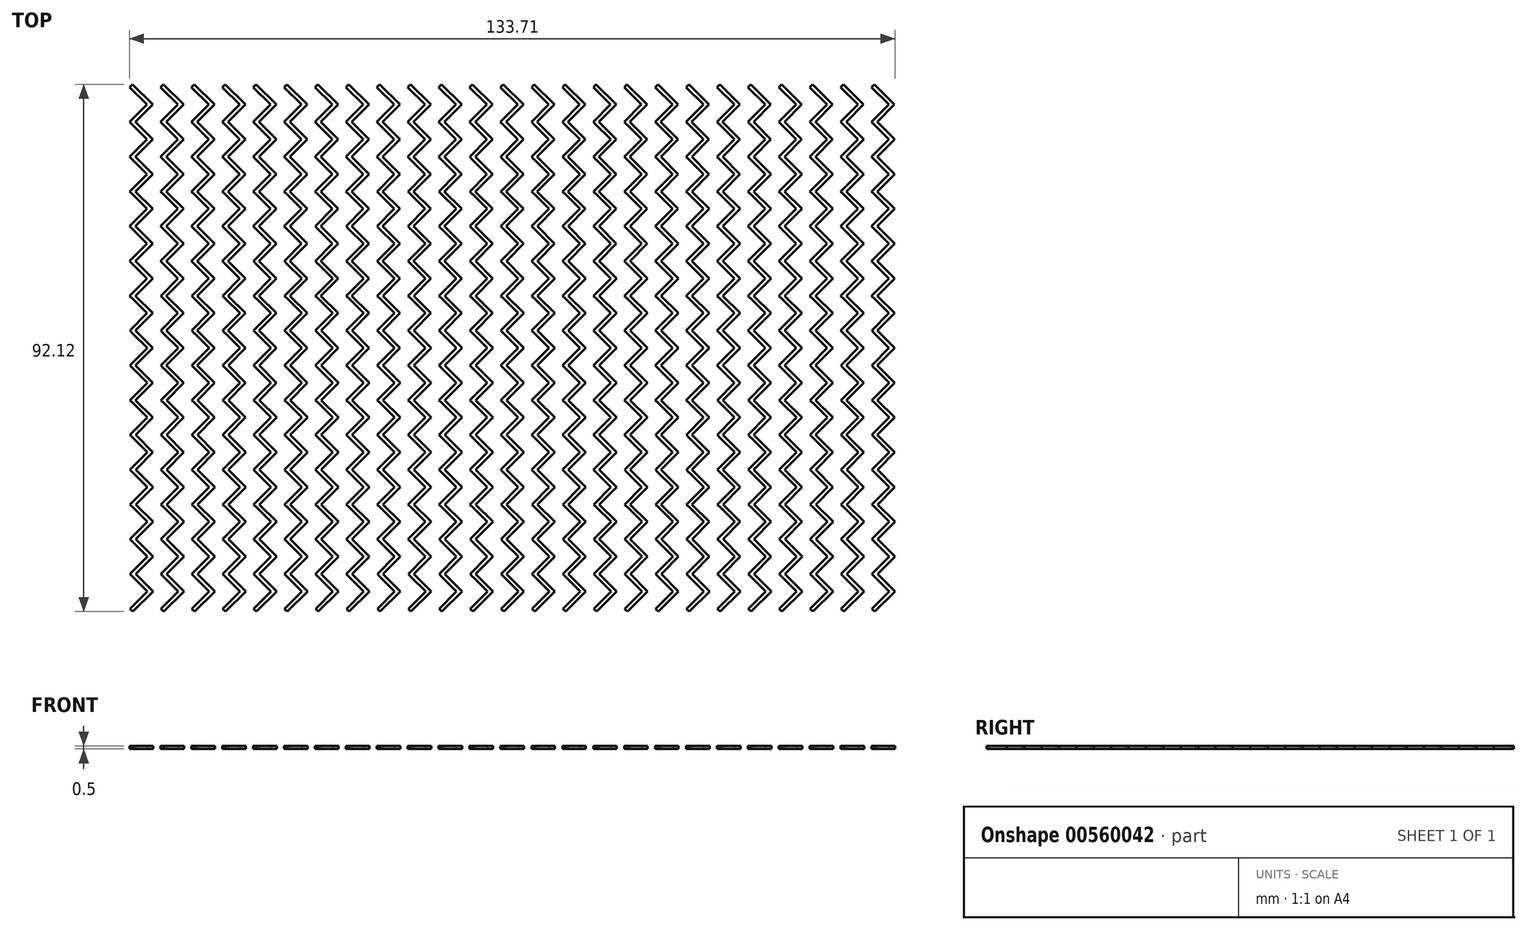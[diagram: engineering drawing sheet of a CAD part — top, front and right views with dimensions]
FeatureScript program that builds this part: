
annotation { "Feature Type Name" : "Feature", "Feature Type Description" : "" }
export const myFeature = defineFeature(function(context is Context, id is Id, definition is map)
    precondition{}
    {
        {
            var Q0;
            Q0=qCreatedBy(makeId("Top.planeOp"),FACE);
            var sketch = newSketch(context, id + "F0", { "sketchPlane" : qUnion([Q0])});
            skLineSegment(sketch, "E0.bottom", {"start": v(-69.05, 44.95) * mm, "end": v(-65.51, 41.41) * mm});
            skLineSegment(sketch, "E0.top", {"start": v(-69.54, 44.45) * mm, "end": v(-66, 40.91) * mm});
            skLineSegment(sketch, "E0.left", {"start": v(-69.05, 44.95) * mm, "end": v(-69.54, 44.45) * mm});
            skLineSegment(sketch, "E0.right", {"start": v(-65.51, 41.41) * mm, "end": v(-66, 40.91) * mm});
            skLineSegment(sketch, "E1.bottom", {"start": v(-65.51, 41.41) * mm, "end": v(-69.05, 37.87) * mm});
            skLineSegment(sketch, "E1.top", {"start": v(-66, 41.9) * mm, "end": v(-69.54, 38.37) * mm});
            skLineSegment(sketch, "E1.left", {"start": v(-65.51, 41.41) * mm, "end": v(-66, 41.9) * mm});
            skLineSegment(sketch, "E1.right", {"start": v(-69.05, 37.87) * mm, "end": v(-69.54, 38.37) * mm});
            skLineSegment(sketch, "E2.1.0.0", {"start": v(-69.54, 38.37) * mm, "end": v(-66, 34.84) * mm});
            skLineSegment(sketch, "E2.1.0.1", {"start": v(-65.5, 35.34) * mm, "end": v(-69.04, 31.8) * mm});
            skLineSegment(sketch, "E2.1.0.2", {"start": v(-66, 35.83) * mm, "end": v(-69.54, 32.3) * mm});
            skLineSegment(sketch, "E2.1.0.3", {"start": v(-69.04, 38.87) * mm, "end": v(-65.5, 35.34) * mm});
            skLineSegment(sketch, "E2.1.0.4", {"start": v(-69.04, 38.87) * mm, "end": v(-69.54, 38.37) * mm});
            skLineSegment(sketch, "E2.1.0.5", {"start": v(-65.5, 35.34) * mm, "end": v(-66, 34.84) * mm});
            skLineSegment(sketch, "E2.1.0.6", {"start": v(-65.5, 35.34) * mm, "end": v(-66, 35.83) * mm});
            skLineSegment(sketch, "E2.1.0.7", {"start": v(-69.04, 31.8) * mm, "end": v(-69.54, 32.3) * mm});
            skLineSegment(sketch, "E2.2.0.0", {"start": v(-69.53, 32.3) * mm, "end": v(-66, 28.76) * mm});
            skLineSegment(sketch, "E2.2.0.1", {"start": v(-65.5, 29.26) * mm, "end": v(-69.03, 25.73) * mm});
            skLineSegment(sketch, "E2.2.0.2", {"start": v(-66, 29.76) * mm, "end": v(-69.53, 26.22) * mm});
            skLineSegment(sketch, "E2.2.0.3", {"start": v(-69.03, 32.8) * mm, "end": v(-65.5, 29.26) * mm});
            skLineSegment(sketch, "E2.2.0.4", {"start": v(-69.03, 32.8) * mm, "end": v(-69.53, 32.3) * mm});
            skLineSegment(sketch, "E2.2.0.5", {"start": v(-65.5, 29.26) * mm, "end": v(-66, 28.76) * mm});
            skLineSegment(sketch, "E2.2.0.6", {"start": v(-65.5, 29.26) * mm, "end": v(-66, 29.76) * mm});
            skLineSegment(sketch, "E2.2.0.7", {"start": v(-69.03, 25.73) * mm, "end": v(-69.53, 26.22) * mm});
            skLineSegment(sketch, "E2.3.0.0", {"start": v(-69.53, 26.22) * mm, "end": v(-66, 22.69) * mm});
            skLineSegment(sketch, "E2.3.0.1", {"start": v(-65.5, 23.19) * mm, "end": v(-69.03, 19.65) * mm});
            skLineSegment(sketch, "E2.3.0.2", {"start": v(-66, 23.68) * mm, "end": v(-69.53, 20.15) * mm});
            skLineSegment(sketch, "E2.3.0.3", {"start": v(-69.03, 26.72) * mm, "end": v(-65.5, 23.19) * mm});
            skLineSegment(sketch, "E2.3.0.4", {"start": v(-69.03, 26.72) * mm, "end": v(-69.53, 26.22) * mm});
            skLineSegment(sketch, "E2.3.0.5", {"start": v(-65.5, 23.19) * mm, "end": v(-66, 22.69) * mm});
            skLineSegment(sketch, "E2.3.0.6", {"start": v(-65.5, 23.19) * mm, "end": v(-66, 23.68) * mm});
            skLineSegment(sketch, "E2.3.0.7", {"start": v(-69.03, 19.65) * mm, "end": v(-69.53, 20.15) * mm});
            skLineSegment(sketch, "E2.4.0.0", {"start": v(-69.52, 20.15) * mm, "end": v(-65.98, 16.61) * mm});
            skLineSegment(sketch, "E2.4.0.1", {"start": v(-65.49, 17.11) * mm, "end": v(-69.02, 13.58) * mm});
            skLineSegment(sketch, "E2.4.0.2", {"start": v(-65.98, 17.6) * mm, "end": v(-69.52, 14.07) * mm});
            skLineSegment(sketch, "E2.4.0.3", {"start": v(-69.02, 20.65) * mm, "end": v(-65.49, 17.11) * mm});
            skLineSegment(sketch, "E2.4.0.4", {"start": v(-69.02, 20.65) * mm, "end": v(-69.52, 20.15) * mm});
            skLineSegment(sketch, "E2.4.0.5", {"start": v(-65.49, 17.11) * mm, "end": v(-65.98, 16.61) * mm});
            skLineSegment(sketch, "E2.4.0.6", {"start": v(-65.49, 17.11) * mm, "end": v(-65.98, 17.6) * mm});
            skLineSegment(sketch, "E2.4.0.7", {"start": v(-69.02, 13.58) * mm, "end": v(-69.52, 14.07) * mm});
            skLineSegment(sketch, "E2.5.0.0", {"start": v(-69.51, 14.07) * mm, "end": v(-65.98, 10.54) * mm});
            skLineSegment(sketch, "E2.5.0.1", {"start": v(-65.48, 11.04) * mm, "end": v(-69.02, 7.5) * mm});
            skLineSegment(sketch, "E2.5.0.2", {"start": v(-65.98, 11.53) * mm, "end": v(-69.51, 8) * mm});
            skLineSegment(sketch, "E2.5.0.3", {"start": v(-69.02, 14.57) * mm, "end": v(-65.48, 11.04) * mm});
            skLineSegment(sketch, "E2.5.0.4", {"start": v(-69.02, 14.57) * mm, "end": v(-69.51, 14.07) * mm});
            skLineSegment(sketch, "E2.5.0.5", {"start": v(-65.48, 11.04) * mm, "end": v(-65.98, 10.54) * mm});
            skLineSegment(sketch, "E2.5.0.6", {"start": v(-65.48, 11.04) * mm, "end": v(-65.98, 11.53) * mm});
            skLineSegment(sketch, "E2.5.0.7", {"start": v(-69.02, 7.5) * mm, "end": v(-69.51, 8) * mm});
            skLineSegment(sketch, "E2.6.0.0", {"start": v(-69.5, 8) * mm, "end": v(-65.97, 4.46) * mm});
            skLineSegment(sketch, "E2.6.0.1", {"start": v(-65.48, 4.96) * mm, "end": v(-69.01, 1.43) * mm});
            skLineSegment(sketch, "E2.6.0.2", {"start": v(-65.97, 5.46) * mm, "end": v(-69.5, 1.92) * mm});
            skLineSegment(sketch, "E2.6.0.3", {"start": v(-69.01, 8.5) * mm, "end": v(-65.48, 4.96) * mm});
            skLineSegment(sketch, "E2.6.0.4", {"start": v(-69.01, 8.5) * mm, "end": v(-69.5, 8) * mm});
            skLineSegment(sketch, "E2.6.0.5", {"start": v(-65.48, 4.96) * mm, "end": v(-65.97, 4.46) * mm});
            skLineSegment(sketch, "E2.6.0.6", {"start": v(-65.48, 4.96) * mm, "end": v(-65.97, 5.46) * mm});
            skLineSegment(sketch, "E2.6.0.7", {"start": v(-69.01, 1.43) * mm, "end": v(-69.5, 1.92) * mm});
            skLineSegment(sketch, "E2.7.0.0", {"start": v(-69.5, 1.92) * mm, "end": v(-65.97, -1.61) * mm});
            skLineSegment(sketch, "E2.7.0.1", {"start": v(-65.47, -1.11) * mm, "end": v(-69, -4.65) * mm});
            skLineSegment(sketch, "E2.7.0.2", {"start": v(-65.97, -0.62) * mm, "end": v(-69.5, -4.15) * mm});
            skLineSegment(sketch, "E2.7.0.3", {"start": v(-69, 2.42) * mm, "end": v(-65.47, -1.11) * mm});
            skLineSegment(sketch, "E2.7.0.4", {"start": v(-69, 2.42) * mm, "end": v(-69.5, 1.92) * mm});
            skLineSegment(sketch, "E2.7.0.5", {"start": v(-65.47, -1.11) * mm, "end": v(-65.97, -1.61) * mm});
            skLineSegment(sketch, "E2.7.0.6", {"start": v(-65.47, -1.11) * mm, "end": v(-65.97, -0.62) * mm});
            skLineSegment(sketch, "E2.7.0.7", {"start": v(-69, -4.65) * mm, "end": v(-69.5, -4.15) * mm});
            skLineSegment(sketch, "E2.8.0.0", {"start": v(-69.5, -4.15) * mm, "end": v(-65.96, -7.69) * mm});
            skLineSegment(sketch, "E2.8.0.1", {"start": v(-65.46, -7.19) * mm, "end": v(-69, -10.72) * mm});
            skLineSegment(sketch, "E2.8.0.2", {"start": v(-65.96, -6.7) * mm, "end": v(-69.5, -10.23) * mm});
            skLineSegment(sketch, "E2.8.0.3", {"start": v(-69, -3.65) * mm, "end": v(-65.46, -7.19) * mm});
            skLineSegment(sketch, "E2.8.0.4", {"start": v(-69, -3.65) * mm, "end": v(-69.5, -4.15) * mm});
            skLineSegment(sketch, "E2.8.0.5", {"start": v(-65.46, -7.19) * mm, "end": v(-65.96, -7.69) * mm});
            skLineSegment(sketch, "E2.8.0.6", {"start": v(-65.46, -7.19) * mm, "end": v(-65.96, -6.7) * mm});
            skLineSegment(sketch, "E2.8.0.7", {"start": v(-69, -10.72) * mm, "end": v(-69.5, -10.23) * mm});
            skLineSegment(sketch, "E2.9.0.0", {"start": v(-69.5, -10.23) * mm, "end": v(-65.96, -13.76) * mm});
            skLineSegment(sketch, "E2.9.0.1", {"start": v(-65.46, -13.26) * mm, "end": v(-69, -16.8) * mm});
            skLineSegment(sketch, "E2.9.0.2", {"start": v(-65.96, -12.77) * mm, "end": v(-69.5, -16.3) * mm});
            skLineSegment(sketch, "E2.9.0.3", {"start": v(-69, -9.73) * mm, "end": v(-65.46, -13.26) * mm});
            skLineSegment(sketch, "E2.9.0.4", {"start": v(-69, -9.73) * mm, "end": v(-69.5, -10.23) * mm});
            skLineSegment(sketch, "E2.9.0.5", {"start": v(-65.46, -13.26) * mm, "end": v(-65.96, -13.76) * mm});
            skLineSegment(sketch, "E2.9.0.6", {"start": v(-65.46, -13.26) * mm, "end": v(-65.96, -12.77) * mm});
            skLineSegment(sketch, "E2.9.0.7", {"start": v(-69, -16.8) * mm, "end": v(-69.5, -16.3) * mm});
            skLineSegment(sketch, "E2.10.0.0", {"start": v(-69.49, -16.3) * mm, "end": v(-65.95, -19.84) * mm});
            skLineSegment(sketch, "E2.10.0.1", {"start": v(-65.45, -19.34) * mm, "end": v(-68.99, -22.87) * mm});
            skLineSegment(sketch, "E2.10.0.2", {"start": v(-65.95, -18.84) * mm, "end": v(-69.49, -22.38) * mm});
            skLineSegment(sketch, "E2.10.0.3", {"start": v(-68.99, -15.8) * mm, "end": v(-65.45, -19.34) * mm});
            skLineSegment(sketch, "E2.10.0.4", {"start": v(-68.99, -15.8) * mm, "end": v(-69.49, -16.3) * mm});
            skLineSegment(sketch, "E2.10.0.5", {"start": v(-65.45, -19.34) * mm, "end": v(-65.95, -19.84) * mm});
            skLineSegment(sketch, "E2.10.0.6", {"start": v(-65.45, -19.34) * mm, "end": v(-65.95, -18.84) * mm});
            skLineSegment(sketch, "E2.10.0.7", {"start": v(-68.99, -22.87) * mm, "end": v(-69.49, -22.38) * mm});
            skLineSegment(sketch, "E2.11.0.0", {"start": v(-69.48, -22.38) * mm, "end": v(-65.94, -25.91) * mm});
            skLineSegment(sketch, "E2.11.0.1", {"start": v(-65.45, -25.41) * mm, "end": v(-68.98, -28.95) * mm});
            skLineSegment(sketch, "E2.11.0.2", {"start": v(-65.94, -24.92) * mm, "end": v(-69.48, -28.45) * mm});
            skLineSegment(sketch, "E2.11.0.3", {"start": v(-68.98, -21.88) * mm, "end": v(-65.45, -25.41) * mm});
            skLineSegment(sketch, "E2.11.0.4", {"start": v(-68.98, -21.88) * mm, "end": v(-69.48, -22.38) * mm});
            skLineSegment(sketch, "E2.11.0.5", {"start": v(-65.45, -25.41) * mm, "end": v(-65.94, -25.91) * mm});
            skLineSegment(sketch, "E2.11.0.6", {"start": v(-65.45, -25.41) * mm, "end": v(-65.94, -24.92) * mm});
            skLineSegment(sketch, "E2.11.0.7", {"start": v(-68.98, -28.95) * mm, "end": v(-69.48, -28.45) * mm});
            skLineSegment(sketch, "E2.12.0.0", {"start": v(-69.47, -28.45) * mm, "end": v(-65.94, -31.99) * mm});
            skLineSegment(sketch, "E2.12.0.1", {"start": v(-65.44, -31.49) * mm, "end": v(-68.98, -35.02) * mm});
            skLineSegment(sketch, "E2.12.0.2", {"start": v(-65.94, -31) * mm, "end": v(-69.47, -34.53) * mm});
            skLineSegment(sketch, "E2.12.0.3", {"start": v(-68.98, -27.95) * mm, "end": v(-65.44, -31.49) * mm});
            skLineSegment(sketch, "E2.12.0.4", {"start": v(-68.98, -27.95) * mm, "end": v(-69.47, -28.45) * mm});
            skLineSegment(sketch, "E2.12.0.5", {"start": v(-65.44, -31.49) * mm, "end": v(-65.94, -31.99) * mm});
            skLineSegment(sketch, "E2.12.0.6", {"start": v(-65.44, -31.49) * mm, "end": v(-65.94, -31) * mm});
            skLineSegment(sketch, "E2.12.0.7", {"start": v(-68.98, -35.02) * mm, "end": v(-69.47, -34.53) * mm});
            skLineSegment(sketch, "E2.13.0.0", {"start": v(-69.47, -34.52) * mm, "end": v(-65.93, -38.06) * mm});
            skLineSegment(sketch, "E2.13.0.1", {"start": v(-65.43, -37.56) * mm, "end": v(-68.97, -41.1) * mm});
            skLineSegment(sketch, "E2.13.0.2", {"start": v(-65.93, -37.07) * mm, "end": v(-69.47, -40.6) * mm});
            skLineSegment(sketch, "E2.13.0.3", {"start": v(-68.97, -34.03) * mm, "end": v(-65.43, -37.56) * mm});
            skLineSegment(sketch, "E2.13.0.4", {"start": v(-68.97, -34.03) * mm, "end": v(-69.47, -34.52) * mm});
            skLineSegment(sketch, "E2.13.0.5", {"start": v(-65.43, -37.56) * mm, "end": v(-65.93, -38.06) * mm});
            skLineSegment(sketch, "E2.13.0.6", {"start": v(-65.43, -37.56) * mm, "end": v(-65.93, -37.07) * mm});
            skLineSegment(sketch, "E2.13.0.7", {"start": v(-68.97, -41.1) * mm, "end": v(-69.47, -40.6) * mm});
            skLineSegment(sketch, "E2.14.0.0", {"start": v(-69.46, -40.6) * mm, "end": v(-65.93, -44.14) * mm});
            skLineSegment(sketch, "E2.14.0.1", {"start": v(-65.43, -43.64) * mm, "end": v(-68.96, -47.17) * mm});
            skLineSegment(sketch, "E2.14.0.2", {"start": v(-65.93, -43.14) * mm, "end": v(-69.46, -46.68) * mm});
            skLineSegment(sketch, "E2.14.0.3", {"start": v(-68.96, -40.1) * mm, "end": v(-65.43, -43.64) * mm});
            skLineSegment(sketch, "E2.14.0.4", {"start": v(-68.96, -40.1) * mm, "end": v(-69.46, -40.6) * mm});
            skLineSegment(sketch, "E2.14.0.5", {"start": v(-65.43, -43.64) * mm, "end": v(-65.93, -44.14) * mm});
            skLineSegment(sketch, "E2.14.0.6", {"start": v(-65.43, -43.64) * mm, "end": v(-65.93, -43.14) * mm});
            skLineSegment(sketch, "E2.14.0.7", {"start": v(-68.96, -47.17) * mm, "end": v(-69.46, -46.68) * mm});
            skLineSegment(sketch, "E2.direction1", {"start": v(-69.05, 37.87) * mm, "end": v(-69.04, 31.8) * mm, "construction": true});
            skLineSegment(sketch, "E3.1.0.0", {"start": v(-63.65, 44.95) * mm, "end": v(-60.11, 41.41) * mm});
            skLineSegment(sketch, "E3.1.0.1", {"start": v(-64.14, 44.45) * mm, "end": v(-60.6, 40.91) * mm});
            skLineSegment(sketch, "E3.1.0.2", {"start": v(-63.65, 44.95) * mm, "end": v(-64.14, 44.45) * mm});
            skLineSegment(sketch, "E3.1.0.3", {"start": v(-60.03, -43.64) * mm, "end": v(-63.56, -47.17) * mm});
            skLineSegment(sketch, "E3.1.0.4", {"start": v(-60.53, -43.14) * mm, "end": v(-64.06, -46.68) * mm});
            skLineSegment(sketch, "E3.1.0.5", {"start": v(-63.56, -47.17) * mm, "end": v(-64.06, -46.68) * mm});
            skLineSegment(sketch, "E3.1.0.6", {"start": v(-63.61, 8.5) * mm, "end": v(-60.08, 4.96) * mm});
            skLineSegment(sketch, "E3.1.0.7", {"start": v(-60.03, -43.64) * mm, "end": v(-60.53, -43.14) * mm});
            skLineSegment(sketch, "E3.1.0.8", {"start": v(-60.08, 11.04) * mm, "end": v(-63.62, 7.5) * mm});
            skLineSegment(sketch, "E3.1.0.9", {"start": v(-60.03, -37.56) * mm, "end": v(-63.57, -41.1) * mm});
            skLineSegment(sketch, "E3.1.0.10", {"start": v(-60.05, -25.41) * mm, "end": v(-63.58, -28.95) * mm});
            skLineSegment(sketch, "E3.1.0.11", {"start": v(-60.58, 11.53) * mm, "end": v(-64.11, 8) * mm});
            skLineSegment(sketch, "E3.1.0.12", {"start": v(-60.6, 23.68) * mm, "end": v(-64.13, 20.15) * mm});
            skLineSegment(sketch, "E3.1.0.13", {"start": v(-63.6, 2.42) * mm, "end": v(-60.07, -1.11) * mm});
            skLineSegment(sketch, "E3.1.0.14", {"start": v(-63.62, 14.57) * mm, "end": v(-60.08, 11.04) * mm});
            skLineSegment(sketch, "E3.1.0.15", {"start": v(-63.63, 26.72) * mm, "end": v(-60.1, 23.19) * mm});
            skLineSegment(sketch, "E3.1.0.16", {"start": v(-63.57, -34.03) * mm, "end": v(-60.03, -37.56) * mm});
            skLineSegment(sketch, "E3.1.0.17", {"start": v(-63.58, -21.88) * mm, "end": v(-60.05, -25.41) * mm});
            skLineSegment(sketch, "E3.1.0.18", {"start": v(-63.6, -9.73) * mm, "end": v(-60.06, -13.26) * mm});
            skLineSegment(sketch, "E3.1.0.19", {"start": v(-60.06, -13.26) * mm, "end": v(-60.56, -13.76) * mm});
            skLineSegment(sketch, "E3.1.0.20", {"start": v(-60.07, -1.11) * mm, "end": v(-60.57, -1.61) * mm});
            skLineSegment(sketch, "E3.1.0.21", {"start": v(-60.08, 11.04) * mm, "end": v(-60.58, 10.54) * mm});
            skLineSegment(sketch, "E3.1.0.22", {"start": v(-60.1, 23.19) * mm, "end": v(-60.6, 22.69) * mm});
            skLineSegment(sketch, "E3.1.0.23", {"start": v(-60.03, -37.56) * mm, "end": v(-60.53, -38.06) * mm});
            skLineSegment(sketch, "E3.1.0.24", {"start": v(-60.05, -25.41) * mm, "end": v(-60.54, -25.91) * mm});
            skLineSegment(sketch, "E3.1.0.25", {"start": v(-60.06, -13.26) * mm, "end": v(-60.56, -12.77) * mm});
            skLineSegment(sketch, "E3.1.0.26", {"start": v(-60.07, -1.11) * mm, "end": v(-60.57, -0.62) * mm});
            skLineSegment(sketch, "E3.1.0.27", {"start": v(-60.08, 11.04) * mm, "end": v(-60.58, 11.53) * mm});
            skLineSegment(sketch, "E3.1.0.28", {"start": v(-60.1, 23.19) * mm, "end": v(-60.6, 23.68) * mm});
            skLineSegment(sketch, "E3.1.0.29", {"start": v(-60.03, -37.56) * mm, "end": v(-60.53, -37.07) * mm});
            skLineSegment(sketch, "E3.1.0.30", {"start": v(-60.05, -25.41) * mm, "end": v(-60.54, -24.92) * mm});
            skLineSegment(sketch, "E3.1.0.31", {"start": v(-63.62, 7.5) * mm, "end": v(-64.11, 8) * mm});
            skLineSegment(sketch, "E3.1.0.32", {"start": v(-60.11, 41.41) * mm, "end": v(-63.65, 37.87) * mm});
            skLineSegment(sketch, "E3.1.0.33", {"start": v(-60.6, 41.9) * mm, "end": v(-64.14, 38.37) * mm});
            skLineSegment(sketch, "E3.1.0.34", {"start": v(-60.11, 41.41) * mm, "end": v(-60.6, 41.9) * mm});
            skLineSegment(sketch, "E3.1.0.35", {"start": v(-64.14, 38.37) * mm, "end": v(-60.6, 34.84) * mm});
            skLineSegment(sketch, "E3.1.0.36", {"start": v(-63.64, 38.87) * mm, "end": v(-60.1, 35.34) * mm});
            skLineSegment(sketch, "E3.1.0.37", {"start": v(-64.06, -40.6) * mm, "end": v(-60.53, -44.14) * mm});
            skLineSegment(sketch, "E3.1.0.38", {"start": v(-64.1, 8) * mm, "end": v(-60.57, 4.46) * mm});
            skLineSegment(sketch, "E3.1.0.39", {"start": v(-60.05, -19.34) * mm, "end": v(-63.59, -22.87) * mm});
            skLineSegment(sketch, "E3.1.0.40", {"start": v(-60.06, -7.19) * mm, "end": v(-63.6, -10.72) * mm});
            skLineSegment(sketch, "E3.1.0.41", {"start": v(-60.08, 4.96) * mm, "end": v(-63.61, 1.43) * mm});
            skLineSegment(sketch, "E3.1.0.42", {"start": v(-60.04, -31.49) * mm, "end": v(-63.58, -35.02) * mm});
            skLineSegment(sketch, "E3.1.0.43", {"start": v(-60.55, -18.84) * mm, "end": v(-64.09, -22.38) * mm});
            skLineSegment(sketch, "E3.1.0.44", {"start": v(-60.56, -6.7) * mm, "end": v(-64.1, -10.23) * mm});
            skLineSegment(sketch, "E3.1.0.45", {"start": v(-60.57, 5.46) * mm, "end": v(-64.1, 1.92) * mm});
            skLineSegment(sketch, "E3.1.0.46", {"start": v(-60.54, -31) * mm, "end": v(-64.07, -34.53) * mm});
            skLineSegment(sketch, "E3.1.0.47", {"start": v(-63.59, -15.8) * mm, "end": v(-60.05, -19.34) * mm});
            skLineSegment(sketch, "E3.1.0.48", {"start": v(-63.6, -3.65) * mm, "end": v(-60.06, -7.19) * mm});
            skLineSegment(sketch, "E3.1.0.49", {"start": v(-63.63, 32.8) * mm, "end": v(-60.1, 29.26) * mm});
            skLineSegment(sketch, "E3.1.0.50", {"start": v(-63.56, -40.1) * mm, "end": v(-60.03, -43.64) * mm});
            skLineSegment(sketch, "E3.1.0.51", {"start": v(-63.58, -27.95) * mm, "end": v(-60.04, -31.49) * mm});
            skLineSegment(sketch, "E3.1.0.52", {"start": v(-63.62, 20.65) * mm, "end": v(-60.09, 17.11) * mm});
            skLineSegment(sketch, "E3.1.0.53", {"start": v(-63.59, -15.8) * mm, "end": v(-64.09, -16.3) * mm});
            skLineSegment(sketch, "E3.1.0.54", {"start": v(-63.6, -3.65) * mm, "end": v(-64.1, -4.15) * mm});
            skLineSegment(sketch, "E3.1.0.55", {"start": v(-63.61, 8.5) * mm, "end": v(-64.1, 8) * mm});
            skLineSegment(sketch, "E3.1.0.56", {"start": v(-63.56, -40.1) * mm, "end": v(-64.06, -40.6) * mm});
            skLineSegment(sketch, "E3.1.0.57", {"start": v(-63.58, -27.95) * mm, "end": v(-64.07, -28.45) * mm});
            skLineSegment(sketch, "E3.1.0.58", {"start": v(-60.03, -43.64) * mm, "end": v(-60.53, -44.14) * mm});
            skLineSegment(sketch, "E3.1.0.59", {"start": v(-60.05, -19.34) * mm, "end": v(-60.55, -18.84) * mm});
            skLineSegment(sketch, "E3.1.0.60", {"start": v(-60.06, -7.19) * mm, "end": v(-60.56, -6.7) * mm});
            skLineSegment(sketch, "E3.1.0.61", {"start": v(-60.08, 4.96) * mm, "end": v(-60.57, 5.46) * mm});
            skLineSegment(sketch, "E3.1.0.62", {"start": v(-60.04, -31.49) * mm, "end": v(-60.54, -31) * mm});
            skLineSegment(sketch, "E3.1.0.63", {"start": v(-63.61, 1.43) * mm, "end": v(-64.1, 1.92) * mm});
            skLineSegment(sketch, "E3.1.0.64", {"start": v(-63.58, -35.02) * mm, "end": v(-64.07, -34.53) * mm});
            skLineSegment(sketch, "E3.1.0.65", {"start": v(-63.59, -22.87) * mm, "end": v(-64.09, -22.38) * mm});
            skLineSegment(sketch, "E3.1.0.66", {"start": v(-63.6, -10.72) * mm, "end": v(-64.1, -10.23) * mm});
            skLineSegment(sketch, "E3.1.0.67", {"start": v(-64.1, 1.92) * mm, "end": v(-60.57, -1.61) * mm});
            skLineSegment(sketch, "E3.1.0.68", {"start": v(-64.11, 14.07) * mm, "end": v(-60.58, 10.54) * mm});
            skLineSegment(sketch, "E3.1.0.69", {"start": v(-64.13, 26.22) * mm, "end": v(-60.6, 22.69) * mm});
            skLineSegment(sketch, "E3.1.0.70", {"start": v(-63.65, 37.87) * mm, "end": v(-63.64, 31.8) * mm, "construction": true});
            skLineSegment(sketch, "E3.1.0.71", {"start": v(-64.07, -34.52) * mm, "end": v(-60.53, -38.06) * mm});
            skLineSegment(sketch, "E3.1.0.72", {"start": v(-64.08, -22.38) * mm, "end": v(-60.54, -25.91) * mm});
            skLineSegment(sketch, "E3.1.0.73", {"start": v(-64.1, -10.23) * mm, "end": v(-60.56, -13.76) * mm});
            skLineSegment(sketch, "E3.1.0.74", {"start": v(-60.07, -1.11) * mm, "end": v(-63.6, -4.65) * mm});
            skLineSegment(sketch, "E3.1.0.75", {"start": v(-60.1, 23.19) * mm, "end": v(-63.63, 19.65) * mm});
            skLineSegment(sketch, "E3.1.0.76", {"start": v(-60.06, -13.26) * mm, "end": v(-63.6, -16.8) * mm});
            skLineSegment(sketch, "E3.1.0.77", {"start": v(-60.57, -0.62) * mm, "end": v(-64.1, -4.15) * mm});
            skLineSegment(sketch, "E3.1.0.78", {"start": v(-60.53, -37.07) * mm, "end": v(-64.07, -40.6) * mm});
            skLineSegment(sketch, "E3.1.0.79", {"start": v(-60.54, -24.92) * mm, "end": v(-64.08, -28.45) * mm});
            skLineSegment(sketch, "E3.1.0.80", {"start": v(-60.56, -12.77) * mm, "end": v(-64.1, -16.3) * mm});
            skLineSegment(sketch, "E3.1.0.81", {"start": v(-63.6, 2.42) * mm, "end": v(-64.1, 1.92) * mm});
            skLineSegment(sketch, "E3.1.0.82", {"start": v(-63.62, 14.57) * mm, "end": v(-64.11, 14.07) * mm});
            skLineSegment(sketch, "E3.1.0.83", {"start": v(-63.63, 26.72) * mm, "end": v(-64.13, 26.22) * mm});
            skLineSegment(sketch, "E3.1.0.84", {"start": v(-63.57, -34.03) * mm, "end": v(-64.07, -34.52) * mm});
            skLineSegment(sketch, "E3.1.0.85", {"start": v(-63.58, -21.88) * mm, "end": v(-64.08, -22.38) * mm});
            skLineSegment(sketch, "E3.1.0.86", {"start": v(-63.6, -9.73) * mm, "end": v(-64.1, -10.23) * mm});
            skLineSegment(sketch, "E3.1.0.87", {"start": v(-63.63, 19.65) * mm, "end": v(-64.13, 20.15) * mm});
            skLineSegment(sketch, "E3.1.0.88", {"start": v(-63.57, -41.1) * mm, "end": v(-64.07, -40.6) * mm});
            skLineSegment(sketch, "E3.1.0.89", {"start": v(-60.1, 35.34) * mm, "end": v(-60.6, 34.84) * mm});
            skLineSegment(sketch, "E3.1.0.90", {"start": v(-60.11, 41.41) * mm, "end": v(-60.6, 40.91) * mm});
            skLineSegment(sketch, "E3.1.0.91", {"start": v(-60.1, 35.34) * mm, "end": v(-63.64, 31.8) * mm});
            skLineSegment(sketch, "E3.1.0.92", {"start": v(-60.6, 35.83) * mm, "end": v(-64.14, 32.3) * mm});
            skLineSegment(sketch, "E3.1.0.93", {"start": v(-63.64, 38.87) * mm, "end": v(-64.14, 38.37) * mm});
            skLineSegment(sketch, "E3.1.0.94", {"start": v(-64.07, -28.45) * mm, "end": v(-60.54, -31.99) * mm});
            skLineSegment(sketch, "E3.1.0.95", {"start": v(-64.13, 32.3) * mm, "end": v(-60.6, 28.76) * mm});
            skLineSegment(sketch, "E3.1.0.96", {"start": v(-64.09, -16.3) * mm, "end": v(-60.55, -19.84) * mm});
            skLineSegment(sketch, "E3.1.0.97", {"start": v(-64.1, -4.15) * mm, "end": v(-60.56, -7.69) * mm});
            skLineSegment(sketch, "E3.1.0.98", {"start": v(-64.12, 20.15) * mm, "end": v(-60.58, 16.61) * mm});
            skLineSegment(sketch, "E3.1.0.99", {"start": v(-60.1, 29.26) * mm, "end": v(-63.63, 25.73) * mm});
            skLineSegment(sketch, "E3.1.0.100", {"start": v(-60.09, 17.11) * mm, "end": v(-63.62, 13.58) * mm});
            skLineSegment(sketch, "E3.1.0.101", {"start": v(-60.6, 29.76) * mm, "end": v(-64.13, 26.22) * mm});
            skLineSegment(sketch, "E3.1.0.102", {"start": v(-60.58, 17.6) * mm, "end": v(-64.12, 14.07) * mm});
            skLineSegment(sketch, "E3.1.0.103", {"start": v(-63.62, 20.65) * mm, "end": v(-64.12, 20.15) * mm});
            skLineSegment(sketch, "E3.1.0.104", {"start": v(-60.05, -19.34) * mm, "end": v(-60.55, -19.84) * mm});
            skLineSegment(sketch, "E3.1.0.105", {"start": v(-60.06, -7.19) * mm, "end": v(-60.56, -7.69) * mm});
            skLineSegment(sketch, "E3.1.0.106", {"start": v(-60.08, 4.96) * mm, "end": v(-60.57, 4.46) * mm});
            skLineSegment(sketch, "E3.1.0.107", {"start": v(-60.04, -31.49) * mm, "end": v(-60.54, -31.99) * mm});
            skLineSegment(sketch, "E3.1.0.108", {"start": v(-60.1, 29.26) * mm, "end": v(-60.6, 29.76) * mm});
            skLineSegment(sketch, "E3.1.0.109", {"start": v(-60.09, 17.11) * mm, "end": v(-60.58, 17.6) * mm});
            skLineSegment(sketch, "E3.1.0.110", {"start": v(-63.62, 13.58) * mm, "end": v(-64.12, 14.07) * mm});
            skLineSegment(sketch, "E3.1.0.111", {"start": v(-63.63, 25.73) * mm, "end": v(-64.13, 26.22) * mm});
            skLineSegment(sketch, "E3.1.0.112", {"start": v(-63.6, -16.8) * mm, "end": v(-64.1, -16.3) * mm});
            skLineSegment(sketch, "E3.1.0.113", {"start": v(-63.6, -4.65) * mm, "end": v(-64.1, -4.15) * mm});
            skLineSegment(sketch, "E3.1.0.114", {"start": v(-63.58, -28.95) * mm, "end": v(-64.08, -28.45) * mm});
            skLineSegment(sketch, "E3.1.0.115", {"start": v(-60.1, 35.34) * mm, "end": v(-60.6, 35.83) * mm});
            skLineSegment(sketch, "E3.1.0.116", {"start": v(-63.64, 31.8) * mm, "end": v(-64.14, 32.3) * mm});
            skLineSegment(sketch, "E3.1.0.117", {"start": v(-63.65, 37.87) * mm, "end": v(-64.14, 38.37) * mm});
            skLineSegment(sketch, "E3.1.0.118", {"start": v(-63.63, 32.8) * mm, "end": v(-64.13, 32.3) * mm});
            skLineSegment(sketch, "E3.1.0.119", {"start": v(-60.1, 29.26) * mm, "end": v(-60.6, 28.76) * mm});
            skLineSegment(sketch, "E3.1.0.120", {"start": v(-60.09, 17.11) * mm, "end": v(-60.58, 16.61) * mm});
            skLineSegment(sketch, "E3.2.0.0", {"start": v(-58.25, 44.95) * mm, "end": v(-54.71, 41.41) * mm});
            skLineSegment(sketch, "E3.2.0.1", {"start": v(-58.74, 44.45) * mm, "end": v(-55.2, 40.91) * mm});
            skLineSegment(sketch, "E3.2.0.2", {"start": v(-58.25, 44.95) * mm, "end": v(-58.74, 44.45) * mm});
            skLineSegment(sketch, "E3.2.0.3", {"start": v(-54.63, -43.64) * mm, "end": v(-58.16, -47.17) * mm});
            skLineSegment(sketch, "E3.2.0.4", {"start": v(-55.13, -43.14) * mm, "end": v(-58.66, -46.68) * mm});
            skLineSegment(sketch, "E3.2.0.5", {"start": v(-58.16, -47.17) * mm, "end": v(-58.66, -46.68) * mm});
            skLineSegment(sketch, "E3.2.0.6", {"start": v(-58.21, 8.5) * mm, "end": v(-54.68, 4.96) * mm});
            skLineSegment(sketch, "E3.2.0.7", {"start": v(-54.63, -43.64) * mm, "end": v(-55.13, -43.14) * mm});
            skLineSegment(sketch, "E3.2.0.8", {"start": v(-54.68, 11.04) * mm, "end": v(-58.22, 7.5) * mm});
            skLineSegment(sketch, "E3.2.0.9", {"start": v(-54.63, -37.56) * mm, "end": v(-58.17, -41.1) * mm});
            skLineSegment(sketch, "E3.2.0.10", {"start": v(-54.65, -25.41) * mm, "end": v(-58.18, -28.95) * mm});
            skLineSegment(sketch, "E3.2.0.11", {"start": v(-55.18, 11.53) * mm, "end": v(-58.71, 8) * mm});
            skLineSegment(sketch, "E3.2.0.12", {"start": v(-55.2, 23.68) * mm, "end": v(-58.73, 20.15) * mm});
            skLineSegment(sketch, "E3.2.0.13", {"start": v(-58.2, 2.42) * mm, "end": v(-54.67, -1.11) * mm});
            skLineSegment(sketch, "E3.2.0.14", {"start": v(-58.22, 14.57) * mm, "end": v(-54.68, 11.04) * mm});
            skLineSegment(sketch, "E3.2.0.15", {"start": v(-58.23, 26.72) * mm, "end": v(-54.7, 23.19) * mm});
            skLineSegment(sketch, "E3.2.0.16", {"start": v(-58.17, -34.03) * mm, "end": v(-54.63, -37.56) * mm});
            skLineSegment(sketch, "E3.2.0.17", {"start": v(-58.18, -21.88) * mm, "end": v(-54.65, -25.41) * mm});
            skLineSegment(sketch, "E3.2.0.18", {"start": v(-58.2, -9.73) * mm, "end": v(-54.66, -13.26) * mm});
            skLineSegment(sketch, "E3.2.0.19", {"start": v(-54.66, -13.26) * mm, "end": v(-55.16, -13.76) * mm});
            skLineSegment(sketch, "E3.2.0.20", {"start": v(-54.67, -1.11) * mm, "end": v(-55.17, -1.61) * mm});
            skLineSegment(sketch, "E3.2.0.21", {"start": v(-54.68, 11.04) * mm, "end": v(-55.18, 10.54) * mm});
            skLineSegment(sketch, "E3.2.0.22", {"start": v(-54.7, 23.19) * mm, "end": v(-55.2, 22.69) * mm});
            skLineSegment(sketch, "E3.2.0.23", {"start": v(-54.63, -37.56) * mm, "end": v(-55.13, -38.06) * mm});
            skLineSegment(sketch, "E3.2.0.24", {"start": v(-54.65, -25.41) * mm, "end": v(-55.14, -25.91) * mm});
            skLineSegment(sketch, "E3.2.0.25", {"start": v(-54.66, -13.26) * mm, "end": v(-55.16, -12.77) * mm});
            skLineSegment(sketch, "E3.2.0.26", {"start": v(-54.67, -1.11) * mm, "end": v(-55.17, -0.62) * mm});
            skLineSegment(sketch, "E3.2.0.27", {"start": v(-54.68, 11.04) * mm, "end": v(-55.18, 11.53) * mm});
            skLineSegment(sketch, "E3.2.0.28", {"start": v(-54.7, 23.19) * mm, "end": v(-55.2, 23.68) * mm});
            skLineSegment(sketch, "E3.2.0.29", {"start": v(-54.63, -37.56) * mm, "end": v(-55.13, -37.07) * mm});
            skLineSegment(sketch, "E3.2.0.30", {"start": v(-54.65, -25.41) * mm, "end": v(-55.14, -24.92) * mm});
            skLineSegment(sketch, "E3.2.0.31", {"start": v(-58.22, 7.5) * mm, "end": v(-58.71, 8) * mm});
            skLineSegment(sketch, "E3.2.0.32", {"start": v(-54.71, 41.41) * mm, "end": v(-58.25, 37.87) * mm});
            skLineSegment(sketch, "E3.2.0.33", {"start": v(-55.2, 41.9) * mm, "end": v(-58.74, 38.37) * mm});
            skLineSegment(sketch, "E3.2.0.34", {"start": v(-54.71, 41.41) * mm, "end": v(-55.2, 41.9) * mm});
            skLineSegment(sketch, "E3.2.0.35", {"start": v(-58.74, 38.37) * mm, "end": v(-55.2, 34.84) * mm});
            skLineSegment(sketch, "E3.2.0.36", {"start": v(-58.24, 38.87) * mm, "end": v(-54.7, 35.34) * mm});
            skLineSegment(sketch, "E3.2.0.37", {"start": v(-58.66, -40.6) * mm, "end": v(-55.13, -44.14) * mm});
            skLineSegment(sketch, "E3.2.0.38", {"start": v(-58.7, 8) * mm, "end": v(-55.17, 4.46) * mm});
            skLineSegment(sketch, "E3.2.0.39", {"start": v(-54.65, -19.34) * mm, "end": v(-58.19, -22.87) * mm});
            skLineSegment(sketch, "E3.2.0.40", {"start": v(-54.66, -7.19) * mm, "end": v(-58.2, -10.72) * mm});
            skLineSegment(sketch, "E3.2.0.41", {"start": v(-54.68, 4.96) * mm, "end": v(-58.21, 1.43) * mm});
            skLineSegment(sketch, "E3.2.0.42", {"start": v(-54.64, -31.49) * mm, "end": v(-58.18, -35.02) * mm});
            skLineSegment(sketch, "E3.2.0.43", {"start": v(-55.15, -18.84) * mm, "end": v(-58.69, -22.38) * mm});
            skLineSegment(sketch, "E3.2.0.44", {"start": v(-55.16, -6.7) * mm, "end": v(-58.7, -10.23) * mm});
            skLineSegment(sketch, "E3.2.0.45", {"start": v(-55.17, 5.46) * mm, "end": v(-58.7, 1.92) * mm});
            skLineSegment(sketch, "E3.2.0.46", {"start": v(-55.14, -31) * mm, "end": v(-58.67, -34.53) * mm});
            skLineSegment(sketch, "E3.2.0.47", {"start": v(-58.19, -15.8) * mm, "end": v(-54.65, -19.34) * mm});
            skLineSegment(sketch, "E3.2.0.48", {"start": v(-58.2, -3.65) * mm, "end": v(-54.66, -7.19) * mm});
            skLineSegment(sketch, "E3.2.0.49", {"start": v(-58.23, 32.8) * mm, "end": v(-54.7, 29.26) * mm});
            skLineSegment(sketch, "E3.2.0.50", {"start": v(-58.16, -40.1) * mm, "end": v(-54.63, -43.64) * mm});
            skLineSegment(sketch, "E3.2.0.51", {"start": v(-58.18, -27.95) * mm, "end": v(-54.64, -31.49) * mm});
            skLineSegment(sketch, "E3.2.0.52", {"start": v(-58.22, 20.65) * mm, "end": v(-54.69, 17.11) * mm});
            skLineSegment(sketch, "E3.2.0.53", {"start": v(-58.19, -15.8) * mm, "end": v(-58.69, -16.3) * mm});
            skLineSegment(sketch, "E3.2.0.54", {"start": v(-58.2, -3.65) * mm, "end": v(-58.7, -4.15) * mm});
            skLineSegment(sketch, "E3.2.0.55", {"start": v(-58.21, 8.5) * mm, "end": v(-58.7, 8) * mm});
            skLineSegment(sketch, "E3.2.0.56", {"start": v(-58.16, -40.1) * mm, "end": v(-58.66, -40.6) * mm});
            skLineSegment(sketch, "E3.2.0.57", {"start": v(-58.18, -27.95) * mm, "end": v(-58.67, -28.45) * mm});
            skLineSegment(sketch, "E3.2.0.58", {"start": v(-54.63, -43.64) * mm, "end": v(-55.13, -44.14) * mm});
            skLineSegment(sketch, "E3.2.0.59", {"start": v(-54.65, -19.34) * mm, "end": v(-55.15, -18.84) * mm});
            skLineSegment(sketch, "E3.2.0.60", {"start": v(-54.66, -7.19) * mm, "end": v(-55.16, -6.7) * mm});
            skLineSegment(sketch, "E3.2.0.61", {"start": v(-54.68, 4.96) * mm, "end": v(-55.17, 5.46) * mm});
            skLineSegment(sketch, "E3.2.0.62", {"start": v(-54.64, -31.49) * mm, "end": v(-55.14, -31) * mm});
            skLineSegment(sketch, "E3.2.0.63", {"start": v(-58.21, 1.43) * mm, "end": v(-58.7, 1.92) * mm});
            skLineSegment(sketch, "E3.2.0.64", {"start": v(-58.18, -35.02) * mm, "end": v(-58.67, -34.53) * mm});
            skLineSegment(sketch, "E3.2.0.65", {"start": v(-58.19, -22.87) * mm, "end": v(-58.69, -22.38) * mm});
            skLineSegment(sketch, "E3.2.0.66", {"start": v(-58.2, -10.72) * mm, "end": v(-58.7, -10.23) * mm});
            skLineSegment(sketch, "E3.2.0.67", {"start": v(-58.7, 1.92) * mm, "end": v(-55.17, -1.61) * mm});
            skLineSegment(sketch, "E3.2.0.68", {"start": v(-58.71, 14.07) * mm, "end": v(-55.18, 10.54) * mm});
            skLineSegment(sketch, "E3.2.0.69", {"start": v(-58.73, 26.22) * mm, "end": v(-55.2, 22.69) * mm});
            skLineSegment(sketch, "E3.2.0.70", {"start": v(-58.25, 37.87) * mm, "end": v(-58.24, 31.8) * mm, "construction": true});
            skLineSegment(sketch, "E3.2.0.71", {"start": v(-58.67, -34.52) * mm, "end": v(-55.13, -38.06) * mm});
            skLineSegment(sketch, "E3.2.0.72", {"start": v(-58.68, -22.38) * mm, "end": v(-55.14, -25.91) * mm});
            skLineSegment(sketch, "E3.2.0.73", {"start": v(-58.7, -10.23) * mm, "end": v(-55.16, -13.76) * mm});
            skLineSegment(sketch, "E3.2.0.74", {"start": v(-54.67, -1.11) * mm, "end": v(-58.2, -4.65) * mm});
            skLineSegment(sketch, "E3.2.0.75", {"start": v(-54.7, 23.19) * mm, "end": v(-58.23, 19.65) * mm});
            skLineSegment(sketch, "E3.2.0.76", {"start": v(-54.66, -13.26) * mm, "end": v(-58.2, -16.8) * mm});
            skLineSegment(sketch, "E3.2.0.77", {"start": v(-55.17, -0.62) * mm, "end": v(-58.7, -4.15) * mm});
            skLineSegment(sketch, "E3.2.0.78", {"start": v(-55.13, -37.07) * mm, "end": v(-58.67, -40.6) * mm});
            skLineSegment(sketch, "E3.2.0.79", {"start": v(-55.14, -24.92) * mm, "end": v(-58.68, -28.45) * mm});
            skLineSegment(sketch, "E3.2.0.80", {"start": v(-55.16, -12.77) * mm, "end": v(-58.7, -16.3) * mm});
            skLineSegment(sketch, "E3.2.0.81", {"start": v(-58.2, 2.42) * mm, "end": v(-58.7, 1.92) * mm});
            skLineSegment(sketch, "E3.2.0.82", {"start": v(-58.22, 14.57) * mm, "end": v(-58.71, 14.07) * mm});
            skLineSegment(sketch, "E3.2.0.83", {"start": v(-58.23, 26.72) * mm, "end": v(-58.73, 26.22) * mm});
            skLineSegment(sketch, "E3.2.0.84", {"start": v(-58.17, -34.03) * mm, "end": v(-58.67, -34.52) * mm});
            skLineSegment(sketch, "E3.2.0.85", {"start": v(-58.18, -21.88) * mm, "end": v(-58.68, -22.38) * mm});
            skLineSegment(sketch, "E3.2.0.86", {"start": v(-58.2, -9.73) * mm, "end": v(-58.7, -10.23) * mm});
            skLineSegment(sketch, "E3.2.0.87", {"start": v(-58.23, 19.65) * mm, "end": v(-58.73, 20.15) * mm});
            skLineSegment(sketch, "E3.2.0.88", {"start": v(-58.17, -41.1) * mm, "end": v(-58.67, -40.6) * mm});
            skLineSegment(sketch, "E3.2.0.89", {"start": v(-54.7, 35.34) * mm, "end": v(-55.2, 34.84) * mm});
            skLineSegment(sketch, "E3.2.0.90", {"start": v(-54.71, 41.41) * mm, "end": v(-55.2, 40.91) * mm});
            skLineSegment(sketch, "E3.2.0.91", {"start": v(-54.7, 35.34) * mm, "end": v(-58.24, 31.8) * mm});
            skLineSegment(sketch, "E3.2.0.92", {"start": v(-55.2, 35.83) * mm, "end": v(-58.74, 32.3) * mm});
            skLineSegment(sketch, "E3.2.0.93", {"start": v(-58.24, 38.87) * mm, "end": v(-58.74, 38.37) * mm});
            skLineSegment(sketch, "E3.2.0.94", {"start": v(-58.67, -28.45) * mm, "end": v(-55.14, -31.99) * mm});
            skLineSegment(sketch, "E3.2.0.95", {"start": v(-58.73, 32.3) * mm, "end": v(-55.2, 28.76) * mm});
            skLineSegment(sketch, "E3.2.0.96", {"start": v(-58.69, -16.3) * mm, "end": v(-55.15, -19.84) * mm});
            skLineSegment(sketch, "E3.2.0.97", {"start": v(-58.7, -4.15) * mm, "end": v(-55.16, -7.69) * mm});
            skLineSegment(sketch, "E3.2.0.98", {"start": v(-58.72, 20.15) * mm, "end": v(-55.18, 16.61) * mm});
            skLineSegment(sketch, "E3.2.0.99", {"start": v(-54.7, 29.26) * mm, "end": v(-58.23, 25.73) * mm});
            skLineSegment(sketch, "E3.2.0.100", {"start": v(-54.69, 17.11) * mm, "end": v(-58.22, 13.58) * mm});
            skLineSegment(sketch, "E3.2.0.101", {"start": v(-55.2, 29.76) * mm, "end": v(-58.73, 26.22) * mm});
            skLineSegment(sketch, "E3.2.0.102", {"start": v(-55.18, 17.6) * mm, "end": v(-58.72, 14.07) * mm});
            skLineSegment(sketch, "E3.2.0.103", {"start": v(-58.22, 20.65) * mm, "end": v(-58.72, 20.15) * mm});
            skLineSegment(sketch, "E3.2.0.104", {"start": v(-54.65, -19.34) * mm, "end": v(-55.15, -19.84) * mm});
            skLineSegment(sketch, "E3.2.0.105", {"start": v(-54.66, -7.19) * mm, "end": v(-55.16, -7.69) * mm});
            skLineSegment(sketch, "E3.2.0.106", {"start": v(-54.68, 4.96) * mm, "end": v(-55.17, 4.46) * mm});
            skLineSegment(sketch, "E3.2.0.107", {"start": v(-54.64, -31.49) * mm, "end": v(-55.14, -31.99) * mm});
            skLineSegment(sketch, "E3.2.0.108", {"start": v(-54.7, 29.26) * mm, "end": v(-55.2, 29.76) * mm});
            skLineSegment(sketch, "E3.2.0.109", {"start": v(-54.69, 17.11) * mm, "end": v(-55.18, 17.6) * mm});
            skLineSegment(sketch, "E3.2.0.110", {"start": v(-58.22, 13.58) * mm, "end": v(-58.72, 14.07) * mm});
            skLineSegment(sketch, "E3.2.0.111", {"start": v(-58.23, 25.73) * mm, "end": v(-58.73, 26.22) * mm});
            skLineSegment(sketch, "E3.2.0.112", {"start": v(-58.2, -16.8) * mm, "end": v(-58.7, -16.3) * mm});
            skLineSegment(sketch, "E3.2.0.113", {"start": v(-58.2, -4.65) * mm, "end": v(-58.7, -4.15) * mm});
            skLineSegment(sketch, "E3.2.0.114", {"start": v(-58.18, -28.95) * mm, "end": v(-58.68, -28.45) * mm});
            skLineSegment(sketch, "E3.2.0.115", {"start": v(-54.7, 35.34) * mm, "end": v(-55.2, 35.83) * mm});
            skLineSegment(sketch, "E3.2.0.116", {"start": v(-58.24, 31.8) * mm, "end": v(-58.74, 32.3) * mm});
            skLineSegment(sketch, "E3.2.0.117", {"start": v(-58.25, 37.87) * mm, "end": v(-58.74, 38.37) * mm});
            skLineSegment(sketch, "E3.2.0.118", {"start": v(-58.23, 32.8) * mm, "end": v(-58.73, 32.3) * mm});
            skLineSegment(sketch, "E3.2.0.119", {"start": v(-54.7, 29.26) * mm, "end": v(-55.2, 28.76) * mm});
            skLineSegment(sketch, "E3.2.0.120", {"start": v(-54.69, 17.11) * mm, "end": v(-55.18, 16.61) * mm});
            skLineSegment(sketch, "E3.3.0.0", {"start": v(-52.85, 44.95) * mm, "end": v(-49.31, 41.41) * mm});
            skLineSegment(sketch, "E3.3.0.1", {"start": v(-53.34, 44.45) * mm, "end": v(-49.8, 40.91) * mm});
            skLineSegment(sketch, "E3.3.0.2", {"start": v(-52.85, 44.95) * mm, "end": v(-53.34, 44.45) * mm});
            skLineSegment(sketch, "E3.3.0.3", {"start": v(-49.23, -43.64) * mm, "end": v(-52.76, -47.17) * mm});
            skLineSegment(sketch, "E3.3.0.4", {"start": v(-49.73, -43.14) * mm, "end": v(-53.26, -46.68) * mm});
            skLineSegment(sketch, "E3.3.0.5", {"start": v(-52.76, -47.17) * mm, "end": v(-53.26, -46.68) * mm});
            skLineSegment(sketch, "E3.3.0.6", {"start": v(-52.81, 8.5) * mm, "end": v(-49.28, 4.96) * mm});
            skLineSegment(sketch, "E3.3.0.7", {"start": v(-49.23, -43.64) * mm, "end": v(-49.73, -43.14) * mm});
            skLineSegment(sketch, "E3.3.0.8", {"start": v(-49.28, 11.04) * mm, "end": v(-52.82, 7.5) * mm});
            skLineSegment(sketch, "E3.3.0.9", {"start": v(-49.23, -37.56) * mm, "end": v(-52.77, -41.1) * mm});
            skLineSegment(sketch, "E3.3.0.10", {"start": v(-49.25, -25.41) * mm, "end": v(-52.78, -28.95) * mm});
            skLineSegment(sketch, "E3.3.0.11", {"start": v(-49.78, 11.53) * mm, "end": v(-53.31, 8) * mm});
            skLineSegment(sketch, "E3.3.0.12", {"start": v(-49.8, 23.68) * mm, "end": v(-53.33, 20.15) * mm});
            skLineSegment(sketch, "E3.3.0.13", {"start": v(-52.8, 2.42) * mm, "end": v(-49.27, -1.11) * mm});
            skLineSegment(sketch, "E3.3.0.14", {"start": v(-52.82, 14.57) * mm, "end": v(-49.28, 11.04) * mm});
            skLineSegment(sketch, "E3.3.0.15", {"start": v(-52.83, 26.72) * mm, "end": v(-49.3, 23.19) * mm});
            skLineSegment(sketch, "E3.3.0.16", {"start": v(-52.77, -34.03) * mm, "end": v(-49.23, -37.56) * mm});
            skLineSegment(sketch, "E3.3.0.17", {"start": v(-52.78, -21.88) * mm, "end": v(-49.25, -25.41) * mm});
            skLineSegment(sketch, "E3.3.0.18", {"start": v(-52.8, -9.73) * mm, "end": v(-49.26, -13.26) * mm});
            skLineSegment(sketch, "E3.3.0.19", {"start": v(-49.26, -13.26) * mm, "end": v(-49.76, -13.76) * mm});
            skLineSegment(sketch, "E3.3.0.20", {"start": v(-49.27, -1.11) * mm, "end": v(-49.77, -1.61) * mm});
            skLineSegment(sketch, "E3.3.0.21", {"start": v(-49.28, 11.04) * mm, "end": v(-49.78, 10.54) * mm});
            skLineSegment(sketch, "E3.3.0.22", {"start": v(-49.3, 23.19) * mm, "end": v(-49.8, 22.69) * mm});
            skLineSegment(sketch, "E3.3.0.23", {"start": v(-49.23, -37.56) * mm, "end": v(-49.73, -38.06) * mm});
            skLineSegment(sketch, "E3.3.0.24", {"start": v(-49.25, -25.41) * mm, "end": v(-49.74, -25.91) * mm});
            skLineSegment(sketch, "E3.3.0.25", {"start": v(-49.26, -13.26) * mm, "end": v(-49.76, -12.77) * mm});
            skLineSegment(sketch, "E3.3.0.26", {"start": v(-49.27, -1.11) * mm, "end": v(-49.77, -0.62) * mm});
            skLineSegment(sketch, "E3.3.0.27", {"start": v(-49.28, 11.04) * mm, "end": v(-49.78, 11.53) * mm});
            skLineSegment(sketch, "E3.3.0.28", {"start": v(-49.3, 23.19) * mm, "end": v(-49.8, 23.68) * mm});
            skLineSegment(sketch, "E3.3.0.29", {"start": v(-49.23, -37.56) * mm, "end": v(-49.73, -37.07) * mm});
            skLineSegment(sketch, "E3.3.0.30", {"start": v(-49.25, -25.41) * mm, "end": v(-49.74, -24.92) * mm});
            skLineSegment(sketch, "E3.3.0.31", {"start": v(-52.82, 7.5) * mm, "end": v(-53.31, 8) * mm});
            skLineSegment(sketch, "E3.3.0.32", {"start": v(-49.31, 41.41) * mm, "end": v(-52.85, 37.87) * mm});
            skLineSegment(sketch, "E3.3.0.33", {"start": v(-49.8, 41.9) * mm, "end": v(-53.34, 38.37) * mm});
            skLineSegment(sketch, "E3.3.0.34", {"start": v(-49.31, 41.41) * mm, "end": v(-49.8, 41.9) * mm});
            skLineSegment(sketch, "E3.3.0.35", {"start": v(-53.34, 38.37) * mm, "end": v(-49.8, 34.84) * mm});
            skLineSegment(sketch, "E3.3.0.36", {"start": v(-52.84, 38.87) * mm, "end": v(-49.3, 35.34) * mm});
            skLineSegment(sketch, "E3.3.0.37", {"start": v(-53.26, -40.6) * mm, "end": v(-49.73, -44.14) * mm});
            skLineSegment(sketch, "E3.3.0.38", {"start": v(-53.3, 8) * mm, "end": v(-49.77, 4.46) * mm});
            skLineSegment(sketch, "E3.3.0.39", {"start": v(-49.25, -19.34) * mm, "end": v(-52.79, -22.87) * mm});
            skLineSegment(sketch, "E3.3.0.40", {"start": v(-49.26, -7.19) * mm, "end": v(-52.8, -10.72) * mm});
            skLineSegment(sketch, "E3.3.0.41", {"start": v(-49.28, 4.96) * mm, "end": v(-52.81, 1.43) * mm});
            skLineSegment(sketch, "E3.3.0.42", {"start": v(-49.24, -31.49) * mm, "end": v(-52.78, -35.02) * mm});
            skLineSegment(sketch, "E3.3.0.43", {"start": v(-49.75, -18.84) * mm, "end": v(-53.29, -22.38) * mm});
            skLineSegment(sketch, "E3.3.0.44", {"start": v(-49.76, -6.7) * mm, "end": v(-53.3, -10.23) * mm});
            skLineSegment(sketch, "E3.3.0.45", {"start": v(-49.77, 5.46) * mm, "end": v(-53.3, 1.92) * mm});
            skLineSegment(sketch, "E3.3.0.46", {"start": v(-49.74, -31) * mm, "end": v(-53.27, -34.53) * mm});
            skLineSegment(sketch, "E3.3.0.47", {"start": v(-52.79, -15.8) * mm, "end": v(-49.25, -19.34) * mm});
            skLineSegment(sketch, "E3.3.0.48", {"start": v(-52.8, -3.65) * mm, "end": v(-49.26, -7.19) * mm});
            skLineSegment(sketch, "E3.3.0.49", {"start": v(-52.83, 32.8) * mm, "end": v(-49.3, 29.26) * mm});
            skLineSegment(sketch, "E3.3.0.50", {"start": v(-52.76, -40.1) * mm, "end": v(-49.23, -43.64) * mm});
            skLineSegment(sketch, "E3.3.0.51", {"start": v(-52.78, -27.95) * mm, "end": v(-49.24, -31.49) * mm});
            skLineSegment(sketch, "E3.3.0.52", {"start": v(-52.82, 20.65) * mm, "end": v(-49.29, 17.11) * mm});
            skLineSegment(sketch, "E3.3.0.53", {"start": v(-52.79, -15.8) * mm, "end": v(-53.29, -16.3) * mm});
            skLineSegment(sketch, "E3.3.0.54", {"start": v(-52.8, -3.65) * mm, "end": v(-53.3, -4.15) * mm});
            skLineSegment(sketch, "E3.3.0.55", {"start": v(-52.81, 8.5) * mm, "end": v(-53.3, 8) * mm});
            skLineSegment(sketch, "E3.3.0.56", {"start": v(-52.76, -40.1) * mm, "end": v(-53.26, -40.6) * mm});
            skLineSegment(sketch, "E3.3.0.57", {"start": v(-52.78, -27.95) * mm, "end": v(-53.27, -28.45) * mm});
            skLineSegment(sketch, "E3.3.0.58", {"start": v(-49.23, -43.64) * mm, "end": v(-49.73, -44.14) * mm});
            skLineSegment(sketch, "E3.3.0.59", {"start": v(-49.25, -19.34) * mm, "end": v(-49.75, -18.84) * mm});
            skLineSegment(sketch, "E3.3.0.60", {"start": v(-49.26, -7.19) * mm, "end": v(-49.76, -6.7) * mm});
            skLineSegment(sketch, "E3.3.0.61", {"start": v(-49.28, 4.96) * mm, "end": v(-49.77, 5.46) * mm});
            skLineSegment(sketch, "E3.3.0.62", {"start": v(-49.24, -31.49) * mm, "end": v(-49.74, -31) * mm});
            skLineSegment(sketch, "E3.3.0.63", {"start": v(-52.81, 1.43) * mm, "end": v(-53.3, 1.92) * mm});
            skLineSegment(sketch, "E3.3.0.64", {"start": v(-52.78, -35.02) * mm, "end": v(-53.27, -34.53) * mm});
            skLineSegment(sketch, "E3.3.0.65", {"start": v(-52.79, -22.87) * mm, "end": v(-53.29, -22.38) * mm});
            skLineSegment(sketch, "E3.3.0.66", {"start": v(-52.8, -10.72) * mm, "end": v(-53.3, -10.23) * mm});
            skLineSegment(sketch, "E3.3.0.67", {"start": v(-53.3, 1.92) * mm, "end": v(-49.77, -1.61) * mm});
            skLineSegment(sketch, "E3.3.0.68", {"start": v(-53.31, 14.07) * mm, "end": v(-49.78, 10.54) * mm});
            skLineSegment(sketch, "E3.3.0.69", {"start": v(-53.33, 26.22) * mm, "end": v(-49.8, 22.69) * mm});
            skLineSegment(sketch, "E3.3.0.70", {"start": v(-52.85, 37.87) * mm, "end": v(-52.84, 31.8) * mm, "construction": true});
            skLineSegment(sketch, "E3.3.0.71", {"start": v(-53.27, -34.52) * mm, "end": v(-49.73, -38.06) * mm});
            skLineSegment(sketch, "E3.3.0.72", {"start": v(-53.28, -22.38) * mm, "end": v(-49.74, -25.91) * mm});
            skLineSegment(sketch, "E3.3.0.73", {"start": v(-53.3, -10.23) * mm, "end": v(-49.76, -13.76) * mm});
            skLineSegment(sketch, "E3.3.0.74", {"start": v(-49.27, -1.11) * mm, "end": v(-52.8, -4.65) * mm});
            skLineSegment(sketch, "E3.3.0.75", {"start": v(-49.3, 23.19) * mm, "end": v(-52.83, 19.65) * mm});
            skLineSegment(sketch, "E3.3.0.76", {"start": v(-49.26, -13.26) * mm, "end": v(-52.8, -16.8) * mm});
            skLineSegment(sketch, "E3.3.0.77", {"start": v(-49.77, -0.62) * mm, "end": v(-53.3, -4.15) * mm});
            skLineSegment(sketch, "E3.3.0.78", {"start": v(-49.73, -37.07) * mm, "end": v(-53.27, -40.6) * mm});
            skLineSegment(sketch, "E3.3.0.79", {"start": v(-49.74, -24.92) * mm, "end": v(-53.28, -28.45) * mm});
            skLineSegment(sketch, "E3.3.0.80", {"start": v(-49.76, -12.77) * mm, "end": v(-53.3, -16.3) * mm});
            skLineSegment(sketch, "E3.3.0.81", {"start": v(-52.8, 2.42) * mm, "end": v(-53.3, 1.92) * mm});
            skLineSegment(sketch, "E3.3.0.82", {"start": v(-52.82, 14.57) * mm, "end": v(-53.31, 14.07) * mm});
            skLineSegment(sketch, "E3.3.0.83", {"start": v(-52.83, 26.72) * mm, "end": v(-53.33, 26.22) * mm});
            skLineSegment(sketch, "E3.3.0.84", {"start": v(-52.77, -34.03) * mm, "end": v(-53.27, -34.52) * mm});
            skLineSegment(sketch, "E3.3.0.85", {"start": v(-52.78, -21.88) * mm, "end": v(-53.28, -22.38) * mm});
            skLineSegment(sketch, "E3.3.0.86", {"start": v(-52.8, -9.73) * mm, "end": v(-53.3, -10.23) * mm});
            skLineSegment(sketch, "E3.3.0.87", {"start": v(-52.83, 19.65) * mm, "end": v(-53.33, 20.15) * mm});
            skLineSegment(sketch, "E3.3.0.88", {"start": v(-52.77, -41.1) * mm, "end": v(-53.27, -40.6) * mm});
            skLineSegment(sketch, "E3.3.0.89", {"start": v(-49.3, 35.34) * mm, "end": v(-49.8, 34.84) * mm});
            skLineSegment(sketch, "E3.3.0.90", {"start": v(-49.31, 41.41) * mm, "end": v(-49.8, 40.91) * mm});
            skLineSegment(sketch, "E3.3.0.91", {"start": v(-49.3, 35.34) * mm, "end": v(-52.84, 31.8) * mm});
            skLineSegment(sketch, "E3.3.0.92", {"start": v(-49.8, 35.83) * mm, "end": v(-53.34, 32.3) * mm});
            skLineSegment(sketch, "E3.3.0.93", {"start": v(-52.84, 38.87) * mm, "end": v(-53.34, 38.37) * mm});
            skLineSegment(sketch, "E3.3.0.94", {"start": v(-53.27, -28.45) * mm, "end": v(-49.74, -31.99) * mm});
            skLineSegment(sketch, "E3.3.0.95", {"start": v(-53.33, 32.3) * mm, "end": v(-49.8, 28.76) * mm});
            skLineSegment(sketch, "E3.3.0.96", {"start": v(-53.29, -16.3) * mm, "end": v(-49.75, -19.84) * mm});
            skLineSegment(sketch, "E3.3.0.97", {"start": v(-53.3, -4.15) * mm, "end": v(-49.76, -7.69) * mm});
            skLineSegment(sketch, "E3.3.0.98", {"start": v(-53.32, 20.15) * mm, "end": v(-49.78, 16.61) * mm});
            skLineSegment(sketch, "E3.3.0.99", {"start": v(-49.3, 29.26) * mm, "end": v(-52.83, 25.73) * mm});
            skLineSegment(sketch, "E3.3.0.100", {"start": v(-49.29, 17.11) * mm, "end": v(-52.82, 13.58) * mm});
            skLineSegment(sketch, "E3.3.0.101", {"start": v(-49.8, 29.76) * mm, "end": v(-53.33, 26.22) * mm});
            skLineSegment(sketch, "E3.3.0.102", {"start": v(-49.78, 17.6) * mm, "end": v(-53.32, 14.07) * mm});
            skLineSegment(sketch, "E3.3.0.103", {"start": v(-52.82, 20.65) * mm, "end": v(-53.32, 20.15) * mm});
            skLineSegment(sketch, "E3.3.0.104", {"start": v(-49.25, -19.34) * mm, "end": v(-49.75, -19.84) * mm});
            skLineSegment(sketch, "E3.3.0.105", {"start": v(-49.26, -7.19) * mm, "end": v(-49.76, -7.69) * mm});
            skLineSegment(sketch, "E3.3.0.106", {"start": v(-49.28, 4.96) * mm, "end": v(-49.77, 4.46) * mm});
            skLineSegment(sketch, "E3.3.0.107", {"start": v(-49.24, -31.49) * mm, "end": v(-49.74, -31.99) * mm});
            skLineSegment(sketch, "E3.3.0.108", {"start": v(-49.3, 29.26) * mm, "end": v(-49.8, 29.76) * mm});
            skLineSegment(sketch, "E3.3.0.109", {"start": v(-49.29, 17.11) * mm, "end": v(-49.78, 17.6) * mm});
            skLineSegment(sketch, "E3.3.0.110", {"start": v(-52.82, 13.58) * mm, "end": v(-53.32, 14.07) * mm});
            skLineSegment(sketch, "E3.3.0.111", {"start": v(-52.83, 25.73) * mm, "end": v(-53.33, 26.22) * mm});
            skLineSegment(sketch, "E3.3.0.112", {"start": v(-52.8, -16.8) * mm, "end": v(-53.3, -16.3) * mm});
            skLineSegment(sketch, "E3.3.0.113", {"start": v(-52.8, -4.65) * mm, "end": v(-53.3, -4.15) * mm});
            skLineSegment(sketch, "E3.3.0.114", {"start": v(-52.78, -28.95) * mm, "end": v(-53.28, -28.45) * mm});
            skLineSegment(sketch, "E3.3.0.115", {"start": v(-49.3, 35.34) * mm, "end": v(-49.8, 35.83) * mm});
            skLineSegment(sketch, "E3.3.0.116", {"start": v(-52.84, 31.8) * mm, "end": v(-53.34, 32.3) * mm});
            skLineSegment(sketch, "E3.3.0.117", {"start": v(-52.85, 37.87) * mm, "end": v(-53.34, 38.37) * mm});
            skLineSegment(sketch, "E3.3.0.118", {"start": v(-52.83, 32.8) * mm, "end": v(-53.33, 32.3) * mm});
            skLineSegment(sketch, "E3.3.0.119", {"start": v(-49.3, 29.26) * mm, "end": v(-49.8, 28.76) * mm});
            skLineSegment(sketch, "E3.3.0.120", {"start": v(-49.29, 17.11) * mm, "end": v(-49.78, 16.61) * mm});
            skLineSegment(sketch, "E3.4.0.0", {"start": v(-47.45, 44.95) * mm, "end": v(-43.91, 41.41) * mm});
            skLineSegment(sketch, "E3.4.0.1", {"start": v(-47.94, 44.45) * mm, "end": v(-44.4, 40.91) * mm});
            skLineSegment(sketch, "E3.4.0.2", {"start": v(-47.45, 44.95) * mm, "end": v(-47.94, 44.45) * mm});
            skLineSegment(sketch, "E3.4.0.3", {"start": v(-43.83, -43.64) * mm, "end": v(-47.36, -47.17) * mm});
            skLineSegment(sketch, "E3.4.0.4", {"start": v(-44.33, -43.14) * mm, "end": v(-47.86, -46.68) * mm});
            skLineSegment(sketch, "E3.4.0.5", {"start": v(-47.36, -47.17) * mm, "end": v(-47.86, -46.68) * mm});
            skLineSegment(sketch, "E3.4.0.6", {"start": v(-47.41, 8.5) * mm, "end": v(-43.88, 4.96) * mm});
            skLineSegment(sketch, "E3.4.0.7", {"start": v(-43.83, -43.64) * mm, "end": v(-44.33, -43.14) * mm});
            skLineSegment(sketch, "E3.4.0.8", {"start": v(-43.88, 11.04) * mm, "end": v(-47.42, 7.5) * mm});
            skLineSegment(sketch, "E3.4.0.9", {"start": v(-43.83, -37.56) * mm, "end": v(-47.37, -41.1) * mm});
            skLineSegment(sketch, "E3.4.0.10", {"start": v(-43.85, -25.41) * mm, "end": v(-47.38, -28.95) * mm});
            skLineSegment(sketch, "E3.4.0.11", {"start": v(-44.38, 11.53) * mm, "end": v(-47.91, 8) * mm});
            skLineSegment(sketch, "E3.4.0.12", {"start": v(-44.4, 23.68) * mm, "end": v(-47.93, 20.15) * mm});
            skLineSegment(sketch, "E3.4.0.13", {"start": v(-47.4, 2.42) * mm, "end": v(-43.87, -1.11) * mm});
            skLineSegment(sketch, "E3.4.0.14", {"start": v(-47.42, 14.57) * mm, "end": v(-43.88, 11.04) * mm});
            skLineSegment(sketch, "E3.4.0.15", {"start": v(-47.43, 26.72) * mm, "end": v(-43.9, 23.19) * mm});
            skLineSegment(sketch, "E3.4.0.16", {"start": v(-47.37, -34.03) * mm, "end": v(-43.83, -37.56) * mm});
            skLineSegment(sketch, "E3.4.0.17", {"start": v(-47.38, -21.88) * mm, "end": v(-43.85, -25.41) * mm});
            skLineSegment(sketch, "E3.4.0.18", {"start": v(-47.4, -9.73) * mm, "end": v(-43.86, -13.26) * mm});
            skLineSegment(sketch, "E3.4.0.19", {"start": v(-43.86, -13.26) * mm, "end": v(-44.36, -13.76) * mm});
            skLineSegment(sketch, "E3.4.0.20", {"start": v(-43.87, -1.11) * mm, "end": v(-44.37, -1.61) * mm});
            skLineSegment(sketch, "E3.4.0.21", {"start": v(-43.88, 11.04) * mm, "end": v(-44.38, 10.54) * mm});
            skLineSegment(sketch, "E3.4.0.22", {"start": v(-43.9, 23.19) * mm, "end": v(-44.4, 22.69) * mm});
            skLineSegment(sketch, "E3.4.0.23", {"start": v(-43.83, -37.56) * mm, "end": v(-44.33, -38.06) * mm});
            skLineSegment(sketch, "E3.4.0.24", {"start": v(-43.85, -25.41) * mm, "end": v(-44.34, -25.91) * mm});
            skLineSegment(sketch, "E3.4.0.25", {"start": v(-43.86, -13.26) * mm, "end": v(-44.36, -12.77) * mm});
            skLineSegment(sketch, "E3.4.0.26", {"start": v(-43.87, -1.11) * mm, "end": v(-44.37, -0.62) * mm});
            skLineSegment(sketch, "E3.4.0.27", {"start": v(-43.88, 11.04) * mm, "end": v(-44.38, 11.53) * mm});
            skLineSegment(sketch, "E3.4.0.28", {"start": v(-43.9, 23.19) * mm, "end": v(-44.4, 23.68) * mm});
            skLineSegment(sketch, "E3.4.0.29", {"start": v(-43.83, -37.56) * mm, "end": v(-44.33, -37.07) * mm});
            skLineSegment(sketch, "E3.4.0.30", {"start": v(-43.85, -25.41) * mm, "end": v(-44.34, -24.92) * mm});
            skLineSegment(sketch, "E3.4.0.31", {"start": v(-47.42, 7.5) * mm, "end": v(-47.91, 8) * mm});
            skLineSegment(sketch, "E3.4.0.32", {"start": v(-43.91, 41.41) * mm, "end": v(-47.45, 37.87) * mm});
            skLineSegment(sketch, "E3.4.0.33", {"start": v(-44.4, 41.9) * mm, "end": v(-47.94, 38.37) * mm});
            skLineSegment(sketch, "E3.4.0.34", {"start": v(-43.91, 41.41) * mm, "end": v(-44.4, 41.9) * mm});
            skLineSegment(sketch, "E3.4.0.35", {"start": v(-47.94, 38.37) * mm, "end": v(-44.4, 34.84) * mm});
            skLineSegment(sketch, "E3.4.0.36", {"start": v(-47.44, 38.87) * mm, "end": v(-43.9, 35.34) * mm});
            skLineSegment(sketch, "E3.4.0.37", {"start": v(-47.86, -40.6) * mm, "end": v(-44.33, -44.14) * mm});
            skLineSegment(sketch, "E3.4.0.38", {"start": v(-47.9, 8) * mm, "end": v(-44.37, 4.46) * mm});
            skLineSegment(sketch, "E3.4.0.39", {"start": v(-43.85, -19.34) * mm, "end": v(-47.39, -22.87) * mm});
            skLineSegment(sketch, "E3.4.0.40", {"start": v(-43.86, -7.19) * mm, "end": v(-47.4, -10.72) * mm});
            skLineSegment(sketch, "E3.4.0.41", {"start": v(-43.88, 4.96) * mm, "end": v(-47.41, 1.43) * mm});
            skLineSegment(sketch, "E3.4.0.42", {"start": v(-43.84, -31.49) * mm, "end": v(-47.38, -35.02) * mm});
            skLineSegment(sketch, "E3.4.0.43", {"start": v(-44.35, -18.84) * mm, "end": v(-47.89, -22.38) * mm});
            skLineSegment(sketch, "E3.4.0.44", {"start": v(-44.36, -6.7) * mm, "end": v(-47.9, -10.23) * mm});
            skLineSegment(sketch, "E3.4.0.45", {"start": v(-44.37, 5.46) * mm, "end": v(-47.9, 1.92) * mm});
            skLineSegment(sketch, "E3.4.0.46", {"start": v(-44.34, -31) * mm, "end": v(-47.87, -34.53) * mm});
            skLineSegment(sketch, "E3.4.0.47", {"start": v(-47.39, -15.8) * mm, "end": v(-43.85, -19.34) * mm});
            skLineSegment(sketch, "E3.4.0.48", {"start": v(-47.4, -3.65) * mm, "end": v(-43.86, -7.19) * mm});
            skLineSegment(sketch, "E3.4.0.49", {"start": v(-47.43, 32.8) * mm, "end": v(-43.9, 29.26) * mm});
            skLineSegment(sketch, "E3.4.0.50", {"start": v(-47.36, -40.1) * mm, "end": v(-43.83, -43.64) * mm});
            skLineSegment(sketch, "E3.4.0.51", {"start": v(-47.38, -27.95) * mm, "end": v(-43.84, -31.49) * mm});
            skLineSegment(sketch, "E3.4.0.52", {"start": v(-47.42, 20.65) * mm, "end": v(-43.89, 17.11) * mm});
            skLineSegment(sketch, "E3.4.0.53", {"start": v(-47.39, -15.8) * mm, "end": v(-47.89, -16.3) * mm});
            skLineSegment(sketch, "E3.4.0.54", {"start": v(-47.4, -3.65) * mm, "end": v(-47.9, -4.15) * mm});
            skLineSegment(sketch, "E3.4.0.55", {"start": v(-47.41, 8.5) * mm, "end": v(-47.9, 8) * mm});
            skLineSegment(sketch, "E3.4.0.56", {"start": v(-47.36, -40.1) * mm, "end": v(-47.86, -40.6) * mm});
            skLineSegment(sketch, "E3.4.0.57", {"start": v(-47.38, -27.95) * mm, "end": v(-47.87, -28.45) * mm});
            skLineSegment(sketch, "E3.4.0.58", {"start": v(-43.83, -43.64) * mm, "end": v(-44.33, -44.14) * mm});
            skLineSegment(sketch, "E3.4.0.59", {"start": v(-43.85, -19.34) * mm, "end": v(-44.35, -18.84) * mm});
            skLineSegment(sketch, "E3.4.0.60", {"start": v(-43.86, -7.19) * mm, "end": v(-44.36, -6.7) * mm});
            skLineSegment(sketch, "E3.4.0.61", {"start": v(-43.88, 4.96) * mm, "end": v(-44.37, 5.46) * mm});
            skLineSegment(sketch, "E3.4.0.62", {"start": v(-43.84, -31.49) * mm, "end": v(-44.34, -31) * mm});
            skLineSegment(sketch, "E3.4.0.63", {"start": v(-47.41, 1.43) * mm, "end": v(-47.9, 1.92) * mm});
            skLineSegment(sketch, "E3.4.0.64", {"start": v(-47.38, -35.02) * mm, "end": v(-47.87, -34.53) * mm});
            skLineSegment(sketch, "E3.4.0.65", {"start": v(-47.39, -22.87) * mm, "end": v(-47.89, -22.38) * mm});
            skLineSegment(sketch, "E3.4.0.66", {"start": v(-47.4, -10.72) * mm, "end": v(-47.9, -10.23) * mm});
            skLineSegment(sketch, "E3.4.0.67", {"start": v(-47.9, 1.92) * mm, "end": v(-44.37, -1.61) * mm});
            skLineSegment(sketch, "E3.4.0.68", {"start": v(-47.91, 14.07) * mm, "end": v(-44.38, 10.54) * mm});
            skLineSegment(sketch, "E3.4.0.69", {"start": v(-47.93, 26.22) * mm, "end": v(-44.4, 22.69) * mm});
            skLineSegment(sketch, "E3.4.0.70", {"start": v(-47.45, 37.87) * mm, "end": v(-47.44, 31.8) * mm, "construction": true});
            skLineSegment(sketch, "E3.4.0.71", {"start": v(-47.87, -34.52) * mm, "end": v(-44.33, -38.06) * mm});
            skLineSegment(sketch, "E3.4.0.72", {"start": v(-47.88, -22.38) * mm, "end": v(-44.34, -25.91) * mm});
            skLineSegment(sketch, "E3.4.0.73", {"start": v(-47.9, -10.23) * mm, "end": v(-44.36, -13.76) * mm});
            skLineSegment(sketch, "E3.4.0.74", {"start": v(-43.87, -1.11) * mm, "end": v(-47.4, -4.65) * mm});
            skLineSegment(sketch, "E3.4.0.75", {"start": v(-43.9, 23.19) * mm, "end": v(-47.43, 19.65) * mm});
            skLineSegment(sketch, "E3.4.0.76", {"start": v(-43.86, -13.26) * mm, "end": v(-47.4, -16.8) * mm});
            skLineSegment(sketch, "E3.4.0.77", {"start": v(-44.37, -0.62) * mm, "end": v(-47.9, -4.15) * mm});
            skLineSegment(sketch, "E3.4.0.78", {"start": v(-44.33, -37.07) * mm, "end": v(-47.87, -40.6) * mm});
            skLineSegment(sketch, "E3.4.0.79", {"start": v(-44.34, -24.92) * mm, "end": v(-47.88, -28.45) * mm});
            skLineSegment(sketch, "E3.4.0.80", {"start": v(-44.36, -12.77) * mm, "end": v(-47.9, -16.3) * mm});
            skLineSegment(sketch, "E3.4.0.81", {"start": v(-47.4, 2.42) * mm, "end": v(-47.9, 1.92) * mm});
            skLineSegment(sketch, "E3.4.0.82", {"start": v(-47.42, 14.57) * mm, "end": v(-47.91, 14.07) * mm});
            skLineSegment(sketch, "E3.4.0.83", {"start": v(-47.43, 26.72) * mm, "end": v(-47.93, 26.22) * mm});
            skLineSegment(sketch, "E3.4.0.84", {"start": v(-47.37, -34.03) * mm, "end": v(-47.87, -34.52) * mm});
            skLineSegment(sketch, "E3.4.0.85", {"start": v(-47.38, -21.88) * mm, "end": v(-47.88, -22.38) * mm});
            skLineSegment(sketch, "E3.4.0.86", {"start": v(-47.4, -9.73) * mm, "end": v(-47.9, -10.23) * mm});
            skLineSegment(sketch, "E3.4.0.87", {"start": v(-47.43, 19.65) * mm, "end": v(-47.93, 20.15) * mm});
            skLineSegment(sketch, "E3.4.0.88", {"start": v(-47.37, -41.1) * mm, "end": v(-47.87, -40.6) * mm});
            skLineSegment(sketch, "E3.4.0.89", {"start": v(-43.9, 35.34) * mm, "end": v(-44.4, 34.84) * mm});
            skLineSegment(sketch, "E3.4.0.90", {"start": v(-43.91, 41.41) * mm, "end": v(-44.4, 40.91) * mm});
            skLineSegment(sketch, "E3.4.0.91", {"start": v(-43.9, 35.34) * mm, "end": v(-47.44, 31.8) * mm});
            skLineSegment(sketch, "E3.4.0.92", {"start": v(-44.4, 35.83) * mm, "end": v(-47.94, 32.3) * mm});
            skLineSegment(sketch, "E3.4.0.93", {"start": v(-47.44, 38.87) * mm, "end": v(-47.94, 38.37) * mm});
            skLineSegment(sketch, "E3.4.0.94", {"start": v(-47.87, -28.45) * mm, "end": v(-44.34, -31.99) * mm});
            skLineSegment(sketch, "E3.4.0.95", {"start": v(-47.93, 32.3) * mm, "end": v(-44.4, 28.76) * mm});
            skLineSegment(sketch, "E3.4.0.96", {"start": v(-47.89, -16.3) * mm, "end": v(-44.35, -19.84) * mm});
            skLineSegment(sketch, "E3.4.0.97", {"start": v(-47.9, -4.15) * mm, "end": v(-44.36, -7.69) * mm});
            skLineSegment(sketch, "E3.4.0.98", {"start": v(-47.92, 20.15) * mm, "end": v(-44.38, 16.61) * mm});
            skLineSegment(sketch, "E3.4.0.99", {"start": v(-43.9, 29.26) * mm, "end": v(-47.43, 25.73) * mm});
            skLineSegment(sketch, "E3.4.0.100", {"start": v(-43.89, 17.11) * mm, "end": v(-47.42, 13.58) * mm});
            skLineSegment(sketch, "E3.4.0.101", {"start": v(-44.4, 29.76) * mm, "end": v(-47.93, 26.22) * mm});
            skLineSegment(sketch, "E3.4.0.102", {"start": v(-44.38, 17.6) * mm, "end": v(-47.92, 14.07) * mm});
            skLineSegment(sketch, "E3.4.0.103", {"start": v(-47.42, 20.65) * mm, "end": v(-47.92, 20.15) * mm});
            skLineSegment(sketch, "E3.4.0.104", {"start": v(-43.85, -19.34) * mm, "end": v(-44.35, -19.84) * mm});
            skLineSegment(sketch, "E3.4.0.105", {"start": v(-43.86, -7.19) * mm, "end": v(-44.36, -7.69) * mm});
            skLineSegment(sketch, "E3.4.0.106", {"start": v(-43.88, 4.96) * mm, "end": v(-44.37, 4.46) * mm});
            skLineSegment(sketch, "E3.4.0.107", {"start": v(-43.84, -31.49) * mm, "end": v(-44.34, -31.99) * mm});
            skLineSegment(sketch, "E3.4.0.108", {"start": v(-43.9, 29.26) * mm, "end": v(-44.4, 29.76) * mm});
            skLineSegment(sketch, "E3.4.0.109", {"start": v(-43.89, 17.11) * mm, "end": v(-44.38, 17.6) * mm});
            skLineSegment(sketch, "E3.4.0.110", {"start": v(-47.42, 13.58) * mm, "end": v(-47.92, 14.07) * mm});
            skLineSegment(sketch, "E3.4.0.111", {"start": v(-47.43, 25.73) * mm, "end": v(-47.93, 26.22) * mm});
            skLineSegment(sketch, "E3.4.0.112", {"start": v(-47.4, -16.8) * mm, "end": v(-47.9, -16.3) * mm});
            skLineSegment(sketch, "E3.4.0.113", {"start": v(-47.4, -4.65) * mm, "end": v(-47.9, -4.15) * mm});
            skLineSegment(sketch, "E3.4.0.114", {"start": v(-47.38, -28.95) * mm, "end": v(-47.88, -28.45) * mm});
            skLineSegment(sketch, "E3.4.0.115", {"start": v(-43.9, 35.34) * mm, "end": v(-44.4, 35.83) * mm});
            skLineSegment(sketch, "E3.4.0.116", {"start": v(-47.44, 31.8) * mm, "end": v(-47.94, 32.3) * mm});
            skLineSegment(sketch, "E3.4.0.117", {"start": v(-47.45, 37.87) * mm, "end": v(-47.94, 38.37) * mm});
            skLineSegment(sketch, "E3.4.0.118", {"start": v(-47.43, 32.8) * mm, "end": v(-47.93, 32.3) * mm});
            skLineSegment(sketch, "E3.4.0.119", {"start": v(-43.9, 29.26) * mm, "end": v(-44.4, 28.76) * mm});
            skLineSegment(sketch, "E3.4.0.120", {"start": v(-43.89, 17.11) * mm, "end": v(-44.38, 16.61) * mm});
            skLineSegment(sketch, "E3.5.0.0", {"start": v(-42.05, 44.95) * mm, "end": v(-38.51, 41.41) * mm});
            skLineSegment(sketch, "E3.5.0.1", {"start": v(-42.54, 44.45) * mm, "end": v(-39, 40.91) * mm});
            skLineSegment(sketch, "E3.5.0.2", {"start": v(-42.05, 44.95) * mm, "end": v(-42.54, 44.45) * mm});
            skLineSegment(sketch, "E3.5.0.3", {"start": v(-38.43, -43.64) * mm, "end": v(-41.96, -47.17) * mm});
            skLineSegment(sketch, "E3.5.0.4", {"start": v(-38.93, -43.14) * mm, "end": v(-42.46, -46.68) * mm});
            skLineSegment(sketch, "E3.5.0.5", {"start": v(-41.96, -47.17) * mm, "end": v(-42.46, -46.68) * mm});
            skLineSegment(sketch, "E3.5.0.6", {"start": v(-42.01, 8.5) * mm, "end": v(-38.48, 4.96) * mm});
            skLineSegment(sketch, "E3.5.0.7", {"start": v(-38.43, -43.64) * mm, "end": v(-38.93, -43.14) * mm});
            skLineSegment(sketch, "E3.5.0.8", {"start": v(-38.48, 11.04) * mm, "end": v(-42.02, 7.5) * mm});
            skLineSegment(sketch, "E3.5.0.9", {"start": v(-38.43, -37.56) * mm, "end": v(-41.97, -41.1) * mm});
            skLineSegment(sketch, "E3.5.0.10", {"start": v(-38.45, -25.41) * mm, "end": v(-41.98, -28.95) * mm});
            skLineSegment(sketch, "E3.5.0.11", {"start": v(-38.98, 11.53) * mm, "end": v(-42.51, 8) * mm});
            skLineSegment(sketch, "E3.5.0.12", {"start": v(-39, 23.68) * mm, "end": v(-42.53, 20.15) * mm});
            skLineSegment(sketch, "E3.5.0.13", {"start": v(-42, 2.42) * mm, "end": v(-38.47, -1.11) * mm});
            skLineSegment(sketch, "E3.5.0.14", {"start": v(-42.02, 14.57) * mm, "end": v(-38.48, 11.04) * mm});
            skLineSegment(sketch, "E3.5.0.15", {"start": v(-42.03, 26.72) * mm, "end": v(-38.5, 23.19) * mm});
            skLineSegment(sketch, "E3.5.0.16", {"start": v(-41.97, -34.03) * mm, "end": v(-38.43, -37.56) * mm});
            skLineSegment(sketch, "E3.5.0.17", {"start": v(-41.98, -21.88) * mm, "end": v(-38.45, -25.41) * mm});
            skLineSegment(sketch, "E3.5.0.18", {"start": v(-42, -9.73) * mm, "end": v(-38.46, -13.26) * mm});
            skLineSegment(sketch, "E3.5.0.19", {"start": v(-38.46, -13.26) * mm, "end": v(-38.96, -13.76) * mm});
            skLineSegment(sketch, "E3.5.0.20", {"start": v(-38.47, -1.11) * mm, "end": v(-38.97, -1.61) * mm});
            skLineSegment(sketch, "E3.5.0.21", {"start": v(-38.48, 11.04) * mm, "end": v(-38.98, 10.54) * mm});
            skLineSegment(sketch, "E3.5.0.22", {"start": v(-38.5, 23.19) * mm, "end": v(-39, 22.69) * mm});
            skLineSegment(sketch, "E3.5.0.23", {"start": v(-38.43, -37.56) * mm, "end": v(-38.93, -38.06) * mm});
            skLineSegment(sketch, "E3.5.0.24", {"start": v(-38.45, -25.41) * mm, "end": v(-38.94, -25.91) * mm});
            skLineSegment(sketch, "E3.5.0.25", {"start": v(-38.46, -13.26) * mm, "end": v(-38.96, -12.77) * mm});
            skLineSegment(sketch, "E3.5.0.26", {"start": v(-38.47, -1.11) * mm, "end": v(-38.97, -0.62) * mm});
            skLineSegment(sketch, "E3.5.0.27", {"start": v(-38.48, 11.04) * mm, "end": v(-38.98, 11.53) * mm});
            skLineSegment(sketch, "E3.5.0.28", {"start": v(-38.5, 23.19) * mm, "end": v(-39, 23.68) * mm});
            skLineSegment(sketch, "E3.5.0.29", {"start": v(-38.43, -37.56) * mm, "end": v(-38.93, -37.07) * mm});
            skLineSegment(sketch, "E3.5.0.30", {"start": v(-38.45, -25.41) * mm, "end": v(-38.94, -24.92) * mm});
            skLineSegment(sketch, "E3.5.0.31", {"start": v(-42.02, 7.5) * mm, "end": v(-42.51, 8) * mm});
            skLineSegment(sketch, "E3.5.0.32", {"start": v(-38.51, 41.41) * mm, "end": v(-42.05, 37.87) * mm});
            skLineSegment(sketch, "E3.5.0.33", {"start": v(-39, 41.9) * mm, "end": v(-42.54, 38.37) * mm});
            skLineSegment(sketch, "E3.5.0.34", {"start": v(-38.51, 41.41) * mm, "end": v(-39, 41.9) * mm});
            skLineSegment(sketch, "E3.5.0.35", {"start": v(-42.54, 38.37) * mm, "end": v(-39, 34.84) * mm});
            skLineSegment(sketch, "E3.5.0.36", {"start": v(-42.04, 38.87) * mm, "end": v(-38.5, 35.34) * mm});
            skLineSegment(sketch, "E3.5.0.37", {"start": v(-42.46, -40.6) * mm, "end": v(-38.93, -44.14) * mm});
            skLineSegment(sketch, "E3.5.0.38", {"start": v(-42.5, 8) * mm, "end": v(-38.97, 4.46) * mm});
            skLineSegment(sketch, "E3.5.0.39", {"start": v(-38.45, -19.34) * mm, "end": v(-41.99, -22.87) * mm});
            skLineSegment(sketch, "E3.5.0.40", {"start": v(-38.46, -7.19) * mm, "end": v(-42, -10.72) * mm});
            skLineSegment(sketch, "E3.5.0.41", {"start": v(-38.48, 4.96) * mm, "end": v(-42.01, 1.43) * mm});
            skLineSegment(sketch, "E3.5.0.42", {"start": v(-38.44, -31.49) * mm, "end": v(-41.98, -35.02) * mm});
            skLineSegment(sketch, "E3.5.0.43", {"start": v(-38.95, -18.84) * mm, "end": v(-42.49, -22.38) * mm});
            skLineSegment(sketch, "E3.5.0.44", {"start": v(-38.96, -6.7) * mm, "end": v(-42.5, -10.23) * mm});
            skLineSegment(sketch, "E3.5.0.45", {"start": v(-38.97, 5.46) * mm, "end": v(-42.5, 1.92) * mm});
            skLineSegment(sketch, "E3.5.0.46", {"start": v(-38.94, -31) * mm, "end": v(-42.47, -34.53) * mm});
            skLineSegment(sketch, "E3.5.0.47", {"start": v(-41.99, -15.8) * mm, "end": v(-38.45, -19.34) * mm});
            skLineSegment(sketch, "E3.5.0.48", {"start": v(-42, -3.65) * mm, "end": v(-38.46, -7.19) * mm});
            skLineSegment(sketch, "E3.5.0.49", {"start": v(-42.03, 32.8) * mm, "end": v(-38.5, 29.26) * mm});
            skLineSegment(sketch, "E3.5.0.50", {"start": v(-41.96, -40.1) * mm, "end": v(-38.43, -43.64) * mm});
            skLineSegment(sketch, "E3.5.0.51", {"start": v(-41.98, -27.95) * mm, "end": v(-38.44, -31.49) * mm});
            skLineSegment(sketch, "E3.5.0.52", {"start": v(-42.02, 20.65) * mm, "end": v(-38.49, 17.11) * mm});
            skLineSegment(sketch, "E3.5.0.53", {"start": v(-41.99, -15.8) * mm, "end": v(-42.49, -16.3) * mm});
            skLineSegment(sketch, "E3.5.0.54", {"start": v(-42, -3.65) * mm, "end": v(-42.5, -4.15) * mm});
            skLineSegment(sketch, "E3.5.0.55", {"start": v(-42.01, 8.5) * mm, "end": v(-42.5, 8) * mm});
            skLineSegment(sketch, "E3.5.0.56", {"start": v(-41.96, -40.1) * mm, "end": v(-42.46, -40.6) * mm});
            skLineSegment(sketch, "E3.5.0.57", {"start": v(-41.98, -27.95) * mm, "end": v(-42.47, -28.45) * mm});
            skLineSegment(sketch, "E3.5.0.58", {"start": v(-38.43, -43.64) * mm, "end": v(-38.93, -44.14) * mm});
            skLineSegment(sketch, "E3.5.0.59", {"start": v(-38.45, -19.34) * mm, "end": v(-38.95, -18.84) * mm});
            skLineSegment(sketch, "E3.5.0.60", {"start": v(-38.46, -7.19) * mm, "end": v(-38.96, -6.7) * mm});
            skLineSegment(sketch, "E3.5.0.61", {"start": v(-38.48, 4.96) * mm, "end": v(-38.97, 5.46) * mm});
            skLineSegment(sketch, "E3.5.0.62", {"start": v(-38.44, -31.49) * mm, "end": v(-38.94, -31) * mm});
            skLineSegment(sketch, "E3.5.0.63", {"start": v(-42.01, 1.43) * mm, "end": v(-42.5, 1.92) * mm});
            skLineSegment(sketch, "E3.5.0.64", {"start": v(-41.98, -35.02) * mm, "end": v(-42.47, -34.53) * mm});
            skLineSegment(sketch, "E3.5.0.65", {"start": v(-41.99, -22.87) * mm, "end": v(-42.49, -22.38) * mm});
            skLineSegment(sketch, "E3.5.0.66", {"start": v(-42, -10.72) * mm, "end": v(-42.5, -10.23) * mm});
            skLineSegment(sketch, "E3.5.0.67", {"start": v(-42.5, 1.92) * mm, "end": v(-38.97, -1.61) * mm});
            skLineSegment(sketch, "E3.5.0.68", {"start": v(-42.51, 14.07) * mm, "end": v(-38.98, 10.54) * mm});
            skLineSegment(sketch, "E3.5.0.69", {"start": v(-42.53, 26.22) * mm, "end": v(-39, 22.69) * mm});
            skLineSegment(sketch, "E3.5.0.70", {"start": v(-42.05, 37.87) * mm, "end": v(-42.04, 31.8) * mm, "construction": true});
            skLineSegment(sketch, "E3.5.0.71", {"start": v(-42.47, -34.52) * mm, "end": v(-38.93, -38.06) * mm});
            skLineSegment(sketch, "E3.5.0.72", {"start": v(-42.48, -22.38) * mm, "end": v(-38.94, -25.91) * mm});
            skLineSegment(sketch, "E3.5.0.73", {"start": v(-42.5, -10.23) * mm, "end": v(-38.96, -13.76) * mm});
            skLineSegment(sketch, "E3.5.0.74", {"start": v(-38.47, -1.11) * mm, "end": v(-42, -4.65) * mm});
            skLineSegment(sketch, "E3.5.0.75", {"start": v(-38.5, 23.19) * mm, "end": v(-42.03, 19.65) * mm});
            skLineSegment(sketch, "E3.5.0.76", {"start": v(-38.46, -13.26) * mm, "end": v(-42, -16.8) * mm});
            skLineSegment(sketch, "E3.5.0.77", {"start": v(-38.97, -0.62) * mm, "end": v(-42.5, -4.15) * mm});
            skLineSegment(sketch, "E3.5.0.78", {"start": v(-38.93, -37.07) * mm, "end": v(-42.47, -40.6) * mm});
            skLineSegment(sketch, "E3.5.0.79", {"start": v(-38.94, -24.92) * mm, "end": v(-42.48, -28.45) * mm});
            skLineSegment(sketch, "E3.5.0.80", {"start": v(-38.96, -12.77) * mm, "end": v(-42.5, -16.3) * mm});
            skLineSegment(sketch, "E3.5.0.81", {"start": v(-42, 2.42) * mm, "end": v(-42.5, 1.92) * mm});
            skLineSegment(sketch, "E3.5.0.82", {"start": v(-42.02, 14.57) * mm, "end": v(-42.51, 14.07) * mm});
            skLineSegment(sketch, "E3.5.0.83", {"start": v(-42.03, 26.72) * mm, "end": v(-42.53, 26.22) * mm});
            skLineSegment(sketch, "E3.5.0.84", {"start": v(-41.97, -34.03) * mm, "end": v(-42.47, -34.52) * mm});
            skLineSegment(sketch, "E3.5.0.85", {"start": v(-41.98, -21.88) * mm, "end": v(-42.48, -22.38) * mm});
            skLineSegment(sketch, "E3.5.0.86", {"start": v(-42, -9.73) * mm, "end": v(-42.5, -10.23) * mm});
            skLineSegment(sketch, "E3.5.0.87", {"start": v(-42.03, 19.65) * mm, "end": v(-42.53, 20.15) * mm});
            skLineSegment(sketch, "E3.5.0.88", {"start": v(-41.97, -41.1) * mm, "end": v(-42.47, -40.6) * mm});
            skLineSegment(sketch, "E3.5.0.89", {"start": v(-38.5, 35.34) * mm, "end": v(-39, 34.84) * mm});
            skLineSegment(sketch, "E3.5.0.90", {"start": v(-38.51, 41.41) * mm, "end": v(-39, 40.91) * mm});
            skLineSegment(sketch, "E3.5.0.91", {"start": v(-38.5, 35.34) * mm, "end": v(-42.04, 31.8) * mm});
            skLineSegment(sketch, "E3.5.0.92", {"start": v(-39, 35.83) * mm, "end": v(-42.54, 32.3) * mm});
            skLineSegment(sketch, "E3.5.0.93", {"start": v(-42.04, 38.87) * mm, "end": v(-42.54, 38.37) * mm});
            skLineSegment(sketch, "E3.5.0.94", {"start": v(-42.47, -28.45) * mm, "end": v(-38.94, -31.99) * mm});
            skLineSegment(sketch, "E3.5.0.95", {"start": v(-42.53, 32.3) * mm, "end": v(-39, 28.76) * mm});
            skLineSegment(sketch, "E3.5.0.96", {"start": v(-42.49, -16.3) * mm, "end": v(-38.95, -19.84) * mm});
            skLineSegment(sketch, "E3.5.0.97", {"start": v(-42.5, -4.15) * mm, "end": v(-38.96, -7.69) * mm});
            skLineSegment(sketch, "E3.5.0.98", {"start": v(-42.52, 20.15) * mm, "end": v(-38.98, 16.61) * mm});
            skLineSegment(sketch, "E3.5.0.99", {"start": v(-38.5, 29.26) * mm, "end": v(-42.03, 25.73) * mm});
            skLineSegment(sketch, "E3.5.0.100", {"start": v(-38.49, 17.11) * mm, "end": v(-42.02, 13.58) * mm});
            skLineSegment(sketch, "E3.5.0.101", {"start": v(-39, 29.76) * mm, "end": v(-42.53, 26.22) * mm});
            skLineSegment(sketch, "E3.5.0.102", {"start": v(-38.98, 17.6) * mm, "end": v(-42.52, 14.07) * mm});
            skLineSegment(sketch, "E3.5.0.103", {"start": v(-42.02, 20.65) * mm, "end": v(-42.52, 20.15) * mm});
            skLineSegment(sketch, "E3.5.0.104", {"start": v(-38.45, -19.34) * mm, "end": v(-38.95, -19.84) * mm});
            skLineSegment(sketch, "E3.5.0.105", {"start": v(-38.46, -7.19) * mm, "end": v(-38.96, -7.69) * mm});
            skLineSegment(sketch, "E3.5.0.106", {"start": v(-38.48, 4.96) * mm, "end": v(-38.97, 4.46) * mm});
            skLineSegment(sketch, "E3.5.0.107", {"start": v(-38.44, -31.49) * mm, "end": v(-38.94, -31.99) * mm});
            skLineSegment(sketch, "E3.5.0.108", {"start": v(-38.5, 29.26) * mm, "end": v(-39, 29.76) * mm});
            skLineSegment(sketch, "E3.5.0.109", {"start": v(-38.49, 17.11) * mm, "end": v(-38.98, 17.6) * mm});
            skLineSegment(sketch, "E3.5.0.110", {"start": v(-42.02, 13.58) * mm, "end": v(-42.52, 14.07) * mm});
            skLineSegment(sketch, "E3.5.0.111", {"start": v(-42.03, 25.73) * mm, "end": v(-42.53, 26.22) * mm});
            skLineSegment(sketch, "E3.5.0.112", {"start": v(-42, -16.8) * mm, "end": v(-42.5, -16.3) * mm});
            skLineSegment(sketch, "E3.5.0.113", {"start": v(-42, -4.65) * mm, "end": v(-42.5, -4.15) * mm});
            skLineSegment(sketch, "E3.5.0.114", {"start": v(-41.98, -28.95) * mm, "end": v(-42.48, -28.45) * mm});
            skLineSegment(sketch, "E3.5.0.115", {"start": v(-38.5, 35.34) * mm, "end": v(-39, 35.83) * mm});
            skLineSegment(sketch, "E3.5.0.116", {"start": v(-42.04, 31.8) * mm, "end": v(-42.54, 32.3) * mm});
            skLineSegment(sketch, "E3.5.0.117", {"start": v(-42.05, 37.87) * mm, "end": v(-42.54, 38.37) * mm});
            skLineSegment(sketch, "E3.5.0.118", {"start": v(-42.03, 32.8) * mm, "end": v(-42.53, 32.3) * mm});
            skLineSegment(sketch, "E3.5.0.119", {"start": v(-38.5, 29.26) * mm, "end": v(-39, 28.76) * mm});
            skLineSegment(sketch, "E3.5.0.120", {"start": v(-38.49, 17.11) * mm, "end": v(-38.98, 16.61) * mm});
            skLineSegment(sketch, "E3.6.0.0", {"start": v(-36.65, 44.95) * mm, "end": v(-33.11, 41.41) * mm});
            skLineSegment(sketch, "E3.6.0.1", {"start": v(-37.14, 44.45) * mm, "end": v(-33.6, 40.91) * mm});
            skLineSegment(sketch, "E3.6.0.2", {"start": v(-36.65, 44.95) * mm, "end": v(-37.14, 44.45) * mm});
            skLineSegment(sketch, "E3.6.0.3", {"start": v(-33.03, -43.64) * mm, "end": v(-36.56, -47.17) * mm});
            skLineSegment(sketch, "E3.6.0.4", {"start": v(-33.53, -43.14) * mm, "end": v(-37.06, -46.68) * mm});
            skLineSegment(sketch, "E3.6.0.5", {"start": v(-36.56, -47.17) * mm, "end": v(-37.06, -46.68) * mm});
            skLineSegment(sketch, "E3.6.0.6", {"start": v(-36.61, 8.5) * mm, "end": v(-33.08, 4.96) * mm});
            skLineSegment(sketch, "E3.6.0.7", {"start": v(-33.03, -43.64) * mm, "end": v(-33.53, -43.14) * mm});
            skLineSegment(sketch, "E3.6.0.8", {"start": v(-33.08, 11.04) * mm, "end": v(-36.62, 7.5) * mm});
            skLineSegment(sketch, "E3.6.0.9", {"start": v(-33.03, -37.56) * mm, "end": v(-36.57, -41.1) * mm});
            skLineSegment(sketch, "E3.6.0.10", {"start": v(-33.05, -25.41) * mm, "end": v(-36.58, -28.95) * mm});
            skLineSegment(sketch, "E3.6.0.11", {"start": v(-33.58, 11.53) * mm, "end": v(-37.11, 8) * mm});
            skLineSegment(sketch, "E3.6.0.12", {"start": v(-33.6, 23.68) * mm, "end": v(-37.13, 20.15) * mm});
            skLineSegment(sketch, "E3.6.0.13", {"start": v(-36.6, 2.42) * mm, "end": v(-33.07, -1.11) * mm});
            skLineSegment(sketch, "E3.6.0.14", {"start": v(-36.62, 14.57) * mm, "end": v(-33.08, 11.04) * mm});
            skLineSegment(sketch, "E3.6.0.15", {"start": v(-36.63, 26.72) * mm, "end": v(-33.1, 23.19) * mm});
            skLineSegment(sketch, "E3.6.0.16", {"start": v(-36.57, -34.03) * mm, "end": v(-33.03, -37.56) * mm});
            skLineSegment(sketch, "E3.6.0.17", {"start": v(-36.58, -21.88) * mm, "end": v(-33.05, -25.41) * mm});
            skLineSegment(sketch, "E3.6.0.18", {"start": v(-36.6, -9.73) * mm, "end": v(-33.06, -13.26) * mm});
            skLineSegment(sketch, "E3.6.0.19", {"start": v(-33.06, -13.26) * mm, "end": v(-33.56, -13.76) * mm});
            skLineSegment(sketch, "E3.6.0.20", {"start": v(-33.07, -1.11) * mm, "end": v(-33.57, -1.61) * mm});
            skLineSegment(sketch, "E3.6.0.21", {"start": v(-33.08, 11.04) * mm, "end": v(-33.58, 10.54) * mm});
            skLineSegment(sketch, "E3.6.0.22", {"start": v(-33.1, 23.19) * mm, "end": v(-33.6, 22.69) * mm});
            skLineSegment(sketch, "E3.6.0.23", {"start": v(-33.03, -37.56) * mm, "end": v(-33.53, -38.06) * mm});
            skLineSegment(sketch, "E3.6.0.24", {"start": v(-33.05, -25.41) * mm, "end": v(-33.54, -25.91) * mm});
            skLineSegment(sketch, "E3.6.0.25", {"start": v(-33.06, -13.26) * mm, "end": v(-33.56, -12.77) * mm});
            skLineSegment(sketch, "E3.6.0.26", {"start": v(-33.07, -1.11) * mm, "end": v(-33.57, -0.62) * mm});
            skLineSegment(sketch, "E3.6.0.27", {"start": v(-33.08, 11.04) * mm, "end": v(-33.58, 11.53) * mm});
            skLineSegment(sketch, "E3.6.0.28", {"start": v(-33.1, 23.19) * mm, "end": v(-33.6, 23.68) * mm});
            skLineSegment(sketch, "E3.6.0.29", {"start": v(-33.03, -37.56) * mm, "end": v(-33.53, -37.07) * mm});
            skLineSegment(sketch, "E3.6.0.30", {"start": v(-33.05, -25.41) * mm, "end": v(-33.54, -24.92) * mm});
            skLineSegment(sketch, "E3.6.0.31", {"start": v(-36.62, 7.5) * mm, "end": v(-37.11, 8) * mm});
            skLineSegment(sketch, "E3.6.0.32", {"start": v(-33.11, 41.41) * mm, "end": v(-36.65, 37.87) * mm});
            skLineSegment(sketch, "E3.6.0.33", {"start": v(-33.6, 41.9) * mm, "end": v(-37.14, 38.37) * mm});
            skLineSegment(sketch, "E3.6.0.34", {"start": v(-33.11, 41.41) * mm, "end": v(-33.6, 41.9) * mm});
            skLineSegment(sketch, "E3.6.0.35", {"start": v(-37.14, 38.37) * mm, "end": v(-33.6, 34.84) * mm});
            skLineSegment(sketch, "E3.6.0.36", {"start": v(-36.64, 38.87) * mm, "end": v(-33.1, 35.34) * mm});
            skLineSegment(sketch, "E3.6.0.37", {"start": v(-37.06, -40.6) * mm, "end": v(-33.53, -44.14) * mm});
            skLineSegment(sketch, "E3.6.0.38", {"start": v(-37.1, 8) * mm, "end": v(-33.57, 4.46) * mm});
            skLineSegment(sketch, "E3.6.0.39", {"start": v(-33.05, -19.34) * mm, "end": v(-36.59, -22.87) * mm});
            skLineSegment(sketch, "E3.6.0.40", {"start": v(-33.06, -7.19) * mm, "end": v(-36.6, -10.72) * mm});
            skLineSegment(sketch, "E3.6.0.41", {"start": v(-33.08, 4.96) * mm, "end": v(-36.61, 1.43) * mm});
            skLineSegment(sketch, "E3.6.0.42", {"start": v(-33.04, -31.49) * mm, "end": v(-36.58, -35.02) * mm});
            skLineSegment(sketch, "E3.6.0.43", {"start": v(-33.55, -18.84) * mm, "end": v(-37.09, -22.38) * mm});
            skLineSegment(sketch, "E3.6.0.44", {"start": v(-33.56, -6.7) * mm, "end": v(-37.1, -10.23) * mm});
            skLineSegment(sketch, "E3.6.0.45", {"start": v(-33.57, 5.46) * mm, "end": v(-37.1, 1.92) * mm});
            skLineSegment(sketch, "E3.6.0.46", {"start": v(-33.54, -31) * mm, "end": v(-37.07, -34.53) * mm});
            skLineSegment(sketch, "E3.6.0.47", {"start": v(-36.59, -15.8) * mm, "end": v(-33.05, -19.34) * mm});
            skLineSegment(sketch, "E3.6.0.48", {"start": v(-36.6, -3.65) * mm, "end": v(-33.06, -7.19) * mm});
            skLineSegment(sketch, "E3.6.0.49", {"start": v(-36.63, 32.8) * mm, "end": v(-33.1, 29.26) * mm});
            skLineSegment(sketch, "E3.6.0.50", {"start": v(-36.56, -40.1) * mm, "end": v(-33.03, -43.64) * mm});
            skLineSegment(sketch, "E3.6.0.51", {"start": v(-36.58, -27.95) * mm, "end": v(-33.04, -31.49) * mm});
            skLineSegment(sketch, "E3.6.0.52", {"start": v(-36.62, 20.65) * mm, "end": v(-33.09, 17.11) * mm});
            skLineSegment(sketch, "E3.6.0.53", {"start": v(-36.59, -15.8) * mm, "end": v(-37.09, -16.3) * mm});
            skLineSegment(sketch, "E3.6.0.54", {"start": v(-36.6, -3.65) * mm, "end": v(-37.1, -4.15) * mm});
            skLineSegment(sketch, "E3.6.0.55", {"start": v(-36.61, 8.5) * mm, "end": v(-37.1, 8) * mm});
            skLineSegment(sketch, "E3.6.0.56", {"start": v(-36.56, -40.1) * mm, "end": v(-37.06, -40.6) * mm});
            skLineSegment(sketch, "E3.6.0.57", {"start": v(-36.58, -27.95) * mm, "end": v(-37.07, -28.45) * mm});
            skLineSegment(sketch, "E3.6.0.58", {"start": v(-33.03, -43.64) * mm, "end": v(-33.53, -44.14) * mm});
            skLineSegment(sketch, "E3.6.0.59", {"start": v(-33.05, -19.34) * mm, "end": v(-33.55, -18.84) * mm});
            skLineSegment(sketch, "E3.6.0.60", {"start": v(-33.06, -7.19) * mm, "end": v(-33.56, -6.7) * mm});
            skLineSegment(sketch, "E3.6.0.61", {"start": v(-33.08, 4.96) * mm, "end": v(-33.57, 5.46) * mm});
            skLineSegment(sketch, "E3.6.0.62", {"start": v(-33.04, -31.49) * mm, "end": v(-33.54, -31) * mm});
            skLineSegment(sketch, "E3.6.0.63", {"start": v(-36.61, 1.43) * mm, "end": v(-37.1, 1.92) * mm});
            skLineSegment(sketch, "E3.6.0.64", {"start": v(-36.58, -35.02) * mm, "end": v(-37.07, -34.53) * mm});
            skLineSegment(sketch, "E3.6.0.65", {"start": v(-36.59, -22.87) * mm, "end": v(-37.09, -22.38) * mm});
            skLineSegment(sketch, "E3.6.0.66", {"start": v(-36.6, -10.72) * mm, "end": v(-37.1, -10.23) * mm});
            skLineSegment(sketch, "E3.6.0.67", {"start": v(-37.1, 1.92) * mm, "end": v(-33.57, -1.61) * mm});
            skLineSegment(sketch, "E3.6.0.68", {"start": v(-37.11, 14.07) * mm, "end": v(-33.58, 10.54) * mm});
            skLineSegment(sketch, "E3.6.0.69", {"start": v(-37.13, 26.22) * mm, "end": v(-33.6, 22.69) * mm});
            skLineSegment(sketch, "E3.6.0.70", {"start": v(-36.65, 37.87) * mm, "end": v(-36.64, 31.8) * mm, "construction": true});
            skLineSegment(sketch, "E3.6.0.71", {"start": v(-37.07, -34.52) * mm, "end": v(-33.53, -38.06) * mm});
            skLineSegment(sketch, "E3.6.0.72", {"start": v(-37.08, -22.38) * mm, "end": v(-33.54, -25.91) * mm});
            skLineSegment(sketch, "E3.6.0.73", {"start": v(-37.1, -10.23) * mm, "end": v(-33.56, -13.76) * mm});
            skLineSegment(sketch, "E3.6.0.74", {"start": v(-33.07, -1.11) * mm, "end": v(-36.6, -4.65) * mm});
            skLineSegment(sketch, "E3.6.0.75", {"start": v(-33.1, 23.19) * mm, "end": v(-36.63, 19.65) * mm});
            skLineSegment(sketch, "E3.6.0.76", {"start": v(-33.06, -13.26) * mm, "end": v(-36.6, -16.8) * mm});
            skLineSegment(sketch, "E3.6.0.77", {"start": v(-33.57, -0.62) * mm, "end": v(-37.1, -4.15) * mm});
            skLineSegment(sketch, "E3.6.0.78", {"start": v(-33.53, -37.07) * mm, "end": v(-37.07, -40.6) * mm});
            skLineSegment(sketch, "E3.6.0.79", {"start": v(-33.54, -24.92) * mm, "end": v(-37.08, -28.45) * mm});
            skLineSegment(sketch, "E3.6.0.80", {"start": v(-33.56, -12.77) * mm, "end": v(-37.1, -16.3) * mm});
            skLineSegment(sketch, "E3.6.0.81", {"start": v(-36.6, 2.42) * mm, "end": v(-37.1, 1.92) * mm});
            skLineSegment(sketch, "E3.6.0.82", {"start": v(-36.62, 14.57) * mm, "end": v(-37.11, 14.07) * mm});
            skLineSegment(sketch, "E3.6.0.83", {"start": v(-36.63, 26.72) * mm, "end": v(-37.13, 26.22) * mm});
            skLineSegment(sketch, "E3.6.0.84", {"start": v(-36.57, -34.03) * mm, "end": v(-37.07, -34.52) * mm});
            skLineSegment(sketch, "E3.6.0.85", {"start": v(-36.58, -21.88) * mm, "end": v(-37.08, -22.38) * mm});
            skLineSegment(sketch, "E3.6.0.86", {"start": v(-36.6, -9.73) * mm, "end": v(-37.1, -10.23) * mm});
            skLineSegment(sketch, "E3.6.0.87", {"start": v(-36.63, 19.65) * mm, "end": v(-37.13, 20.15) * mm});
            skLineSegment(sketch, "E3.6.0.88", {"start": v(-36.57, -41.1) * mm, "end": v(-37.07, -40.6) * mm});
            skLineSegment(sketch, "E3.6.0.89", {"start": v(-33.1, 35.34) * mm, "end": v(-33.6, 34.84) * mm});
            skLineSegment(sketch, "E3.6.0.90", {"start": v(-33.11, 41.41) * mm, "end": v(-33.6, 40.91) * mm});
            skLineSegment(sketch, "E3.6.0.91", {"start": v(-33.1, 35.34) * mm, "end": v(-36.64, 31.8) * mm});
            skLineSegment(sketch, "E3.6.0.92", {"start": v(-33.6, 35.83) * mm, "end": v(-37.14, 32.3) * mm});
            skLineSegment(sketch, "E3.6.0.93", {"start": v(-36.64, 38.87) * mm, "end": v(-37.14, 38.37) * mm});
            skLineSegment(sketch, "E3.6.0.94", {"start": v(-37.07, -28.45) * mm, "end": v(-33.54, -31.99) * mm});
            skLineSegment(sketch, "E3.6.0.95", {"start": v(-37.13, 32.3) * mm, "end": v(-33.6, 28.76) * mm});
            skLineSegment(sketch, "E3.6.0.96", {"start": v(-37.09, -16.3) * mm, "end": v(-33.55, -19.84) * mm});
            skLineSegment(sketch, "E3.6.0.97", {"start": v(-37.1, -4.15) * mm, "end": v(-33.56, -7.69) * mm});
            skLineSegment(sketch, "E3.6.0.98", {"start": v(-37.12, 20.15) * mm, "end": v(-33.58, 16.61) * mm});
            skLineSegment(sketch, "E3.6.0.99", {"start": v(-33.1, 29.26) * mm, "end": v(-36.63, 25.73) * mm});
            skLineSegment(sketch, "E3.6.0.100", {"start": v(-33.09, 17.11) * mm, "end": v(-36.62, 13.58) * mm});
            skLineSegment(sketch, "E3.6.0.101", {"start": v(-33.6, 29.76) * mm, "end": v(-37.13, 26.22) * mm});
            skLineSegment(sketch, "E3.6.0.102", {"start": v(-33.58, 17.6) * mm, "end": v(-37.12, 14.07) * mm});
            skLineSegment(sketch, "E3.6.0.103", {"start": v(-36.62, 20.65) * mm, "end": v(-37.12, 20.15) * mm});
            skLineSegment(sketch, "E3.6.0.104", {"start": v(-33.05, -19.34) * mm, "end": v(-33.55, -19.84) * mm});
            skLineSegment(sketch, "E3.6.0.105", {"start": v(-33.06, -7.19) * mm, "end": v(-33.56, -7.69) * mm});
            skLineSegment(sketch, "E3.6.0.106", {"start": v(-33.08, 4.96) * mm, "end": v(-33.57, 4.46) * mm});
            skLineSegment(sketch, "E3.6.0.107", {"start": v(-33.04, -31.49) * mm, "end": v(-33.54, -31.99) * mm});
            skLineSegment(sketch, "E3.6.0.108", {"start": v(-33.1, 29.26) * mm, "end": v(-33.6, 29.76) * mm});
            skLineSegment(sketch, "E3.6.0.109", {"start": v(-33.09, 17.11) * mm, "end": v(-33.58, 17.6) * mm});
            skLineSegment(sketch, "E3.6.0.110", {"start": v(-36.62, 13.58) * mm, "end": v(-37.12, 14.07) * mm});
            skLineSegment(sketch, "E3.6.0.111", {"start": v(-36.63, 25.73) * mm, "end": v(-37.13, 26.22) * mm});
            skLineSegment(sketch, "E3.6.0.112", {"start": v(-36.6, -16.8) * mm, "end": v(-37.1, -16.3) * mm});
            skLineSegment(sketch, "E3.6.0.113", {"start": v(-36.6, -4.65) * mm, "end": v(-37.1, -4.15) * mm});
            skLineSegment(sketch, "E3.6.0.114", {"start": v(-36.58, -28.95) * mm, "end": v(-37.08, -28.45) * mm});
            skLineSegment(sketch, "E3.6.0.115", {"start": v(-33.1, 35.34) * mm, "end": v(-33.6, 35.83) * mm});
            skLineSegment(sketch, "E3.6.0.116", {"start": v(-36.64, 31.8) * mm, "end": v(-37.14, 32.3) * mm});
            skLineSegment(sketch, "E3.6.0.117", {"start": v(-36.65, 37.87) * mm, "end": v(-37.14, 38.37) * mm});
            skLineSegment(sketch, "E3.6.0.118", {"start": v(-36.63, 32.8) * mm, "end": v(-37.13, 32.3) * mm});
            skLineSegment(sketch, "E3.6.0.119", {"start": v(-33.1, 29.26) * mm, "end": v(-33.6, 28.76) * mm});
            skLineSegment(sketch, "E3.6.0.120", {"start": v(-33.09, 17.11) * mm, "end": v(-33.58, 16.61) * mm});
            skLineSegment(sketch, "E3.7.0.0", {"start": v(-31.25, 44.95) * mm, "end": v(-27.71, 41.41) * mm});
            skLineSegment(sketch, "E3.7.0.1", {"start": v(-31.74, 44.45) * mm, "end": v(-28.2, 40.91) * mm});
            skLineSegment(sketch, "E3.7.0.2", {"start": v(-31.25, 44.95) * mm, "end": v(-31.74, 44.45) * mm});
            skLineSegment(sketch, "E3.7.0.3", {"start": v(-27.63, -43.64) * mm, "end": v(-31.16, -47.17) * mm});
            skLineSegment(sketch, "E3.7.0.4", {"start": v(-28.13, -43.14) * mm, "end": v(-31.66, -46.68) * mm});
            skLineSegment(sketch, "E3.7.0.5", {"start": v(-31.16, -47.17) * mm, "end": v(-31.66, -46.68) * mm});
            skLineSegment(sketch, "E3.7.0.6", {"start": v(-31.21, 8.5) * mm, "end": v(-27.68, 4.96) * mm});
            skLineSegment(sketch, "E3.7.0.7", {"start": v(-27.63, -43.64) * mm, "end": v(-28.13, -43.14) * mm});
            skLineSegment(sketch, "E3.7.0.8", {"start": v(-27.68, 11.04) * mm, "end": v(-31.22, 7.5) * mm});
            skLineSegment(sketch, "E3.7.0.9", {"start": v(-27.63, -37.56) * mm, "end": v(-31.17, -41.1) * mm});
            skLineSegment(sketch, "E3.7.0.10", {"start": v(-27.65, -25.41) * mm, "end": v(-31.18, -28.95) * mm});
            skLineSegment(sketch, "E3.7.0.11", {"start": v(-28.18, 11.53) * mm, "end": v(-31.71, 8) * mm});
            skLineSegment(sketch, "E3.7.0.12", {"start": v(-28.2, 23.68) * mm, "end": v(-31.73, 20.15) * mm});
            skLineSegment(sketch, "E3.7.0.13", {"start": v(-31.2, 2.42) * mm, "end": v(-27.67, -1.11) * mm});
            skLineSegment(sketch, "E3.7.0.14", {"start": v(-31.22, 14.57) * mm, "end": v(-27.68, 11.04) * mm});
            skLineSegment(sketch, "E3.7.0.15", {"start": v(-31.23, 26.72) * mm, "end": v(-27.7, 23.19) * mm});
            skLineSegment(sketch, "E3.7.0.16", {"start": v(-31.17, -34.03) * mm, "end": v(-27.63, -37.56) * mm});
            skLineSegment(sketch, "E3.7.0.17", {"start": v(-31.18, -21.88) * mm, "end": v(-27.65, -25.41) * mm});
            skLineSegment(sketch, "E3.7.0.18", {"start": v(-31.2, -9.73) * mm, "end": v(-27.66, -13.26) * mm});
            skLineSegment(sketch, "E3.7.0.19", {"start": v(-27.66, -13.26) * mm, "end": v(-28.16, -13.76) * mm});
            skLineSegment(sketch, "E3.7.0.20", {"start": v(-27.67, -1.11) * mm, "end": v(-28.17, -1.61) * mm});
            skLineSegment(sketch, "E3.7.0.21", {"start": v(-27.68, 11.04) * mm, "end": v(-28.18, 10.54) * mm});
            skLineSegment(sketch, "E3.7.0.22", {"start": v(-27.7, 23.19) * mm, "end": v(-28.2, 22.69) * mm});
            skLineSegment(sketch, "E3.7.0.23", {"start": v(-27.63, -37.56) * mm, "end": v(-28.13, -38.06) * mm});
            skLineSegment(sketch, "E3.7.0.24", {"start": v(-27.65, -25.41) * mm, "end": v(-28.14, -25.91) * mm});
            skLineSegment(sketch, "E3.7.0.25", {"start": v(-27.66, -13.26) * mm, "end": v(-28.16, -12.77) * mm});
            skLineSegment(sketch, "E3.7.0.26", {"start": v(-27.67, -1.11) * mm, "end": v(-28.17, -0.62) * mm});
            skLineSegment(sketch, "E3.7.0.27", {"start": v(-27.68, 11.04) * mm, "end": v(-28.18, 11.53) * mm});
            skLineSegment(sketch, "E3.7.0.28", {"start": v(-27.7, 23.19) * mm, "end": v(-28.2, 23.68) * mm});
            skLineSegment(sketch, "E3.7.0.29", {"start": v(-27.63, -37.56) * mm, "end": v(-28.13, -37.07) * mm});
            skLineSegment(sketch, "E3.7.0.30", {"start": v(-27.65, -25.41) * mm, "end": v(-28.14, -24.92) * mm});
            skLineSegment(sketch, "E3.7.0.31", {"start": v(-31.22, 7.5) * mm, "end": v(-31.71, 8) * mm});
            skLineSegment(sketch, "E3.7.0.32", {"start": v(-27.71, 41.41) * mm, "end": v(-31.25, 37.87) * mm});
            skLineSegment(sketch, "E3.7.0.33", {"start": v(-28.2, 41.9) * mm, "end": v(-31.74, 38.37) * mm});
            skLineSegment(sketch, "E3.7.0.34", {"start": v(-27.71, 41.41) * mm, "end": v(-28.2, 41.9) * mm});
            skLineSegment(sketch, "E3.7.0.35", {"start": v(-31.74, 38.37) * mm, "end": v(-28.2, 34.84) * mm});
            skLineSegment(sketch, "E3.7.0.36", {"start": v(-31.24, 38.87) * mm, "end": v(-27.7, 35.34) * mm});
            skLineSegment(sketch, "E3.7.0.37", {"start": v(-31.66, -40.6) * mm, "end": v(-28.13, -44.14) * mm});
            skLineSegment(sketch, "E3.7.0.38", {"start": v(-31.7, 8) * mm, "end": v(-28.17, 4.46) * mm});
            skLineSegment(sketch, "E3.7.0.39", {"start": v(-27.65, -19.34) * mm, "end": v(-31.19, -22.87) * mm});
            skLineSegment(sketch, "E3.7.0.40", {"start": v(-27.66, -7.19) * mm, "end": v(-31.2, -10.72) * mm});
            skLineSegment(sketch, "E3.7.0.41", {"start": v(-27.68, 4.96) * mm, "end": v(-31.21, 1.43) * mm});
            skLineSegment(sketch, "E3.7.0.42", {"start": v(-27.64, -31.49) * mm, "end": v(-31.18, -35.02) * mm});
            skLineSegment(sketch, "E3.7.0.43", {"start": v(-28.15, -18.84) * mm, "end": v(-31.69, -22.38) * mm});
            skLineSegment(sketch, "E3.7.0.44", {"start": v(-28.16, -6.7) * mm, "end": v(-31.7, -10.23) * mm});
            skLineSegment(sketch, "E3.7.0.45", {"start": v(-28.17, 5.46) * mm, "end": v(-31.7, 1.92) * mm});
            skLineSegment(sketch, "E3.7.0.46", {"start": v(-28.14, -31) * mm, "end": v(-31.67, -34.53) * mm});
            skLineSegment(sketch, "E3.7.0.47", {"start": v(-31.19, -15.8) * mm, "end": v(-27.65, -19.34) * mm});
            skLineSegment(sketch, "E3.7.0.48", {"start": v(-31.2, -3.65) * mm, "end": v(-27.66, -7.19) * mm});
            skLineSegment(sketch, "E3.7.0.49", {"start": v(-31.23, 32.8) * mm, "end": v(-27.7, 29.26) * mm});
            skLineSegment(sketch, "E3.7.0.50", {"start": v(-31.16, -40.1) * mm, "end": v(-27.63, -43.64) * mm});
            skLineSegment(sketch, "E3.7.0.51", {"start": v(-31.18, -27.95) * mm, "end": v(-27.64, -31.49) * mm});
            skLineSegment(sketch, "E3.7.0.52", {"start": v(-31.22, 20.65) * mm, "end": v(-27.69, 17.11) * mm});
            skLineSegment(sketch, "E3.7.0.53", {"start": v(-31.19, -15.8) * mm, "end": v(-31.69, -16.3) * mm});
            skLineSegment(sketch, "E3.7.0.54", {"start": v(-31.2, -3.65) * mm, "end": v(-31.7, -4.15) * mm});
            skLineSegment(sketch, "E3.7.0.55", {"start": v(-31.21, 8.5) * mm, "end": v(-31.7, 8) * mm});
            skLineSegment(sketch, "E3.7.0.56", {"start": v(-31.16, -40.1) * mm, "end": v(-31.66, -40.6) * mm});
            skLineSegment(sketch, "E3.7.0.57", {"start": v(-31.18, -27.95) * mm, "end": v(-31.67, -28.45) * mm});
            skLineSegment(sketch, "E3.7.0.58", {"start": v(-27.63, -43.64) * mm, "end": v(-28.13, -44.14) * mm});
            skLineSegment(sketch, "E3.7.0.59", {"start": v(-27.65, -19.34) * mm, "end": v(-28.15, -18.84) * mm});
            skLineSegment(sketch, "E3.7.0.60", {"start": v(-27.66, -7.19) * mm, "end": v(-28.16, -6.7) * mm});
            skLineSegment(sketch, "E3.7.0.61", {"start": v(-27.68, 4.96) * mm, "end": v(-28.17, 5.46) * mm});
            skLineSegment(sketch, "E3.7.0.62", {"start": v(-27.64, -31.49) * mm, "end": v(-28.14, -31) * mm});
            skLineSegment(sketch, "E3.7.0.63", {"start": v(-31.21, 1.43) * mm, "end": v(-31.7, 1.92) * mm});
            skLineSegment(sketch, "E3.7.0.64", {"start": v(-31.18, -35.02) * mm, "end": v(-31.67, -34.53) * mm});
            skLineSegment(sketch, "E3.7.0.65", {"start": v(-31.19, -22.87) * mm, "end": v(-31.69, -22.38) * mm});
            skLineSegment(sketch, "E3.7.0.66", {"start": v(-31.2, -10.72) * mm, "end": v(-31.7, -10.23) * mm});
            skLineSegment(sketch, "E3.7.0.67", {"start": v(-31.7, 1.92) * mm, "end": v(-28.17, -1.61) * mm});
            skLineSegment(sketch, "E3.7.0.68", {"start": v(-31.71, 14.07) * mm, "end": v(-28.18, 10.54) * mm});
            skLineSegment(sketch, "E3.7.0.69", {"start": v(-31.73, 26.22) * mm, "end": v(-28.2, 22.69) * mm});
            skLineSegment(sketch, "E3.7.0.70", {"start": v(-31.25, 37.87) * mm, "end": v(-31.24, 31.8) * mm, "construction": true});
            skLineSegment(sketch, "E3.7.0.71", {"start": v(-31.67, -34.52) * mm, "end": v(-28.13, -38.06) * mm});
            skLineSegment(sketch, "E3.7.0.72", {"start": v(-31.68, -22.38) * mm, "end": v(-28.14, -25.91) * mm});
            skLineSegment(sketch, "E3.7.0.73", {"start": v(-31.7, -10.23) * mm, "end": v(-28.16, -13.76) * mm});
            skLineSegment(sketch, "E3.7.0.74", {"start": v(-27.67, -1.11) * mm, "end": v(-31.2, -4.65) * mm});
            skLineSegment(sketch, "E3.7.0.75", {"start": v(-27.7, 23.19) * mm, "end": v(-31.23, 19.65) * mm});
            skLineSegment(sketch, "E3.7.0.76", {"start": v(-27.66, -13.26) * mm, "end": v(-31.2, -16.8) * mm});
            skLineSegment(sketch, "E3.7.0.77", {"start": v(-28.17, -0.62) * mm, "end": v(-31.7, -4.15) * mm});
            skLineSegment(sketch, "E3.7.0.78", {"start": v(-28.13, -37.07) * mm, "end": v(-31.67, -40.6) * mm});
            skLineSegment(sketch, "E3.7.0.79", {"start": v(-28.14, -24.92) * mm, "end": v(-31.68, -28.45) * mm});
            skLineSegment(sketch, "E3.7.0.80", {"start": v(-28.16, -12.77) * mm, "end": v(-31.7, -16.3) * mm});
            skLineSegment(sketch, "E3.7.0.81", {"start": v(-31.2, 2.42) * mm, "end": v(-31.7, 1.92) * mm});
            skLineSegment(sketch, "E3.7.0.82", {"start": v(-31.22, 14.57) * mm, "end": v(-31.71, 14.07) * mm});
            skLineSegment(sketch, "E3.7.0.83", {"start": v(-31.23, 26.72) * mm, "end": v(-31.73, 26.22) * mm});
            skLineSegment(sketch, "E3.7.0.84", {"start": v(-31.17, -34.03) * mm, "end": v(-31.67, -34.52) * mm});
            skLineSegment(sketch, "E3.7.0.85", {"start": v(-31.18, -21.88) * mm, "end": v(-31.68, -22.38) * mm});
            skLineSegment(sketch, "E3.7.0.86", {"start": v(-31.2, -9.73) * mm, "end": v(-31.7, -10.23) * mm});
            skLineSegment(sketch, "E3.7.0.87", {"start": v(-31.23, 19.65) * mm, "end": v(-31.73, 20.15) * mm});
            skLineSegment(sketch, "E3.7.0.88", {"start": v(-31.17, -41.1) * mm, "end": v(-31.67, -40.6) * mm});
            skLineSegment(sketch, "E3.7.0.89", {"start": v(-27.7, 35.34) * mm, "end": v(-28.2, 34.84) * mm});
            skLineSegment(sketch, "E3.7.0.90", {"start": v(-27.71, 41.41) * mm, "end": v(-28.2, 40.91) * mm});
            skLineSegment(sketch, "E3.7.0.91", {"start": v(-27.7, 35.34) * mm, "end": v(-31.24, 31.8) * mm});
            skLineSegment(sketch, "E3.7.0.92", {"start": v(-28.2, 35.83) * mm, "end": v(-31.74, 32.3) * mm});
            skLineSegment(sketch, "E3.7.0.93", {"start": v(-31.24, 38.87) * mm, "end": v(-31.74, 38.37) * mm});
            skLineSegment(sketch, "E3.7.0.94", {"start": v(-31.67, -28.45) * mm, "end": v(-28.14, -31.99) * mm});
            skLineSegment(sketch, "E3.7.0.95", {"start": v(-31.73, 32.3) * mm, "end": v(-28.2, 28.76) * mm});
            skLineSegment(sketch, "E3.7.0.96", {"start": v(-31.69, -16.3) * mm, "end": v(-28.15, -19.84) * mm});
            skLineSegment(sketch, "E3.7.0.97", {"start": v(-31.7, -4.15) * mm, "end": v(-28.16, -7.69) * mm});
            skLineSegment(sketch, "E3.7.0.98", {"start": v(-31.72, 20.15) * mm, "end": v(-28.18, 16.61) * mm});
            skLineSegment(sketch, "E3.7.0.99", {"start": v(-27.7, 29.26) * mm, "end": v(-31.23, 25.73) * mm});
            skLineSegment(sketch, "E3.7.0.100", {"start": v(-27.69, 17.11) * mm, "end": v(-31.22, 13.58) * mm});
            skLineSegment(sketch, "E3.7.0.101", {"start": v(-28.2, 29.76) * mm, "end": v(-31.73, 26.22) * mm});
            skLineSegment(sketch, "E3.7.0.102", {"start": v(-28.18, 17.6) * mm, "end": v(-31.72, 14.07) * mm});
            skLineSegment(sketch, "E3.7.0.103", {"start": v(-31.22, 20.65) * mm, "end": v(-31.72, 20.15) * mm});
            skLineSegment(sketch, "E3.7.0.104", {"start": v(-27.65, -19.34) * mm, "end": v(-28.15, -19.84) * mm});
            skLineSegment(sketch, "E3.7.0.105", {"start": v(-27.66, -7.19) * mm, "end": v(-28.16, -7.69) * mm});
            skLineSegment(sketch, "E3.7.0.106", {"start": v(-27.68, 4.96) * mm, "end": v(-28.17, 4.46) * mm});
            skLineSegment(sketch, "E3.7.0.107", {"start": v(-27.64, -31.49) * mm, "end": v(-28.14, -31.99) * mm});
            skLineSegment(sketch, "E3.7.0.108", {"start": v(-27.7, 29.26) * mm, "end": v(-28.2, 29.76) * mm});
            skLineSegment(sketch, "E3.7.0.109", {"start": v(-27.69, 17.11) * mm, "end": v(-28.18, 17.6) * mm});
            skLineSegment(sketch, "E3.7.0.110", {"start": v(-31.22, 13.58) * mm, "end": v(-31.72, 14.07) * mm});
            skLineSegment(sketch, "E3.7.0.111", {"start": v(-31.23, 25.73) * mm, "end": v(-31.73, 26.22) * mm});
            skLineSegment(sketch, "E3.7.0.112", {"start": v(-31.2, -16.8) * mm, "end": v(-31.7, -16.3) * mm});
            skLineSegment(sketch, "E3.7.0.113", {"start": v(-31.2, -4.65) * mm, "end": v(-31.7, -4.15) * mm});
            skLineSegment(sketch, "E3.7.0.114", {"start": v(-31.18, -28.95) * mm, "end": v(-31.68, -28.45) * mm});
            skLineSegment(sketch, "E3.7.0.115", {"start": v(-27.7, 35.34) * mm, "end": v(-28.2, 35.83) * mm});
            skLineSegment(sketch, "E3.7.0.116", {"start": v(-31.24, 31.8) * mm, "end": v(-31.74, 32.3) * mm});
            skLineSegment(sketch, "E3.7.0.117", {"start": v(-31.25, 37.87) * mm, "end": v(-31.74, 38.37) * mm});
            skLineSegment(sketch, "E3.7.0.118", {"start": v(-31.23, 32.8) * mm, "end": v(-31.73, 32.3) * mm});
            skLineSegment(sketch, "E3.7.0.119", {"start": v(-27.7, 29.26) * mm, "end": v(-28.2, 28.76) * mm});
            skLineSegment(sketch, "E3.7.0.120", {"start": v(-27.69, 17.11) * mm, "end": v(-28.18, 16.61) * mm});
            skLineSegment(sketch, "E3.8.0.0", {"start": v(-25.85, 44.95) * mm, "end": v(-22.31, 41.41) * mm});
            skLineSegment(sketch, "E3.8.0.1", {"start": v(-26.34, 44.45) * mm, "end": v(-22.8, 40.91) * mm});
            skLineSegment(sketch, "E3.8.0.2", {"start": v(-25.85, 44.95) * mm, "end": v(-26.34, 44.45) * mm});
            skLineSegment(sketch, "E3.8.0.3", {"start": v(-22.23, -43.64) * mm, "end": v(-25.76, -47.17) * mm});
            skLineSegment(sketch, "E3.8.0.4", {"start": v(-22.73, -43.14) * mm, "end": v(-26.26, -46.68) * mm});
            skLineSegment(sketch, "E3.8.0.5", {"start": v(-25.76, -47.17) * mm, "end": v(-26.26, -46.68) * mm});
            skLineSegment(sketch, "E3.8.0.6", {"start": v(-25.81, 8.5) * mm, "end": v(-22.28, 4.96) * mm});
            skLineSegment(sketch, "E3.8.0.7", {"start": v(-22.23, -43.64) * mm, "end": v(-22.73, -43.14) * mm});
            skLineSegment(sketch, "E3.8.0.8", {"start": v(-22.28, 11.04) * mm, "end": v(-25.82, 7.5) * mm});
            skLineSegment(sketch, "E3.8.0.9", {"start": v(-22.23, -37.56) * mm, "end": v(-25.77, -41.1) * mm});
            skLineSegment(sketch, "E3.8.0.10", {"start": v(-22.25, -25.41) * mm, "end": v(-25.78, -28.95) * mm});
            skLineSegment(sketch, "E3.8.0.11", {"start": v(-22.78, 11.53) * mm, "end": v(-26.31, 8) * mm});
            skLineSegment(sketch, "E3.8.0.12", {"start": v(-22.8, 23.68) * mm, "end": v(-26.33, 20.15) * mm});
            skLineSegment(sketch, "E3.8.0.13", {"start": v(-25.8, 2.42) * mm, "end": v(-22.27, -1.11) * mm});
            skLineSegment(sketch, "E3.8.0.14", {"start": v(-25.82, 14.57) * mm, "end": v(-22.28, 11.04) * mm});
            skLineSegment(sketch, "E3.8.0.15", {"start": v(-25.83, 26.72) * mm, "end": v(-22.3, 23.19) * mm});
            skLineSegment(sketch, "E3.8.0.16", {"start": v(-25.77, -34.03) * mm, "end": v(-22.23, -37.56) * mm});
            skLineSegment(sketch, "E3.8.0.17", {"start": v(-25.78, -21.88) * mm, "end": v(-22.25, -25.41) * mm});
            skLineSegment(sketch, "E3.8.0.18", {"start": v(-25.8, -9.73) * mm, "end": v(-22.26, -13.26) * mm});
            skLineSegment(sketch, "E3.8.0.19", {"start": v(-22.26, -13.26) * mm, "end": v(-22.76, -13.76) * mm});
            skLineSegment(sketch, "E3.8.0.20", {"start": v(-22.27, -1.11) * mm, "end": v(-22.77, -1.61) * mm});
            skLineSegment(sketch, "E3.8.0.21", {"start": v(-22.28, 11.04) * mm, "end": v(-22.78, 10.54) * mm});
            skLineSegment(sketch, "E3.8.0.22", {"start": v(-22.3, 23.19) * mm, "end": v(-22.8, 22.69) * mm});
            skLineSegment(sketch, "E3.8.0.23", {"start": v(-22.23, -37.56) * mm, "end": v(-22.73, -38.06) * mm});
            skLineSegment(sketch, "E3.8.0.24", {"start": v(-22.25, -25.41) * mm, "end": v(-22.74, -25.91) * mm});
            skLineSegment(sketch, "E3.8.0.25", {"start": v(-22.26, -13.26) * mm, "end": v(-22.76, -12.77) * mm});
            skLineSegment(sketch, "E3.8.0.26", {"start": v(-22.27, -1.11) * mm, "end": v(-22.77, -0.62) * mm});
            skLineSegment(sketch, "E3.8.0.27", {"start": v(-22.28, 11.04) * mm, "end": v(-22.78, 11.53) * mm});
            skLineSegment(sketch, "E3.8.0.28", {"start": v(-22.3, 23.19) * mm, "end": v(-22.8, 23.68) * mm});
            skLineSegment(sketch, "E3.8.0.29", {"start": v(-22.23, -37.56) * mm, "end": v(-22.73, -37.07) * mm});
            skLineSegment(sketch, "E3.8.0.30", {"start": v(-22.25, -25.41) * mm, "end": v(-22.74, -24.92) * mm});
            skLineSegment(sketch, "E3.8.0.31", {"start": v(-25.82, 7.5) * mm, "end": v(-26.31, 8) * mm});
            skLineSegment(sketch, "E3.8.0.32", {"start": v(-22.31, 41.41) * mm, "end": v(-25.85, 37.87) * mm});
            skLineSegment(sketch, "E3.8.0.33", {"start": v(-22.8, 41.9) * mm, "end": v(-26.34, 38.37) * mm});
            skLineSegment(sketch, "E3.8.0.34", {"start": v(-22.31, 41.41) * mm, "end": v(-22.8, 41.9) * mm});
            skLineSegment(sketch, "E3.8.0.35", {"start": v(-26.34, 38.37) * mm, "end": v(-22.8, 34.84) * mm});
            skLineSegment(sketch, "E3.8.0.36", {"start": v(-25.84, 38.87) * mm, "end": v(-22.3, 35.34) * mm});
            skLineSegment(sketch, "E3.8.0.37", {"start": v(-26.26, -40.6) * mm, "end": v(-22.73, -44.14) * mm});
            skLineSegment(sketch, "E3.8.0.38", {"start": v(-26.3, 8) * mm, "end": v(-22.77, 4.46) * mm});
            skLineSegment(sketch, "E3.8.0.39", {"start": v(-22.25, -19.34) * mm, "end": v(-25.79, -22.87) * mm});
            skLineSegment(sketch, "E3.8.0.40", {"start": v(-22.26, -7.19) * mm, "end": v(-25.8, -10.72) * mm});
            skLineSegment(sketch, "E3.8.0.41", {"start": v(-22.28, 4.96) * mm, "end": v(-25.81, 1.43) * mm});
            skLineSegment(sketch, "E3.8.0.42", {"start": v(-22.24, -31.49) * mm, "end": v(-25.78, -35.02) * mm});
            skLineSegment(sketch, "E3.8.0.43", {"start": v(-22.75, -18.84) * mm, "end": v(-26.29, -22.38) * mm});
            skLineSegment(sketch, "E3.8.0.44", {"start": v(-22.76, -6.7) * mm, "end": v(-26.3, -10.23) * mm});
            skLineSegment(sketch, "E3.8.0.45", {"start": v(-22.77, 5.46) * mm, "end": v(-26.3, 1.92) * mm});
            skLineSegment(sketch, "E3.8.0.46", {"start": v(-22.74, -31) * mm, "end": v(-26.27, -34.53) * mm});
            skLineSegment(sketch, "E3.8.0.47", {"start": v(-25.79, -15.8) * mm, "end": v(-22.25, -19.34) * mm});
            skLineSegment(sketch, "E3.8.0.48", {"start": v(-25.8, -3.65) * mm, "end": v(-22.26, -7.19) * mm});
            skLineSegment(sketch, "E3.8.0.49", {"start": v(-25.83, 32.8) * mm, "end": v(-22.3, 29.26) * mm});
            skLineSegment(sketch, "E3.8.0.50", {"start": v(-25.76, -40.1) * mm, "end": v(-22.23, -43.64) * mm});
            skLineSegment(sketch, "E3.8.0.51", {"start": v(-25.78, -27.95) * mm, "end": v(-22.24, -31.49) * mm});
            skLineSegment(sketch, "E3.8.0.52", {"start": v(-25.82, 20.65) * mm, "end": v(-22.29, 17.11) * mm});
            skLineSegment(sketch, "E3.8.0.53", {"start": v(-25.79, -15.8) * mm, "end": v(-26.29, -16.3) * mm});
            skLineSegment(sketch, "E3.8.0.54", {"start": v(-25.8, -3.65) * mm, "end": v(-26.3, -4.15) * mm});
            skLineSegment(sketch, "E3.8.0.55", {"start": v(-25.81, 8.5) * mm, "end": v(-26.3, 8) * mm});
            skLineSegment(sketch, "E3.8.0.56", {"start": v(-25.76, -40.1) * mm, "end": v(-26.26, -40.6) * mm});
            skLineSegment(sketch, "E3.8.0.57", {"start": v(-25.78, -27.95) * mm, "end": v(-26.27, -28.45) * mm});
            skLineSegment(sketch, "E3.8.0.58", {"start": v(-22.23, -43.64) * mm, "end": v(-22.73, -44.14) * mm});
            skLineSegment(sketch, "E3.8.0.59", {"start": v(-22.25, -19.34) * mm, "end": v(-22.75, -18.84) * mm});
            skLineSegment(sketch, "E3.8.0.60", {"start": v(-22.26, -7.19) * mm, "end": v(-22.76, -6.7) * mm});
            skLineSegment(sketch, "E3.8.0.61", {"start": v(-22.28, 4.96) * mm, "end": v(-22.77, 5.46) * mm});
            skLineSegment(sketch, "E3.8.0.62", {"start": v(-22.24, -31.49) * mm, "end": v(-22.74, -31) * mm});
            skLineSegment(sketch, "E3.8.0.63", {"start": v(-25.81, 1.43) * mm, "end": v(-26.3, 1.92) * mm});
            skLineSegment(sketch, "E3.8.0.64", {"start": v(-25.78, -35.02) * mm, "end": v(-26.27, -34.53) * mm});
            skLineSegment(sketch, "E3.8.0.65", {"start": v(-25.79, -22.87) * mm, "end": v(-26.29, -22.38) * mm});
            skLineSegment(sketch, "E3.8.0.66", {"start": v(-25.8, -10.72) * mm, "end": v(-26.3, -10.23) * mm});
            skLineSegment(sketch, "E3.8.0.67", {"start": v(-26.3, 1.92) * mm, "end": v(-22.77, -1.61) * mm});
            skLineSegment(sketch, "E3.8.0.68", {"start": v(-26.31, 14.07) * mm, "end": v(-22.78, 10.54) * mm});
            skLineSegment(sketch, "E3.8.0.69", {"start": v(-26.33, 26.22) * mm, "end": v(-22.8, 22.69) * mm});
            skLineSegment(sketch, "E3.8.0.70", {"start": v(-25.85, 37.87) * mm, "end": v(-25.84, 31.8) * mm, "construction": true});
            skLineSegment(sketch, "E3.8.0.71", {"start": v(-26.27, -34.52) * mm, "end": v(-22.73, -38.06) * mm});
            skLineSegment(sketch, "E3.8.0.72", {"start": v(-26.28, -22.38) * mm, "end": v(-22.74, -25.91) * mm});
            skLineSegment(sketch, "E3.8.0.73", {"start": v(-26.3, -10.23) * mm, "end": v(-22.76, -13.76) * mm});
            skLineSegment(sketch, "E3.8.0.74", {"start": v(-22.27, -1.11) * mm, "end": v(-25.8, -4.65) * mm});
            skLineSegment(sketch, "E3.8.0.75", {"start": v(-22.3, 23.19) * mm, "end": v(-25.83, 19.65) * mm});
            skLineSegment(sketch, "E3.8.0.76", {"start": v(-22.26, -13.26) * mm, "end": v(-25.8, -16.8) * mm});
            skLineSegment(sketch, "E3.8.0.77", {"start": v(-22.77, -0.62) * mm, "end": v(-26.3, -4.15) * mm});
            skLineSegment(sketch, "E3.8.0.78", {"start": v(-22.73, -37.07) * mm, "end": v(-26.27, -40.6) * mm});
            skLineSegment(sketch, "E3.8.0.79", {"start": v(-22.74, -24.92) * mm, "end": v(-26.28, -28.45) * mm});
            skLineSegment(sketch, "E3.8.0.80", {"start": v(-22.76, -12.77) * mm, "end": v(-26.3, -16.3) * mm});
            skLineSegment(sketch, "E3.8.0.81", {"start": v(-25.8, 2.42) * mm, "end": v(-26.3, 1.92) * mm});
            skLineSegment(sketch, "E3.8.0.82", {"start": v(-25.82, 14.57) * mm, "end": v(-26.31, 14.07) * mm});
            skLineSegment(sketch, "E3.8.0.83", {"start": v(-25.83, 26.72) * mm, "end": v(-26.33, 26.22) * mm});
            skLineSegment(sketch, "E3.8.0.84", {"start": v(-25.77, -34.03) * mm, "end": v(-26.27, -34.52) * mm});
            skLineSegment(sketch, "E3.8.0.85", {"start": v(-25.78, -21.88) * mm, "end": v(-26.28, -22.38) * mm});
            skLineSegment(sketch, "E3.8.0.86", {"start": v(-25.8, -9.73) * mm, "end": v(-26.3, -10.23) * mm});
            skLineSegment(sketch, "E3.8.0.87", {"start": v(-25.83, 19.65) * mm, "end": v(-26.33, 20.15) * mm});
            skLineSegment(sketch, "E3.8.0.88", {"start": v(-25.77, -41.1) * mm, "end": v(-26.27, -40.6) * mm});
            skLineSegment(sketch, "E3.8.0.89", {"start": v(-22.3, 35.34) * mm, "end": v(-22.8, 34.84) * mm});
            skLineSegment(sketch, "E3.8.0.90", {"start": v(-22.31, 41.41) * mm, "end": v(-22.8, 40.91) * mm});
            skLineSegment(sketch, "E3.8.0.91", {"start": v(-22.3, 35.34) * mm, "end": v(-25.84, 31.8) * mm});
            skLineSegment(sketch, "E3.8.0.92", {"start": v(-22.8, 35.83) * mm, "end": v(-26.34, 32.3) * mm});
            skLineSegment(sketch, "E3.8.0.93", {"start": v(-25.84, 38.87) * mm, "end": v(-26.34, 38.37) * mm});
            skLineSegment(sketch, "E3.8.0.94", {"start": v(-26.27, -28.45) * mm, "end": v(-22.74, -31.99) * mm});
            skLineSegment(sketch, "E3.8.0.95", {"start": v(-26.33, 32.3) * mm, "end": v(-22.8, 28.76) * mm});
            skLineSegment(sketch, "E3.8.0.96", {"start": v(-26.29, -16.3) * mm, "end": v(-22.75, -19.84) * mm});
            skLineSegment(sketch, "E3.8.0.97", {"start": v(-26.3, -4.15) * mm, "end": v(-22.76, -7.69) * mm});
            skLineSegment(sketch, "E3.8.0.98", {"start": v(-26.32, 20.15) * mm, "end": v(-22.78, 16.61) * mm});
            skLineSegment(sketch, "E3.8.0.99", {"start": v(-22.3, 29.26) * mm, "end": v(-25.83, 25.73) * mm});
            skLineSegment(sketch, "E3.8.0.100", {"start": v(-22.29, 17.11) * mm, "end": v(-25.82, 13.58) * mm});
            skLineSegment(sketch, "E3.8.0.101", {"start": v(-22.8, 29.76) * mm, "end": v(-26.33, 26.22) * mm});
            skLineSegment(sketch, "E3.8.0.102", {"start": v(-22.78, 17.6) * mm, "end": v(-26.32, 14.07) * mm});
            skLineSegment(sketch, "E3.8.0.103", {"start": v(-25.82, 20.65) * mm, "end": v(-26.32, 20.15) * mm});
            skLineSegment(sketch, "E3.8.0.104", {"start": v(-22.25, -19.34) * mm, "end": v(-22.75, -19.84) * mm});
            skLineSegment(sketch, "E3.8.0.105", {"start": v(-22.26, -7.19) * mm, "end": v(-22.76, -7.69) * mm});
            skLineSegment(sketch, "E3.8.0.106", {"start": v(-22.28, 4.96) * mm, "end": v(-22.77, 4.46) * mm});
            skLineSegment(sketch, "E3.8.0.107", {"start": v(-22.24, -31.49) * mm, "end": v(-22.74, -31.99) * mm});
            skLineSegment(sketch, "E3.8.0.108", {"start": v(-22.3, 29.26) * mm, "end": v(-22.8, 29.76) * mm});
            skLineSegment(sketch, "E3.8.0.109", {"start": v(-22.29, 17.11) * mm, "end": v(-22.78, 17.6) * mm});
            skLineSegment(sketch, "E3.8.0.110", {"start": v(-25.82, 13.58) * mm, "end": v(-26.32, 14.07) * mm});
            skLineSegment(sketch, "E3.8.0.111", {"start": v(-25.83, 25.73) * mm, "end": v(-26.33, 26.22) * mm});
            skLineSegment(sketch, "E3.8.0.112", {"start": v(-25.8, -16.8) * mm, "end": v(-26.3, -16.3) * mm});
            skLineSegment(sketch, "E3.8.0.113", {"start": v(-25.8, -4.65) * mm, "end": v(-26.3, -4.15) * mm});
            skLineSegment(sketch, "E3.8.0.114", {"start": v(-25.78, -28.95) * mm, "end": v(-26.28, -28.45) * mm});
            skLineSegment(sketch, "E3.8.0.115", {"start": v(-22.3, 35.34) * mm, "end": v(-22.8, 35.83) * mm});
            skLineSegment(sketch, "E3.8.0.116", {"start": v(-25.84, 31.8) * mm, "end": v(-26.34, 32.3) * mm});
            skLineSegment(sketch, "E3.8.0.117", {"start": v(-25.85, 37.87) * mm, "end": v(-26.34, 38.37) * mm});
            skLineSegment(sketch, "E3.8.0.118", {"start": v(-25.83, 32.8) * mm, "end": v(-26.33, 32.3) * mm});
            skLineSegment(sketch, "E3.8.0.119", {"start": v(-22.3, 29.26) * mm, "end": v(-22.8, 28.76) * mm});
            skLineSegment(sketch, "E3.8.0.120", {"start": v(-22.29, 17.11) * mm, "end": v(-22.78, 16.61) * mm});
            skLineSegment(sketch, "E3.9.0.0", {"start": v(-20.45, 44.95) * mm, "end": v(-16.91, 41.41) * mm});
            skLineSegment(sketch, "E3.9.0.1", {"start": v(-20.94, 44.45) * mm, "end": v(-17.4, 40.91) * mm});
            skLineSegment(sketch, "E3.9.0.2", {"start": v(-20.45, 44.95) * mm, "end": v(-20.94, 44.45) * mm});
            skLineSegment(sketch, "E3.9.0.3", {"start": v(-16.83, -43.64) * mm, "end": v(-20.36, -47.17) * mm});
            skLineSegment(sketch, "E3.9.0.4", {"start": v(-17.33, -43.14) * mm, "end": v(-20.86, -46.68) * mm});
            skLineSegment(sketch, "E3.9.0.5", {"start": v(-20.36, -47.17) * mm, "end": v(-20.86, -46.68) * mm});
            skLineSegment(sketch, "E3.9.0.6", {"start": v(-20.41, 8.5) * mm, "end": v(-16.88, 4.96) * mm});
            skLineSegment(sketch, "E3.9.0.7", {"start": v(-16.83, -43.64) * mm, "end": v(-17.33, -43.14) * mm});
            skLineSegment(sketch, "E3.9.0.8", {"start": v(-16.88, 11.04) * mm, "end": v(-20.42, 7.5) * mm});
            skLineSegment(sketch, "E3.9.0.9", {"start": v(-16.83, -37.56) * mm, "end": v(-20.37, -41.1) * mm});
            skLineSegment(sketch, "E3.9.0.10", {"start": v(-16.85, -25.41) * mm, "end": v(-20.38, -28.95) * mm});
            skLineSegment(sketch, "E3.9.0.11", {"start": v(-17.38, 11.53) * mm, "end": v(-20.91, 8) * mm});
            skLineSegment(sketch, "E3.9.0.12", {"start": v(-17.4, 23.68) * mm, "end": v(-20.93, 20.15) * mm});
            skLineSegment(sketch, "E3.9.0.13", {"start": v(-20.4, 2.42) * mm, "end": v(-16.87, -1.11) * mm});
            skLineSegment(sketch, "E3.9.0.14", {"start": v(-20.42, 14.57) * mm, "end": v(-16.88, 11.04) * mm});
            skLineSegment(sketch, "E3.9.0.15", {"start": v(-20.43, 26.72) * mm, "end": v(-16.9, 23.19) * mm});
            skLineSegment(sketch, "E3.9.0.16", {"start": v(-20.37, -34.03) * mm, "end": v(-16.83, -37.56) * mm});
            skLineSegment(sketch, "E3.9.0.17", {"start": v(-20.38, -21.88) * mm, "end": v(-16.85, -25.41) * mm});
            skLineSegment(sketch, "E3.9.0.18", {"start": v(-20.4, -9.73) * mm, "end": v(-16.86, -13.26) * mm});
            skLineSegment(sketch, "E3.9.0.19", {"start": v(-16.86, -13.26) * mm, "end": v(-17.36, -13.76) * mm});
            skLineSegment(sketch, "E3.9.0.20", {"start": v(-16.87, -1.11) * mm, "end": v(-17.37, -1.61) * mm});
            skLineSegment(sketch, "E3.9.0.21", {"start": v(-16.88, 11.04) * mm, "end": v(-17.38, 10.54) * mm});
            skLineSegment(sketch, "E3.9.0.22", {"start": v(-16.9, 23.19) * mm, "end": v(-17.4, 22.69) * mm});
            skLineSegment(sketch, "E3.9.0.23", {"start": v(-16.83, -37.56) * mm, "end": v(-17.33, -38.06) * mm});
            skLineSegment(sketch, "E3.9.0.24", {"start": v(-16.85, -25.41) * mm, "end": v(-17.34, -25.91) * mm});
            skLineSegment(sketch, "E3.9.0.25", {"start": v(-16.86, -13.26) * mm, "end": v(-17.36, -12.77) * mm});
            skLineSegment(sketch, "E3.9.0.26", {"start": v(-16.87, -1.11) * mm, "end": v(-17.37, -0.62) * mm});
            skLineSegment(sketch, "E3.9.0.27", {"start": v(-16.88, 11.04) * mm, "end": v(-17.38, 11.53) * mm});
            skLineSegment(sketch, "E3.9.0.28", {"start": v(-16.9, 23.19) * mm, "end": v(-17.4, 23.68) * mm});
            skLineSegment(sketch, "E3.9.0.29", {"start": v(-16.83, -37.56) * mm, "end": v(-17.33, -37.07) * mm});
            skLineSegment(sketch, "E3.9.0.30", {"start": v(-16.85, -25.41) * mm, "end": v(-17.34, -24.92) * mm});
            skLineSegment(sketch, "E3.9.0.31", {"start": v(-20.42, 7.5) * mm, "end": v(-20.91, 8) * mm});
            skLineSegment(sketch, "E3.9.0.32", {"start": v(-16.91, 41.41) * mm, "end": v(-20.45, 37.87) * mm});
            skLineSegment(sketch, "E3.9.0.33", {"start": v(-17.4, 41.9) * mm, "end": v(-20.94, 38.37) * mm});
            skLineSegment(sketch, "E3.9.0.34", {"start": v(-16.91, 41.41) * mm, "end": v(-17.4, 41.9) * mm});
            skLineSegment(sketch, "E3.9.0.35", {"start": v(-20.94, 38.37) * mm, "end": v(-17.4, 34.84) * mm});
            skLineSegment(sketch, "E3.9.0.36", {"start": v(-20.44, 38.87) * mm, "end": v(-16.9, 35.34) * mm});
            skLineSegment(sketch, "E3.9.0.37", {"start": v(-20.86, -40.6) * mm, "end": v(-17.33, -44.14) * mm});
            skLineSegment(sketch, "E3.9.0.38", {"start": v(-20.9, 8) * mm, "end": v(-17.37, 4.46) * mm});
            skLineSegment(sketch, "E3.9.0.39", {"start": v(-16.85, -19.34) * mm, "end": v(-20.39, -22.87) * mm});
            skLineSegment(sketch, "E3.9.0.40", {"start": v(-16.86, -7.19) * mm, "end": v(-20.4, -10.72) * mm});
            skLineSegment(sketch, "E3.9.0.41", {"start": v(-16.88, 4.96) * mm, "end": v(-20.41, 1.43) * mm});
            skLineSegment(sketch, "E3.9.0.42", {"start": v(-16.84, -31.49) * mm, "end": v(-20.38, -35.02) * mm});
            skLineSegment(sketch, "E3.9.0.43", {"start": v(-17.35, -18.84) * mm, "end": v(-20.89, -22.38) * mm});
            skLineSegment(sketch, "E3.9.0.44", {"start": v(-17.36, -6.7) * mm, "end": v(-20.9, -10.23) * mm});
            skLineSegment(sketch, "E3.9.0.45", {"start": v(-17.37, 5.46) * mm, "end": v(-20.9, 1.92) * mm});
            skLineSegment(sketch, "E3.9.0.46", {"start": v(-17.34, -31) * mm, "end": v(-20.87, -34.53) * mm});
            skLineSegment(sketch, "E3.9.0.47", {"start": v(-20.39, -15.8) * mm, "end": v(-16.85, -19.34) * mm});
            skLineSegment(sketch, "E3.9.0.48", {"start": v(-20.4, -3.65) * mm, "end": v(-16.86, -7.19) * mm});
            skLineSegment(sketch, "E3.9.0.49", {"start": v(-20.43, 32.8) * mm, "end": v(-16.9, 29.26) * mm});
            skLineSegment(sketch, "E3.9.0.50", {"start": v(-20.36, -40.1) * mm, "end": v(-16.83, -43.64) * mm});
            skLineSegment(sketch, "E3.9.0.51", {"start": v(-20.38, -27.95) * mm, "end": v(-16.84, -31.49) * mm});
            skLineSegment(sketch, "E3.9.0.52", {"start": v(-20.42, 20.65) * mm, "end": v(-16.89, 17.11) * mm});
            skLineSegment(sketch, "E3.9.0.53", {"start": v(-20.39, -15.8) * mm, "end": v(-20.89, -16.3) * mm});
            skLineSegment(sketch, "E3.9.0.54", {"start": v(-20.4, -3.65) * mm, "end": v(-20.9, -4.15) * mm});
            skLineSegment(sketch, "E3.9.0.55", {"start": v(-20.41, 8.5) * mm, "end": v(-20.9, 8) * mm});
            skLineSegment(sketch, "E3.9.0.56", {"start": v(-20.36, -40.1) * mm, "end": v(-20.86, -40.6) * mm});
            skLineSegment(sketch, "E3.9.0.57", {"start": v(-20.38, -27.95) * mm, "end": v(-20.87, -28.45) * mm});
            skLineSegment(sketch, "E3.9.0.58", {"start": v(-16.83, -43.64) * mm, "end": v(-17.33, -44.14) * mm});
            skLineSegment(sketch, "E3.9.0.59", {"start": v(-16.85, -19.34) * mm, "end": v(-17.35, -18.84) * mm});
            skLineSegment(sketch, "E3.9.0.60", {"start": v(-16.86, -7.19) * mm, "end": v(-17.36, -6.7) * mm});
            skLineSegment(sketch, "E3.9.0.61", {"start": v(-16.88, 4.96) * mm, "end": v(-17.37, 5.46) * mm});
            skLineSegment(sketch, "E3.9.0.62", {"start": v(-16.84, -31.49) * mm, "end": v(-17.34, -31) * mm});
            skLineSegment(sketch, "E3.9.0.63", {"start": v(-20.41, 1.43) * mm, "end": v(-20.9, 1.92) * mm});
            skLineSegment(sketch, "E3.9.0.64", {"start": v(-20.38, -35.02) * mm, "end": v(-20.87, -34.53) * mm});
            skLineSegment(sketch, "E3.9.0.65", {"start": v(-20.39, -22.87) * mm, "end": v(-20.89, -22.38) * mm});
            skLineSegment(sketch, "E3.9.0.66", {"start": v(-20.4, -10.72) * mm, "end": v(-20.9, -10.23) * mm});
            skLineSegment(sketch, "E3.9.0.67", {"start": v(-20.9, 1.92) * mm, "end": v(-17.37, -1.61) * mm});
            skLineSegment(sketch, "E3.9.0.68", {"start": v(-20.91, 14.07) * mm, "end": v(-17.38, 10.54) * mm});
            skLineSegment(sketch, "E3.9.0.69", {"start": v(-20.93, 26.22) * mm, "end": v(-17.4, 22.69) * mm});
            skLineSegment(sketch, "E3.9.0.70", {"start": v(-20.45, 37.87) * mm, "end": v(-20.44, 31.8) * mm, "construction": true});
            skLineSegment(sketch, "E3.9.0.71", {"start": v(-20.87, -34.52) * mm, "end": v(-17.33, -38.06) * mm});
            skLineSegment(sketch, "E3.9.0.72", {"start": v(-20.88, -22.38) * mm, "end": v(-17.34, -25.91) * mm});
            skLineSegment(sketch, "E3.9.0.73", {"start": v(-20.9, -10.23) * mm, "end": v(-17.36, -13.76) * mm});
            skLineSegment(sketch, "E3.9.0.74", {"start": v(-16.87, -1.11) * mm, "end": v(-20.4, -4.65) * mm});
            skLineSegment(sketch, "E3.9.0.75", {"start": v(-16.9, 23.19) * mm, "end": v(-20.43, 19.65) * mm});
            skLineSegment(sketch, "E3.9.0.76", {"start": v(-16.86, -13.26) * mm, "end": v(-20.4, -16.8) * mm});
            skLineSegment(sketch, "E3.9.0.77", {"start": v(-17.37, -0.62) * mm, "end": v(-20.9, -4.15) * mm});
            skLineSegment(sketch, "E3.9.0.78", {"start": v(-17.33, -37.07) * mm, "end": v(-20.87, -40.6) * mm});
            skLineSegment(sketch, "E3.9.0.79", {"start": v(-17.34, -24.92) * mm, "end": v(-20.88, -28.45) * mm});
            skLineSegment(sketch, "E3.9.0.80", {"start": v(-17.36, -12.77) * mm, "end": v(-20.9, -16.3) * mm});
            skLineSegment(sketch, "E3.9.0.81", {"start": v(-20.4, 2.42) * mm, "end": v(-20.9, 1.92) * mm});
            skLineSegment(sketch, "E3.9.0.82", {"start": v(-20.42, 14.57) * mm, "end": v(-20.91, 14.07) * mm});
            skLineSegment(sketch, "E3.9.0.83", {"start": v(-20.43, 26.72) * mm, "end": v(-20.93, 26.22) * mm});
            skLineSegment(sketch, "E3.9.0.84", {"start": v(-20.37, -34.03) * mm, "end": v(-20.87, -34.52) * mm});
            skLineSegment(sketch, "E3.9.0.85", {"start": v(-20.38, -21.88) * mm, "end": v(-20.88, -22.38) * mm});
            skLineSegment(sketch, "E3.9.0.86", {"start": v(-20.4, -9.73) * mm, "end": v(-20.9, -10.23) * mm});
            skLineSegment(sketch, "E3.9.0.87", {"start": v(-20.43, 19.65) * mm, "end": v(-20.93, 20.15) * mm});
            skLineSegment(sketch, "E3.9.0.88", {"start": v(-20.37, -41.1) * mm, "end": v(-20.87, -40.6) * mm});
            skLineSegment(sketch, "E3.9.0.89", {"start": v(-16.9, 35.34) * mm, "end": v(-17.4, 34.84) * mm});
            skLineSegment(sketch, "E3.9.0.90", {"start": v(-16.91, 41.41) * mm, "end": v(-17.4, 40.91) * mm});
            skLineSegment(sketch, "E3.9.0.91", {"start": v(-16.9, 35.34) * mm, "end": v(-20.44, 31.8) * mm});
            skLineSegment(sketch, "E3.9.0.92", {"start": v(-17.4, 35.83) * mm, "end": v(-20.94, 32.3) * mm});
            skLineSegment(sketch, "E3.9.0.93", {"start": v(-20.44, 38.87) * mm, "end": v(-20.94, 38.37) * mm});
            skLineSegment(sketch, "E3.9.0.94", {"start": v(-20.87, -28.45) * mm, "end": v(-17.34, -31.99) * mm});
            skLineSegment(sketch, "E3.9.0.95", {"start": v(-20.93, 32.3) * mm, "end": v(-17.4, 28.76) * mm});
            skLineSegment(sketch, "E3.9.0.96", {"start": v(-20.89, -16.3) * mm, "end": v(-17.35, -19.84) * mm});
            skLineSegment(sketch, "E3.9.0.97", {"start": v(-20.9, -4.15) * mm, "end": v(-17.36, -7.69) * mm});
            skLineSegment(sketch, "E3.9.0.98", {"start": v(-20.92, 20.15) * mm, "end": v(-17.38, 16.61) * mm});
            skLineSegment(sketch, "E3.9.0.99", {"start": v(-16.9, 29.26) * mm, "end": v(-20.43, 25.73) * mm});
            skLineSegment(sketch, "E3.9.0.100", {"start": v(-16.89, 17.11) * mm, "end": v(-20.42, 13.58) * mm});
            skLineSegment(sketch, "E3.9.0.101", {"start": v(-17.4, 29.76) * mm, "end": v(-20.93, 26.22) * mm});
            skLineSegment(sketch, "E3.9.0.102", {"start": v(-17.38, 17.6) * mm, "end": v(-20.92, 14.07) * mm});
            skLineSegment(sketch, "E3.9.0.103", {"start": v(-20.42, 20.65) * mm, "end": v(-20.92, 20.15) * mm});
            skLineSegment(sketch, "E3.9.0.104", {"start": v(-16.85, -19.34) * mm, "end": v(-17.35, -19.84) * mm});
            skLineSegment(sketch, "E3.9.0.105", {"start": v(-16.86, -7.19) * mm, "end": v(-17.36, -7.69) * mm});
            skLineSegment(sketch, "E3.9.0.106", {"start": v(-16.88, 4.96) * mm, "end": v(-17.37, 4.46) * mm});
            skLineSegment(sketch, "E3.9.0.107", {"start": v(-16.84, -31.49) * mm, "end": v(-17.34, -31.99) * mm});
            skLineSegment(sketch, "E3.9.0.108", {"start": v(-16.9, 29.26) * mm, "end": v(-17.4, 29.76) * mm});
            skLineSegment(sketch, "E3.9.0.109", {"start": v(-16.89, 17.11) * mm, "end": v(-17.38, 17.6) * mm});
            skLineSegment(sketch, "E3.9.0.110", {"start": v(-20.42, 13.58) * mm, "end": v(-20.92, 14.07) * mm});
            skLineSegment(sketch, "E3.9.0.111", {"start": v(-20.43, 25.73) * mm, "end": v(-20.93, 26.22) * mm});
            skLineSegment(sketch, "E3.9.0.112", {"start": v(-20.4, -16.8) * mm, "end": v(-20.9, -16.3) * mm});
            skLineSegment(sketch, "E3.9.0.113", {"start": v(-20.4, -4.65) * mm, "end": v(-20.9, -4.15) * mm});
            skLineSegment(sketch, "E3.9.0.114", {"start": v(-20.38, -28.95) * mm, "end": v(-20.88, -28.45) * mm});
            skLineSegment(sketch, "E3.9.0.115", {"start": v(-16.9, 35.34) * mm, "end": v(-17.4, 35.83) * mm});
            skLineSegment(sketch, "E3.9.0.116", {"start": v(-20.44, 31.8) * mm, "end": v(-20.94, 32.3) * mm});
            skLineSegment(sketch, "E3.9.0.117", {"start": v(-20.45, 37.87) * mm, "end": v(-20.94, 38.37) * mm});
            skLineSegment(sketch, "E3.9.0.118", {"start": v(-20.43, 32.8) * mm, "end": v(-20.93, 32.3) * mm});
            skLineSegment(sketch, "E3.9.0.119", {"start": v(-16.9, 29.26) * mm, "end": v(-17.4, 28.76) * mm});
            skLineSegment(sketch, "E3.9.0.120", {"start": v(-16.89, 17.11) * mm, "end": v(-17.38, 16.61) * mm});
            skLineSegment(sketch, "E3.10.0.0", {"start": v(-15.05, 44.95) * mm, "end": v(-11.51, 41.41) * mm});
            skLineSegment(sketch, "E3.10.0.1", {"start": v(-15.54, 44.45) * mm, "end": v(-12, 40.91) * mm});
            skLineSegment(sketch, "E3.10.0.2", {"start": v(-15.05, 44.95) * mm, "end": v(-15.54, 44.45) * mm});
            skLineSegment(sketch, "E3.10.0.3", {"start": v(-11.43, -43.64) * mm, "end": v(-14.96, -47.17) * mm});
            skLineSegment(sketch, "E3.10.0.4", {"start": v(-11.93, -43.14) * mm, "end": v(-15.46, -46.68) * mm});
            skLineSegment(sketch, "E3.10.0.5", {"start": v(-14.96, -47.17) * mm, "end": v(-15.46, -46.68) * mm});
            skLineSegment(sketch, "E3.10.0.6", {"start": v(-15.01, 8.5) * mm, "end": v(-11.48, 4.96) * mm});
            skLineSegment(sketch, "E3.10.0.7", {"start": v(-11.43, -43.64) * mm, "end": v(-11.93, -43.14) * mm});
            skLineSegment(sketch, "E3.10.0.8", {"start": v(-11.48, 11.04) * mm, "end": v(-15.02, 7.5) * mm});
            skLineSegment(sketch, "E3.10.0.9", {"start": v(-11.43, -37.56) * mm, "end": v(-14.97, -41.1) * mm});
            skLineSegment(sketch, "E3.10.0.10", {"start": v(-11.45, -25.41) * mm, "end": v(-14.98, -28.95) * mm});
            skLineSegment(sketch, "E3.10.0.11", {"start": v(-11.98, 11.53) * mm, "end": v(-15.51, 8) * mm});
            skLineSegment(sketch, "E3.10.0.12", {"start": v(-12, 23.68) * mm, "end": v(-15.53, 20.15) * mm});
            skLineSegment(sketch, "E3.10.0.13", {"start": v(-15, 2.42) * mm, "end": v(-11.47, -1.11) * mm});
            skLineSegment(sketch, "E3.10.0.14", {"start": v(-15.02, 14.57) * mm, "end": v(-11.48, 11.04) * mm});
            skLineSegment(sketch, "E3.10.0.15", {"start": v(-15.03, 26.72) * mm, "end": v(-11.5, 23.19) * mm});
            skLineSegment(sketch, "E3.10.0.16", {"start": v(-14.97, -34.03) * mm, "end": v(-11.43, -37.56) * mm});
            skLineSegment(sketch, "E3.10.0.17", {"start": v(-14.98, -21.88) * mm, "end": v(-11.45, -25.41) * mm});
            skLineSegment(sketch, "E3.10.0.18", {"start": v(-15, -9.73) * mm, "end": v(-11.46, -13.26) * mm});
            skLineSegment(sketch, "E3.10.0.19", {"start": v(-11.46, -13.26) * mm, "end": v(-11.96, -13.76) * mm});
            skLineSegment(sketch, "E3.10.0.20", {"start": v(-11.47, -1.11) * mm, "end": v(-11.97, -1.61) * mm});
            skLineSegment(sketch, "E3.10.0.21", {"start": v(-11.48, 11.04) * mm, "end": v(-11.98, 10.54) * mm});
            skLineSegment(sketch, "E3.10.0.22", {"start": v(-11.5, 23.19) * mm, "end": v(-12, 22.69) * mm});
            skLineSegment(sketch, "E3.10.0.23", {"start": v(-11.43, -37.56) * mm, "end": v(-11.93, -38.06) * mm});
            skLineSegment(sketch, "E3.10.0.24", {"start": v(-11.45, -25.41) * mm, "end": v(-11.94, -25.91) * mm});
            skLineSegment(sketch, "E3.10.0.25", {"start": v(-11.46, -13.26) * mm, "end": v(-11.96, -12.77) * mm});
            skLineSegment(sketch, "E3.10.0.26", {"start": v(-11.47, -1.11) * mm, "end": v(-11.97, -0.62) * mm});
            skLineSegment(sketch, "E3.10.0.27", {"start": v(-11.48, 11.04) * mm, "end": v(-11.98, 11.53) * mm});
            skLineSegment(sketch, "E3.10.0.28", {"start": v(-11.5, 23.19) * mm, "end": v(-12, 23.68) * mm});
            skLineSegment(sketch, "E3.10.0.29", {"start": v(-11.43, -37.56) * mm, "end": v(-11.93, -37.07) * mm});
            skLineSegment(sketch, "E3.10.0.30", {"start": v(-11.45, -25.41) * mm, "end": v(-11.94, -24.92) * mm});
            skLineSegment(sketch, "E3.10.0.31", {"start": v(-15.02, 7.5) * mm, "end": v(-15.51, 8) * mm});
            skLineSegment(sketch, "E3.10.0.32", {"start": v(-11.51, 41.41) * mm, "end": v(-15.05, 37.87) * mm});
            skLineSegment(sketch, "E3.10.0.33", {"start": v(-12, 41.9) * mm, "end": v(-15.54, 38.37) * mm});
            skLineSegment(sketch, "E3.10.0.34", {"start": v(-11.51, 41.41) * mm, "end": v(-12, 41.9) * mm});
            skLineSegment(sketch, "E3.10.0.35", {"start": v(-15.54, 38.37) * mm, "end": v(-12, 34.84) * mm});
            skLineSegment(sketch, "E3.10.0.36", {"start": v(-15.04, 38.87) * mm, "end": v(-11.5, 35.34) * mm});
            skLineSegment(sketch, "E3.10.0.37", {"start": v(-15.46, -40.6) * mm, "end": v(-11.93, -44.14) * mm});
            skLineSegment(sketch, "E3.10.0.38", {"start": v(-15.5, 8) * mm, "end": v(-11.97, 4.46) * mm});
            skLineSegment(sketch, "E3.10.0.39", {"start": v(-11.45, -19.34) * mm, "end": v(-14.99, -22.87) * mm});
            skLineSegment(sketch, "E3.10.0.40", {"start": v(-11.46, -7.19) * mm, "end": v(-15, -10.72) * mm});
            skLineSegment(sketch, "E3.10.0.41", {"start": v(-11.48, 4.96) * mm, "end": v(-15.01, 1.43) * mm});
            skLineSegment(sketch, "E3.10.0.42", {"start": v(-11.44, -31.49) * mm, "end": v(-14.98, -35.02) * mm});
            skLineSegment(sketch, "E3.10.0.43", {"start": v(-11.95, -18.84) * mm, "end": v(-15.49, -22.38) * mm});
            skLineSegment(sketch, "E3.10.0.44", {"start": v(-11.96, -6.7) * mm, "end": v(-15.5, -10.23) * mm});
            skLineSegment(sketch, "E3.10.0.45", {"start": v(-11.97, 5.46) * mm, "end": v(-15.5, 1.92) * mm});
            skLineSegment(sketch, "E3.10.0.46", {"start": v(-11.94, -31) * mm, "end": v(-15.47, -34.53) * mm});
            skLineSegment(sketch, "E3.10.0.47", {"start": v(-14.99, -15.8) * mm, "end": v(-11.45, -19.34) * mm});
            skLineSegment(sketch, "E3.10.0.48", {"start": v(-15, -3.65) * mm, "end": v(-11.46, -7.19) * mm});
            skLineSegment(sketch, "E3.10.0.49", {"start": v(-15.03, 32.8) * mm, "end": v(-11.5, 29.26) * mm});
            skLineSegment(sketch, "E3.10.0.50", {"start": v(-14.96, -40.1) * mm, "end": v(-11.43, -43.64) * mm});
            skLineSegment(sketch, "E3.10.0.51", {"start": v(-14.98, -27.95) * mm, "end": v(-11.44, -31.49) * mm});
            skLineSegment(sketch, "E3.10.0.52", {"start": v(-15.02, 20.65) * mm, "end": v(-11.49, 17.11) * mm});
            skLineSegment(sketch, "E3.10.0.53", {"start": v(-14.99, -15.8) * mm, "end": v(-15.49, -16.3) * mm});
            skLineSegment(sketch, "E3.10.0.54", {"start": v(-15, -3.65) * mm, "end": v(-15.5, -4.15) * mm});
            skLineSegment(sketch, "E3.10.0.55", {"start": v(-15.01, 8.5) * mm, "end": v(-15.5, 8) * mm});
            skLineSegment(sketch, "E3.10.0.56", {"start": v(-14.96, -40.1) * mm, "end": v(-15.46, -40.6) * mm});
            skLineSegment(sketch, "E3.10.0.57", {"start": v(-14.98, -27.95) * mm, "end": v(-15.47, -28.45) * mm});
            skLineSegment(sketch, "E3.10.0.58", {"start": v(-11.43, -43.64) * mm, "end": v(-11.93, -44.14) * mm});
            skLineSegment(sketch, "E3.10.0.59", {"start": v(-11.45, -19.34) * mm, "end": v(-11.95, -18.84) * mm});
            skLineSegment(sketch, "E3.10.0.60", {"start": v(-11.46, -7.19) * mm, "end": v(-11.96, -6.7) * mm});
            skLineSegment(sketch, "E3.10.0.61", {"start": v(-11.48, 4.96) * mm, "end": v(-11.97, 5.46) * mm});
            skLineSegment(sketch, "E3.10.0.62", {"start": v(-11.44, -31.49) * mm, "end": v(-11.94, -31) * mm});
            skLineSegment(sketch, "E3.10.0.63", {"start": v(-15.01, 1.43) * mm, "end": v(-15.5, 1.92) * mm});
            skLineSegment(sketch, "E3.10.0.64", {"start": v(-14.98, -35.02) * mm, "end": v(-15.47, -34.53) * mm});
            skLineSegment(sketch, "E3.10.0.65", {"start": v(-14.99, -22.87) * mm, "end": v(-15.49, -22.38) * mm});
            skLineSegment(sketch, "E3.10.0.66", {"start": v(-15, -10.72) * mm, "end": v(-15.5, -10.23) * mm});
            skLineSegment(sketch, "E3.10.0.67", {"start": v(-15.5, 1.92) * mm, "end": v(-11.97, -1.61) * mm});
            skLineSegment(sketch, "E3.10.0.68", {"start": v(-15.51, 14.07) * mm, "end": v(-11.98, 10.54) * mm});
            skLineSegment(sketch, "E3.10.0.69", {"start": v(-15.53, 26.22) * mm, "end": v(-12, 22.69) * mm});
            skLineSegment(sketch, "E3.10.0.70", {"start": v(-15.05, 37.87) * mm, "end": v(-15.04, 31.8) * mm, "construction": true});
            skLineSegment(sketch, "E3.10.0.71", {"start": v(-15.47, -34.52) * mm, "end": v(-11.93, -38.06) * mm});
            skLineSegment(sketch, "E3.10.0.72", {"start": v(-15.48, -22.38) * mm, "end": v(-11.94, -25.91) * mm});
            skLineSegment(sketch, "E3.10.0.73", {"start": v(-15.5, -10.23) * mm, "end": v(-11.96, -13.76) * mm});
            skLineSegment(sketch, "E3.10.0.74", {"start": v(-11.47, -1.11) * mm, "end": v(-15, -4.65) * mm});
            skLineSegment(sketch, "E3.10.0.75", {"start": v(-11.5, 23.19) * mm, "end": v(-15.03, 19.65) * mm});
            skLineSegment(sketch, "E3.10.0.76", {"start": v(-11.46, -13.26) * mm, "end": v(-15, -16.8) * mm});
            skLineSegment(sketch, "E3.10.0.77", {"start": v(-11.97, -0.62) * mm, "end": v(-15.5, -4.15) * mm});
            skLineSegment(sketch, "E3.10.0.78", {"start": v(-11.93, -37.07) * mm, "end": v(-15.47, -40.6) * mm});
            skLineSegment(sketch, "E3.10.0.79", {"start": v(-11.94, -24.92) * mm, "end": v(-15.48, -28.45) * mm});
            skLineSegment(sketch, "E3.10.0.80", {"start": v(-11.96, -12.77) * mm, "end": v(-15.5, -16.3) * mm});
            skLineSegment(sketch, "E3.10.0.81", {"start": v(-15, 2.42) * mm, "end": v(-15.5, 1.92) * mm});
            skLineSegment(sketch, "E3.10.0.82", {"start": v(-15.02, 14.57) * mm, "end": v(-15.51, 14.07) * mm});
            skLineSegment(sketch, "E3.10.0.83", {"start": v(-15.03, 26.72) * mm, "end": v(-15.53, 26.22) * mm});
            skLineSegment(sketch, "E3.10.0.84", {"start": v(-14.97, -34.03) * mm, "end": v(-15.47, -34.52) * mm});
            skLineSegment(sketch, "E3.10.0.85", {"start": v(-14.98, -21.88) * mm, "end": v(-15.48, -22.38) * mm});
            skLineSegment(sketch, "E3.10.0.86", {"start": v(-15, -9.73) * mm, "end": v(-15.5, -10.23) * mm});
            skLineSegment(sketch, "E3.10.0.87", {"start": v(-15.03, 19.65) * mm, "end": v(-15.53, 20.15) * mm});
            skLineSegment(sketch, "E3.10.0.88", {"start": v(-14.97, -41.1) * mm, "end": v(-15.47, -40.6) * mm});
            skLineSegment(sketch, "E3.10.0.89", {"start": v(-11.5, 35.34) * mm, "end": v(-12, 34.84) * mm});
            skLineSegment(sketch, "E3.10.0.90", {"start": v(-11.51, 41.41) * mm, "end": v(-12, 40.91) * mm});
            skLineSegment(sketch, "E3.10.0.91", {"start": v(-11.5, 35.34) * mm, "end": v(-15.04, 31.8) * mm});
            skLineSegment(sketch, "E3.10.0.92", {"start": v(-12, 35.83) * mm, "end": v(-15.54, 32.3) * mm});
            skLineSegment(sketch, "E3.10.0.93", {"start": v(-15.04, 38.87) * mm, "end": v(-15.54, 38.37) * mm});
            skLineSegment(sketch, "E3.10.0.94", {"start": v(-15.47, -28.45) * mm, "end": v(-11.94, -31.99) * mm});
            skLineSegment(sketch, "E3.10.0.95", {"start": v(-15.53, 32.3) * mm, "end": v(-12, 28.76) * mm});
            skLineSegment(sketch, "E3.10.0.96", {"start": v(-15.49, -16.3) * mm, "end": v(-11.95, -19.84) * mm});
            skLineSegment(sketch, "E3.10.0.97", {"start": v(-15.5, -4.15) * mm, "end": v(-11.96, -7.69) * mm});
            skLineSegment(sketch, "E3.10.0.98", {"start": v(-15.52, 20.15) * mm, "end": v(-11.98, 16.61) * mm});
            skLineSegment(sketch, "E3.10.0.99", {"start": v(-11.5, 29.26) * mm, "end": v(-15.03, 25.73) * mm});
            skLineSegment(sketch, "E3.10.0.100", {"start": v(-11.49, 17.11) * mm, "end": v(-15.02, 13.58) * mm});
            skLineSegment(sketch, "E3.10.0.101", {"start": v(-12, 29.76) * mm, "end": v(-15.53, 26.22) * mm});
            skLineSegment(sketch, "E3.10.0.102", {"start": v(-11.98, 17.6) * mm, "end": v(-15.52, 14.07) * mm});
            skLineSegment(sketch, "E3.10.0.103", {"start": v(-15.02, 20.65) * mm, "end": v(-15.52, 20.15) * mm});
            skLineSegment(sketch, "E3.10.0.104", {"start": v(-11.45, -19.34) * mm, "end": v(-11.95, -19.84) * mm});
            skLineSegment(sketch, "E3.10.0.105", {"start": v(-11.46, -7.19) * mm, "end": v(-11.96, -7.69) * mm});
            skLineSegment(sketch, "E3.10.0.106", {"start": v(-11.48, 4.96) * mm, "end": v(-11.97, 4.46) * mm});
            skLineSegment(sketch, "E3.10.0.107", {"start": v(-11.44, -31.49) * mm, "end": v(-11.94, -31.99) * mm});
            skLineSegment(sketch, "E3.10.0.108", {"start": v(-11.5, 29.26) * mm, "end": v(-12, 29.76) * mm});
            skLineSegment(sketch, "E3.10.0.109", {"start": v(-11.49, 17.11) * mm, "end": v(-11.98, 17.6) * mm});
            skLineSegment(sketch, "E3.10.0.110", {"start": v(-15.02, 13.58) * mm, "end": v(-15.52, 14.07) * mm});
            skLineSegment(sketch, "E3.10.0.111", {"start": v(-15.03, 25.73) * mm, "end": v(-15.53, 26.22) * mm});
            skLineSegment(sketch, "E3.10.0.112", {"start": v(-15, -16.8) * mm, "end": v(-15.5, -16.3) * mm});
            skLineSegment(sketch, "E3.10.0.113", {"start": v(-15, -4.65) * mm, "end": v(-15.5, -4.15) * mm});
            skLineSegment(sketch, "E3.10.0.114", {"start": v(-14.98, -28.95) * mm, "end": v(-15.48, -28.45) * mm});
            skLineSegment(sketch, "E3.10.0.115", {"start": v(-11.5, 35.34) * mm, "end": v(-12, 35.83) * mm});
            skLineSegment(sketch, "E3.10.0.116", {"start": v(-15.04, 31.8) * mm, "end": v(-15.54, 32.3) * mm});
            skLineSegment(sketch, "E3.10.0.117", {"start": v(-15.05, 37.87) * mm, "end": v(-15.54, 38.37) * mm});
            skLineSegment(sketch, "E3.10.0.118", {"start": v(-15.03, 32.8) * mm, "end": v(-15.53, 32.3) * mm});
            skLineSegment(sketch, "E3.10.0.119", {"start": v(-11.5, 29.26) * mm, "end": v(-12, 28.76) * mm});
            skLineSegment(sketch, "E3.10.0.120", {"start": v(-11.49, 17.11) * mm, "end": v(-11.98, 16.61) * mm});
            skLineSegment(sketch, "E3.11.0.0", {"start": v(-9.65, 44.95) * mm, "end": v(-6.11, 41.41) * mm});
            skLineSegment(sketch, "E3.11.0.1", {"start": v(-10.14, 44.45) * mm, "end": v(-6.6, 40.91) * mm});
            skLineSegment(sketch, "E3.11.0.2", {"start": v(-9.65, 44.95) * mm, "end": v(-10.14, 44.45) * mm});
            skLineSegment(sketch, "E3.11.0.3", {"start": v(-6.03, -43.64) * mm, "end": v(-9.56, -47.17) * mm});
            skLineSegment(sketch, "E3.11.0.4", {"start": v(-6.53, -43.14) * mm, "end": v(-10.06, -46.68) * mm});
            skLineSegment(sketch, "E3.11.0.5", {"start": v(-9.56, -47.17) * mm, "end": v(-10.06, -46.68) * mm});
            skLineSegment(sketch, "E3.11.0.6", {"start": v(-9.61, 8.5) * mm, "end": v(-6.08, 4.96) * mm});
            skLineSegment(sketch, "E3.11.0.7", {"start": v(-6.03, -43.64) * mm, "end": v(-6.53, -43.14) * mm});
            skLineSegment(sketch, "E3.11.0.8", {"start": v(-6.08, 11.04) * mm, "end": v(-9.62, 7.5) * mm});
            skLineSegment(sketch, "E3.11.0.9", {"start": v(-6.03, -37.56) * mm, "end": v(-9.57, -41.1) * mm});
            skLineSegment(sketch, "E3.11.0.10", {"start": v(-6.05, -25.41) * mm, "end": v(-9.58, -28.95) * mm});
            skLineSegment(sketch, "E3.11.0.11", {"start": v(-6.58, 11.53) * mm, "end": v(-10.11, 8) * mm});
            skLineSegment(sketch, "E3.11.0.12", {"start": v(-6.6, 23.68) * mm, "end": v(-10.13, 20.15) * mm});
            skLineSegment(sketch, "E3.11.0.13", {"start": v(-9.6, 2.42) * mm, "end": v(-6.07, -1.11) * mm});
            skLineSegment(sketch, "E3.11.0.14", {"start": v(-9.62, 14.57) * mm, "end": v(-6.08, 11.04) * mm});
            skLineSegment(sketch, "E3.11.0.15", {"start": v(-9.63, 26.72) * mm, "end": v(-6.1, 23.19) * mm});
            skLineSegment(sketch, "E3.11.0.16", {"start": v(-9.57, -34.03) * mm, "end": v(-6.03, -37.56) * mm});
            skLineSegment(sketch, "E3.11.0.17", {"start": v(-9.58, -21.88) * mm, "end": v(-6.05, -25.41) * mm});
            skLineSegment(sketch, "E3.11.0.18", {"start": v(-9.6, -9.73) * mm, "end": v(-6.06, -13.26) * mm});
            skLineSegment(sketch, "E3.11.0.19", {"start": v(-6.06, -13.26) * mm, "end": v(-6.56, -13.76) * mm});
            skLineSegment(sketch, "E3.11.0.20", {"start": v(-6.07, -1.11) * mm, "end": v(-6.57, -1.61) * mm});
            skLineSegment(sketch, "E3.11.0.21", {"start": v(-6.08, 11.04) * mm, "end": v(-6.58, 10.54) * mm});
            skLineSegment(sketch, "E3.11.0.22", {"start": v(-6.1, 23.19) * mm, "end": v(-6.6, 22.69) * mm});
            skLineSegment(sketch, "E3.11.0.23", {"start": v(-6.03, -37.56) * mm, "end": v(-6.53, -38.06) * mm});
            skLineSegment(sketch, "E3.11.0.24", {"start": v(-6.05, -25.41) * mm, "end": v(-6.54, -25.91) * mm});
            skLineSegment(sketch, "E3.11.0.25", {"start": v(-6.06, -13.26) * mm, "end": v(-6.56, -12.77) * mm});
            skLineSegment(sketch, "E3.11.0.26", {"start": v(-6.07, -1.11) * mm, "end": v(-6.57, -0.62) * mm});
            skLineSegment(sketch, "E3.11.0.27", {"start": v(-6.08, 11.04) * mm, "end": v(-6.58, 11.53) * mm});
            skLineSegment(sketch, "E3.11.0.28", {"start": v(-6.1, 23.19) * mm, "end": v(-6.6, 23.68) * mm});
            skLineSegment(sketch, "E3.11.0.29", {"start": v(-6.03, -37.56) * mm, "end": v(-6.53, -37.07) * mm});
            skLineSegment(sketch, "E3.11.0.30", {"start": v(-6.05, -25.41) * mm, "end": v(-6.54, -24.92) * mm});
            skLineSegment(sketch, "E3.11.0.31", {"start": v(-9.62, 7.5) * mm, "end": v(-10.11, 8) * mm});
            skLineSegment(sketch, "E3.11.0.32", {"start": v(-6.11, 41.41) * mm, "end": v(-9.65, 37.87) * mm});
            skLineSegment(sketch, "E3.11.0.33", {"start": v(-6.6, 41.9) * mm, "end": v(-10.14, 38.37) * mm});
            skLineSegment(sketch, "E3.11.0.34", {"start": v(-6.11, 41.41) * mm, "end": v(-6.6, 41.9) * mm});
            skLineSegment(sketch, "E3.11.0.35", {"start": v(-10.14, 38.37) * mm, "end": v(-6.6, 34.84) * mm});
            skLineSegment(sketch, "E3.11.0.36", {"start": v(-9.64, 38.87) * mm, "end": v(-6.1, 35.34) * mm});
            skLineSegment(sketch, "E3.11.0.37", {"start": v(-10.06, -40.6) * mm, "end": v(-6.53, -44.14) * mm});
            skLineSegment(sketch, "E3.11.0.38", {"start": v(-10.1, 8) * mm, "end": v(-6.57, 4.46) * mm});
            skLineSegment(sketch, "E3.11.0.39", {"start": v(-6.05, -19.34) * mm, "end": v(-9.59, -22.87) * mm});
            skLineSegment(sketch, "E3.11.0.40", {"start": v(-6.06, -7.19) * mm, "end": v(-9.6, -10.72) * mm});
            skLineSegment(sketch, "E3.11.0.41", {"start": v(-6.08, 4.96) * mm, "end": v(-9.61, 1.43) * mm});
            skLineSegment(sketch, "E3.11.0.42", {"start": v(-6.04, -31.49) * mm, "end": v(-9.58, -35.02) * mm});
            skLineSegment(sketch, "E3.11.0.43", {"start": v(-6.55, -18.84) * mm, "end": v(-10.09, -22.38) * mm});
            skLineSegment(sketch, "E3.11.0.44", {"start": v(-6.56, -6.7) * mm, "end": v(-10.1, -10.23) * mm});
            skLineSegment(sketch, "E3.11.0.45", {"start": v(-6.57, 5.46) * mm, "end": v(-10.1, 1.92) * mm});
            skLineSegment(sketch, "E3.11.0.46", {"start": v(-6.54, -31) * mm, "end": v(-10.07, -34.53) * mm});
            skLineSegment(sketch, "E3.11.0.47", {"start": v(-9.59, -15.8) * mm, "end": v(-6.05, -19.34) * mm});
            skLineSegment(sketch, "E3.11.0.48", {"start": v(-9.6, -3.65) * mm, "end": v(-6.06, -7.19) * mm});
            skLineSegment(sketch, "E3.11.0.49", {"start": v(-9.63, 32.8) * mm, "end": v(-6.1, 29.26) * mm});
            skLineSegment(sketch, "E3.11.0.50", {"start": v(-9.56, -40.1) * mm, "end": v(-6.03, -43.64) * mm});
            skLineSegment(sketch, "E3.11.0.51", {"start": v(-9.58, -27.95) * mm, "end": v(-6.04, -31.49) * mm});
            skLineSegment(sketch, "E3.11.0.52", {"start": v(-9.62, 20.65) * mm, "end": v(-6.09, 17.11) * mm});
            skLineSegment(sketch, "E3.11.0.53", {"start": v(-9.59, -15.8) * mm, "end": v(-10.09, -16.3) * mm});
            skLineSegment(sketch, "E3.11.0.54", {"start": v(-9.6, -3.65) * mm, "end": v(-10.1, -4.15) * mm});
            skLineSegment(sketch, "E3.11.0.55", {"start": v(-9.61, 8.5) * mm, "end": v(-10.1, 8) * mm});
            skLineSegment(sketch, "E3.11.0.56", {"start": v(-9.56, -40.1) * mm, "end": v(-10.06, -40.6) * mm});
            skLineSegment(sketch, "E3.11.0.57", {"start": v(-9.58, -27.95) * mm, "end": v(-10.07, -28.45) * mm});
            skLineSegment(sketch, "E3.11.0.58", {"start": v(-6.03, -43.64) * mm, "end": v(-6.53, -44.14) * mm});
            skLineSegment(sketch, "E3.11.0.59", {"start": v(-6.05, -19.34) * mm, "end": v(-6.55, -18.84) * mm});
            skLineSegment(sketch, "E3.11.0.60", {"start": v(-6.06, -7.19) * mm, "end": v(-6.56, -6.7) * mm});
            skLineSegment(sketch, "E3.11.0.61", {"start": v(-6.08, 4.96) * mm, "end": v(-6.57, 5.46) * mm});
            skLineSegment(sketch, "E3.11.0.62", {"start": v(-6.04, -31.49) * mm, "end": v(-6.54, -31) * mm});
            skLineSegment(sketch, "E3.11.0.63", {"start": v(-9.61, 1.43) * mm, "end": v(-10.1, 1.92) * mm});
            skLineSegment(sketch, "E3.11.0.64", {"start": v(-9.58, -35.02) * mm, "end": v(-10.07, -34.53) * mm});
            skLineSegment(sketch, "E3.11.0.65", {"start": v(-9.59, -22.87) * mm, "end": v(-10.09, -22.38) * mm});
            skLineSegment(sketch, "E3.11.0.66", {"start": v(-9.6, -10.72) * mm, "end": v(-10.1, -10.23) * mm});
            skLineSegment(sketch, "E3.11.0.67", {"start": v(-10.1, 1.92) * mm, "end": v(-6.57, -1.61) * mm});
            skLineSegment(sketch, "E3.11.0.68", {"start": v(-10.11, 14.07) * mm, "end": v(-6.58, 10.54) * mm});
            skLineSegment(sketch, "E3.11.0.69", {"start": v(-10.13, 26.22) * mm, "end": v(-6.6, 22.69) * mm});
            skLineSegment(sketch, "E3.11.0.70", {"start": v(-9.65, 37.87) * mm, "end": v(-9.64, 31.8) * mm, "construction": true});
            skLineSegment(sketch, "E3.11.0.71", {"start": v(-10.07, -34.52) * mm, "end": v(-6.53, -38.06) * mm});
            skLineSegment(sketch, "E3.11.0.72", {"start": v(-10.08, -22.38) * mm, "end": v(-6.54, -25.91) * mm});
            skLineSegment(sketch, "E3.11.0.73", {"start": v(-10.1, -10.23) * mm, "end": v(-6.56, -13.76) * mm});
            skLineSegment(sketch, "E3.11.0.74", {"start": v(-6.07, -1.11) * mm, "end": v(-9.6, -4.65) * mm});
            skLineSegment(sketch, "E3.11.0.75", {"start": v(-6.1, 23.19) * mm, "end": v(-9.63, 19.65) * mm});
            skLineSegment(sketch, "E3.11.0.76", {"start": v(-6.06, -13.26) * mm, "end": v(-9.6, -16.8) * mm});
            skLineSegment(sketch, "E3.11.0.77", {"start": v(-6.57, -0.62) * mm, "end": v(-10.1, -4.15) * mm});
            skLineSegment(sketch, "E3.11.0.78", {"start": v(-6.53, -37.07) * mm, "end": v(-10.07, -40.6) * mm});
            skLineSegment(sketch, "E3.11.0.79", {"start": v(-6.54, -24.92) * mm, "end": v(-10.08, -28.45) * mm});
            skLineSegment(sketch, "E3.11.0.80", {"start": v(-6.56, -12.77) * mm, "end": v(-10.1, -16.3) * mm});
            skLineSegment(sketch, "E3.11.0.81", {"start": v(-9.6, 2.42) * mm, "end": v(-10.1, 1.92) * mm});
            skLineSegment(sketch, "E3.11.0.82", {"start": v(-9.62, 14.57) * mm, "end": v(-10.11, 14.07) * mm});
            skLineSegment(sketch, "E3.11.0.83", {"start": v(-9.63, 26.72) * mm, "end": v(-10.13, 26.22) * mm});
            skLineSegment(sketch, "E3.11.0.84", {"start": v(-9.57, -34.03) * mm, "end": v(-10.07, -34.52) * mm});
            skLineSegment(sketch, "E3.11.0.85", {"start": v(-9.58, -21.88) * mm, "end": v(-10.08, -22.38) * mm});
            skLineSegment(sketch, "E3.11.0.86", {"start": v(-9.6, -9.73) * mm, "end": v(-10.1, -10.23) * mm});
            skLineSegment(sketch, "E3.11.0.87", {"start": v(-9.63, 19.65) * mm, "end": v(-10.13, 20.15) * mm});
            skLineSegment(sketch, "E3.11.0.88", {"start": v(-9.57, -41.1) * mm, "end": v(-10.07, -40.6) * mm});
            skLineSegment(sketch, "E3.11.0.89", {"start": v(-6.1, 35.34) * mm, "end": v(-6.6, 34.84) * mm});
            skLineSegment(sketch, "E3.11.0.90", {"start": v(-6.11, 41.41) * mm, "end": v(-6.6, 40.91) * mm});
            skLineSegment(sketch, "E3.11.0.91", {"start": v(-6.1, 35.34) * mm, "end": v(-9.64, 31.8) * mm});
            skLineSegment(sketch, "E3.11.0.92", {"start": v(-6.6, 35.83) * mm, "end": v(-10.14, 32.3) * mm});
            skLineSegment(sketch, "E3.11.0.93", {"start": v(-9.64, 38.87) * mm, "end": v(-10.14, 38.37) * mm});
            skLineSegment(sketch, "E3.11.0.94", {"start": v(-10.07, -28.45) * mm, "end": v(-6.54, -31.99) * mm});
            skLineSegment(sketch, "E3.11.0.95", {"start": v(-10.13, 32.3) * mm, "end": v(-6.6, 28.76) * mm});
            skLineSegment(sketch, "E3.11.0.96", {"start": v(-10.09, -16.3) * mm, "end": v(-6.55, -19.84) * mm});
            skLineSegment(sketch, "E3.11.0.97", {"start": v(-10.1, -4.15) * mm, "end": v(-6.56, -7.69) * mm});
            skLineSegment(sketch, "E3.11.0.98", {"start": v(-10.12, 20.15) * mm, "end": v(-6.58, 16.61) * mm});
            skLineSegment(sketch, "E3.11.0.99", {"start": v(-6.1, 29.26) * mm, "end": v(-9.63, 25.73) * mm});
            skLineSegment(sketch, "E3.11.0.100", {"start": v(-6.09, 17.11) * mm, "end": v(-9.62, 13.58) * mm});
            skLineSegment(sketch, "E3.11.0.101", {"start": v(-6.6, 29.76) * mm, "end": v(-10.13, 26.22) * mm});
            skLineSegment(sketch, "E3.11.0.102", {"start": v(-6.58, 17.6) * mm, "end": v(-10.12, 14.07) * mm});
            skLineSegment(sketch, "E3.11.0.103", {"start": v(-9.62, 20.65) * mm, "end": v(-10.12, 20.15) * mm});
            skLineSegment(sketch, "E3.11.0.104", {"start": v(-6.05, -19.34) * mm, "end": v(-6.55, -19.84) * mm});
            skLineSegment(sketch, "E3.11.0.105", {"start": v(-6.06, -7.19) * mm, "end": v(-6.56, -7.69) * mm});
            skLineSegment(sketch, "E3.11.0.106", {"start": v(-6.08, 4.96) * mm, "end": v(-6.57, 4.46) * mm});
            skLineSegment(sketch, "E3.11.0.107", {"start": v(-6.04, -31.49) * mm, "end": v(-6.54, -31.99) * mm});
            skLineSegment(sketch, "E3.11.0.108", {"start": v(-6.1, 29.26) * mm, "end": v(-6.6, 29.76) * mm});
            skLineSegment(sketch, "E3.11.0.109", {"start": v(-6.09, 17.11) * mm, "end": v(-6.58, 17.6) * mm});
            skLineSegment(sketch, "E3.11.0.110", {"start": v(-9.62, 13.58) * mm, "end": v(-10.12, 14.07) * mm});
            skLineSegment(sketch, "E3.11.0.111", {"start": v(-9.63, 25.73) * mm, "end": v(-10.13, 26.22) * mm});
            skLineSegment(sketch, "E3.11.0.112", {"start": v(-9.6, -16.8) * mm, "end": v(-10.1, -16.3) * mm});
            skLineSegment(sketch, "E3.11.0.113", {"start": v(-9.6, -4.65) * mm, "end": v(-10.1, -4.15) * mm});
            skLineSegment(sketch, "E3.11.0.114", {"start": v(-9.58, -28.95) * mm, "end": v(-10.08, -28.45) * mm});
            skLineSegment(sketch, "E3.11.0.115", {"start": v(-6.1, 35.34) * mm, "end": v(-6.6, 35.83) * mm});
            skLineSegment(sketch, "E3.11.0.116", {"start": v(-9.64, 31.8) * mm, "end": v(-10.14, 32.3) * mm});
            skLineSegment(sketch, "E3.11.0.117", {"start": v(-9.65, 37.87) * mm, "end": v(-10.14, 38.37) * mm});
            skLineSegment(sketch, "E3.11.0.118", {"start": v(-9.63, 32.8) * mm, "end": v(-10.13, 32.3) * mm});
            skLineSegment(sketch, "E3.11.0.119", {"start": v(-6.1, 29.26) * mm, "end": v(-6.6, 28.76) * mm});
            skLineSegment(sketch, "E3.11.0.120", {"start": v(-6.09, 17.11) * mm, "end": v(-6.58, 16.61) * mm});
            skLineSegment(sketch, "E3.12.0.0", {"start": v(-4.25, 44.95) * mm, "end": v(-0.71, 41.41) * mm});
            skLineSegment(sketch, "E3.12.0.1", {"start": v(-4.74, 44.45) * mm, "end": v(-1.2, 40.91) * mm});
            skLineSegment(sketch, "E3.12.0.2", {"start": v(-4.25, 44.95) * mm, "end": v(-4.74, 44.45) * mm});
            skLineSegment(sketch, "E3.12.0.3", {"start": v(-0.63, -43.64) * mm, "end": v(-4.16, -47.17) * mm});
            skLineSegment(sketch, "E3.12.0.4", {"start": v(-1.13, -43.14) * mm, "end": v(-4.66, -46.68) * mm});
            skLineSegment(sketch, "E3.12.0.5", {"start": v(-4.16, -47.17) * mm, "end": v(-4.66, -46.68) * mm});
            skLineSegment(sketch, "E3.12.0.6", {"start": v(-4.21, 8.5) * mm, "end": v(-0.68, 4.96) * mm});
            skLineSegment(sketch, "E3.12.0.7", {"start": v(-0.63, -43.64) * mm, "end": v(-1.13, -43.14) * mm});
            skLineSegment(sketch, "E3.12.0.8", {"start": v(-0.68, 11.04) * mm, "end": v(-4.22, 7.5) * mm});
            skLineSegment(sketch, "E3.12.0.9", {"start": v(-0.63, -37.56) * mm, "end": v(-4.17, -41.1) * mm});
            skLineSegment(sketch, "E3.12.0.10", {"start": v(-0.65, -25.41) * mm, "end": v(-4.18, -28.95) * mm});
            skLineSegment(sketch, "E3.12.0.11", {"start": v(-1.18, 11.53) * mm, "end": v(-4.71, 8) * mm});
            skLineSegment(sketch, "E3.12.0.12", {"start": v(-1.2, 23.68) * mm, "end": v(-4.73, 20.15) * mm});
            skLineSegment(sketch, "E3.12.0.13", {"start": v(-4.2, 2.42) * mm, "end": v(-0.67, -1.11) * mm});
            skLineSegment(sketch, "E3.12.0.14", {"start": v(-4.22, 14.57) * mm, "end": v(-0.68, 11.04) * mm});
            skLineSegment(sketch, "E3.12.0.15", {"start": v(-4.23, 26.72) * mm, "end": v(-0.7, 23.19) * mm});
            skLineSegment(sketch, "E3.12.0.16", {"start": v(-4.17, -34.03) * mm, "end": v(-0.63, -37.56) * mm});
            skLineSegment(sketch, "E3.12.0.17", {"start": v(-4.18, -21.88) * mm, "end": v(-0.65, -25.41) * mm});
            skLineSegment(sketch, "E3.12.0.18", {"start": v(-4.2, -9.73) * mm, "end": v(-0.66, -13.26) * mm});
            skLineSegment(sketch, "E3.12.0.19", {"start": v(-0.66, -13.26) * mm, "end": v(-1.16, -13.76) * mm});
            skLineSegment(sketch, "E3.12.0.20", {"start": v(-0.67, -1.11) * mm, "end": v(-1.17, -1.61) * mm});
            skLineSegment(sketch, "E3.12.0.21", {"start": v(-0.68, 11.04) * mm, "end": v(-1.18, 10.54) * mm});
            skLineSegment(sketch, "E3.12.0.22", {"start": v(-0.7, 23.19) * mm, "end": v(-1.2, 22.69) * mm});
            skLineSegment(sketch, "E3.12.0.23", {"start": v(-0.63, -37.56) * mm, "end": v(-1.13, -38.06) * mm});
            skLineSegment(sketch, "E3.12.0.24", {"start": v(-0.65, -25.41) * mm, "end": v(-1.14, -25.91) * mm});
            skLineSegment(sketch, "E3.12.0.25", {"start": v(-0.66, -13.26) * mm, "end": v(-1.16, -12.77) * mm});
            skLineSegment(sketch, "E3.12.0.26", {"start": v(-0.67, -1.11) * mm, "end": v(-1.17, -0.62) * mm});
            skLineSegment(sketch, "E3.12.0.27", {"start": v(-0.68, 11.04) * mm, "end": v(-1.18, 11.53) * mm});
            skLineSegment(sketch, "E3.12.0.28", {"start": v(-0.7, 23.19) * mm, "end": v(-1.2, 23.68) * mm});
            skLineSegment(sketch, "E3.12.0.29", {"start": v(-0.63, -37.56) * mm, "end": v(-1.13, -37.07) * mm});
            skLineSegment(sketch, "E3.12.0.30", {"start": v(-0.65, -25.41) * mm, "end": v(-1.14, -24.92) * mm});
            skLineSegment(sketch, "E3.12.0.31", {"start": v(-4.22, 7.5) * mm, "end": v(-4.71, 8) * mm});
            skLineSegment(sketch, "E3.12.0.32", {"start": v(-0.71, 41.41) * mm, "end": v(-4.25, 37.87) * mm});
            skLineSegment(sketch, "E3.12.0.33", {"start": v(-1.2, 41.9) * mm, "end": v(-4.74, 38.37) * mm});
            skLineSegment(sketch, "E3.12.0.34", {"start": v(-0.71, 41.41) * mm, "end": v(-1.2, 41.9) * mm});
            skLineSegment(sketch, "E3.12.0.35", {"start": v(-4.74, 38.37) * mm, "end": v(-1.2, 34.84) * mm});
            skLineSegment(sketch, "E3.12.0.36", {"start": v(-4.24, 38.87) * mm, "end": v(-0.7, 35.34) * mm});
            skLineSegment(sketch, "E3.12.0.37", {"start": v(-4.66, -40.6) * mm, "end": v(-1.13, -44.14) * mm});
            skLineSegment(sketch, "E3.12.0.38", {"start": v(-4.7, 8) * mm, "end": v(-1.17, 4.46) * mm});
            skLineSegment(sketch, "E3.12.0.39", {"start": v(-0.65, -19.34) * mm, "end": v(-4.19, -22.87) * mm});
            skLineSegment(sketch, "E3.12.0.40", {"start": v(-0.66, -7.19) * mm, "end": v(-4.2, -10.72) * mm});
            skLineSegment(sketch, "E3.12.0.41", {"start": v(-0.68, 4.96) * mm, "end": v(-4.21, 1.43) * mm});
            skLineSegment(sketch, "E3.12.0.42", {"start": v(-0.64, -31.49) * mm, "end": v(-4.18, -35.02) * mm});
            skLineSegment(sketch, "E3.12.0.43", {"start": v(-1.15, -18.84) * mm, "end": v(-4.69, -22.38) * mm});
            skLineSegment(sketch, "E3.12.0.44", {"start": v(-1.16, -6.7) * mm, "end": v(-4.7, -10.23) * mm});
            skLineSegment(sketch, "E3.12.0.45", {"start": v(-1.17, 5.46) * mm, "end": v(-4.7, 1.92) * mm});
            skLineSegment(sketch, "E3.12.0.46", {"start": v(-1.14, -31) * mm, "end": v(-4.67, -34.53) * mm});
            skLineSegment(sketch, "E3.12.0.47", {"start": v(-4.19, -15.8) * mm, "end": v(-0.65, -19.34) * mm});
            skLineSegment(sketch, "E3.12.0.48", {"start": v(-4.2, -3.65) * mm, "end": v(-0.66, -7.19) * mm});
            skLineSegment(sketch, "E3.12.0.49", {"start": v(-4.23, 32.8) * mm, "end": v(-0.7, 29.26) * mm});
            skLineSegment(sketch, "E3.12.0.50", {"start": v(-4.16, -40.1) * mm, "end": v(-0.63, -43.64) * mm});
            skLineSegment(sketch, "E3.12.0.51", {"start": v(-4.18, -27.95) * mm, "end": v(-0.64, -31.49) * mm});
            skLineSegment(sketch, "E3.12.0.52", {"start": v(-4.22, 20.65) * mm, "end": v(-0.69, 17.11) * mm});
            skLineSegment(sketch, "E3.12.0.53", {"start": v(-4.19, -15.8) * mm, "end": v(-4.69, -16.3) * mm});
            skLineSegment(sketch, "E3.12.0.54", {"start": v(-4.2, -3.65) * mm, "end": v(-4.7, -4.15) * mm});
            skLineSegment(sketch, "E3.12.0.55", {"start": v(-4.21, 8.5) * mm, "end": v(-4.7, 8) * mm});
            skLineSegment(sketch, "E3.12.0.56", {"start": v(-4.16, -40.1) * mm, "end": v(-4.66, -40.6) * mm});
            skLineSegment(sketch, "E3.12.0.57", {"start": v(-4.18, -27.95) * mm, "end": v(-4.67, -28.45) * mm});
            skLineSegment(sketch, "E3.12.0.58", {"start": v(-0.63, -43.64) * mm, "end": v(-1.13, -44.14) * mm});
            skLineSegment(sketch, "E3.12.0.59", {"start": v(-0.65, -19.34) * mm, "end": v(-1.15, -18.84) * mm});
            skLineSegment(sketch, "E3.12.0.60", {"start": v(-0.66, -7.19) * mm, "end": v(-1.16, -6.7) * mm});
            skLineSegment(sketch, "E3.12.0.61", {"start": v(-0.68, 4.96) * mm, "end": v(-1.17, 5.46) * mm});
            skLineSegment(sketch, "E3.12.0.62", {"start": v(-0.64, -31.49) * mm, "end": v(-1.14, -31) * mm});
            skLineSegment(sketch, "E3.12.0.63", {"start": v(-4.21, 1.43) * mm, "end": v(-4.7, 1.92) * mm});
            skLineSegment(sketch, "E3.12.0.64", {"start": v(-4.18, -35.02) * mm, "end": v(-4.67, -34.53) * mm});
            skLineSegment(sketch, "E3.12.0.65", {"start": v(-4.19, -22.87) * mm, "end": v(-4.69, -22.38) * mm});
            skLineSegment(sketch, "E3.12.0.66", {"start": v(-4.2, -10.72) * mm, "end": v(-4.7, -10.23) * mm});
            skLineSegment(sketch, "E3.12.0.67", {"start": v(-4.7, 1.92) * mm, "end": v(-1.17, -1.61) * mm});
            skLineSegment(sketch, "E3.12.0.68", {"start": v(-4.71, 14.07) * mm, "end": v(-1.18, 10.54) * mm});
            skLineSegment(sketch, "E3.12.0.69", {"start": v(-4.73, 26.22) * mm, "end": v(-1.2, 22.69) * mm});
            skLineSegment(sketch, "E3.12.0.70", {"start": v(-4.25, 37.87) * mm, "end": v(-4.24, 31.8) * mm, "construction": true});
            skLineSegment(sketch, "E3.12.0.71", {"start": v(-4.67, -34.52) * mm, "end": v(-1.13, -38.06) * mm});
            skLineSegment(sketch, "E3.12.0.72", {"start": v(-4.68, -22.38) * mm, "end": v(-1.14, -25.91) * mm});
            skLineSegment(sketch, "E3.12.0.73", {"start": v(-4.7, -10.23) * mm, "end": v(-1.16, -13.76) * mm});
            skLineSegment(sketch, "E3.12.0.74", {"start": v(-0.67, -1.11) * mm, "end": v(-4.2, -4.65) * mm});
            skLineSegment(sketch, "E3.12.0.75", {"start": v(-0.7, 23.19) * mm, "end": v(-4.23, 19.65) * mm});
            skLineSegment(sketch, "E3.12.0.76", {"start": v(-0.66, -13.26) * mm, "end": v(-4.2, -16.8) * mm});
            skLineSegment(sketch, "E3.12.0.77", {"start": v(-1.17, -0.62) * mm, "end": v(-4.7, -4.15) * mm});
            skLineSegment(sketch, "E3.12.0.78", {"start": v(-1.13, -37.07) * mm, "end": v(-4.67, -40.6) * mm});
            skLineSegment(sketch, "E3.12.0.79", {"start": v(-1.14, -24.92) * mm, "end": v(-4.68, -28.45) * mm});
            skLineSegment(sketch, "E3.12.0.80", {"start": v(-1.16, -12.77) * mm, "end": v(-4.7, -16.3) * mm});
            skLineSegment(sketch, "E3.12.0.81", {"start": v(-4.2, 2.42) * mm, "end": v(-4.7, 1.92) * mm});
            skLineSegment(sketch, "E3.12.0.82", {"start": v(-4.22, 14.57) * mm, "end": v(-4.71, 14.07) * mm});
            skLineSegment(sketch, "E3.12.0.83", {"start": v(-4.23, 26.72) * mm, "end": v(-4.73, 26.22) * mm});
            skLineSegment(sketch, "E3.12.0.84", {"start": v(-4.17, -34.03) * mm, "end": v(-4.67, -34.52) * mm});
            skLineSegment(sketch, "E3.12.0.85", {"start": v(-4.18, -21.88) * mm, "end": v(-4.68, -22.38) * mm});
            skLineSegment(sketch, "E3.12.0.86", {"start": v(-4.2, -9.73) * mm, "end": v(-4.7, -10.23) * mm});
            skLineSegment(sketch, "E3.12.0.87", {"start": v(-4.23, 19.65) * mm, "end": v(-4.73, 20.15) * mm});
            skLineSegment(sketch, "E3.12.0.88", {"start": v(-4.17, -41.1) * mm, "end": v(-4.67, -40.6) * mm});
            skLineSegment(sketch, "E3.12.0.89", {"start": v(-0.7, 35.34) * mm, "end": v(-1.2, 34.84) * mm});
            skLineSegment(sketch, "E3.12.0.90", {"start": v(-0.71, 41.41) * mm, "end": v(-1.2, 40.91) * mm});
            skLineSegment(sketch, "E3.12.0.91", {"start": v(-0.7, 35.34) * mm, "end": v(-4.24, 31.8) * mm});
            skLineSegment(sketch, "E3.12.0.92", {"start": v(-1.2, 35.83) * mm, "end": v(-4.74, 32.3) * mm});
            skLineSegment(sketch, "E3.12.0.93", {"start": v(-4.24, 38.87) * mm, "end": v(-4.74, 38.37) * mm});
            skLineSegment(sketch, "E3.12.0.94", {"start": v(-4.67, -28.45) * mm, "end": v(-1.14, -31.99) * mm});
            skLineSegment(sketch, "E3.12.0.95", {"start": v(-4.73, 32.3) * mm, "end": v(-1.2, 28.76) * mm});
            skLineSegment(sketch, "E3.12.0.96", {"start": v(-4.69, -16.3) * mm, "end": v(-1.15, -19.84) * mm});
            skLineSegment(sketch, "E3.12.0.97", {"start": v(-4.7, -4.15) * mm, "end": v(-1.16, -7.69) * mm});
            skLineSegment(sketch, "E3.12.0.98", {"start": v(-4.72, 20.15) * mm, "end": v(-1.18, 16.61) * mm});
            skLineSegment(sketch, "E3.12.0.99", {"start": v(-0.7, 29.26) * mm, "end": v(-4.23, 25.73) * mm});
            skLineSegment(sketch, "E3.12.0.100", {"start": v(-0.69, 17.11) * mm, "end": v(-4.22, 13.58) * mm});
            skLineSegment(sketch, "E3.12.0.101", {"start": v(-1.2, 29.76) * mm, "end": v(-4.73, 26.22) * mm});
            skLineSegment(sketch, "E3.12.0.102", {"start": v(-1.18, 17.6) * mm, "end": v(-4.72, 14.07) * mm});
            skLineSegment(sketch, "E3.12.0.103", {"start": v(-4.22, 20.65) * mm, "end": v(-4.72, 20.15) * mm});
            skLineSegment(sketch, "E3.12.0.104", {"start": v(-0.65, -19.34) * mm, "end": v(-1.15, -19.84) * mm});
            skLineSegment(sketch, "E3.12.0.105", {"start": v(-0.66, -7.19) * mm, "end": v(-1.16, -7.69) * mm});
            skLineSegment(sketch, "E3.12.0.106", {"start": v(-0.68, 4.96) * mm, "end": v(-1.17, 4.46) * mm});
            skLineSegment(sketch, "E3.12.0.107", {"start": v(-0.64, -31.49) * mm, "end": v(-1.14, -31.99) * mm});
            skLineSegment(sketch, "E3.12.0.108", {"start": v(-0.7, 29.26) * mm, "end": v(-1.2, 29.76) * mm});
            skLineSegment(sketch, "E3.12.0.109", {"start": v(-0.69, 17.11) * mm, "end": v(-1.18, 17.6) * mm});
            skLineSegment(sketch, "E3.12.0.110", {"start": v(-4.22, 13.58) * mm, "end": v(-4.72, 14.07) * mm});
            skLineSegment(sketch, "E3.12.0.111", {"start": v(-4.23, 25.73) * mm, "end": v(-4.73, 26.22) * mm});
            skLineSegment(sketch, "E3.12.0.112", {"start": v(-4.2, -16.8) * mm, "end": v(-4.7, -16.3) * mm});
            skLineSegment(sketch, "E3.12.0.113", {"start": v(-4.2, -4.65) * mm, "end": v(-4.7, -4.15) * mm});
            skLineSegment(sketch, "E3.12.0.114", {"start": v(-4.18, -28.95) * mm, "end": v(-4.68, -28.45) * mm});
            skLineSegment(sketch, "E3.12.0.115", {"start": v(-0.7, 35.34) * mm, "end": v(-1.2, 35.83) * mm});
            skLineSegment(sketch, "E3.12.0.116", {"start": v(-4.24, 31.8) * mm, "end": v(-4.74, 32.3) * mm});
            skLineSegment(sketch, "E3.12.0.117", {"start": v(-4.25, 37.87) * mm, "end": v(-4.74, 38.37) * mm});
            skLineSegment(sketch, "E3.12.0.118", {"start": v(-4.23, 32.8) * mm, "end": v(-4.73, 32.3) * mm});
            skLineSegment(sketch, "E3.12.0.119", {"start": v(-0.7, 29.26) * mm, "end": v(-1.2, 28.76) * mm});
            skLineSegment(sketch, "E3.12.0.120", {"start": v(-0.69, 17.11) * mm, "end": v(-1.18, 16.61) * mm});
            skLineSegment(sketch, "E3.13.0.0", {"start": v(1.15, 44.95) * mm, "end": v(4.69, 41.41) * mm});
            skLineSegment(sketch, "E3.13.0.1", {"start": v(0.66, 44.45) * mm, "end": v(4.2, 40.91) * mm});
            skLineSegment(sketch, "E3.13.0.2", {"start": v(1.15, 44.95) * mm, "end": v(0.66, 44.45) * mm});
            skLineSegment(sketch, "E3.13.0.3", {"start": v(4.77, -43.64) * mm, "end": v(1.24, -47.17) * mm});
            skLineSegment(sketch, "E3.13.0.4", {"start": v(4.27, -43.14) * mm, "end": v(0.74, -46.68) * mm});
            skLineSegment(sketch, "E3.13.0.5", {"start": v(1.24, -47.17) * mm, "end": v(0.74, -46.68) * mm});
            skLineSegment(sketch, "E3.13.0.6", {"start": v(1.19, 8.5) * mm, "end": v(4.72, 4.96) * mm});
            skLineSegment(sketch, "E3.13.0.7", {"start": v(4.77, -43.64) * mm, "end": v(4.27, -43.14) * mm});
            skLineSegment(sketch, "E3.13.0.8", {"start": v(4.72, 11.04) * mm, "end": v(1.18, 7.5) * mm});
            skLineSegment(sketch, "E3.13.0.9", {"start": v(4.77, -37.56) * mm, "end": v(1.23, -41.1) * mm});
            skLineSegment(sketch, "E3.13.0.10", {"start": v(4.75, -25.41) * mm, "end": v(1.22, -28.95) * mm});
            skLineSegment(sketch, "E3.13.0.11", {"start": v(4.22, 11.53) * mm, "end": v(0.69, 8) * mm});
            skLineSegment(sketch, "E3.13.0.12", {"start": v(4.2, 23.68) * mm, "end": v(0.67, 20.15) * mm});
            skLineSegment(sketch, "E3.13.0.13", {"start": v(1.2, 2.42) * mm, "end": v(4.73, -1.11) * mm});
            skLineSegment(sketch, "E3.13.0.14", {"start": v(1.18, 14.57) * mm, "end": v(4.72, 11.04) * mm});
            skLineSegment(sketch, "E3.13.0.15", {"start": v(1.17, 26.72) * mm, "end": v(4.7, 23.19) * mm});
            skLineSegment(sketch, "E3.13.0.16", {"start": v(1.23, -34.03) * mm, "end": v(4.77, -37.56) * mm});
            skLineSegment(sketch, "E3.13.0.17", {"start": v(1.22, -21.88) * mm, "end": v(4.75, -25.41) * mm});
            skLineSegment(sketch, "E3.13.0.18", {"start": v(1.2, -9.73) * mm, "end": v(4.74, -13.26) * mm});
            skLineSegment(sketch, "E3.13.0.19", {"start": v(4.74, -13.26) * mm, "end": v(4.24, -13.76) * mm});
            skLineSegment(sketch, "E3.13.0.20", {"start": v(4.73, -1.11) * mm, "end": v(4.23, -1.61) * mm});
            skLineSegment(sketch, "E3.13.0.21", {"start": v(4.72, 11.04) * mm, "end": v(4.22, 10.54) * mm});
            skLineSegment(sketch, "E3.13.0.22", {"start": v(4.7, 23.19) * mm, "end": v(4.2, 22.69) * mm});
            skLineSegment(sketch, "E3.13.0.23", {"start": v(4.77, -37.56) * mm, "end": v(4.27, -38.06) * mm});
            skLineSegment(sketch, "E3.13.0.24", {"start": v(4.75, -25.41) * mm, "end": v(4.26, -25.91) * mm});
            skLineSegment(sketch, "E3.13.0.25", {"start": v(4.74, -13.26) * mm, "end": v(4.24, -12.77) * mm});
            skLineSegment(sketch, "E3.13.0.26", {"start": v(4.73, -1.11) * mm, "end": v(4.23, -0.62) * mm});
            skLineSegment(sketch, "E3.13.0.27", {"start": v(4.72, 11.04) * mm, "end": v(4.22, 11.53) * mm});
            skLineSegment(sketch, "E3.13.0.28", {"start": v(4.7, 23.19) * mm, "end": v(4.2, 23.68) * mm});
            skLineSegment(sketch, "E3.13.0.29", {"start": v(4.77, -37.56) * mm, "end": v(4.27, -37.07) * mm});
            skLineSegment(sketch, "E3.13.0.30", {"start": v(4.75, -25.41) * mm, "end": v(4.26, -24.92) * mm});
            skLineSegment(sketch, "E3.13.0.31", {"start": v(1.18, 7.5) * mm, "end": v(0.69, 8) * mm});
            skLineSegment(sketch, "E3.13.0.32", {"start": v(4.69, 41.41) * mm, "end": v(1.15, 37.87) * mm});
            skLineSegment(sketch, "E3.13.0.33", {"start": v(4.2, 41.9) * mm, "end": v(0.66, 38.37) * mm});
            skLineSegment(sketch, "E3.13.0.34", {"start": v(4.69, 41.41) * mm, "end": v(4.2, 41.9) * mm});
            skLineSegment(sketch, "E3.13.0.35", {"start": v(0.66, 38.37) * mm, "end": v(4.2, 34.84) * mm});
            skLineSegment(sketch, "E3.13.0.36", {"start": v(1.16, 38.87) * mm, "end": v(4.7, 35.34) * mm});
            skLineSegment(sketch, "E3.13.0.37", {"start": v(0.74, -40.6) * mm, "end": v(4.27, -44.14) * mm});
            skLineSegment(sketch, "E3.13.0.38", {"start": v(0.7, 8) * mm, "end": v(4.23, 4.46) * mm});
            skLineSegment(sketch, "E3.13.0.39", {"start": v(4.75, -19.34) * mm, "end": v(1.21, -22.87) * mm});
            skLineSegment(sketch, "E3.13.0.40", {"start": v(4.74, -7.19) * mm, "end": v(1.2, -10.72) * mm});
            skLineSegment(sketch, "E3.13.0.41", {"start": v(4.72, 4.96) * mm, "end": v(1.19, 1.43) * mm});
            skLineSegment(sketch, "E3.13.0.42", {"start": v(4.76, -31.49) * mm, "end": v(1.22, -35.02) * mm});
            skLineSegment(sketch, "E3.13.0.43", {"start": v(4.25, -18.84) * mm, "end": v(0.71, -22.38) * mm});
            skLineSegment(sketch, "E3.13.0.44", {"start": v(4.24, -6.7) * mm, "end": v(0.7, -10.23) * mm});
            skLineSegment(sketch, "E3.13.0.45", {"start": v(4.23, 5.46) * mm, "end": v(0.7, 1.92) * mm});
            skLineSegment(sketch, "E3.13.0.46", {"start": v(4.26, -31) * mm, "end": v(0.73, -34.53) * mm});
            skLineSegment(sketch, "E3.13.0.47", {"start": v(1.21, -15.8) * mm, "end": v(4.75, -19.34) * mm});
            skLineSegment(sketch, "E3.13.0.48", {"start": v(1.2, -3.65) * mm, "end": v(4.74, -7.19) * mm});
            skLineSegment(sketch, "E3.13.0.49", {"start": v(1.17, 32.8) * mm, "end": v(4.7, 29.26) * mm});
            skLineSegment(sketch, "E3.13.0.50", {"start": v(1.24, -40.1) * mm, "end": v(4.77, -43.64) * mm});
            skLineSegment(sketch, "E3.13.0.51", {"start": v(1.22, -27.95) * mm, "end": v(4.76, -31.49) * mm});
            skLineSegment(sketch, "E3.13.0.52", {"start": v(1.18, 20.65) * mm, "end": v(4.71, 17.11) * mm});
            skLineSegment(sketch, "E3.13.0.53", {"start": v(1.21, -15.8) * mm, "end": v(0.71, -16.3) * mm});
            skLineSegment(sketch, "E3.13.0.54", {"start": v(1.2, -3.65) * mm, "end": v(0.7, -4.15) * mm});
            skLineSegment(sketch, "E3.13.0.55", {"start": v(1.19, 8.5) * mm, "end": v(0.7, 8) * mm});
            skLineSegment(sketch, "E3.13.0.56", {"start": v(1.24, -40.1) * mm, "end": v(0.74, -40.6) * mm});
            skLineSegment(sketch, "E3.13.0.57", {"start": v(1.22, -27.95) * mm, "end": v(0.73, -28.45) * mm});
            skLineSegment(sketch, "E3.13.0.58", {"start": v(4.77, -43.64) * mm, "end": v(4.27, -44.14) * mm});
            skLineSegment(sketch, "E3.13.0.59", {"start": v(4.75, -19.34) * mm, "end": v(4.25, -18.84) * mm});
            skLineSegment(sketch, "E3.13.0.60", {"start": v(4.74, -7.19) * mm, "end": v(4.24, -6.7) * mm});
            skLineSegment(sketch, "E3.13.0.61", {"start": v(4.72, 4.96) * mm, "end": v(4.23, 5.46) * mm});
            skLineSegment(sketch, "E3.13.0.62", {"start": v(4.76, -31.49) * mm, "end": v(4.26, -31) * mm});
            skLineSegment(sketch, "E3.13.0.63", {"start": v(1.19, 1.43) * mm, "end": v(0.7, 1.92) * mm});
            skLineSegment(sketch, "E3.13.0.64", {"start": v(1.22, -35.02) * mm, "end": v(0.73, -34.53) * mm});
            skLineSegment(sketch, "E3.13.0.65", {"start": v(1.21, -22.87) * mm, "end": v(0.71, -22.38) * mm});
            skLineSegment(sketch, "E3.13.0.66", {"start": v(1.2, -10.72) * mm, "end": v(0.7, -10.23) * mm});
            skLineSegment(sketch, "E3.13.0.67", {"start": v(0.7, 1.92) * mm, "end": v(4.23, -1.61) * mm});
            skLineSegment(sketch, "E3.13.0.68", {"start": v(0.69, 14.07) * mm, "end": v(4.22, 10.54) * mm});
            skLineSegment(sketch, "E3.13.0.69", {"start": v(0.67, 26.22) * mm, "end": v(4.2, 22.69) * mm});
            skLineSegment(sketch, "E3.13.0.70", {"start": v(1.15, 37.87) * mm, "end": v(1.16, 31.8) * mm, "construction": true});
            skLineSegment(sketch, "E3.13.0.71", {"start": v(0.73, -34.52) * mm, "end": v(4.27, -38.06) * mm});
            skLineSegment(sketch, "E3.13.0.72", {"start": v(0.72, -22.38) * mm, "end": v(4.26, -25.91) * mm});
            skLineSegment(sketch, "E3.13.0.73", {"start": v(0.7, -10.23) * mm, "end": v(4.24, -13.76) * mm});
            skLineSegment(sketch, "E3.13.0.74", {"start": v(4.73, -1.11) * mm, "end": v(1.2, -4.65) * mm});
            skLineSegment(sketch, "E3.13.0.75", {"start": v(4.7, 23.19) * mm, "end": v(1.17, 19.65) * mm});
            skLineSegment(sketch, "E3.13.0.76", {"start": v(4.74, -13.26) * mm, "end": v(1.2, -16.8) * mm});
            skLineSegment(sketch, "E3.13.0.77", {"start": v(4.23, -0.62) * mm, "end": v(0.7, -4.15) * mm});
            skLineSegment(sketch, "E3.13.0.78", {"start": v(4.27, -37.07) * mm, "end": v(0.73, -40.6) * mm});
            skLineSegment(sketch, "E3.13.0.79", {"start": v(4.26, -24.92) * mm, "end": v(0.72, -28.45) * mm});
            skLineSegment(sketch, "E3.13.0.80", {"start": v(4.24, -12.77) * mm, "end": v(0.7, -16.3) * mm});
            skLineSegment(sketch, "E3.13.0.81", {"start": v(1.2, 2.42) * mm, "end": v(0.7, 1.92) * mm});
            skLineSegment(sketch, "E3.13.0.82", {"start": v(1.18, 14.57) * mm, "end": v(0.69, 14.07) * mm});
            skLineSegment(sketch, "E3.13.0.83", {"start": v(1.17, 26.72) * mm, "end": v(0.67, 26.22) * mm});
            skLineSegment(sketch, "E3.13.0.84", {"start": v(1.23, -34.03) * mm, "end": v(0.73, -34.52) * mm});
            skLineSegment(sketch, "E3.13.0.85", {"start": v(1.22, -21.88) * mm, "end": v(0.72, -22.38) * mm});
            skLineSegment(sketch, "E3.13.0.86", {"start": v(1.2, -9.73) * mm, "end": v(0.7, -10.23) * mm});
            skLineSegment(sketch, "E3.13.0.87", {"start": v(1.17, 19.65) * mm, "end": v(0.67, 20.15) * mm});
            skLineSegment(sketch, "E3.13.0.88", {"start": v(1.23, -41.1) * mm, "end": v(0.73, -40.6) * mm});
            skLineSegment(sketch, "E3.13.0.89", {"start": v(4.7, 35.34) * mm, "end": v(4.2, 34.84) * mm});
            skLineSegment(sketch, "E3.13.0.90", {"start": v(4.69, 41.41) * mm, "end": v(4.2, 40.91) * mm});
            skLineSegment(sketch, "E3.13.0.91", {"start": v(4.7, 35.34) * mm, "end": v(1.16, 31.8) * mm});
            skLineSegment(sketch, "E3.13.0.92", {"start": v(4.2, 35.83) * mm, "end": v(0.66, 32.3) * mm});
            skLineSegment(sketch, "E3.13.0.93", {"start": v(1.16, 38.87) * mm, "end": v(0.66, 38.37) * mm});
            skLineSegment(sketch, "E3.13.0.94", {"start": v(0.73, -28.45) * mm, "end": v(4.26, -31.99) * mm});
            skLineSegment(sketch, "E3.13.0.95", {"start": v(0.67, 32.3) * mm, "end": v(4.2, 28.76) * mm});
            skLineSegment(sketch, "E3.13.0.96", {"start": v(0.71, -16.3) * mm, "end": v(4.25, -19.84) * mm});
            skLineSegment(sketch, "E3.13.0.97", {"start": v(0.7, -4.15) * mm, "end": v(4.24, -7.69) * mm});
            skLineSegment(sketch, "E3.13.0.98", {"start": v(0.68, 20.15) * mm, "end": v(4.22, 16.61) * mm});
            skLineSegment(sketch, "E3.13.0.99", {"start": v(4.7, 29.26) * mm, "end": v(1.17, 25.73) * mm});
            skLineSegment(sketch, "E3.13.0.100", {"start": v(4.71, 17.11) * mm, "end": v(1.18, 13.58) * mm});
            skLineSegment(sketch, "E3.13.0.101", {"start": v(4.2, 29.76) * mm, "end": v(0.67, 26.22) * mm});
            skLineSegment(sketch, "E3.13.0.102", {"start": v(4.22, 17.6) * mm, "end": v(0.68, 14.07) * mm});
            skLineSegment(sketch, "E3.13.0.103", {"start": v(1.18, 20.65) * mm, "end": v(0.68, 20.15) * mm});
            skLineSegment(sketch, "E3.13.0.104", {"start": v(4.75, -19.34) * mm, "end": v(4.25, -19.84) * mm});
            skLineSegment(sketch, "E3.13.0.105", {"start": v(4.74, -7.19) * mm, "end": v(4.24, -7.69) * mm});
            skLineSegment(sketch, "E3.13.0.106", {"start": v(4.72, 4.96) * mm, "end": v(4.23, 4.46) * mm});
            skLineSegment(sketch, "E3.13.0.107", {"start": v(4.76, -31.49) * mm, "end": v(4.26, -31.99) * mm});
            skLineSegment(sketch, "E3.13.0.108", {"start": v(4.7, 29.26) * mm, "end": v(4.2, 29.76) * mm});
            skLineSegment(sketch, "E3.13.0.109", {"start": v(4.71, 17.11) * mm, "end": v(4.22, 17.6) * mm});
            skLineSegment(sketch, "E3.13.0.110", {"start": v(1.18, 13.58) * mm, "end": v(0.68, 14.07) * mm});
            skLineSegment(sketch, "E3.13.0.111", {"start": v(1.17, 25.73) * mm, "end": v(0.67, 26.22) * mm});
            skLineSegment(sketch, "E3.13.0.112", {"start": v(1.2, -16.8) * mm, "end": v(0.7, -16.3) * mm});
            skLineSegment(sketch, "E3.13.0.113", {"start": v(1.2, -4.65) * mm, "end": v(0.7, -4.15) * mm});
            skLineSegment(sketch, "E3.13.0.114", {"start": v(1.22, -28.95) * mm, "end": v(0.72, -28.45) * mm});
            skLineSegment(sketch, "E3.13.0.115", {"start": v(4.7, 35.34) * mm, "end": v(4.2, 35.83) * mm});
            skLineSegment(sketch, "E3.13.0.116", {"start": v(1.16, 31.8) * mm, "end": v(0.66, 32.3) * mm});
            skLineSegment(sketch, "E3.13.0.117", {"start": v(1.15, 37.87) * mm, "end": v(0.66, 38.37) * mm});
            skLineSegment(sketch, "E3.13.0.118", {"start": v(1.17, 32.8) * mm, "end": v(0.67, 32.3) * mm});
            skLineSegment(sketch, "E3.13.0.119", {"start": v(4.7, 29.26) * mm, "end": v(4.2, 28.76) * mm});
            skLineSegment(sketch, "E3.13.0.120", {"start": v(4.71, 17.11) * mm, "end": v(4.22, 16.61) * mm});
            skLineSegment(sketch, "E3.14.0.0", {"start": v(6.55, 44.95) * mm, "end": v(10.09, 41.41) * mm});
            skLineSegment(sketch, "E3.14.0.1", {"start": v(6.06, 44.45) * mm, "end": v(9.6, 40.91) * mm});
            skLineSegment(sketch, "E3.14.0.2", {"start": v(6.55, 44.95) * mm, "end": v(6.06, 44.45) * mm});
            skLineSegment(sketch, "E3.14.0.3", {"start": v(10.17, -43.64) * mm, "end": v(6.64, -47.17) * mm});
            skLineSegment(sketch, "E3.14.0.4", {"start": v(9.67, -43.14) * mm, "end": v(6.14, -46.68) * mm});
            skLineSegment(sketch, "E3.14.0.5", {"start": v(6.64, -47.17) * mm, "end": v(6.14, -46.68) * mm});
            skLineSegment(sketch, "E3.14.0.6", {"start": v(6.59, 8.5) * mm, "end": v(10.12, 4.96) * mm});
            skLineSegment(sketch, "E3.14.0.7", {"start": v(10.17, -43.64) * mm, "end": v(9.67, -43.14) * mm});
            skLineSegment(sketch, "E3.14.0.8", {"start": v(10.12, 11.04) * mm, "end": v(6.58, 7.5) * mm});
            skLineSegment(sketch, "E3.14.0.9", {"start": v(10.17, -37.56) * mm, "end": v(6.63, -41.1) * mm});
            skLineSegment(sketch, "E3.14.0.10", {"start": v(10.15, -25.41) * mm, "end": v(6.62, -28.95) * mm});
            skLineSegment(sketch, "E3.14.0.11", {"start": v(9.62, 11.53) * mm, "end": v(6.09, 8) * mm});
            skLineSegment(sketch, "E3.14.0.12", {"start": v(9.6, 23.68) * mm, "end": v(6.07, 20.15) * mm});
            skLineSegment(sketch, "E3.14.0.13", {"start": v(6.6, 2.42) * mm, "end": v(10.13, -1.11) * mm});
            skLineSegment(sketch, "E3.14.0.14", {"start": v(6.58, 14.57) * mm, "end": v(10.12, 11.04) * mm});
            skLineSegment(sketch, "E3.14.0.15", {"start": v(6.57, 26.72) * mm, "end": v(10.1, 23.19) * mm});
            skLineSegment(sketch, "E3.14.0.16", {"start": v(6.63, -34.03) * mm, "end": v(10.17, -37.56) * mm});
            skLineSegment(sketch, "E3.14.0.17", {"start": v(6.62, -21.88) * mm, "end": v(10.15, -25.41) * mm});
            skLineSegment(sketch, "E3.14.0.18", {"start": v(6.6, -9.73) * mm, "end": v(10.14, -13.26) * mm});
            skLineSegment(sketch, "E3.14.0.19", {"start": v(10.14, -13.26) * mm, "end": v(9.64, -13.76) * mm});
            skLineSegment(sketch, "E3.14.0.20", {"start": v(10.13, -1.11) * mm, "end": v(9.63, -1.61) * mm});
            skLineSegment(sketch, "E3.14.0.21", {"start": v(10.12, 11.04) * mm, "end": v(9.62, 10.54) * mm});
            skLineSegment(sketch, "E3.14.0.22", {"start": v(10.1, 23.19) * mm, "end": v(9.6, 22.69) * mm});
            skLineSegment(sketch, "E3.14.0.23", {"start": v(10.17, -37.56) * mm, "end": v(9.67, -38.06) * mm});
            skLineSegment(sketch, "E3.14.0.24", {"start": v(10.15, -25.41) * mm, "end": v(9.66, -25.91) * mm});
            skLineSegment(sketch, "E3.14.0.25", {"start": v(10.14, -13.26) * mm, "end": v(9.64, -12.77) * mm});
            skLineSegment(sketch, "E3.14.0.26", {"start": v(10.13, -1.11) * mm, "end": v(9.63, -0.62) * mm});
            skLineSegment(sketch, "E3.14.0.27", {"start": v(10.12, 11.04) * mm, "end": v(9.62, 11.53) * mm});
            skLineSegment(sketch, "E3.14.0.28", {"start": v(10.1, 23.19) * mm, "end": v(9.6, 23.68) * mm});
            skLineSegment(sketch, "E3.14.0.29", {"start": v(10.17, -37.56) * mm, "end": v(9.67, -37.07) * mm});
            skLineSegment(sketch, "E3.14.0.30", {"start": v(10.15, -25.41) * mm, "end": v(9.66, -24.92) * mm});
            skLineSegment(sketch, "E3.14.0.31", {"start": v(6.58, 7.5) * mm, "end": v(6.09, 8) * mm});
            skLineSegment(sketch, "E3.14.0.32", {"start": v(10.09, 41.41) * mm, "end": v(6.55, 37.87) * mm});
            skLineSegment(sketch, "E3.14.0.33", {"start": v(9.6, 41.9) * mm, "end": v(6.06, 38.37) * mm});
            skLineSegment(sketch, "E3.14.0.34", {"start": v(10.09, 41.41) * mm, "end": v(9.6, 41.9) * mm});
            skLineSegment(sketch, "E3.14.0.35", {"start": v(6.06, 38.37) * mm, "end": v(9.6, 34.84) * mm});
            skLineSegment(sketch, "E3.14.0.36", {"start": v(6.56, 38.87) * mm, "end": v(10.1, 35.34) * mm});
            skLineSegment(sketch, "E3.14.0.37", {"start": v(6.14, -40.6) * mm, "end": v(9.67, -44.14) * mm});
            skLineSegment(sketch, "E3.14.0.38", {"start": v(6.1, 8) * mm, "end": v(9.63, 4.46) * mm});
            skLineSegment(sketch, "E3.14.0.39", {"start": v(10.15, -19.34) * mm, "end": v(6.61, -22.87) * mm});
            skLineSegment(sketch, "E3.14.0.40", {"start": v(10.14, -7.19) * mm, "end": v(6.6, -10.72) * mm});
            skLineSegment(sketch, "E3.14.0.41", {"start": v(10.12, 4.96) * mm, "end": v(6.59, 1.43) * mm});
            skLineSegment(sketch, "E3.14.0.42", {"start": v(10.16, -31.49) * mm, "end": v(6.62, -35.02) * mm});
            skLineSegment(sketch, "E3.14.0.43", {"start": v(9.65, -18.84) * mm, "end": v(6.11, -22.38) * mm});
            skLineSegment(sketch, "E3.14.0.44", {"start": v(9.64, -6.7) * mm, "end": v(6.1, -10.23) * mm});
            skLineSegment(sketch, "E3.14.0.45", {"start": v(9.63, 5.46) * mm, "end": v(6.1, 1.92) * mm});
            skLineSegment(sketch, "E3.14.0.46", {"start": v(9.66, -31) * mm, "end": v(6.13, -34.53) * mm});
            skLineSegment(sketch, "E3.14.0.47", {"start": v(6.61, -15.8) * mm, "end": v(10.15, -19.34) * mm});
            skLineSegment(sketch, "E3.14.0.48", {"start": v(6.6, -3.65) * mm, "end": v(10.14, -7.19) * mm});
            skLineSegment(sketch, "E3.14.0.49", {"start": v(6.57, 32.8) * mm, "end": v(10.1, 29.26) * mm});
            skLineSegment(sketch, "E3.14.0.50", {"start": v(6.64, -40.1) * mm, "end": v(10.17, -43.64) * mm});
            skLineSegment(sketch, "E3.14.0.51", {"start": v(6.62, -27.95) * mm, "end": v(10.16, -31.49) * mm});
            skLineSegment(sketch, "E3.14.0.52", {"start": v(6.58, 20.65) * mm, "end": v(10.11, 17.11) * mm});
            skLineSegment(sketch, "E3.14.0.53", {"start": v(6.61, -15.8) * mm, "end": v(6.11, -16.3) * mm});
            skLineSegment(sketch, "E3.14.0.54", {"start": v(6.6, -3.65) * mm, "end": v(6.1, -4.15) * mm});
            skLineSegment(sketch, "E3.14.0.55", {"start": v(6.59, 8.5) * mm, "end": v(6.1, 8) * mm});
            skLineSegment(sketch, "E3.14.0.56", {"start": v(6.64, -40.1) * mm, "end": v(6.14, -40.6) * mm});
            skLineSegment(sketch, "E3.14.0.57", {"start": v(6.62, -27.95) * mm, "end": v(6.13, -28.45) * mm});
            skLineSegment(sketch, "E3.14.0.58", {"start": v(10.17, -43.64) * mm, "end": v(9.67, -44.14) * mm});
            skLineSegment(sketch, "E3.14.0.59", {"start": v(10.15, -19.34) * mm, "end": v(9.65, -18.84) * mm});
            skLineSegment(sketch, "E3.14.0.60", {"start": v(10.14, -7.19) * mm, "end": v(9.64, -6.7) * mm});
            skLineSegment(sketch, "E3.14.0.61", {"start": v(10.12, 4.96) * mm, "end": v(9.63, 5.46) * mm});
            skLineSegment(sketch, "E3.14.0.62", {"start": v(10.16, -31.49) * mm, "end": v(9.66, -31) * mm});
            skLineSegment(sketch, "E3.14.0.63", {"start": v(6.59, 1.43) * mm, "end": v(6.1, 1.92) * mm});
            skLineSegment(sketch, "E3.14.0.64", {"start": v(6.62, -35.02) * mm, "end": v(6.13, -34.53) * mm});
            skLineSegment(sketch, "E3.14.0.65", {"start": v(6.61, -22.87) * mm, "end": v(6.11, -22.38) * mm});
            skLineSegment(sketch, "E3.14.0.66", {"start": v(6.6, -10.72) * mm, "end": v(6.1, -10.23) * mm});
            skLineSegment(sketch, "E3.14.0.67", {"start": v(6.1, 1.92) * mm, "end": v(9.63, -1.61) * mm});
            skLineSegment(sketch, "E3.14.0.68", {"start": v(6.09, 14.07) * mm, "end": v(9.62, 10.54) * mm});
            skLineSegment(sketch, "E3.14.0.69", {"start": v(6.07, 26.22) * mm, "end": v(9.6, 22.69) * mm});
            skLineSegment(sketch, "E3.14.0.70", {"start": v(6.55, 37.87) * mm, "end": v(6.56, 31.8) * mm, "construction": true});
            skLineSegment(sketch, "E3.14.0.71", {"start": v(6.13, -34.52) * mm, "end": v(9.67, -38.06) * mm});
            skLineSegment(sketch, "E3.14.0.72", {"start": v(6.12, -22.38) * mm, "end": v(9.66, -25.91) * mm});
            skLineSegment(sketch, "E3.14.0.73", {"start": v(6.1, -10.23) * mm, "end": v(9.64, -13.76) * mm});
            skLineSegment(sketch, "E3.14.0.74", {"start": v(10.13, -1.11) * mm, "end": v(6.6, -4.65) * mm});
            skLineSegment(sketch, "E3.14.0.75", {"start": v(10.1, 23.19) * mm, "end": v(6.57, 19.65) * mm});
            skLineSegment(sketch, "E3.14.0.76", {"start": v(10.14, -13.26) * mm, "end": v(6.6, -16.8) * mm});
            skLineSegment(sketch, "E3.14.0.77", {"start": v(9.63, -0.62) * mm, "end": v(6.1, -4.15) * mm});
            skLineSegment(sketch, "E3.14.0.78", {"start": v(9.67, -37.07) * mm, "end": v(6.13, -40.6) * mm});
            skLineSegment(sketch, "E3.14.0.79", {"start": v(9.66, -24.92) * mm, "end": v(6.12, -28.45) * mm});
            skLineSegment(sketch, "E3.14.0.80", {"start": v(9.64, -12.77) * mm, "end": v(6.1, -16.3) * mm});
            skLineSegment(sketch, "E3.14.0.81", {"start": v(6.6, 2.42) * mm, "end": v(6.1, 1.92) * mm});
            skLineSegment(sketch, "E3.14.0.82", {"start": v(6.58, 14.57) * mm, "end": v(6.09, 14.07) * mm});
            skLineSegment(sketch, "E3.14.0.83", {"start": v(6.57, 26.72) * mm, "end": v(6.07, 26.22) * mm});
            skLineSegment(sketch, "E3.14.0.84", {"start": v(6.63, -34.03) * mm, "end": v(6.13, -34.52) * mm});
            skLineSegment(sketch, "E3.14.0.85", {"start": v(6.62, -21.88) * mm, "end": v(6.12, -22.38) * mm});
            skLineSegment(sketch, "E3.14.0.86", {"start": v(6.6, -9.73) * mm, "end": v(6.1, -10.23) * mm});
            skLineSegment(sketch, "E3.14.0.87", {"start": v(6.57, 19.65) * mm, "end": v(6.07, 20.15) * mm});
            skLineSegment(sketch, "E3.14.0.88", {"start": v(6.63, -41.1) * mm, "end": v(6.13, -40.6) * mm});
            skLineSegment(sketch, "E3.14.0.89", {"start": v(10.1, 35.34) * mm, "end": v(9.6, 34.84) * mm});
            skLineSegment(sketch, "E3.14.0.90", {"start": v(10.09, 41.41) * mm, "end": v(9.6, 40.91) * mm});
            skLineSegment(sketch, "E3.14.0.91", {"start": v(10.1, 35.34) * mm, "end": v(6.56, 31.8) * mm});
            skLineSegment(sketch, "E3.14.0.92", {"start": v(9.6, 35.83) * mm, "end": v(6.06, 32.3) * mm});
            skLineSegment(sketch, "E3.14.0.93", {"start": v(6.56, 38.87) * mm, "end": v(6.06, 38.37) * mm});
            skLineSegment(sketch, "E3.14.0.94", {"start": v(6.13, -28.45) * mm, "end": v(9.66, -31.99) * mm});
            skLineSegment(sketch, "E3.14.0.95", {"start": v(6.07, 32.3) * mm, "end": v(9.6, 28.76) * mm});
            skLineSegment(sketch, "E3.14.0.96", {"start": v(6.11, -16.3) * mm, "end": v(9.65, -19.84) * mm});
            skLineSegment(sketch, "E3.14.0.97", {"start": v(6.1, -4.15) * mm, "end": v(9.64, -7.69) * mm});
            skLineSegment(sketch, "E3.14.0.98", {"start": v(6.08, 20.15) * mm, "end": v(9.62, 16.61) * mm});
            skLineSegment(sketch, "E3.14.0.99", {"start": v(10.1, 29.26) * mm, "end": v(6.57, 25.73) * mm});
            skLineSegment(sketch, "E3.14.0.100", {"start": v(10.11, 17.11) * mm, "end": v(6.58, 13.58) * mm});
            skLineSegment(sketch, "E3.14.0.101", {"start": v(9.6, 29.76) * mm, "end": v(6.07, 26.22) * mm});
            skLineSegment(sketch, "E3.14.0.102", {"start": v(9.62, 17.6) * mm, "end": v(6.08, 14.07) * mm});
            skLineSegment(sketch, "E3.14.0.103", {"start": v(6.58, 20.65) * mm, "end": v(6.08, 20.15) * mm});
            skLineSegment(sketch, "E3.14.0.104", {"start": v(10.15, -19.34) * mm, "end": v(9.65, -19.84) * mm});
            skLineSegment(sketch, "E3.14.0.105", {"start": v(10.14, -7.19) * mm, "end": v(9.64, -7.69) * mm});
            skLineSegment(sketch, "E3.14.0.106", {"start": v(10.12, 4.96) * mm, "end": v(9.63, 4.46) * mm});
            skLineSegment(sketch, "E3.14.0.107", {"start": v(10.16, -31.49) * mm, "end": v(9.66, -31.99) * mm});
            skLineSegment(sketch, "E3.14.0.108", {"start": v(10.1, 29.26) * mm, "end": v(9.6, 29.76) * mm});
            skLineSegment(sketch, "E3.14.0.109", {"start": v(10.11, 17.11) * mm, "end": v(9.62, 17.6) * mm});
            skLineSegment(sketch, "E3.14.0.110", {"start": v(6.58, 13.58) * mm, "end": v(6.08, 14.07) * mm});
            skLineSegment(sketch, "E3.14.0.111", {"start": v(6.57, 25.73) * mm, "end": v(6.07, 26.22) * mm});
            skLineSegment(sketch, "E3.14.0.112", {"start": v(6.6, -16.8) * mm, "end": v(6.1, -16.3) * mm});
            skLineSegment(sketch, "E3.14.0.113", {"start": v(6.6, -4.65) * mm, "end": v(6.1, -4.15) * mm});
            skLineSegment(sketch, "E3.14.0.114", {"start": v(6.62, -28.95) * mm, "end": v(6.12, -28.45) * mm});
            skLineSegment(sketch, "E3.14.0.115", {"start": v(10.1, 35.34) * mm, "end": v(9.6, 35.83) * mm});
            skLineSegment(sketch, "E3.14.0.116", {"start": v(6.56, 31.8) * mm, "end": v(6.06, 32.3) * mm});
            skLineSegment(sketch, "E3.14.0.117", {"start": v(6.55, 37.87) * mm, "end": v(6.06, 38.37) * mm});
            skLineSegment(sketch, "E3.14.0.118", {"start": v(6.57, 32.8) * mm, "end": v(6.07, 32.3) * mm});
            skLineSegment(sketch, "E3.14.0.119", {"start": v(10.1, 29.26) * mm, "end": v(9.6, 28.76) * mm});
            skLineSegment(sketch, "E3.14.0.120", {"start": v(10.11, 17.11) * mm, "end": v(9.62, 16.61) * mm});
            skLineSegment(sketch, "E3.15.0.0", {"start": v(11.95, 44.95) * mm, "end": v(15.49, 41.41) * mm});
            skLineSegment(sketch, "E3.15.0.1", {"start": v(11.46, 44.45) * mm, "end": v(15, 40.91) * mm});
            skLineSegment(sketch, "E3.15.0.2", {"start": v(11.95, 44.95) * mm, "end": v(11.46, 44.45) * mm});
            skLineSegment(sketch, "E3.15.0.3", {"start": v(15.57, -43.64) * mm, "end": v(12.04, -47.17) * mm});
            skLineSegment(sketch, "E3.15.0.4", {"start": v(15.07, -43.14) * mm, "end": v(11.54, -46.68) * mm});
            skLineSegment(sketch, "E3.15.0.5", {"start": v(12.04, -47.17) * mm, "end": v(11.54, -46.68) * mm});
            skLineSegment(sketch, "E3.15.0.6", {"start": v(11.99, 8.5) * mm, "end": v(15.52, 4.96) * mm});
            skLineSegment(sketch, "E3.15.0.7", {"start": v(15.57, -43.64) * mm, "end": v(15.07, -43.14) * mm});
            skLineSegment(sketch, "E3.15.0.8", {"start": v(15.52, 11.04) * mm, "end": v(11.98, 7.5) * mm});
            skLineSegment(sketch, "E3.15.0.9", {"start": v(15.57, -37.56) * mm, "end": v(12.03, -41.1) * mm});
            skLineSegment(sketch, "E3.15.0.10", {"start": v(15.55, -25.41) * mm, "end": v(12.02, -28.95) * mm});
            skLineSegment(sketch, "E3.15.0.11", {"start": v(15.02, 11.53) * mm, "end": v(11.49, 8) * mm});
            skLineSegment(sketch, "E3.15.0.12", {"start": v(15, 23.68) * mm, "end": v(11.47, 20.15) * mm});
            skLineSegment(sketch, "E3.15.0.13", {"start": v(12, 2.42) * mm, "end": v(15.53, -1.11) * mm});
            skLineSegment(sketch, "E3.15.0.14", {"start": v(11.98, 14.57) * mm, "end": v(15.52, 11.04) * mm});
            skLineSegment(sketch, "E3.15.0.15", {"start": v(11.97, 26.72) * mm, "end": v(15.5, 23.19) * mm});
            skLineSegment(sketch, "E3.15.0.16", {"start": v(12.03, -34.03) * mm, "end": v(15.57, -37.56) * mm});
            skLineSegment(sketch, "E3.15.0.17", {"start": v(12.02, -21.88) * mm, "end": v(15.55, -25.41) * mm});
            skLineSegment(sketch, "E3.15.0.18", {"start": v(12, -9.73) * mm, "end": v(15.54, -13.26) * mm});
            skLineSegment(sketch, "E3.15.0.19", {"start": v(15.54, -13.26) * mm, "end": v(15.04, -13.76) * mm});
            skLineSegment(sketch, "E3.15.0.20", {"start": v(15.53, -1.11) * mm, "end": v(15.03, -1.61) * mm});
            skLineSegment(sketch, "E3.15.0.21", {"start": v(15.52, 11.04) * mm, "end": v(15.02, 10.54) * mm});
            skLineSegment(sketch, "E3.15.0.22", {"start": v(15.5, 23.19) * mm, "end": v(15, 22.69) * mm});
            skLineSegment(sketch, "E3.15.0.23", {"start": v(15.57, -37.56) * mm, "end": v(15.07, -38.06) * mm});
            skLineSegment(sketch, "E3.15.0.24", {"start": v(15.55, -25.41) * mm, "end": v(15.06, -25.91) * mm});
            skLineSegment(sketch, "E3.15.0.25", {"start": v(15.54, -13.26) * mm, "end": v(15.04, -12.77) * mm});
            skLineSegment(sketch, "E3.15.0.26", {"start": v(15.53, -1.11) * mm, "end": v(15.03, -0.62) * mm});
            skLineSegment(sketch, "E3.15.0.27", {"start": v(15.52, 11.04) * mm, "end": v(15.02, 11.53) * mm});
            skLineSegment(sketch, "E3.15.0.28", {"start": v(15.5, 23.19) * mm, "end": v(15, 23.68) * mm});
            skLineSegment(sketch, "E3.15.0.29", {"start": v(15.57, -37.56) * mm, "end": v(15.07, -37.07) * mm});
            skLineSegment(sketch, "E3.15.0.30", {"start": v(15.55, -25.41) * mm, "end": v(15.06, -24.92) * mm});
            skLineSegment(sketch, "E3.15.0.31", {"start": v(11.98, 7.5) * mm, "end": v(11.49, 8) * mm});
            skLineSegment(sketch, "E3.15.0.32", {"start": v(15.49, 41.41) * mm, "end": v(11.95, 37.87) * mm});
            skLineSegment(sketch, "E3.15.0.33", {"start": v(15, 41.9) * mm, "end": v(11.46, 38.37) * mm});
            skLineSegment(sketch, "E3.15.0.34", {"start": v(15.49, 41.41) * mm, "end": v(15, 41.9) * mm});
            skLineSegment(sketch, "E3.15.0.35", {"start": v(11.46, 38.37) * mm, "end": v(15, 34.84) * mm});
            skLineSegment(sketch, "E3.15.0.36", {"start": v(11.96, 38.87) * mm, "end": v(15.5, 35.34) * mm});
            skLineSegment(sketch, "E3.15.0.37", {"start": v(11.54, -40.6) * mm, "end": v(15.07, -44.14) * mm});
            skLineSegment(sketch, "E3.15.0.38", {"start": v(11.5, 8) * mm, "end": v(15.03, 4.46) * mm});
            skLineSegment(sketch, "E3.15.0.39", {"start": v(15.55, -19.34) * mm, "end": v(12.01, -22.87) * mm});
            skLineSegment(sketch, "E3.15.0.40", {"start": v(15.54, -7.19) * mm, "end": v(12, -10.72) * mm});
            skLineSegment(sketch, "E3.15.0.41", {"start": v(15.52, 4.96) * mm, "end": v(11.99, 1.43) * mm});
            skLineSegment(sketch, "E3.15.0.42", {"start": v(15.56, -31.49) * mm, "end": v(12.02, -35.02) * mm});
            skLineSegment(sketch, "E3.15.0.43", {"start": v(15.05, -18.84) * mm, "end": v(11.51, -22.38) * mm});
            skLineSegment(sketch, "E3.15.0.44", {"start": v(15.04, -6.7) * mm, "end": v(11.5, -10.23) * mm});
            skLineSegment(sketch, "E3.15.0.45", {"start": v(15.03, 5.46) * mm, "end": v(11.5, 1.92) * mm});
            skLineSegment(sketch, "E3.15.0.46", {"start": v(15.06, -31) * mm, "end": v(11.53, -34.53) * mm});
            skLineSegment(sketch, "E3.15.0.47", {"start": v(12.01, -15.8) * mm, "end": v(15.55, -19.34) * mm});
            skLineSegment(sketch, "E3.15.0.48", {"start": v(12, -3.65) * mm, "end": v(15.54, -7.19) * mm});
            skLineSegment(sketch, "E3.15.0.49", {"start": v(11.97, 32.8) * mm, "end": v(15.5, 29.26) * mm});
            skLineSegment(sketch, "E3.15.0.50", {"start": v(12.04, -40.1) * mm, "end": v(15.57, -43.64) * mm});
            skLineSegment(sketch, "E3.15.0.51", {"start": v(12.02, -27.95) * mm, "end": v(15.56, -31.49) * mm});
            skLineSegment(sketch, "E3.15.0.52", {"start": v(11.98, 20.65) * mm, "end": v(15.51, 17.11) * mm});
            skLineSegment(sketch, "E3.15.0.53", {"start": v(12.01, -15.8) * mm, "end": v(11.51, -16.3) * mm});
            skLineSegment(sketch, "E3.15.0.54", {"start": v(12, -3.65) * mm, "end": v(11.5, -4.15) * mm});
            skLineSegment(sketch, "E3.15.0.55", {"start": v(11.99, 8.5) * mm, "end": v(11.5, 8) * mm});
            skLineSegment(sketch, "E3.15.0.56", {"start": v(12.04, -40.1) * mm, "end": v(11.54, -40.6) * mm});
            skLineSegment(sketch, "E3.15.0.57", {"start": v(12.02, -27.95) * mm, "end": v(11.53, -28.45) * mm});
            skLineSegment(sketch, "E3.15.0.58", {"start": v(15.57, -43.64) * mm, "end": v(15.07, -44.14) * mm});
            skLineSegment(sketch, "E3.15.0.59", {"start": v(15.55, -19.34) * mm, "end": v(15.05, -18.84) * mm});
            skLineSegment(sketch, "E3.15.0.60", {"start": v(15.54, -7.19) * mm, "end": v(15.04, -6.7) * mm});
            skLineSegment(sketch, "E3.15.0.61", {"start": v(15.52, 4.96) * mm, "end": v(15.03, 5.46) * mm});
            skLineSegment(sketch, "E3.15.0.62", {"start": v(15.56, -31.49) * mm, "end": v(15.06, -31) * mm});
            skLineSegment(sketch, "E3.15.0.63", {"start": v(11.99, 1.43) * mm, "end": v(11.5, 1.92) * mm});
            skLineSegment(sketch, "E3.15.0.64", {"start": v(12.02, -35.02) * mm, "end": v(11.53, -34.53) * mm});
            skLineSegment(sketch, "E3.15.0.65", {"start": v(12.01, -22.87) * mm, "end": v(11.51, -22.38) * mm});
            skLineSegment(sketch, "E3.15.0.66", {"start": v(12, -10.72) * mm, "end": v(11.5, -10.23) * mm});
            skLineSegment(sketch, "E3.15.0.67", {"start": v(11.5, 1.92) * mm, "end": v(15.03, -1.61) * mm});
            skLineSegment(sketch, "E3.15.0.68", {"start": v(11.49, 14.07) * mm, "end": v(15.02, 10.54) * mm});
            skLineSegment(sketch, "E3.15.0.69", {"start": v(11.47, 26.22) * mm, "end": v(15, 22.69) * mm});
            skLineSegment(sketch, "E3.15.0.70", {"start": v(11.95, 37.87) * mm, "end": v(11.96, 31.8) * mm, "construction": true});
            skLineSegment(sketch, "E3.15.0.71", {"start": v(11.53, -34.52) * mm, "end": v(15.07, -38.06) * mm});
            skLineSegment(sketch, "E3.15.0.72", {"start": v(11.52, -22.38) * mm, "end": v(15.06, -25.91) * mm});
            skLineSegment(sketch, "E3.15.0.73", {"start": v(11.5, -10.23) * mm, "end": v(15.04, -13.76) * mm});
            skLineSegment(sketch, "E3.15.0.74", {"start": v(15.53, -1.11) * mm, "end": v(12, -4.65) * mm});
            skLineSegment(sketch, "E3.15.0.75", {"start": v(15.5, 23.19) * mm, "end": v(11.97, 19.65) * mm});
            skLineSegment(sketch, "E3.15.0.76", {"start": v(15.54, -13.26) * mm, "end": v(12, -16.8) * mm});
            skLineSegment(sketch, "E3.15.0.77", {"start": v(15.03, -0.62) * mm, "end": v(11.5, -4.15) * mm});
            skLineSegment(sketch, "E3.15.0.78", {"start": v(15.07, -37.07) * mm, "end": v(11.53, -40.6) * mm});
            skLineSegment(sketch, "E3.15.0.79", {"start": v(15.06, -24.92) * mm, "end": v(11.52, -28.45) * mm});
            skLineSegment(sketch, "E3.15.0.80", {"start": v(15.04, -12.77) * mm, "end": v(11.5, -16.3) * mm});
            skLineSegment(sketch, "E3.15.0.81", {"start": v(12, 2.42) * mm, "end": v(11.5, 1.92) * mm});
            skLineSegment(sketch, "E3.15.0.82", {"start": v(11.98, 14.57) * mm, "end": v(11.49, 14.07) * mm});
            skLineSegment(sketch, "E3.15.0.83", {"start": v(11.97, 26.72) * mm, "end": v(11.47, 26.22) * mm});
            skLineSegment(sketch, "E3.15.0.84", {"start": v(12.03, -34.03) * mm, "end": v(11.53, -34.52) * mm});
            skLineSegment(sketch, "E3.15.0.85", {"start": v(12.02, -21.88) * mm, "end": v(11.52, -22.38) * mm});
            skLineSegment(sketch, "E3.15.0.86", {"start": v(12, -9.73) * mm, "end": v(11.5, -10.23) * mm});
            skLineSegment(sketch, "E3.15.0.87", {"start": v(11.97, 19.65) * mm, "end": v(11.47, 20.15) * mm});
            skLineSegment(sketch, "E3.15.0.88", {"start": v(12.03, -41.1) * mm, "end": v(11.53, -40.6) * mm});
            skLineSegment(sketch, "E3.15.0.89", {"start": v(15.5, 35.34) * mm, "end": v(15, 34.84) * mm});
            skLineSegment(sketch, "E3.15.0.90", {"start": v(15.49, 41.41) * mm, "end": v(15, 40.91) * mm});
            skLineSegment(sketch, "E3.15.0.91", {"start": v(15.5, 35.34) * mm, "end": v(11.96, 31.8) * mm});
            skLineSegment(sketch, "E3.15.0.92", {"start": v(15, 35.83) * mm, "end": v(11.46, 32.3) * mm});
            skLineSegment(sketch, "E3.15.0.93", {"start": v(11.96, 38.87) * mm, "end": v(11.46, 38.37) * mm});
            skLineSegment(sketch, "E3.15.0.94", {"start": v(11.53, -28.45) * mm, "end": v(15.06, -31.99) * mm});
            skLineSegment(sketch, "E3.15.0.95", {"start": v(11.47, 32.3) * mm, "end": v(15, 28.76) * mm});
            skLineSegment(sketch, "E3.15.0.96", {"start": v(11.51, -16.3) * mm, "end": v(15.05, -19.84) * mm});
            skLineSegment(sketch, "E3.15.0.97", {"start": v(11.5, -4.15) * mm, "end": v(15.04, -7.69) * mm});
            skLineSegment(sketch, "E3.15.0.98", {"start": v(11.48, 20.15) * mm, "end": v(15.02, 16.61) * mm});
            skLineSegment(sketch, "E3.15.0.99", {"start": v(15.5, 29.26) * mm, "end": v(11.97, 25.73) * mm});
            skLineSegment(sketch, "E3.15.0.100", {"start": v(15.51, 17.11) * mm, "end": v(11.98, 13.58) * mm});
            skLineSegment(sketch, "E3.15.0.101", {"start": v(15, 29.76) * mm, "end": v(11.47, 26.22) * mm});
            skLineSegment(sketch, "E3.15.0.102", {"start": v(15.02, 17.6) * mm, "end": v(11.48, 14.07) * mm});
            skLineSegment(sketch, "E3.15.0.103", {"start": v(11.98, 20.65) * mm, "end": v(11.48, 20.15) * mm});
            skLineSegment(sketch, "E3.15.0.104", {"start": v(15.55, -19.34) * mm, "end": v(15.05, -19.84) * mm});
            skLineSegment(sketch, "E3.15.0.105", {"start": v(15.54, -7.19) * mm, "end": v(15.04, -7.69) * mm});
            skLineSegment(sketch, "E3.15.0.106", {"start": v(15.52, 4.96) * mm, "end": v(15.03, 4.46) * mm});
            skLineSegment(sketch, "E3.15.0.107", {"start": v(15.56, -31.49) * mm, "end": v(15.06, -31.99) * mm});
            skLineSegment(sketch, "E3.15.0.108", {"start": v(15.5, 29.26) * mm, "end": v(15, 29.76) * mm});
            skLineSegment(sketch, "E3.15.0.109", {"start": v(15.51, 17.11) * mm, "end": v(15.02, 17.6) * mm});
            skLineSegment(sketch, "E3.15.0.110", {"start": v(11.98, 13.58) * mm, "end": v(11.48, 14.07) * mm});
            skLineSegment(sketch, "E3.15.0.111", {"start": v(11.97, 25.73) * mm, "end": v(11.47, 26.22) * mm});
            skLineSegment(sketch, "E3.15.0.112", {"start": v(12, -16.8) * mm, "end": v(11.5, -16.3) * mm});
            skLineSegment(sketch, "E3.15.0.113", {"start": v(12, -4.65) * mm, "end": v(11.5, -4.15) * mm});
            skLineSegment(sketch, "E3.15.0.114", {"start": v(12.02, -28.95) * mm, "end": v(11.52, -28.45) * mm});
            skLineSegment(sketch, "E3.15.0.115", {"start": v(15.5, 35.34) * mm, "end": v(15, 35.83) * mm});
            skLineSegment(sketch, "E3.15.0.116", {"start": v(11.96, 31.8) * mm, "end": v(11.46, 32.3) * mm});
            skLineSegment(sketch, "E3.15.0.117", {"start": v(11.95, 37.87) * mm, "end": v(11.46, 38.37) * mm});
            skLineSegment(sketch, "E3.15.0.118", {"start": v(11.97, 32.8) * mm, "end": v(11.47, 32.3) * mm});
            skLineSegment(sketch, "E3.15.0.119", {"start": v(15.5, 29.26) * mm, "end": v(15, 28.76) * mm});
            skLineSegment(sketch, "E3.15.0.120", {"start": v(15.51, 17.11) * mm, "end": v(15.02, 16.61) * mm});
            skLineSegment(sketch, "E3.16.0.0", {"start": v(17.35, 44.95) * mm, "end": v(20.89, 41.41) * mm});
            skLineSegment(sketch, "E3.16.0.1", {"start": v(16.86, 44.45) * mm, "end": v(20.4, 40.91) * mm});
            skLineSegment(sketch, "E3.16.0.2", {"start": v(17.35, 44.95) * mm, "end": v(16.86, 44.45) * mm});
            skLineSegment(sketch, "E3.16.0.3", {"start": v(20.97, -43.64) * mm, "end": v(17.44, -47.17) * mm});
            skLineSegment(sketch, "E3.16.0.4", {"start": v(20.47, -43.14) * mm, "end": v(16.94, -46.68) * mm});
            skLineSegment(sketch, "E3.16.0.5", {"start": v(17.44, -47.17) * mm, "end": v(16.94, -46.68) * mm});
            skLineSegment(sketch, "E3.16.0.6", {"start": v(17.39, 8.5) * mm, "end": v(20.92, 4.96) * mm});
            skLineSegment(sketch, "E3.16.0.7", {"start": v(20.97, -43.64) * mm, "end": v(20.47, -43.14) * mm});
            skLineSegment(sketch, "E3.16.0.8", {"start": v(20.92, 11.04) * mm, "end": v(17.38, 7.5) * mm});
            skLineSegment(sketch, "E3.16.0.9", {"start": v(20.97, -37.56) * mm, "end": v(17.43, -41.1) * mm});
            skLineSegment(sketch, "E3.16.0.10", {"start": v(20.95, -25.41) * mm, "end": v(17.42, -28.95) * mm});
            skLineSegment(sketch, "E3.16.0.11", {"start": v(20.42, 11.53) * mm, "end": v(16.89, 8) * mm});
            skLineSegment(sketch, "E3.16.0.12", {"start": v(20.4, 23.68) * mm, "end": v(16.87, 20.15) * mm});
            skLineSegment(sketch, "E3.16.0.13", {"start": v(17.4, 2.42) * mm, "end": v(20.93, -1.11) * mm});
            skLineSegment(sketch, "E3.16.0.14", {"start": v(17.38, 14.57) * mm, "end": v(20.92, 11.04) * mm});
            skLineSegment(sketch, "E3.16.0.15", {"start": v(17.37, 26.72) * mm, "end": v(20.9, 23.19) * mm});
            skLineSegment(sketch, "E3.16.0.16", {"start": v(17.43, -34.03) * mm, "end": v(20.97, -37.56) * mm});
            skLineSegment(sketch, "E3.16.0.17", {"start": v(17.42, -21.88) * mm, "end": v(20.95, -25.41) * mm});
            skLineSegment(sketch, "E3.16.0.18", {"start": v(17.4, -9.73) * mm, "end": v(20.94, -13.26) * mm});
            skLineSegment(sketch, "E3.16.0.19", {"start": v(20.94, -13.26) * mm, "end": v(20.44, -13.76) * mm});
            skLineSegment(sketch, "E3.16.0.20", {"start": v(20.93, -1.11) * mm, "end": v(20.43, -1.61) * mm});
            skLineSegment(sketch, "E3.16.0.21", {"start": v(20.92, 11.04) * mm, "end": v(20.42, 10.54) * mm});
            skLineSegment(sketch, "E3.16.0.22", {"start": v(20.9, 23.19) * mm, "end": v(20.4, 22.69) * mm});
            skLineSegment(sketch, "E3.16.0.23", {"start": v(20.97, -37.56) * mm, "end": v(20.47, -38.06) * mm});
            skLineSegment(sketch, "E3.16.0.24", {"start": v(20.95, -25.41) * mm, "end": v(20.46, -25.91) * mm});
            skLineSegment(sketch, "E3.16.0.25", {"start": v(20.94, -13.26) * mm, "end": v(20.44, -12.77) * mm});
            skLineSegment(sketch, "E3.16.0.26", {"start": v(20.93, -1.11) * mm, "end": v(20.43, -0.62) * mm});
            skLineSegment(sketch, "E3.16.0.27", {"start": v(20.92, 11.04) * mm, "end": v(20.42, 11.53) * mm});
            skLineSegment(sketch, "E3.16.0.28", {"start": v(20.9, 23.19) * mm, "end": v(20.4, 23.68) * mm});
            skLineSegment(sketch, "E3.16.0.29", {"start": v(20.97, -37.56) * mm, "end": v(20.47, -37.07) * mm});
            skLineSegment(sketch, "E3.16.0.30", {"start": v(20.95, -25.41) * mm, "end": v(20.46, -24.92) * mm});
            skLineSegment(sketch, "E3.16.0.31", {"start": v(17.38, 7.5) * mm, "end": v(16.89, 8) * mm});
            skLineSegment(sketch, "E3.16.0.32", {"start": v(20.89, 41.41) * mm, "end": v(17.35, 37.87) * mm});
            skLineSegment(sketch, "E3.16.0.33", {"start": v(20.4, 41.9) * mm, "end": v(16.86, 38.37) * mm});
            skLineSegment(sketch, "E3.16.0.34", {"start": v(20.89, 41.41) * mm, "end": v(20.4, 41.9) * mm});
            skLineSegment(sketch, "E3.16.0.35", {"start": v(16.86, 38.37) * mm, "end": v(20.4, 34.84) * mm});
            skLineSegment(sketch, "E3.16.0.36", {"start": v(17.36, 38.87) * mm, "end": v(20.9, 35.34) * mm});
            skLineSegment(sketch, "E3.16.0.37", {"start": v(16.94, -40.6) * mm, "end": v(20.47, -44.14) * mm});
            skLineSegment(sketch, "E3.16.0.38", {"start": v(16.9, 8) * mm, "end": v(20.43, 4.46) * mm});
            skLineSegment(sketch, "E3.16.0.39", {"start": v(20.95, -19.34) * mm, "end": v(17.41, -22.87) * mm});
            skLineSegment(sketch, "E3.16.0.40", {"start": v(20.94, -7.19) * mm, "end": v(17.4, -10.72) * mm});
            skLineSegment(sketch, "E3.16.0.41", {"start": v(20.92, 4.96) * mm, "end": v(17.39, 1.43) * mm});
            skLineSegment(sketch, "E3.16.0.42", {"start": v(20.96, -31.49) * mm, "end": v(17.42, -35.02) * mm});
            skLineSegment(sketch, "E3.16.0.43", {"start": v(20.45, -18.84) * mm, "end": v(16.91, -22.38) * mm});
            skLineSegment(sketch, "E3.16.0.44", {"start": v(20.44, -6.7) * mm, "end": v(16.9, -10.23) * mm});
            skLineSegment(sketch, "E3.16.0.45", {"start": v(20.43, 5.46) * mm, "end": v(16.9, 1.92) * mm});
            skLineSegment(sketch, "E3.16.0.46", {"start": v(20.46, -31) * mm, "end": v(16.93, -34.53) * mm});
            skLineSegment(sketch, "E3.16.0.47", {"start": v(17.41, -15.8) * mm, "end": v(20.95, -19.34) * mm});
            skLineSegment(sketch, "E3.16.0.48", {"start": v(17.4, -3.65) * mm, "end": v(20.94, -7.19) * mm});
            skLineSegment(sketch, "E3.16.0.49", {"start": v(17.37, 32.8) * mm, "end": v(20.9, 29.26) * mm});
            skLineSegment(sketch, "E3.16.0.50", {"start": v(17.44, -40.1) * mm, "end": v(20.97, -43.64) * mm});
            skLineSegment(sketch, "E3.16.0.51", {"start": v(17.42, -27.95) * mm, "end": v(20.96, -31.49) * mm});
            skLineSegment(sketch, "E3.16.0.52", {"start": v(17.38, 20.65) * mm, "end": v(20.91, 17.11) * mm});
            skLineSegment(sketch, "E3.16.0.53", {"start": v(17.41, -15.8) * mm, "end": v(16.91, -16.3) * mm});
            skLineSegment(sketch, "E3.16.0.54", {"start": v(17.4, -3.65) * mm, "end": v(16.9, -4.15) * mm});
            skLineSegment(sketch, "E3.16.0.55", {"start": v(17.39, 8.5) * mm, "end": v(16.9, 8) * mm});
            skLineSegment(sketch, "E3.16.0.56", {"start": v(17.44, -40.1) * mm, "end": v(16.94, -40.6) * mm});
            skLineSegment(sketch, "E3.16.0.57", {"start": v(17.42, -27.95) * mm, "end": v(16.93, -28.45) * mm});
            skLineSegment(sketch, "E3.16.0.58", {"start": v(20.97, -43.64) * mm, "end": v(20.47, -44.14) * mm});
            skLineSegment(sketch, "E3.16.0.59", {"start": v(20.95, -19.34) * mm, "end": v(20.45, -18.84) * mm});
            skLineSegment(sketch, "E3.16.0.60", {"start": v(20.94, -7.19) * mm, "end": v(20.44, -6.7) * mm});
            skLineSegment(sketch, "E3.16.0.61", {"start": v(20.92, 4.96) * mm, "end": v(20.43, 5.46) * mm});
            skLineSegment(sketch, "E3.16.0.62", {"start": v(20.96, -31.49) * mm, "end": v(20.46, -31) * mm});
            skLineSegment(sketch, "E3.16.0.63", {"start": v(17.39, 1.43) * mm, "end": v(16.9, 1.92) * mm});
            skLineSegment(sketch, "E3.16.0.64", {"start": v(17.42, -35.02) * mm, "end": v(16.93, -34.53) * mm});
            skLineSegment(sketch, "E3.16.0.65", {"start": v(17.41, -22.87) * mm, "end": v(16.91, -22.38) * mm});
            skLineSegment(sketch, "E3.16.0.66", {"start": v(17.4, -10.72) * mm, "end": v(16.9, -10.23) * mm});
            skLineSegment(sketch, "E3.16.0.67", {"start": v(16.9, 1.92) * mm, "end": v(20.43, -1.61) * mm});
            skLineSegment(sketch, "E3.16.0.68", {"start": v(16.89, 14.07) * mm, "end": v(20.42, 10.54) * mm});
            skLineSegment(sketch, "E3.16.0.69", {"start": v(16.87, 26.22) * mm, "end": v(20.4, 22.69) * mm});
            skLineSegment(sketch, "E3.16.0.70", {"start": v(17.35, 37.87) * mm, "end": v(17.36, 31.8) * mm, "construction": true});
            skLineSegment(sketch, "E3.16.0.71", {"start": v(16.93, -34.52) * mm, "end": v(20.47, -38.06) * mm});
            skLineSegment(sketch, "E3.16.0.72", {"start": v(16.92, -22.38) * mm, "end": v(20.46, -25.91) * mm});
            skLineSegment(sketch, "E3.16.0.73", {"start": v(16.9, -10.23) * mm, "end": v(20.44, -13.76) * mm});
            skLineSegment(sketch, "E3.16.0.74", {"start": v(20.93, -1.11) * mm, "end": v(17.4, -4.65) * mm});
            skLineSegment(sketch, "E3.16.0.75", {"start": v(20.9, 23.19) * mm, "end": v(17.37, 19.65) * mm});
            skLineSegment(sketch, "E3.16.0.76", {"start": v(20.94, -13.26) * mm, "end": v(17.4, -16.8) * mm});
            skLineSegment(sketch, "E3.16.0.77", {"start": v(20.43, -0.62) * mm, "end": v(16.9, -4.15) * mm});
            skLineSegment(sketch, "E3.16.0.78", {"start": v(20.47, -37.07) * mm, "end": v(16.93, -40.6) * mm});
            skLineSegment(sketch, "E3.16.0.79", {"start": v(20.46, -24.92) * mm, "end": v(16.92, -28.45) * mm});
            skLineSegment(sketch, "E3.16.0.80", {"start": v(20.44, -12.77) * mm, "end": v(16.9, -16.3) * mm});
            skLineSegment(sketch, "E3.16.0.81", {"start": v(17.4, 2.42) * mm, "end": v(16.9, 1.92) * mm});
            skLineSegment(sketch, "E3.16.0.82", {"start": v(17.38, 14.57) * mm, "end": v(16.89, 14.07) * mm});
            skLineSegment(sketch, "E3.16.0.83", {"start": v(17.37, 26.72) * mm, "end": v(16.87, 26.22) * mm});
            skLineSegment(sketch, "E3.16.0.84", {"start": v(17.43, -34.03) * mm, "end": v(16.93, -34.52) * mm});
            skLineSegment(sketch, "E3.16.0.85", {"start": v(17.42, -21.88) * mm, "end": v(16.92, -22.38) * mm});
            skLineSegment(sketch, "E3.16.0.86", {"start": v(17.4, -9.73) * mm, "end": v(16.9, -10.23) * mm});
            skLineSegment(sketch, "E3.16.0.87", {"start": v(17.37, 19.65) * mm, "end": v(16.87, 20.15) * mm});
            skLineSegment(sketch, "E3.16.0.88", {"start": v(17.43, -41.1) * mm, "end": v(16.93, -40.6) * mm});
            skLineSegment(sketch, "E3.16.0.89", {"start": v(20.9, 35.34) * mm, "end": v(20.4, 34.84) * mm});
            skLineSegment(sketch, "E3.16.0.90", {"start": v(20.89, 41.41) * mm, "end": v(20.4, 40.91) * mm});
            skLineSegment(sketch, "E3.16.0.91", {"start": v(20.9, 35.34) * mm, "end": v(17.36, 31.8) * mm});
            skLineSegment(sketch, "E3.16.0.92", {"start": v(20.4, 35.83) * mm, "end": v(16.86, 32.3) * mm});
            skLineSegment(sketch, "E3.16.0.93", {"start": v(17.36, 38.87) * mm, "end": v(16.86, 38.37) * mm});
            skLineSegment(sketch, "E3.16.0.94", {"start": v(16.93, -28.45) * mm, "end": v(20.46, -31.99) * mm});
            skLineSegment(sketch, "E3.16.0.95", {"start": v(16.87, 32.3) * mm, "end": v(20.4, 28.76) * mm});
            skLineSegment(sketch, "E3.16.0.96", {"start": v(16.91, -16.3) * mm, "end": v(20.45, -19.84) * mm});
            skLineSegment(sketch, "E3.16.0.97", {"start": v(16.9, -4.15) * mm, "end": v(20.44, -7.69) * mm});
            skLineSegment(sketch, "E3.16.0.98", {"start": v(16.88, 20.15) * mm, "end": v(20.42, 16.61) * mm});
            skLineSegment(sketch, "E3.16.0.99", {"start": v(20.9, 29.26) * mm, "end": v(17.37, 25.73) * mm});
            skLineSegment(sketch, "E3.16.0.100", {"start": v(20.91, 17.11) * mm, "end": v(17.38, 13.58) * mm});
            skLineSegment(sketch, "E3.16.0.101", {"start": v(20.4, 29.76) * mm, "end": v(16.87, 26.22) * mm});
            skLineSegment(sketch, "E3.16.0.102", {"start": v(20.42, 17.6) * mm, "end": v(16.88, 14.07) * mm});
            skLineSegment(sketch, "E3.16.0.103", {"start": v(17.38, 20.65) * mm, "end": v(16.88, 20.15) * mm});
            skLineSegment(sketch, "E3.16.0.104", {"start": v(20.95, -19.34) * mm, "end": v(20.45, -19.84) * mm});
            skLineSegment(sketch, "E3.16.0.105", {"start": v(20.94, -7.19) * mm, "end": v(20.44, -7.69) * mm});
            skLineSegment(sketch, "E3.16.0.106", {"start": v(20.92, 4.96) * mm, "end": v(20.43, 4.46) * mm});
            skLineSegment(sketch, "E3.16.0.107", {"start": v(20.96, -31.49) * mm, "end": v(20.46, -31.99) * mm});
            skLineSegment(sketch, "E3.16.0.108", {"start": v(20.9, 29.26) * mm, "end": v(20.4, 29.76) * mm});
            skLineSegment(sketch, "E3.16.0.109", {"start": v(20.91, 17.11) * mm, "end": v(20.42, 17.6) * mm});
            skLineSegment(sketch, "E3.16.0.110", {"start": v(17.38, 13.58) * mm, "end": v(16.88, 14.07) * mm});
            skLineSegment(sketch, "E3.16.0.111", {"start": v(17.37, 25.73) * mm, "end": v(16.87, 26.22) * mm});
            skLineSegment(sketch, "E3.16.0.112", {"start": v(17.4, -16.8) * mm, "end": v(16.9, -16.3) * mm});
            skLineSegment(sketch, "E3.16.0.113", {"start": v(17.4, -4.65) * mm, "end": v(16.9, -4.15) * mm});
            skLineSegment(sketch, "E3.16.0.114", {"start": v(17.42, -28.95) * mm, "end": v(16.92, -28.45) * mm});
            skLineSegment(sketch, "E3.16.0.115", {"start": v(20.9, 35.34) * mm, "end": v(20.4, 35.83) * mm});
            skLineSegment(sketch, "E3.16.0.116", {"start": v(17.36, 31.8) * mm, "end": v(16.86, 32.3) * mm});
            skLineSegment(sketch, "E3.16.0.117", {"start": v(17.35, 37.87) * mm, "end": v(16.86, 38.37) * mm});
            skLineSegment(sketch, "E3.16.0.118", {"start": v(17.37, 32.8) * mm, "end": v(16.87, 32.3) * mm});
            skLineSegment(sketch, "E3.16.0.119", {"start": v(20.9, 29.26) * mm, "end": v(20.4, 28.76) * mm});
            skLineSegment(sketch, "E3.16.0.120", {"start": v(20.91, 17.11) * mm, "end": v(20.42, 16.61) * mm});
            skLineSegment(sketch, "E3.17.0.0", {"start": v(22.75, 44.95) * mm, "end": v(26.29, 41.41) * mm});
            skLineSegment(sketch, "E3.17.0.1", {"start": v(22.26, 44.45) * mm, "end": v(25.8, 40.91) * mm});
            skLineSegment(sketch, "E3.17.0.2", {"start": v(22.75, 44.95) * mm, "end": v(22.26, 44.45) * mm});
            skLineSegment(sketch, "E3.17.0.3", {"start": v(26.37, -43.64) * mm, "end": v(22.84, -47.17) * mm});
            skLineSegment(sketch, "E3.17.0.4", {"start": v(25.87, -43.14) * mm, "end": v(22.34, -46.68) * mm});
            skLineSegment(sketch, "E3.17.0.5", {"start": v(22.84, -47.17) * mm, "end": v(22.34, -46.68) * mm});
            skLineSegment(sketch, "E3.17.0.6", {"start": v(22.79, 8.5) * mm, "end": v(26.32, 4.96) * mm});
            skLineSegment(sketch, "E3.17.0.7", {"start": v(26.37, -43.64) * mm, "end": v(25.87, -43.14) * mm});
            skLineSegment(sketch, "E3.17.0.8", {"start": v(26.32, 11.04) * mm, "end": v(22.78, 7.5) * mm});
            skLineSegment(sketch, "E3.17.0.9", {"start": v(26.37, -37.56) * mm, "end": v(22.83, -41.1) * mm});
            skLineSegment(sketch, "E3.17.0.10", {"start": v(26.35, -25.41) * mm, "end": v(22.82, -28.95) * mm});
            skLineSegment(sketch, "E3.17.0.11", {"start": v(25.82, 11.53) * mm, "end": v(22.29, 8) * mm});
            skLineSegment(sketch, "E3.17.0.12", {"start": v(25.8, 23.68) * mm, "end": v(22.27, 20.15) * mm});
            skLineSegment(sketch, "E3.17.0.13", {"start": v(22.8, 2.42) * mm, "end": v(26.33, -1.11) * mm});
            skLineSegment(sketch, "E3.17.0.14", {"start": v(22.78, 14.57) * mm, "end": v(26.32, 11.04) * mm});
            skLineSegment(sketch, "E3.17.0.15", {"start": v(22.77, 26.72) * mm, "end": v(26.3, 23.19) * mm});
            skLineSegment(sketch, "E3.17.0.16", {"start": v(22.83, -34.03) * mm, "end": v(26.37, -37.56) * mm});
            skLineSegment(sketch, "E3.17.0.17", {"start": v(22.82, -21.88) * mm, "end": v(26.35, -25.41) * mm});
            skLineSegment(sketch, "E3.17.0.18", {"start": v(22.8, -9.73) * mm, "end": v(26.34, -13.26) * mm});
            skLineSegment(sketch, "E3.17.0.19", {"start": v(26.34, -13.26) * mm, "end": v(25.84, -13.76) * mm});
            skLineSegment(sketch, "E3.17.0.20", {"start": v(26.33, -1.11) * mm, "end": v(25.83, -1.61) * mm});
            skLineSegment(sketch, "E3.17.0.21", {"start": v(26.32, 11.04) * mm, "end": v(25.82, 10.54) * mm});
            skLineSegment(sketch, "E3.17.0.22", {"start": v(26.3, 23.19) * mm, "end": v(25.8, 22.69) * mm});
            skLineSegment(sketch, "E3.17.0.23", {"start": v(26.37, -37.56) * mm, "end": v(25.87, -38.06) * mm});
            skLineSegment(sketch, "E3.17.0.24", {"start": v(26.35, -25.41) * mm, "end": v(25.86, -25.91) * mm});
            skLineSegment(sketch, "E3.17.0.25", {"start": v(26.34, -13.26) * mm, "end": v(25.84, -12.77) * mm});
            skLineSegment(sketch, "E3.17.0.26", {"start": v(26.33, -1.11) * mm, "end": v(25.83, -0.62) * mm});
            skLineSegment(sketch, "E3.17.0.27", {"start": v(26.32, 11.04) * mm, "end": v(25.82, 11.53) * mm});
            skLineSegment(sketch, "E3.17.0.28", {"start": v(26.3, 23.19) * mm, "end": v(25.8, 23.68) * mm});
            skLineSegment(sketch, "E3.17.0.29", {"start": v(26.37, -37.56) * mm, "end": v(25.87, -37.07) * mm});
            skLineSegment(sketch, "E3.17.0.30", {"start": v(26.35, -25.41) * mm, "end": v(25.86, -24.92) * mm});
            skLineSegment(sketch, "E3.17.0.31", {"start": v(22.78, 7.5) * mm, "end": v(22.29, 8) * mm});
            skLineSegment(sketch, "E3.17.0.32", {"start": v(26.29, 41.41) * mm, "end": v(22.75, 37.87) * mm});
            skLineSegment(sketch, "E3.17.0.33", {"start": v(25.8, 41.9) * mm, "end": v(22.26, 38.37) * mm});
            skLineSegment(sketch, "E3.17.0.34", {"start": v(26.29, 41.41) * mm, "end": v(25.8, 41.9) * mm});
            skLineSegment(sketch, "E3.17.0.35", {"start": v(22.26, 38.37) * mm, "end": v(25.8, 34.84) * mm});
            skLineSegment(sketch, "E3.17.0.36", {"start": v(22.76, 38.87) * mm, "end": v(26.3, 35.34) * mm});
            skLineSegment(sketch, "E3.17.0.37", {"start": v(22.34, -40.6) * mm, "end": v(25.87, -44.14) * mm});
            skLineSegment(sketch, "E3.17.0.38", {"start": v(22.3, 8) * mm, "end": v(25.83, 4.46) * mm});
            skLineSegment(sketch, "E3.17.0.39", {"start": v(26.35, -19.34) * mm, "end": v(22.81, -22.87) * mm});
            skLineSegment(sketch, "E3.17.0.40", {"start": v(26.34, -7.19) * mm, "end": v(22.8, -10.72) * mm});
            skLineSegment(sketch, "E3.17.0.41", {"start": v(26.32, 4.96) * mm, "end": v(22.79, 1.43) * mm});
            skLineSegment(sketch, "E3.17.0.42", {"start": v(26.36, -31.49) * mm, "end": v(22.82, -35.02) * mm});
            skLineSegment(sketch, "E3.17.0.43", {"start": v(25.85, -18.84) * mm, "end": v(22.31, -22.38) * mm});
            skLineSegment(sketch, "E3.17.0.44", {"start": v(25.84, -6.7) * mm, "end": v(22.3, -10.23) * mm});
            skLineSegment(sketch, "E3.17.0.45", {"start": v(25.83, 5.46) * mm, "end": v(22.3, 1.92) * mm});
            skLineSegment(sketch, "E3.17.0.46", {"start": v(25.86, -31) * mm, "end": v(22.33, -34.53) * mm});
            skLineSegment(sketch, "E3.17.0.47", {"start": v(22.81, -15.8) * mm, "end": v(26.35, -19.34) * mm});
            skLineSegment(sketch, "E3.17.0.48", {"start": v(22.8, -3.65) * mm, "end": v(26.34, -7.19) * mm});
            skLineSegment(sketch, "E3.17.0.49", {"start": v(22.77, 32.8) * mm, "end": v(26.3, 29.26) * mm});
            skLineSegment(sketch, "E3.17.0.50", {"start": v(22.84, -40.1) * mm, "end": v(26.37, -43.64) * mm});
            skLineSegment(sketch, "E3.17.0.51", {"start": v(22.82, -27.95) * mm, "end": v(26.36, -31.49) * mm});
            skLineSegment(sketch, "E3.17.0.52", {"start": v(22.78, 20.65) * mm, "end": v(26.31, 17.11) * mm});
            skLineSegment(sketch, "E3.17.0.53", {"start": v(22.81, -15.8) * mm, "end": v(22.31, -16.3) * mm});
            skLineSegment(sketch, "E3.17.0.54", {"start": v(22.8, -3.65) * mm, "end": v(22.3, -4.15) * mm});
            skLineSegment(sketch, "E3.17.0.55", {"start": v(22.79, 8.5) * mm, "end": v(22.3, 8) * mm});
            skLineSegment(sketch, "E3.17.0.56", {"start": v(22.84, -40.1) * mm, "end": v(22.34, -40.6) * mm});
            skLineSegment(sketch, "E3.17.0.57", {"start": v(22.82, -27.95) * mm, "end": v(22.33, -28.45) * mm});
            skLineSegment(sketch, "E3.17.0.58", {"start": v(26.37, -43.64) * mm, "end": v(25.87, -44.14) * mm});
            skLineSegment(sketch, "E3.17.0.59", {"start": v(26.35, -19.34) * mm, "end": v(25.85, -18.84) * mm});
            skLineSegment(sketch, "E3.17.0.60", {"start": v(26.34, -7.19) * mm, "end": v(25.84, -6.7) * mm});
            skLineSegment(sketch, "E3.17.0.61", {"start": v(26.32, 4.96) * mm, "end": v(25.83, 5.46) * mm});
            skLineSegment(sketch, "E3.17.0.62", {"start": v(26.36, -31.49) * mm, "end": v(25.86, -31) * mm});
            skLineSegment(sketch, "E3.17.0.63", {"start": v(22.79, 1.43) * mm, "end": v(22.3, 1.92) * mm});
            skLineSegment(sketch, "E3.17.0.64", {"start": v(22.82, -35.02) * mm, "end": v(22.33, -34.53) * mm});
            skLineSegment(sketch, "E3.17.0.65", {"start": v(22.81, -22.87) * mm, "end": v(22.31, -22.38) * mm});
            skLineSegment(sketch, "E3.17.0.66", {"start": v(22.8, -10.72) * mm, "end": v(22.3, -10.23) * mm});
            skLineSegment(sketch, "E3.17.0.67", {"start": v(22.3, 1.92) * mm, "end": v(25.83, -1.61) * mm});
            skLineSegment(sketch, "E3.17.0.68", {"start": v(22.29, 14.07) * mm, "end": v(25.82, 10.54) * mm});
            skLineSegment(sketch, "E3.17.0.69", {"start": v(22.27, 26.22) * mm, "end": v(25.8, 22.69) * mm});
            skLineSegment(sketch, "E3.17.0.70", {"start": v(22.75, 37.87) * mm, "end": v(22.76, 31.8) * mm, "construction": true});
            skLineSegment(sketch, "E3.17.0.71", {"start": v(22.33, -34.52) * mm, "end": v(25.87, -38.06) * mm});
            skLineSegment(sketch, "E3.17.0.72", {"start": v(22.32, -22.38) * mm, "end": v(25.86, -25.91) * mm});
            skLineSegment(sketch, "E3.17.0.73", {"start": v(22.3, -10.23) * mm, "end": v(25.84, -13.76) * mm});
            skLineSegment(sketch, "E3.17.0.74", {"start": v(26.33, -1.11) * mm, "end": v(22.8, -4.65) * mm});
            skLineSegment(sketch, "E3.17.0.75", {"start": v(26.3, 23.19) * mm, "end": v(22.77, 19.65) * mm});
            skLineSegment(sketch, "E3.17.0.76", {"start": v(26.34, -13.26) * mm, "end": v(22.8, -16.8) * mm});
            skLineSegment(sketch, "E3.17.0.77", {"start": v(25.83, -0.62) * mm, "end": v(22.3, -4.15) * mm});
            skLineSegment(sketch, "E3.17.0.78", {"start": v(25.87, -37.07) * mm, "end": v(22.33, -40.6) * mm});
            skLineSegment(sketch, "E3.17.0.79", {"start": v(25.86, -24.92) * mm, "end": v(22.32, -28.45) * mm});
            skLineSegment(sketch, "E3.17.0.80", {"start": v(25.84, -12.77) * mm, "end": v(22.3, -16.3) * mm});
            skLineSegment(sketch, "E3.17.0.81", {"start": v(22.8, 2.42) * mm, "end": v(22.3, 1.92) * mm});
            skLineSegment(sketch, "E3.17.0.82", {"start": v(22.78, 14.57) * mm, "end": v(22.29, 14.07) * mm});
            skLineSegment(sketch, "E3.17.0.83", {"start": v(22.77, 26.72) * mm, "end": v(22.27, 26.22) * mm});
            skLineSegment(sketch, "E3.17.0.84", {"start": v(22.83, -34.03) * mm, "end": v(22.33, -34.52) * mm});
            skLineSegment(sketch, "E3.17.0.85", {"start": v(22.82, -21.88) * mm, "end": v(22.32, -22.38) * mm});
            skLineSegment(sketch, "E3.17.0.86", {"start": v(22.8, -9.73) * mm, "end": v(22.3, -10.23) * mm});
            skLineSegment(sketch, "E3.17.0.87", {"start": v(22.77, 19.65) * mm, "end": v(22.27, 20.15) * mm});
            skLineSegment(sketch, "E3.17.0.88", {"start": v(22.83, -41.1) * mm, "end": v(22.33, -40.6) * mm});
            skLineSegment(sketch, "E3.17.0.89", {"start": v(26.3, 35.34) * mm, "end": v(25.8, 34.84) * mm});
            skLineSegment(sketch, "E3.17.0.90", {"start": v(26.29, 41.41) * mm, "end": v(25.8, 40.91) * mm});
            skLineSegment(sketch, "E3.17.0.91", {"start": v(26.3, 35.34) * mm, "end": v(22.76, 31.8) * mm});
            skLineSegment(sketch, "E3.17.0.92", {"start": v(25.8, 35.83) * mm, "end": v(22.26, 32.3) * mm});
            skLineSegment(sketch, "E3.17.0.93", {"start": v(22.76, 38.87) * mm, "end": v(22.26, 38.37) * mm});
            skLineSegment(sketch, "E3.17.0.94", {"start": v(22.33, -28.45) * mm, "end": v(25.86, -31.99) * mm});
            skLineSegment(sketch, "E3.17.0.95", {"start": v(22.27, 32.3) * mm, "end": v(25.8, 28.76) * mm});
            skLineSegment(sketch, "E3.17.0.96", {"start": v(22.31, -16.3) * mm, "end": v(25.85, -19.84) * mm});
            skLineSegment(sketch, "E3.17.0.97", {"start": v(22.3, -4.15) * mm, "end": v(25.84, -7.69) * mm});
            skLineSegment(sketch, "E3.17.0.98", {"start": v(22.28, 20.15) * mm, "end": v(25.82, 16.61) * mm});
            skLineSegment(sketch, "E3.17.0.99", {"start": v(26.3, 29.26) * mm, "end": v(22.77, 25.73) * mm});
            skLineSegment(sketch, "E3.17.0.100", {"start": v(26.31, 17.11) * mm, "end": v(22.78, 13.58) * mm});
            skLineSegment(sketch, "E3.17.0.101", {"start": v(25.8, 29.76) * mm, "end": v(22.27, 26.22) * mm});
            skLineSegment(sketch, "E3.17.0.102", {"start": v(25.82, 17.6) * mm, "end": v(22.28, 14.07) * mm});
            skLineSegment(sketch, "E3.17.0.103", {"start": v(22.78, 20.65) * mm, "end": v(22.28, 20.15) * mm});
            skLineSegment(sketch, "E3.17.0.104", {"start": v(26.35, -19.34) * mm, "end": v(25.85, -19.84) * mm});
            skLineSegment(sketch, "E3.17.0.105", {"start": v(26.34, -7.19) * mm, "end": v(25.84, -7.69) * mm});
            skLineSegment(sketch, "E3.17.0.106", {"start": v(26.32, 4.96) * mm, "end": v(25.83, 4.46) * mm});
            skLineSegment(sketch, "E3.17.0.107", {"start": v(26.36, -31.49) * mm, "end": v(25.86, -31.99) * mm});
            skLineSegment(sketch, "E3.17.0.108", {"start": v(26.3, 29.26) * mm, "end": v(25.8, 29.76) * mm});
            skLineSegment(sketch, "E3.17.0.109", {"start": v(26.31, 17.11) * mm, "end": v(25.82, 17.6) * mm});
            skLineSegment(sketch, "E3.17.0.110", {"start": v(22.78, 13.58) * mm, "end": v(22.28, 14.07) * mm});
            skLineSegment(sketch, "E3.17.0.111", {"start": v(22.77, 25.73) * mm, "end": v(22.27, 26.22) * mm});
            skLineSegment(sketch, "E3.17.0.112", {"start": v(22.8, -16.8) * mm, "end": v(22.3, -16.3) * mm});
            skLineSegment(sketch, "E3.17.0.113", {"start": v(22.8, -4.65) * mm, "end": v(22.3, -4.15) * mm});
            skLineSegment(sketch, "E3.17.0.114", {"start": v(22.82, -28.95) * mm, "end": v(22.32, -28.45) * mm});
            skLineSegment(sketch, "E3.17.0.115", {"start": v(26.3, 35.34) * mm, "end": v(25.8, 35.83) * mm});
            skLineSegment(sketch, "E3.17.0.116", {"start": v(22.76, 31.8) * mm, "end": v(22.26, 32.3) * mm});
            skLineSegment(sketch, "E3.17.0.117", {"start": v(22.75, 37.87) * mm, "end": v(22.26, 38.37) * mm});
            skLineSegment(sketch, "E3.17.0.118", {"start": v(22.77, 32.8) * mm, "end": v(22.27, 32.3) * mm});
            skLineSegment(sketch, "E3.17.0.119", {"start": v(26.3, 29.26) * mm, "end": v(25.8, 28.76) * mm});
            skLineSegment(sketch, "E3.17.0.120", {"start": v(26.31, 17.11) * mm, "end": v(25.82, 16.61) * mm});
            skLineSegment(sketch, "E3.18.0.0", {"start": v(28.15, 44.95) * mm, "end": v(31.69, 41.41) * mm});
            skLineSegment(sketch, "E3.18.0.1", {"start": v(27.66, 44.45) * mm, "end": v(31.2, 40.91) * mm});
            skLineSegment(sketch, "E3.18.0.2", {"start": v(28.15, 44.95) * mm, "end": v(27.66, 44.45) * mm});
            skLineSegment(sketch, "E3.18.0.3", {"start": v(31.77, -43.64) * mm, "end": v(28.24, -47.17) * mm});
            skLineSegment(sketch, "E3.18.0.4", {"start": v(31.27, -43.14) * mm, "end": v(27.74, -46.68) * mm});
            skLineSegment(sketch, "E3.18.0.5", {"start": v(28.24, -47.17) * mm, "end": v(27.74, -46.68) * mm});
            skLineSegment(sketch, "E3.18.0.6", {"start": v(28.19, 8.5) * mm, "end": v(31.72, 4.96) * mm});
            skLineSegment(sketch, "E3.18.0.7", {"start": v(31.77, -43.64) * mm, "end": v(31.27, -43.14) * mm});
            skLineSegment(sketch, "E3.18.0.8", {"start": v(31.72, 11.04) * mm, "end": v(28.18, 7.5) * mm});
            skLineSegment(sketch, "E3.18.0.9", {"start": v(31.77, -37.56) * mm, "end": v(28.23, -41.1) * mm});
            skLineSegment(sketch, "E3.18.0.10", {"start": v(31.75, -25.41) * mm, "end": v(28.22, -28.95) * mm});
            skLineSegment(sketch, "E3.18.0.11", {"start": v(31.22, 11.53) * mm, "end": v(27.69, 8) * mm});
            skLineSegment(sketch, "E3.18.0.12", {"start": v(31.2, 23.68) * mm, "end": v(27.67, 20.15) * mm});
            skLineSegment(sketch, "E3.18.0.13", {"start": v(28.2, 2.42) * mm, "end": v(31.73, -1.11) * mm});
            skLineSegment(sketch, "E3.18.0.14", {"start": v(28.18, 14.57) * mm, "end": v(31.72, 11.04) * mm});
            skLineSegment(sketch, "E3.18.0.15", {"start": v(28.17, 26.72) * mm, "end": v(31.7, 23.19) * mm});
            skLineSegment(sketch, "E3.18.0.16", {"start": v(28.23, -34.03) * mm, "end": v(31.77, -37.56) * mm});
            skLineSegment(sketch, "E3.18.0.17", {"start": v(28.22, -21.88) * mm, "end": v(31.75, -25.41) * mm});
            skLineSegment(sketch, "E3.18.0.18", {"start": v(28.2, -9.73) * mm, "end": v(31.74, -13.26) * mm});
            skLineSegment(sketch, "E3.18.0.19", {"start": v(31.74, -13.26) * mm, "end": v(31.24, -13.76) * mm});
            skLineSegment(sketch, "E3.18.0.20", {"start": v(31.73, -1.11) * mm, "end": v(31.23, -1.61) * mm});
            skLineSegment(sketch, "E3.18.0.21", {"start": v(31.72, 11.04) * mm, "end": v(31.22, 10.54) * mm});
            skLineSegment(sketch, "E3.18.0.22", {"start": v(31.7, 23.19) * mm, "end": v(31.2, 22.69) * mm});
            skLineSegment(sketch, "E3.18.0.23", {"start": v(31.77, -37.56) * mm, "end": v(31.27, -38.06) * mm});
            skLineSegment(sketch, "E3.18.0.24", {"start": v(31.75, -25.41) * mm, "end": v(31.26, -25.91) * mm});
            skLineSegment(sketch, "E3.18.0.25", {"start": v(31.74, -13.26) * mm, "end": v(31.24, -12.77) * mm});
            skLineSegment(sketch, "E3.18.0.26", {"start": v(31.73, -1.11) * mm, "end": v(31.23, -0.62) * mm});
            skLineSegment(sketch, "E3.18.0.27", {"start": v(31.72, 11.04) * mm, "end": v(31.22, 11.53) * mm});
            skLineSegment(sketch, "E3.18.0.28", {"start": v(31.7, 23.19) * mm, "end": v(31.2, 23.68) * mm});
            skLineSegment(sketch, "E3.18.0.29", {"start": v(31.77, -37.56) * mm, "end": v(31.27, -37.07) * mm});
            skLineSegment(sketch, "E3.18.0.30", {"start": v(31.75, -25.41) * mm, "end": v(31.26, -24.92) * mm});
            skLineSegment(sketch, "E3.18.0.31", {"start": v(28.18, 7.5) * mm, "end": v(27.69, 8) * mm});
            skLineSegment(sketch, "E3.18.0.32", {"start": v(31.69, 41.41) * mm, "end": v(28.15, 37.87) * mm});
            skLineSegment(sketch, "E3.18.0.33", {"start": v(31.2, 41.9) * mm, "end": v(27.66, 38.37) * mm});
            skLineSegment(sketch, "E3.18.0.34", {"start": v(31.69, 41.41) * mm, "end": v(31.2, 41.9) * mm});
            skLineSegment(sketch, "E3.18.0.35", {"start": v(27.66, 38.37) * mm, "end": v(31.2, 34.84) * mm});
            skLineSegment(sketch, "E3.18.0.36", {"start": v(28.16, 38.87) * mm, "end": v(31.7, 35.34) * mm});
            skLineSegment(sketch, "E3.18.0.37", {"start": v(27.74, -40.6) * mm, "end": v(31.27, -44.14) * mm});
            skLineSegment(sketch, "E3.18.0.38", {"start": v(27.7, 8) * mm, "end": v(31.23, 4.46) * mm});
            skLineSegment(sketch, "E3.18.0.39", {"start": v(31.75, -19.34) * mm, "end": v(28.21, -22.87) * mm});
            skLineSegment(sketch, "E3.18.0.40", {"start": v(31.74, -7.19) * mm, "end": v(28.2, -10.72) * mm});
            skLineSegment(sketch, "E3.18.0.41", {"start": v(31.72, 4.96) * mm, "end": v(28.19, 1.43) * mm});
            skLineSegment(sketch, "E3.18.0.42", {"start": v(31.76, -31.49) * mm, "end": v(28.22, -35.02) * mm});
            skLineSegment(sketch, "E3.18.0.43", {"start": v(31.25, -18.84) * mm, "end": v(27.71, -22.38) * mm});
            skLineSegment(sketch, "E3.18.0.44", {"start": v(31.24, -6.7) * mm, "end": v(27.7, -10.23) * mm});
            skLineSegment(sketch, "E3.18.0.45", {"start": v(31.23, 5.46) * mm, "end": v(27.7, 1.92) * mm});
            skLineSegment(sketch, "E3.18.0.46", {"start": v(31.26, -31) * mm, "end": v(27.73, -34.53) * mm});
            skLineSegment(sketch, "E3.18.0.47", {"start": v(28.21, -15.8) * mm, "end": v(31.75, -19.34) * mm});
            skLineSegment(sketch, "E3.18.0.48", {"start": v(28.2, -3.65) * mm, "end": v(31.74, -7.19) * mm});
            skLineSegment(sketch, "E3.18.0.49", {"start": v(28.17, 32.8) * mm, "end": v(31.7, 29.26) * mm});
            skLineSegment(sketch, "E3.18.0.50", {"start": v(28.24, -40.1) * mm, "end": v(31.77, -43.64) * mm});
            skLineSegment(sketch, "E3.18.0.51", {"start": v(28.22, -27.95) * mm, "end": v(31.76, -31.49) * mm});
            skLineSegment(sketch, "E3.18.0.52", {"start": v(28.18, 20.65) * mm, "end": v(31.71, 17.11) * mm});
            skLineSegment(sketch, "E3.18.0.53", {"start": v(28.21, -15.8) * mm, "end": v(27.71, -16.3) * mm});
            skLineSegment(sketch, "E3.18.0.54", {"start": v(28.2, -3.65) * mm, "end": v(27.7, -4.15) * mm});
            skLineSegment(sketch, "E3.18.0.55", {"start": v(28.19, 8.5) * mm, "end": v(27.7, 8) * mm});
            skLineSegment(sketch, "E3.18.0.56", {"start": v(28.24, -40.1) * mm, "end": v(27.74, -40.6) * mm});
            skLineSegment(sketch, "E3.18.0.57", {"start": v(28.22, -27.95) * mm, "end": v(27.73, -28.45) * mm});
            skLineSegment(sketch, "E3.18.0.58", {"start": v(31.77, -43.64) * mm, "end": v(31.27, -44.14) * mm});
            skLineSegment(sketch, "E3.18.0.59", {"start": v(31.75, -19.34) * mm, "end": v(31.25, -18.84) * mm});
            skLineSegment(sketch, "E3.18.0.60", {"start": v(31.74, -7.19) * mm, "end": v(31.24, -6.7) * mm});
            skLineSegment(sketch, "E3.18.0.61", {"start": v(31.72, 4.96) * mm, "end": v(31.23, 5.46) * mm});
            skLineSegment(sketch, "E3.18.0.62", {"start": v(31.76, -31.49) * mm, "end": v(31.26, -31) * mm});
            skLineSegment(sketch, "E3.18.0.63", {"start": v(28.19, 1.43) * mm, "end": v(27.7, 1.92) * mm});
            skLineSegment(sketch, "E3.18.0.64", {"start": v(28.22, -35.02) * mm, "end": v(27.73, -34.53) * mm});
            skLineSegment(sketch, "E3.18.0.65", {"start": v(28.21, -22.87) * mm, "end": v(27.71, -22.38) * mm});
            skLineSegment(sketch, "E3.18.0.66", {"start": v(28.2, -10.72) * mm, "end": v(27.7, -10.23) * mm});
            skLineSegment(sketch, "E3.18.0.67", {"start": v(27.7, 1.92) * mm, "end": v(31.23, -1.61) * mm});
            skLineSegment(sketch, "E3.18.0.68", {"start": v(27.69, 14.07) * mm, "end": v(31.22, 10.54) * mm});
            skLineSegment(sketch, "E3.18.0.69", {"start": v(27.67, 26.22) * mm, "end": v(31.2, 22.69) * mm});
            skLineSegment(sketch, "E3.18.0.70", {"start": v(28.15, 37.87) * mm, "end": v(28.16, 31.8) * mm, "construction": true});
            skLineSegment(sketch, "E3.18.0.71", {"start": v(27.73, -34.52) * mm, "end": v(31.27, -38.06) * mm});
            skLineSegment(sketch, "E3.18.0.72", {"start": v(27.72, -22.38) * mm, "end": v(31.26, -25.91) * mm});
            skLineSegment(sketch, "E3.18.0.73", {"start": v(27.7, -10.23) * mm, "end": v(31.24, -13.76) * mm});
            skLineSegment(sketch, "E3.18.0.74", {"start": v(31.73, -1.11) * mm, "end": v(28.2, -4.65) * mm});
            skLineSegment(sketch, "E3.18.0.75", {"start": v(31.7, 23.19) * mm, "end": v(28.17, 19.65) * mm});
            skLineSegment(sketch, "E3.18.0.76", {"start": v(31.74, -13.26) * mm, "end": v(28.2, -16.8) * mm});
            skLineSegment(sketch, "E3.18.0.77", {"start": v(31.23, -0.62) * mm, "end": v(27.7, -4.15) * mm});
            skLineSegment(sketch, "E3.18.0.78", {"start": v(31.27, -37.07) * mm, "end": v(27.73, -40.6) * mm});
            skLineSegment(sketch, "E3.18.0.79", {"start": v(31.26, -24.92) * mm, "end": v(27.72, -28.45) * mm});
            skLineSegment(sketch, "E3.18.0.80", {"start": v(31.24, -12.77) * mm, "end": v(27.7, -16.3) * mm});
            skLineSegment(sketch, "E3.18.0.81", {"start": v(28.2, 2.42) * mm, "end": v(27.7, 1.92) * mm});
            skLineSegment(sketch, "E3.18.0.82", {"start": v(28.18, 14.57) * mm, "end": v(27.69, 14.07) * mm});
            skLineSegment(sketch, "E3.18.0.83", {"start": v(28.17, 26.72) * mm, "end": v(27.67, 26.22) * mm});
            skLineSegment(sketch, "E3.18.0.84", {"start": v(28.23, -34.03) * mm, "end": v(27.73, -34.52) * mm});
            skLineSegment(sketch, "E3.18.0.85", {"start": v(28.22, -21.88) * mm, "end": v(27.72, -22.38) * mm});
            skLineSegment(sketch, "E3.18.0.86", {"start": v(28.2, -9.73) * mm, "end": v(27.7, -10.23) * mm});
            skLineSegment(sketch, "E3.18.0.87", {"start": v(28.17, 19.65) * mm, "end": v(27.67, 20.15) * mm});
            skLineSegment(sketch, "E3.18.0.88", {"start": v(28.23, -41.1) * mm, "end": v(27.73, -40.6) * mm});
            skLineSegment(sketch, "E3.18.0.89", {"start": v(31.7, 35.34) * mm, "end": v(31.2, 34.84) * mm});
            skLineSegment(sketch, "E3.18.0.90", {"start": v(31.69, 41.41) * mm, "end": v(31.2, 40.91) * mm});
            skLineSegment(sketch, "E3.18.0.91", {"start": v(31.7, 35.34) * mm, "end": v(28.16, 31.8) * mm});
            skLineSegment(sketch, "E3.18.0.92", {"start": v(31.2, 35.83) * mm, "end": v(27.66, 32.3) * mm});
            skLineSegment(sketch, "E3.18.0.93", {"start": v(28.16, 38.87) * mm, "end": v(27.66, 38.37) * mm});
            skLineSegment(sketch, "E3.18.0.94", {"start": v(27.73, -28.45) * mm, "end": v(31.26, -31.99) * mm});
            skLineSegment(sketch, "E3.18.0.95", {"start": v(27.67, 32.3) * mm, "end": v(31.2, 28.76) * mm});
            skLineSegment(sketch, "E3.18.0.96", {"start": v(27.71, -16.3) * mm, "end": v(31.25, -19.84) * mm});
            skLineSegment(sketch, "E3.18.0.97", {"start": v(27.7, -4.15) * mm, "end": v(31.24, -7.69) * mm});
            skLineSegment(sketch, "E3.18.0.98", {"start": v(27.68, 20.15) * mm, "end": v(31.22, 16.61) * mm});
            skLineSegment(sketch, "E3.18.0.99", {"start": v(31.7, 29.26) * mm, "end": v(28.17, 25.73) * mm});
            skLineSegment(sketch, "E3.18.0.100", {"start": v(31.71, 17.11) * mm, "end": v(28.18, 13.58) * mm});
            skLineSegment(sketch, "E3.18.0.101", {"start": v(31.2, 29.76) * mm, "end": v(27.67, 26.22) * mm});
            skLineSegment(sketch, "E3.18.0.102", {"start": v(31.22, 17.6) * mm, "end": v(27.68, 14.07) * mm});
            skLineSegment(sketch, "E3.18.0.103", {"start": v(28.18, 20.65) * mm, "end": v(27.68, 20.15) * mm});
            skLineSegment(sketch, "E3.18.0.104", {"start": v(31.75, -19.34) * mm, "end": v(31.25, -19.84) * mm});
            skLineSegment(sketch, "E3.18.0.105", {"start": v(31.74, -7.19) * mm, "end": v(31.24, -7.69) * mm});
            skLineSegment(sketch, "E3.18.0.106", {"start": v(31.72, 4.96) * mm, "end": v(31.23, 4.46) * mm});
            skLineSegment(sketch, "E3.18.0.107", {"start": v(31.76, -31.49) * mm, "end": v(31.26, -31.99) * mm});
            skLineSegment(sketch, "E3.18.0.108", {"start": v(31.7, 29.26) * mm, "end": v(31.2, 29.76) * mm});
            skLineSegment(sketch, "E3.18.0.109", {"start": v(31.71, 17.11) * mm, "end": v(31.22, 17.6) * mm});
            skLineSegment(sketch, "E3.18.0.110", {"start": v(28.18, 13.58) * mm, "end": v(27.68, 14.07) * mm});
            skLineSegment(sketch, "E3.18.0.111", {"start": v(28.17, 25.73) * mm, "end": v(27.67, 26.22) * mm});
            skLineSegment(sketch, "E3.18.0.112", {"start": v(28.2, -16.8) * mm, "end": v(27.7, -16.3) * mm});
            skLineSegment(sketch, "E3.18.0.113", {"start": v(28.2, -4.65) * mm, "end": v(27.7, -4.15) * mm});
            skLineSegment(sketch, "E3.18.0.114", {"start": v(28.22, -28.95) * mm, "end": v(27.72, -28.45) * mm});
            skLineSegment(sketch, "E3.18.0.115", {"start": v(31.7, 35.34) * mm, "end": v(31.2, 35.83) * mm});
            skLineSegment(sketch, "E3.18.0.116", {"start": v(28.16, 31.8) * mm, "end": v(27.66, 32.3) * mm});
            skLineSegment(sketch, "E3.18.0.117", {"start": v(28.15, 37.87) * mm, "end": v(27.66, 38.37) * mm});
            skLineSegment(sketch, "E3.18.0.118", {"start": v(28.17, 32.8) * mm, "end": v(27.67, 32.3) * mm});
            skLineSegment(sketch, "E3.18.0.119", {"start": v(31.7, 29.26) * mm, "end": v(31.2, 28.76) * mm});
            skLineSegment(sketch, "E3.18.0.120", {"start": v(31.71, 17.11) * mm, "end": v(31.22, 16.61) * mm});
            skLineSegment(sketch, "E3.19.0.0", {"start": v(33.55, 44.95) * mm, "end": v(37.09, 41.41) * mm});
            skLineSegment(sketch, "E3.19.0.1", {"start": v(33.06, 44.45) * mm, "end": v(36.6, 40.91) * mm});
            skLineSegment(sketch, "E3.19.0.2", {"start": v(33.55, 44.95) * mm, "end": v(33.06, 44.45) * mm});
            skLineSegment(sketch, "E3.19.0.3", {"start": v(37.17, -43.64) * mm, "end": v(33.64, -47.17) * mm});
            skLineSegment(sketch, "E3.19.0.4", {"start": v(36.67, -43.14) * mm, "end": v(33.14, -46.68) * mm});
            skLineSegment(sketch, "E3.19.0.5", {"start": v(33.64, -47.17) * mm, "end": v(33.14, -46.68) * mm});
            skLineSegment(sketch, "E3.19.0.6", {"start": v(33.59, 8.5) * mm, "end": v(37.12, 4.96) * mm});
            skLineSegment(sketch, "E3.19.0.7", {"start": v(37.17, -43.64) * mm, "end": v(36.67, -43.14) * mm});
            skLineSegment(sketch, "E3.19.0.8", {"start": v(37.12, 11.04) * mm, "end": v(33.58, 7.5) * mm});
            skLineSegment(sketch, "E3.19.0.9", {"start": v(37.17, -37.56) * mm, "end": v(33.63, -41.1) * mm});
            skLineSegment(sketch, "E3.19.0.10", {"start": v(37.15, -25.41) * mm, "end": v(33.62, -28.95) * mm});
            skLineSegment(sketch, "E3.19.0.11", {"start": v(36.62, 11.53) * mm, "end": v(33.09, 8) * mm});
            skLineSegment(sketch, "E3.19.0.12", {"start": v(36.6, 23.68) * mm, "end": v(33.07, 20.15) * mm});
            skLineSegment(sketch, "E3.19.0.13", {"start": v(33.6, 2.42) * mm, "end": v(37.13, -1.11) * mm});
            skLineSegment(sketch, "E3.19.0.14", {"start": v(33.58, 14.57) * mm, "end": v(37.12, 11.04) * mm});
            skLineSegment(sketch, "E3.19.0.15", {"start": v(33.57, 26.72) * mm, "end": v(37.1, 23.19) * mm});
            skLineSegment(sketch, "E3.19.0.16", {"start": v(33.63, -34.03) * mm, "end": v(37.17, -37.56) * mm});
            skLineSegment(sketch, "E3.19.0.17", {"start": v(33.62, -21.88) * mm, "end": v(37.15, -25.41) * mm});
            skLineSegment(sketch, "E3.19.0.18", {"start": v(33.6, -9.73) * mm, "end": v(37.14, -13.26) * mm});
            skLineSegment(sketch, "E3.19.0.19", {"start": v(37.14, -13.26) * mm, "end": v(36.64, -13.76) * mm});
            skLineSegment(sketch, "E3.19.0.20", {"start": v(37.13, -1.11) * mm, "end": v(36.63, -1.61) * mm});
            skLineSegment(sketch, "E3.19.0.21", {"start": v(37.12, 11.04) * mm, "end": v(36.62, 10.54) * mm});
            skLineSegment(sketch, "E3.19.0.22", {"start": v(37.1, 23.19) * mm, "end": v(36.6, 22.69) * mm});
            skLineSegment(sketch, "E3.19.0.23", {"start": v(37.17, -37.56) * mm, "end": v(36.67, -38.06) * mm});
            skLineSegment(sketch, "E3.19.0.24", {"start": v(37.15, -25.41) * mm, "end": v(36.66, -25.91) * mm});
            skLineSegment(sketch, "E3.19.0.25", {"start": v(37.14, -13.26) * mm, "end": v(36.64, -12.77) * mm});
            skLineSegment(sketch, "E3.19.0.26", {"start": v(37.13, -1.11) * mm, "end": v(36.63, -0.62) * mm});
            skLineSegment(sketch, "E3.19.0.27", {"start": v(37.12, 11.04) * mm, "end": v(36.62, 11.53) * mm});
            skLineSegment(sketch, "E3.19.0.28", {"start": v(37.1, 23.19) * mm, "end": v(36.6, 23.68) * mm});
            skLineSegment(sketch, "E3.19.0.29", {"start": v(37.17, -37.56) * mm, "end": v(36.67, -37.07) * mm});
            skLineSegment(sketch, "E3.19.0.30", {"start": v(37.15, -25.41) * mm, "end": v(36.66, -24.92) * mm});
            skLineSegment(sketch, "E3.19.0.31", {"start": v(33.58, 7.5) * mm, "end": v(33.09, 8) * mm});
            skLineSegment(sketch, "E3.19.0.32", {"start": v(37.09, 41.41) * mm, "end": v(33.55, 37.87) * mm});
            skLineSegment(sketch, "E3.19.0.33", {"start": v(36.6, 41.9) * mm, "end": v(33.06, 38.37) * mm});
            skLineSegment(sketch, "E3.19.0.34", {"start": v(37.09, 41.41) * mm, "end": v(36.6, 41.9) * mm});
            skLineSegment(sketch, "E3.19.0.35", {"start": v(33.06, 38.37) * mm, "end": v(36.6, 34.84) * mm});
            skLineSegment(sketch, "E3.19.0.36", {"start": v(33.56, 38.87) * mm, "end": v(37.1, 35.34) * mm});
            skLineSegment(sketch, "E3.19.0.37", {"start": v(33.14, -40.6) * mm, "end": v(36.67, -44.14) * mm});
            skLineSegment(sketch, "E3.19.0.38", {"start": v(33.1, 8) * mm, "end": v(36.63, 4.46) * mm});
            skLineSegment(sketch, "E3.19.0.39", {"start": v(37.15, -19.34) * mm, "end": v(33.61, -22.87) * mm});
            skLineSegment(sketch, "E3.19.0.40", {"start": v(37.14, -7.19) * mm, "end": v(33.6, -10.72) * mm});
            skLineSegment(sketch, "E3.19.0.41", {"start": v(37.12, 4.96) * mm, "end": v(33.59, 1.43) * mm});
            skLineSegment(sketch, "E3.19.0.42", {"start": v(37.16, -31.49) * mm, "end": v(33.62, -35.02) * mm});
            skLineSegment(sketch, "E3.19.0.43", {"start": v(36.65, -18.84) * mm, "end": v(33.11, -22.38) * mm});
            skLineSegment(sketch, "E3.19.0.44", {"start": v(36.64, -6.7) * mm, "end": v(33.1, -10.23) * mm});
            skLineSegment(sketch, "E3.19.0.45", {"start": v(36.63, 5.46) * mm, "end": v(33.1, 1.92) * mm});
            skLineSegment(sketch, "E3.19.0.46", {"start": v(36.66, -31) * mm, "end": v(33.13, -34.53) * mm});
            skLineSegment(sketch, "E3.19.0.47", {"start": v(33.61, -15.8) * mm, "end": v(37.15, -19.34) * mm});
            skLineSegment(sketch, "E3.19.0.48", {"start": v(33.6, -3.65) * mm, "end": v(37.14, -7.19) * mm});
            skLineSegment(sketch, "E3.19.0.49", {"start": v(33.57, 32.8) * mm, "end": v(37.1, 29.26) * mm});
            skLineSegment(sketch, "E3.19.0.50", {"start": v(33.64, -40.1) * mm, "end": v(37.17, -43.64) * mm});
            skLineSegment(sketch, "E3.19.0.51", {"start": v(33.62, -27.95) * mm, "end": v(37.16, -31.49) * mm});
            skLineSegment(sketch, "E3.19.0.52", {"start": v(33.58, 20.65) * mm, "end": v(37.11, 17.11) * mm});
            skLineSegment(sketch, "E3.19.0.53", {"start": v(33.61, -15.8) * mm, "end": v(33.11, -16.3) * mm});
            skLineSegment(sketch, "E3.19.0.54", {"start": v(33.6, -3.65) * mm, "end": v(33.1, -4.15) * mm});
            skLineSegment(sketch, "E3.19.0.55", {"start": v(33.59, 8.5) * mm, "end": v(33.1, 8) * mm});
            skLineSegment(sketch, "E3.19.0.56", {"start": v(33.64, -40.1) * mm, "end": v(33.14, -40.6) * mm});
            skLineSegment(sketch, "E3.19.0.57", {"start": v(33.62, -27.95) * mm, "end": v(33.13, -28.45) * mm});
            skLineSegment(sketch, "E3.19.0.58", {"start": v(37.17, -43.64) * mm, "end": v(36.67, -44.14) * mm});
            skLineSegment(sketch, "E3.19.0.59", {"start": v(37.15, -19.34) * mm, "end": v(36.65, -18.84) * mm});
            skLineSegment(sketch, "E3.19.0.60", {"start": v(37.14, -7.19) * mm, "end": v(36.64, -6.7) * mm});
            skLineSegment(sketch, "E3.19.0.61", {"start": v(37.12, 4.96) * mm, "end": v(36.63, 5.46) * mm});
            skLineSegment(sketch, "E3.19.0.62", {"start": v(37.16, -31.49) * mm, "end": v(36.66, -31) * mm});
            skLineSegment(sketch, "E3.19.0.63", {"start": v(33.59, 1.43) * mm, "end": v(33.1, 1.92) * mm});
            skLineSegment(sketch, "E3.19.0.64", {"start": v(33.62, -35.02) * mm, "end": v(33.13, -34.53) * mm});
            skLineSegment(sketch, "E3.19.0.65", {"start": v(33.61, -22.87) * mm, "end": v(33.11, -22.38) * mm});
            skLineSegment(sketch, "E3.19.0.66", {"start": v(33.6, -10.72) * mm, "end": v(33.1, -10.23) * mm});
            skLineSegment(sketch, "E3.19.0.67", {"start": v(33.1, 1.92) * mm, "end": v(36.63, -1.61) * mm});
            skLineSegment(sketch, "E3.19.0.68", {"start": v(33.09, 14.07) * mm, "end": v(36.62, 10.54) * mm});
            skLineSegment(sketch, "E3.19.0.69", {"start": v(33.07, 26.22) * mm, "end": v(36.6, 22.69) * mm});
            skLineSegment(sketch, "E3.19.0.70", {"start": v(33.55, 37.87) * mm, "end": v(33.56, 31.8) * mm, "construction": true});
            skLineSegment(sketch, "E3.19.0.71", {"start": v(33.13, -34.52) * mm, "end": v(36.67, -38.06) * mm});
            skLineSegment(sketch, "E3.19.0.72", {"start": v(33.12, -22.38) * mm, "end": v(36.66, -25.91) * mm});
            skLineSegment(sketch, "E3.19.0.73", {"start": v(33.1, -10.23) * mm, "end": v(36.64, -13.76) * mm});
            skLineSegment(sketch, "E3.19.0.74", {"start": v(37.13, -1.11) * mm, "end": v(33.6, -4.65) * mm});
            skLineSegment(sketch, "E3.19.0.75", {"start": v(37.1, 23.19) * mm, "end": v(33.57, 19.65) * mm});
            skLineSegment(sketch, "E3.19.0.76", {"start": v(37.14, -13.26) * mm, "end": v(33.6, -16.8) * mm});
            skLineSegment(sketch, "E3.19.0.77", {"start": v(36.63, -0.62) * mm, "end": v(33.1, -4.15) * mm});
            skLineSegment(sketch, "E3.19.0.78", {"start": v(36.67, -37.07) * mm, "end": v(33.13, -40.6) * mm});
            skLineSegment(sketch, "E3.19.0.79", {"start": v(36.66, -24.92) * mm, "end": v(33.12, -28.45) * mm});
            skLineSegment(sketch, "E3.19.0.80", {"start": v(36.64, -12.77) * mm, "end": v(33.1, -16.3) * mm});
            skLineSegment(sketch, "E3.19.0.81", {"start": v(33.6, 2.42) * mm, "end": v(33.1, 1.92) * mm});
            skLineSegment(sketch, "E3.19.0.82", {"start": v(33.58, 14.57) * mm, "end": v(33.09, 14.07) * mm});
            skLineSegment(sketch, "E3.19.0.83", {"start": v(33.57, 26.72) * mm, "end": v(33.07, 26.22) * mm});
            skLineSegment(sketch, "E3.19.0.84", {"start": v(33.63, -34.03) * mm, "end": v(33.13, -34.52) * mm});
            skLineSegment(sketch, "E3.19.0.85", {"start": v(33.62, -21.88) * mm, "end": v(33.12, -22.38) * mm});
            skLineSegment(sketch, "E3.19.0.86", {"start": v(33.6, -9.73) * mm, "end": v(33.1, -10.23) * mm});
            skLineSegment(sketch, "E3.19.0.87", {"start": v(33.57, 19.65) * mm, "end": v(33.07, 20.15) * mm});
            skLineSegment(sketch, "E3.19.0.88", {"start": v(33.63, -41.1) * mm, "end": v(33.13, -40.6) * mm});
            skLineSegment(sketch, "E3.19.0.89", {"start": v(37.1, 35.34) * mm, "end": v(36.6, 34.84) * mm});
            skLineSegment(sketch, "E3.19.0.90", {"start": v(37.09, 41.41) * mm, "end": v(36.6, 40.91) * mm});
            skLineSegment(sketch, "E3.19.0.91", {"start": v(37.1, 35.34) * mm, "end": v(33.56, 31.8) * mm});
            skLineSegment(sketch, "E3.19.0.92", {"start": v(36.6, 35.83) * mm, "end": v(33.06, 32.3) * mm});
            skLineSegment(sketch, "E3.19.0.93", {"start": v(33.56, 38.87) * mm, "end": v(33.06, 38.37) * mm});
            skLineSegment(sketch, "E3.19.0.94", {"start": v(33.13, -28.45) * mm, "end": v(36.66, -31.99) * mm});
            skLineSegment(sketch, "E3.19.0.95", {"start": v(33.07, 32.3) * mm, "end": v(36.6, 28.76) * mm});
            skLineSegment(sketch, "E3.19.0.96", {"start": v(33.11, -16.3) * mm, "end": v(36.65, -19.84) * mm});
            skLineSegment(sketch, "E3.19.0.97", {"start": v(33.1, -4.15) * mm, "end": v(36.64, -7.69) * mm});
            skLineSegment(sketch, "E3.19.0.98", {"start": v(33.08, 20.15) * mm, "end": v(36.62, 16.61) * mm});
            skLineSegment(sketch, "E3.19.0.99", {"start": v(37.1, 29.26) * mm, "end": v(33.57, 25.73) * mm});
            skLineSegment(sketch, "E3.19.0.100", {"start": v(37.11, 17.11) * mm, "end": v(33.58, 13.58) * mm});
            skLineSegment(sketch, "E3.19.0.101", {"start": v(36.6, 29.76) * mm, "end": v(33.07, 26.22) * mm});
            skLineSegment(sketch, "E3.19.0.102", {"start": v(36.62, 17.6) * mm, "end": v(33.08, 14.07) * mm});
            skLineSegment(sketch, "E3.19.0.103", {"start": v(33.58, 20.65) * mm, "end": v(33.08, 20.15) * mm});
            skLineSegment(sketch, "E3.19.0.104", {"start": v(37.15, -19.34) * mm, "end": v(36.65, -19.84) * mm});
            skLineSegment(sketch, "E3.19.0.105", {"start": v(37.14, -7.19) * mm, "end": v(36.64, -7.69) * mm});
            skLineSegment(sketch, "E3.19.0.106", {"start": v(37.12, 4.96) * mm, "end": v(36.63, 4.46) * mm});
            skLineSegment(sketch, "E3.19.0.107", {"start": v(37.16, -31.49) * mm, "end": v(36.66, -31.99) * mm});
            skLineSegment(sketch, "E3.19.0.108", {"start": v(37.1, 29.26) * mm, "end": v(36.6, 29.76) * mm});
            skLineSegment(sketch, "E3.19.0.109", {"start": v(37.11, 17.11) * mm, "end": v(36.62, 17.6) * mm});
            skLineSegment(sketch, "E3.19.0.110", {"start": v(33.58, 13.58) * mm, "end": v(33.08, 14.07) * mm});
            skLineSegment(sketch, "E3.19.0.111", {"start": v(33.57, 25.73) * mm, "end": v(33.07, 26.22) * mm});
            skLineSegment(sketch, "E3.19.0.112", {"start": v(33.6, -16.8) * mm, "end": v(33.1, -16.3) * mm});
            skLineSegment(sketch, "E3.19.0.113", {"start": v(33.6, -4.65) * mm, "end": v(33.1, -4.15) * mm});
            skLineSegment(sketch, "E3.19.0.114", {"start": v(33.62, -28.95) * mm, "end": v(33.12, -28.45) * mm});
            skLineSegment(sketch, "E3.19.0.115", {"start": v(37.1, 35.34) * mm, "end": v(36.6, 35.83) * mm});
            skLineSegment(sketch, "E3.19.0.116", {"start": v(33.56, 31.8) * mm, "end": v(33.06, 32.3) * mm});
            skLineSegment(sketch, "E3.19.0.117", {"start": v(33.55, 37.87) * mm, "end": v(33.06, 38.37) * mm});
            skLineSegment(sketch, "E3.19.0.118", {"start": v(33.57, 32.8) * mm, "end": v(33.07, 32.3) * mm});
            skLineSegment(sketch, "E3.19.0.119", {"start": v(37.1, 29.26) * mm, "end": v(36.6, 28.76) * mm});
            skLineSegment(sketch, "E3.19.0.120", {"start": v(37.11, 17.11) * mm, "end": v(36.62, 16.61) * mm});
            skLineSegment(sketch, "E3.20.0.0", {"start": v(38.95, 44.95) * mm, "end": v(42.49, 41.41) * mm});
            skLineSegment(sketch, "E3.20.0.1", {"start": v(38.46, 44.45) * mm, "end": v(42, 40.91) * mm});
            skLineSegment(sketch, "E3.20.0.2", {"start": v(38.95, 44.95) * mm, "end": v(38.46, 44.45) * mm});
            skLineSegment(sketch, "E3.20.0.3", {"start": v(42.57, -43.64) * mm, "end": v(39.04, -47.17) * mm});
            skLineSegment(sketch, "E3.20.0.4", {"start": v(42.07, -43.14) * mm, "end": v(38.54, -46.68) * mm});
            skLineSegment(sketch, "E3.20.0.5", {"start": v(39.04, -47.17) * mm, "end": v(38.54, -46.68) * mm});
            skLineSegment(sketch, "E3.20.0.6", {"start": v(38.99, 8.5) * mm, "end": v(42.52, 4.96) * mm});
            skLineSegment(sketch, "E3.20.0.7", {"start": v(42.57, -43.64) * mm, "end": v(42.07, -43.14) * mm});
            skLineSegment(sketch, "E3.20.0.8", {"start": v(42.52, 11.04) * mm, "end": v(38.98, 7.5) * mm});
            skLineSegment(sketch, "E3.20.0.9", {"start": v(42.57, -37.56) * mm, "end": v(39.03, -41.1) * mm});
            skLineSegment(sketch, "E3.20.0.10", {"start": v(42.55, -25.41) * mm, "end": v(39.02, -28.95) * mm});
            skLineSegment(sketch, "E3.20.0.11", {"start": v(42.02, 11.53) * mm, "end": v(38.49, 8) * mm});
            skLineSegment(sketch, "E3.20.0.12", {"start": v(42, 23.68) * mm, "end": v(38.47, 20.15) * mm});
            skLineSegment(sketch, "E3.20.0.13", {"start": v(39, 2.42) * mm, "end": v(42.53, -1.11) * mm});
            skLineSegment(sketch, "E3.20.0.14", {"start": v(38.98, 14.57) * mm, "end": v(42.52, 11.04) * mm});
            skLineSegment(sketch, "E3.20.0.15", {"start": v(38.97, 26.72) * mm, "end": v(42.5, 23.19) * mm});
            skLineSegment(sketch, "E3.20.0.16", {"start": v(39.03, -34.03) * mm, "end": v(42.57, -37.56) * mm});
            skLineSegment(sketch, "E3.20.0.17", {"start": v(39.02, -21.88) * mm, "end": v(42.55, -25.41) * mm});
            skLineSegment(sketch, "E3.20.0.18", {"start": v(39, -9.73) * mm, "end": v(42.54, -13.26) * mm});
            skLineSegment(sketch, "E3.20.0.19", {"start": v(42.54, -13.26) * mm, "end": v(42.04, -13.76) * mm});
            skLineSegment(sketch, "E3.20.0.20", {"start": v(42.53, -1.11) * mm, "end": v(42.03, -1.61) * mm});
            skLineSegment(sketch, "E3.20.0.21", {"start": v(42.52, 11.04) * mm, "end": v(42.02, 10.54) * mm});
            skLineSegment(sketch, "E3.20.0.22", {"start": v(42.5, 23.19) * mm, "end": v(42, 22.69) * mm});
            skLineSegment(sketch, "E3.20.0.23", {"start": v(42.57, -37.56) * mm, "end": v(42.07, -38.06) * mm});
            skLineSegment(sketch, "E3.20.0.24", {"start": v(42.55, -25.41) * mm, "end": v(42.06, -25.91) * mm});
            skLineSegment(sketch, "E3.20.0.25", {"start": v(42.54, -13.26) * mm, "end": v(42.04, -12.77) * mm});
            skLineSegment(sketch, "E3.20.0.26", {"start": v(42.53, -1.11) * mm, "end": v(42.03, -0.62) * mm});
            skLineSegment(sketch, "E3.20.0.27", {"start": v(42.52, 11.04) * mm, "end": v(42.02, 11.53) * mm});
            skLineSegment(sketch, "E3.20.0.28", {"start": v(42.5, 23.19) * mm, "end": v(42, 23.68) * mm});
            skLineSegment(sketch, "E3.20.0.29", {"start": v(42.57, -37.56) * mm, "end": v(42.07, -37.07) * mm});
            skLineSegment(sketch, "E3.20.0.30", {"start": v(42.55, -25.41) * mm, "end": v(42.06, -24.92) * mm});
            skLineSegment(sketch, "E3.20.0.31", {"start": v(38.98, 7.5) * mm, "end": v(38.49, 8) * mm});
            skLineSegment(sketch, "E3.20.0.32", {"start": v(42.49, 41.41) * mm, "end": v(38.95, 37.87) * mm});
            skLineSegment(sketch, "E3.20.0.33", {"start": v(42, 41.9) * mm, "end": v(38.46, 38.37) * mm});
            skLineSegment(sketch, "E3.20.0.34", {"start": v(42.49, 41.41) * mm, "end": v(42, 41.9) * mm});
            skLineSegment(sketch, "E3.20.0.35", {"start": v(38.46, 38.37) * mm, "end": v(42, 34.84) * mm});
            skLineSegment(sketch, "E3.20.0.36", {"start": v(38.96, 38.87) * mm, "end": v(42.5, 35.34) * mm});
            skLineSegment(sketch, "E3.20.0.37", {"start": v(38.54, -40.6) * mm, "end": v(42.07, -44.14) * mm});
            skLineSegment(sketch, "E3.20.0.38", {"start": v(38.5, 8) * mm, "end": v(42.03, 4.46) * mm});
            skLineSegment(sketch, "E3.20.0.39", {"start": v(42.55, -19.34) * mm, "end": v(39.01, -22.87) * mm});
            skLineSegment(sketch, "E3.20.0.40", {"start": v(42.54, -7.19) * mm, "end": v(39, -10.72) * mm});
            skLineSegment(sketch, "E3.20.0.41", {"start": v(42.52, 4.96) * mm, "end": v(38.99, 1.43) * mm});
            skLineSegment(sketch, "E3.20.0.42", {"start": v(42.56, -31.49) * mm, "end": v(39.02, -35.02) * mm});
            skLineSegment(sketch, "E3.20.0.43", {"start": v(42.05, -18.84) * mm, "end": v(38.51, -22.38) * mm});
            skLineSegment(sketch, "E3.20.0.44", {"start": v(42.04, -6.7) * mm, "end": v(38.5, -10.23) * mm});
            skLineSegment(sketch, "E3.20.0.45", {"start": v(42.03, 5.46) * mm, "end": v(38.5, 1.92) * mm});
            skLineSegment(sketch, "E3.20.0.46", {"start": v(42.06, -31) * mm, "end": v(38.53, -34.53) * mm});
            skLineSegment(sketch, "E3.20.0.47", {"start": v(39.01, -15.8) * mm, "end": v(42.55, -19.34) * mm});
            skLineSegment(sketch, "E3.20.0.48", {"start": v(39, -3.65) * mm, "end": v(42.54, -7.19) * mm});
            skLineSegment(sketch, "E3.20.0.49", {"start": v(38.97, 32.8) * mm, "end": v(42.5, 29.26) * mm});
            skLineSegment(sketch, "E3.20.0.50", {"start": v(39.04, -40.1) * mm, "end": v(42.57, -43.64) * mm});
            skLineSegment(sketch, "E3.20.0.51", {"start": v(39.02, -27.95) * mm, "end": v(42.56, -31.49) * mm});
            skLineSegment(sketch, "E3.20.0.52", {"start": v(38.98, 20.65) * mm, "end": v(42.51, 17.11) * mm});
            skLineSegment(sketch, "E3.20.0.53", {"start": v(39.01, -15.8) * mm, "end": v(38.51, -16.3) * mm});
            skLineSegment(sketch, "E3.20.0.54", {"start": v(39, -3.65) * mm, "end": v(38.5, -4.15) * mm});
            skLineSegment(sketch, "E3.20.0.55", {"start": v(38.99, 8.5) * mm, "end": v(38.5, 8) * mm});
            skLineSegment(sketch, "E3.20.0.56", {"start": v(39.04, -40.1) * mm, "end": v(38.54, -40.6) * mm});
            skLineSegment(sketch, "E3.20.0.57", {"start": v(39.02, -27.95) * mm, "end": v(38.53, -28.45) * mm});
            skLineSegment(sketch, "E3.20.0.58", {"start": v(42.57, -43.64) * mm, "end": v(42.07, -44.14) * mm});
            skLineSegment(sketch, "E3.20.0.59", {"start": v(42.55, -19.34) * mm, "end": v(42.05, -18.84) * mm});
            skLineSegment(sketch, "E3.20.0.60", {"start": v(42.54, -7.19) * mm, "end": v(42.04, -6.7) * mm});
            skLineSegment(sketch, "E3.20.0.61", {"start": v(42.52, 4.96) * mm, "end": v(42.03, 5.46) * mm});
            skLineSegment(sketch, "E3.20.0.62", {"start": v(42.56, -31.49) * mm, "end": v(42.06, -31) * mm});
            skLineSegment(sketch, "E3.20.0.63", {"start": v(38.99, 1.43) * mm, "end": v(38.5, 1.92) * mm});
            skLineSegment(sketch, "E3.20.0.64", {"start": v(39.02, -35.02) * mm, "end": v(38.53, -34.53) * mm});
            skLineSegment(sketch, "E3.20.0.65", {"start": v(39.01, -22.87) * mm, "end": v(38.51, -22.38) * mm});
            skLineSegment(sketch, "E3.20.0.66", {"start": v(39, -10.72) * mm, "end": v(38.5, -10.23) * mm});
            skLineSegment(sketch, "E3.20.0.67", {"start": v(38.5, 1.92) * mm, "end": v(42.03, -1.61) * mm});
            skLineSegment(sketch, "E3.20.0.68", {"start": v(38.49, 14.07) * mm, "end": v(42.02, 10.54) * mm});
            skLineSegment(sketch, "E3.20.0.69", {"start": v(38.47, 26.22) * mm, "end": v(42, 22.69) * mm});
            skLineSegment(sketch, "E3.20.0.70", {"start": v(38.95, 37.87) * mm, "end": v(38.96, 31.8) * mm, "construction": true});
            skLineSegment(sketch, "E3.20.0.71", {"start": v(38.53, -34.52) * mm, "end": v(42.07, -38.06) * mm});
            skLineSegment(sketch, "E3.20.0.72", {"start": v(38.52, -22.38) * mm, "end": v(42.06, -25.91) * mm});
            skLineSegment(sketch, "E3.20.0.73", {"start": v(38.5, -10.23) * mm, "end": v(42.04, -13.76) * mm});
            skLineSegment(sketch, "E3.20.0.74", {"start": v(42.53, -1.11) * mm, "end": v(39, -4.65) * mm});
            skLineSegment(sketch, "E3.20.0.75", {"start": v(42.5, 23.19) * mm, "end": v(38.97, 19.65) * mm});
            skLineSegment(sketch, "E3.20.0.76", {"start": v(42.54, -13.26) * mm, "end": v(39, -16.8) * mm});
            skLineSegment(sketch, "E3.20.0.77", {"start": v(42.03, -0.62) * mm, "end": v(38.5, -4.15) * mm});
            skLineSegment(sketch, "E3.20.0.78", {"start": v(42.07, -37.07) * mm, "end": v(38.53, -40.6) * mm});
            skLineSegment(sketch, "E3.20.0.79", {"start": v(42.06, -24.92) * mm, "end": v(38.52, -28.45) * mm});
            skLineSegment(sketch, "E3.20.0.80", {"start": v(42.04, -12.77) * mm, "end": v(38.5, -16.3) * mm});
            skLineSegment(sketch, "E3.20.0.81", {"start": v(39, 2.42) * mm, "end": v(38.5, 1.92) * mm});
            skLineSegment(sketch, "E3.20.0.82", {"start": v(38.98, 14.57) * mm, "end": v(38.49, 14.07) * mm});
            skLineSegment(sketch, "E3.20.0.83", {"start": v(38.97, 26.72) * mm, "end": v(38.47, 26.22) * mm});
            skLineSegment(sketch, "E3.20.0.84", {"start": v(39.03, -34.03) * mm, "end": v(38.53, -34.52) * mm});
            skLineSegment(sketch, "E3.20.0.85", {"start": v(39.02, -21.88) * mm, "end": v(38.52, -22.38) * mm});
            skLineSegment(sketch, "E3.20.0.86", {"start": v(39, -9.73) * mm, "end": v(38.5, -10.23) * mm});
            skLineSegment(sketch, "E3.20.0.87", {"start": v(38.97, 19.65) * mm, "end": v(38.47, 20.15) * mm});
            skLineSegment(sketch, "E3.20.0.88", {"start": v(39.03, -41.1) * mm, "end": v(38.53, -40.6) * mm});
            skLineSegment(sketch, "E3.20.0.89", {"start": v(42.5, 35.34) * mm, "end": v(42, 34.84) * mm});
            skLineSegment(sketch, "E3.20.0.90", {"start": v(42.49, 41.41) * mm, "end": v(42, 40.91) * mm});
            skLineSegment(sketch, "E3.20.0.91", {"start": v(42.5, 35.34) * mm, "end": v(38.96, 31.8) * mm});
            skLineSegment(sketch, "E3.20.0.92", {"start": v(42, 35.83) * mm, "end": v(38.46, 32.3) * mm});
            skLineSegment(sketch, "E3.20.0.93", {"start": v(38.96, 38.87) * mm, "end": v(38.46, 38.37) * mm});
            skLineSegment(sketch, "E3.20.0.94", {"start": v(38.53, -28.45) * mm, "end": v(42.06, -31.99) * mm});
            skLineSegment(sketch, "E3.20.0.95", {"start": v(38.47, 32.3) * mm, "end": v(42, 28.76) * mm});
            skLineSegment(sketch, "E3.20.0.96", {"start": v(38.51, -16.3) * mm, "end": v(42.05, -19.84) * mm});
            skLineSegment(sketch, "E3.20.0.97", {"start": v(38.5, -4.15) * mm, "end": v(42.04, -7.69) * mm});
            skLineSegment(sketch, "E3.20.0.98", {"start": v(38.48, 20.15) * mm, "end": v(42.02, 16.61) * mm});
            skLineSegment(sketch, "E3.20.0.99", {"start": v(42.5, 29.26) * mm, "end": v(38.97, 25.73) * mm});
            skLineSegment(sketch, "E3.20.0.100", {"start": v(42.51, 17.11) * mm, "end": v(38.98, 13.58) * mm});
            skLineSegment(sketch, "E3.20.0.101", {"start": v(42, 29.76) * mm, "end": v(38.47, 26.22) * mm});
            skLineSegment(sketch, "E3.20.0.102", {"start": v(42.02, 17.6) * mm, "end": v(38.48, 14.07) * mm});
            skLineSegment(sketch, "E3.20.0.103", {"start": v(38.98, 20.65) * mm, "end": v(38.48, 20.15) * mm});
            skLineSegment(sketch, "E3.20.0.104", {"start": v(42.55, -19.34) * mm, "end": v(42.05, -19.84) * mm});
            skLineSegment(sketch, "E3.20.0.105", {"start": v(42.54, -7.19) * mm, "end": v(42.04, -7.69) * mm});
            skLineSegment(sketch, "E3.20.0.106", {"start": v(42.52, 4.96) * mm, "end": v(42.03, 4.46) * mm});
            skLineSegment(sketch, "E3.20.0.107", {"start": v(42.56, -31.49) * mm, "end": v(42.06, -31.99) * mm});
            skLineSegment(sketch, "E3.20.0.108", {"start": v(42.5, 29.26) * mm, "end": v(42, 29.76) * mm});
            skLineSegment(sketch, "E3.20.0.109", {"start": v(42.51, 17.11) * mm, "end": v(42.02, 17.6) * mm});
            skLineSegment(sketch, "E3.20.0.110", {"start": v(38.98, 13.58) * mm, "end": v(38.48, 14.07) * mm});
            skLineSegment(sketch, "E3.20.0.111", {"start": v(38.97, 25.73) * mm, "end": v(38.47, 26.22) * mm});
            skLineSegment(sketch, "E3.20.0.112", {"start": v(39, -16.8) * mm, "end": v(38.5, -16.3) * mm});
            skLineSegment(sketch, "E3.20.0.113", {"start": v(39, -4.65) * mm, "end": v(38.5, -4.15) * mm});
            skLineSegment(sketch, "E3.20.0.114", {"start": v(39.02, -28.95) * mm, "end": v(38.52, -28.45) * mm});
            skLineSegment(sketch, "E3.20.0.115", {"start": v(42.5, 35.34) * mm, "end": v(42, 35.83) * mm});
            skLineSegment(sketch, "E3.20.0.116", {"start": v(38.96, 31.8) * mm, "end": v(38.46, 32.3) * mm});
            skLineSegment(sketch, "E3.20.0.117", {"start": v(38.95, 37.87) * mm, "end": v(38.46, 38.37) * mm});
            skLineSegment(sketch, "E3.20.0.118", {"start": v(38.97, 32.8) * mm, "end": v(38.47, 32.3) * mm});
            skLineSegment(sketch, "E3.20.0.119", {"start": v(42.5, 29.26) * mm, "end": v(42, 28.76) * mm});
            skLineSegment(sketch, "E3.20.0.120", {"start": v(42.51, 17.11) * mm, "end": v(42.02, 16.61) * mm});
            skLineSegment(sketch, "E3.21.0.0", {"start": v(44.35, 44.95) * mm, "end": v(47.89, 41.41) * mm});
            skLineSegment(sketch, "E3.21.0.1", {"start": v(43.86, 44.45) * mm, "end": v(47.4, 40.91) * mm});
            skLineSegment(sketch, "E3.21.0.2", {"start": v(44.35, 44.95) * mm, "end": v(43.86, 44.45) * mm});
            skLineSegment(sketch, "E3.21.0.3", {"start": v(47.97, -43.64) * mm, "end": v(44.44, -47.17) * mm});
            skLineSegment(sketch, "E3.21.0.4", {"start": v(47.47, -43.14) * mm, "end": v(43.94, -46.68) * mm});
            skLineSegment(sketch, "E3.21.0.5", {"start": v(44.44, -47.17) * mm, "end": v(43.94, -46.68) * mm});
            skLineSegment(sketch, "E3.21.0.6", {"start": v(44.39, 8.5) * mm, "end": v(47.92, 4.96) * mm});
            skLineSegment(sketch, "E3.21.0.7", {"start": v(47.97, -43.64) * mm, "end": v(47.47, -43.14) * mm});
            skLineSegment(sketch, "E3.21.0.8", {"start": v(47.92, 11.04) * mm, "end": v(44.38, 7.5) * mm});
            skLineSegment(sketch, "E3.21.0.9", {"start": v(47.97, -37.56) * mm, "end": v(44.43, -41.1) * mm});
            skLineSegment(sketch, "E3.21.0.10", {"start": v(47.95, -25.41) * mm, "end": v(44.42, -28.95) * mm});
            skLineSegment(sketch, "E3.21.0.11", {"start": v(47.42, 11.53) * mm, "end": v(43.89, 8) * mm});
            skLineSegment(sketch, "E3.21.0.12", {"start": v(47.4, 23.68) * mm, "end": v(43.87, 20.15) * mm});
            skLineSegment(sketch, "E3.21.0.13", {"start": v(44.4, 2.42) * mm, "end": v(47.93, -1.11) * mm});
            skLineSegment(sketch, "E3.21.0.14", {"start": v(44.38, 14.57) * mm, "end": v(47.92, 11.04) * mm});
            skLineSegment(sketch, "E3.21.0.15", {"start": v(44.37, 26.72) * mm, "end": v(47.9, 23.19) * mm});
            skLineSegment(sketch, "E3.21.0.16", {"start": v(44.43, -34.03) * mm, "end": v(47.97, -37.56) * mm});
            skLineSegment(sketch, "E3.21.0.17", {"start": v(44.42, -21.88) * mm, "end": v(47.95, -25.41) * mm});
            skLineSegment(sketch, "E3.21.0.18", {"start": v(44.4, -9.73) * mm, "end": v(47.94, -13.26) * mm});
            skLineSegment(sketch, "E3.21.0.19", {"start": v(47.94, -13.26) * mm, "end": v(47.44, -13.76) * mm});
            skLineSegment(sketch, "E3.21.0.20", {"start": v(47.93, -1.11) * mm, "end": v(47.43, -1.61) * mm});
            skLineSegment(sketch, "E3.21.0.21", {"start": v(47.92, 11.04) * mm, "end": v(47.42, 10.54) * mm});
            skLineSegment(sketch, "E3.21.0.22", {"start": v(47.9, 23.19) * mm, "end": v(47.4, 22.69) * mm});
            skLineSegment(sketch, "E3.21.0.23", {"start": v(47.97, -37.56) * mm, "end": v(47.47, -38.06) * mm});
            skLineSegment(sketch, "E3.21.0.24", {"start": v(47.95, -25.41) * mm, "end": v(47.46, -25.91) * mm});
            skLineSegment(sketch, "E3.21.0.25", {"start": v(47.94, -13.26) * mm, "end": v(47.44, -12.77) * mm});
            skLineSegment(sketch, "E3.21.0.26", {"start": v(47.93, -1.11) * mm, "end": v(47.43, -0.62) * mm});
            skLineSegment(sketch, "E3.21.0.27", {"start": v(47.92, 11.04) * mm, "end": v(47.42, 11.53) * mm});
            skLineSegment(sketch, "E3.21.0.28", {"start": v(47.9, 23.19) * mm, "end": v(47.4, 23.68) * mm});
            skLineSegment(sketch, "E3.21.0.29", {"start": v(47.97, -37.56) * mm, "end": v(47.47, -37.07) * mm});
            skLineSegment(sketch, "E3.21.0.30", {"start": v(47.95, -25.41) * mm, "end": v(47.46, -24.92) * mm});
            skLineSegment(sketch, "E3.21.0.31", {"start": v(44.38, 7.5) * mm, "end": v(43.89, 8) * mm});
            skLineSegment(sketch, "E3.21.0.32", {"start": v(47.89, 41.41) * mm, "end": v(44.35, 37.87) * mm});
            skLineSegment(sketch, "E3.21.0.33", {"start": v(47.4, 41.9) * mm, "end": v(43.86, 38.37) * mm});
            skLineSegment(sketch, "E3.21.0.34", {"start": v(47.89, 41.41) * mm, "end": v(47.4, 41.9) * mm});
            skLineSegment(sketch, "E3.21.0.35", {"start": v(43.86, 38.37) * mm, "end": v(47.4, 34.84) * mm});
            skLineSegment(sketch, "E3.21.0.36", {"start": v(44.36, 38.87) * mm, "end": v(47.9, 35.34) * mm});
            skLineSegment(sketch, "E3.21.0.37", {"start": v(43.94, -40.6) * mm, "end": v(47.47, -44.14) * mm});
            skLineSegment(sketch, "E3.21.0.38", {"start": v(43.9, 8) * mm, "end": v(47.43, 4.46) * mm});
            skLineSegment(sketch, "E3.21.0.39", {"start": v(47.95, -19.34) * mm, "end": v(44.41, -22.87) * mm});
            skLineSegment(sketch, "E3.21.0.40", {"start": v(47.94, -7.19) * mm, "end": v(44.4, -10.72) * mm});
            skLineSegment(sketch, "E3.21.0.41", {"start": v(47.92, 4.96) * mm, "end": v(44.39, 1.43) * mm});
            skLineSegment(sketch, "E3.21.0.42", {"start": v(47.96, -31.49) * mm, "end": v(44.42, -35.02) * mm});
            skLineSegment(sketch, "E3.21.0.43", {"start": v(47.45, -18.84) * mm, "end": v(43.91, -22.38) * mm});
            skLineSegment(sketch, "E3.21.0.44", {"start": v(47.44, -6.7) * mm, "end": v(43.9, -10.23) * mm});
            skLineSegment(sketch, "E3.21.0.45", {"start": v(47.43, 5.46) * mm, "end": v(43.9, 1.92) * mm});
            skLineSegment(sketch, "E3.21.0.46", {"start": v(47.46, -31) * mm, "end": v(43.93, -34.53) * mm});
            skLineSegment(sketch, "E3.21.0.47", {"start": v(44.41, -15.8) * mm, "end": v(47.95, -19.34) * mm});
            skLineSegment(sketch, "E3.21.0.48", {"start": v(44.4, -3.65) * mm, "end": v(47.94, -7.19) * mm});
            skLineSegment(sketch, "E3.21.0.49", {"start": v(44.37, 32.8) * mm, "end": v(47.9, 29.26) * mm});
            skLineSegment(sketch, "E3.21.0.50", {"start": v(44.44, -40.1) * mm, "end": v(47.97, -43.64) * mm});
            skLineSegment(sketch, "E3.21.0.51", {"start": v(44.42, -27.95) * mm, "end": v(47.96, -31.49) * mm});
            skLineSegment(sketch, "E3.21.0.52", {"start": v(44.38, 20.65) * mm, "end": v(47.91, 17.11) * mm});
            skLineSegment(sketch, "E3.21.0.53", {"start": v(44.41, -15.8) * mm, "end": v(43.91, -16.3) * mm});
            skLineSegment(sketch, "E3.21.0.54", {"start": v(44.4, -3.65) * mm, "end": v(43.9, -4.15) * mm});
            skLineSegment(sketch, "E3.21.0.55", {"start": v(44.39, 8.5) * mm, "end": v(43.9, 8) * mm});
            skLineSegment(sketch, "E3.21.0.56", {"start": v(44.44, -40.1) * mm, "end": v(43.94, -40.6) * mm});
            skLineSegment(sketch, "E3.21.0.57", {"start": v(44.42, -27.95) * mm, "end": v(43.93, -28.45) * mm});
            skLineSegment(sketch, "E3.21.0.58", {"start": v(47.97, -43.64) * mm, "end": v(47.47, -44.14) * mm});
            skLineSegment(sketch, "E3.21.0.59", {"start": v(47.95, -19.34) * mm, "end": v(47.45, -18.84) * mm});
            skLineSegment(sketch, "E3.21.0.60", {"start": v(47.94, -7.19) * mm, "end": v(47.44, -6.7) * mm});
            skLineSegment(sketch, "E3.21.0.61", {"start": v(47.92, 4.96) * mm, "end": v(47.43, 5.46) * mm});
            skLineSegment(sketch, "E3.21.0.62", {"start": v(47.96, -31.49) * mm, "end": v(47.46, -31) * mm});
            skLineSegment(sketch, "E3.21.0.63", {"start": v(44.39, 1.43) * mm, "end": v(43.9, 1.92) * mm});
            skLineSegment(sketch, "E3.21.0.64", {"start": v(44.42, -35.02) * mm, "end": v(43.93, -34.53) * mm});
            skLineSegment(sketch, "E3.21.0.65", {"start": v(44.41, -22.87) * mm, "end": v(43.91, -22.38) * mm});
            skLineSegment(sketch, "E3.21.0.66", {"start": v(44.4, -10.72) * mm, "end": v(43.9, -10.23) * mm});
            skLineSegment(sketch, "E3.21.0.67", {"start": v(43.9, 1.92) * mm, "end": v(47.43, -1.61) * mm});
            skLineSegment(sketch, "E3.21.0.68", {"start": v(43.89, 14.07) * mm, "end": v(47.42, 10.54) * mm});
            skLineSegment(sketch, "E3.21.0.69", {"start": v(43.87, 26.22) * mm, "end": v(47.4, 22.69) * mm});
            skLineSegment(sketch, "E3.21.0.70", {"start": v(44.35, 37.87) * mm, "end": v(44.36, 31.8) * mm, "construction": true});
            skLineSegment(sketch, "E3.21.0.71", {"start": v(43.93, -34.52) * mm, "end": v(47.47, -38.06) * mm});
            skLineSegment(sketch, "E3.21.0.72", {"start": v(43.92, -22.38) * mm, "end": v(47.46, -25.91) * mm});
            skLineSegment(sketch, "E3.21.0.73", {"start": v(43.9, -10.23) * mm, "end": v(47.44, -13.76) * mm});
            skLineSegment(sketch, "E3.21.0.74", {"start": v(47.93, -1.11) * mm, "end": v(44.4, -4.65) * mm});
            skLineSegment(sketch, "E3.21.0.75", {"start": v(47.9, 23.19) * mm, "end": v(44.37, 19.65) * mm});
            skLineSegment(sketch, "E3.21.0.76", {"start": v(47.94, -13.26) * mm, "end": v(44.4, -16.8) * mm});
            skLineSegment(sketch, "E3.21.0.77", {"start": v(47.43, -0.62) * mm, "end": v(43.9, -4.15) * mm});
            skLineSegment(sketch, "E3.21.0.78", {"start": v(47.47, -37.07) * mm, "end": v(43.93, -40.6) * mm});
            skLineSegment(sketch, "E3.21.0.79", {"start": v(47.46, -24.92) * mm, "end": v(43.92, -28.45) * mm});
            skLineSegment(sketch, "E3.21.0.80", {"start": v(47.44, -12.77) * mm, "end": v(43.9, -16.3) * mm});
            skLineSegment(sketch, "E3.21.0.81", {"start": v(44.4, 2.42) * mm, "end": v(43.9, 1.92) * mm});
            skLineSegment(sketch, "E3.21.0.82", {"start": v(44.38, 14.57) * mm, "end": v(43.89, 14.07) * mm});
            skLineSegment(sketch, "E3.21.0.83", {"start": v(44.37, 26.72) * mm, "end": v(43.87, 26.22) * mm});
            skLineSegment(sketch, "E3.21.0.84", {"start": v(44.43, -34.03) * mm, "end": v(43.93, -34.52) * mm});
            skLineSegment(sketch, "E3.21.0.85", {"start": v(44.42, -21.88) * mm, "end": v(43.92, -22.38) * mm});
            skLineSegment(sketch, "E3.21.0.86", {"start": v(44.4, -9.73) * mm, "end": v(43.9, -10.23) * mm});
            skLineSegment(sketch, "E3.21.0.87", {"start": v(44.37, 19.65) * mm, "end": v(43.87, 20.15) * mm});
            skLineSegment(sketch, "E3.21.0.88", {"start": v(44.43, -41.1) * mm, "end": v(43.93, -40.6) * mm});
            skLineSegment(sketch, "E3.21.0.89", {"start": v(47.9, 35.34) * mm, "end": v(47.4, 34.84) * mm});
            skLineSegment(sketch, "E3.21.0.90", {"start": v(47.89, 41.41) * mm, "end": v(47.4, 40.91) * mm});
            skLineSegment(sketch, "E3.21.0.91", {"start": v(47.9, 35.34) * mm, "end": v(44.36, 31.8) * mm});
            skLineSegment(sketch, "E3.21.0.92", {"start": v(47.4, 35.83) * mm, "end": v(43.86, 32.3) * mm});
            skLineSegment(sketch, "E3.21.0.93", {"start": v(44.36, 38.87) * mm, "end": v(43.86, 38.37) * mm});
            skLineSegment(sketch, "E3.21.0.94", {"start": v(43.93, -28.45) * mm, "end": v(47.46, -31.99) * mm});
            skLineSegment(sketch, "E3.21.0.95", {"start": v(43.87, 32.3) * mm, "end": v(47.4, 28.76) * mm});
            skLineSegment(sketch, "E3.21.0.96", {"start": v(43.91, -16.3) * mm, "end": v(47.45, -19.84) * mm});
            skLineSegment(sketch, "E3.21.0.97", {"start": v(43.9, -4.15) * mm, "end": v(47.44, -7.69) * mm});
            skLineSegment(sketch, "E3.21.0.98", {"start": v(43.88, 20.15) * mm, "end": v(47.42, 16.61) * mm});
            skLineSegment(sketch, "E3.21.0.99", {"start": v(47.9, 29.26) * mm, "end": v(44.37, 25.73) * mm});
            skLineSegment(sketch, "E3.21.0.100", {"start": v(47.91, 17.11) * mm, "end": v(44.38, 13.58) * mm});
            skLineSegment(sketch, "E3.21.0.101", {"start": v(47.4, 29.76) * mm, "end": v(43.87, 26.22) * mm});
            skLineSegment(sketch, "E3.21.0.102", {"start": v(47.42, 17.6) * mm, "end": v(43.88, 14.07) * mm});
            skLineSegment(sketch, "E3.21.0.103", {"start": v(44.38, 20.65) * mm, "end": v(43.88, 20.15) * mm});
            skLineSegment(sketch, "E3.21.0.104", {"start": v(47.95, -19.34) * mm, "end": v(47.45, -19.84) * mm});
            skLineSegment(sketch, "E3.21.0.105", {"start": v(47.94, -7.19) * mm, "end": v(47.44, -7.69) * mm});
            skLineSegment(sketch, "E3.21.0.106", {"start": v(47.92, 4.96) * mm, "end": v(47.43, 4.46) * mm});
            skLineSegment(sketch, "E3.21.0.107", {"start": v(47.96, -31.49) * mm, "end": v(47.46, -31.99) * mm});
            skLineSegment(sketch, "E3.21.0.108", {"start": v(47.9, 29.26) * mm, "end": v(47.4, 29.76) * mm});
            skLineSegment(sketch, "E3.21.0.109", {"start": v(47.91, 17.11) * mm, "end": v(47.42, 17.6) * mm});
            skLineSegment(sketch, "E3.21.0.110", {"start": v(44.38, 13.58) * mm, "end": v(43.88, 14.07) * mm});
            skLineSegment(sketch, "E3.21.0.111", {"start": v(44.37, 25.73) * mm, "end": v(43.87, 26.22) * mm});
            skLineSegment(sketch, "E3.21.0.112", {"start": v(44.4, -16.8) * mm, "end": v(43.9, -16.3) * mm});
            skLineSegment(sketch, "E3.21.0.113", {"start": v(44.4, -4.65) * mm, "end": v(43.9, -4.15) * mm});
            skLineSegment(sketch, "E3.21.0.114", {"start": v(44.42, -28.95) * mm, "end": v(43.92, -28.45) * mm});
            skLineSegment(sketch, "E3.21.0.115", {"start": v(47.9, 35.34) * mm, "end": v(47.4, 35.83) * mm});
            skLineSegment(sketch, "E3.21.0.116", {"start": v(44.36, 31.8) * mm, "end": v(43.86, 32.3) * mm});
            skLineSegment(sketch, "E3.21.0.117", {"start": v(44.35, 37.87) * mm, "end": v(43.86, 38.37) * mm});
            skLineSegment(sketch, "E3.21.0.118", {"start": v(44.37, 32.8) * mm, "end": v(43.87, 32.3) * mm});
            skLineSegment(sketch, "E3.21.0.119", {"start": v(47.9, 29.26) * mm, "end": v(47.4, 28.76) * mm});
            skLineSegment(sketch, "E3.21.0.120", {"start": v(47.91, 17.11) * mm, "end": v(47.42, 16.61) * mm});
            skLineSegment(sketch, "E3.22.0.0", {"start": v(49.75, 44.95) * mm, "end": v(53.29, 41.41) * mm});
            skLineSegment(sketch, "E3.22.0.1", {"start": v(49.26, 44.45) * mm, "end": v(52.8, 40.91) * mm});
            skLineSegment(sketch, "E3.22.0.2", {"start": v(49.75, 44.95) * mm, "end": v(49.26, 44.45) * mm});
            skLineSegment(sketch, "E3.22.0.3", {"start": v(53.37, -43.64) * mm, "end": v(49.84, -47.17) * mm});
            skLineSegment(sketch, "E3.22.0.4", {"start": v(52.87, -43.14) * mm, "end": v(49.34, -46.68) * mm});
            skLineSegment(sketch, "E3.22.0.5", {"start": v(49.84, -47.17) * mm, "end": v(49.34, -46.68) * mm});
            skLineSegment(sketch, "E3.22.0.6", {"start": v(49.79, 8.5) * mm, "end": v(53.32, 4.96) * mm});
            skLineSegment(sketch, "E3.22.0.7", {"start": v(53.37, -43.64) * mm, "end": v(52.87, -43.14) * mm});
            skLineSegment(sketch, "E3.22.0.8", {"start": v(53.32, 11.04) * mm, "end": v(49.78, 7.5) * mm});
            skLineSegment(sketch, "E3.22.0.9", {"start": v(53.37, -37.56) * mm, "end": v(49.83, -41.1) * mm});
            skLineSegment(sketch, "E3.22.0.10", {"start": v(53.35, -25.41) * mm, "end": v(49.82, -28.95) * mm});
            skLineSegment(sketch, "E3.22.0.11", {"start": v(52.82, 11.53) * mm, "end": v(49.29, 8) * mm});
            skLineSegment(sketch, "E3.22.0.12", {"start": v(52.8, 23.68) * mm, "end": v(49.27, 20.15) * mm});
            skLineSegment(sketch, "E3.22.0.13", {"start": v(49.8, 2.42) * mm, "end": v(53.33, -1.11) * mm});
            skLineSegment(sketch, "E3.22.0.14", {"start": v(49.78, 14.57) * mm, "end": v(53.32, 11.04) * mm});
            skLineSegment(sketch, "E3.22.0.15", {"start": v(49.77, 26.72) * mm, "end": v(53.3, 23.19) * mm});
            skLineSegment(sketch, "E3.22.0.16", {"start": v(49.83, -34.03) * mm, "end": v(53.37, -37.56) * mm});
            skLineSegment(sketch, "E3.22.0.17", {"start": v(49.82, -21.88) * mm, "end": v(53.35, -25.41) * mm});
            skLineSegment(sketch, "E3.22.0.18", {"start": v(49.8, -9.73) * mm, "end": v(53.34, -13.26) * mm});
            skLineSegment(sketch, "E3.22.0.19", {"start": v(53.34, -13.26) * mm, "end": v(52.84, -13.76) * mm});
            skLineSegment(sketch, "E3.22.0.20", {"start": v(53.33, -1.11) * mm, "end": v(52.83, -1.61) * mm});
            skLineSegment(sketch, "E3.22.0.21", {"start": v(53.32, 11.04) * mm, "end": v(52.82, 10.54) * mm});
            skLineSegment(sketch, "E3.22.0.22", {"start": v(53.3, 23.19) * mm, "end": v(52.8, 22.69) * mm});
            skLineSegment(sketch, "E3.22.0.23", {"start": v(53.37, -37.56) * mm, "end": v(52.87, -38.06) * mm});
            skLineSegment(sketch, "E3.22.0.24", {"start": v(53.35, -25.41) * mm, "end": v(52.86, -25.91) * mm});
            skLineSegment(sketch, "E3.22.0.25", {"start": v(53.34, -13.26) * mm, "end": v(52.84, -12.77) * mm});
            skLineSegment(sketch, "E3.22.0.26", {"start": v(53.33, -1.11) * mm, "end": v(52.83, -0.62) * mm});
            skLineSegment(sketch, "E3.22.0.27", {"start": v(53.32, 11.04) * mm, "end": v(52.82, 11.53) * mm});
            skLineSegment(sketch, "E3.22.0.28", {"start": v(53.3, 23.19) * mm, "end": v(52.8, 23.68) * mm});
            skLineSegment(sketch, "E3.22.0.29", {"start": v(53.37, -37.56) * mm, "end": v(52.87, -37.07) * mm});
            skLineSegment(sketch, "E3.22.0.30", {"start": v(53.35, -25.41) * mm, "end": v(52.86, -24.92) * mm});
            skLineSegment(sketch, "E3.22.0.31", {"start": v(49.78, 7.5) * mm, "end": v(49.29, 8) * mm});
            skLineSegment(sketch, "E3.22.0.32", {"start": v(53.29, 41.41) * mm, "end": v(49.75, 37.87) * mm});
            skLineSegment(sketch, "E3.22.0.33", {"start": v(52.8, 41.9) * mm, "end": v(49.26, 38.37) * mm});
            skLineSegment(sketch, "E3.22.0.34", {"start": v(53.29, 41.41) * mm, "end": v(52.8, 41.9) * mm});
            skLineSegment(sketch, "E3.22.0.35", {"start": v(49.26, 38.37) * mm, "end": v(52.8, 34.84) * mm});
            skLineSegment(sketch, "E3.22.0.36", {"start": v(49.76, 38.87) * mm, "end": v(53.3, 35.34) * mm});
            skLineSegment(sketch, "E3.22.0.37", {"start": v(49.34, -40.6) * mm, "end": v(52.87, -44.14) * mm});
            skLineSegment(sketch, "E3.22.0.38", {"start": v(49.3, 8) * mm, "end": v(52.83, 4.46) * mm});
            skLineSegment(sketch, "E3.22.0.39", {"start": v(53.35, -19.34) * mm, "end": v(49.81, -22.87) * mm});
            skLineSegment(sketch, "E3.22.0.40", {"start": v(53.34, -7.19) * mm, "end": v(49.8, -10.72) * mm});
            skLineSegment(sketch, "E3.22.0.41", {"start": v(53.32, 4.96) * mm, "end": v(49.79, 1.43) * mm});
            skLineSegment(sketch, "E3.22.0.42", {"start": v(53.36, -31.49) * mm, "end": v(49.82, -35.02) * mm});
            skLineSegment(sketch, "E3.22.0.43", {"start": v(52.85, -18.84) * mm, "end": v(49.31, -22.38) * mm});
            skLineSegment(sketch, "E3.22.0.44", {"start": v(52.84, -6.7) * mm, "end": v(49.3, -10.23) * mm});
            skLineSegment(sketch, "E3.22.0.45", {"start": v(52.83, 5.46) * mm, "end": v(49.3, 1.92) * mm});
            skLineSegment(sketch, "E3.22.0.46", {"start": v(52.86, -31) * mm, "end": v(49.33, -34.53) * mm});
            skLineSegment(sketch, "E3.22.0.47", {"start": v(49.81, -15.8) * mm, "end": v(53.35, -19.34) * mm});
            skLineSegment(sketch, "E3.22.0.48", {"start": v(49.8, -3.65) * mm, "end": v(53.34, -7.19) * mm});
            skLineSegment(sketch, "E3.22.0.49", {"start": v(49.77, 32.8) * mm, "end": v(53.3, 29.26) * mm});
            skLineSegment(sketch, "E3.22.0.50", {"start": v(49.84, -40.1) * mm, "end": v(53.37, -43.64) * mm});
            skLineSegment(sketch, "E3.22.0.51", {"start": v(49.82, -27.95) * mm, "end": v(53.36, -31.49) * mm});
            skLineSegment(sketch, "E3.22.0.52", {"start": v(49.78, 20.65) * mm, "end": v(53.31, 17.11) * mm});
            skLineSegment(sketch, "E3.22.0.53", {"start": v(49.81, -15.8) * mm, "end": v(49.31, -16.3) * mm});
            skLineSegment(sketch, "E3.22.0.54", {"start": v(49.8, -3.65) * mm, "end": v(49.3, -4.15) * mm});
            skLineSegment(sketch, "E3.22.0.55", {"start": v(49.79, 8.5) * mm, "end": v(49.3, 8) * mm});
            skLineSegment(sketch, "E3.22.0.56", {"start": v(49.84, -40.1) * mm, "end": v(49.34, -40.6) * mm});
            skLineSegment(sketch, "E3.22.0.57", {"start": v(49.82, -27.95) * mm, "end": v(49.33, -28.45) * mm});
            skLineSegment(sketch, "E3.22.0.58", {"start": v(53.37, -43.64) * mm, "end": v(52.87, -44.14) * mm});
            skLineSegment(sketch, "E3.22.0.59", {"start": v(53.35, -19.34) * mm, "end": v(52.85, -18.84) * mm});
            skLineSegment(sketch, "E3.22.0.60", {"start": v(53.34, -7.19) * mm, "end": v(52.84, -6.7) * mm});
            skLineSegment(sketch, "E3.22.0.61", {"start": v(53.32, 4.96) * mm, "end": v(52.83, 5.46) * mm});
            skLineSegment(sketch, "E3.22.0.62", {"start": v(53.36, -31.49) * mm, "end": v(52.86, -31) * mm});
            skLineSegment(sketch, "E3.22.0.63", {"start": v(49.79, 1.43) * mm, "end": v(49.3, 1.92) * mm});
            skLineSegment(sketch, "E3.22.0.64", {"start": v(49.82, -35.02) * mm, "end": v(49.33, -34.53) * mm});
            skLineSegment(sketch, "E3.22.0.65", {"start": v(49.81, -22.87) * mm, "end": v(49.31, -22.38) * mm});
            skLineSegment(sketch, "E3.22.0.66", {"start": v(49.8, -10.72) * mm, "end": v(49.3, -10.23) * mm});
            skLineSegment(sketch, "E3.22.0.67", {"start": v(49.3, 1.92) * mm, "end": v(52.83, -1.61) * mm});
            skLineSegment(sketch, "E3.22.0.68", {"start": v(49.29, 14.07) * mm, "end": v(52.82, 10.54) * mm});
            skLineSegment(sketch, "E3.22.0.69", {"start": v(49.27, 26.22) * mm, "end": v(52.8, 22.69) * mm});
            skLineSegment(sketch, "E3.22.0.70", {"start": v(49.75, 37.87) * mm, "end": v(49.76, 31.8) * mm, "construction": true});
            skLineSegment(sketch, "E3.22.0.71", {"start": v(49.33, -34.52) * mm, "end": v(52.87, -38.06) * mm});
            skLineSegment(sketch, "E3.22.0.72", {"start": v(49.32, -22.38) * mm, "end": v(52.86, -25.91) * mm});
            skLineSegment(sketch, "E3.22.0.73", {"start": v(49.3, -10.23) * mm, "end": v(52.84, -13.76) * mm});
            skLineSegment(sketch, "E3.22.0.74", {"start": v(53.33, -1.11) * mm, "end": v(49.8, -4.65) * mm});
            skLineSegment(sketch, "E3.22.0.75", {"start": v(53.3, 23.19) * mm, "end": v(49.77, 19.65) * mm});
            skLineSegment(sketch, "E3.22.0.76", {"start": v(53.34, -13.26) * mm, "end": v(49.8, -16.8) * mm});
            skLineSegment(sketch, "E3.22.0.77", {"start": v(52.83, -0.62) * mm, "end": v(49.3, -4.15) * mm});
            skLineSegment(sketch, "E3.22.0.78", {"start": v(52.87, -37.07) * mm, "end": v(49.33, -40.6) * mm});
            skLineSegment(sketch, "E3.22.0.79", {"start": v(52.86, -24.92) * mm, "end": v(49.32, -28.45) * mm});
            skLineSegment(sketch, "E3.22.0.80", {"start": v(52.84, -12.77) * mm, "end": v(49.3, -16.3) * mm});
            skLineSegment(sketch, "E3.22.0.81", {"start": v(49.8, 2.42) * mm, "end": v(49.3, 1.92) * mm});
            skLineSegment(sketch, "E3.22.0.82", {"start": v(49.78, 14.57) * mm, "end": v(49.29, 14.07) * mm});
            skLineSegment(sketch, "E3.22.0.83", {"start": v(49.77, 26.72) * mm, "end": v(49.27, 26.22) * mm});
            skLineSegment(sketch, "E3.22.0.84", {"start": v(49.83, -34.03) * mm, "end": v(49.33, -34.52) * mm});
            skLineSegment(sketch, "E3.22.0.85", {"start": v(49.82, -21.88) * mm, "end": v(49.32, -22.38) * mm});
            skLineSegment(sketch, "E3.22.0.86", {"start": v(49.8, -9.73) * mm, "end": v(49.3, -10.23) * mm});
            skLineSegment(sketch, "E3.22.0.87", {"start": v(49.77, 19.65) * mm, "end": v(49.27, 20.15) * mm});
            skLineSegment(sketch, "E3.22.0.88", {"start": v(49.83, -41.1) * mm, "end": v(49.33, -40.6) * mm});
            skLineSegment(sketch, "E3.22.0.89", {"start": v(53.3, 35.34) * mm, "end": v(52.8, 34.84) * mm});
            skLineSegment(sketch, "E3.22.0.90", {"start": v(53.29, 41.41) * mm, "end": v(52.8, 40.91) * mm});
            skLineSegment(sketch, "E3.22.0.91", {"start": v(53.3, 35.34) * mm, "end": v(49.76, 31.8) * mm});
            skLineSegment(sketch, "E3.22.0.92", {"start": v(52.8, 35.83) * mm, "end": v(49.26, 32.3) * mm});
            skLineSegment(sketch, "E3.22.0.93", {"start": v(49.76, 38.87) * mm, "end": v(49.26, 38.37) * mm});
            skLineSegment(sketch, "E3.22.0.94", {"start": v(49.33, -28.45) * mm, "end": v(52.86, -31.99) * mm});
            skLineSegment(sketch, "E3.22.0.95", {"start": v(49.27, 32.3) * mm, "end": v(52.8, 28.76) * mm});
            skLineSegment(sketch, "E3.22.0.96", {"start": v(49.31, -16.3) * mm, "end": v(52.85, -19.84) * mm});
            skLineSegment(sketch, "E3.22.0.97", {"start": v(49.3, -4.15) * mm, "end": v(52.84, -7.69) * mm});
            skLineSegment(sketch, "E3.22.0.98", {"start": v(49.28, 20.15) * mm, "end": v(52.82, 16.61) * mm});
            skLineSegment(sketch, "E3.22.0.99", {"start": v(53.3, 29.26) * mm, "end": v(49.77, 25.73) * mm});
            skLineSegment(sketch, "E3.22.0.100", {"start": v(53.31, 17.11) * mm, "end": v(49.78, 13.58) * mm});
            skLineSegment(sketch, "E3.22.0.101", {"start": v(52.8, 29.76) * mm, "end": v(49.27, 26.22) * mm});
            skLineSegment(sketch, "E3.22.0.102", {"start": v(52.82, 17.6) * mm, "end": v(49.28, 14.07) * mm});
            skLineSegment(sketch, "E3.22.0.103", {"start": v(49.78, 20.65) * mm, "end": v(49.28, 20.15) * mm});
            skLineSegment(sketch, "E3.22.0.104", {"start": v(53.35, -19.34) * mm, "end": v(52.85, -19.84) * mm});
            skLineSegment(sketch, "E3.22.0.105", {"start": v(53.34, -7.19) * mm, "end": v(52.84, -7.69) * mm});
            skLineSegment(sketch, "E3.22.0.106", {"start": v(53.32, 4.96) * mm, "end": v(52.83, 4.46) * mm});
            skLineSegment(sketch, "E3.22.0.107", {"start": v(53.36, -31.49) * mm, "end": v(52.86, -31.99) * mm});
            skLineSegment(sketch, "E3.22.0.108", {"start": v(53.3, 29.26) * mm, "end": v(52.8, 29.76) * mm});
            skLineSegment(sketch, "E3.22.0.109", {"start": v(53.31, 17.11) * mm, "end": v(52.82, 17.6) * mm});
            skLineSegment(sketch, "E3.22.0.110", {"start": v(49.78, 13.58) * mm, "end": v(49.28, 14.07) * mm});
            skLineSegment(sketch, "E3.22.0.111", {"start": v(49.77, 25.73) * mm, "end": v(49.27, 26.22) * mm});
            skLineSegment(sketch, "E3.22.0.112", {"start": v(49.8, -16.8) * mm, "end": v(49.3, -16.3) * mm});
            skLineSegment(sketch, "E3.22.0.113", {"start": v(49.8, -4.65) * mm, "end": v(49.3, -4.15) * mm});
            skLineSegment(sketch, "E3.22.0.114", {"start": v(49.82, -28.95) * mm, "end": v(49.32, -28.45) * mm});
            skLineSegment(sketch, "E3.22.0.115", {"start": v(53.3, 35.34) * mm, "end": v(52.8, 35.83) * mm});
            skLineSegment(sketch, "E3.22.0.116", {"start": v(49.76, 31.8) * mm, "end": v(49.26, 32.3) * mm});
            skLineSegment(sketch, "E3.22.0.117", {"start": v(49.75, 37.87) * mm, "end": v(49.26, 38.37) * mm});
            skLineSegment(sketch, "E3.22.0.118", {"start": v(49.77, 32.8) * mm, "end": v(49.27, 32.3) * mm});
            skLineSegment(sketch, "E3.22.0.119", {"start": v(53.3, 29.26) * mm, "end": v(52.8, 28.76) * mm});
            skLineSegment(sketch, "E3.22.0.120", {"start": v(53.31, 17.11) * mm, "end": v(52.82, 16.61) * mm});
            skLineSegment(sketch, "E3.23.0.0", {"start": v(55.15, 44.95) * mm, "end": v(58.69, 41.41) * mm});
            skLineSegment(sketch, "E3.23.0.1", {"start": v(54.66, 44.45) * mm, "end": v(58.2, 40.91) * mm});
            skLineSegment(sketch, "E3.23.0.2", {"start": v(55.15, 44.95) * mm, "end": v(54.66, 44.45) * mm});
            skLineSegment(sketch, "E3.23.0.3", {"start": v(58.77, -43.64) * mm, "end": v(55.24, -47.17) * mm});
            skLineSegment(sketch, "E3.23.0.4", {"start": v(58.27, -43.14) * mm, "end": v(54.74, -46.68) * mm});
            skLineSegment(sketch, "E3.23.0.5", {"start": v(55.24, -47.17) * mm, "end": v(54.74, -46.68) * mm});
            skLineSegment(sketch, "E3.23.0.6", {"start": v(55.19, 8.5) * mm, "end": v(58.72, 4.96) * mm});
            skLineSegment(sketch, "E3.23.0.7", {"start": v(58.77, -43.64) * mm, "end": v(58.27, -43.14) * mm});
            skLineSegment(sketch, "E3.23.0.8", {"start": v(58.72, 11.04) * mm, "end": v(55.18, 7.5) * mm});
            skLineSegment(sketch, "E3.23.0.9", {"start": v(58.77, -37.56) * mm, "end": v(55.23, -41.1) * mm});
            skLineSegment(sketch, "E3.23.0.10", {"start": v(58.75, -25.41) * mm, "end": v(55.22, -28.95) * mm});
            skLineSegment(sketch, "E3.23.0.11", {"start": v(58.22, 11.53) * mm, "end": v(54.69, 8) * mm});
            skLineSegment(sketch, "E3.23.0.12", {"start": v(58.2, 23.68) * mm, "end": v(54.67, 20.15) * mm});
            skLineSegment(sketch, "E3.23.0.13", {"start": v(55.2, 2.42) * mm, "end": v(58.73, -1.11) * mm});
            skLineSegment(sketch, "E3.23.0.14", {"start": v(55.18, 14.57) * mm, "end": v(58.72, 11.04) * mm});
            skLineSegment(sketch, "E3.23.0.15", {"start": v(55.17, 26.72) * mm, "end": v(58.7, 23.19) * mm});
            skLineSegment(sketch, "E3.23.0.16", {"start": v(55.23, -34.03) * mm, "end": v(58.77, -37.56) * mm});
            skLineSegment(sketch, "E3.23.0.17", {"start": v(55.22, -21.88) * mm, "end": v(58.75, -25.41) * mm});
            skLineSegment(sketch, "E3.23.0.18", {"start": v(55.2, -9.73) * mm, "end": v(58.74, -13.26) * mm});
            skLineSegment(sketch, "E3.23.0.19", {"start": v(58.74, -13.26) * mm, "end": v(58.24, -13.76) * mm});
            skLineSegment(sketch, "E3.23.0.20", {"start": v(58.73, -1.11) * mm, "end": v(58.23, -1.61) * mm});
            skLineSegment(sketch, "E3.23.0.21", {"start": v(58.72, 11.04) * mm, "end": v(58.22, 10.54) * mm});
            skLineSegment(sketch, "E3.23.0.22", {"start": v(58.7, 23.19) * mm, "end": v(58.2, 22.69) * mm});
            skLineSegment(sketch, "E3.23.0.23", {"start": v(58.77, -37.56) * mm, "end": v(58.27, -38.06) * mm});
            skLineSegment(sketch, "E3.23.0.24", {"start": v(58.75, -25.41) * mm, "end": v(58.26, -25.91) * mm});
            skLineSegment(sketch, "E3.23.0.25", {"start": v(58.74, -13.26) * mm, "end": v(58.24, -12.77) * mm});
            skLineSegment(sketch, "E3.23.0.26", {"start": v(58.73, -1.11) * mm, "end": v(58.23, -0.62) * mm});
            skLineSegment(sketch, "E3.23.0.27", {"start": v(58.72, 11.04) * mm, "end": v(58.22, 11.53) * mm});
            skLineSegment(sketch, "E3.23.0.28", {"start": v(58.7, 23.19) * mm, "end": v(58.2, 23.68) * mm});
            skLineSegment(sketch, "E3.23.0.29", {"start": v(58.77, -37.56) * mm, "end": v(58.27, -37.07) * mm});
            skLineSegment(sketch, "E3.23.0.30", {"start": v(58.75, -25.41) * mm, "end": v(58.26, -24.92) * mm});
            skLineSegment(sketch, "E3.23.0.31", {"start": v(55.18, 7.5) * mm, "end": v(54.69, 8) * mm});
            skLineSegment(sketch, "E3.23.0.32", {"start": v(58.69, 41.41) * mm, "end": v(55.15, 37.87) * mm});
            skLineSegment(sketch, "E3.23.0.33", {"start": v(58.2, 41.9) * mm, "end": v(54.66, 38.37) * mm});
            skLineSegment(sketch, "E3.23.0.34", {"start": v(58.69, 41.41) * mm, "end": v(58.2, 41.9) * mm});
            skLineSegment(sketch, "E3.23.0.35", {"start": v(54.66, 38.37) * mm, "end": v(58.2, 34.84) * mm});
            skLineSegment(sketch, "E3.23.0.36", {"start": v(55.16, 38.87) * mm, "end": v(58.7, 35.34) * mm});
            skLineSegment(sketch, "E3.23.0.37", {"start": v(54.74, -40.6) * mm, "end": v(58.27, -44.14) * mm});
            skLineSegment(sketch, "E3.23.0.38", {"start": v(54.7, 8) * mm, "end": v(58.23, 4.46) * mm});
            skLineSegment(sketch, "E3.23.0.39", {"start": v(58.75, -19.34) * mm, "end": v(55.21, -22.87) * mm});
            skLineSegment(sketch, "E3.23.0.40", {"start": v(58.74, -7.19) * mm, "end": v(55.2, -10.72) * mm});
            skLineSegment(sketch, "E3.23.0.41", {"start": v(58.72, 4.96) * mm, "end": v(55.19, 1.43) * mm});
            skLineSegment(sketch, "E3.23.0.42", {"start": v(58.76, -31.49) * mm, "end": v(55.22, -35.02) * mm});
            skLineSegment(sketch, "E3.23.0.43", {"start": v(58.25, -18.84) * mm, "end": v(54.71, -22.38) * mm});
            skLineSegment(sketch, "E3.23.0.44", {"start": v(58.24, -6.7) * mm, "end": v(54.7, -10.23) * mm});
            skLineSegment(sketch, "E3.23.0.45", {"start": v(58.23, 5.46) * mm, "end": v(54.7, 1.92) * mm});
            skLineSegment(sketch, "E3.23.0.46", {"start": v(58.26, -31) * mm, "end": v(54.73, -34.53) * mm});
            skLineSegment(sketch, "E3.23.0.47", {"start": v(55.21, -15.8) * mm, "end": v(58.75, -19.34) * mm});
            skLineSegment(sketch, "E3.23.0.48", {"start": v(55.2, -3.65) * mm, "end": v(58.74, -7.19) * mm});
            skLineSegment(sketch, "E3.23.0.49", {"start": v(55.17, 32.8) * mm, "end": v(58.7, 29.26) * mm});
            skLineSegment(sketch, "E3.23.0.50", {"start": v(55.24, -40.1) * mm, "end": v(58.77, -43.64) * mm});
            skLineSegment(sketch, "E3.23.0.51", {"start": v(55.22, -27.95) * mm, "end": v(58.76, -31.49) * mm});
            skLineSegment(sketch, "E3.23.0.52", {"start": v(55.18, 20.65) * mm, "end": v(58.71, 17.11) * mm});
            skLineSegment(sketch, "E3.23.0.53", {"start": v(55.21, -15.8) * mm, "end": v(54.71, -16.3) * mm});
            skLineSegment(sketch, "E3.23.0.54", {"start": v(55.2, -3.65) * mm, "end": v(54.7, -4.15) * mm});
            skLineSegment(sketch, "E3.23.0.55", {"start": v(55.19, 8.5) * mm, "end": v(54.7, 8) * mm});
            skLineSegment(sketch, "E3.23.0.56", {"start": v(55.24, -40.1) * mm, "end": v(54.74, -40.6) * mm});
            skLineSegment(sketch, "E3.23.0.57", {"start": v(55.22, -27.95) * mm, "end": v(54.73, -28.45) * mm});
            skLineSegment(sketch, "E3.23.0.58", {"start": v(58.77, -43.64) * mm, "end": v(58.27, -44.14) * mm});
            skLineSegment(sketch, "E3.23.0.59", {"start": v(58.75, -19.34) * mm, "end": v(58.25, -18.84) * mm});
            skLineSegment(sketch, "E3.23.0.60", {"start": v(58.74, -7.19) * mm, "end": v(58.24, -6.7) * mm});
            skLineSegment(sketch, "E3.23.0.61", {"start": v(58.72, 4.96) * mm, "end": v(58.23, 5.46) * mm});
            skLineSegment(sketch, "E3.23.0.62", {"start": v(58.76, -31.49) * mm, "end": v(58.26, -31) * mm});
            skLineSegment(sketch, "E3.23.0.63", {"start": v(55.19, 1.43) * mm, "end": v(54.7, 1.92) * mm});
            skLineSegment(sketch, "E3.23.0.64", {"start": v(55.22, -35.02) * mm, "end": v(54.73, -34.53) * mm});
            skLineSegment(sketch, "E3.23.0.65", {"start": v(55.21, -22.87) * mm, "end": v(54.71, -22.38) * mm});
            skLineSegment(sketch, "E3.23.0.66", {"start": v(55.2, -10.72) * mm, "end": v(54.7, -10.23) * mm});
            skLineSegment(sketch, "E3.23.0.67", {"start": v(54.7, 1.92) * mm, "end": v(58.23, -1.61) * mm});
            skLineSegment(sketch, "E3.23.0.68", {"start": v(54.69, 14.07) * mm, "end": v(58.22, 10.54) * mm});
            skLineSegment(sketch, "E3.23.0.69", {"start": v(54.67, 26.22) * mm, "end": v(58.2, 22.69) * mm});
            skLineSegment(sketch, "E3.23.0.70", {"start": v(55.15, 37.87) * mm, "end": v(55.16, 31.8) * mm, "construction": true});
            skLineSegment(sketch, "E3.23.0.71", {"start": v(54.73, -34.52) * mm, "end": v(58.27, -38.06) * mm});
            skLineSegment(sketch, "E3.23.0.72", {"start": v(54.72, -22.38) * mm, "end": v(58.26, -25.91) * mm});
            skLineSegment(sketch, "E3.23.0.73", {"start": v(54.7, -10.23) * mm, "end": v(58.24, -13.76) * mm});
            skLineSegment(sketch, "E3.23.0.74", {"start": v(58.73, -1.11) * mm, "end": v(55.2, -4.65) * mm});
            skLineSegment(sketch, "E3.23.0.75", {"start": v(58.7, 23.19) * mm, "end": v(55.17, 19.65) * mm});
            skLineSegment(sketch, "E3.23.0.76", {"start": v(58.74, -13.26) * mm, "end": v(55.2, -16.8) * mm});
            skLineSegment(sketch, "E3.23.0.77", {"start": v(58.23, -0.62) * mm, "end": v(54.7, -4.15) * mm});
            skLineSegment(sketch, "E3.23.0.78", {"start": v(58.27, -37.07) * mm, "end": v(54.73, -40.6) * mm});
            skLineSegment(sketch, "E3.23.0.79", {"start": v(58.26, -24.92) * mm, "end": v(54.72, -28.45) * mm});
            skLineSegment(sketch, "E3.23.0.80", {"start": v(58.24, -12.77) * mm, "end": v(54.7, -16.3) * mm});
            skLineSegment(sketch, "E3.23.0.81", {"start": v(55.2, 2.42) * mm, "end": v(54.7, 1.92) * mm});
            skLineSegment(sketch, "E3.23.0.82", {"start": v(55.18, 14.57) * mm, "end": v(54.69, 14.07) * mm});
            skLineSegment(sketch, "E3.23.0.83", {"start": v(55.17, 26.72) * mm, "end": v(54.67, 26.22) * mm});
            skLineSegment(sketch, "E3.23.0.84", {"start": v(55.23, -34.03) * mm, "end": v(54.73, -34.52) * mm});
            skLineSegment(sketch, "E3.23.0.85", {"start": v(55.22, -21.88) * mm, "end": v(54.72, -22.38) * mm});
            skLineSegment(sketch, "E3.23.0.86", {"start": v(55.2, -9.73) * mm, "end": v(54.7, -10.23) * mm});
            skLineSegment(sketch, "E3.23.0.87", {"start": v(55.17, 19.65) * mm, "end": v(54.67, 20.15) * mm});
            skLineSegment(sketch, "E3.23.0.88", {"start": v(55.23, -41.1) * mm, "end": v(54.73, -40.6) * mm});
            skLineSegment(sketch, "E3.23.0.89", {"start": v(58.7, 35.34) * mm, "end": v(58.2, 34.84) * mm});
            skLineSegment(sketch, "E3.23.0.90", {"start": v(58.69, 41.41) * mm, "end": v(58.2, 40.91) * mm});
            skLineSegment(sketch, "E3.23.0.91", {"start": v(58.7, 35.34) * mm, "end": v(55.16, 31.8) * mm});
            skLineSegment(sketch, "E3.23.0.92", {"start": v(58.2, 35.83) * mm, "end": v(54.66, 32.3) * mm});
            skLineSegment(sketch, "E3.23.0.93", {"start": v(55.16, 38.87) * mm, "end": v(54.66, 38.37) * mm});
            skLineSegment(sketch, "E3.23.0.94", {"start": v(54.73, -28.45) * mm, "end": v(58.26, -31.99) * mm});
            skLineSegment(sketch, "E3.23.0.95", {"start": v(54.67, 32.3) * mm, "end": v(58.2, 28.76) * mm});
            skLineSegment(sketch, "E3.23.0.96", {"start": v(54.71, -16.3) * mm, "end": v(58.25, -19.84) * mm});
            skLineSegment(sketch, "E3.23.0.97", {"start": v(54.7, -4.15) * mm, "end": v(58.24, -7.69) * mm});
            skLineSegment(sketch, "E3.23.0.98", {"start": v(54.68, 20.15) * mm, "end": v(58.22, 16.61) * mm});
            skLineSegment(sketch, "E3.23.0.99", {"start": v(58.7, 29.26) * mm, "end": v(55.17, 25.73) * mm});
            skLineSegment(sketch, "E3.23.0.100", {"start": v(58.71, 17.11) * mm, "end": v(55.18, 13.58) * mm});
            skLineSegment(sketch, "E3.23.0.101", {"start": v(58.2, 29.76) * mm, "end": v(54.67, 26.22) * mm});
            skLineSegment(sketch, "E3.23.0.102", {"start": v(58.22, 17.6) * mm, "end": v(54.68, 14.07) * mm});
            skLineSegment(sketch, "E3.23.0.103", {"start": v(55.18, 20.65) * mm, "end": v(54.68, 20.15) * mm});
            skLineSegment(sketch, "E3.23.0.104", {"start": v(58.75, -19.34) * mm, "end": v(58.25, -19.84) * mm});
            skLineSegment(sketch, "E3.23.0.105", {"start": v(58.74, -7.19) * mm, "end": v(58.24, -7.69) * mm});
            skLineSegment(sketch, "E3.23.0.106", {"start": v(58.72, 4.96) * mm, "end": v(58.23, 4.46) * mm});
            skLineSegment(sketch, "E3.23.0.107", {"start": v(58.76, -31.49) * mm, "end": v(58.26, -31.99) * mm});
            skLineSegment(sketch, "E3.23.0.108", {"start": v(58.7, 29.26) * mm, "end": v(58.2, 29.76) * mm});
            skLineSegment(sketch, "E3.23.0.109", {"start": v(58.71, 17.11) * mm, "end": v(58.22, 17.6) * mm});
            skLineSegment(sketch, "E3.23.0.110", {"start": v(55.18, 13.58) * mm, "end": v(54.68, 14.07) * mm});
            skLineSegment(sketch, "E3.23.0.111", {"start": v(55.17, 25.73) * mm, "end": v(54.67, 26.22) * mm});
            skLineSegment(sketch, "E3.23.0.112", {"start": v(55.2, -16.8) * mm, "end": v(54.7, -16.3) * mm});
            skLineSegment(sketch, "E3.23.0.113", {"start": v(55.2, -4.65) * mm, "end": v(54.7, -4.15) * mm});
            skLineSegment(sketch, "E3.23.0.114", {"start": v(55.22, -28.95) * mm, "end": v(54.72, -28.45) * mm});
            skLineSegment(sketch, "E3.23.0.115", {"start": v(58.7, 35.34) * mm, "end": v(58.2, 35.83) * mm});
            skLineSegment(sketch, "E3.23.0.116", {"start": v(55.16, 31.8) * mm, "end": v(54.66, 32.3) * mm});
            skLineSegment(sketch, "E3.23.0.117", {"start": v(55.15, 37.87) * mm, "end": v(54.66, 38.37) * mm});
            skLineSegment(sketch, "E3.23.0.118", {"start": v(55.17, 32.8) * mm, "end": v(54.67, 32.3) * mm});
            skLineSegment(sketch, "E3.23.0.119", {"start": v(58.7, 29.26) * mm, "end": v(58.2, 28.76) * mm});
            skLineSegment(sketch, "E3.23.0.120", {"start": v(58.71, 17.11) * mm, "end": v(58.22, 16.61) * mm});
            skLineSegment(sketch, "E3.24.0.0", {"start": v(60.55, 44.95) * mm, "end": v(64.09, 41.41) * mm});
            skLineSegment(sketch, "E3.24.0.1", {"start": v(60.06, 44.45) * mm, "end": v(63.6, 40.91) * mm});
            skLineSegment(sketch, "E3.24.0.2", {"start": v(60.55, 44.95) * mm, "end": v(60.06, 44.45) * mm});
            skLineSegment(sketch, "E3.24.0.3", {"start": v(64.17, -43.64) * mm, "end": v(60.64, -47.17) * mm});
            skLineSegment(sketch, "E3.24.0.4", {"start": v(63.67, -43.14) * mm, "end": v(60.14, -46.68) * mm});
            skLineSegment(sketch, "E3.24.0.5", {"start": v(60.64, -47.17) * mm, "end": v(60.14, -46.68) * mm});
            skLineSegment(sketch, "E3.24.0.6", {"start": v(60.59, 8.5) * mm, "end": v(64.12, 4.96) * mm});
            skLineSegment(sketch, "E3.24.0.7", {"start": v(64.17, -43.64) * mm, "end": v(63.67, -43.14) * mm});
            skLineSegment(sketch, "E3.24.0.8", {"start": v(64.12, 11.04) * mm, "end": v(60.58, 7.5) * mm});
            skLineSegment(sketch, "E3.24.0.9", {"start": v(64.17, -37.56) * mm, "end": v(60.63, -41.1) * mm});
            skLineSegment(sketch, "E3.24.0.10", {"start": v(64.15, -25.41) * mm, "end": v(60.62, -28.95) * mm});
            skLineSegment(sketch, "E3.24.0.11", {"start": v(63.62, 11.53) * mm, "end": v(60.09, 8) * mm});
            skLineSegment(sketch, "E3.24.0.12", {"start": v(63.6, 23.68) * mm, "end": v(60.07, 20.15) * mm});
            skLineSegment(sketch, "E3.24.0.13", {"start": v(60.6, 2.42) * mm, "end": v(64.13, -1.11) * mm});
            skLineSegment(sketch, "E3.24.0.14", {"start": v(60.58, 14.57) * mm, "end": v(64.12, 11.04) * mm});
            skLineSegment(sketch, "E3.24.0.15", {"start": v(60.57, 26.72) * mm, "end": v(64.1, 23.19) * mm});
            skLineSegment(sketch, "E3.24.0.16", {"start": v(60.63, -34.03) * mm, "end": v(64.17, -37.56) * mm});
            skLineSegment(sketch, "E3.24.0.17", {"start": v(60.62, -21.88) * mm, "end": v(64.15, -25.41) * mm});
            skLineSegment(sketch, "E3.24.0.18", {"start": v(60.6, -9.73) * mm, "end": v(64.14, -13.26) * mm});
            skLineSegment(sketch, "E3.24.0.19", {"start": v(64.14, -13.26) * mm, "end": v(63.64, -13.76) * mm});
            skLineSegment(sketch, "E3.24.0.20", {"start": v(64.13, -1.11) * mm, "end": v(63.63, -1.61) * mm});
            skLineSegment(sketch, "E3.24.0.21", {"start": v(64.12, 11.04) * mm, "end": v(63.62, 10.54) * mm});
            skLineSegment(sketch, "E3.24.0.22", {"start": v(64.1, 23.19) * mm, "end": v(63.6, 22.69) * mm});
            skLineSegment(sketch, "E3.24.0.23", {"start": v(64.17, -37.56) * mm, "end": v(63.67, -38.06) * mm});
            skLineSegment(sketch, "E3.24.0.24", {"start": v(64.15, -25.41) * mm, "end": v(63.66, -25.91) * mm});
            skLineSegment(sketch, "E3.24.0.25", {"start": v(64.14, -13.26) * mm, "end": v(63.64, -12.77) * mm});
            skLineSegment(sketch, "E3.24.0.26", {"start": v(64.13, -1.11) * mm, "end": v(63.63, -0.62) * mm});
            skLineSegment(sketch, "E3.24.0.27", {"start": v(64.12, 11.04) * mm, "end": v(63.62, 11.53) * mm});
            skLineSegment(sketch, "E3.24.0.28", {"start": v(64.1, 23.19) * mm, "end": v(63.6, 23.68) * mm});
            skLineSegment(sketch, "E3.24.0.29", {"start": v(64.17, -37.56) * mm, "end": v(63.67, -37.07) * mm});
            skLineSegment(sketch, "E3.24.0.30", {"start": v(64.15, -25.41) * mm, "end": v(63.66, -24.92) * mm});
            skLineSegment(sketch, "E3.24.0.31", {"start": v(60.58, 7.5) * mm, "end": v(60.09, 8) * mm});
            skLineSegment(sketch, "E3.24.0.32", {"start": v(64.09, 41.41) * mm, "end": v(60.55, 37.87) * mm});
            skLineSegment(sketch, "E3.24.0.33", {"start": v(63.6, 41.9) * mm, "end": v(60.06, 38.37) * mm});
            skLineSegment(sketch, "E3.24.0.34", {"start": v(64.09, 41.41) * mm, "end": v(63.6, 41.9) * mm});
            skLineSegment(sketch, "E3.24.0.35", {"start": v(60.06, 38.37) * mm, "end": v(63.6, 34.84) * mm});
            skLineSegment(sketch, "E3.24.0.36", {"start": v(60.56, 38.87) * mm, "end": v(64.1, 35.34) * mm});
            skLineSegment(sketch, "E3.24.0.37", {"start": v(60.14, -40.6) * mm, "end": v(63.67, -44.14) * mm});
            skLineSegment(sketch, "E3.24.0.38", {"start": v(60.1, 8) * mm, "end": v(63.63, 4.46) * mm});
            skLineSegment(sketch, "E3.24.0.39", {"start": v(64.15, -19.34) * mm, "end": v(60.61, -22.87) * mm});
            skLineSegment(sketch, "E3.24.0.40", {"start": v(64.14, -7.19) * mm, "end": v(60.6, -10.72) * mm});
            skLineSegment(sketch, "E3.24.0.41", {"start": v(64.12, 4.96) * mm, "end": v(60.59, 1.43) * mm});
            skLineSegment(sketch, "E3.24.0.42", {"start": v(64.16, -31.49) * mm, "end": v(60.62, -35.02) * mm});
            skLineSegment(sketch, "E3.24.0.43", {"start": v(63.65, -18.84) * mm, "end": v(60.11, -22.38) * mm});
            skLineSegment(sketch, "E3.24.0.44", {"start": v(63.64, -6.7) * mm, "end": v(60.1, -10.23) * mm});
            skLineSegment(sketch, "E3.24.0.45", {"start": v(63.63, 5.46) * mm, "end": v(60.1, 1.92) * mm});
            skLineSegment(sketch, "E3.24.0.46", {"start": v(63.66, -31) * mm, "end": v(60.13, -34.53) * mm});
            skLineSegment(sketch, "E3.24.0.47", {"start": v(60.61, -15.8) * mm, "end": v(64.15, -19.34) * mm});
            skLineSegment(sketch, "E3.24.0.48", {"start": v(60.6, -3.65) * mm, "end": v(64.14, -7.19) * mm});
            skLineSegment(sketch, "E3.24.0.49", {"start": v(60.57, 32.8) * mm, "end": v(64.1, 29.26) * mm});
            skLineSegment(sketch, "E3.24.0.50", {"start": v(60.64, -40.1) * mm, "end": v(64.17, -43.64) * mm});
            skLineSegment(sketch, "E3.24.0.51", {"start": v(60.62, -27.95) * mm, "end": v(64.16, -31.49) * mm});
            skLineSegment(sketch, "E3.24.0.52", {"start": v(60.58, 20.65) * mm, "end": v(64.11, 17.11) * mm});
            skLineSegment(sketch, "E3.24.0.53", {"start": v(60.61, -15.8) * mm, "end": v(60.11, -16.3) * mm});
            skLineSegment(sketch, "E3.24.0.54", {"start": v(60.6, -3.65) * mm, "end": v(60.1, -4.15) * mm});
            skLineSegment(sketch, "E3.24.0.55", {"start": v(60.59, 8.5) * mm, "end": v(60.1, 8) * mm});
            skLineSegment(sketch, "E3.24.0.56", {"start": v(60.64, -40.1) * mm, "end": v(60.14, -40.6) * mm});
            skLineSegment(sketch, "E3.24.0.57", {"start": v(60.62, -27.95) * mm, "end": v(60.13, -28.45) * mm});
            skLineSegment(sketch, "E3.24.0.58", {"start": v(64.17, -43.64) * mm, "end": v(63.67, -44.14) * mm});
            skLineSegment(sketch, "E3.24.0.59", {"start": v(64.15, -19.34) * mm, "end": v(63.65, -18.84) * mm});
            skLineSegment(sketch, "E3.24.0.60", {"start": v(64.14, -7.19) * mm, "end": v(63.64, -6.7) * mm});
            skLineSegment(sketch, "E3.24.0.61", {"start": v(64.12, 4.96) * mm, "end": v(63.63, 5.46) * mm});
            skLineSegment(sketch, "E3.24.0.62", {"start": v(64.16, -31.49) * mm, "end": v(63.66, -31) * mm});
            skLineSegment(sketch, "E3.24.0.63", {"start": v(60.59, 1.43) * mm, "end": v(60.1, 1.92) * mm});
            skLineSegment(sketch, "E3.24.0.64", {"start": v(60.62, -35.02) * mm, "end": v(60.13, -34.53) * mm});
            skLineSegment(sketch, "E3.24.0.65", {"start": v(60.61, -22.87) * mm, "end": v(60.11, -22.38) * mm});
            skLineSegment(sketch, "E3.24.0.66", {"start": v(60.6, -10.72) * mm, "end": v(60.1, -10.23) * mm});
            skLineSegment(sketch, "E3.24.0.67", {"start": v(60.1, 1.92) * mm, "end": v(63.63, -1.61) * mm});
            skLineSegment(sketch, "E3.24.0.68", {"start": v(60.09, 14.07) * mm, "end": v(63.62, 10.54) * mm});
            skLineSegment(sketch, "E3.24.0.69", {"start": v(60.07, 26.22) * mm, "end": v(63.6, 22.69) * mm});
            skLineSegment(sketch, "E3.24.0.70", {"start": v(60.55, 37.87) * mm, "end": v(60.56, 31.8) * mm, "construction": true});
            skLineSegment(sketch, "E3.24.0.71", {"start": v(60.13, -34.52) * mm, "end": v(63.67, -38.06) * mm});
            skLineSegment(sketch, "E3.24.0.72", {"start": v(60.12, -22.38) * mm, "end": v(63.66, -25.91) * mm});
            skLineSegment(sketch, "E3.24.0.73", {"start": v(60.1, -10.23) * mm, "end": v(63.64, -13.76) * mm});
            skLineSegment(sketch, "E3.24.0.74", {"start": v(64.13, -1.11) * mm, "end": v(60.6, -4.65) * mm});
            skLineSegment(sketch, "E3.24.0.75", {"start": v(64.1, 23.19) * mm, "end": v(60.57, 19.65) * mm});
            skLineSegment(sketch, "E3.24.0.76", {"start": v(64.14, -13.26) * mm, "end": v(60.6, -16.8) * mm});
            skLineSegment(sketch, "E3.24.0.77", {"start": v(63.63, -0.62) * mm, "end": v(60.1, -4.15) * mm});
            skLineSegment(sketch, "E3.24.0.78", {"start": v(63.67, -37.07) * mm, "end": v(60.13, -40.6) * mm});
            skLineSegment(sketch, "E3.24.0.79", {"start": v(63.66, -24.92) * mm, "end": v(60.12, -28.45) * mm});
            skLineSegment(sketch, "E3.24.0.80", {"start": v(63.64, -12.77) * mm, "end": v(60.1, -16.3) * mm});
            skLineSegment(sketch, "E3.24.0.81", {"start": v(60.6, 2.42) * mm, "end": v(60.1, 1.92) * mm});
            skLineSegment(sketch, "E3.24.0.82", {"start": v(60.58, 14.57) * mm, "end": v(60.09, 14.07) * mm});
            skLineSegment(sketch, "E3.24.0.83", {"start": v(60.57, 26.72) * mm, "end": v(60.07, 26.22) * mm});
            skLineSegment(sketch, "E3.24.0.84", {"start": v(60.63, -34.03) * mm, "end": v(60.13, -34.52) * mm});
            skLineSegment(sketch, "E3.24.0.85", {"start": v(60.62, -21.88) * mm, "end": v(60.12, -22.38) * mm});
            skLineSegment(sketch, "E3.24.0.86", {"start": v(60.6, -9.73) * mm, "end": v(60.1, -10.23) * mm});
            skLineSegment(sketch, "E3.24.0.87", {"start": v(60.57, 19.65) * mm, "end": v(60.07, 20.15) * mm});
            skLineSegment(sketch, "E3.24.0.88", {"start": v(60.63, -41.1) * mm, "end": v(60.13, -40.6) * mm});
            skLineSegment(sketch, "E3.24.0.89", {"start": v(64.1, 35.34) * mm, "end": v(63.6, 34.84) * mm});
            skLineSegment(sketch, "E3.24.0.90", {"start": v(64.09, 41.41) * mm, "end": v(63.6, 40.91) * mm});
            skLineSegment(sketch, "E3.24.0.91", {"start": v(64.1, 35.34) * mm, "end": v(60.56, 31.8) * mm});
            skLineSegment(sketch, "E3.24.0.92", {"start": v(63.6, 35.83) * mm, "end": v(60.06, 32.3) * mm});
            skLineSegment(sketch, "E3.24.0.93", {"start": v(60.56, 38.87) * mm, "end": v(60.06, 38.37) * mm});
            skLineSegment(sketch, "E3.24.0.94", {"start": v(60.13, -28.45) * mm, "end": v(63.66, -31.99) * mm});
            skLineSegment(sketch, "E3.24.0.95", {"start": v(60.07, 32.3) * mm, "end": v(63.6, 28.76) * mm});
            skLineSegment(sketch, "E3.24.0.96", {"start": v(60.11, -16.3) * mm, "end": v(63.65, -19.84) * mm});
            skLineSegment(sketch, "E3.24.0.97", {"start": v(60.1, -4.15) * mm, "end": v(63.64, -7.69) * mm});
            skLineSegment(sketch, "E3.24.0.98", {"start": v(60.08, 20.15) * mm, "end": v(63.62, 16.61) * mm});
            skLineSegment(sketch, "E3.24.0.99", {"start": v(64.1, 29.26) * mm, "end": v(60.57, 25.73) * mm});
            skLineSegment(sketch, "E3.24.0.100", {"start": v(64.11, 17.11) * mm, "end": v(60.58, 13.58) * mm});
            skLineSegment(sketch, "E3.24.0.101", {"start": v(63.6, 29.76) * mm, "end": v(60.07, 26.22) * mm});
            skLineSegment(sketch, "E3.24.0.102", {"start": v(63.62, 17.6) * mm, "end": v(60.08, 14.07) * mm});
            skLineSegment(sketch, "E3.24.0.103", {"start": v(60.58, 20.65) * mm, "end": v(60.08, 20.15) * mm});
            skLineSegment(sketch, "E3.24.0.104", {"start": v(64.15, -19.34) * mm, "end": v(63.65, -19.84) * mm});
            skLineSegment(sketch, "E3.24.0.105", {"start": v(64.14, -7.19) * mm, "end": v(63.64, -7.69) * mm});
            skLineSegment(sketch, "E3.24.0.106", {"start": v(64.12, 4.96) * mm, "end": v(63.63, 4.46) * mm});
            skLineSegment(sketch, "E3.24.0.107", {"start": v(64.16, -31.49) * mm, "end": v(63.66, -31.99) * mm});
            skLineSegment(sketch, "E3.24.0.108", {"start": v(64.1, 29.26) * mm, "end": v(63.6, 29.76) * mm});
            skLineSegment(sketch, "E3.24.0.109", {"start": v(64.11, 17.11) * mm, "end": v(63.62, 17.6) * mm});
            skLineSegment(sketch, "E3.24.0.110", {"start": v(60.58, 13.58) * mm, "end": v(60.08, 14.07) * mm});
            skLineSegment(sketch, "E3.24.0.111", {"start": v(60.57, 25.73) * mm, "end": v(60.07, 26.22) * mm});
            skLineSegment(sketch, "E3.24.0.112", {"start": v(60.6, -16.8) * mm, "end": v(60.1, -16.3) * mm});
            skLineSegment(sketch, "E3.24.0.113", {"start": v(60.6, -4.65) * mm, "end": v(60.1, -4.15) * mm});
            skLineSegment(sketch, "E3.24.0.114", {"start": v(60.62, -28.95) * mm, "end": v(60.12, -28.45) * mm});
            skLineSegment(sketch, "E3.24.0.115", {"start": v(64.1, 35.34) * mm, "end": v(63.6, 35.83) * mm});
            skLineSegment(sketch, "E3.24.0.116", {"start": v(60.56, 31.8) * mm, "end": v(60.06, 32.3) * mm});
            skLineSegment(sketch, "E3.24.0.117", {"start": v(60.55, 37.87) * mm, "end": v(60.06, 38.37) * mm});
            skLineSegment(sketch, "E3.24.0.118", {"start": v(60.57, 32.8) * mm, "end": v(60.07, 32.3) * mm});
            skLineSegment(sketch, "E3.24.0.119", {"start": v(64.1, 29.26) * mm, "end": v(63.6, 28.76) * mm});
            skLineSegment(sketch, "E3.24.0.120", {"start": v(64.11, 17.11) * mm, "end": v(63.62, 16.61) * mm});
            skLineSegment(sketch, "E3.direction1", {"start": v(-68.96, -47.17) * mm, "end": v(-63.56, -47.17) * mm, "construction": true});
            skSolve(sketch);
        }
        {
            var Q0;
            {var subQ0=sQuery(id+"F0.wireOp",EDGE,"E3.7.0.2");Q0=makeQuery(id+"F0.imprint","IMPRINT",FACE,{"disambiguationData":[TD([[makeQuery(id+"F0.imprint","IMPRINT",EDGE,{"derivedFrom":subQ0}),1.0]])]});}
            var Q1;
            {var subQ0=sQuery(id+"F0.wireOp",EDGE,"E0.left");Q1=makeQuery(id+"F0.imprint","IMPRINT",FACE,{"disambiguationData":[TD([[makeQuery(id+"F0.imprint","IMPRINT",EDGE,{"derivedFrom":subQ0}),1.0]])]});}
            var Q2;
            {var subQ0=sQuery(id+"F0.wireOp",EDGE,"E3.23.0.2");Q2=makeQuery(id+"F0.imprint","IMPRINT",FACE,{"disambiguationData":[TD([[makeQuery(id+"F0.imprint","IMPRINT",EDGE,{"derivedFrom":subQ0}),1.0]])]});}
            var Q3;
            {var subQ0=sQuery(id+"F0.wireOp",EDGE,"E3.15.0.2");Q3=makeQuery(id+"F0.imprint","IMPRINT",FACE,{"disambiguationData":[TD([[makeQuery(id+"F0.imprint","IMPRINT",EDGE,{"derivedFrom":subQ0}),1.0]])]});}
            var Q4;
            {var subQ0=sQuery(id+"F0.wireOp",EDGE,"E3.24.0.2");Q4=makeQuery(id+"F0.imprint","IMPRINT",FACE,{"disambiguationData":[TD([[makeQuery(id+"F0.imprint","IMPRINT",EDGE,{"derivedFrom":subQ0}),1.0]])]});}
            var Q5;
            {var subQ0=sQuery(id+"F0.wireOp",EDGE,"E3.16.0.2");Q5=makeQuery(id+"F0.imprint","IMPRINT",FACE,{"disambiguationData":[TD([[makeQuery(id+"F0.imprint","IMPRINT",EDGE,{"derivedFrom":subQ0}),1.0]])]});}
            var Q6;
            {var subQ0=sQuery(id+"F0.wireOp",EDGE,"E3.18.0.2");Q6=makeQuery(id+"F0.imprint","IMPRINT",FACE,{"disambiguationData":[TD([[makeQuery(id+"F0.imprint","IMPRINT",EDGE,{"derivedFrom":subQ0}),1.0]])]});}
            var Q7;
            {var subQ3=sQuery(id+"F0.wireOp",EDGE,"E3.12.0.5");Q7=makeQuery(id+"F0.imprint","IMPRINT",FACE,{"disambiguationData":[TD([[makeQuery(id+"F0.imprint","IMPRINT",EDGE,{"derivedFrom":subQ3}),-1.0]])]});}
            var Q8;
            {var subQ3=sQuery(id+"F0.wireOp",EDGE,"E3.7.0.5");Q8=makeQuery(id+"F0.imprint","IMPRINT",FACE,{"disambiguationData":[TD([[makeQuery(id+"F0.imprint","IMPRINT",EDGE,{"derivedFrom":subQ3}),-1.0]])]});}
            var Q9;
            {var subQ3=sQuery(id+"F0.wireOp",EDGE,"E3.6.0.5");Q9=makeQuery(id+"F0.imprint","IMPRINT",FACE,{"disambiguationData":[TD([[makeQuery(id+"F0.imprint","IMPRINT",EDGE,{"derivedFrom":subQ3}),-1.0]])]});}
            var Q10;
            {var subQ5=sQuery(id+"F0.wireOp",EDGE,"E2.14.0.7");Q10=makeQuery(id+"F0.imprint","IMPRINT",FACE,{"disambiguationData":[TD([[makeQuery(id+"F0.imprint","IMPRINT",EDGE,{"derivedFrom":subQ5}),-1.0]])]});}
            var Q11;
            {var subQ0=sQuery(id+"F0.wireOp",EDGE,"E3.1.0.2");Q11=makeQuery(id+"F0.imprint","IMPRINT",FACE,{"disambiguationData":[TD([[makeQuery(id+"F0.imprint","IMPRINT",EDGE,{"derivedFrom":subQ0}),1.0]])]});}
            var Q12;
            {var subQ3=sQuery(id+"F0.wireOp",EDGE,"E3.15.0.5");Q12=makeQuery(id+"F0.imprint","IMPRINT",FACE,{"disambiguationData":[TD([[makeQuery(id+"F0.imprint","IMPRINT",EDGE,{"derivedFrom":subQ3}),-1.0]])]});}
            var Q13;
            {var subQ3=sQuery(id+"F0.wireOp",EDGE,"E3.14.0.5");Q13=makeQuery(id+"F0.imprint","IMPRINT",FACE,{"disambiguationData":[TD([[makeQuery(id+"F0.imprint","IMPRINT",EDGE,{"derivedFrom":subQ3}),-1.0]])]});}
            var Q14;
            {var subQ0=sQuery(id+"F0.wireOp",EDGE,"E3.8.0.2");Q14=makeQuery(id+"F0.imprint","IMPRINT",FACE,{"disambiguationData":[TD([[makeQuery(id+"F0.imprint","IMPRINT",EDGE,{"derivedFrom":subQ0}),1.0]])]});}
            var Q15;
            {var subQ0=sQuery(id+"F0.wireOp",EDGE,"E3.9.0.2");Q15=makeQuery(id+"F0.imprint","IMPRINT",FACE,{"disambiguationData":[TD([[makeQuery(id+"F0.imprint","IMPRINT",EDGE,{"derivedFrom":subQ0}),1.0]])]});}
            var Q16;
            {var subQ0=sQuery(id+"F0.wireOp",EDGE,"E3.17.0.2");Q16=makeQuery(id+"F0.imprint","IMPRINT",FACE,{"disambiguationData":[TD([[makeQuery(id+"F0.imprint","IMPRINT",EDGE,{"derivedFrom":subQ0}),1.0]])]});}
            var Q17;
            {var subQ3=sQuery(id+"F0.wireOp",EDGE,"E1.right");Q17=makeQuery(id+"F0.imprint","IMPRINT",FACE,{"disambiguationData":[TD([[makeQuery(id+"F0.imprint","IMPRINT",EDGE,{"derivedFrom":subQ3}),-1.0]])]});}
            var Q18;
            {var subQ3=sQuery(id+"F0.wireOp",EDGE,"E3.10.0.5");Q18=makeQuery(id+"F0.imprint","IMPRINT",FACE,{"disambiguationData":[TD([[makeQuery(id+"F0.imprint","IMPRINT",EDGE,{"derivedFrom":subQ3}),-1.0]])]});}
            var Q19;
            {var subQ3=sQuery(id+"F0.wireOp",EDGE,"E3.18.0.5");Q19=makeQuery(id+"F0.imprint","IMPRINT",FACE,{"disambiguationData":[TD([[makeQuery(id+"F0.imprint","IMPRINT",EDGE,{"derivedFrom":subQ3}),-1.0]])]});}
            var Q20;
            {var subQ0=sQuery(id+"F0.wireOp",EDGE,"E3.19.0.2");Q20=makeQuery(id+"F0.imprint","IMPRINT",FACE,{"disambiguationData":[TD([[makeQuery(id+"F0.imprint","IMPRINT",EDGE,{"derivedFrom":subQ0}),1.0]])]});}
            var Q21;
            {var subQ3=sQuery(id+"F0.wireOp",EDGE,"E3.11.0.5");Q21=makeQuery(id+"F0.imprint","IMPRINT",FACE,{"disambiguationData":[TD([[makeQuery(id+"F0.imprint","IMPRINT",EDGE,{"derivedFrom":subQ3}),-1.0]])]});}
            var Q22;
            {var subQ3=sQuery(id+"F0.wireOp",EDGE,"E3.13.0.5");Q22=makeQuery(id+"F0.imprint","IMPRINT",FACE,{"disambiguationData":[TD([[makeQuery(id+"F0.imprint","IMPRINT",EDGE,{"derivedFrom":subQ3}),-1.0]])]});}
            var Q23;
            {var subQ10=sQuery(id+"F0.wireOp",EDGE,"E3.19.0.93");Q23=makeQuery(id+"F0.imprint","IMPRINT",FACE,{"disambiguationData":[TD([[makeQuery(id+"F0.imprint","IMPRINT",EDGE,{"derivedFrom":subQ10}),-1.0]])]});}
            var Q24;
            {var subQ10=sQuery(id+"F0.wireOp",EDGE,"E3.18.0.93");Q24=makeQuery(id+"F0.imprint","IMPRINT",FACE,{"disambiguationData":[TD([[makeQuery(id+"F0.imprint","IMPRINT",EDGE,{"derivedFrom":subQ10}),-1.0]])]});}
            var Q25;
            {var subQ0=sQuery(id+"F0.wireOp",EDGE,"E3.24.0.37");var subQ5=sQuery(id+"F0.wireOp",EDGE,"E3.24.0.9");var subQ7=makeQuery(id+"F0.imprint","INTERSECT",VERTEX,{"derivedFrom":[subQ5,subQ0]});Q25=makeQuery(id+"F0.imprint","IMPRINT",FACE,{"disambiguationData":[TD([[makeQuery(id+"F0.imprint","IMPRINT",EDGE,{"disambiguationData":[TD([[subQ7,1.0]])],"derivedFrom":subQ5}),1.0]])]});}
            var Q26;
            {var subQ0=sQuery(id+"F0.wireOp",EDGE,"E3.2.0.2");Q26=makeQuery(id+"F0.imprint","IMPRINT",FACE,{"disambiguationData":[TD([[makeQuery(id+"F0.imprint","IMPRINT",EDGE,{"derivedFrom":subQ0}),1.0]])]});}
            var Q27;
            {var subQ0=sQuery(id+"F0.wireOp",EDGE,"E3.3.0.2");Q27=makeQuery(id+"F0.imprint","IMPRINT",FACE,{"disambiguationData":[TD([[makeQuery(id+"F0.imprint","IMPRINT",EDGE,{"derivedFrom":subQ0}),1.0]])]});}
            var Q28;
            {var subQ3=sQuery(id+"F0.wireOp",EDGE,"E3.3.0.5");Q28=makeQuery(id+"F0.imprint","IMPRINT",FACE,{"disambiguationData":[TD([[makeQuery(id+"F0.imprint","IMPRINT",EDGE,{"derivedFrom":subQ3}),-1.0]])]});}
            var Q29;
            {var subQ0=sQuery(id+"F0.wireOp",EDGE,"E3.4.0.2");Q29=makeQuery(id+"F0.imprint","IMPRINT",FACE,{"disambiguationData":[TD([[makeQuery(id+"F0.imprint","IMPRINT",EDGE,{"derivedFrom":subQ0}),1.0]])]});}
            var Q30;
            {var subQ3=sQuery(id+"F0.wireOp",EDGE,"E3.4.0.5");Q30=makeQuery(id+"F0.imprint","IMPRINT",FACE,{"disambiguationData":[TD([[makeQuery(id+"F0.imprint","IMPRINT",EDGE,{"derivedFrom":subQ3}),-1.0]])]});}
            var Q31;
            {var subQ0=sQuery(id+"F0.wireOp",EDGE,"E3.5.0.2");Q31=makeQuery(id+"F0.imprint","IMPRINT",FACE,{"disambiguationData":[TD([[makeQuery(id+"F0.imprint","IMPRINT",EDGE,{"derivedFrom":subQ0}),1.0]])]});}
            var Q32;
            {var subQ3=sQuery(id+"F0.wireOp",EDGE,"E3.5.0.5");Q32=makeQuery(id+"F0.imprint","IMPRINT",FACE,{"disambiguationData":[TD([[makeQuery(id+"F0.imprint","IMPRINT",EDGE,{"derivedFrom":subQ3}),-1.0]])]});}
            var Q33;
            {var subQ0=sQuery(id+"F0.wireOp",EDGE,"E3.6.0.2");Q33=makeQuery(id+"F0.imprint","IMPRINT",FACE,{"disambiguationData":[TD([[makeQuery(id+"F0.imprint","IMPRINT",EDGE,{"derivedFrom":subQ0}),1.0]])]});}
            var Q34;
            {var subQ3=sQuery(id+"F0.wireOp",EDGE,"E3.23.0.5");Q34=makeQuery(id+"F0.imprint","IMPRINT",FACE,{"disambiguationData":[TD([[makeQuery(id+"F0.imprint","IMPRINT",EDGE,{"derivedFrom":subQ3}),-1.0]])]});}
            var Q35;
            {var subQ3=sQuery(id+"F0.wireOp",EDGE,"E3.22.0.5");Q35=makeQuery(id+"F0.imprint","IMPRINT",FACE,{"disambiguationData":[TD([[makeQuery(id+"F0.imprint","IMPRINT",EDGE,{"derivedFrom":subQ3}),-1.0]])]});}
            var Q36;
            {var subQ3=sQuery(id+"F0.wireOp",EDGE,"E3.8.0.5");Q36=makeQuery(id+"F0.imprint","IMPRINT",FACE,{"disambiguationData":[TD([[makeQuery(id+"F0.imprint","IMPRINT",EDGE,{"derivedFrom":subQ3}),-1.0]])]});}
            var Q37;
            {var subQ3=sQuery(id+"F0.wireOp",EDGE,"E3.24.0.5");Q37=makeQuery(id+"F0.imprint","IMPRINT",FACE,{"disambiguationData":[TD([[makeQuery(id+"F0.imprint","IMPRINT",EDGE,{"derivedFrom":subQ3}),-1.0]])]});}
            var Q38;
            {var subQ3=sQuery(id+"F0.wireOp",EDGE,"E3.16.0.5");Q38=makeQuery(id+"F0.imprint","IMPRINT",FACE,{"disambiguationData":[TD([[makeQuery(id+"F0.imprint","IMPRINT",EDGE,{"derivedFrom":subQ3}),-1.0]])]});}
            var Q39;
            {var subQ3=sQuery(id+"F0.wireOp",EDGE,"E3.9.0.5");Q39=makeQuery(id+"F0.imprint","IMPRINT",FACE,{"disambiguationData":[TD([[makeQuery(id+"F0.imprint","IMPRINT",EDGE,{"derivedFrom":subQ3}),-1.0]])]});}
            var Q40;
            {var subQ0=sQuery(id+"F0.wireOp",EDGE,"E3.10.0.2");Q40=makeQuery(id+"F0.imprint","IMPRINT",FACE,{"disambiguationData":[TD([[makeQuery(id+"F0.imprint","IMPRINT",EDGE,{"derivedFrom":subQ0}),1.0]])]});}
            var Q41;
            {var subQ0=sQuery(id+"F0.wireOp",EDGE,"E2.9.0.0");var subQ1=sQuery(id+"F0.wireOp",EDGE,"E2.8.0.1");var subQ2=makeQuery(id+"F0.imprint","INTERSECT",VERTEX,{"derivedFrom":[subQ1,subQ0]});Q41=makeQuery(id+"F0.imprint","IMPRINT",FACE,{"disambiguationData":[TD([[makeQuery(id+"F0.imprint","IMPRINT",EDGE,{"disambiguationData":[TD([[subQ2,1.0]])],"derivedFrom":subQ1}),1.0]])]});}
            var Q42;
            {var subQ3=sQuery(id+"F0.wireOp",EDGE,"E2.9.0.7");Q42=makeQuery(id+"F0.imprint","IMPRINT",FACE,{"disambiguationData":[TD([[makeQuery(id+"F0.imprint","IMPRINT",EDGE,{"derivedFrom":subQ3}),-1.0]])]});}
            var Q43;
            {var subQ0=sQuery(id+"F0.wireOp",EDGE,"E3.11.0.2");Q43=makeQuery(id+"F0.imprint","IMPRINT",FACE,{"disambiguationData":[TD([[makeQuery(id+"F0.imprint","IMPRINT",EDGE,{"derivedFrom":subQ0}),1.0]])]});}
            var Q44;
            {var subQ3=sQuery(id+"F0.wireOp",EDGE,"E3.19.0.5");Q44=makeQuery(id+"F0.imprint","IMPRINT",FACE,{"disambiguationData":[TD([[makeQuery(id+"F0.imprint","IMPRINT",EDGE,{"derivedFrom":subQ3}),-1.0]])]});}
            var Q45;
            {var subQ0=sQuery(id+"F0.wireOp",EDGE,"E3.20.0.2");Q45=makeQuery(id+"F0.imprint","IMPRINT",FACE,{"disambiguationData":[TD([[makeQuery(id+"F0.imprint","IMPRINT",EDGE,{"derivedFrom":subQ0}),1.0]])]});}
            var Q46;
            {var subQ0=sQuery(id+"F0.wireOp",EDGE,"E3.12.0.2");Q46=makeQuery(id+"F0.imprint","IMPRINT",FACE,{"disambiguationData":[TD([[makeQuery(id+"F0.imprint","IMPRINT",EDGE,{"derivedFrom":subQ0}),1.0]])]});}
            var Q47;
            {var subQ3=sQuery(id+"F0.wireOp",EDGE,"E3.20.0.5");Q47=makeQuery(id+"F0.imprint","IMPRINT",FACE,{"disambiguationData":[TD([[makeQuery(id+"F0.imprint","IMPRINT",EDGE,{"derivedFrom":subQ3}),-1.0]])]});}
            var Q48;
            {var subQ0=sQuery(id+"F0.wireOp",EDGE,"E3.13.0.2");Q48=makeQuery(id+"F0.imprint","IMPRINT",FACE,{"disambiguationData":[TD([[makeQuery(id+"F0.imprint","IMPRINT",EDGE,{"derivedFrom":subQ0}),1.0]])]});}
            var Q49;
            {var subQ10=sQuery(id+"F0.wireOp",EDGE,"E3.17.0.93");Q49=makeQuery(id+"F0.imprint","IMPRINT",FACE,{"disambiguationData":[TD([[makeQuery(id+"F0.imprint","IMPRINT",EDGE,{"derivedFrom":subQ10}),-1.0]])]});}
            var Q50;
            {var subQ3=sQuery(id+"F0.wireOp",EDGE,"E3.21.0.5");Q50=makeQuery(id+"F0.imprint","IMPRINT",FACE,{"disambiguationData":[TD([[makeQuery(id+"F0.imprint","IMPRINT",EDGE,{"derivedFrom":subQ3}),-1.0]])]});}
            var Q51;
            {var subQ10=sQuery(id+"F0.wireOp",EDGE,"E3.1.0.93");Q51=makeQuery(id+"F0.imprint","IMPRINT",FACE,{"disambiguationData":[TD([[makeQuery(id+"F0.imprint","IMPRINT",EDGE,{"derivedFrom":subQ10}),-1.0]])]});}
            var Q52;
            {var subQ0=sQuery(id+"F0.wireOp",EDGE,"E3.14.0.2");Q52=makeQuery(id+"F0.imprint","IMPRINT",FACE,{"disambiguationData":[TD([[makeQuery(id+"F0.imprint","IMPRINT",EDGE,{"derivedFrom":subQ0}),1.0]])]});}
            var Q53;
            {var subQ0=sQuery(id+"F0.wireOp",EDGE,"E3.24.0.96");var subQ1=sQuery(id+"F0.wireOp",EDGE,"E3.24.0.43");var subQ2=makeQuery(id+"F0.imprint","INTERSECT",VERTEX,{"derivedFrom":[subQ1,subQ0]});Q53=makeQuery(id+"F0.imprint","IMPRINT",FACE,{"disambiguationData":[TD([[makeQuery(id+"F0.imprint","IMPRINT",EDGE,{"disambiguationData":[TD([[subQ2,1.0]])],"derivedFrom":subQ1}),-1.0]])]});}
            var Q54;
            {var subQ0=sQuery(id+"F0.wireOp",EDGE,"E3.19.0.40");var subQ1=sQuery(id+"F0.wireOp",EDGE,"E3.19.0.18");var subQ2=makeQuery(id+"F0.imprint","INTERSECT",VERTEX,{"derivedFrom":[subQ1,subQ0]});Q54=makeQuery(id+"F0.imprint","IMPRINT",FACE,{"disambiguationData":[TD([[makeQuery(id+"F0.imprint","IMPRINT",EDGE,{"disambiguationData":[TD([[subQ2,-1.0]])],"derivedFrom":subQ1}),-1.0]])]});}
            var Q55;
            {var subQ0=sQuery(id+"F0.wireOp",EDGE,"E3.24.0.42");var subQ1=sQuery(id+"F0.wireOp",EDGE,"E3.24.0.16");var subQ2=makeQuery(id+"F0.imprint","INTERSECT",VERTEX,{"derivedFrom":[subQ1,subQ0]});Q55=makeQuery(id+"F0.imprint","IMPRINT",FACE,{"disambiguationData":[TD([[makeQuery(id+"F0.imprint","IMPRINT",EDGE,{"disambiguationData":[TD([[subQ2,-1.0]])],"derivedFrom":subQ1}),-1.0]])]});}
            var Q56;
            {var subQ3=sQuery(id+"F0.wireOp",EDGE,"E3.24.0.7");Q56=makeQuery(id+"F0.imprint","IMPRINT",FACE,{"disambiguationData":[TD([[makeQuery(id+"F0.imprint","IMPRINT",EDGE,{"derivedFrom":subQ3}),1.0]])]});}
            var Q57;
            {var subQ0=sQuery(id+"F0.wireOp",EDGE,"E3.24.0.32");var subQ1=sQuery(id+"F0.wireOp",EDGE,"E3.24.0.0");var subQ2=makeQuery(id+"F0.imprint","INTERSECT",VERTEX,{"derivedFrom":[subQ1,subQ0]});Q57=makeQuery(id+"F0.imprint","IMPRINT",FACE,{"disambiguationData":[TD([[makeQuery(id+"F0.imprint","IMPRINT",EDGE,{"disambiguationData":[TD([[subQ2,1.0]])],"derivedFrom":subQ1}),-1.0]])]});}
            var Q58;
            {var subQ3=sQuery(id+"F0.wireOp",EDGE,"E3.23.0.7");Q58=makeQuery(id+"F0.imprint","IMPRINT",FACE,{"disambiguationData":[TD([[makeQuery(id+"F0.imprint","IMPRINT",EDGE,{"derivedFrom":subQ3}),1.0]])]});}
            var Q59;
            {var subQ0=sQuery(id+"F0.wireOp",EDGE,"E3.24.0.51");var subQ1=sQuery(id+"F0.wireOp",EDGE,"E3.24.0.10");var subQ2=makeQuery(id+"F0.imprint","INTERSECT",VERTEX,{"derivedFrom":[subQ1,subQ0]});Q59=makeQuery(id+"F0.imprint","IMPRINT",FACE,{"disambiguationData":[TD([[makeQuery(id+"F0.imprint","IMPRINT",EDGE,{"disambiguationData":[TD([[subQ2,-1.0]])],"derivedFrom":subQ1}),1.0]])]});}
            var Q60;
            {var subQ0=sQuery(id+"F0.wireOp",EDGE,"E3.24.0.63");Q60=makeQuery(id+"F0.imprint","IMPRINT",FACE,{"disambiguationData":[TD([[makeQuery(id+"F0.imprint","IMPRINT",EDGE,{"derivedFrom":subQ0}),-1.0]])]});}
            var Q61;
            {var subQ0=sQuery(id+"F0.wireOp",EDGE,"E3.18.0.32");var subQ1=sQuery(id+"F0.wireOp",EDGE,"E3.18.0.0");var subQ2=makeQuery(id+"F0.imprint","INTERSECT",VERTEX,{"derivedFrom":[subQ1,subQ0]});Q61=makeQuery(id+"F0.imprint","IMPRINT",FACE,{"disambiguationData":[TD([[makeQuery(id+"F0.imprint","IMPRINT",EDGE,{"disambiguationData":[TD([[subQ2,1.0]])],"derivedFrom":subQ1}),-1.0]])]});}
            var Q62;
            {var subQ0=sQuery(id+"F0.wireOp",EDGE,"E3.19.0.32");var subQ1=sQuery(id+"F0.wireOp",EDGE,"E3.19.0.0");var subQ2=makeQuery(id+"F0.imprint","INTERSECT",VERTEX,{"derivedFrom":[subQ1,subQ0]});Q62=makeQuery(id+"F0.imprint","IMPRINT",FACE,{"disambiguationData":[TD([[makeQuery(id+"F0.imprint","IMPRINT",EDGE,{"disambiguationData":[TD([[subQ2,1.0]])],"derivedFrom":subQ1}),-1.0]])]});}
            var Q63;
            {var subQ3=sQuery(id+"F0.wireOp",EDGE,"E3.24.0.65");Q63=makeQuery(id+"F0.imprint","IMPRINT",FACE,{"disambiguationData":[TD([[makeQuery(id+"F0.imprint","IMPRINT",EDGE,{"derivedFrom":subQ3}),-1.0]])]});}
            var Q64;
            {var subQ3=sQuery(id+"F0.wireOp",EDGE,"E3.2.0.5");Q64=makeQuery(id+"F0.imprint","IMPRINT",FACE,{"disambiguationData":[TD([[makeQuery(id+"F0.imprint","IMPRINT",EDGE,{"derivedFrom":subQ3}),-1.0]])]});}
            var Q65;
            {var subQ3=sQuery(id+"F0.wireOp",EDGE,"E3.10.0.7");Q65=makeQuery(id+"F0.imprint","IMPRINT",FACE,{"disambiguationData":[TD([[makeQuery(id+"F0.imprint","IMPRINT",EDGE,{"derivedFrom":subQ3}),1.0]])]});}
            var Q66;
            {var subQ0=sQuery(id+"F0.wireOp",EDGE,"E2.7.0.0");var subQ1=sQuery(id+"F0.wireOp",EDGE,"E2.6.0.1");var subQ2=makeQuery(id+"F0.imprint","INTERSECT",VERTEX,{"derivedFrom":[subQ1,subQ0]});Q66=makeQuery(id+"F0.imprint","IMPRINT",FACE,{"disambiguationData":[TD([[makeQuery(id+"F0.imprint","IMPRINT",EDGE,{"disambiguationData":[TD([[subQ2,1.0]])],"derivedFrom":subQ1}),1.0]])]});}
            var Q67;
            {var subQ3=sQuery(id+"F0.wireOp",EDGE,"E2.11.0.7");Q67=makeQuery(id+"F0.imprint","IMPRINT",FACE,{"disambiguationData":[TD([[makeQuery(id+"F0.imprint","IMPRINT",EDGE,{"derivedFrom":subQ3}),-1.0]])]});}
            var Q68;
            {var subQ10=sQuery(id+"F0.wireOp",EDGE,"E3.16.0.93");Q68=makeQuery(id+"F0.imprint","IMPRINT",FACE,{"disambiguationData":[TD([[makeQuery(id+"F0.imprint","IMPRINT",EDGE,{"derivedFrom":subQ10}),-1.0]])]});}
            var Q69;
            {var subQ0=sQuery(id+"F0.wireOp",EDGE,"E0.right");Q69=makeQuery(id+"F0.imprint","IMPRINT",FACE,{"disambiguationData":[TD([[makeQuery(id+"F0.imprint","IMPRINT",EDGE,{"derivedFrom":subQ0}),-1.0]])]});}
            var Q70;
            {var subQ0=sQuery(id+"F0.wireOp",EDGE,"E3.6.0.51");var subQ1=sQuery(id+"F0.wireOp",EDGE,"E3.6.0.10");var subQ2=makeQuery(id+"F0.imprint","INTERSECT",VERTEX,{"derivedFrom":[subQ1,subQ0]});Q70=makeQuery(id+"F0.imprint","IMPRINT",FACE,{"disambiguationData":[TD([[makeQuery(id+"F0.imprint","IMPRINT",EDGE,{"disambiguationData":[TD([[subQ2,-1.0]])],"derivedFrom":subQ1}),1.0]])]});}
            var Q71;
            {var subQ3=sQuery(id+"F0.wireOp",EDGE,"E3.17.0.5");Q71=makeQuery(id+"F0.imprint","IMPRINT",FACE,{"disambiguationData":[TD([[makeQuery(id+"F0.imprint","IMPRINT",EDGE,{"derivedFrom":subQ3}),-1.0]])]});}
            var Q72;
            {var subQ3=sQuery(id+"F0.wireOp",EDGE,"E3.14.0.7");Q72=makeQuery(id+"F0.imprint","IMPRINT",FACE,{"disambiguationData":[TD([[makeQuery(id+"F0.imprint","IMPRINT",EDGE,{"derivedFrom":subQ3}),1.0]])]});}
            var Q73;
            {var subQ10=sQuery(id+"F0.wireOp",EDGE,"E3.2.0.93");Q73=makeQuery(id+"F0.imprint","IMPRINT",FACE,{"disambiguationData":[TD([[makeQuery(id+"F0.imprint","IMPRINT",EDGE,{"derivedFrom":subQ10}),-1.0]])]});}
            var Q74;
            {var subQ0=sQuery(id+"F0.wireOp",EDGE,"E3.8.0.42");var subQ1=sQuery(id+"F0.wireOp",EDGE,"E3.8.0.16");var subQ2=makeQuery(id+"F0.imprint","INTERSECT",VERTEX,{"derivedFrom":[subQ1,subQ0]});Q74=makeQuery(id+"F0.imprint","IMPRINT",FACE,{"disambiguationData":[TD([[makeQuery(id+"F0.imprint","IMPRINT",EDGE,{"disambiguationData":[TD([[subQ2,-1.0]])],"derivedFrom":subQ1}),-1.0]])]});}
            var Q75;
            {var subQ0=sQuery(id+"F0.wireOp",EDGE,"E3.9.0.37");var subQ5=sQuery(id+"F0.wireOp",EDGE,"E3.9.0.9");var subQ7=makeQuery(id+"F0.imprint","INTERSECT",VERTEX,{"derivedFrom":[subQ5,subQ0]});Q75=makeQuery(id+"F0.imprint","IMPRINT",FACE,{"disambiguationData":[TD([[makeQuery(id+"F0.imprint","IMPRINT",EDGE,{"disambiguationData":[TD([[subQ7,1.0]])],"derivedFrom":subQ5}),1.0]])]});}
            var Q76;
            {var subQ3=sQuery(id+"F0.wireOp",EDGE,"E2.13.0.7");Q76=makeQuery(id+"F0.imprint","IMPRINT",FACE,{"disambiguationData":[TD([[makeQuery(id+"F0.imprint","IMPRINT",EDGE,{"derivedFrom":subQ3}),-1.0]])]});}
            var Q77;
            {var subQ3=sQuery(id+"F0.wireOp",EDGE,"E2.5.0.7");Q77=makeQuery(id+"F0.imprint","IMPRINT",FACE,{"disambiguationData":[TD([[makeQuery(id+"F0.imprint","IMPRINT",EDGE,{"derivedFrom":subQ3}),-1.0]])]});}
            var Q78;
            {var subQ0=sQuery(id+"F0.wireOp",EDGE,"E3.6.0.69");var subQ1=sQuery(id+"F0.wireOp",EDGE,"E3.6.0.12");var subQ2=makeQuery(id+"F0.imprint","INTERSECT",VERTEX,{"derivedFrom":[subQ1,subQ0]});Q78=makeQuery(id+"F0.imprint","IMPRINT",FACE,{"disambiguationData":[TD([[makeQuery(id+"F0.imprint","IMPRINT",EDGE,{"disambiguationData":[TD([[subQ2,1.0]])],"derivedFrom":subQ1}),-1.0]])]});}
            var Q79;
            {var subQ3=sQuery(id+"F0.wireOp",EDGE,"E2.1.0.7");Q79=makeQuery(id+"F0.imprint","IMPRINT",FACE,{"disambiguationData":[TD([[makeQuery(id+"F0.imprint","IMPRINT",EDGE,{"derivedFrom":subQ3}),-1.0]])]});}
            var Q80;
            {var subQ0=sQuery(id+"F0.wireOp",EDGE,"E3.3.0.51");var subQ1=sQuery(id+"F0.wireOp",EDGE,"E3.3.0.10");var subQ2=makeQuery(id+"F0.imprint","INTERSECT",VERTEX,{"derivedFrom":[subQ1,subQ0]});Q80=makeQuery(id+"F0.imprint","IMPRINT",FACE,{"disambiguationData":[TD([[makeQuery(id+"F0.imprint","IMPRINT",EDGE,{"disambiguationData":[TD([[subQ2,-1.0]])],"derivedFrom":subQ1}),1.0]])]});}
            var Q81;
            {var subQ0=sQuery(id+"F0.wireOp",EDGE,"E2.9.0.1");var subQ1=sQuery(id+"F0.wireOp",EDGE,"E2.9.0.0");var subQ2=makeQuery(id+"F0.imprint","INTERSECT",VERTEX,{"derivedFrom":[subQ1,subQ0]});Q81=makeQuery(id+"F0.imprint","IMPRINT",FACE,{"disambiguationData":[TD([[makeQuery(id+"F0.imprint","IMPRINT",EDGE,{"disambiguationData":[TD([[subQ2,1.0]])],"derivedFrom":subQ1}),1.0]])]});}
            var Q82;
            {var subQ0=sQuery(id+"F0.wireOp",EDGE,"E3.11.0.37");var subQ5=sQuery(id+"F0.wireOp",EDGE,"E3.11.0.9");var subQ7=makeQuery(id+"F0.imprint","INTERSECT",VERTEX,{"derivedFrom":[subQ5,subQ0]});Q82=makeQuery(id+"F0.imprint","IMPRINT",FACE,{"disambiguationData":[TD([[makeQuery(id+"F0.imprint","IMPRINT",EDGE,{"disambiguationData":[TD([[subQ7,1.0]])],"derivedFrom":subQ5}),1.0]])]});}
            var Q83;
            {var subQ5=sQuery(id+"F0.wireOp",EDGE,"E2.10.0.4");Q83=makeQuery(id+"F0.imprint","IMPRINT",FACE,{"disambiguationData":[TD([[makeQuery(id+"F0.imprint","IMPRINT",EDGE,{"derivedFrom":subQ5}),1.0]])]});}
            var Q84;
            {var subQ0=sQuery(id+"F0.wireOp",EDGE,"E3.7.0.64");Q84=makeQuery(id+"F0.imprint","IMPRINT",FACE,{"disambiguationData":[TD([[makeQuery(id+"F0.imprint","IMPRINT",EDGE,{"derivedFrom":subQ0}),-1.0]])]});}
            var Q85;
            {var subQ0=sQuery(id+"F0.wireOp",EDGE,"E2.6.0.0");var subQ1=sQuery(id+"F0.wireOp",EDGE,"E2.5.0.1");var subQ2=makeQuery(id+"F0.imprint","INTERSECT",VERTEX,{"derivedFrom":[subQ1,subQ0]});Q85=makeQuery(id+"F0.imprint","IMPRINT",FACE,{"disambiguationData":[TD([[makeQuery(id+"F0.imprint","IMPRINT",EDGE,{"disambiguationData":[TD([[subQ2,1.0]])],"derivedFrom":subQ1}),1.0]])]});}
            var Q86;
            {var subQ0=sQuery(id+"F0.wireOp",EDGE,"E3.13.0.37");var subQ5=sQuery(id+"F0.wireOp",EDGE,"E3.13.0.9");var subQ7=makeQuery(id+"F0.imprint","INTERSECT",VERTEX,{"derivedFrom":[subQ5,subQ0]});Q86=makeQuery(id+"F0.imprint","IMPRINT",FACE,{"disambiguationData":[TD([[makeQuery(id+"F0.imprint","IMPRINT",EDGE,{"disambiguationData":[TD([[subQ7,1.0]])],"derivedFrom":subQ5}),1.0]])]});}
            var Q87;
            {var subQ3=sQuery(id+"F0.wireOp",EDGE,"E2.2.0.7");Q87=makeQuery(id+"F0.imprint","IMPRINT",FACE,{"disambiguationData":[TD([[makeQuery(id+"F0.imprint","IMPRINT",EDGE,{"derivedFrom":subQ3}),-1.0]])]});}
            var Q88;
            {var subQ0=sQuery(id+"F0.wireOp",EDGE,"E3.21.0.2");Q88=makeQuery(id+"F0.imprint","IMPRINT",FACE,{"disambiguationData":[TD([[makeQuery(id+"F0.imprint","IMPRINT",EDGE,{"derivedFrom":subQ0}),1.0]])]});}
            var Q89;
            {var subQ3=sQuery(id+"F0.wireOp",EDGE,"E2.10.0.7");Q89=makeQuery(id+"F0.imprint","IMPRINT",FACE,{"disambiguationData":[TD([[makeQuery(id+"F0.imprint","IMPRINT",EDGE,{"derivedFrom":subQ3}),-1.0]])]});}
            var Q90;
            {var subQ3=sQuery(id+"F0.wireOp",EDGE,"E2.6.0.7");Q90=makeQuery(id+"F0.imprint","IMPRINT",FACE,{"disambiguationData":[TD([[makeQuery(id+"F0.imprint","IMPRINT",EDGE,{"derivedFrom":subQ3}),-1.0]])]});}
            var Q91;
            {var subQ0=sQuery(id+"F0.wireOp",EDGE,"E3.2.0.116");Q91=makeQuery(id+"F0.imprint","IMPRINT",FACE,{"disambiguationData":[TD([[makeQuery(id+"F0.imprint","IMPRINT",EDGE,{"derivedFrom":subQ0}),-1.0]])]});}
            var Q92;
            {var subQ0=sQuery(id+"F0.wireOp",EDGE,"E3.17.0.32");var subQ1=sQuery(id+"F0.wireOp",EDGE,"E3.17.0.0");var subQ2=makeQuery(id+"F0.imprint","INTERSECT",VERTEX,{"derivedFrom":[subQ1,subQ0]});Q92=makeQuery(id+"F0.imprint","IMPRINT",FACE,{"disambiguationData":[TD([[makeQuery(id+"F0.imprint","IMPRINT",EDGE,{"disambiguationData":[TD([[subQ2,1.0]])],"derivedFrom":subQ1}),-1.0]])]});}
            var Q93;
            {var subQ0=sQuery(id+"F0.wireOp",EDGE,"E3.8.0.37");var subQ5=sQuery(id+"F0.wireOp",EDGE,"E3.8.0.9");var subQ7=makeQuery(id+"F0.imprint","INTERSECT",VERTEX,{"derivedFrom":[subQ5,subQ0]});Q93=makeQuery(id+"F0.imprint","IMPRINT",FACE,{"disambiguationData":[TD([[makeQuery(id+"F0.imprint","IMPRINT",EDGE,{"disambiguationData":[TD([[subQ7,1.0]])],"derivedFrom":subQ5}),1.0]])]});}
            var Q94;
            {var subQ3=sQuery(id+"F0.wireOp",EDGE,"E3.11.0.56");Q94=makeQuery(id+"F0.imprint","IMPRINT",FACE,{"disambiguationData":[TD([[makeQuery(id+"F0.imprint","IMPRINT",EDGE,{"derivedFrom":subQ3}),-1.0]])]});}
            var Q95;
            {var subQ0=sQuery(id+"F0.wireOp",EDGE,"E3.1.0.32");var subQ1=sQuery(id+"F0.wireOp",EDGE,"E3.1.0.0");var subQ2=makeQuery(id+"F0.imprint","INTERSECT",VERTEX,{"derivedFrom":[subQ1,subQ0]});Q95=makeQuery(id+"F0.imprint","IMPRINT",FACE,{"disambiguationData":[TD([[makeQuery(id+"F0.imprint","IMPRINT",EDGE,{"disambiguationData":[TD([[subQ2,1.0]])],"derivedFrom":subQ1}),-1.0]])]});}
            var Q96;
            {var subQ3=sQuery(id+"F0.wireOp",EDGE,"E3.24.0.56");Q96=makeQuery(id+"F0.imprint","IMPRINT",FACE,{"disambiguationData":[TD([[makeQuery(id+"F0.imprint","IMPRINT",EDGE,{"derivedFrom":subQ3}),-1.0]])]});}
            var Q97;
            {var subQ0=sQuery(id+"F0.wireOp",EDGE,"E3.24.0.64");Q97=makeQuery(id+"F0.imprint","IMPRINT",FACE,{"disambiguationData":[TD([[makeQuery(id+"F0.imprint","IMPRINT",EDGE,{"derivedFrom":subQ0}),-1.0]])]});}
            var Q98;
            {var subQ0=sQuery(id+"F0.wireOp",EDGE,"E3.24.0.57");Q98=makeQuery(id+"F0.imprint","IMPRINT",FACE,{"disambiguationData":[TD([[makeQuery(id+"F0.imprint","IMPRINT",EDGE,{"derivedFrom":subQ0}),-1.0]])]});}
            var Q99;
            {var subQ7=sQuery(id+"F0.wireOp",EDGE,"E3.24.0.87");Q99=makeQuery(id+"F0.imprint","IMPRINT",FACE,{"disambiguationData":[TD([[makeQuery(id+"F0.imprint","IMPRINT",EDGE,{"derivedFrom":subQ7}),-1.0]])]});}
            var Q100;
            {var subQ0=sQuery(id+"F0.wireOp",EDGE,"E3.23.0.37");var subQ5=sQuery(id+"F0.wireOp",EDGE,"E3.23.0.9");var subQ7=makeQuery(id+"F0.imprint","INTERSECT",VERTEX,{"derivedFrom":[subQ5,subQ0]});Q100=makeQuery(id+"F0.imprint","IMPRINT",FACE,{"disambiguationData":[TD([[makeQuery(id+"F0.imprint","IMPRINT",EDGE,{"disambiguationData":[TD([[subQ7,1.0]])],"derivedFrom":subQ5}),1.0]])]});}
            var Q101;
            {var subQ0=sQuery(id+"F0.wireOp",EDGE,"E3.21.0.69");var subQ1=sQuery(id+"F0.wireOp",EDGE,"E3.21.0.12");var subQ2=makeQuery(id+"F0.imprint","INTERSECT",VERTEX,{"derivedFrom":[subQ1,subQ0]});Q101=makeQuery(id+"F0.imprint","IMPRINT",FACE,{"disambiguationData":[TD([[makeQuery(id+"F0.imprint","IMPRINT",EDGE,{"disambiguationData":[TD([[subQ2,1.0]])],"derivedFrom":subQ1}),-1.0]])]});}
            var Q102;
            {var subQ0=sQuery(id+"F0.wireOp",EDGE,"E3.20.0.116");Q102=makeQuery(id+"F0.imprint","IMPRINT",FACE,{"disambiguationData":[TD([[makeQuery(id+"F0.imprint","IMPRINT",EDGE,{"derivedFrom":subQ0}),-1.0]])]});}
            var Q103;
            {var subQ0=sQuery(id+"F0.wireOp",EDGE,"E3.19.0.94");var subQ1=sQuery(id+"F0.wireOp",EDGE,"E3.19.0.42");var subQ2=makeQuery(id+"F0.imprint","INTERSECT",VERTEX,{"derivedFrom":[subQ1,subQ0]});Q103=makeQuery(id+"F0.imprint","IMPRINT",FACE,{"disambiguationData":[TD([[makeQuery(id+"F0.imprint","IMPRINT",EDGE,{"disambiguationData":[TD([[subQ2,1.0]])],"derivedFrom":subQ1}),-1.0]])]});}
            var Q104;
            {var subQ5=sQuery(id+"F0.wireOp",EDGE,"E3.20.0.93");Q104=makeQuery(id+"F0.imprint","IMPRINT",FACE,{"disambiguationData":[TD([[makeQuery(id+"F0.imprint","IMPRINT",EDGE,{"derivedFrom":subQ5}),1.0]])]});}
            var Q105;
            {var subQ0=sQuery(id+"F0.wireOp",EDGE,"E3.18.0.40");var subQ1=sQuery(id+"F0.wireOp",EDGE,"E3.18.0.18");var subQ2=makeQuery(id+"F0.imprint","INTERSECT",VERTEX,{"derivedFrom":[subQ1,subQ0]});Q105=makeQuery(id+"F0.imprint","IMPRINT",FACE,{"disambiguationData":[TD([[makeQuery(id+"F0.imprint","IMPRINT",EDGE,{"disambiguationData":[TD([[subQ2,-1.0]])],"derivedFrom":subQ1}),-1.0]])]});}
            var Q106;
            {var subQ3=sQuery(id+"F0.wireOp",EDGE,"E3.19.0.66");Q106=makeQuery(id+"F0.imprint","IMPRINT",FACE,{"disambiguationData":[TD([[makeQuery(id+"F0.imprint","IMPRINT",EDGE,{"derivedFrom":subQ3}),-1.0]])]});}
            var Q107;
            {var subQ0=sQuery(id+"F0.wireOp",EDGE,"E3.17.0.40");var subQ1=sQuery(id+"F0.wireOp",EDGE,"E3.17.0.18");var subQ2=makeQuery(id+"F0.imprint","INTERSECT",VERTEX,{"derivedFrom":[subQ1,subQ0]});Q107=makeQuery(id+"F0.imprint","IMPRINT",FACE,{"disambiguationData":[TD([[makeQuery(id+"F0.imprint","IMPRINT",EDGE,{"disambiguationData":[TD([[subQ2,-1.0]])],"derivedFrom":subQ1}),-1.0]])]});}
            var Q108;
            {var subQ0=sQuery(id+"F0.wireOp",EDGE,"E3.20.0.69");var subQ1=sQuery(id+"F0.wireOp",EDGE,"E3.20.0.12");var subQ2=makeQuery(id+"F0.imprint","INTERSECT",VERTEX,{"derivedFrom":[subQ1,subQ0]});Q108=makeQuery(id+"F0.imprint","IMPRINT",FACE,{"disambiguationData":[TD([[makeQuery(id+"F0.imprint","IMPRINT",EDGE,{"disambiguationData":[TD([[subQ2,1.0]])],"derivedFrom":subQ1}),-1.0]])]});}
            var Q109;
            {var subQ3=sQuery(id+"F0.wireOp",EDGE,"E3.21.0.103");Q109=makeQuery(id+"F0.imprint","IMPRINT",FACE,{"disambiguationData":[TD([[makeQuery(id+"F0.imprint","IMPRINT",EDGE,{"derivedFrom":subQ3}),1.0]])]});}
            var Q110;
            {var subQ0=sQuery(id+"F0.wireOp",EDGE,"E3.23.0.51");var subQ1=sQuery(id+"F0.wireOp",EDGE,"E3.23.0.10");var subQ2=makeQuery(id+"F0.imprint","INTERSECT",VERTEX,{"derivedFrom":[subQ1,subQ0]});Q110=makeQuery(id+"F0.imprint","IMPRINT",FACE,{"disambiguationData":[TD([[makeQuery(id+"F0.imprint","IMPRINT",EDGE,{"disambiguationData":[TD([[subQ2,-1.0]])],"derivedFrom":subQ1}),1.0]])]});}
            var Q111;
            {var subQ0=sQuery(id+"F0.wireOp",EDGE,"E3.24.0.71");var subQ1=sQuery(id+"F0.wireOp",EDGE,"E3.24.0.9");var subQ2=makeQuery(id+"F0.imprint","INTERSECT",VERTEX,{"derivedFrom":[subQ1,subQ0]});Q111=makeQuery(id+"F0.imprint","IMPRINT",FACE,{"disambiguationData":[TD([[makeQuery(id+"F0.imprint","IMPRINT",EDGE,{"disambiguationData":[TD([[subQ2,1.0]])],"derivedFrom":subQ1}),-1.0]])]});}
            var Q112;
            {var subQ0=sQuery(id+"F0.wireOp",EDGE,"E3.20.0.64");Q112=makeQuery(id+"F0.imprint","IMPRINT",FACE,{"disambiguationData":[TD([[makeQuery(id+"F0.imprint","IMPRINT",EDGE,{"derivedFrom":subQ0}),-1.0]])]});}
            var Q113;
            {var subQ5=sQuery(id+"F0.wireOp",EDGE,"E3.21.0.22");Q113=makeQuery(id+"F0.imprint","IMPRINT",FACE,{"disambiguationData":[TD([[makeQuery(id+"F0.imprint","IMPRINT",EDGE,{"derivedFrom":subQ5}),-1.0]])]});}
            var Q114;
            {var subQ0=sQuery(id+"F0.wireOp",EDGE,"E3.22.0.35");var subQ1=sQuery(id+"F0.wireOp",EDGE,"E3.22.0.32");var subQ2=makeQuery(id+"F0.imprint","INTERSECT",VERTEX,{"derivedFrom":[subQ1,subQ0]});Q114=makeQuery(id+"F0.imprint","IMPRINT",FACE,{"disambiguationData":[TD([[makeQuery(id+"F0.imprint","IMPRINT",EDGE,{"disambiguationData":[TD([[subQ2,1.0]])],"derivedFrom":subQ1}),1.0]])]});}
            var Q115;
            {var subQ0=sQuery(id+"F0.wireOp",EDGE,"E3.22.0.75");var subQ1=sQuery(id+"F0.wireOp",EDGE,"E3.22.0.52");var subQ2=makeQuery(id+"F0.imprint","INTERSECT",VERTEX,{"derivedFrom":[subQ1,subQ0]});Q115=makeQuery(id+"F0.imprint","IMPRINT",FACE,{"disambiguationData":[TD([[makeQuery(id+"F0.imprint","IMPRINT",EDGE,{"disambiguationData":[TD([[subQ2,-1.0]])],"derivedFrom":subQ1}),-1.0]])]});}
            var Q116;
            {var subQ5=sQuery(id+"F0.wireOp",EDGE,"E3.24.0.82");Q116=makeQuery(id+"F0.imprint","IMPRINT",FACE,{"disambiguationData":[TD([[makeQuery(id+"F0.imprint","IMPRINT",EDGE,{"derivedFrom":subQ5}),-1.0]])]});}
            var Q117;
            {var subQ0=sQuery(id+"F0.wireOp",EDGE,"E3.24.0.91");var subQ1=sQuery(id+"F0.wireOp",EDGE,"E3.24.0.49");var subQ2=makeQuery(id+"F0.imprint","INTERSECT",VERTEX,{"derivedFrom":[subQ1,subQ0]});Q117=makeQuery(id+"F0.imprint","IMPRINT",FACE,{"disambiguationData":[TD([[makeQuery(id+"F0.imprint","IMPRINT",EDGE,{"disambiguationData":[TD([[subQ2,-1.0]])],"derivedFrom":subQ1}),-1.0]])]});}
            var Q118;
            {var subQ0=sQuery(id+"F0.wireOp",EDGE,"E3.21.0.75");var subQ1=sQuery(id+"F0.wireOp",EDGE,"E3.21.0.52");var subQ2=makeQuery(id+"F0.imprint","INTERSECT",VERTEX,{"derivedFrom":[subQ1,subQ0]});Q118=makeQuery(id+"F0.imprint","IMPRINT",FACE,{"disambiguationData":[TD([[makeQuery(id+"F0.imprint","IMPRINT",EDGE,{"disambiguationData":[TD([[subQ2,-1.0]])],"derivedFrom":subQ1}),-1.0]])]});}
            var Q119;
            {var subQ5=sQuery(id+"F0.wireOp",EDGE,"E3.24.0.57");Q119=makeQuery(id+"F0.imprint","IMPRINT",FACE,{"disambiguationData":[TD([[makeQuery(id+"F0.imprint","IMPRINT",EDGE,{"derivedFrom":subQ5}),1.0]])]});}
            var Q120;
            {var subQ5=sQuery(id+"F0.wireOp",EDGE,"E3.23.0.82");Q120=makeQuery(id+"F0.imprint","IMPRINT",FACE,{"disambiguationData":[TD([[makeQuery(id+"F0.imprint","IMPRINT",EDGE,{"derivedFrom":subQ5}),-1.0]])]});}
            var Q121;
            {var subQ0=sQuery(id+"F0.wireOp",EDGE,"E3.24.0.72");var subQ1=sQuery(id+"F0.wireOp",EDGE,"E3.24.0.10");var subQ2=makeQuery(id+"F0.imprint","INTERSECT",VERTEX,{"derivedFrom":[subQ1,subQ0]});Q121=makeQuery(id+"F0.imprint","IMPRINT",FACE,{"disambiguationData":[TD([[makeQuery(id+"F0.imprint","IMPRINT",EDGE,{"disambiguationData":[TD([[subQ2,1.0]])],"derivedFrom":subQ1}),-1.0]])]});}
            var Q122;
            {var subQ0=sQuery(id+"F0.wireOp",EDGE,"E3.24.0.96");var subQ1=sQuery(id+"F0.wireOp",EDGE,"E3.24.0.39");var subQ2=makeQuery(id+"F0.imprint","INTERSECT",VERTEX,{"derivedFrom":[subQ1,subQ0]});Q122=makeQuery(id+"F0.imprint","IMPRINT",FACE,{"disambiguationData":[TD([[makeQuery(id+"F0.imprint","IMPRINT",EDGE,{"disambiguationData":[TD([[subQ2,1.0]])],"derivedFrom":subQ1}),-1.0]])]});}
            var Q123;
            {var subQ3=sQuery(id+"F0.wireOp",EDGE,"E3.1.0.5");Q123=makeQuery(id+"F0.imprint","IMPRINT",FACE,{"disambiguationData":[TD([[makeQuery(id+"F0.imprint","IMPRINT",EDGE,{"derivedFrom":subQ3}),-1.0]])]});}
            var Q124;
            {var subQ0=sQuery(id+"F0.wireOp",EDGE,"E3.4.0.57");Q124=makeQuery(id+"F0.imprint","IMPRINT",FACE,{"disambiguationData":[TD([[makeQuery(id+"F0.imprint","IMPRINT",EDGE,{"derivedFrom":subQ0}),-1.0]])]});}
            var Q125;
            {var subQ7=sQuery(id+"F0.wireOp",EDGE,"E3.5.0.87");Q125=makeQuery(id+"F0.imprint","IMPRINT",FACE,{"disambiguationData":[TD([[makeQuery(id+"F0.imprint","IMPRINT",EDGE,{"derivedFrom":subQ7}),-1.0]])]});}
            var Q126;
            {var subQ10=sQuery(id+"F0.wireOp",EDGE,"E3.5.0.93");Q126=makeQuery(id+"F0.imprint","IMPRINT",FACE,{"disambiguationData":[TD([[makeQuery(id+"F0.imprint","IMPRINT",EDGE,{"derivedFrom":subQ10}),-1.0]])]});}
            var Q127;
            {var subQ0=sQuery(id+"F0.wireOp",EDGE,"E3.5.0.40");var subQ1=sQuery(id+"F0.wireOp",EDGE,"E3.5.0.18");var subQ2=makeQuery(id+"F0.imprint","INTERSECT",VERTEX,{"derivedFrom":[subQ1,subQ0]});Q127=makeQuery(id+"F0.imprint","IMPRINT",FACE,{"disambiguationData":[TD([[makeQuery(id+"F0.imprint","IMPRINT",EDGE,{"disambiguationData":[TD([[subQ2,-1.0]])],"derivedFrom":subQ1}),-1.0]])]});}
            var Q128;
            {var subQ0=sQuery(id+"F0.wireOp",EDGE,"E3.6.0.116");Q128=makeQuery(id+"F0.imprint","IMPRINT",FACE,{"disambiguationData":[TD([[makeQuery(id+"F0.imprint","IMPRINT",EDGE,{"derivedFrom":subQ0}),-1.0]])]});}
            var Q129;
            {var subQ0=sQuery(id+"F0.wireOp",EDGE,"E3.15.0.8");var subQ1=sQuery(id+"F0.wireOp",EDGE,"E3.15.0.6");var subQ2=makeQuery(id+"F0.imprint","INTERSECT",VERTEX,{"derivedFrom":[subQ1,subQ0]});Q129=makeQuery(id+"F0.imprint","IMPRINT",FACE,{"disambiguationData":[TD([[makeQuery(id+"F0.imprint","IMPRINT",EDGE,{"disambiguationData":[TD([[subQ2,-1.0]])],"derivedFrom":subQ1}),-1.0]])]});}
            var Q130;
            {var subQ5=sQuery(id+"F0.wireOp",EDGE,"E3.14.0.53");Q130=makeQuery(id+"F0.imprint","IMPRINT",FACE,{"disambiguationData":[TD([[makeQuery(id+"F0.imprint","IMPRINT",EDGE,{"derivedFrom":subQ5}),-1.0]])]});}
            var Q131;
            {var subQ0=sQuery(id+"F0.wireOp",EDGE,"E2.11.0.1");var subQ1=sQuery(id+"F0.wireOp",EDGE,"E2.11.0.0");var subQ2=makeQuery(id+"F0.imprint","INTERSECT",VERTEX,{"derivedFrom":[subQ1,subQ0]});Q131=makeQuery(id+"F0.imprint","IMPRINT",FACE,{"disambiguationData":[TD([[makeQuery(id+"F0.imprint","IMPRINT",EDGE,{"disambiguationData":[TD([[subQ2,1.0]])],"derivedFrom":subQ1}),1.0]])]});}
            var Q132;
            {var subQ0=sQuery(id+"F0.wireOp",EDGE,"E3.11.0.42");var subQ1=sQuery(id+"F0.wireOp",EDGE,"E3.11.0.16");var subQ2=makeQuery(id+"F0.imprint","INTERSECT",VERTEX,{"derivedFrom":[subQ1,subQ0]});Q132=makeQuery(id+"F0.imprint","IMPRINT",FACE,{"disambiguationData":[TD([[makeQuery(id+"F0.imprint","IMPRINT",EDGE,{"disambiguationData":[TD([[subQ2,-1.0]])],"derivedFrom":subQ1}),-1.0]])]});}
            var Q133;
            {var subQ0=sQuery(id+"F0.wireOp",EDGE,"E3.12.0.63");Q133=makeQuery(id+"F0.imprint","IMPRINT",FACE,{"disambiguationData":[TD([[makeQuery(id+"F0.imprint","IMPRINT",EDGE,{"derivedFrom":subQ0}),-1.0]])]});}
            var Q134;
            {var subQ0=sQuery(id+"F0.wireOp",EDGE,"E3.15.0.20");Q134=makeQuery(id+"F0.imprint","IMPRINT",FACE,{"disambiguationData":[TD([[makeQuery(id+"F0.imprint","IMPRINT",EDGE,{"derivedFrom":subQ0}),-1.0]])]});}
            var Q135;
            {var subQ0=sQuery(id+"F0.wireOp",EDGE,"E2.3.0.0");var subQ1=sQuery(id+"F0.wireOp",EDGE,"E2.2.0.1");var subQ2=makeQuery(id+"F0.imprint","INTERSECT",VERTEX,{"derivedFrom":[subQ1,subQ0]});Q135=makeQuery(id+"F0.imprint","IMPRINT",FACE,{"disambiguationData":[TD([[makeQuery(id+"F0.imprint","IMPRINT",EDGE,{"disambiguationData":[TD([[subQ2,1.0]])],"derivedFrom":subQ1}),1.0]])]});}
            var Q136;
            {var subQ0=sQuery(id+"F0.wireOp",EDGE,"E2.11.0.0");var subQ1=sQuery(id+"F0.wireOp",EDGE,"E2.10.0.1");var subQ2=makeQuery(id+"F0.imprint","INTERSECT",VERTEX,{"derivedFrom":[subQ1,subQ0]});Q136=makeQuery(id+"F0.imprint","IMPRINT",FACE,{"disambiguationData":[TD([[makeQuery(id+"F0.imprint","IMPRINT",EDGE,{"disambiguationData":[TD([[subQ2,1.0]])],"derivedFrom":subQ1}),1.0]])]});}
            var Q137;
            {var subQ10=sQuery(id+"F0.wireOp",EDGE,"E3.3.0.93");Q137=makeQuery(id+"F0.imprint","IMPRINT",FACE,{"disambiguationData":[TD([[makeQuery(id+"F0.imprint","IMPRINT",EDGE,{"derivedFrom":subQ10}),-1.0]])]});}
            var Q138;
            {var subQ3=sQuery(id+"F0.wireOp",EDGE,"E3.4.0.56");Q138=makeQuery(id+"F0.imprint","IMPRINT",FACE,{"disambiguationData":[TD([[makeQuery(id+"F0.imprint","IMPRINT",EDGE,{"derivedFrom":subQ3}),-1.0]])]});}
            var Q139;
            {var subQ0=sQuery(id+"F0.wireOp",EDGE,"E3.13.0.75");var subQ1=sQuery(id+"F0.wireOp",EDGE,"E3.13.0.52");var subQ2=makeQuery(id+"F0.imprint","INTERSECT",VERTEX,{"derivedFrom":[subQ1,subQ0]});Q139=makeQuery(id+"F0.imprint","IMPRINT",FACE,{"disambiguationData":[TD([[makeQuery(id+"F0.imprint","IMPRINT",EDGE,{"disambiguationData":[TD([[subQ2,-1.0]])],"derivedFrom":subQ1}),-1.0]])]});}
            var Q140;
            {var subQ5=sQuery(id+"F0.wireOp",EDGE,"E3.15.0.82");Q140=makeQuery(id+"F0.imprint","IMPRINT",FACE,{"disambiguationData":[TD([[makeQuery(id+"F0.imprint","IMPRINT",EDGE,{"derivedFrom":subQ5}),-1.0]])]});}
            var Q141;
            {var subQ0=sQuery(id+"F0.wireOp",EDGE,"E3.5.0.69");var subQ1=sQuery(id+"F0.wireOp",EDGE,"E3.5.0.12");var subQ2=makeQuery(id+"F0.imprint","INTERSECT",VERTEX,{"derivedFrom":[subQ1,subQ0]});Q141=makeQuery(id+"F0.imprint","IMPRINT",FACE,{"disambiguationData":[TD([[makeQuery(id+"F0.imprint","IMPRINT",EDGE,{"disambiguationData":[TD([[subQ2,1.0]])],"derivedFrom":subQ1}),-1.0]])]});}
            var Q142;
            {var subQ5=sQuery(id+"F0.wireOp",EDGE,"E3.6.0.93");Q142=makeQuery(id+"F0.imprint","IMPRINT",FACE,{"disambiguationData":[TD([[makeQuery(id+"F0.imprint","IMPRINT",EDGE,{"derivedFrom":subQ5}),1.0]])]});}
            var Q143;
            {var subQ3=sQuery(id+"F0.wireOp",EDGE,"E2.7.0.7");Q143=makeQuery(id+"F0.imprint","IMPRINT",FACE,{"disambiguationData":[TD([[makeQuery(id+"F0.imprint","IMPRINT",EDGE,{"derivedFrom":subQ3}),-1.0]])]});}
            var Q144;
            {var subQ0=sQuery(id+"F0.wireOp",EDGE,"E3.1.0.19");Q144=makeQuery(id+"F0.imprint","IMPRINT",FACE,{"disambiguationData":[TD([[makeQuery(id+"F0.imprint","IMPRINT",EDGE,{"derivedFrom":subQ0}),-1.0]])]});}
            var Q145;
            {var subQ7=sQuery(id+"F0.wireOp",EDGE,"E3.6.0.83");Q145=makeQuery(id+"F0.imprint","IMPRINT",FACE,{"disambiguationData":[TD([[makeQuery(id+"F0.imprint","IMPRINT",EDGE,{"derivedFrom":subQ7}),-1.0]])]});}
            var Q146;
            {var subQ0=sQuery(id+"F0.wireOp",EDGE,"E3.10.0.37");var subQ5=sQuery(id+"F0.wireOp",EDGE,"E3.10.0.9");var subQ7=makeQuery(id+"F0.imprint","INTERSECT",VERTEX,{"derivedFrom":[subQ5,subQ0]});Q146=makeQuery(id+"F0.imprint","IMPRINT",FACE,{"disambiguationData":[TD([[makeQuery(id+"F0.imprint","IMPRINT",EDGE,{"disambiguationData":[TD([[subQ7,1.0]])],"derivedFrom":subQ5}),1.0]])]});}
            var Q147;
            {var subQ10=sQuery(id+"F0.wireOp",EDGE,"E3.14.0.93");Q147=makeQuery(id+"F0.imprint","IMPRINT",FACE,{"disambiguationData":[TD([[makeQuery(id+"F0.imprint","IMPRINT",EDGE,{"derivedFrom":subQ10}),-1.0]])]});}
            var Q148;
            {var subQ0=sQuery(id+"F0.wireOp",EDGE,"E3.14.0.40");var subQ1=sQuery(id+"F0.wireOp",EDGE,"E3.14.0.18");var subQ2=makeQuery(id+"F0.imprint","INTERSECT",VERTEX,{"derivedFrom":[subQ1,subQ0]});Q148=makeQuery(id+"F0.imprint","IMPRINT",FACE,{"disambiguationData":[TD([[makeQuery(id+"F0.imprint","IMPRINT",EDGE,{"disambiguationData":[TD([[subQ2,-1.0]])],"derivedFrom":subQ1}),-1.0]])]});}
            var Q149;
            {var subQ0=sQuery(id+"F0.wireOp",EDGE,"E3.8.0.75");var subQ1=sQuery(id+"F0.wireOp",EDGE,"E3.8.0.52");var subQ2=makeQuery(id+"F0.imprint","INTERSECT",VERTEX,{"derivedFrom":[subQ1,subQ0]});Q149=makeQuery(id+"F0.imprint","IMPRINT",FACE,{"disambiguationData":[TD([[makeQuery(id+"F0.imprint","IMPRINT",EDGE,{"disambiguationData":[TD([[subQ2,-1.0]])],"derivedFrom":subQ1}),-1.0]])]});}
            var Q150;
            {var subQ0=sQuery(id+"F0.wireOp",EDGE,"E3.12.0.37");var subQ5=sQuery(id+"F0.wireOp",EDGE,"E3.12.0.9");var subQ7=makeQuery(id+"F0.imprint","INTERSECT",VERTEX,{"derivedFrom":[subQ5,subQ0]});Q150=makeQuery(id+"F0.imprint","IMPRINT",FACE,{"disambiguationData":[TD([[makeQuery(id+"F0.imprint","IMPRINT",EDGE,{"disambiguationData":[TD([[subQ7,1.0]])],"derivedFrom":subQ5}),1.0]])]});}
            var Q151;
            {var subQ5=sQuery(id+"F0.wireOp",EDGE,"E2.12.0.4");Q151=makeQuery(id+"F0.imprint","IMPRINT",FACE,{"disambiguationData":[TD([[makeQuery(id+"F0.imprint","IMPRINT",EDGE,{"derivedFrom":subQ5}),1.0]])]});}
            var Q152;
            {var subQ0=sQuery(id+"F0.wireOp",EDGE,"E3.5.0.32");var subQ1=sQuery(id+"F0.wireOp",EDGE,"E3.5.0.0");var subQ2=makeQuery(id+"F0.imprint","INTERSECT",VERTEX,{"derivedFrom":[subQ1,subQ0]});Q152=makeQuery(id+"F0.imprint","IMPRINT",FACE,{"disambiguationData":[TD([[makeQuery(id+"F0.imprint","IMPRINT",EDGE,{"disambiguationData":[TD([[subQ2,1.0]])],"derivedFrom":subQ1}),-1.0]])]});}
            var Q153;
            {var subQ0=sQuery(id+"F0.wireOp",EDGE,"E3.6.0.64");Q153=makeQuery(id+"F0.imprint","IMPRINT",FACE,{"disambiguationData":[TD([[makeQuery(id+"F0.imprint","IMPRINT",EDGE,{"derivedFrom":subQ0}),-1.0]])]});}
            var Q154;
            {var subQ0=sQuery(id+"F0.wireOp",EDGE,"E3.14.0.63");Q154=makeQuery(id+"F0.imprint","IMPRINT",FACE,{"disambiguationData":[TD([[makeQuery(id+"F0.imprint","IMPRINT",EDGE,{"derivedFrom":subQ0}),-1.0]])]});}
            var Q155;
            {var subQ0=sQuery(id+"F0.wireOp",EDGE,"E3.14.0.32");var subQ1=sQuery(id+"F0.wireOp",EDGE,"E3.14.0.0");var subQ2=makeQuery(id+"F0.imprint","INTERSECT",VERTEX,{"derivedFrom":[subQ1,subQ0]});Q155=makeQuery(id+"F0.imprint","IMPRINT",FACE,{"disambiguationData":[TD([[makeQuery(id+"F0.imprint","IMPRINT",EDGE,{"disambiguationData":[TD([[subQ2,1.0]])],"derivedFrom":subQ1}),-1.0]])]});}
            var Q156;
            {var subQ7=sQuery(id+"F0.wireOp",EDGE,"E3.14.0.54");Q156=makeQuery(id+"F0.imprint","IMPRINT",FACE,{"disambiguationData":[TD([[makeQuery(id+"F0.imprint","IMPRINT",EDGE,{"derivedFrom":subQ7}),-1.0]])]});}
            var Q157;
            {var subQ0=sQuery(id+"F0.wireOp",EDGE,"E2.8.0.0");var subQ1=sQuery(id+"F0.wireOp",EDGE,"E2.7.0.1");var subQ2=makeQuery(id+"F0.imprint","INTERSECT",VERTEX,{"derivedFrom":[subQ1,subQ0]});Q157=makeQuery(id+"F0.imprint","IMPRINT",FACE,{"disambiguationData":[TD([[makeQuery(id+"F0.imprint","IMPRINT",EDGE,{"disambiguationData":[TD([[subQ2,1.0]])],"derivedFrom":subQ1}),1.0]])]});}
            var Q158;
            {var subQ0=sQuery(id+"F0.wireOp",EDGE,"E2.12.0.0");var subQ1=sQuery(id+"F0.wireOp",EDGE,"E2.11.0.1");var subQ2=makeQuery(id+"F0.imprint","INTERSECT",VERTEX,{"derivedFrom":[subQ1,subQ0]});Q158=makeQuery(id+"F0.imprint","IMPRINT",FACE,{"disambiguationData":[TD([[makeQuery(id+"F0.imprint","IMPRINT",EDGE,{"disambiguationData":[TD([[subQ2,1.0]])],"derivedFrom":subQ1}),1.0]])]});}
            var Q159;
            {var subQ0=sQuery(id+"F0.wireOp",EDGE,"E3.9.0.69");var subQ1=sQuery(id+"F0.wireOp",EDGE,"E3.9.0.12");var subQ2=makeQuery(id+"F0.imprint","INTERSECT",VERTEX,{"derivedFrom":[subQ1,subQ0]});Q159=makeQuery(id+"F0.imprint","IMPRINT",FACE,{"disambiguationData":[TD([[makeQuery(id+"F0.imprint","IMPRINT",EDGE,{"disambiguationData":[TD([[subQ2,1.0]])],"derivedFrom":subQ1}),-1.0]])]});}
            var Q160;
            {var subQ0=sQuery(id+"F0.wireOp",EDGE,"E3.11.0.68");var subQ1=sQuery(id+"F0.wireOp",EDGE,"E3.11.0.11");var subQ2=makeQuery(id+"F0.imprint","INTERSECT",VERTEX,{"derivedFrom":[subQ1,subQ0]});Q160=makeQuery(id+"F0.imprint","IMPRINT",FACE,{"disambiguationData":[TD([[makeQuery(id+"F0.imprint","IMPRINT",EDGE,{"disambiguationData":[TD([[subQ2,1.0]])],"derivedFrom":subQ1}),-1.0]])]});}
            var Q161;
            {var subQ0=sQuery(id+"F0.wireOp",EDGE,"E3.11.0.97");var subQ1=sQuery(id+"F0.wireOp",EDGE,"E3.11.0.44");var subQ2=makeQuery(id+"F0.imprint","INTERSECT",VERTEX,{"derivedFrom":[subQ1,subQ0]});Q161=makeQuery(id+"F0.imprint","IMPRINT",FACE,{"disambiguationData":[TD([[makeQuery(id+"F0.imprint","IMPRINT",EDGE,{"disambiguationData":[TD([[subQ2,1.0]])],"derivedFrom":subQ1}),-1.0]])]});}
            var Q162;
            {var subQ7=sQuery(id+"F0.wireOp",EDGE,"E3.7.0.87");Q162=makeQuery(id+"F0.imprint","IMPRINT",FACE,{"disambiguationData":[TD([[makeQuery(id+"F0.imprint","IMPRINT",EDGE,{"derivedFrom":subQ7}),-1.0]])]});}
            var Q163;
            {var subQ3=sQuery(id+"F0.wireOp",EDGE,"E3.8.0.56");Q163=makeQuery(id+"F0.imprint","IMPRINT",FACE,{"disambiguationData":[TD([[makeQuery(id+"F0.imprint","IMPRINT",EDGE,{"derivedFrom":subQ3}),-1.0]])]});}
            var Q164;
            {var subQ0=sQuery(id+"F0.wireOp",EDGE,"E3.14.0.37");var subQ5=sQuery(id+"F0.wireOp",EDGE,"E3.14.0.9");var subQ7=makeQuery(id+"F0.imprint","INTERSECT",VERTEX,{"derivedFrom":[subQ5,subQ0]});Q164=makeQuery(id+"F0.imprint","IMPRINT",FACE,{"disambiguationData":[TD([[makeQuery(id+"F0.imprint","IMPRINT",EDGE,{"disambiguationData":[TD([[subQ7,1.0]])],"derivedFrom":subQ5}),1.0]])]});}
            var Q165;
            {var subQ3=sQuery(id+"F0.wireOp",EDGE,"E2.8.0.7");Q165=makeQuery(id+"F0.imprint","IMPRINT",FACE,{"disambiguationData":[TD([[makeQuery(id+"F0.imprint","IMPRINT",EDGE,{"derivedFrom":subQ3}),-1.0]])]});}
            var Q166;
            {var subQ7=sQuery(id+"F0.wireOp",EDGE,"E3.10.0.83");Q166=makeQuery(id+"F0.imprint","IMPRINT",FACE,{"disambiguationData":[TD([[makeQuery(id+"F0.imprint","IMPRINT",EDGE,{"derivedFrom":subQ7}),-1.0]])]});}
            var Q167;
            {var subQ5=sQuery(id+"F0.wireOp",EDGE,"E3.3.0.93");Q167=makeQuery(id+"F0.imprint","IMPRINT",FACE,{"disambiguationData":[TD([[makeQuery(id+"F0.imprint","IMPRINT",EDGE,{"derivedFrom":subQ5}),1.0]])]});}
            var Q168;
            {var subQ0=sQuery(id+"F0.wireOp",EDGE,"E3.8.0.64");Q168=makeQuery(id+"F0.imprint","IMPRINT",FACE,{"disambiguationData":[TD([[makeQuery(id+"F0.imprint","IMPRINT",EDGE,{"derivedFrom":subQ0}),-1.0]])]});}
            var Q169;
            {var subQ0=sQuery(id+"F0.wireOp",EDGE,"E3.10.0.8");var subQ1=sQuery(id+"F0.wireOp",EDGE,"E3.10.0.6");var subQ2=makeQuery(id+"F0.imprint","INTERSECT",VERTEX,{"derivedFrom":[subQ1,subQ0]});Q169=makeQuery(id+"F0.imprint","IMPRINT",FACE,{"disambiguationData":[TD([[makeQuery(id+"F0.imprint","IMPRINT",EDGE,{"disambiguationData":[TD([[subQ2,-1.0]])],"derivedFrom":subQ1}),-1.0]])]});}
            var Q170;
            {var subQ0=sQuery(id+"F0.wireOp",EDGE,"E3.16.0.32");var subQ1=sQuery(id+"F0.wireOp",EDGE,"E3.16.0.0");var subQ2=makeQuery(id+"F0.imprint","INTERSECT",VERTEX,{"derivedFrom":[subQ1,subQ0]});Q170=makeQuery(id+"F0.imprint","IMPRINT",FACE,{"disambiguationData":[TD([[makeQuery(id+"F0.imprint","IMPRINT",EDGE,{"disambiguationData":[TD([[subQ2,1.0]])],"derivedFrom":subQ1}),-1.0]])]});}
            var Q171;
            {var subQ0=sQuery(id+"F0.wireOp",EDGE,"E3.3.0.35");var subQ1=sQuery(id+"F0.wireOp",EDGE,"E3.3.0.32");var subQ2=makeQuery(id+"F0.imprint","INTERSECT",VERTEX,{"derivedFrom":[subQ1,subQ0]});Q171=makeQuery(id+"F0.imprint","IMPRINT",FACE,{"disambiguationData":[TD([[makeQuery(id+"F0.imprint","IMPRINT",EDGE,{"disambiguationData":[TD([[subQ2,1.0]])],"derivedFrom":subQ1}),1.0]])]});}
            var Q172;
            {var subQ3=sQuery(id+"F0.wireOp",EDGE,"E3.5.0.31");Q172=makeQuery(id+"F0.imprint","IMPRINT",FACE,{"disambiguationData":[TD([[makeQuery(id+"F0.imprint","IMPRINT",EDGE,{"derivedFrom":subQ3}),-1.0]])]});}
            var Q173;
            {var subQ0=sQuery(id+"F0.wireOp",EDGE,"E3.4.0.39");var subQ1=sQuery(id+"F0.wireOp",EDGE,"E3.4.0.17");var subQ2=makeQuery(id+"F0.imprint","INTERSECT",VERTEX,{"derivedFrom":[subQ1,subQ0]});Q173=makeQuery(id+"F0.imprint","IMPRINT",FACE,{"disambiguationData":[TD([[makeQuery(id+"F0.imprint","IMPRINT",EDGE,{"disambiguationData":[TD([[subQ2,-1.0]])],"derivedFrom":subQ1}),-1.0]])]});}
            var Q174;
            {var subQ0=sQuery(id+"F0.wireOp",EDGE,"E3.5.0.91");var subQ1=sQuery(id+"F0.wireOp",EDGE,"E3.5.0.49");var subQ2=makeQuery(id+"F0.imprint","INTERSECT",VERTEX,{"derivedFrom":[subQ1,subQ0]});Q174=makeQuery(id+"F0.imprint","IMPRINT",FACE,{"disambiguationData":[TD([[makeQuery(id+"F0.imprint","IMPRINT",EDGE,{"disambiguationData":[TD([[subQ2,-1.0]])],"derivedFrom":subQ1}),-1.0]])]});}
            var Q175;
            {var subQ0=sQuery(id+"F0.wireOp",EDGE,"E3.7.0.37");var subQ5=sQuery(id+"F0.wireOp",EDGE,"E3.7.0.9");var subQ7=makeQuery(id+"F0.imprint","INTERSECT",VERTEX,{"derivedFrom":[subQ5,subQ0]});Q175=makeQuery(id+"F0.imprint","IMPRINT",FACE,{"disambiguationData":[TD([[makeQuery(id+"F0.imprint","IMPRINT",EDGE,{"disambiguationData":[TD([[subQ7,1.0]])],"derivedFrom":subQ5}),1.0]])]});}
            var Q176;
            {var subQ7=sQuery(id+"F0.wireOp",EDGE,"E3.9.0.87");Q176=makeQuery(id+"F0.imprint","IMPRINT",FACE,{"disambiguationData":[TD([[makeQuery(id+"F0.imprint","IMPRINT",EDGE,{"derivedFrom":subQ7}),-1.0]])]});}
            var Q177;
            {var subQ0=sQuery(id+"F0.wireOp",EDGE,"E3.16.0.37");var subQ5=sQuery(id+"F0.wireOp",EDGE,"E3.16.0.9");var subQ7=makeQuery(id+"F0.imprint","INTERSECT",VERTEX,{"derivedFrom":[subQ5,subQ0]});Q177=makeQuery(id+"F0.imprint","IMPRINT",FACE,{"disambiguationData":[TD([[makeQuery(id+"F0.imprint","IMPRINT",EDGE,{"disambiguationData":[TD([[subQ7,1.0]])],"derivedFrom":subQ5}),1.0]])]});}
            var Q178;
            {var subQ0=sQuery(id+"F0.wireOp",EDGE,"E3.3.0.116");Q178=makeQuery(id+"F0.imprint","IMPRINT",FACE,{"disambiguationData":[TD([[makeQuery(id+"F0.imprint","IMPRINT",EDGE,{"derivedFrom":subQ0}),-1.0]])]});}
            var Q179;
            {var subQ3=sQuery(id+"F0.wireOp",EDGE,"E3.3.0.56");Q179=makeQuery(id+"F0.imprint","IMPRINT",FACE,{"disambiguationData":[TD([[makeQuery(id+"F0.imprint","IMPRINT",EDGE,{"derivedFrom":subQ3}),-1.0]])]});}
            var Q180;
            {var subQ3=sQuery(id+"F0.wireOp",EDGE,"E3.14.0.31");Q180=makeQuery(id+"F0.imprint","IMPRINT",FACE,{"disambiguationData":[TD([[makeQuery(id+"F0.imprint","IMPRINT",EDGE,{"derivedFrom":subQ3}),-1.0]])]});}
            var Q181;
            {var subQ3=sQuery(id+"F0.wireOp",EDGE,"E3.7.0.7");Q181=makeQuery(id+"F0.imprint","IMPRINT",FACE,{"disambiguationData":[TD([[makeQuery(id+"F0.imprint","IMPRINT",EDGE,{"derivedFrom":subQ3}),1.0]])]});}
            var Q182;
            {var subQ7=sQuery(id+"F0.wireOp",EDGE,"E3.9.0.54");Q182=makeQuery(id+"F0.imprint","IMPRINT",FACE,{"disambiguationData":[TD([[makeQuery(id+"F0.imprint","IMPRINT",EDGE,{"derivedFrom":subQ7}),-1.0]])]});}
            var Q183;
            {var subQ0=sQuery(id+"F0.wireOp",EDGE,"E2.5.0.0");var subQ1=sQuery(id+"F0.wireOp",EDGE,"E2.4.0.1");var subQ2=makeQuery(id+"F0.imprint","INTERSECT",VERTEX,{"derivedFrom":[subQ1,subQ0]});Q183=makeQuery(id+"F0.imprint","IMPRINT",FACE,{"disambiguationData":[TD([[makeQuery(id+"F0.imprint","IMPRINT",EDGE,{"disambiguationData":[TD([[subQ2,1.0]])],"derivedFrom":subQ1}),1.0]])]});}
            var Q184;
            {var subQ0=sQuery(id+"F0.wireOp",EDGE,"E3.1.0.96");var subQ1=sQuery(id+"F0.wireOp",EDGE,"E3.1.0.43");var subQ2=makeQuery(id+"F0.imprint","INTERSECT",VERTEX,{"derivedFrom":[subQ1,subQ0]});Q184=makeQuery(id+"F0.imprint","IMPRINT",FACE,{"disambiguationData":[TD([[makeQuery(id+"F0.imprint","IMPRINT",EDGE,{"disambiguationData":[TD([[subQ2,1.0]])],"derivedFrom":subQ1}),-1.0]])]});}
            var Q185;
            {var subQ0=sQuery(id+"F0.wireOp",EDGE,"E3.2.0.32");var subQ1=sQuery(id+"F0.wireOp",EDGE,"E3.2.0.0");var subQ2=makeQuery(id+"F0.imprint","INTERSECT",VERTEX,{"derivedFrom":[subQ1,subQ0]});Q185=makeQuery(id+"F0.imprint","IMPRINT",FACE,{"disambiguationData":[TD([[makeQuery(id+"F0.imprint","IMPRINT",EDGE,{"disambiguationData":[TD([[subQ2,1.0]])],"derivedFrom":subQ1}),-1.0]])]});}
            var Q186;
            {var subQ0=sQuery(id+"F0.wireOp",EDGE,"E3.3.0.64");Q186=makeQuery(id+"F0.imprint","IMPRINT",FACE,{"disambiguationData":[TD([[makeQuery(id+"F0.imprint","IMPRINT",EDGE,{"derivedFrom":subQ0}),-1.0]])]});}
            var Q187;
            {var subQ7=sQuery(id+"F0.wireOp",EDGE,"E3.5.0.83");Q187=makeQuery(id+"F0.imprint","IMPRINT",FACE,{"disambiguationData":[TD([[makeQuery(id+"F0.imprint","IMPRINT",EDGE,{"derivedFrom":subQ7}),-1.0]])]});}
            var Q188;
            {var subQ0=sQuery(id+"F0.wireOp",EDGE,"E3.15.0.68");var subQ1=sQuery(id+"F0.wireOp",EDGE,"E3.15.0.11");var subQ2=makeQuery(id+"F0.imprint","INTERSECT",VERTEX,{"derivedFrom":[subQ1,subQ0]});Q188=makeQuery(id+"F0.imprint","IMPRINT",FACE,{"disambiguationData":[TD([[makeQuery(id+"F0.imprint","IMPRINT",EDGE,{"disambiguationData":[TD([[subQ2,1.0]])],"derivedFrom":subQ1}),-1.0]])]});}
            var Q189;
            {var subQ3=sQuery(id+"F0.wireOp",EDGE,"E3.16.0.7");Q189=makeQuery(id+"F0.imprint","IMPRINT",FACE,{"disambiguationData":[TD([[makeQuery(id+"F0.imprint","IMPRINT",EDGE,{"derivedFrom":subQ3}),1.0]])]});}
            var Q190;
            {var subQ0=sQuery(id+"F0.wireOp",EDGE,"E3.15.0.97");var subQ1=sQuery(id+"F0.wireOp",EDGE,"E3.15.0.44");var subQ2=makeQuery(id+"F0.imprint","INTERSECT",VERTEX,{"derivedFrom":[subQ1,subQ0]});Q190=makeQuery(id+"F0.imprint","IMPRINT",FACE,{"disambiguationData":[TD([[makeQuery(id+"F0.imprint","IMPRINT",EDGE,{"disambiguationData":[TD([[subQ2,1.0]])],"derivedFrom":subQ1}),-1.0]])]});}
            var Q191;
            {var subQ3=sQuery(id+"F0.wireOp",EDGE,"E3.12.0.56");Q191=makeQuery(id+"F0.imprint","IMPRINT",FACE,{"disambiguationData":[TD([[makeQuery(id+"F0.imprint","IMPRINT",EDGE,{"derivedFrom":subQ3}),-1.0]])]});}
            var Q192;
            {var subQ0=sQuery(id+"F0.wireOp",EDGE,"E3.3.0.57");Q192=makeQuery(id+"F0.imprint","IMPRINT",FACE,{"disambiguationData":[TD([[makeQuery(id+"F0.imprint","IMPRINT",EDGE,{"derivedFrom":subQ0}),-1.0]])]});}
            var Q193;
            {var subQ10=sQuery(id+"F0.wireOp",EDGE,"E3.4.0.93");Q193=makeQuery(id+"F0.imprint","IMPRINT",FACE,{"disambiguationData":[TD([[makeQuery(id+"F0.imprint","IMPRINT",EDGE,{"derivedFrom":subQ10}),-1.0]])]});}
            var Q194;
            {var subQ0=sQuery(id+"F0.wireOp",EDGE,"E3.5.0.116");Q194=makeQuery(id+"F0.imprint","IMPRINT",FACE,{"disambiguationData":[TD([[makeQuery(id+"F0.imprint","IMPRINT",EDGE,{"derivedFrom":subQ0}),-1.0]])]});}
            var Q195;
            {var subQ5=sQuery(id+"F0.wireOp",EDGE,"E3.13.0.53");Q195=makeQuery(id+"F0.imprint","IMPRINT",FACE,{"disambiguationData":[TD([[makeQuery(id+"F0.imprint","IMPRINT",EDGE,{"derivedFrom":subQ5}),-1.0]])]});}
            var Q196;
            {var subQ3=sQuery(id+"F0.wireOp",EDGE,"E3.16.0.31");Q196=makeQuery(id+"F0.imprint","IMPRINT",FACE,{"disambiguationData":[TD([[makeQuery(id+"F0.imprint","IMPRINT",EDGE,{"derivedFrom":subQ3}),-1.0]])]});}
            var Q197;
            {var subQ3=sQuery(id+"F0.wireOp",EDGE,"E3.9.0.7");Q197=makeQuery(id+"F0.imprint","IMPRINT",FACE,{"disambiguationData":[TD([[makeQuery(id+"F0.imprint","IMPRINT",EDGE,{"derivedFrom":subQ3}),1.0]])]});}
            var Q198;
            {var subQ7=sQuery(id+"F0.wireOp",EDGE,"E3.11.0.54");Q198=makeQuery(id+"F0.imprint","IMPRINT",FACE,{"disambiguationData":[TD([[makeQuery(id+"F0.imprint","IMPRINT",EDGE,{"derivedFrom":subQ7}),-1.0]])]});}
            var Q199;
            {var subQ0=sQuery(id+"F0.wireOp",EDGE,"E3.11.0.63");Q199=makeQuery(id+"F0.imprint","IMPRINT",FACE,{"disambiguationData":[TD([[makeQuery(id+"F0.imprint","IMPRINT",EDGE,{"derivedFrom":subQ0}),-1.0]])]});}
            var Q200;
            {var subQ0=sQuery(id+"F0.wireOp",EDGE,"E3.3.0.42");var subQ1=sQuery(id+"F0.wireOp",EDGE,"E3.3.0.16");var subQ2=makeQuery(id+"F0.imprint","INTERSECT",VERTEX,{"derivedFrom":[subQ1,subQ0]});Q200=makeQuery(id+"F0.imprint","IMPRINT",FACE,{"disambiguationData":[TD([[makeQuery(id+"F0.imprint","IMPRINT",EDGE,{"disambiguationData":[TD([[subQ2,-1.0]])],"derivedFrom":subQ1}),-1.0]])]});}
            var Q201;
            {var subQ0=sQuery(id+"F0.wireOp",EDGE,"E3.4.0.32");var subQ1=sQuery(id+"F0.wireOp",EDGE,"E3.4.0.0");var subQ2=makeQuery(id+"F0.imprint","INTERSECT",VERTEX,{"derivedFrom":[subQ1,subQ0]});Q201=makeQuery(id+"F0.imprint","IMPRINT",FACE,{"disambiguationData":[TD([[makeQuery(id+"F0.imprint","IMPRINT",EDGE,{"disambiguationData":[TD([[subQ2,1.0]])],"derivedFrom":subQ1}),-1.0]])]});}
            var Q202;
            {var subQ0=sQuery(id+"F0.wireOp",EDGE,"E3.5.0.64");Q202=makeQuery(id+"F0.imprint","IMPRINT",FACE,{"disambiguationData":[TD([[makeQuery(id+"F0.imprint","IMPRINT",EDGE,{"derivedFrom":subQ0}),-1.0]])]});}
            var Q203;
            {var subQ0=sQuery(id+"F0.wireOp",EDGE,"E3.7.0.75");var subQ1=sQuery(id+"F0.wireOp",EDGE,"E3.7.0.52");var subQ2=makeQuery(id+"F0.imprint","INTERSECT",VERTEX,{"derivedFrom":[subQ1,subQ0]});Q203=makeQuery(id+"F0.imprint","IMPRINT",FACE,{"disambiguationData":[TD([[makeQuery(id+"F0.imprint","IMPRINT",EDGE,{"disambiguationData":[TD([[subQ2,-1.0]])],"derivedFrom":subQ1}),-1.0]])]});}
            var Q204;
            {var subQ5=sQuery(id+"F0.wireOp",EDGE,"E3.16.0.93");Q204=makeQuery(id+"F0.imprint","IMPRINT",FACE,{"disambiguationData":[TD([[makeQuery(id+"F0.imprint","IMPRINT",EDGE,{"derivedFrom":subQ5}),1.0]])]});}
            var Q205;
            {var subQ0=sQuery(id+"F0.wireOp",EDGE,"E3.13.0.40");var subQ1=sQuery(id+"F0.wireOp",EDGE,"E3.13.0.18");var subQ2=makeQuery(id+"F0.imprint","INTERSECT",VERTEX,{"derivedFrom":[subQ1,subQ0]});Q205=makeQuery(id+"F0.imprint","IMPRINT",FACE,{"disambiguationData":[TD([[makeQuery(id+"F0.imprint","IMPRINT",EDGE,{"disambiguationData":[TD([[subQ2,-1.0]])],"derivedFrom":subQ1}),-1.0]])]});}
            var Q206;
            {var subQ10=sQuery(id+"F0.wireOp",EDGE,"E3.6.0.93");Q206=makeQuery(id+"F0.imprint","IMPRINT",FACE,{"disambiguationData":[TD([[makeQuery(id+"F0.imprint","IMPRINT",EDGE,{"derivedFrom":subQ10}),-1.0]])]});}
            var Q207;
            {var subQ3=sQuery(id+"F0.wireOp",EDGE,"E3.7.0.56");Q207=makeQuery(id+"F0.imprint","IMPRINT",FACE,{"disambiguationData":[TD([[makeQuery(id+"F0.imprint","IMPRINT",EDGE,{"derivedFrom":subQ3}),-1.0]])]});}
            var Q208;
            {var subQ7=sQuery(id+"F0.wireOp",EDGE,"E3.13.0.54");Q208=makeQuery(id+"F0.imprint","IMPRINT",FACE,{"disambiguationData":[TD([[makeQuery(id+"F0.imprint","IMPRINT",EDGE,{"derivedFrom":subQ7}),-1.0]])]});}
            var Q209;
            {var subQ5=sQuery(id+"F0.wireOp",EDGE,"E3.15.0.53");Q209=makeQuery(id+"F0.imprint","IMPRINT",FACE,{"disambiguationData":[TD([[makeQuery(id+"F0.imprint","IMPRINT",EDGE,{"derivedFrom":subQ5}),-1.0]])]});}
            var Q210;
            {var subQ5=sQuery(id+"F0.wireOp",EDGE,"E2.2.0.4");Q210=makeQuery(id+"F0.imprint","IMPRINT",FACE,{"disambiguationData":[TD([[makeQuery(id+"F0.imprint","IMPRINT",EDGE,{"derivedFrom":subQ5}),1.0]])]});}
            var Q211;
            {var subQ5=sQuery(id+"F0.wireOp",EDGE,"E2.14.0.4");Q211=makeQuery(id+"F0.imprint","IMPRINT",FACE,{"disambiguationData":[TD([[makeQuery(id+"F0.imprint","IMPRINT",EDGE,{"derivedFrom":subQ5}),1.0]])]});}
            var Q212;
            {var subQ5=sQuery(id+"F0.wireOp",EDGE,"E2.6.0.4");Q212=makeQuery(id+"F0.imprint","IMPRINT",FACE,{"disambiguationData":[TD([[makeQuery(id+"F0.imprint","IMPRINT",EDGE,{"derivedFrom":subQ5}),1.0]])]});}
            var Q213;
            {var subQ3=sQuery(id+"F0.wireOp",EDGE,"E3.11.0.7");Q213=makeQuery(id+"F0.imprint","IMPRINT",FACE,{"disambiguationData":[TD([[makeQuery(id+"F0.imprint","IMPRINT",EDGE,{"derivedFrom":subQ3}),1.0]])]});}
            var Q214;
            {var subQ0=sQuery(id+"F0.wireOp",EDGE,"E3.12.0.42");var subQ1=sQuery(id+"F0.wireOp",EDGE,"E3.12.0.16");var subQ2=makeQuery(id+"F0.imprint","INTERSECT",VERTEX,{"derivedFrom":[subQ1,subQ0]});Q214=makeQuery(id+"F0.imprint","IMPRINT",FACE,{"disambiguationData":[TD([[makeQuery(id+"F0.imprint","IMPRINT",EDGE,{"disambiguationData":[TD([[subQ2,-1.0]])],"derivedFrom":subQ1}),-1.0]])]});}
            var Q215;
            {var subQ0=sQuery(id+"F0.wireOp",EDGE,"E3.5.0.51");var subQ1=sQuery(id+"F0.wireOp",EDGE,"E3.5.0.10");var subQ2=makeQuery(id+"F0.imprint","INTERSECT",VERTEX,{"derivedFrom":[subQ1,subQ0]});Q215=makeQuery(id+"F0.imprint","IMPRINT",FACE,{"disambiguationData":[TD([[makeQuery(id+"F0.imprint","IMPRINT",EDGE,{"disambiguationData":[TD([[subQ2,-1.0]])],"derivedFrom":subQ1}),1.0]])]});}
            var Q216;
            {var subQ0=sQuery(id+"F0.wireOp",EDGE,"E3.6.0.32");var subQ1=sQuery(id+"F0.wireOp",EDGE,"E3.6.0.0");var subQ2=makeQuery(id+"F0.imprint","INTERSECT",VERTEX,{"derivedFrom":[subQ1,subQ0]});Q216=makeQuery(id+"F0.imprint","IMPRINT",FACE,{"disambiguationData":[TD([[makeQuery(id+"F0.imprint","IMPRINT",EDGE,{"disambiguationData":[TD([[subQ2,1.0]])],"derivedFrom":subQ1}),-1.0]])]});}
            var Q217;
            {var subQ7=sQuery(id+"F0.wireOp",EDGE,"E3.9.0.83");Q217=makeQuery(id+"F0.imprint","IMPRINT",FACE,{"disambiguationData":[TD([[makeQuery(id+"F0.imprint","IMPRINT",EDGE,{"derivedFrom":subQ7}),-1.0]])]});}
            var Q218;
            {var subQ10=sQuery(id+"F0.wireOp",EDGE,"E3.15.0.93");Q218=makeQuery(id+"F0.imprint","IMPRINT",FACE,{"disambiguationData":[TD([[makeQuery(id+"F0.imprint","IMPRINT",EDGE,{"derivedFrom":subQ10}),-1.0]])]});}
            var Q219;
            {var subQ0=sQuery(id+"F0.wireOp",EDGE,"E3.15.0.40");var subQ1=sQuery(id+"F0.wireOp",EDGE,"E3.15.0.18");var subQ2=makeQuery(id+"F0.imprint","INTERSECT",VERTEX,{"derivedFrom":[subQ1,subQ0]});Q219=makeQuery(id+"F0.imprint","IMPRINT",FACE,{"disambiguationData":[TD([[makeQuery(id+"F0.imprint","IMPRINT",EDGE,{"disambiguationData":[TD([[subQ2,-1.0]])],"derivedFrom":subQ1}),-1.0]])]});}
            var Q220;
            {var subQ0=sQuery(id+"F0.wireOp",EDGE,"E2.14.0.0");var subQ1=sQuery(id+"F0.wireOp",EDGE,"E2.13.0.1");var subQ2=makeQuery(id+"F0.imprint","INTERSECT",VERTEX,{"derivedFrom":[subQ1,subQ0]});Q220=makeQuery(id+"F0.imprint","IMPRINT",FACE,{"disambiguationData":[TD([[makeQuery(id+"F0.imprint","IMPRINT",EDGE,{"disambiguationData":[TD([[subQ2,1.0]])],"derivedFrom":subQ1}),1.0]])]});}
            var Q221;
            {var subQ0=sQuery(id+"F0.wireOp",EDGE,"E2.10.0.0");var subQ1=sQuery(id+"F0.wireOp",EDGE,"E2.9.0.1");var subQ2=makeQuery(id+"F0.imprint","INTERSECT",VERTEX,{"derivedFrom":[subQ1,subQ0]});Q221=makeQuery(id+"F0.imprint","IMPRINT",FACE,{"disambiguationData":[TD([[makeQuery(id+"F0.imprint","IMPRINT",EDGE,{"disambiguationData":[TD([[subQ2,1.0]])],"derivedFrom":subQ1}),1.0]])]});}
            var Q222;
            {var subQ3=sQuery(id+"F0.wireOp",EDGE,"E3.1.0.66");Q222=makeQuery(id+"F0.imprint","IMPRINT",FACE,{"disambiguationData":[TD([[makeQuery(id+"F0.imprint","IMPRINT",EDGE,{"derivedFrom":subQ3}),-1.0]])]});}
            var Q223;
            {var subQ0=sQuery(id+"F0.wireOp",EDGE,"E3.15.0.32");var subQ1=sQuery(id+"F0.wireOp",EDGE,"E3.15.0.0");var subQ2=makeQuery(id+"F0.imprint","INTERSECT",VERTEX,{"derivedFrom":[subQ1,subQ0]});Q223=makeQuery(id+"F0.imprint","IMPRINT",FACE,{"disambiguationData":[TD([[makeQuery(id+"F0.imprint","IMPRINT",EDGE,{"disambiguationData":[TD([[subQ2,1.0]])],"derivedFrom":subQ1}),-1.0]])]});}
            var Q224;
            {var subQ0=sQuery(id+"F0.wireOp",EDGE,"E3.6.0.37");var subQ5=sQuery(id+"F0.wireOp",EDGE,"E3.6.0.9");var subQ7=makeQuery(id+"F0.imprint","INTERSECT",VERTEX,{"derivedFrom":[subQ5,subQ0]});Q224=makeQuery(id+"F0.imprint","IMPRINT",FACE,{"disambiguationData":[TD([[makeQuery(id+"F0.imprint","IMPRINT",EDGE,{"disambiguationData":[TD([[subQ7,1.0]])],"derivedFrom":subQ5}),1.0]])]});}
            var Q225;
            {var subQ0=sQuery(id+"F0.wireOp",EDGE,"E3.7.0.57");Q225=makeQuery(id+"F0.imprint","IMPRINT",FACE,{"disambiguationData":[TD([[makeQuery(id+"F0.imprint","IMPRINT",EDGE,{"derivedFrom":subQ0}),-1.0]])]});}
            var Q226;
            {var subQ3=sQuery(id+"F0.wireOp",EDGE,"E3.9.0.56");Q226=makeQuery(id+"F0.imprint","IMPRINT",FACE,{"disambiguationData":[TD([[makeQuery(id+"F0.imprint","IMPRINT",EDGE,{"derivedFrom":subQ3}),-1.0]])]});}
            var Q227;
            {var subQ0=sQuery(id+"F0.wireOp",EDGE,"E3.10.0.69");var subQ1=sQuery(id+"F0.wireOp",EDGE,"E3.10.0.12");var subQ2=makeQuery(id+"F0.imprint","INTERSECT",VERTEX,{"derivedFrom":[subQ1,subQ0]});Q227=makeQuery(id+"F0.imprint","IMPRINT",FACE,{"disambiguationData":[TD([[makeQuery(id+"F0.imprint","IMPRINT",EDGE,{"disambiguationData":[TD([[subQ2,1.0]])],"derivedFrom":subQ1}),-1.0]])]});}
            var Q228;
            {var subQ7=sQuery(id+"F0.wireOp",EDGE,"E3.15.0.54");Q228=makeQuery(id+"F0.imprint","IMPRINT",FACE,{"disambiguationData":[TD([[makeQuery(id+"F0.imprint","IMPRINT",EDGE,{"derivedFrom":subQ7}),-1.0]])]});}
            var Q229;
            {var subQ0=sQuery(id+"F0.wireOp",EDGE,"E3.15.0.63");Q229=makeQuery(id+"F0.imprint","IMPRINT",FACE,{"disambiguationData":[TD([[makeQuery(id+"F0.imprint","IMPRINT",EDGE,{"derivedFrom":subQ0}),-1.0]])]});}
            var Q230;
            {var subQ5=sQuery(id+"F0.wireOp",EDGE,"E3.1.0.53");Q230=makeQuery(id+"F0.imprint","IMPRINT",FACE,{"disambiguationData":[TD([[makeQuery(id+"F0.imprint","IMPRINT",EDGE,{"derivedFrom":subQ5}),-1.0]])]});}
            var Q231;
            {var subQ0=sQuery(id+"F0.wireOp",EDGE,"E3.2.0.35");var subQ1=sQuery(id+"F0.wireOp",EDGE,"E3.2.0.32");var subQ2=makeQuery(id+"F0.imprint","INTERSECT",VERTEX,{"derivedFrom":[subQ1,subQ0]});Q231=makeQuery(id+"F0.imprint","IMPRINT",FACE,{"disambiguationData":[TD([[makeQuery(id+"F0.imprint","IMPRINT",EDGE,{"disambiguationData":[TD([[subQ2,1.0]])],"derivedFrom":subQ1}),1.0]])]});}
            var Q232;
            {var subQ0=sQuery(id+"F0.wireOp",EDGE,"E3.15.0.37");var subQ5=sQuery(id+"F0.wireOp",EDGE,"E3.15.0.9");var subQ7=makeQuery(id+"F0.imprint","INTERSECT",VERTEX,{"derivedFrom":[subQ5,subQ0]});Q232=makeQuery(id+"F0.imprint","IMPRINT",FACE,{"disambiguationData":[TD([[makeQuery(id+"F0.imprint","IMPRINT",EDGE,{"disambiguationData":[TD([[subQ7,1.0]])],"derivedFrom":subQ5}),1.0]])]});}
            var Q233;
            {var subQ3=sQuery(id+"F0.wireOp",EDGE,"E3.13.0.7");Q233=makeQuery(id+"F0.imprint","IMPRINT",FACE,{"disambiguationData":[TD([[makeQuery(id+"F0.imprint","IMPRINT",EDGE,{"derivedFrom":subQ3}),1.0]])]});}
            var Q234;
            {var subQ3=sQuery(id+"F0.wireOp",EDGE,"E3.6.0.7");Q234=makeQuery(id+"F0.imprint","IMPRINT",FACE,{"disambiguationData":[TD([[makeQuery(id+"F0.imprint","IMPRINT",EDGE,{"derivedFrom":subQ3}),1.0]])]});}
            var Q235;
            {var subQ0=sQuery(id+"F0.wireOp",EDGE,"E3.7.0.42");var subQ1=sQuery(id+"F0.wireOp",EDGE,"E3.7.0.16");var subQ2=makeQuery(id+"F0.imprint","INTERSECT",VERTEX,{"derivedFrom":[subQ1,subQ0]});Q235=makeQuery(id+"F0.imprint","IMPRINT",FACE,{"disambiguationData":[TD([[makeQuery(id+"F0.imprint","IMPRINT",EDGE,{"disambiguationData":[TD([[subQ2,-1.0]])],"derivedFrom":subQ1}),-1.0]])]});}
            var Q236;
            {var subQ0=sQuery(id+"F0.wireOp",EDGE,"E3.7.0.51");var subQ1=sQuery(id+"F0.wireOp",EDGE,"E3.7.0.10");var subQ2=makeQuery(id+"F0.imprint","INTERSECT",VERTEX,{"derivedFrom":[subQ1,subQ0]});Q236=makeQuery(id+"F0.imprint","IMPRINT",FACE,{"disambiguationData":[TD([[makeQuery(id+"F0.imprint","IMPRINT",EDGE,{"disambiguationData":[TD([[subQ2,-1.0]])],"derivedFrom":subQ1}),1.0]])]});}
            var Q237;
            {var subQ3=sQuery(id+"F0.wireOp",EDGE,"E3.13.0.31");Q237=makeQuery(id+"F0.imprint","IMPRINT",FACE,{"disambiguationData":[TD([[makeQuery(id+"F0.imprint","IMPRINT",EDGE,{"derivedFrom":subQ3}),-1.0]])]});}
            var Q238;
            {var subQ0=sQuery(id+"F0.wireOp",EDGE,"E2.6.0.1");var subQ1=sQuery(id+"F0.wireOp",EDGE,"E2.6.0.0");var subQ2=makeQuery(id+"F0.imprint","INTERSECT",VERTEX,{"derivedFrom":[subQ1,subQ0]});Q238=makeQuery(id+"F0.imprint","IMPRINT",FACE,{"disambiguationData":[TD([[makeQuery(id+"F0.imprint","IMPRINT",EDGE,{"disambiguationData":[TD([[subQ2,1.0]])],"derivedFrom":subQ1}),1.0]])]});}
            var Q239;
            {var subQ0=sQuery(id+"F0.wireOp",EDGE,"E3.1.0.40");var subQ1=sQuery(id+"F0.wireOp",EDGE,"E3.1.0.18");var subQ2=makeQuery(id+"F0.imprint","INTERSECT",VERTEX,{"derivedFrom":[subQ1,subQ0]});Q239=makeQuery(id+"F0.imprint","IMPRINT",FACE,{"disambiguationData":[TD([[makeQuery(id+"F0.imprint","IMPRINT",EDGE,{"disambiguationData":[TD([[subQ2,-1.0]])],"derivedFrom":subQ1}),-1.0]])]});}
            var Q240;
            {var subQ5=sQuery(id+"F0.wireOp",EDGE,"E3.4.0.93");Q240=makeQuery(id+"F0.imprint","IMPRINT",FACE,{"disambiguationData":[TD([[makeQuery(id+"F0.imprint","IMPRINT",EDGE,{"derivedFrom":subQ5}),1.0]])]});}
            var Q241;
            {var subQ0=sQuery(id+"F0.wireOp",EDGE,"E3.5.0.68");var subQ1=sQuery(id+"F0.wireOp",EDGE,"E3.5.0.11");var subQ2=makeQuery(id+"F0.imprint","INTERSECT",VERTEX,{"derivedFrom":[subQ1,subQ0]});Q241=makeQuery(id+"F0.imprint","IMPRINT",FACE,{"disambiguationData":[TD([[makeQuery(id+"F0.imprint","IMPRINT",EDGE,{"disambiguationData":[TD([[subQ2,1.0]])],"derivedFrom":subQ1}),-1.0]])]});}
            var Q242;
            {var subQ3=sQuery(id+"F0.wireOp",EDGE,"E3.15.0.7");Q242=makeQuery(id+"F0.imprint","IMPRINT",FACE,{"disambiguationData":[TD([[makeQuery(id+"F0.imprint","IMPRINT",EDGE,{"derivedFrom":subQ3}),1.0]])]});}
            var Q243;
            {var subQ0=sQuery(id+"F0.wireOp",EDGE,"E3.14.0.68");var subQ1=sQuery(id+"F0.wireOp",EDGE,"E3.14.0.11");var subQ2=makeQuery(id+"F0.imprint","INTERSECT",VERTEX,{"derivedFrom":[subQ1,subQ0]});Q243=makeQuery(id+"F0.imprint","IMPRINT",FACE,{"disambiguationData":[TD([[makeQuery(id+"F0.imprint","IMPRINT",EDGE,{"disambiguationData":[TD([[subQ2,1.0]])],"derivedFrom":subQ1}),-1.0]])]});}
            var Q244;
            {var subQ0=sQuery(id+"F0.wireOp",EDGE,"E3.15.0.41");var subQ1=sQuery(id+"F0.wireOp",EDGE,"E3.15.0.13");var subQ2=makeQuery(id+"F0.imprint","INTERSECT",VERTEX,{"derivedFrom":[subQ1,subQ0]});Q244=makeQuery(id+"F0.imprint","IMPRINT",FACE,{"disambiguationData":[TD([[makeQuery(id+"F0.imprint","IMPRINT",EDGE,{"disambiguationData":[TD([[subQ2,-1.0]])],"derivedFrom":subQ1}),-1.0]])]});}
            var Q245;
            {var subQ0=sQuery(id+"F0.wireOp",EDGE,"E3.22.0.2");Q245=makeQuery(id+"F0.imprint","IMPRINT",FACE,{"disambiguationData":[TD([[makeQuery(id+"F0.imprint","IMPRINT",EDGE,{"derivedFrom":subQ0}),1.0]])]});}
            var Q246;
            {var subQ5=sQuery(id+"F0.wireOp",EDGE,"E2.7.0.4");Q246=makeQuery(id+"F0.imprint","IMPRINT",FACE,{"disambiguationData":[TD([[makeQuery(id+"F0.imprint","IMPRINT",EDGE,{"derivedFrom":subQ5}),1.0]])]});}
            var Q247;
            {var subQ0=sQuery(id+"F0.wireOp",EDGE,"E3.4.0.35");var subQ1=sQuery(id+"F0.wireOp",EDGE,"E3.4.0.32");var subQ2=makeQuery(id+"F0.imprint","INTERSECT",VERTEX,{"derivedFrom":[subQ1,subQ0]});Q247=makeQuery(id+"F0.imprint","IMPRINT",FACE,{"disambiguationData":[TD([[makeQuery(id+"F0.imprint","IMPRINT",EDGE,{"disambiguationData":[TD([[subQ2,1.0]])],"derivedFrom":subQ1}),1.0]])]});}
            var Q248;
            {var subQ5=sQuery(id+"F0.wireOp",EDGE,"E3.3.0.53");Q248=makeQuery(id+"F0.imprint","IMPRINT",FACE,{"disambiguationData":[TD([[makeQuery(id+"F0.imprint","IMPRINT",EDGE,{"derivedFrom":subQ5}),-1.0]])]});}
            var Q249;
            {var subQ0=sQuery(id+"F0.wireOp",EDGE,"E3.19.0.57");Q249=makeQuery(id+"F0.imprint","IMPRINT",FACE,{"disambiguationData":[TD([[makeQuery(id+"F0.imprint","IMPRINT",EDGE,{"derivedFrom":subQ0}),-1.0]])]});}
            var Q250;
            {var subQ0=sQuery(id+"F0.wireOp",EDGE,"E3.20.0.40");var subQ1=sQuery(id+"F0.wireOp",EDGE,"E3.20.0.18");var subQ2=makeQuery(id+"F0.imprint","INTERSECT",VERTEX,{"derivedFrom":[subQ1,subQ0]});Q250=makeQuery(id+"F0.imprint","IMPRINT",FACE,{"disambiguationData":[TD([[makeQuery(id+"F0.imprint","IMPRINT",EDGE,{"disambiguationData":[TD([[subQ2,-1.0]])],"derivedFrom":subQ1}),-1.0]])]});}
            var Q251;
            {var subQ10=sQuery(id+"F0.wireOp",EDGE,"E3.20.0.93");Q251=makeQuery(id+"F0.imprint","IMPRINT",FACE,{"disambiguationData":[TD([[makeQuery(id+"F0.imprint","IMPRINT",EDGE,{"derivedFrom":subQ10}),-1.0]])]});}
            var Q252;
            {var subQ0=sQuery(id+"F0.wireOp",EDGE,"E3.21.0.116");Q252=makeQuery(id+"F0.imprint","IMPRINT",FACE,{"disambiguationData":[TD([[makeQuery(id+"F0.imprint","IMPRINT",EDGE,{"derivedFrom":subQ0}),-1.0]])]});}
            var Q253;
            {var subQ3=sQuery(id+"F0.wireOp",EDGE,"E3.23.0.103");Q253=makeQuery(id+"F0.imprint","IMPRINT",FACE,{"disambiguationData":[TD([[makeQuery(id+"F0.imprint","IMPRINT",EDGE,{"derivedFrom":subQ3}),1.0]])]});}
            var Q254;
            {var subQ0=sQuery(id+"F0.wireOp",EDGE,"E3.24.0.68");var subQ1=sQuery(id+"F0.wireOp",EDGE,"E3.24.0.11");var subQ2=makeQuery(id+"F0.imprint","INTERSECT",VERTEX,{"derivedFrom":[subQ1,subQ0]});Q254=makeQuery(id+"F0.imprint","IMPRINT",FACE,{"disambiguationData":[TD([[makeQuery(id+"F0.imprint","IMPRINT",EDGE,{"disambiguationData":[TD([[subQ2,1.0]])],"derivedFrom":subQ1}),-1.0]])]});}
            var Q255;
            {var subQ0=sQuery(id+"F0.wireOp",EDGE,"E3.18.0.19");Q255=makeQuery(id+"F0.imprint","IMPRINT",FACE,{"disambiguationData":[TD([[makeQuery(id+"F0.imprint","IMPRINT",EDGE,{"derivedFrom":subQ0}),-1.0]])]});}
            var Q256;
            {var subQ0=sQuery(id+"F0.wireOp",EDGE,"E3.23.0.75");var subQ1=sQuery(id+"F0.wireOp",EDGE,"E3.23.0.52");var subQ2=makeQuery(id+"F0.imprint","INTERSECT",VERTEX,{"derivedFrom":[subQ1,subQ0]});Q256=makeQuery(id+"F0.imprint","IMPRINT",FACE,{"disambiguationData":[TD([[makeQuery(id+"F0.imprint","IMPRINT",EDGE,{"disambiguationData":[TD([[subQ2,-1.0]])],"derivedFrom":subQ1}),-1.0]])]});}
            var Q257;
            {var subQ0=sQuery(id+"F0.wireOp",EDGE,"E3.23.0.35");var subQ1=sQuery(id+"F0.wireOp",EDGE,"E3.23.0.32");var subQ2=makeQuery(id+"F0.imprint","INTERSECT",VERTEX,{"derivedFrom":[subQ1,subQ0]});Q257=makeQuery(id+"F0.imprint","IMPRINT",FACE,{"disambiguationData":[TD([[makeQuery(id+"F0.imprint","IMPRINT",EDGE,{"disambiguationData":[TD([[subQ2,1.0]])],"derivedFrom":subQ1}),1.0]])]});}
            var Q258;
            {var subQ0=sQuery(id+"F0.wireOp",EDGE,"E3.24.0.39");var subQ1=sQuery(id+"F0.wireOp",EDGE,"E3.24.0.17");var subQ2=makeQuery(id+"F0.imprint","INTERSECT",VERTEX,{"derivedFrom":[subQ1,subQ0]});Q258=makeQuery(id+"F0.imprint","IMPRINT",FACE,{"disambiguationData":[TD([[makeQuery(id+"F0.imprint","IMPRINT",EDGE,{"disambiguationData":[TD([[subQ2,-1.0]])],"derivedFrom":subQ1}),-1.0]])]});}
            var Q259;
            {var subQ0=sQuery(id+"F0.wireOp",EDGE,"E3.24.0.35");var subQ1=sQuery(id+"F0.wireOp",EDGE,"E3.24.0.32");var subQ2=makeQuery(id+"F0.imprint","INTERSECT",VERTEX,{"derivedFrom":[subQ1,subQ0]});Q259=makeQuery(id+"F0.imprint","IMPRINT",FACE,{"disambiguationData":[TD([[makeQuery(id+"F0.imprint","IMPRINT",EDGE,{"disambiguationData":[TD([[subQ2,1.0]])],"derivedFrom":subQ1}),1.0]])]});}
            var Q260;
            {var subQ0=sQuery(id+"F0.wireOp",EDGE,"E3.24.0.75");var subQ1=sQuery(id+"F0.wireOp",EDGE,"E3.24.0.52");var subQ2=makeQuery(id+"F0.imprint","INTERSECT",VERTEX,{"derivedFrom":[subQ1,subQ0]});Q260=makeQuery(id+"F0.imprint","IMPRINT",FACE,{"disambiguationData":[TD([[makeQuery(id+"F0.imprint","IMPRINT",EDGE,{"disambiguationData":[TD([[subQ2,-1.0]])],"derivedFrom":subQ1}),-1.0]])]});}
            var Q261;
            {var subQ7=sQuery(id+"F0.wireOp",EDGE,"E3.24.0.83");Q261=makeQuery(id+"F0.imprint","IMPRINT",FACE,{"disambiguationData":[TD([[makeQuery(id+"F0.imprint","IMPRINT",EDGE,{"derivedFrom":subQ7}),-1.0]])]});}
            var Q262;
            {var subQ0=sQuery(id+"F0.wireOp",EDGE,"E3.20.0.72");var subQ1=sQuery(id+"F0.wireOp",EDGE,"E3.20.0.10");var subQ2=makeQuery(id+"F0.imprint","INTERSECT",VERTEX,{"derivedFrom":[subQ1,subQ0]});Q262=makeQuery(id+"F0.imprint","IMPRINT",FACE,{"disambiguationData":[TD([[makeQuery(id+"F0.imprint","IMPRINT",EDGE,{"disambiguationData":[TD([[subQ2,1.0]])],"derivedFrom":subQ1}),-1.0]])]});}
            var Q263;
            {var subQ10=sQuery(id+"F0.wireOp",EDGE,"E3.22.0.93");Q263=makeQuery(id+"F0.imprint","IMPRINT",FACE,{"disambiguationData":[TD([[makeQuery(id+"F0.imprint","IMPRINT",EDGE,{"derivedFrom":subQ10}),-1.0]])]});}
            var Q264;
            {var subQ3=sQuery(id+"F0.wireOp",EDGE,"E3.23.0.56");Q264=makeQuery(id+"F0.imprint","IMPRINT",FACE,{"disambiguationData":[TD([[makeQuery(id+"F0.imprint","IMPRINT",EDGE,{"derivedFrom":subQ3}),-1.0]])]});}
            var Q265;
            {var subQ7=sQuery(id+"F0.wireOp",EDGE,"E3.22.0.87");Q265=makeQuery(id+"F0.imprint","IMPRINT",FACE,{"disambiguationData":[TD([[makeQuery(id+"F0.imprint","IMPRINT",EDGE,{"derivedFrom":subQ7}),-1.0]])]});}
            var Q266;
            {var subQ0=sQuery(id+"F0.wireOp",EDGE,"E3.24.0.69");var subQ1=sQuery(id+"F0.wireOp",EDGE,"E3.24.0.12");var subQ2=makeQuery(id+"F0.imprint","INTERSECT",VERTEX,{"derivedFrom":[subQ1,subQ0]});Q266=makeQuery(id+"F0.imprint","IMPRINT",FACE,{"disambiguationData":[TD([[makeQuery(id+"F0.imprint","IMPRINT",EDGE,{"disambiguationData":[TD([[subQ2,1.0]])],"derivedFrom":subQ1}),-1.0]])]});}
            var Q267;
            {var subQ0=sQuery(id+"F0.wireOp",EDGE,"E3.24.0.94");var subQ1=sQuery(id+"F0.wireOp",EDGE,"E3.24.0.42");var subQ2=makeQuery(id+"F0.imprint","INTERSECT",VERTEX,{"derivedFrom":[subQ1,subQ0]});Q267=makeQuery(id+"F0.imprint","IMPRINT",FACE,{"disambiguationData":[TD([[makeQuery(id+"F0.imprint","IMPRINT",EDGE,{"disambiguationData":[TD([[subQ2,1.0]])],"derivedFrom":subQ1}),-1.0]])]});}
            var Q268;
            {var subQ0=sQuery(id+"F0.wireOp",EDGE,"E3.23.0.32");var subQ1=sQuery(id+"F0.wireOp",EDGE,"E3.23.0.0");var subQ2=makeQuery(id+"F0.imprint","INTERSECT",VERTEX,{"derivedFrom":[subQ1,subQ0]});Q268=makeQuery(id+"F0.imprint","IMPRINT",FACE,{"disambiguationData":[TD([[makeQuery(id+"F0.imprint","IMPRINT",EDGE,{"disambiguationData":[TD([[subQ2,1.0]])],"derivedFrom":subQ1}),-1.0]])]});}
            var Q269;
            {var subQ5=sQuery(id+"F0.wireOp",EDGE,"E3.24.0.56");Q269=makeQuery(id+"F0.imprint","IMPRINT",FACE,{"disambiguationData":[TD([[makeQuery(id+"F0.imprint","IMPRINT",EDGE,{"derivedFrom":subQ5}),1.0]])]});}
            var Q270;
            {var subQ5=sQuery(id+"F0.wireOp",EDGE,"E3.24.0.53");Q270=makeQuery(id+"F0.imprint","IMPRINT",FACE,{"disambiguationData":[TD([[makeQuery(id+"F0.imprint","IMPRINT",EDGE,{"derivedFrom":subQ5}),-1.0]])]});}
            var Q271;
            {var subQ5=sQuery(id+"F0.wireOp",EDGE,"E3.19.0.93");Q271=makeQuery(id+"F0.imprint","IMPRINT",FACE,{"disambiguationData":[TD([[makeQuery(id+"F0.imprint","IMPRINT",EDGE,{"derivedFrom":subQ5}),1.0]])]});}
            var Q272;
            {var subQ0=sQuery(id+"F0.wireOp",EDGE,"E3.23.0.69");var subQ1=sQuery(id+"F0.wireOp",EDGE,"E3.23.0.12");var subQ2=makeQuery(id+"F0.imprint","INTERSECT",VERTEX,{"derivedFrom":[subQ1,subQ0]});Q272=makeQuery(id+"F0.imprint","IMPRINT",FACE,{"disambiguationData":[TD([[makeQuery(id+"F0.imprint","IMPRINT",EDGE,{"disambiguationData":[TD([[subQ2,1.0]])],"derivedFrom":subQ1}),-1.0]])]});}
            var Q273;
            {var subQ10=sQuery(id+"F0.wireOp",EDGE,"E3.21.0.93");Q273=makeQuery(id+"F0.imprint","IMPRINT",FACE,{"disambiguationData":[TD([[makeQuery(id+"F0.imprint","IMPRINT",EDGE,{"derivedFrom":subQ10}),-1.0]])]});}
            var Q274;
            {var subQ7=sQuery(id+"F0.wireOp",EDGE,"E3.21.0.87");Q274=makeQuery(id+"F0.imprint","IMPRINT",FACE,{"disambiguationData":[TD([[makeQuery(id+"F0.imprint","IMPRINT",EDGE,{"derivedFrom":subQ7}),-1.0]])]});}
            var Q275;
            {var subQ0=sQuery(id+"F0.wireOp",EDGE,"E3.24.0.41");var subQ1=sQuery(id+"F0.wireOp",EDGE,"E3.24.0.6");var subQ2=makeQuery(id+"F0.imprint","INTERSECT",VERTEX,{"derivedFrom":[subQ1,subQ0]});Q275=makeQuery(id+"F0.imprint","IMPRINT",FACE,{"disambiguationData":[TD([[makeQuery(id+"F0.imprint","IMPRINT",EDGE,{"disambiguationData":[TD([[subQ2,1.0]])],"derivedFrom":subQ1}),-1.0]])]});}
            var Q276;
            {var subQ5=sQuery(id+"F0.wireOp",EDGE,"E3.18.0.53");Q276=makeQuery(id+"F0.imprint","IMPRINT",FACE,{"disambiguationData":[TD([[makeQuery(id+"F0.imprint","IMPRINT",EDGE,{"derivedFrom":subQ5}),-1.0]])]});}
            var Q277;
            {var subQ3=sQuery(id+"F0.wireOp",EDGE,"E3.21.0.65");Q277=makeQuery(id+"F0.imprint","IMPRINT",FACE,{"disambiguationData":[TD([[makeQuery(id+"F0.imprint","IMPRINT",EDGE,{"derivedFrom":subQ3}),-1.0]])]});}
            var Q278;
            {var subQ0=sQuery(id+"F0.wireOp",EDGE,"E3.20.0.39");var subQ1=sQuery(id+"F0.wireOp",EDGE,"E3.20.0.17");var subQ2=makeQuery(id+"F0.imprint","INTERSECT",VERTEX,{"derivedFrom":[subQ1,subQ0]});Q278=makeQuery(id+"F0.imprint","IMPRINT",FACE,{"disambiguationData":[TD([[makeQuery(id+"F0.imprint","IMPRINT",EDGE,{"disambiguationData":[TD([[subQ2,-1.0]])],"derivedFrom":subQ1}),-1.0]])]});}
            var Q279;
            {var subQ10=sQuery(id+"F0.wireOp",EDGE,"E3.24.0.93");Q279=makeQuery(id+"F0.imprint","IMPRINT",FACE,{"disambiguationData":[TD([[makeQuery(id+"F0.imprint","IMPRINT",EDGE,{"derivedFrom":subQ10}),-1.0]])]});}
            var Q280;
            {var subQ0=sQuery(id+"F0.wireOp",EDGE,"E3.23.0.57");Q280=makeQuery(id+"F0.imprint","IMPRINT",FACE,{"disambiguationData":[TD([[makeQuery(id+"F0.imprint","IMPRINT",EDGE,{"derivedFrom":subQ0}),-1.0]])]});}
            var Q281;
            {var subQ3=sQuery(id+"F0.wireOp",EDGE,"E3.22.0.65");Q281=makeQuery(id+"F0.imprint","IMPRINT",FACE,{"disambiguationData":[TD([[makeQuery(id+"F0.imprint","IMPRINT",EDGE,{"derivedFrom":subQ3}),-1.0]])]});}
            var Q282;
            {var subQ0=sQuery(id+"F0.wireOp",EDGE,"E3.21.0.94");var subQ1=sQuery(id+"F0.wireOp",EDGE,"E3.21.0.42");var subQ2=makeQuery(id+"F0.imprint","INTERSECT",VERTEX,{"derivedFrom":[subQ1,subQ0]});Q282=makeQuery(id+"F0.imprint","IMPRINT",FACE,{"disambiguationData":[TD([[makeQuery(id+"F0.imprint","IMPRINT",EDGE,{"disambiguationData":[TD([[subQ2,1.0]])],"derivedFrom":subQ1}),-1.0]])]});}
            var Q283;
            {var subQ3=sQuery(id+"F0.wireOp",EDGE,"E3.20.0.56");Q283=makeQuery(id+"F0.imprint","IMPRINT",FACE,{"disambiguationData":[TD([[makeQuery(id+"F0.imprint","IMPRINT",EDGE,{"derivedFrom":subQ3}),-1.0]])]});}
            var Q284;
            {var subQ0=sQuery(id+"F0.wireOp",EDGE,"E3.18.0.41");var subQ1=sQuery(id+"F0.wireOp",EDGE,"E3.18.0.6");var subQ2=makeQuery(id+"F0.imprint","INTERSECT",VERTEX,{"derivedFrom":[subQ1,subQ0]});Q284=makeQuery(id+"F0.imprint","IMPRINT",FACE,{"disambiguationData":[TD([[makeQuery(id+"F0.imprint","IMPRINT",EDGE,{"disambiguationData":[TD([[subQ2,1.0]])],"derivedFrom":subQ1}),-1.0]])]});}
            var Q285;
            {var subQ0=sQuery(id+"F0.wireOp",EDGE,"E3.23.0.68");var subQ1=sQuery(id+"F0.wireOp",EDGE,"E3.23.0.11");var subQ2=makeQuery(id+"F0.imprint","INTERSECT",VERTEX,{"derivedFrom":[subQ1,subQ0]});Q285=makeQuery(id+"F0.imprint","IMPRINT",FACE,{"disambiguationData":[TD([[makeQuery(id+"F0.imprint","IMPRINT",EDGE,{"disambiguationData":[TD([[subQ2,1.0]])],"derivedFrom":subQ1}),-1.0]])]});}
            var Q286;
            {var subQ0=sQuery(id+"F0.wireOp",EDGE,"E3.18.0.57");Q286=makeQuery(id+"F0.imprint","IMPRINT",FACE,{"disambiguationData":[TD([[makeQuery(id+"F0.imprint","IMPRINT",EDGE,{"derivedFrom":subQ0}),-1.0]])]});}
            var Q287;
            {var subQ0=sQuery(id+"F0.wireOp",EDGE,"E3.24.0.41");var subQ1=sQuery(id+"F0.wireOp",EDGE,"E3.24.0.13");var subQ2=makeQuery(id+"F0.imprint","INTERSECT",VERTEX,{"derivedFrom":[subQ1,subQ0]});Q287=makeQuery(id+"F0.imprint","IMPRINT",FACE,{"disambiguationData":[TD([[makeQuery(id+"F0.imprint","IMPRINT",EDGE,{"disambiguationData":[TD([[subQ2,-1.0]])],"derivedFrom":subQ1}),-1.0]])]});}
            var Q288;
            {var subQ3=sQuery(id+"F0.wireOp",EDGE,"E3.19.0.56");Q288=makeQuery(id+"F0.imprint","IMPRINT",FACE,{"disambiguationData":[TD([[makeQuery(id+"F0.imprint","IMPRINT",EDGE,{"derivedFrom":subQ3}),-1.0]])]});}
            var Q289;
            {var subQ3=sQuery(id+"F0.wireOp",EDGE,"E3.18.0.53");Q289=makeQuery(id+"F0.imprint","IMPRINT",FACE,{"disambiguationData":[TD([[makeQuery(id+"F0.imprint","IMPRINT",EDGE,{"derivedFrom":subQ3}),1.0]])]});}
            var Q290;
            {var subQ0=sQuery(id+"F0.wireOp",EDGE,"E3.19.0.116");Q290=makeQuery(id+"F0.imprint","IMPRINT",FACE,{"disambiguationData":[TD([[makeQuery(id+"F0.imprint","IMPRINT",EDGE,{"derivedFrom":subQ0}),-1.0]])]});}
            var Q291;
            {var subQ0=sQuery(id+"F0.wireOp",EDGE,"E3.18.0.116");Q291=makeQuery(id+"F0.imprint","IMPRINT",FACE,{"disambiguationData":[TD([[makeQuery(id+"F0.imprint","IMPRINT",EDGE,{"derivedFrom":subQ0}),-1.0]])]});}
            var Q292;
            {var subQ7=sQuery(id+"F0.wireOp",EDGE,"E3.18.0.87");Q292=makeQuery(id+"F0.imprint","IMPRINT",FACE,{"disambiguationData":[TD([[makeQuery(id+"F0.imprint","IMPRINT",EDGE,{"derivedFrom":subQ7}),-1.0]])]});}
            var Q293;
            {var subQ0=sQuery(id+"F0.wireOp",EDGE,"E3.19.0.69");var subQ1=sQuery(id+"F0.wireOp",EDGE,"E3.19.0.12");var subQ2=makeQuery(id+"F0.imprint","INTERSECT",VERTEX,{"derivedFrom":[subQ1,subQ0]});Q293=makeQuery(id+"F0.imprint","IMPRINT",FACE,{"disambiguationData":[TD([[makeQuery(id+"F0.imprint","IMPRINT",EDGE,{"disambiguationData":[TD([[subQ2,1.0]])],"derivedFrom":subQ1}),-1.0]])]});}
            var Q294;
            {var subQ3=sQuery(id+"F0.wireOp",EDGE,"E3.17.0.53");Q294=makeQuery(id+"F0.imprint","IMPRINT",FACE,{"disambiguationData":[TD([[makeQuery(id+"F0.imprint","IMPRINT",EDGE,{"derivedFrom":subQ3}),1.0]])]});}
            var Q295;
            {var subQ0=sQuery(id+"F0.wireOp",EDGE,"E3.17.0.57");Q295=makeQuery(id+"F0.imprint","IMPRINT",FACE,{"disambiguationData":[TD([[makeQuery(id+"F0.imprint","IMPRINT",EDGE,{"derivedFrom":subQ0}),-1.0]])]});}
            var Q296;
            {var subQ3=sQuery(id+"F0.wireOp",EDGE,"E3.22.0.103");Q296=makeQuery(id+"F0.imprint","IMPRINT",FACE,{"disambiguationData":[TD([[makeQuery(id+"F0.imprint","IMPRINT",EDGE,{"derivedFrom":subQ3}),1.0]])]});}
            var Q297;
            {var subQ0=sQuery(id+"F0.wireOp",EDGE,"E3.20.0.94");var subQ1=sQuery(id+"F0.wireOp",EDGE,"E3.20.0.42");var subQ2=makeQuery(id+"F0.imprint","INTERSECT",VERTEX,{"derivedFrom":[subQ1,subQ0]});Q297=makeQuery(id+"F0.imprint","IMPRINT",FACE,{"disambiguationData":[TD([[makeQuery(id+"F0.imprint","IMPRINT",EDGE,{"disambiguationData":[TD([[subQ2,1.0]])],"derivedFrom":subQ1}),-1.0]])]});}
            var Q298;
            {var subQ0=sQuery(id+"F0.wireOp",EDGE,"E3.21.0.68");var subQ1=sQuery(id+"F0.wireOp",EDGE,"E3.21.0.11");var subQ2=makeQuery(id+"F0.imprint","INTERSECT",VERTEX,{"derivedFrom":[subQ1,subQ0]});Q298=makeQuery(id+"F0.imprint","IMPRINT",FACE,{"disambiguationData":[TD([[makeQuery(id+"F0.imprint","IMPRINT",EDGE,{"disambiguationData":[TD([[subQ2,1.0]])],"derivedFrom":subQ1}),-1.0]])]});}
            var Q299;
            {var subQ5=sQuery(id+"F0.wireOp",EDGE,"E3.21.0.93");Q299=makeQuery(id+"F0.imprint","IMPRINT",FACE,{"disambiguationData":[TD([[makeQuery(id+"F0.imprint","IMPRINT",EDGE,{"derivedFrom":subQ5}),1.0]])]});}
            var Q300;
            {var subQ3=sQuery(id+"F0.wireOp",EDGE,"E3.22.0.7");Q300=makeQuery(id+"F0.imprint","IMPRINT",FACE,{"disambiguationData":[TD([[makeQuery(id+"F0.imprint","IMPRINT",EDGE,{"derivedFrom":subQ3}),1.0]])]});}
            var Q301;
            {var subQ0=sQuery(id+"F0.wireOp",EDGE,"E3.22.0.68");var subQ1=sQuery(id+"F0.wireOp",EDGE,"E3.22.0.11");var subQ2=makeQuery(id+"F0.imprint","INTERSECT",VERTEX,{"derivedFrom":[subQ1,subQ0]});Q301=makeQuery(id+"F0.imprint","IMPRINT",FACE,{"disambiguationData":[TD([[makeQuery(id+"F0.imprint","IMPRINT",EDGE,{"disambiguationData":[TD([[subQ2,1.0]])],"derivedFrom":subQ1}),-1.0]])]});}
            var Q302;
            {var subQ0=sQuery(id+"F0.wireOp",EDGE,"E3.23.0.42");var subQ1=sQuery(id+"F0.wireOp",EDGE,"E3.23.0.16");var subQ2=makeQuery(id+"F0.imprint","INTERSECT",VERTEX,{"derivedFrom":[subQ1,subQ0]});Q302=makeQuery(id+"F0.imprint","IMPRINT",FACE,{"disambiguationData":[TD([[makeQuery(id+"F0.imprint","IMPRINT",EDGE,{"disambiguationData":[TD([[subQ2,-1.0]])],"derivedFrom":subQ1}),-1.0]])]});}
            var Q303;
            {var subQ0=sQuery(id+"F0.wireOp",EDGE,"E3.23.0.41");var subQ1=sQuery(id+"F0.wireOp",EDGE,"E3.23.0.13");var subQ2=makeQuery(id+"F0.imprint","INTERSECT",VERTEX,{"derivedFrom":[subQ1,subQ0]});Q303=makeQuery(id+"F0.imprint","IMPRINT",FACE,{"disambiguationData":[TD([[makeQuery(id+"F0.imprint","IMPRINT",EDGE,{"disambiguationData":[TD([[subQ2,-1.0]])],"derivedFrom":subQ1}),-1.0]])]});}
            var Q304;
            {var subQ0=sQuery(id+"F0.wireOp",EDGE,"E3.18.0.64");Q304=makeQuery(id+"F0.imprint","IMPRINT",FACE,{"disambiguationData":[TD([[makeQuery(id+"F0.imprint","IMPRINT",EDGE,{"derivedFrom":subQ0}),-1.0]])]});}
            var Q305;
            {var subQ3=sQuery(id+"F0.wireOp",EDGE,"E3.19.0.86");Q305=makeQuery(id+"F0.imprint","IMPRINT",FACE,{"disambiguationData":[TD([[makeQuery(id+"F0.imprint","IMPRINT",EDGE,{"derivedFrom":subQ3}),1.0]])]});}
            var Q306;
            {var subQ0=sQuery(id+"F0.wireOp",EDGE,"E3.17.0.96");var subQ1=sQuery(id+"F0.wireOp",EDGE,"E3.17.0.43");var subQ2=makeQuery(id+"F0.imprint","INTERSECT",VERTEX,{"derivedFrom":[subQ1,subQ0]});Q306=makeQuery(id+"F0.imprint","IMPRINT",FACE,{"disambiguationData":[TD([[makeQuery(id+"F0.imprint","IMPRINT",EDGE,{"disambiguationData":[TD([[subQ2,1.0]])],"derivedFrom":subQ1}),-1.0]])]});}
            var Q307;
            {var subQ0=sQuery(id+"F0.wireOp",EDGE,"E3.24.0.19");Q307=makeQuery(id+"F0.imprint","IMPRINT",FACE,{"disambiguationData":[TD([[makeQuery(id+"F0.imprint","IMPRINT",EDGE,{"derivedFrom":subQ0}),-1.0]])]});}
            var Q308;
            {var subQ0=sQuery(id+"F0.wireOp",EDGE,"E3.19.0.63");Q308=makeQuery(id+"F0.imprint","IMPRINT",FACE,{"disambiguationData":[TD([[makeQuery(id+"F0.imprint","IMPRINT",EDGE,{"derivedFrom":subQ0}),-1.0]])]});}
            var Q309;
            {var subQ0=sQuery(id+"F0.wireOp",EDGE,"E3.18.0.96");var subQ1=sQuery(id+"F0.wireOp",EDGE,"E3.18.0.43");var subQ2=makeQuery(id+"F0.imprint","INTERSECT",VERTEX,{"derivedFrom":[subQ1,subQ0]});Q309=makeQuery(id+"F0.imprint","IMPRINT",FACE,{"disambiguationData":[TD([[makeQuery(id+"F0.imprint","IMPRINT",EDGE,{"disambiguationData":[TD([[subQ2,1.0]])],"derivedFrom":subQ1}),-1.0]])]});}
            var Q310;
            {var subQ0=sQuery(id+"F0.wireOp",EDGE,"E3.20.0.89");Q310=makeQuery(id+"F0.imprint","IMPRINT",FACE,{"disambiguationData":[TD([[makeQuery(id+"F0.imprint","IMPRINT",EDGE,{"derivedFrom":subQ0}),-1.0]])]});}
            var Q311;
            {var subQ7=sQuery(id+"F0.wireOp",EDGE,"E3.19.0.54");Q311=makeQuery(id+"F0.imprint","IMPRINT",FACE,{"disambiguationData":[TD([[makeQuery(id+"F0.imprint","IMPRINT",EDGE,{"derivedFrom":subQ7}),-1.0]])]});}
            var Q312;
            {var subQ7=sQuery(id+"F0.wireOp",EDGE,"E3.22.0.83");Q312=makeQuery(id+"F0.imprint","IMPRINT",FACE,{"disambiguationData":[TD([[makeQuery(id+"F0.imprint","IMPRINT",EDGE,{"derivedFrom":subQ7}),-1.0]])]});}
            var Q313;
            {var subQ3=sQuery(id+"F0.wireOp",EDGE,"E3.24.0.31");Q313=makeQuery(id+"F0.imprint","IMPRINT",FACE,{"disambiguationData":[TD([[makeQuery(id+"F0.imprint","IMPRINT",EDGE,{"derivedFrom":subQ3}),-1.0]])]});}
            var Q314;
            {var subQ0=sQuery(id+"F0.wireOp",EDGE,"E3.23.0.39");var subQ1=sQuery(id+"F0.wireOp",EDGE,"E3.23.0.17");var subQ2=makeQuery(id+"F0.imprint","INTERSECT",VERTEX,{"derivedFrom":[subQ1,subQ0]});Q314=makeQuery(id+"F0.imprint","IMPRINT",FACE,{"disambiguationData":[TD([[makeQuery(id+"F0.imprint","IMPRINT",EDGE,{"disambiguationData":[TD([[subQ2,-1.0]])],"derivedFrom":subQ1}),-1.0]])]});}
            var Q315;
            {var subQ7=sQuery(id+"F0.wireOp",EDGE,"E3.20.0.83");Q315=makeQuery(id+"F0.imprint","IMPRINT",FACE,{"disambiguationData":[TD([[makeQuery(id+"F0.imprint","IMPRINT",EDGE,{"derivedFrom":subQ7}),-1.0]])]});}
            var Q316;
            {var subQ0=sQuery(id+"F0.wireOp",EDGE,"E3.19.0.64");Q316=makeQuery(id+"F0.imprint","IMPRINT",FACE,{"disambiguationData":[TD([[makeQuery(id+"F0.imprint","IMPRINT",EDGE,{"derivedFrom":subQ0}),-1.0]])]});}
            var Q317;
            {var subQ0=sQuery(id+"F0.wireOp",EDGE,"E3.20.0.35");var subQ1=sQuery(id+"F0.wireOp",EDGE,"E3.20.0.32");var subQ2=makeQuery(id+"F0.imprint","INTERSECT",VERTEX,{"derivedFrom":[subQ1,subQ0]});Q317=makeQuery(id+"F0.imprint","IMPRINT",FACE,{"disambiguationData":[TD([[makeQuery(id+"F0.imprint","IMPRINT",EDGE,{"disambiguationData":[TD([[subQ2,1.0]])],"derivedFrom":subQ1}),1.0]])]});}
            var Q318;
            {var subQ5=sQuery(id+"F0.wireOp",EDGE,"E3.19.0.53");Q318=makeQuery(id+"F0.imprint","IMPRINT",FACE,{"disambiguationData":[TD([[makeQuery(id+"F0.imprint","IMPRINT",EDGE,{"derivedFrom":subQ5}),-1.0]])]});}
            var Q319;
            {var subQ0=sQuery(id+"F0.wireOp",EDGE,"E3.20.0.8");var subQ1=sQuery(id+"F0.wireOp",EDGE,"E3.20.0.6");var subQ2=makeQuery(id+"F0.imprint","INTERSECT",VERTEX,{"derivedFrom":[subQ1,subQ0]});Q319=makeQuery(id+"F0.imprint","IMPRINT",FACE,{"disambiguationData":[TD([[makeQuery(id+"F0.imprint","IMPRINT",EDGE,{"disambiguationData":[TD([[subQ2,-1.0]])],"derivedFrom":subQ1}),-1.0]])]});}
            var Q320;
            {var subQ5=sQuery(id+"F0.wireOp",EDGE,"E3.20.0.53");Q320=makeQuery(id+"F0.imprint","IMPRINT",FACE,{"disambiguationData":[TD([[makeQuery(id+"F0.imprint","IMPRINT",EDGE,{"derivedFrom":subQ5}),-1.0]])]});}
            var Q321;
            {var subQ0=sQuery(id+"F0.wireOp",EDGE,"E3.21.0.68");var subQ1=sQuery(id+"F0.wireOp",EDGE,"E3.21.0.8");var subQ2=makeQuery(id+"F0.imprint","INTERSECT",VERTEX,{"derivedFrom":[subQ1,subQ0]});Q321=makeQuery(id+"F0.imprint","IMPRINT",FACE,{"disambiguationData":[TD([[makeQuery(id+"F0.imprint","IMPRINT",EDGE,{"disambiguationData":[TD([[subQ2,1.0]])],"derivedFrom":subQ1}),-1.0]])]});}
            var Q322;
            {var subQ5=sQuery(id+"F0.wireOp",EDGE,"E3.20.0.22");Q322=makeQuery(id+"F0.imprint","IMPRINT",FACE,{"disambiguationData":[TD([[makeQuery(id+"F0.imprint","IMPRINT",EDGE,{"derivedFrom":subQ5}),-1.0]])]});}
            var Q323;
            {var subQ0=sQuery(id+"F0.wireOp",EDGE,"E3.21.0.35");var subQ1=sQuery(id+"F0.wireOp",EDGE,"E3.21.0.32");var subQ2=makeQuery(id+"F0.imprint","INTERSECT",VERTEX,{"derivedFrom":[subQ1,subQ0]});Q323=makeQuery(id+"F0.imprint","IMPRINT",FACE,{"disambiguationData":[TD([[makeQuery(id+"F0.imprint","IMPRINT",EDGE,{"disambiguationData":[TD([[subQ2,1.0]])],"derivedFrom":subQ1}),1.0]])]});}
            var Q324;
            {var subQ0=sQuery(id+"F0.wireOp",EDGE,"E3.22.0.91");var subQ1=sQuery(id+"F0.wireOp",EDGE,"E3.22.0.49");var subQ2=makeQuery(id+"F0.imprint","INTERSECT",VERTEX,{"derivedFrom":[subQ1,subQ0]});Q324=makeQuery(id+"F0.imprint","IMPRINT",FACE,{"disambiguationData":[TD([[makeQuery(id+"F0.imprint","IMPRINT",EDGE,{"disambiguationData":[TD([[subQ2,-1.0]])],"derivedFrom":subQ1}),-1.0]])]});}
            var Q325;
            {var subQ3=sQuery(id+"F0.wireOp",EDGE,"E3.22.0.31");Q325=makeQuery(id+"F0.imprint","IMPRINT",FACE,{"disambiguationData":[TD([[makeQuery(id+"F0.imprint","IMPRINT",EDGE,{"derivedFrom":subQ3}),-1.0]])]});}
            var Q326;
            {var subQ5=sQuery(id+"F0.wireOp",EDGE,"E3.22.0.82");Q326=makeQuery(id+"F0.imprint","IMPRINT",FACE,{"disambiguationData":[TD([[makeQuery(id+"F0.imprint","IMPRINT",EDGE,{"derivedFrom":subQ5}),-1.0]])]});}
            var Q327;
            {var subQ7=sQuery(id+"F0.wireOp",EDGE,"E3.21.0.83");Q327=makeQuery(id+"F0.imprint","IMPRINT",FACE,{"disambiguationData":[TD([[makeQuery(id+"F0.imprint","IMPRINT",EDGE,{"derivedFrom":subQ7}),-1.0]])]});}
            var Q328;
            {var subQ5=sQuery(id+"F0.wireOp",EDGE,"E3.23.0.57");Q328=makeQuery(id+"F0.imprint","IMPRINT",FACE,{"disambiguationData":[TD([[makeQuery(id+"F0.imprint","IMPRINT",EDGE,{"derivedFrom":subQ5}),1.0]])]});}
            var Q329;
            {var subQ3=sQuery(id+"F0.wireOp",EDGE,"E3.23.0.65");Q329=makeQuery(id+"F0.imprint","IMPRINT",FACE,{"disambiguationData":[TD([[makeQuery(id+"F0.imprint","IMPRINT",EDGE,{"derivedFrom":subQ3}),-1.0]])]});}
            var Q330;
            {var subQ0=sQuery(id+"F0.wireOp",EDGE,"E3.22.0.39");var subQ1=sQuery(id+"F0.wireOp",EDGE,"E3.22.0.17");var subQ2=makeQuery(id+"F0.imprint","INTERSECT",VERTEX,{"derivedFrom":[subQ1,subQ0]});Q330=makeQuery(id+"F0.imprint","IMPRINT",FACE,{"disambiguationData":[TD([[makeQuery(id+"F0.imprint","IMPRINT",EDGE,{"disambiguationData":[TD([[subQ2,-1.0]])],"derivedFrom":subQ1}),-1.0]])]});}
            var Q331;
            {var subQ3=sQuery(id+"F0.wireOp",EDGE,"E3.4.0.84");Q331=makeQuery(id+"F0.imprint","IMPRINT",FACE,{"disambiguationData":[TD([[makeQuery(id+"F0.imprint","IMPRINT",EDGE,{"derivedFrom":subQ3}),1.0]])]});}
            var Q332;
            {var subQ3=sQuery(id+"F0.wireOp",EDGE,"E3.6.0.56");Q332=makeQuery(id+"F0.imprint","IMPRINT",FACE,{"disambiguationData":[TD([[makeQuery(id+"F0.imprint","IMPRINT",EDGE,{"derivedFrom":subQ3}),-1.0]])]});}
            var Q333;
            {var subQ0=sQuery(id+"F0.wireOp",EDGE,"E3.7.0.94");var subQ1=sQuery(id+"F0.wireOp",EDGE,"E3.7.0.42");var subQ2=makeQuery(id+"F0.imprint","INTERSECT",VERTEX,{"derivedFrom":[subQ1,subQ0]});Q333=makeQuery(id+"F0.imprint","IMPRINT",FACE,{"disambiguationData":[TD([[makeQuery(id+"F0.imprint","IMPRINT",EDGE,{"disambiguationData":[TD([[subQ2,1.0]])],"derivedFrom":subQ1}),-1.0]])]});}
            var Q334;
            {var subQ0=sQuery(id+"F0.wireOp",EDGE,"E3.7.0.69");var subQ1=sQuery(id+"F0.wireOp",EDGE,"E3.7.0.12");var subQ2=makeQuery(id+"F0.imprint","INTERSECT",VERTEX,{"derivedFrom":[subQ1,subQ0]});Q334=makeQuery(id+"F0.imprint","IMPRINT",FACE,{"disambiguationData":[TD([[makeQuery(id+"F0.imprint","IMPRINT",EDGE,{"disambiguationData":[TD([[subQ2,1.0]])],"derivedFrom":subQ1}),-1.0]])]});}
            var Q335;
            {var subQ3=sQuery(id+"F0.wireOp",EDGE,"E3.8.0.103");Q335=makeQuery(id+"F0.imprint","IMPRINT",FACE,{"disambiguationData":[TD([[makeQuery(id+"F0.imprint","IMPRINT",EDGE,{"derivedFrom":subQ3}),1.0]])]});}
            var Q336;
            {var subQ0=sQuery(id+"F0.wireOp",EDGE,"E3.10.0.41");var subQ1=sQuery(id+"F0.wireOp",EDGE,"E3.10.0.13");var subQ2=makeQuery(id+"F0.imprint","INTERSECT",VERTEX,{"derivedFrom":[subQ1,subQ0]});Q336=makeQuery(id+"F0.imprint","IMPRINT",FACE,{"disambiguationData":[TD([[makeQuery(id+"F0.imprint","IMPRINT",EDGE,{"disambiguationData":[TD([[subQ2,-1.0]])],"derivedFrom":subQ1}),-1.0]])]});}
            var Q337;
            {var subQ0=sQuery(id+"F0.wireOp",EDGE,"E3.9.0.97");var subQ1=sQuery(id+"F0.wireOp",EDGE,"E3.9.0.44");var subQ2=makeQuery(id+"F0.imprint","INTERSECT",VERTEX,{"derivedFrom":[subQ1,subQ0]});Q337=makeQuery(id+"F0.imprint","IMPRINT",FACE,{"disambiguationData":[TD([[makeQuery(id+"F0.imprint","IMPRINT",EDGE,{"disambiguationData":[TD([[subQ2,1.0]])],"derivedFrom":subQ1}),-1.0]])]});}
            var Q338;
            {var subQ0=sQuery(id+"F0.wireOp",EDGE,"E3.13.0.100");var subQ1=sQuery(id+"F0.wireOp",EDGE,"E3.13.0.52");var subQ2=makeQuery(id+"F0.imprint","INTERSECT",VERTEX,{"derivedFrom":[subQ1,subQ0]});Q338=makeQuery(id+"F0.imprint","IMPRINT",FACE,{"disambiguationData":[TD([[makeQuery(id+"F0.imprint","IMPRINT",EDGE,{"disambiguationData":[TD([[subQ2,1.0]])],"derivedFrom":subQ1}),-1.0]])]});}
            var Q339;
            {var subQ0=sQuery(id+"F0.wireOp",EDGE,"E3.15.0.35");var subQ1=sQuery(id+"F0.wireOp",EDGE,"E3.15.0.32");var subQ2=makeQuery(id+"F0.imprint","INTERSECT",VERTEX,{"derivedFrom":[subQ1,subQ0]});Q339=makeQuery(id+"F0.imprint","IMPRINT",FACE,{"disambiguationData":[TD([[makeQuery(id+"F0.imprint","IMPRINT",EDGE,{"disambiguationData":[TD([[subQ2,1.0]])],"derivedFrom":subQ1}),1.0]])]});}
            var Q340;
            {var subQ0=sQuery(id+"F0.wireOp",EDGE,"E3.16.0.68");var subQ1=sQuery(id+"F0.wireOp",EDGE,"E3.16.0.8");var subQ2=makeQuery(id+"F0.imprint","INTERSECT",VERTEX,{"derivedFrom":[subQ1,subQ0]});Q340=makeQuery(id+"F0.imprint","IMPRINT",FACE,{"disambiguationData":[TD([[makeQuery(id+"F0.imprint","IMPRINT",EDGE,{"disambiguationData":[TD([[subQ2,1.0]])],"derivedFrom":subQ1}),-1.0]])]});}
            var Q341;
            {var subQ0=sQuery(id+"F0.wireOp",EDGE,"E2.7.0.1");var subQ1=sQuery(id+"F0.wireOp",EDGE,"E2.7.0.0");var subQ2=makeQuery(id+"F0.imprint","INTERSECT",VERTEX,{"derivedFrom":[subQ1,subQ0]});Q341=makeQuery(id+"F0.imprint","IMPRINT",FACE,{"disambiguationData":[TD([[makeQuery(id+"F0.imprint","IMPRINT",EDGE,{"disambiguationData":[TD([[subQ2,1.0]])],"derivedFrom":subQ1}),1.0]])]});}
            var Q342;
            {var subQ0=sQuery(id+"F0.wireOp",EDGE,"E3.3.0.37");var subQ5=sQuery(id+"F0.wireOp",EDGE,"E3.3.0.9");var subQ7=makeQuery(id+"F0.imprint","INTERSECT",VERTEX,{"derivedFrom":[subQ5,subQ0]});Q342=makeQuery(id+"F0.imprint","IMPRINT",FACE,{"disambiguationData":[TD([[makeQuery(id+"F0.imprint","IMPRINT",EDGE,{"disambiguationData":[TD([[subQ7,1.0]])],"derivedFrom":subQ5}),1.0]])]});}
            var Q343;
            {var subQ3=sQuery(id+"F0.wireOp",EDGE,"E3.2.0.65");Q343=makeQuery(id+"F0.imprint","IMPRINT",FACE,{"disambiguationData":[TD([[makeQuery(id+"F0.imprint","IMPRINT",EDGE,{"derivedFrom":subQ3}),-1.0]])]});}
            var Q344;
            {var subQ0=sQuery(id+"F0.wireOp",EDGE,"E3.11.0.51");var subQ1=sQuery(id+"F0.wireOp",EDGE,"E3.11.0.10");var subQ2=makeQuery(id+"F0.imprint","INTERSECT",VERTEX,{"derivedFrom":[subQ1,subQ0]});Q344=makeQuery(id+"F0.imprint","IMPRINT",FACE,{"disambiguationData":[TD([[makeQuery(id+"F0.imprint","IMPRINT",EDGE,{"disambiguationData":[TD([[subQ2,-1.0]])],"derivedFrom":subQ1}),1.0]])]});}
            var Q345;
            {var subQ0=sQuery(id+"F0.wireOp",EDGE,"E3.12.0.71");var subQ1=sQuery(id+"F0.wireOp",EDGE,"E3.12.0.9");var subQ2=makeQuery(id+"F0.imprint","INTERSECT",VERTEX,{"derivedFrom":[subQ1,subQ0]});Q345=makeQuery(id+"F0.imprint","IMPRINT",FACE,{"disambiguationData":[TD([[makeQuery(id+"F0.imprint","IMPRINT",EDGE,{"disambiguationData":[TD([[subQ2,1.0]])],"derivedFrom":subQ1}),-1.0]])]});}
            var Q346;
            {var subQ0=sQuery(id+"F0.wireOp",EDGE,"E3.13.0.64");Q346=makeQuery(id+"F0.imprint","IMPRINT",FACE,{"disambiguationData":[TD([[makeQuery(id+"F0.imprint","IMPRINT",EDGE,{"derivedFrom":subQ0}),-1.0]])]});}
            var Q347;
            {var subQ7=sQuery(id+"F0.wireOp",EDGE,"E3.12.0.54");Q347=makeQuery(id+"F0.imprint","IMPRINT",FACE,{"disambiguationData":[TD([[makeQuery(id+"F0.imprint","IMPRINT",EDGE,{"derivedFrom":subQ7}),-1.0]])]});}
            var Q348;
            {var subQ0=sQuery(id+"F0.wireOp",EDGE,"E3.1.0.37");var subQ5=sQuery(id+"F0.wireOp",EDGE,"E3.1.0.9");var subQ7=makeQuery(id+"F0.imprint","INTERSECT",VERTEX,{"derivedFrom":[subQ5,subQ0]});Q348=makeQuery(id+"F0.imprint","IMPRINT",FACE,{"disambiguationData":[TD([[makeQuery(id+"F0.imprint","IMPRINT",EDGE,{"disambiguationData":[TD([[subQ7,1.0]])],"derivedFrom":subQ5}),1.0]])]});}
            var Q349;
            {var subQ3=sQuery(id+"F0.wireOp",EDGE,"E3.2.0.84");Q349=makeQuery(id+"F0.imprint","IMPRINT",FACE,{"disambiguationData":[TD([[makeQuery(id+"F0.imprint","IMPRINT",EDGE,{"derivedFrom":subQ3}),1.0]])]});}
            var Q350;
            {var subQ0=sQuery(id+"F0.wireOp",EDGE,"E3.3.0.40");var subQ1=sQuery(id+"F0.wireOp",EDGE,"E3.3.0.18");var subQ2=makeQuery(id+"F0.imprint","INTERSECT",VERTEX,{"derivedFrom":[subQ1,subQ0]});Q350=makeQuery(id+"F0.imprint","IMPRINT",FACE,{"disambiguationData":[TD([[makeQuery(id+"F0.imprint","IMPRINT",EDGE,{"disambiguationData":[TD([[subQ2,-1.0]])],"derivedFrom":subQ1}),-1.0]])]});}
            var Q351;
            {var subQ7=sQuery(id+"F0.wireOp",EDGE,"E3.3.0.87");Q351=makeQuery(id+"F0.imprint","IMPRINT",FACE,{"disambiguationData":[TD([[makeQuery(id+"F0.imprint","IMPRINT",EDGE,{"derivedFrom":subQ7}),-1.0]])]});}
            var Q352;
            {var subQ0=sQuery(id+"F0.wireOp",EDGE,"E3.4.0.116");Q352=makeQuery(id+"F0.imprint","IMPRINT",FACE,{"disambiguationData":[TD([[makeQuery(id+"F0.imprint","IMPRINT",EDGE,{"derivedFrom":subQ0}),-1.0]])]});}
            var Q353;
            {var subQ0=sQuery(id+"F0.wireOp",EDGE,"E3.14.0.68");var subQ1=sQuery(id+"F0.wireOp",EDGE,"E3.14.0.8");var subQ2=makeQuery(id+"F0.imprint","INTERSECT",VERTEX,{"derivedFrom":[subQ1,subQ0]});Q353=makeQuery(id+"F0.imprint","IMPRINT",FACE,{"disambiguationData":[TD([[makeQuery(id+"F0.imprint","IMPRINT",EDGE,{"disambiguationData":[TD([[subQ2,1.0]])],"derivedFrom":subQ1}),-1.0]])]});}
            var Q354;
            {var subQ0=sQuery(id+"F0.wireOp",EDGE,"E3.17.0.37");var subQ5=sQuery(id+"F0.wireOp",EDGE,"E3.17.0.9");var subQ7=makeQuery(id+"F0.imprint","INTERSECT",VERTEX,{"derivedFrom":[subQ5,subQ0]});Q354=makeQuery(id+"F0.imprint","IMPRINT",FACE,{"disambiguationData":[TD([[makeQuery(id+"F0.imprint","IMPRINT",EDGE,{"disambiguationData":[TD([[subQ7,1.0]])],"derivedFrom":subQ5}),1.0]])]});}
            var Q355;
            {var subQ3=sQuery(id+"F0.wireOp",EDGE,"E3.15.0.31");Q355=makeQuery(id+"F0.imprint","IMPRINT",FACE,{"disambiguationData":[TD([[makeQuery(id+"F0.imprint","IMPRINT",EDGE,{"derivedFrom":subQ3}),-1.0]])]});}
            var Q356;
            {var subQ7=sQuery(id+"F0.wireOp",EDGE,"E3.13.0.83");Q356=makeQuery(id+"F0.imprint","IMPRINT",FACE,{"disambiguationData":[TD([[makeQuery(id+"F0.imprint","IMPRINT",EDGE,{"derivedFrom":subQ7}),-1.0]])]});}
            var Q357;
            {var subQ0=sQuery(id+"F0.wireOp",EDGE,"E3.5.0.94");var subQ1=sQuery(id+"F0.wireOp",EDGE,"E3.5.0.42");var subQ2=makeQuery(id+"F0.imprint","INTERSECT",VERTEX,{"derivedFrom":[subQ1,subQ0]});Q357=makeQuery(id+"F0.imprint","IMPRINT",FACE,{"disambiguationData":[TD([[makeQuery(id+"F0.imprint","IMPRINT",EDGE,{"disambiguationData":[TD([[subQ2,1.0]])],"derivedFrom":subQ1}),-1.0]])]});}
            var Q358;
            {var subQ3=sQuery(id+"F0.wireOp",EDGE,"E3.5.0.66");Q358=makeQuery(id+"F0.imprint","IMPRINT",FACE,{"disambiguationData":[TD([[makeQuery(id+"F0.imprint","IMPRINT",EDGE,{"derivedFrom":subQ3}),-1.0]])]});}
            var Q359;
            {var subQ3=sQuery(id+"F0.wireOp",EDGE,"E3.6.0.82");Q359=makeQuery(id+"F0.imprint","IMPRINT",FACE,{"disambiguationData":[TD([[makeQuery(id+"F0.imprint","IMPRINT",EDGE,{"derivedFrom":subQ3}),1.0]])]});}
            var Q360;
            {var subQ3=sQuery(id+"F0.wireOp",EDGE,"E3.8.0.7");Q360=makeQuery(id+"F0.imprint","IMPRINT",FACE,{"disambiguationData":[TD([[makeQuery(id+"F0.imprint","IMPRINT",EDGE,{"derivedFrom":subQ3}),1.0]])]});}
            var Q361;
            {var subQ0=sQuery(id+"F0.wireOp",EDGE,"E3.9.0.96");var subQ1=sQuery(id+"F0.wireOp",EDGE,"E3.9.0.43");var subQ2=makeQuery(id+"F0.imprint","INTERSECT",VERTEX,{"derivedFrom":[subQ1,subQ0]});Q361=makeQuery(id+"F0.imprint","IMPRINT",FACE,{"disambiguationData":[TD([[makeQuery(id+"F0.imprint","IMPRINT",EDGE,{"disambiguationData":[TD([[subQ2,1.0]])],"derivedFrom":subQ1}),-1.0]])]});}
            var Q362;
            {var subQ0=sQuery(id+"F0.wireOp",EDGE,"E3.9.0.42");var subQ1=sQuery(id+"F0.wireOp",EDGE,"E3.9.0.16");var subQ2=makeQuery(id+"F0.imprint","INTERSECT",VERTEX,{"derivedFrom":[subQ1,subQ0]});Q362=makeQuery(id+"F0.imprint","IMPRINT",FACE,{"disambiguationData":[TD([[makeQuery(id+"F0.imprint","IMPRINT",EDGE,{"disambiguationData":[TD([[subQ2,-1.0]])],"derivedFrom":subQ1}),-1.0]])]});}
            var Q363;
            {var subQ0=sQuery(id+"F0.wireOp",EDGE,"E3.9.0.51");var subQ1=sQuery(id+"F0.wireOp",EDGE,"E3.9.0.10");var subQ2=makeQuery(id+"F0.imprint","INTERSECT",VERTEX,{"derivedFrom":[subQ1,subQ0]});Q363=makeQuery(id+"F0.imprint","IMPRINT",FACE,{"disambiguationData":[TD([[makeQuery(id+"F0.imprint","IMPRINT",EDGE,{"disambiguationData":[TD([[subQ2,-1.0]])],"derivedFrom":subQ1}),1.0]])]});}
            var Q364;
            {var subQ5=sQuery(id+"F0.wireOp",EDGE,"E3.11.0.56");Q364=makeQuery(id+"F0.imprint","IMPRINT",FACE,{"disambiguationData":[TD([[makeQuery(id+"F0.imprint","IMPRINT",EDGE,{"derivedFrom":subQ5}),1.0]])]});}
            var Q365;
            {var subQ7=sQuery(id+"F0.wireOp",EDGE,"E3.10.0.54");Q365=makeQuery(id+"F0.imprint","IMPRINT",FACE,{"disambiguationData":[TD([[makeQuery(id+"F0.imprint","IMPRINT",EDGE,{"derivedFrom":subQ7}),-1.0]])]});}
            var Q366;
            {var subQ0=sQuery(id+"F0.wireOp",EDGE,"E3.10.0.63");Q366=makeQuery(id+"F0.imprint","IMPRINT",FACE,{"disambiguationData":[TD([[makeQuery(id+"F0.imprint","IMPRINT",EDGE,{"derivedFrom":subQ0}),-1.0]])]});}
            var Q367;
            {var subQ0=sQuery(id+"F0.wireOp",EDGE,"E3.11.0.64");Q367=makeQuery(id+"F0.imprint","IMPRINT",FACE,{"disambiguationData":[TD([[makeQuery(id+"F0.imprint","IMPRINT",EDGE,{"derivedFrom":subQ0}),-1.0]])]});}
            var Q368;
            {var subQ3=sQuery(id+"F0.wireOp",EDGE,"E2.3.0.7");Q368=makeQuery(id+"F0.imprint","IMPRINT",FACE,{"disambiguationData":[TD([[makeQuery(id+"F0.imprint","IMPRINT",EDGE,{"derivedFrom":subQ3}),-1.0]])]});}
            var Q369;
            {var subQ0=sQuery(id+"F0.wireOp",EDGE,"E3.1.0.41");var subQ1=sQuery(id+"F0.wireOp",EDGE,"E3.1.0.13");var subQ2=makeQuery(id+"F0.imprint","INTERSECT",VERTEX,{"derivedFrom":[subQ1,subQ0]});Q369=makeQuery(id+"F0.imprint","IMPRINT",FACE,{"disambiguationData":[TD([[makeQuery(id+"F0.imprint","IMPRINT",EDGE,{"disambiguationData":[TD([[subQ2,-1.0]])],"derivedFrom":subQ1}),-1.0]])]});}
            var Q370;
            {var subQ3=sQuery(id+"F0.wireOp",EDGE,"E3.1.0.7");Q370=makeQuery(id+"F0.imprint","IMPRINT",FACE,{"disambiguationData":[TD([[makeQuery(id+"F0.imprint","IMPRINT",EDGE,{"derivedFrom":subQ3}),1.0]])]});}
            var Q371;
            {var subQ0=sQuery(id+"F0.wireOp",EDGE,"E3.2.0.42");var subQ1=sQuery(id+"F0.wireOp",EDGE,"E3.2.0.16");var subQ2=makeQuery(id+"F0.imprint","INTERSECT",VERTEX,{"derivedFrom":[subQ1,subQ0]});Q371=makeQuery(id+"F0.imprint","IMPRINT",FACE,{"disambiguationData":[TD([[makeQuery(id+"F0.imprint","IMPRINT",EDGE,{"disambiguationData":[TD([[subQ2,-1.0]])],"derivedFrom":subQ1}),-1.0]])]});}
            var Q372;
            {var subQ0=sQuery(id+"F0.wireOp",EDGE,"E3.2.0.51");var subQ1=sQuery(id+"F0.wireOp",EDGE,"E3.2.0.10");var subQ2=makeQuery(id+"F0.imprint","INTERSECT",VERTEX,{"derivedFrom":[subQ1,subQ0]});Q372=makeQuery(id+"F0.imprint","IMPRINT",FACE,{"disambiguationData":[TD([[makeQuery(id+"F0.imprint","IMPRINT",EDGE,{"disambiguationData":[TD([[subQ2,-1.0]])],"derivedFrom":subQ1}),1.0]])]});}
            var Q373;
            {var subQ7=sQuery(id+"F0.wireOp",EDGE,"E3.3.0.54");Q373=makeQuery(id+"F0.imprint","IMPRINT",FACE,{"disambiguationData":[TD([[makeQuery(id+"F0.imprint","IMPRINT",EDGE,{"derivedFrom":subQ7}),-1.0]])]});}
            var Q374;
            {var subQ0=sQuery(id+"F0.wireOp",EDGE,"E3.3.0.71");var subQ1=sQuery(id+"F0.wireOp",EDGE,"E3.3.0.9");var subQ2=makeQuery(id+"F0.imprint","INTERSECT",VERTEX,{"derivedFrom":[subQ1,subQ0]});Q374=makeQuery(id+"F0.imprint","IMPRINT",FACE,{"disambiguationData":[TD([[makeQuery(id+"F0.imprint","IMPRINT",EDGE,{"disambiguationData":[TD([[subQ2,1.0]])],"derivedFrom":subQ1}),-1.0]])]});}
            var Q375;
            {var subQ0=sQuery(id+"F0.wireOp",EDGE,"E3.3.0.63");Q375=makeQuery(id+"F0.imprint","IMPRINT",FACE,{"disambiguationData":[TD([[makeQuery(id+"F0.imprint","IMPRINT",EDGE,{"derivedFrom":subQ0}),-1.0]])]});}
            var Q376;
            {var subQ0=sQuery(id+"F0.wireOp",EDGE,"E3.3.0.32");var subQ1=sQuery(id+"F0.wireOp",EDGE,"E3.3.0.0");var subQ2=makeQuery(id+"F0.imprint","INTERSECT",VERTEX,{"derivedFrom":[subQ1,subQ0]});Q376=makeQuery(id+"F0.imprint","IMPRINT",FACE,{"disambiguationData":[TD([[makeQuery(id+"F0.imprint","IMPRINT",EDGE,{"disambiguationData":[TD([[subQ2,1.0]])],"derivedFrom":subQ1}),-1.0]])]});}
            var Q377;
            {var subQ0=sQuery(id+"F0.wireOp",EDGE,"E3.4.0.64");Q377=makeQuery(id+"F0.imprint","IMPRINT",FACE,{"disambiguationData":[TD([[makeQuery(id+"F0.imprint","IMPRINT",EDGE,{"derivedFrom":subQ0}),-1.0]])]});}
            var Q378;
            {var subQ5=sQuery(id+"F0.wireOp",EDGE,"E3.5.0.22");Q378=makeQuery(id+"F0.imprint","IMPRINT",FACE,{"disambiguationData":[TD([[makeQuery(id+"F0.imprint","IMPRINT",EDGE,{"derivedFrom":subQ5}),-1.0]])]});}
            var Q379;
            {var subQ0=sQuery(id+"F0.wireOp",EDGE,"E3.16.0.97");var subQ1=sQuery(id+"F0.wireOp",EDGE,"E3.16.0.44");var subQ2=makeQuery(id+"F0.imprint","INTERSECT",VERTEX,{"derivedFrom":[subQ1,subQ0]});Q379=makeQuery(id+"F0.imprint","IMPRINT",FACE,{"disambiguationData":[TD([[makeQuery(id+"F0.imprint","IMPRINT",EDGE,{"disambiguationData":[TD([[subQ2,1.0]])],"derivedFrom":subQ1}),-1.0]])]});}
            var Q380;
            {var subQ3=sQuery(id+"F0.wireOp",EDGE,"E3.17.0.7");Q380=makeQuery(id+"F0.imprint","IMPRINT",FACE,{"disambiguationData":[TD([[makeQuery(id+"F0.imprint","IMPRINT",EDGE,{"derivedFrom":subQ3}),1.0]])]});}
            var Q381;
            {var subQ3=sQuery(id+"F0.wireOp",EDGE,"E3.15.0.82");Q381=makeQuery(id+"F0.imprint","IMPRINT",FACE,{"disambiguationData":[TD([[makeQuery(id+"F0.imprint","IMPRINT",EDGE,{"derivedFrom":subQ3}),1.0]])]});}
            var Q382;
            {var subQ3=sQuery(id+"F0.wireOp",EDGE,"E3.14.0.66");Q382=makeQuery(id+"F0.imprint","IMPRINT",FACE,{"disambiguationData":[TD([[makeQuery(id+"F0.imprint","IMPRINT",EDGE,{"derivedFrom":subQ3}),-1.0]])]});}
            var Q383;
            {var subQ0=sQuery(id+"F0.wireOp",EDGE,"E3.16.0.68");var subQ1=sQuery(id+"F0.wireOp",EDGE,"E3.16.0.11");var subQ2=makeQuery(id+"F0.imprint","INTERSECT",VERTEX,{"derivedFrom":[subQ1,subQ0]});Q383=makeQuery(id+"F0.imprint","IMPRINT",FACE,{"disambiguationData":[TD([[makeQuery(id+"F0.imprint","IMPRINT",EDGE,{"disambiguationData":[TD([[subQ2,1.0]])],"derivedFrom":subQ1}),-1.0]])]});}
            var Q384;
            {var subQ5=sQuery(id+"F0.wireOp",EDGE,"E3.15.0.93");Q384=makeQuery(id+"F0.imprint","IMPRINT",FACE,{"disambiguationData":[TD([[makeQuery(id+"F0.imprint","IMPRINT",EDGE,{"derivedFrom":subQ5}),1.0]])]});}
            var Q385;
            {var subQ0=sQuery(id+"F0.wireOp",EDGE,"E3.6.0.35");var subQ1=sQuery(id+"F0.wireOp",EDGE,"E3.6.0.32");var subQ2=makeQuery(id+"F0.imprint","INTERSECT",VERTEX,{"derivedFrom":[subQ1,subQ0]});Q385=makeQuery(id+"F0.imprint","IMPRINT",FACE,{"disambiguationData":[TD([[makeQuery(id+"F0.imprint","IMPRINT",EDGE,{"disambiguationData":[TD([[subQ2,1.0]])],"derivedFrom":subQ1}),1.0]])]});}
            var Q386;
            {var subQ0=sQuery(id+"F0.wireOp",EDGE,"E3.7.0.39");var subQ1=sQuery(id+"F0.wireOp",EDGE,"E3.7.0.17");var subQ2=makeQuery(id+"F0.imprint","INTERSECT",VERTEX,{"derivedFrom":[subQ1,subQ0]});Q386=makeQuery(id+"F0.imprint","IMPRINT",FACE,{"disambiguationData":[TD([[makeQuery(id+"F0.imprint","IMPRINT",EDGE,{"disambiguationData":[TD([[subQ2,-1.0]])],"derivedFrom":subQ1}),-1.0]])]});}
            var Q387;
            {var subQ0=sQuery(id+"F0.wireOp",EDGE,"E3.6.0.75");var subQ1=sQuery(id+"F0.wireOp",EDGE,"E3.6.0.52");var subQ2=makeQuery(id+"F0.imprint","INTERSECT",VERTEX,{"derivedFrom":[subQ1,subQ0]});Q387=makeQuery(id+"F0.imprint","IMPRINT",FACE,{"disambiguationData":[TD([[makeQuery(id+"F0.imprint","IMPRINT",EDGE,{"disambiguationData":[TD([[subQ2,-1.0]])],"derivedFrom":subQ1}),-1.0]])]});}
            var Q388;
            {var subQ0=sQuery(id+"F0.wireOp",EDGE,"E3.8.0.91");var subQ1=sQuery(id+"F0.wireOp",EDGE,"E3.8.0.49");var subQ2=makeQuery(id+"F0.imprint","INTERSECT",VERTEX,{"derivedFrom":[subQ1,subQ0]});Q388=makeQuery(id+"F0.imprint","IMPRINT",FACE,{"disambiguationData":[TD([[makeQuery(id+"F0.imprint","IMPRINT",EDGE,{"disambiguationData":[TD([[subQ2,-1.0]])],"derivedFrom":subQ1}),-1.0]])]});}
            var Q389;
            {var subQ5=sQuery(id+"F0.wireOp",EDGE,"E3.8.0.82");Q389=makeQuery(id+"F0.imprint","IMPRINT",FACE,{"disambiguationData":[TD([[makeQuery(id+"F0.imprint","IMPRINT",EDGE,{"derivedFrom":subQ5}),-1.0]])]});}
            var Q390;
            {var subQ0=sQuery(id+"F0.wireOp",EDGE,"E3.11.0.41");var subQ1=sQuery(id+"F0.wireOp",EDGE,"E3.11.0.6");var subQ2=makeQuery(id+"F0.imprint","INTERSECT",VERTEX,{"derivedFrom":[subQ1,subQ0]});Q390=makeQuery(id+"F0.imprint","IMPRINT",FACE,{"disambiguationData":[TD([[makeQuery(id+"F0.imprint","IMPRINT",EDGE,{"disambiguationData":[TD([[subQ2,1.0]])],"derivedFrom":subQ1}),-1.0]])]});}
            var Q391;
            {var subQ3=sQuery(id+"F0.wireOp",EDGE,"E3.16.0.66");Q391=makeQuery(id+"F0.imprint","IMPRINT",FACE,{"disambiguationData":[TD([[makeQuery(id+"F0.imprint","IMPRINT",EDGE,{"derivedFrom":subQ3}),-1.0]])]});}
            var Q392;
            {var subQ3=sQuery(id+"F0.wireOp",EDGE,"E3.15.0.56");Q392=makeQuery(id+"F0.imprint","IMPRINT",FACE,{"disambiguationData":[TD([[makeQuery(id+"F0.imprint","IMPRINT",EDGE,{"derivedFrom":subQ3}),-1.0]])]});}
            var Q393;
            {var subQ7=sQuery(id+"F0.wireOp",EDGE,"E3.8.0.83");Q393=makeQuery(id+"F0.imprint","IMPRINT",FACE,{"disambiguationData":[TD([[makeQuery(id+"F0.imprint","IMPRINT",EDGE,{"derivedFrom":subQ7}),-1.0]])]});}
            var Q394;
            {var subQ3=sQuery(id+"F0.wireOp",EDGE,"E3.10.0.31");Q394=makeQuery(id+"F0.imprint","IMPRINT",FACE,{"disambiguationData":[TD([[makeQuery(id+"F0.imprint","IMPRINT",EDGE,{"derivedFrom":subQ3}),-1.0]])]});}
            var Q395;
            {var subQ0=sQuery(id+"F0.wireOp",EDGE,"E3.9.0.39");var subQ1=sQuery(id+"F0.wireOp",EDGE,"E3.9.0.17");var subQ2=makeQuery(id+"F0.imprint","INTERSECT",VERTEX,{"derivedFrom":[subQ1,subQ0]});Q395=makeQuery(id+"F0.imprint","IMPRINT",FACE,{"disambiguationData":[TD([[makeQuery(id+"F0.imprint","IMPRINT",EDGE,{"disambiguationData":[TD([[subQ2,-1.0]])],"derivedFrom":subQ1}),-1.0]])]});}
            var Q396;
            {var subQ0=sQuery(id+"F0.wireOp",EDGE,"E3.10.0.91");var subQ1=sQuery(id+"F0.wireOp",EDGE,"E3.10.0.49");var subQ2=makeQuery(id+"F0.imprint","INTERSECT",VERTEX,{"derivedFrom":[subQ1,subQ0]});Q396=makeQuery(id+"F0.imprint","IMPRINT",FACE,{"disambiguationData":[TD([[makeQuery(id+"F0.imprint","IMPRINT",EDGE,{"disambiguationData":[TD([[subQ2,-1.0]])],"derivedFrom":subQ1}),-1.0]])]});}
            var Q397;
            {var subQ5=sQuery(id+"F0.wireOp",EDGE,"E3.10.0.82");Q397=makeQuery(id+"F0.imprint","IMPRINT",FACE,{"disambiguationData":[TD([[makeQuery(id+"F0.imprint","IMPRINT",EDGE,{"derivedFrom":subQ5}),-1.0]])]});}
            var Q398;
            {var subQ3=sQuery(id+"F0.wireOp",EDGE,"E3.12.0.81");Q398=makeQuery(id+"F0.imprint","IMPRINT",FACE,{"disambiguationData":[TD([[makeQuery(id+"F0.imprint","IMPRINT",EDGE,{"derivedFrom":subQ3}),1.0]])]});}
            var Q399;
            {var subQ5=sQuery(id+"F0.wireOp",EDGE,"E3.1.0.93");Q399=makeQuery(id+"F0.imprint","IMPRINT",FACE,{"disambiguationData":[TD([[makeQuery(id+"F0.imprint","IMPRINT",EDGE,{"derivedFrom":subQ5}),1.0]])]});}
            var Q400;
            {var subQ3=sQuery(id+"F0.wireOp",EDGE,"E3.3.0.7");Q400=makeQuery(id+"F0.imprint","IMPRINT",FACE,{"disambiguationData":[TD([[makeQuery(id+"F0.imprint","IMPRINT",EDGE,{"derivedFrom":subQ3}),1.0]])]});}
            var Q401;
            {var subQ0=sQuery(id+"F0.wireOp",EDGE,"E3.4.0.96");var subQ1=sQuery(id+"F0.wireOp",EDGE,"E3.4.0.43");var subQ2=makeQuery(id+"F0.imprint","INTERSECT",VERTEX,{"derivedFrom":[subQ1,subQ0]});Q401=makeQuery(id+"F0.imprint","IMPRINT",FACE,{"disambiguationData":[TD([[makeQuery(id+"F0.imprint","IMPRINT",EDGE,{"disambiguationData":[TD([[subQ2,1.0]])],"derivedFrom":subQ1}),-1.0]])]});}
            var Q402;
            {var subQ0=sQuery(id+"F0.wireOp",EDGE,"E3.4.0.42");var subQ1=sQuery(id+"F0.wireOp",EDGE,"E3.4.0.16");var subQ2=makeQuery(id+"F0.imprint","INTERSECT",VERTEX,{"derivedFrom":[subQ1,subQ0]});Q402=makeQuery(id+"F0.imprint","IMPRINT",FACE,{"disambiguationData":[TD([[makeQuery(id+"F0.imprint","IMPRINT",EDGE,{"disambiguationData":[TD([[subQ2,-1.0]])],"derivedFrom":subQ1}),-1.0]])]});}
            var Q403;
            {var subQ5=sQuery(id+"F0.wireOp",EDGE,"E3.7.0.53");Q403=makeQuery(id+"F0.imprint","IMPRINT",FACE,{"disambiguationData":[TD([[makeQuery(id+"F0.imprint","IMPRINT",EDGE,{"derivedFrom":subQ5}),-1.0]])]});}
            var Q404;
            {var subQ5=sQuery(id+"F0.wireOp",EDGE,"E3.16.0.53");Q404=makeQuery(id+"F0.imprint","IMPRINT",FACE,{"disambiguationData":[TD([[makeQuery(id+"F0.imprint","IMPRINT",EDGE,{"derivedFrom":subQ5}),-1.0]])]});}
            var Q405;
            {var subQ0=sQuery(id+"F0.wireOp",EDGE,"E3.1.0.35");var subQ1=sQuery(id+"F0.wireOp",EDGE,"E3.1.0.32");var subQ2=makeQuery(id+"F0.imprint","INTERSECT",VERTEX,{"derivedFrom":[subQ1,subQ0]});Q405=makeQuery(id+"F0.imprint","IMPRINT",FACE,{"disambiguationData":[TD([[makeQuery(id+"F0.imprint","IMPRINT",EDGE,{"disambiguationData":[TD([[subQ2,1.0]])],"derivedFrom":subQ1}),1.0]])]});}
            var Q406;
            {var subQ7=sQuery(id+"F0.wireOp",EDGE,"E3.1.0.83");Q406=makeQuery(id+"F0.imprint","IMPRINT",FACE,{"disambiguationData":[TD([[makeQuery(id+"F0.imprint","IMPRINT",EDGE,{"derivedFrom":subQ7}),-1.0]])]});}
            var Q407;
            {var subQ3=sQuery(id+"F0.wireOp",EDGE,"E3.12.0.7");Q407=makeQuery(id+"F0.imprint","IMPRINT",FACE,{"disambiguationData":[TD([[makeQuery(id+"F0.imprint","IMPRINT",EDGE,{"derivedFrom":subQ3}),1.0]])]});}
            var Q408;
            {var subQ0=sQuery(id+"F0.wireOp",EDGE,"E3.3.0.91");var subQ1=sQuery(id+"F0.wireOp",EDGE,"E3.3.0.49");var subQ2=makeQuery(id+"F0.imprint","INTERSECT",VERTEX,{"derivedFrom":[subQ1,subQ0]});Q408=makeQuery(id+"F0.imprint","IMPRINT",FACE,{"disambiguationData":[TD([[makeQuery(id+"F0.imprint","IMPRINT",EDGE,{"disambiguationData":[TD([[subQ2,-1.0]])],"derivedFrom":subQ1}),-1.0]])]});}
            var Q409;
            {var subQ5=sQuery(id+"F0.wireOp",EDGE,"E3.3.0.82");Q409=makeQuery(id+"F0.imprint","IMPRINT",FACE,{"disambiguationData":[TD([[makeQuery(id+"F0.imprint","IMPRINT",EDGE,{"derivedFrom":subQ5}),-1.0]])]});}
            var Q410;
            {var subQ3=sQuery(id+"F0.wireOp",EDGE,"E3.3.0.31");Q410=makeQuery(id+"F0.imprint","IMPRINT",FACE,{"disambiguationData":[TD([[makeQuery(id+"F0.imprint","IMPRINT",EDGE,{"derivedFrom":subQ3}),-1.0]])]});}
            var Q411;
            {var subQ3=sQuery(id+"F0.wireOp",EDGE,"E3.4.0.65");Q411=makeQuery(id+"F0.imprint","IMPRINT",FACE,{"disambiguationData":[TD([[makeQuery(id+"F0.imprint","IMPRINT",EDGE,{"derivedFrom":subQ3}),-1.0]])]});}
            var Q412;
            {var subQ0=sQuery(id+"F0.wireOp",EDGE,"E3.6.0.57");Q412=makeQuery(id+"F0.imprint","IMPRINT",FACE,{"disambiguationData":[TD([[makeQuery(id+"F0.imprint","IMPRINT",EDGE,{"derivedFrom":subQ0}),-1.0]])]});}
            var Q413;
            {var subQ3=sQuery(id+"F0.wireOp",EDGE,"E3.6.0.84");Q413=makeQuery(id+"F0.imprint","IMPRINT",FACE,{"disambiguationData":[TD([[makeQuery(id+"F0.imprint","IMPRINT",EDGE,{"derivedFrom":subQ3}),1.0]])]});}
            var Q414;
            {var subQ0=sQuery(id+"F0.wireOp",EDGE,"E3.7.0.40");var subQ1=sQuery(id+"F0.wireOp",EDGE,"E3.7.0.18");var subQ2=makeQuery(id+"F0.imprint","INTERSECT",VERTEX,{"derivedFrom":[subQ1,subQ0]});Q414=makeQuery(id+"F0.imprint","IMPRINT",FACE,{"disambiguationData":[TD([[makeQuery(id+"F0.imprint","IMPRINT",EDGE,{"disambiguationData":[TD([[subQ2,-1.0]])],"derivedFrom":subQ1}),-1.0]])]});}
            var Q415;
            {var subQ10=sQuery(id+"F0.wireOp",EDGE,"E3.7.0.93");Q415=makeQuery(id+"F0.imprint","IMPRINT",FACE,{"disambiguationData":[TD([[makeQuery(id+"F0.imprint","IMPRINT",EDGE,{"derivedFrom":subQ10}),-1.0]])]});}
            var Q416;
            {var subQ0=sQuery(id+"F0.wireOp",EDGE,"E3.8.0.116");Q416=makeQuery(id+"F0.imprint","IMPRINT",FACE,{"disambiguationData":[TD([[makeQuery(id+"F0.imprint","IMPRINT",EDGE,{"derivedFrom":subQ0}),-1.0]])]});}
            var Q417;
            {var subQ3=sQuery(id+"F0.wireOp",EDGE,"E3.14.0.81");Q417=makeQuery(id+"F0.imprint","IMPRINT",FACE,{"disambiguationData":[TD([[makeQuery(id+"F0.imprint","IMPRINT",EDGE,{"derivedFrom":subQ3}),1.0]])]});}
            var Q418;
            {var subQ0=sQuery(id+"F0.wireOp",EDGE,"E3.15.0.41");var subQ1=sQuery(id+"F0.wireOp",EDGE,"E3.15.0.6");var subQ2=makeQuery(id+"F0.imprint","INTERSECT",VERTEX,{"derivedFrom":[subQ1,subQ0]});Q418=makeQuery(id+"F0.imprint","IMPRINT",FACE,{"disambiguationData":[TD([[makeQuery(id+"F0.imprint","IMPRINT",EDGE,{"disambiguationData":[TD([[subQ2,1.0]])],"derivedFrom":subQ1}),-1.0]])]});}
            var Q419;
            {var subQ0=sQuery(id+"F0.wireOp",EDGE,"E3.1.0.116");Q419=makeQuery(id+"F0.imprint","IMPRINT",FACE,{"disambiguationData":[TD([[makeQuery(id+"F0.imprint","IMPRINT",EDGE,{"derivedFrom":subQ0}),-1.0]])]});}
            var Q420;
            {var subQ3=sQuery(id+"F0.wireOp",EDGE,"E2.12.0.7");Q420=makeQuery(id+"F0.imprint","IMPRINT",FACE,{"disambiguationData":[TD([[makeQuery(id+"F0.imprint","IMPRINT",EDGE,{"derivedFrom":subQ3}),-1.0]])]});}
            var Q421;
            {var subQ3=sQuery(id+"F0.wireOp",EDGE,"E3.2.0.66");Q421=makeQuery(id+"F0.imprint","IMPRINT",FACE,{"disambiguationData":[TD([[makeQuery(id+"F0.imprint","IMPRINT",EDGE,{"derivedFrom":subQ3}),-1.0]])]});}
            var Q422;
            {var subQ0=sQuery(id+"F0.wireOp",EDGE,"E3.16.0.40");var subQ1=sQuery(id+"F0.wireOp",EDGE,"E3.16.0.18");var subQ2=makeQuery(id+"F0.imprint","INTERSECT",VERTEX,{"derivedFrom":[subQ1,subQ0]});Q422=makeQuery(id+"F0.imprint","IMPRINT",FACE,{"disambiguationData":[TD([[makeQuery(id+"F0.imprint","IMPRINT",EDGE,{"disambiguationData":[TD([[subQ2,-1.0]])],"derivedFrom":subQ1}),-1.0]])]});}
            var Q423;
            {var subQ0=sQuery(id+"F0.wireOp",EDGE,"E3.10.0.75");var subQ1=sQuery(id+"F0.wireOp",EDGE,"E3.10.0.52");var subQ2=makeQuery(id+"F0.imprint","INTERSECT",VERTEX,{"derivedFrom":[subQ1,subQ0]});Q423=makeQuery(id+"F0.imprint","IMPRINT",FACE,{"disambiguationData":[TD([[makeQuery(id+"F0.imprint","IMPRINT",EDGE,{"disambiguationData":[TD([[subQ2,-1.0]])],"derivedFrom":subQ1}),-1.0]])]});}
            var Q424;
            {var subQ3=sQuery(id+"F0.wireOp",EDGE,"E3.12.0.31");Q424=makeQuery(id+"F0.imprint","IMPRINT",FACE,{"disambiguationData":[TD([[makeQuery(id+"F0.imprint","IMPRINT",EDGE,{"derivedFrom":subQ3}),-1.0]])]});}
            var Q425;
            {var subQ0=sQuery(id+"F0.wireOp",EDGE,"E3.11.0.97");var subQ1=sQuery(id+"F0.wireOp",EDGE,"E3.11.0.40");var subQ2=makeQuery(id+"F0.imprint","INTERSECT",VERTEX,{"derivedFrom":[subQ1,subQ0]});Q425=makeQuery(id+"F0.imprint","IMPRINT",FACE,{"disambiguationData":[TD([[makeQuery(id+"F0.imprint","IMPRINT",EDGE,{"disambiguationData":[TD([[subQ2,1.0]])],"derivedFrom":subQ1}),-1.0]])]});}
            var Q426;
            {var subQ3=sQuery(id+"F0.wireOp",EDGE,"E3.5.0.7");Q426=makeQuery(id+"F0.imprint","IMPRINT",FACE,{"disambiguationData":[TD([[makeQuery(id+"F0.imprint","IMPRINT",EDGE,{"derivedFrom":subQ3}),1.0]])]});}
            var Q427;
            {var subQ0=sQuery(id+"F0.wireOp",EDGE,"E3.5.0.19");Q427=makeQuery(id+"F0.imprint","IMPRINT",FACE,{"disambiguationData":[TD([[makeQuery(id+"F0.imprint","IMPRINT",EDGE,{"derivedFrom":subQ0}),-1.0]])]});}
            var Q428;
            {var subQ0=sQuery(id+"F0.wireOp",EDGE,"E3.7.0.32");var subQ1=sQuery(id+"F0.wireOp",EDGE,"E3.7.0.0");var subQ2=makeQuery(id+"F0.imprint","INTERSECT",VERTEX,{"derivedFrom":[subQ1,subQ0]});Q428=makeQuery(id+"F0.imprint","IMPRINT",FACE,{"disambiguationData":[TD([[makeQuery(id+"F0.imprint","IMPRINT",EDGE,{"disambiguationData":[TD([[subQ2,1.0]])],"derivedFrom":subQ1}),-1.0]])]});}
            var Q429;
            {var subQ0=sQuery(id+"F0.wireOp",EDGE,"E3.8.0.100");var subQ1=sQuery(id+"F0.wireOp",EDGE,"E3.8.0.52");var subQ2=makeQuery(id+"F0.imprint","INTERSECT",VERTEX,{"derivedFrom":[subQ1,subQ0]});Q429=makeQuery(id+"F0.imprint","IMPRINT",FACE,{"disambiguationData":[TD([[makeQuery(id+"F0.imprint","IMPRINT",EDGE,{"disambiguationData":[TD([[subQ2,1.0]])],"derivedFrom":subQ1}),-1.0]])]});}
            var Q430;
            {var subQ5=sQuery(id+"F0.wireOp",EDGE,"E3.9.0.22");Q430=makeQuery(id+"F0.imprint","IMPRINT",FACE,{"disambiguationData":[TD([[makeQuery(id+"F0.imprint","IMPRINT",EDGE,{"derivedFrom":subQ5}),-1.0]])]});}
            var Q431;
            {var subQ0=sQuery(id+"F0.wireOp",EDGE,"E3.14.0.19");Q431=makeQuery(id+"F0.imprint","IMPRINT",FACE,{"disambiguationData":[TD([[makeQuery(id+"F0.imprint","IMPRINT",EDGE,{"derivedFrom":subQ0}),-1.0]])]});}
            var Q432;
            {var subQ0=sQuery(id+"F0.wireOp",EDGE,"E3.15.0.96");var subQ1=sQuery(id+"F0.wireOp",EDGE,"E3.15.0.43");var subQ2=makeQuery(id+"F0.imprint","INTERSECT",VERTEX,{"derivedFrom":[subQ1,subQ0]});Q432=makeQuery(id+"F0.imprint","IMPRINT",FACE,{"disambiguationData":[TD([[makeQuery(id+"F0.imprint","IMPRINT",EDGE,{"disambiguationData":[TD([[subQ2,1.0]])],"derivedFrom":subQ1}),-1.0]])]});}
            var Q433;
            {var subQ0=sQuery(id+"F0.wireOp",EDGE,"E2.8.0.1");var subQ1=sQuery(id+"F0.wireOp",EDGE,"E2.8.0.0");var subQ2=makeQuery(id+"F0.imprint","INTERSECT",VERTEX,{"derivedFrom":[subQ1,subQ0]});Q433=makeQuery(id+"F0.imprint","IMPRINT",FACE,{"disambiguationData":[TD([[makeQuery(id+"F0.imprint","IMPRINT",EDGE,{"disambiguationData":[TD([[subQ2,1.0]])],"derivedFrom":subQ1}),1.0]])]});}
            var Q434;
            {var subQ0=sQuery(id+"F0.wireOp",EDGE,"E3.1.0.64");Q434=makeQuery(id+"F0.imprint","IMPRINT",FACE,{"disambiguationData":[TD([[makeQuery(id+"F0.imprint","IMPRINT",EDGE,{"derivedFrom":subQ0}),-1.0]])]});}
            var Q435;
            {var subQ0=sQuery(id+"F0.wireOp",EDGE,"E2.12.0.1");var subQ1=sQuery(id+"F0.wireOp",EDGE,"E2.12.0.0");var subQ2=makeQuery(id+"F0.imprint","INTERSECT",VERTEX,{"derivedFrom":[subQ1,subQ0]});Q435=makeQuery(id+"F0.imprint","IMPRINT",FACE,{"disambiguationData":[TD([[makeQuery(id+"F0.imprint","IMPRINT",EDGE,{"disambiguationData":[TD([[subQ2,1.0]])],"derivedFrom":subQ1}),1.0]])]});}
            var Q436;
            {var subQ0=sQuery(id+"F0.wireOp",EDGE,"E3.3.0.75");var subQ1=sQuery(id+"F0.wireOp",EDGE,"E3.3.0.52");var subQ2=makeQuery(id+"F0.imprint","INTERSECT",VERTEX,{"derivedFrom":[subQ1,subQ0]});Q436=makeQuery(id+"F0.imprint","IMPRINT",FACE,{"disambiguationData":[TD([[makeQuery(id+"F0.imprint","IMPRINT",EDGE,{"disambiguationData":[TD([[subQ2,-1.0]])],"derivedFrom":subQ1}),-1.0]])]});}
            var Q437;
            {var subQ7=sQuery(id+"F0.wireOp",EDGE,"E3.3.0.83");Q437=makeQuery(id+"F0.imprint","IMPRINT",FACE,{"disambiguationData":[TD([[makeQuery(id+"F0.imprint","IMPRINT",EDGE,{"derivedFrom":subQ7}),-1.0]])]});}
            var Q438;
            {var subQ0=sQuery(id+"F0.wireOp",EDGE,"E3.3.0.8");var subQ1=sQuery(id+"F0.wireOp",EDGE,"E3.3.0.6");var subQ2=makeQuery(id+"F0.imprint","INTERSECT",VERTEX,{"derivedFrom":[subQ1,subQ0]});Q438=makeQuery(id+"F0.imprint","IMPRINT",FACE,{"disambiguationData":[TD([[makeQuery(id+"F0.imprint","IMPRINT",EDGE,{"disambiguationData":[TD([[subQ2,-1.0]])],"derivedFrom":subQ1}),-1.0]])]});}
            var Q439;
            {var subQ0=sQuery(id+"F0.wireOp",EDGE,"E3.14.0.41");var subQ1=sQuery(id+"F0.wireOp",EDGE,"E3.14.0.13");var subQ2=makeQuery(id+"F0.imprint","INTERSECT",VERTEX,{"derivedFrom":[subQ1,subQ0]});Q439=makeQuery(id+"F0.imprint","IMPRINT",FACE,{"disambiguationData":[TD([[makeQuery(id+"F0.imprint","IMPRINT",EDGE,{"disambiguationData":[TD([[subQ2,-1.0]])],"derivedFrom":subQ1}),-1.0]])]});}
            var Q440;
            {var subQ7=sQuery(id+"F0.wireOp",EDGE,"E3.16.0.54");Q440=makeQuery(id+"F0.imprint","IMPRINT",FACE,{"disambiguationData":[TD([[makeQuery(id+"F0.imprint","IMPRINT",EDGE,{"derivedFrom":subQ7}),-1.0]])]});}
            var Q441;
            {var subQ3=sQuery(id+"F0.wireOp",EDGE,"E3.11.0.66");Q441=makeQuery(id+"F0.imprint","IMPRINT",FACE,{"disambiguationData":[TD([[makeQuery(id+"F0.imprint","IMPRINT",EDGE,{"derivedFrom":subQ3}),-1.0]])]});}
            var Q442;
            {var subQ0=sQuery(id+"F0.wireOp",EDGE,"E3.13.0.68");var subQ1=sQuery(id+"F0.wireOp",EDGE,"E3.13.0.11");var subQ2=makeQuery(id+"F0.imprint","INTERSECT",VERTEX,{"derivedFrom":[subQ1,subQ0]});Q442=makeQuery(id+"F0.imprint","IMPRINT",FACE,{"disambiguationData":[TD([[makeQuery(id+"F0.imprint","IMPRINT",EDGE,{"disambiguationData":[TD([[subQ2,1.0]])],"derivedFrom":subQ1}),-1.0]])]});}
            var Q443;
            {var subQ0=sQuery(id+"F0.wireOp",EDGE,"E3.4.0.68");var subQ1=sQuery(id+"F0.wireOp",EDGE,"E3.4.0.8");var subQ2=makeQuery(id+"F0.imprint","INTERSECT",VERTEX,{"derivedFrom":[subQ1,subQ0]});Q443=makeQuery(id+"F0.imprint","IMPRINT",FACE,{"disambiguationData":[TD([[makeQuery(id+"F0.imprint","IMPRINT",EDGE,{"disambiguationData":[TD([[subQ2,1.0]])],"derivedFrom":subQ1}),-1.0]])]});}
            var Q444;
            {var subQ5=sQuery(id+"F0.wireOp",EDGE,"E3.5.0.82");Q444=makeQuery(id+"F0.imprint","IMPRINT",FACE,{"disambiguationData":[TD([[makeQuery(id+"F0.imprint","IMPRINT",EDGE,{"derivedFrom":subQ5}),-1.0]])]});}
            var Q445;
            {var subQ0=sQuery(id+"F0.wireOp",EDGE,"E3.8.0.57");Q445=makeQuery(id+"F0.imprint","IMPRINT",FACE,{"disambiguationData":[TD([[makeQuery(id+"F0.imprint","IMPRINT",EDGE,{"derivedFrom":subQ0}),-1.0]])]});}
            var Q446;
            {var subQ3=sQuery(id+"F0.wireOp",EDGE,"E3.10.0.56");Q446=makeQuery(id+"F0.imprint","IMPRINT",FACE,{"disambiguationData":[TD([[makeQuery(id+"F0.imprint","IMPRINT",EDGE,{"derivedFrom":subQ3}),-1.0]])]});}
            var Q447;
            {var subQ0=sQuery(id+"F0.wireOp",EDGE,"E3.10.0.116");Q447=makeQuery(id+"F0.imprint","IMPRINT",FACE,{"disambiguationData":[TD([[makeQuery(id+"F0.imprint","IMPRINT",EDGE,{"derivedFrom":subQ0}),-1.0]])]});}
            var Q448;
            {var subQ3=sQuery(id+"F0.wireOp",EDGE,"E3.10.0.83");Q448=makeQuery(id+"F0.imprint","IMPRINT",FACE,{"disambiguationData":[TD([[makeQuery(id+"F0.imprint","IMPRINT",EDGE,{"derivedFrom":subQ3}),1.0]])]});}
            var Q449;
            {var subQ5=sQuery(id+"F0.wireOp",EDGE,"E2.9.0.4");Q449=makeQuery(id+"F0.imprint","IMPRINT",FACE,{"disambiguationData":[TD([[makeQuery(id+"F0.imprint","IMPRINT",EDGE,{"derivedFrom":subQ5}),1.0]])]});}
            var Q450;
            {var subQ0=sQuery(id+"F0.wireOp",EDGE,"E3.1.0.57");Q450=makeQuery(id+"F0.imprint","IMPRINT",FACE,{"disambiguationData":[TD([[makeQuery(id+"F0.imprint","IMPRINT",EDGE,{"derivedFrom":subQ0}),-1.0]])]});}
            var Q451;
            {var subQ0=sQuery(id+"F0.wireOp",EDGE,"E3.2.0.40");var subQ1=sQuery(id+"F0.wireOp",EDGE,"E3.2.0.18");var subQ2=makeQuery(id+"F0.imprint","INTERSECT",VERTEX,{"derivedFrom":[subQ1,subQ0]});Q451=makeQuery(id+"F0.imprint","IMPRINT",FACE,{"disambiguationData":[TD([[makeQuery(id+"F0.imprint","IMPRINT",EDGE,{"disambiguationData":[TD([[subQ2,-1.0]])],"derivedFrom":subQ1}),-1.0]])]});}
            var Q452;
            {var subQ7=sQuery(id+"F0.wireOp",EDGE,"E3.2.0.87");Q452=makeQuery(id+"F0.imprint","IMPRINT",FACE,{"disambiguationData":[TD([[makeQuery(id+"F0.imprint","IMPRINT",EDGE,{"derivedFrom":subQ7}),-1.0]])]});}
            var Q453;
            {var subQ3=sQuery(id+"F0.wireOp",EDGE,"E3.4.0.66");Q453=makeQuery(id+"F0.imprint","IMPRINT",FACE,{"disambiguationData":[TD([[makeQuery(id+"F0.imprint","IMPRINT",EDGE,{"derivedFrom":subQ3}),-1.0]])]});}
            var Q454;
            {var subQ0=sQuery(id+"F0.wireOp",EDGE,"E3.4.0.69");var subQ1=sQuery(id+"F0.wireOp",EDGE,"E3.4.0.12");var subQ2=makeQuery(id+"F0.imprint","INTERSECT",VERTEX,{"derivedFrom":[subQ1,subQ0]});Q454=makeQuery(id+"F0.imprint","IMPRINT",FACE,{"disambiguationData":[TD([[makeQuery(id+"F0.imprint","IMPRINT",EDGE,{"disambiguationData":[TD([[subQ2,1.0]])],"derivedFrom":subQ1}),-1.0]])]});}
            var Q455;
            {var subQ5=sQuery(id+"F0.wireOp",EDGE,"E3.14.0.82");Q455=makeQuery(id+"F0.imprint","IMPRINT",FACE,{"disambiguationData":[TD([[makeQuery(id+"F0.imprint","IMPRINT",EDGE,{"derivedFrom":subQ5}),-1.0]])]});}
            var Q456;
            {var subQ0=sQuery(id+"F0.wireOp",EDGE,"E3.14.0.20");Q456=makeQuery(id+"F0.imprint","IMPRINT",FACE,{"disambiguationData":[TD([[makeQuery(id+"F0.imprint","IMPRINT",EDGE,{"derivedFrom":subQ0}),-1.0]])]});}
            var Q457;
            {var subQ0=sQuery(id+"F0.wireOp",EDGE,"E3.12.0.75");var subQ1=sQuery(id+"F0.wireOp",EDGE,"E3.12.0.52");var subQ2=makeQuery(id+"F0.imprint","INTERSECT",VERTEX,{"derivedFrom":[subQ1,subQ0]});Q457=makeQuery(id+"F0.imprint","IMPRINT",FACE,{"disambiguationData":[TD([[makeQuery(id+"F0.imprint","IMPRINT",EDGE,{"disambiguationData":[TD([[subQ2,-1.0]])],"derivedFrom":subQ1}),-1.0]])]});}
            var Q458;
            {var subQ0=sQuery(id+"F0.wireOp",EDGE,"E3.6.0.68");var subQ1=sQuery(id+"F0.wireOp",EDGE,"E3.6.0.11");var subQ2=makeQuery(id+"F0.imprint","INTERSECT",VERTEX,{"derivedFrom":[subQ1,subQ0]});Q458=makeQuery(id+"F0.imprint","IMPRINT",FACE,{"disambiguationData":[TD([[makeQuery(id+"F0.imprint","IMPRINT",EDGE,{"disambiguationData":[TD([[subQ2,1.0]])],"derivedFrom":subQ1}),-1.0]])]});}
            var Q459;
            {var subQ3=sQuery(id+"F0.wireOp",EDGE,"E3.5.0.103");Q459=makeQuery(id+"F0.imprint","IMPRINT",FACE,{"disambiguationData":[TD([[makeQuery(id+"F0.imprint","IMPRINT",EDGE,{"derivedFrom":subQ3}),1.0]])]});}
            var Q460;
            {var subQ5=sQuery(id+"F0.wireOp",EDGE,"E3.5.0.93");Q460=makeQuery(id+"F0.imprint","IMPRINT",FACE,{"disambiguationData":[TD([[makeQuery(id+"F0.imprint","IMPRINT",EDGE,{"derivedFrom":subQ5}),1.0]])]});}
            var Q461;
            {var subQ0=sQuery(id+"F0.wireOp",EDGE,"E3.8.0.51");var subQ1=sQuery(id+"F0.wireOp",EDGE,"E3.8.0.10");var subQ2=makeQuery(id+"F0.imprint","INTERSECT",VERTEX,{"derivedFrom":[subQ1,subQ0]});Q461=makeQuery(id+"F0.imprint","IMPRINT",FACE,{"disambiguationData":[TD([[makeQuery(id+"F0.imprint","IMPRINT",EDGE,{"disambiguationData":[TD([[subQ2,-1.0]])],"derivedFrom":subQ1}),1.0]])]});}
            var Q462;
            {var subQ0=sQuery(id+"F0.wireOp",EDGE,"E3.9.0.63");Q462=makeQuery(id+"F0.imprint","IMPRINT",FACE,{"disambiguationData":[TD([[makeQuery(id+"F0.imprint","IMPRINT",EDGE,{"derivedFrom":subQ0}),-1.0]])]});}
            var Q463;
            {var subQ0=sQuery(id+"F0.wireOp",EDGE,"E3.12.0.8");var subQ1=sQuery(id+"F0.wireOp",EDGE,"E3.12.0.6");var subQ2=makeQuery(id+"F0.imprint","INTERSECT",VERTEX,{"derivedFrom":[subQ1,subQ0]});Q463=makeQuery(id+"F0.imprint","IMPRINT",FACE,{"disambiguationData":[TD([[makeQuery(id+"F0.imprint","IMPRINT",EDGE,{"disambiguationData":[TD([[subQ2,-1.0]])],"derivedFrom":subQ1}),-1.0]])]});}
            var Q464;
            {var subQ0=sQuery(id+"F0.wireOp",EDGE,"E2.1.0.0");var subQ1=sQuery(id+"F0.wireOp",EDGE,"E1.bottom");var subQ2=makeQuery(id+"F0.imprint","INTERSECT",VERTEX,{"derivedFrom":[subQ1,subQ0]});Q464=makeQuery(id+"F0.imprint","IMPRINT",FACE,{"disambiguationData":[TD([[makeQuery(id+"F0.imprint","IMPRINT",EDGE,{"disambiguationData":[TD([[subQ2,1.0]])],"derivedFrom":subQ1}),1.0]])]});}
            var Q465;
            {var subQ0=sQuery(id+"F0.wireOp",EDGE,"E3.1.0.51");var subQ1=sQuery(id+"F0.wireOp",EDGE,"E3.1.0.10");var subQ2=makeQuery(id+"F0.imprint","INTERSECT",VERTEX,{"derivedFrom":[subQ1,subQ0]});Q465=makeQuery(id+"F0.imprint","IMPRINT",FACE,{"disambiguationData":[TD([[makeQuery(id+"F0.imprint","IMPRINT",EDGE,{"disambiguationData":[TD([[subQ2,-1.0]])],"derivedFrom":subQ1}),1.0]])]});}
            var Q466;
            {var subQ0=sQuery(id+"F0.wireOp",EDGE,"E2.13.0.0");var subQ1=sQuery(id+"F0.wireOp",EDGE,"E2.12.0.1");var subQ2=makeQuery(id+"F0.imprint","INTERSECT",VERTEX,{"derivedFrom":[subQ1,subQ0]});Q466=makeQuery(id+"F0.imprint","IMPRINT",FACE,{"disambiguationData":[TD([[makeQuery(id+"F0.imprint","IMPRINT",EDGE,{"disambiguationData":[TD([[subQ2,1.0]])],"derivedFrom":subQ1}),1.0]])]});}
            var Q467;
            {var subQ0=sQuery(id+"F0.wireOp",EDGE,"E3.3.0.89");Q467=makeQuery(id+"F0.imprint","IMPRINT",FACE,{"disambiguationData":[TD([[makeQuery(id+"F0.imprint","IMPRINT",EDGE,{"derivedFrom":subQ0}),-1.0]])]});}
            var Q468;
            {var subQ5=sQuery(id+"F0.wireOp",EDGE,"E3.4.0.53");Q468=makeQuery(id+"F0.imprint","IMPRINT",FACE,{"disambiguationData":[TD([[makeQuery(id+"F0.imprint","IMPRINT",EDGE,{"derivedFrom":subQ5}),-1.0]])]});}
            var Q469;
            {var subQ0=sQuery(id+"F0.wireOp",EDGE,"E3.5.0.75");var subQ1=sQuery(id+"F0.wireOp",EDGE,"E3.5.0.52");var subQ2=makeQuery(id+"F0.imprint","INTERSECT",VERTEX,{"derivedFrom":[subQ1,subQ0]});Q469=makeQuery(id+"F0.imprint","IMPRINT",FACE,{"disambiguationData":[TD([[makeQuery(id+"F0.imprint","IMPRINT",EDGE,{"disambiguationData":[TD([[subQ2,-1.0]])],"derivedFrom":subQ1}),-1.0]])]});}
            var Q470;
            {var subQ0=sQuery(id+"F0.wireOp",EDGE,"E3.5.0.35");var subQ1=sQuery(id+"F0.wireOp",EDGE,"E3.5.0.32");var subQ2=makeQuery(id+"F0.imprint","INTERSECT",VERTEX,{"derivedFrom":[subQ1,subQ0]});Q470=makeQuery(id+"F0.imprint","IMPRINT",FACE,{"disambiguationData":[TD([[makeQuery(id+"F0.imprint","IMPRINT",EDGE,{"disambiguationData":[TD([[subQ2,1.0]])],"derivedFrom":subQ1}),1.0]])]});}
            var Q471;
            {var subQ0=sQuery(id+"F0.wireOp",EDGE,"E3.16.0.19");Q471=makeQuery(id+"F0.imprint","IMPRINT",FACE,{"disambiguationData":[TD([[makeQuery(id+"F0.imprint","IMPRINT",EDGE,{"derivedFrom":subQ0}),-1.0]])]});}
            var Q472;
            {var subQ0=sQuery(id+"F0.wireOp",EDGE,"E3.6.0.39");var subQ1=sQuery(id+"F0.wireOp",EDGE,"E3.6.0.17");var subQ2=makeQuery(id+"F0.imprint","INTERSECT",VERTEX,{"derivedFrom":[subQ1,subQ0]});Q472=makeQuery(id+"F0.imprint","IMPRINT",FACE,{"disambiguationData":[TD([[makeQuery(id+"F0.imprint","IMPRINT",EDGE,{"disambiguationData":[TD([[subQ2,-1.0]])],"derivedFrom":subQ1}),-1.0]])]});}
            var Q473;
            {var subQ0=sQuery(id+"F0.wireOp",EDGE,"E3.7.0.91");var subQ1=sQuery(id+"F0.wireOp",EDGE,"E3.7.0.49");var subQ2=makeQuery(id+"F0.imprint","INTERSECT",VERTEX,{"derivedFrom":[subQ1,subQ0]});Q473=makeQuery(id+"F0.imprint","IMPRINT",FACE,{"disambiguationData":[TD([[makeQuery(id+"F0.imprint","IMPRINT",EDGE,{"disambiguationData":[TD([[subQ2,-1.0]])],"derivedFrom":subQ1}),-1.0]])]});}
            var Q474;
            {var subQ3=sQuery(id+"F0.wireOp",EDGE,"E3.8.0.65");Q474=makeQuery(id+"F0.imprint","IMPRINT",FACE,{"disambiguationData":[TD([[makeQuery(id+"F0.imprint","IMPRINT",EDGE,{"derivedFrom":subQ3}),-1.0]])]});}
            var Q475;
            {var subQ0=sQuery(id+"F0.wireOp",EDGE,"E3.10.0.57");Q475=makeQuery(id+"F0.imprint","IMPRINT",FACE,{"disambiguationData":[TD([[makeQuery(id+"F0.imprint","IMPRINT",EDGE,{"derivedFrom":subQ0}),-1.0]])]});}
            var Q476;
            {var subQ7=sQuery(id+"F0.wireOp",EDGE,"E3.11.0.87");Q476=makeQuery(id+"F0.imprint","IMPRINT",FACE,{"disambiguationData":[TD([[makeQuery(id+"F0.imprint","IMPRINT",EDGE,{"derivedFrom":subQ7}),-1.0]])]});}
            var Q477;
            {var subQ3=sQuery(id+"F0.wireOp",EDGE,"E3.13.0.66");Q477=makeQuery(id+"F0.imprint","IMPRINT",FACE,{"disambiguationData":[TD([[makeQuery(id+"F0.imprint","IMPRINT",EDGE,{"derivedFrom":subQ3}),-1.0]])]});}
            var Q478;
            {var subQ0=sQuery(id+"F0.wireOp",EDGE,"E3.13.0.69");var subQ1=sQuery(id+"F0.wireOp",EDGE,"E3.13.0.12");var subQ2=makeQuery(id+"F0.imprint","INTERSECT",VERTEX,{"derivedFrom":[subQ1,subQ0]});Q478=makeQuery(id+"F0.imprint","IMPRINT",FACE,{"disambiguationData":[TD([[makeQuery(id+"F0.imprint","IMPRINT",EDGE,{"disambiguationData":[TD([[subQ2,1.0]])],"derivedFrom":subQ1}),-1.0]])]});}
            var Q479;
            {var subQ0=sQuery(id+"F0.wireOp",EDGE,"E3.2.0.37");var subQ5=sQuery(id+"F0.wireOp",EDGE,"E3.2.0.9");var subQ7=makeQuery(id+"F0.imprint","INTERSECT",VERTEX,{"derivedFrom":[subQ5,subQ0]});Q479=makeQuery(id+"F0.imprint","IMPRINT",FACE,{"disambiguationData":[TD([[makeQuery(id+"F0.imprint","IMPRINT",EDGE,{"disambiguationData":[TD([[subQ7,1.0]])],"derivedFrom":subQ5}),1.0]])]});}
            var Q480;
            {var subQ3=sQuery(id+"F0.wireOp",EDGE,"E3.1.0.65");Q480=makeQuery(id+"F0.imprint","IMPRINT",FACE,{"disambiguationData":[TD([[makeQuery(id+"F0.imprint","IMPRINT",EDGE,{"derivedFrom":subQ3}),-1.0]])]});}
            var Q481;
            {var subQ3=sQuery(id+"F0.wireOp",EDGE,"E3.3.0.84");Q481=makeQuery(id+"F0.imprint","IMPRINT",FACE,{"disambiguationData":[TD([[makeQuery(id+"F0.imprint","IMPRINT",EDGE,{"derivedFrom":subQ3}),1.0]])]});}
            var Q482;
            {var subQ0=sQuery(id+"F0.wireOp",EDGE,"E3.4.0.40");var subQ1=sQuery(id+"F0.wireOp",EDGE,"E3.4.0.18");var subQ2=makeQuery(id+"F0.imprint","INTERSECT",VERTEX,{"derivedFrom":[subQ1,subQ0]});Q482=makeQuery(id+"F0.imprint","IMPRINT",FACE,{"disambiguationData":[TD([[makeQuery(id+"F0.imprint","IMPRINT",EDGE,{"disambiguationData":[TD([[subQ2,-1.0]])],"derivedFrom":subQ1}),-1.0]])]});}
            var Q483;
            {var subQ0=sQuery(id+"F0.wireOp",EDGE,"E3.6.0.94");var subQ1=sQuery(id+"F0.wireOp",EDGE,"E3.6.0.42");var subQ2=makeQuery(id+"F0.imprint","INTERSECT",VERTEX,{"derivedFrom":[subQ1,subQ0]});Q483=makeQuery(id+"F0.imprint","IMPRINT",FACE,{"disambiguationData":[TD([[makeQuery(id+"F0.imprint","IMPRINT",EDGE,{"disambiguationData":[TD([[subQ2,1.0]])],"derivedFrom":subQ1}),-1.0]])]});}
            var Q484;
            {var subQ0=sQuery(id+"F0.wireOp",EDGE,"E3.14.0.8");var subQ1=sQuery(id+"F0.wireOp",EDGE,"E3.14.0.6");var subQ2=makeQuery(id+"F0.imprint","INTERSECT",VERTEX,{"derivedFrom":[subQ1,subQ0]});Q484=makeQuery(id+"F0.imprint","IMPRINT",FACE,{"disambiguationData":[TD([[makeQuery(id+"F0.imprint","IMPRINT",EDGE,{"disambiguationData":[TD([[subQ2,-1.0]])],"derivedFrom":subQ1}),-1.0]])]});}
            var Q485;
            {var subQ0=sQuery(id+"F0.wireOp",EDGE,"E3.15.0.39");var subQ1=sQuery(id+"F0.wireOp",EDGE,"E3.15.0.17");var subQ2=makeQuery(id+"F0.imprint","INTERSECT",VERTEX,{"derivedFrom":[subQ1,subQ0]});Q485=makeQuery(id+"F0.imprint","IMPRINT",FACE,{"disambiguationData":[TD([[makeQuery(id+"F0.imprint","IMPRINT",EDGE,{"disambiguationData":[TD([[subQ2,-1.0]])],"derivedFrom":subQ1}),-1.0]])]});}
            var Q486;
            {var subQ0=sQuery(id+"F0.wireOp",EDGE,"E3.15.0.68");var subQ1=sQuery(id+"F0.wireOp",EDGE,"E3.15.0.8");var subQ2=makeQuery(id+"F0.imprint","INTERSECT",VERTEX,{"derivedFrom":[subQ1,subQ0]});Q486=makeQuery(id+"F0.imprint","IMPRINT",FACE,{"disambiguationData":[TD([[makeQuery(id+"F0.imprint","IMPRINT",EDGE,{"disambiguationData":[TD([[subQ2,1.0]])],"derivedFrom":subQ1}),-1.0]])]});}
            var Q487;
            {var subQ5=sQuery(id+"F0.wireOp",EDGE,"E3.16.0.82");Q487=makeQuery(id+"F0.imprint","IMPRINT",FACE,{"disambiguationData":[TD([[makeQuery(id+"F0.imprint","IMPRINT",EDGE,{"derivedFrom":subQ5}),-1.0]])]});}
            var Q488;
            {var subQ3=sQuery(id+"F0.wireOp",EDGE,"E3.7.0.103");Q488=makeQuery(id+"F0.imprint","IMPRINT",FACE,{"disambiguationData":[TD([[makeQuery(id+"F0.imprint","IMPRINT",EDGE,{"derivedFrom":subQ3}),1.0]])]});}
            var Q489;
            {var subQ0=sQuery(id+"F0.wireOp",EDGE,"E3.9.0.41");var subQ1=sQuery(id+"F0.wireOp",EDGE,"E3.9.0.13");var subQ2=makeQuery(id+"F0.imprint","INTERSECT",VERTEX,{"derivedFrom":[subQ1,subQ0]});Q489=makeQuery(id+"F0.imprint","IMPRINT",FACE,{"disambiguationData":[TD([[makeQuery(id+"F0.imprint","IMPRINT",EDGE,{"disambiguationData":[TD([[subQ2,-1.0]])],"derivedFrom":subQ1}),-1.0]])]});}
            var Q490;
            {var subQ0=sQuery(id+"F0.wireOp",EDGE,"E3.10.0.51");var subQ1=sQuery(id+"F0.wireOp",EDGE,"E3.10.0.10");var subQ2=makeQuery(id+"F0.imprint","INTERSECT",VERTEX,{"derivedFrom":[subQ1,subQ0]});Q490=makeQuery(id+"F0.imprint","IMPRINT",FACE,{"disambiguationData":[TD([[makeQuery(id+"F0.imprint","IMPRINT",EDGE,{"disambiguationData":[TD([[subQ2,-1.0]])],"derivedFrom":subQ1}),1.0]])]});}
            var Q491;
            {var subQ0=sQuery(id+"F0.wireOp",EDGE,"E3.12.0.64");Q491=makeQuery(id+"F0.imprint","IMPRINT",FACE,{"disambiguationData":[TD([[makeQuery(id+"F0.imprint","IMPRINT",EDGE,{"derivedFrom":subQ0}),-1.0]])]});}
            var Q492;
            {var subQ3=sQuery(id+"F0.wireOp",EDGE,"E3.2.0.7");Q492=makeQuery(id+"F0.imprint","IMPRINT",FACE,{"disambiguationData":[TD([[makeQuery(id+"F0.imprint","IMPRINT",EDGE,{"derivedFrom":subQ3}),1.0]])]});}
            var Q493;
            {var subQ0=sQuery(id+"F0.wireOp",EDGE,"E3.1.0.97");var subQ1=sQuery(id+"F0.wireOp",EDGE,"E3.1.0.44");var subQ2=makeQuery(id+"F0.imprint","INTERSECT",VERTEX,{"derivedFrom":[subQ1,subQ0]});Q493=makeQuery(id+"F0.imprint","IMPRINT",FACE,{"disambiguationData":[TD([[makeQuery(id+"F0.imprint","IMPRINT",EDGE,{"disambiguationData":[TD([[subQ2,1.0]])],"derivedFrom":subQ1}),-1.0]])]});}
            var Q494;
            {var subQ3=sQuery(id+"F0.wireOp",EDGE,"E3.2.0.118");Q494=makeQuery(id+"F0.imprint","IMPRINT",FACE,{"disambiguationData":[TD([[makeQuery(id+"F0.imprint","IMPRINT",EDGE,{"derivedFrom":subQ3}),1.0]])]});}
            var Q495;
            {var subQ0=sQuery(id+"F0.wireOp",EDGE,"E3.3.0.96");var subQ1=sQuery(id+"F0.wireOp",EDGE,"E3.3.0.43");var subQ2=makeQuery(id+"F0.imprint","INTERSECT",VERTEX,{"derivedFrom":[subQ1,subQ0]});Q495=makeQuery(id+"F0.imprint","IMPRINT",FACE,{"disambiguationData":[TD([[makeQuery(id+"F0.imprint","IMPRINT",EDGE,{"disambiguationData":[TD([[subQ2,1.0]])],"derivedFrom":subQ1}),-1.0]])]});}
            var Q496;
            {var subQ7=sQuery(id+"F0.wireOp",EDGE,"E3.7.0.83");Q496=makeQuery(id+"F0.imprint","IMPRINT",FACE,{"disambiguationData":[TD([[makeQuery(id+"F0.imprint","IMPRINT",EDGE,{"derivedFrom":subQ7}),-1.0]])]});}
            var Q497;
            {var subQ3=sQuery(id+"F0.wireOp",EDGE,"E3.14.0.56");Q497=makeQuery(id+"F0.imprint","IMPRINT",FACE,{"disambiguationData":[TD([[makeQuery(id+"F0.imprint","IMPRINT",EDGE,{"derivedFrom":subQ3}),-1.0]])]});}
            var Q498;
            {var subQ3=sQuery(id+"F0.wireOp",EDGE,"E3.15.0.66");Q498=makeQuery(id+"F0.imprint","IMPRINT",FACE,{"disambiguationData":[TD([[makeQuery(id+"F0.imprint","IMPRINT",EDGE,{"derivedFrom":subQ3}),-1.0]])]});}
            var Q499;
            {var subQ0=sQuery(id+"F0.wireOp",EDGE,"E2.13.0.1");var subQ1=sQuery(id+"F0.wireOp",EDGE,"E2.13.0.0");var subQ2=makeQuery(id+"F0.imprint","INTERSECT",VERTEX,{"derivedFrom":[subQ1,subQ0]});Q499=makeQuery(id+"F0.imprint","IMPRINT",FACE,{"disambiguationData":[TD([[makeQuery(id+"F0.imprint","IMPRINT",EDGE,{"disambiguationData":[TD([[subQ2,1.0]])],"derivedFrom":subQ1}),1.0]])]});}
            var Q500;
            {var subQ0=sQuery(id+"F0.wireOp",EDGE,"E2.5.0.1");var subQ1=sQuery(id+"F0.wireOp",EDGE,"E2.5.0.0");var subQ2=makeQuery(id+"F0.imprint","INTERSECT",VERTEX,{"derivedFrom":[subQ1,subQ0]});Q500=makeQuery(id+"F0.imprint","IMPRINT",FACE,{"disambiguationData":[TD([[makeQuery(id+"F0.imprint","IMPRINT",EDGE,{"disambiguationData":[TD([[subQ2,1.0]])],"derivedFrom":subQ1}),1.0]])]});}
            var Q501;
            {var subQ0=sQuery(id+"F0.wireOp",EDGE,"E3.16.0.35");var subQ1=sQuery(id+"F0.wireOp",EDGE,"E3.16.0.32");var subQ2=makeQuery(id+"F0.imprint","INTERSECT",VERTEX,{"derivedFrom":[subQ1,subQ0]});Q501=makeQuery(id+"F0.imprint","IMPRINT",FACE,{"disambiguationData":[TD([[makeQuery(id+"F0.imprint","IMPRINT",EDGE,{"disambiguationData":[TD([[subQ2,1.0]])],"derivedFrom":subQ1}),1.0]])]});}
            var Q502;
            {var subQ0=sQuery(id+"F0.wireOp",EDGE,"E3.9.0.20");Q502=makeQuery(id+"F0.imprint","IMPRINT",FACE,{"disambiguationData":[TD([[makeQuery(id+"F0.imprint","IMPRINT",EDGE,{"derivedFrom":subQ0}),-1.0]])]});}
            var Q503;
            {var subQ5=sQuery(id+"F0.wireOp",EDGE,"E3.9.0.82");Q503=makeQuery(id+"F0.imprint","IMPRINT",FACE,{"disambiguationData":[TD([[makeQuery(id+"F0.imprint","IMPRINT",EDGE,{"derivedFrom":subQ5}),-1.0]])]});}
            var Q504;
            {var subQ0=sQuery(id+"F0.wireOp",EDGE,"E3.9.0.91");var subQ1=sQuery(id+"F0.wireOp",EDGE,"E3.9.0.49");var subQ2=makeQuery(id+"F0.imprint","INTERSECT",VERTEX,{"derivedFrom":[subQ1,subQ0]});Q504=makeQuery(id+"F0.imprint","IMPRINT",FACE,{"disambiguationData":[TD([[makeQuery(id+"F0.imprint","IMPRINT",EDGE,{"disambiguationData":[TD([[subQ2,-1.0]])],"derivedFrom":subQ1}),-1.0]])]});}
            var Q505;
            {var subQ3=sQuery(id+"F0.wireOp",EDGE,"E3.11.0.81");Q505=makeQuery(id+"F0.imprint","IMPRINT",FACE,{"disambiguationData":[TD([[makeQuery(id+"F0.imprint","IMPRINT",EDGE,{"derivedFrom":subQ3}),1.0]])]});}
            var Q506;
            {var subQ0=sQuery(id+"F0.wireOp",EDGE,"E3.12.0.41");var subQ1=sQuery(id+"F0.wireOp",EDGE,"E3.12.0.6");var subQ2=makeQuery(id+"F0.imprint","INTERSECT",VERTEX,{"derivedFrom":[subQ1,subQ0]});Q506=makeQuery(id+"F0.imprint","IMPRINT",FACE,{"disambiguationData":[TD([[makeQuery(id+"F0.imprint","IMPRINT",EDGE,{"disambiguationData":[TD([[subQ2,1.0]])],"derivedFrom":subQ1}),-1.0]])]});}
            var Q507;
            {var subQ7=sQuery(id+"F0.wireOp",EDGE,"E3.13.0.87");Q507=makeQuery(id+"F0.imprint","IMPRINT",FACE,{"disambiguationData":[TD([[makeQuery(id+"F0.imprint","IMPRINT",EDGE,{"derivedFrom":subQ7}),-1.0]])]});}
            var Q508;
            {var subQ3=sQuery(id+"F0.wireOp",EDGE,"E3.3.0.65");Q508=makeQuery(id+"F0.imprint","IMPRINT",FACE,{"disambiguationData":[TD([[makeQuery(id+"F0.imprint","IMPRINT",EDGE,{"derivedFrom":subQ3}),-1.0]])]});}
            var Q509;
            {var subQ0=sQuery(id+"F0.wireOp",EDGE,"E3.4.0.37");var subQ5=sQuery(id+"F0.wireOp",EDGE,"E3.4.0.9");var subQ7=makeQuery(id+"F0.imprint","INTERSECT",VERTEX,{"derivedFrom":[subQ5,subQ0]});Q509=makeQuery(id+"F0.imprint","IMPRINT",FACE,{"disambiguationData":[TD([[makeQuery(id+"F0.imprint","IMPRINT",EDGE,{"disambiguationData":[TD([[subQ7,1.0]])],"derivedFrom":subQ5}),1.0]])]});}
            var Q510;
            {var subQ3=sQuery(id+"F0.wireOp",EDGE,"E3.5.0.84");Q510=makeQuery(id+"F0.imprint","IMPRINT",FACE,{"disambiguationData":[TD([[makeQuery(id+"F0.imprint","IMPRINT",EDGE,{"derivedFrom":subQ3}),1.0]])]});}
            var Q511;
            {var subQ0=sQuery(id+"F0.wireOp",EDGE,"E3.5.0.57");Q511=makeQuery(id+"F0.imprint","IMPRINT",FACE,{"disambiguationData":[TD([[makeQuery(id+"F0.imprint","IMPRINT",EDGE,{"derivedFrom":subQ0}),-1.0]])]});}
            var Q512;
            {var subQ7=sQuery(id+"F0.wireOp",EDGE,"E3.6.0.87");Q512=makeQuery(id+"F0.imprint","IMPRINT",FACE,{"disambiguationData":[TD([[makeQuery(id+"F0.imprint","IMPRINT",EDGE,{"derivedFrom":subQ7}),-1.0]])]});}
            var Q513;
            {var subQ0=sQuery(id+"F0.wireOp",EDGE,"E3.6.0.40");var subQ1=sQuery(id+"F0.wireOp",EDGE,"E3.6.0.18");var subQ2=makeQuery(id+"F0.imprint","INTERSECT",VERTEX,{"derivedFrom":[subQ1,subQ0]});Q513=makeQuery(id+"F0.imprint","IMPRINT",FACE,{"disambiguationData":[TD([[makeQuery(id+"F0.imprint","IMPRINT",EDGE,{"disambiguationData":[TD([[subQ2,-1.0]])],"derivedFrom":subQ1}),-1.0]])]});}
            var Q514;
            {var subQ0=sQuery(id+"F0.wireOp",EDGE,"E3.8.0.69");var subQ1=sQuery(id+"F0.wireOp",EDGE,"E3.8.0.12");var subQ2=makeQuery(id+"F0.imprint","INTERSECT",VERTEX,{"derivedFrom":[subQ1,subQ0]});Q514=makeQuery(id+"F0.imprint","IMPRINT",FACE,{"disambiguationData":[TD([[makeQuery(id+"F0.imprint","IMPRINT",EDGE,{"disambiguationData":[TD([[subQ2,1.0]])],"derivedFrom":subQ1}),-1.0]])]});}
            var Q515;
            {var subQ0=sQuery(id+"F0.wireOp",EDGE,"E3.7.0.116");Q515=makeQuery(id+"F0.imprint","IMPRINT",FACE,{"disambiguationData":[TD([[makeQuery(id+"F0.imprint","IMPRINT",EDGE,{"derivedFrom":subQ0}),-1.0]])]});}
            var Q516;
            {var subQ5=sQuery(id+"F0.wireOp",EDGE,"E3.2.0.82");Q516=makeQuery(id+"F0.imprint","IMPRINT",FACE,{"disambiguationData":[TD([[makeQuery(id+"F0.imprint","IMPRINT",EDGE,{"derivedFrom":subQ5}),-1.0]])]});}
            var Q517;
            {var subQ3=sQuery(id+"F0.wireOp",EDGE,"E3.2.0.31");Q517=makeQuery(id+"F0.imprint","IMPRINT",FACE,{"disambiguationData":[TD([[makeQuery(id+"F0.imprint","IMPRINT",EDGE,{"derivedFrom":subQ3}),-1.0]])]});}
            var Q518;
            {var subQ0=sQuery(id+"F0.wireOp",EDGE,"E3.1.0.39");var subQ1=sQuery(id+"F0.wireOp",EDGE,"E3.1.0.17");var subQ2=makeQuery(id+"F0.imprint","INTERSECT",VERTEX,{"derivedFrom":[subQ1,subQ0]});Q518=makeQuery(id+"F0.imprint","IMPRINT",FACE,{"disambiguationData":[TD([[makeQuery(id+"F0.imprint","IMPRINT",EDGE,{"disambiguationData":[TD([[subQ2,-1.0]])],"derivedFrom":subQ1}),-1.0]])]});}
            var Q519;
            {var subQ0=sQuery(id+"F0.wireOp",EDGE,"E3.16.0.116");Q519=makeQuery(id+"F0.imprint","IMPRINT",FACE,{"disambiguationData":[TD([[makeQuery(id+"F0.imprint","IMPRINT",EDGE,{"derivedFrom":subQ0}),-1.0]])]});}
            var Q520;
            {var subQ0=sQuery(id+"F0.wireOp",EDGE,"E3.11.0.41");var subQ1=sQuery(id+"F0.wireOp",EDGE,"E3.11.0.13");var subQ2=makeQuery(id+"F0.imprint","INTERSECT",VERTEX,{"derivedFrom":[subQ1,subQ0]});Q520=makeQuery(id+"F0.imprint","IMPRINT",FACE,{"disambiguationData":[TD([[makeQuery(id+"F0.imprint","IMPRINT",EDGE,{"disambiguationData":[TD([[subQ2,-1.0]])],"derivedFrom":subQ1}),-1.0]])]});}
            var Q521;
            {var subQ0=sQuery(id+"F0.wireOp",EDGE,"E3.13.0.63");Q521=makeQuery(id+"F0.imprint","IMPRINT",FACE,{"disambiguationData":[TD([[makeQuery(id+"F0.imprint","IMPRINT",EDGE,{"derivedFrom":subQ0}),-1.0]])]});}
            var Q522;
            {var subQ0=sQuery(id+"F0.wireOp",EDGE,"E3.9.0.8");var subQ1=sQuery(id+"F0.wireOp",EDGE,"E3.9.0.6");var subQ2=makeQuery(id+"F0.imprint","INTERSECT",VERTEX,{"derivedFrom":[subQ1,subQ0]});Q522=makeQuery(id+"F0.imprint","IMPRINT",FACE,{"disambiguationData":[TD([[makeQuery(id+"F0.imprint","IMPRINT",EDGE,{"disambiguationData":[TD([[subQ2,-1.0]])],"derivedFrom":subQ1}),-1.0]])]});}
            var Q523;
            {var subQ0=sQuery(id+"F0.wireOp",EDGE,"E3.9.0.75");var subQ1=sQuery(id+"F0.wireOp",EDGE,"E3.9.0.52");var subQ2=makeQuery(id+"F0.imprint","INTERSECT",VERTEX,{"derivedFrom":[subQ1,subQ0]});Q523=makeQuery(id+"F0.imprint","IMPRINT",FACE,{"disambiguationData":[TD([[makeQuery(id+"F0.imprint","IMPRINT",EDGE,{"disambiguationData":[TD([[subQ2,-1.0]])],"derivedFrom":subQ1}),-1.0]])]});}
            var Q524;
            {var subQ0=sQuery(id+"F0.wireOp",EDGE,"E3.14.0.41");var subQ1=sQuery(id+"F0.wireOp",EDGE,"E3.14.0.6");var subQ2=makeQuery(id+"F0.imprint","INTERSECT",VERTEX,{"derivedFrom":[subQ1,subQ0]});Q524=makeQuery(id+"F0.imprint","IMPRINT",FACE,{"disambiguationData":[TD([[makeQuery(id+"F0.imprint","IMPRINT",EDGE,{"disambiguationData":[TD([[subQ2,1.0]])],"derivedFrom":subQ1}),-1.0]])]});}
            var Q525;
            {var subQ3=sQuery(id+"F0.wireOp",EDGE,"E3.16.0.56");Q525=makeQuery(id+"F0.imprint","IMPRINT",FACE,{"disambiguationData":[TD([[makeQuery(id+"F0.imprint","IMPRINT",EDGE,{"derivedFrom":subQ3}),-1.0]])]});}
            var Q526;
            {var subQ0=sQuery(id+"F0.wireOp",EDGE,"E2.2.0.0");var subQ1=sQuery(id+"F0.wireOp",EDGE,"E2.1.0.1");var subQ2=makeQuery(id+"F0.imprint","INTERSECT",VERTEX,{"derivedFrom":[subQ1,subQ0]});Q526=makeQuery(id+"F0.imprint","IMPRINT",FACE,{"disambiguationData":[TD([[makeQuery(id+"F0.imprint","IMPRINT",EDGE,{"disambiguationData":[TD([[subQ2,1.0]])],"derivedFrom":subQ1}),1.0]])]});}
            var Q527;
            {var subQ0=sQuery(id+"F0.wireOp",EDGE,"E3.3.0.68");var subQ1=sQuery(id+"F0.wireOp",EDGE,"E3.3.0.11");var subQ2=makeQuery(id+"F0.imprint","INTERSECT",VERTEX,{"derivedFrom":[subQ1,subQ0]});Q527=makeQuery(id+"F0.imprint","IMPRINT",FACE,{"disambiguationData":[TD([[makeQuery(id+"F0.imprint","IMPRINT",EDGE,{"disambiguationData":[TD([[subQ2,1.0]])],"derivedFrom":subQ1}),-1.0]])]});}
            var Q528;
            {var subQ5=sQuery(id+"F0.wireOp",EDGE,"E3.2.0.93");Q528=makeQuery(id+"F0.imprint","IMPRINT",FACE,{"disambiguationData":[TD([[makeQuery(id+"F0.imprint","IMPRINT",EDGE,{"derivedFrom":subQ5}),1.0]])]});}
            var Q529;
            {var subQ0=sQuery(id+"F0.wireOp",EDGE,"E3.14.0.51");var subQ1=sQuery(id+"F0.wireOp",EDGE,"E3.14.0.10");var subQ2=makeQuery(id+"F0.imprint","INTERSECT",VERTEX,{"derivedFrom":[subQ1,subQ0]});Q529=makeQuery(id+"F0.imprint","IMPRINT",FACE,{"disambiguationData":[TD([[makeQuery(id+"F0.imprint","IMPRINT",EDGE,{"disambiguationData":[TD([[subQ2,-1.0]])],"derivedFrom":subQ1}),1.0]])]});}
            var Q530;
            {var subQ0=sQuery(id+"F0.wireOp",EDGE,"E3.11.0.20");Q530=makeQuery(id+"F0.imprint","IMPRINT",FACE,{"disambiguationData":[TD([[makeQuery(id+"F0.imprint","IMPRINT",EDGE,{"derivedFrom":subQ0}),-1.0]])]});}
            var Q531;
            {var subQ5=sQuery(id+"F0.wireOp",EDGE,"E3.11.0.82");Q531=makeQuery(id+"F0.imprint","IMPRINT",FACE,{"disambiguationData":[TD([[makeQuery(id+"F0.imprint","IMPRINT",EDGE,{"derivedFrom":subQ5}),-1.0]])]});}
            var Q532;
            {var subQ3=sQuery(id+"F0.wireOp",EDGE,"E3.11.0.31");Q532=makeQuery(id+"F0.imprint","IMPRINT",FACE,{"disambiguationData":[TD([[makeQuery(id+"F0.imprint","IMPRINT",EDGE,{"derivedFrom":subQ3}),-1.0]])]});}
            var Q533;
            {var subQ3=sQuery(id+"F0.wireOp",EDGE,"E3.5.0.65");Q533=makeQuery(id+"F0.imprint","IMPRINT",FACE,{"disambiguationData":[TD([[makeQuery(id+"F0.imprint","IMPRINT",EDGE,{"derivedFrom":subQ3}),-1.0]])]});}
            var Q534;
            {var subQ0=sQuery(id+"F0.wireOp",EDGE,"E3.4.0.91");var subQ1=sQuery(id+"F0.wireOp",EDGE,"E3.4.0.49");var subQ2=makeQuery(id+"F0.imprint","INTERSECT",VERTEX,{"derivedFrom":[subQ1,subQ0]});Q534=makeQuery(id+"F0.imprint","IMPRINT",FACE,{"disambiguationData":[TD([[makeQuery(id+"F0.imprint","IMPRINT",EDGE,{"disambiguationData":[TD([[subQ2,-1.0]])],"derivedFrom":subQ1}),-1.0]])]});}
            var Q535;
            {var subQ7=sQuery(id+"F0.wireOp",EDGE,"E3.8.0.87");Q535=makeQuery(id+"F0.imprint","IMPRINT",FACE,{"disambiguationData":[TD([[makeQuery(id+"F0.imprint","IMPRINT",EDGE,{"derivedFrom":subQ7}),-1.0]])]});}
            var Q536;
            {var subQ3=sQuery(id+"F0.wireOp",EDGE,"E3.9.0.83");Q536=makeQuery(id+"F0.imprint","IMPRINT",FACE,{"disambiguationData":[TD([[makeQuery(id+"F0.imprint","IMPRINT",EDGE,{"derivedFrom":subQ3}),1.0]])]});}
            var Q537;
            {var subQ0=sQuery(id+"F0.wireOp",EDGE,"E3.9.0.99");var subQ1=sQuery(id+"F0.wireOp",EDGE,"E3.9.0.49");var subQ2=makeQuery(id+"F0.imprint","INTERSECT",VERTEX,{"derivedFrom":[subQ1,subQ0]});Q537=makeQuery(id+"F0.imprint","IMPRINT",FACE,{"disambiguationData":[TD([[makeQuery(id+"F0.imprint","IMPRINT",EDGE,{"disambiguationData":[TD([[subQ2,1.0]])],"derivedFrom":subQ1}),-1.0]])]});}
            var Q538;
            {var subQ0=sQuery(id+"F0.wireOp",EDGE,"E2.14.0.1");var subQ1=sQuery(id+"F0.wireOp",EDGE,"E2.14.0.0");var subQ2=makeQuery(id+"F0.imprint","INTERSECT",VERTEX,{"derivedFrom":[subQ1,subQ0]});Q538=makeQuery(id+"F0.imprint","IMPRINT",FACE,{"disambiguationData":[TD([[makeQuery(id+"F0.imprint","IMPRINT",EDGE,{"disambiguationData":[TD([[subQ2,1.0]])],"derivedFrom":subQ1}),1.0]])]});}
            var Q539;
            {var subQ3=sQuery(id+"F0.wireOp",EDGE,"E3.1.0.86");Q539=makeQuery(id+"F0.imprint","IMPRINT",FACE,{"disambiguationData":[TD([[makeQuery(id+"F0.imprint","IMPRINT",EDGE,{"derivedFrom":subQ3}),1.0]])]});}
            var Q540;
            {var subQ0=sQuery(id+"F0.wireOp",EDGE,"E3.3.0.39");var subQ1=sQuery(id+"F0.wireOp",EDGE,"E3.3.0.17");var subQ2=makeQuery(id+"F0.imprint","INTERSECT",VERTEX,{"derivedFrom":[subQ1,subQ0]});Q540=makeQuery(id+"F0.imprint","IMPRINT",FACE,{"disambiguationData":[TD([[makeQuery(id+"F0.imprint","IMPRINT",EDGE,{"disambiguationData":[TD([[subQ2,-1.0]])],"derivedFrom":subQ1}),-1.0]])]});}
            var Q541;
            {var subQ0=sQuery(id+"F0.wireOp",EDGE,"E3.2.0.75");var subQ1=sQuery(id+"F0.wireOp",EDGE,"E3.2.0.52");var subQ2=makeQuery(id+"F0.imprint","INTERSECT",VERTEX,{"derivedFrom":[subQ1,subQ0]});Q541=makeQuery(id+"F0.imprint","IMPRINT",FACE,{"disambiguationData":[TD([[makeQuery(id+"F0.imprint","IMPRINT",EDGE,{"disambiguationData":[TD([[subQ2,-1.0]])],"derivedFrom":subQ1}),-1.0]])]});}
            var Q542;
            {var subQ3=sQuery(id+"F0.wireOp",EDGE,"E3.4.0.31");Q542=makeQuery(id+"F0.imprint","IMPRINT",FACE,{"disambiguationData":[TD([[makeQuery(id+"F0.imprint","IMPRINT",EDGE,{"derivedFrom":subQ3}),-1.0]])]});}
            var Q543;
            {var subQ0=sQuery(id+"F0.wireOp",EDGE,"E3.12.0.97");var subQ1=sQuery(id+"F0.wireOp",EDGE,"E3.12.0.44");var subQ2=makeQuery(id+"F0.imprint","INTERSECT",VERTEX,{"derivedFrom":[subQ1,subQ0]});Q543=makeQuery(id+"F0.imprint","IMPRINT",FACE,{"disambiguationData":[TD([[makeQuery(id+"F0.imprint","IMPRINT",EDGE,{"disambiguationData":[TD([[subQ2,1.0]])],"derivedFrom":subQ1}),-1.0]])]});}
            var Q544;
            {var subQ0=sQuery(id+"F0.wireOp",EDGE,"E3.13.0.19");Q544=makeQuery(id+"F0.imprint","IMPRINT",FACE,{"disambiguationData":[TD([[makeQuery(id+"F0.imprint","IMPRINT",EDGE,{"derivedFrom":subQ0}),-1.0]])]});}
            var Q545;
            {var subQ0=sQuery(id+"F0.wireOp",EDGE,"E3.13.0.41");var subQ1=sQuery(id+"F0.wireOp",EDGE,"E3.13.0.13");var subQ2=makeQuery(id+"F0.imprint","INTERSECT",VERTEX,{"derivedFrom":[subQ1,subQ0]});Q545=makeQuery(id+"F0.imprint","IMPRINT",FACE,{"disambiguationData":[TD([[makeQuery(id+"F0.imprint","IMPRINT",EDGE,{"disambiguationData":[TD([[subQ2,-1.0]])],"derivedFrom":subQ1}),-1.0]])]});}
            var Q546;
            {var subQ3=sQuery(id+"F0.wireOp",EDGE,"E3.6.0.118");Q546=makeQuery(id+"F0.imprint","IMPRINT",FACE,{"disambiguationData":[TD([[makeQuery(id+"F0.imprint","IMPRINT",EDGE,{"derivedFrom":subQ3}),1.0]])]});}
            var Q547;
            {var subQ0=sQuery(id+"F0.wireOp",EDGE,"E3.8.0.71");var subQ1=sQuery(id+"F0.wireOp",EDGE,"E3.8.0.9");var subQ2=makeQuery(id+"F0.imprint","INTERSECT",VERTEX,{"derivedFrom":[subQ1,subQ0]});Q547=makeQuery(id+"F0.imprint","IMPRINT",FACE,{"disambiguationData":[TD([[makeQuery(id+"F0.imprint","IMPRINT",EDGE,{"disambiguationData":[TD([[subQ2,1.0]])],"derivedFrom":subQ1}),-1.0]])]});}
            var Q548;
            {var subQ0=sQuery(id+"F0.wireOp",EDGE,"E3.7.0.96");var subQ1=sQuery(id+"F0.wireOp",EDGE,"E3.7.0.43");var subQ2=makeQuery(id+"F0.imprint","INTERSECT",VERTEX,{"derivedFrom":[subQ1,subQ0]});Q548=makeQuery(id+"F0.imprint","IMPRINT",FACE,{"disambiguationData":[TD([[makeQuery(id+"F0.imprint","IMPRINT",EDGE,{"disambiguationData":[TD([[subQ2,1.0]])],"derivedFrom":subQ1}),-1.0]])]});}
            var Q549;
            {var subQ0=sQuery(id+"F0.wireOp",EDGE,"E3.9.0.64");Q549=makeQuery(id+"F0.imprint","IMPRINT",FACE,{"disambiguationData":[TD([[makeQuery(id+"F0.imprint","IMPRINT",EDGE,{"derivedFrom":subQ0}),-1.0]])]});}
            var Q550;
            {var subQ5=sQuery(id+"F0.wireOp",EDGE,"E3.9.0.56");Q550=makeQuery(id+"F0.imprint","IMPRINT",FACE,{"disambiguationData":[TD([[makeQuery(id+"F0.imprint","IMPRINT",EDGE,{"derivedFrom":subQ5}),1.0]])]});}
            var Q551;
            {var subQ5=sQuery(id+"F0.wireOp",EDGE,"E3.10.0.22");Q551=makeQuery(id+"F0.imprint","IMPRINT",FACE,{"disambiguationData":[TD([[makeQuery(id+"F0.imprint","IMPRINT",EDGE,{"derivedFrom":subQ5}),-1.0]])]});}
            var Q552;
            {var subQ0=sQuery(id+"F0.wireOp",EDGE,"E3.11.0.75");var subQ1=sQuery(id+"F0.wireOp",EDGE,"E3.11.0.52");var subQ2=makeQuery(id+"F0.imprint","INTERSECT",VERTEX,{"derivedFrom":[subQ1,subQ0]});Q552=makeQuery(id+"F0.imprint","IMPRINT",FACE,{"disambiguationData":[TD([[makeQuery(id+"F0.imprint","IMPRINT",EDGE,{"disambiguationData":[TD([[subQ2,-1.0]])],"derivedFrom":subQ1}),-1.0]])]});}
            var Q553;
            {var subQ0=sQuery(id+"F0.wireOp",EDGE,"E3.11.0.8");var subQ1=sQuery(id+"F0.wireOp",EDGE,"E3.11.0.6");var subQ2=makeQuery(id+"F0.imprint","INTERSECT",VERTEX,{"derivedFrom":[subQ1,subQ0]});Q553=makeQuery(id+"F0.imprint","IMPRINT",FACE,{"disambiguationData":[TD([[makeQuery(id+"F0.imprint","IMPRINT",EDGE,{"disambiguationData":[TD([[subQ2,-1.0]])],"derivedFrom":subQ1}),-1.0]])]});}
            var Q554;
            {var subQ0=sQuery(id+"F0.wireOp",EDGE,"E2.2.0.1");var subQ1=sQuery(id+"F0.wireOp",EDGE,"E2.2.0.0");var subQ2=makeQuery(id+"F0.imprint","INTERSECT",VERTEX,{"derivedFrom":[subQ1,subQ0]});Q554=makeQuery(id+"F0.imprint","IMPRINT",FACE,{"disambiguationData":[TD([[makeQuery(id+"F0.imprint","IMPRINT",EDGE,{"disambiguationData":[TD([[subQ2,1.0]])],"derivedFrom":subQ1}),1.0]])]});}
            var Q555;
            {var subQ0=sQuery(id+"F0.wireOp",EDGE,"E2.10.0.1");var subQ1=sQuery(id+"F0.wireOp",EDGE,"E2.10.0.0");var subQ2=makeQuery(id+"F0.imprint","INTERSECT",VERTEX,{"derivedFrom":[subQ1,subQ0]});Q555=makeQuery(id+"F0.imprint","IMPRINT",FACE,{"disambiguationData":[TD([[makeQuery(id+"F0.imprint","IMPRINT",EDGE,{"disambiguationData":[TD([[subQ2,1.0]])],"derivedFrom":subQ1}),1.0]])]});}
            var Q556;
            {var subQ3=sQuery(id+"F0.wireOp",EDGE,"E3.1.0.53");Q556=makeQuery(id+"F0.imprint","IMPRINT",FACE,{"disambiguationData":[TD([[makeQuery(id+"F0.imprint","IMPRINT",EDGE,{"derivedFrom":subQ3}),1.0]])]});}
            var Q557;
            {var subQ3=sQuery(id+"F0.wireOp",EDGE,"E3.3.0.66");Q557=makeQuery(id+"F0.imprint","IMPRINT",FACE,{"disambiguationData":[TD([[makeQuery(id+"F0.imprint","IMPRINT",EDGE,{"derivedFrom":subQ3}),-1.0]])]});}
            var Q558;
            {var subQ0=sQuery(id+"F0.wireOp",EDGE,"E3.3.0.94");var subQ1=sQuery(id+"F0.wireOp",EDGE,"E3.3.0.42");var subQ2=makeQuery(id+"F0.imprint","INTERSECT",VERTEX,{"derivedFrom":[subQ1,subQ0]});Q558=makeQuery(id+"F0.imprint","IMPRINT",FACE,{"disambiguationData":[TD([[makeQuery(id+"F0.imprint","IMPRINT",EDGE,{"disambiguationData":[TD([[subQ2,1.0]])],"derivedFrom":subQ1}),-1.0]])]});}
            var Q559;
            {var subQ0=sQuery(id+"F0.wireOp",EDGE,"E3.16.0.96");var subQ1=sQuery(id+"F0.wireOp",EDGE,"E3.16.0.43");var subQ2=makeQuery(id+"F0.imprint","INTERSECT",VERTEX,{"derivedFrom":[subQ1,subQ0]});Q559=makeQuery(id+"F0.imprint","IMPRINT",FACE,{"disambiguationData":[TD([[makeQuery(id+"F0.imprint","IMPRINT",EDGE,{"disambiguationData":[TD([[subQ2,1.0]])],"derivedFrom":subQ1}),-1.0]])]});}
            var Q560;
            {var subQ0=sQuery(id+"F0.wireOp",EDGE,"E3.15.0.19");Q560=makeQuery(id+"F0.imprint","IMPRINT",FACE,{"disambiguationData":[TD([[makeQuery(id+"F0.imprint","IMPRINT",EDGE,{"derivedFrom":subQ0}),-1.0]])]});}
            var Q561;
            {var subQ5=sQuery(id+"F0.wireOp",EDGE,"E3.13.0.82");Q561=makeQuery(id+"F0.imprint","IMPRINT",FACE,{"disambiguationData":[TD([[makeQuery(id+"F0.imprint","IMPRINT",EDGE,{"derivedFrom":subQ5}),-1.0]])]});}
            var Q562;
            {var subQ3=sQuery(id+"F0.wireOp",EDGE,"E3.7.0.65");Q562=makeQuery(id+"F0.imprint","IMPRINT",FACE,{"disambiguationData":[TD([[makeQuery(id+"F0.imprint","IMPRINT",EDGE,{"derivedFrom":subQ3}),-1.0]])]});}
            var Q563;
            {var subQ5=sQuery(id+"F0.wireOp",EDGE,"E3.7.0.57");Q563=makeQuery(id+"F0.imprint","IMPRINT",FACE,{"disambiguationData":[TD([[makeQuery(id+"F0.imprint","IMPRINT",EDGE,{"derivedFrom":subQ5}),1.0]])]});}
            var Q564;
            {var subQ0=sQuery(id+"F0.wireOp",EDGE,"E3.6.0.91");var subQ1=sQuery(id+"F0.wireOp",EDGE,"E3.6.0.49");var subQ2=makeQuery(id+"F0.imprint","INTERSECT",VERTEX,{"derivedFrom":[subQ1,subQ0]});Q564=makeQuery(id+"F0.imprint","IMPRINT",FACE,{"disambiguationData":[TD([[makeQuery(id+"F0.imprint","IMPRINT",EDGE,{"disambiguationData":[TD([[subQ2,-1.0]])],"derivedFrom":subQ1}),-1.0]])]});}
            var Q565;
            {var subQ0=sQuery(id+"F0.wireOp",EDGE,"E3.9.0.57");Q565=makeQuery(id+"F0.imprint","IMPRINT",FACE,{"disambiguationData":[TD([[makeQuery(id+"F0.imprint","IMPRINT",EDGE,{"derivedFrom":subQ0}),-1.0]])]});}
            var Q566;
            {var subQ7=sQuery(id+"F0.wireOp",EDGE,"E3.10.0.87");Q566=makeQuery(id+"F0.imprint","IMPRINT",FACE,{"disambiguationData":[TD([[makeQuery(id+"F0.imprint","IMPRINT",EDGE,{"derivedFrom":subQ7}),-1.0]])]});}
            var Q567;
            {var subQ0=sQuery(id+"F0.wireOp",EDGE,"E3.12.0.69");var subQ1=sQuery(id+"F0.wireOp",EDGE,"E3.12.0.12");var subQ2=makeQuery(id+"F0.imprint","INTERSECT",VERTEX,{"derivedFrom":[subQ1,subQ0]});Q567=makeQuery(id+"F0.imprint","IMPRINT",FACE,{"disambiguationData":[TD([[makeQuery(id+"F0.imprint","IMPRINT",EDGE,{"disambiguationData":[TD([[subQ2,1.0]])],"derivedFrom":subQ1}),-1.0]])]});}
            var Q568;
            {var subQ5=sQuery(id+"F0.wireOp",EDGE,"E2.3.0.4");Q568=makeQuery(id+"F0.imprint","IMPRINT",FACE,{"disambiguationData":[TD([[makeQuery(id+"F0.imprint","IMPRINT",EDGE,{"derivedFrom":subQ5}),1.0]])]});}
            var Q569;
            {var subQ5=sQuery(id+"F0.wireOp",EDGE,"E2.11.0.4");Q569=makeQuery(id+"F0.imprint","IMPRINT",FACE,{"disambiguationData":[TD([[makeQuery(id+"F0.imprint","IMPRINT",EDGE,{"derivedFrom":subQ5}),1.0]])]});}
            var Q570;
            {var subQ0=sQuery(id+"F0.wireOp",EDGE,"E3.2.0.64");Q570=makeQuery(id+"F0.imprint","IMPRINT",FACE,{"disambiguationData":[TD([[makeQuery(id+"F0.imprint","IMPRINT",EDGE,{"derivedFrom":subQ0}),-1.0]])]});}
            var Q571;
            {var subQ7=sQuery(id+"F0.wireOp",EDGE,"E3.4.0.83");Q571=makeQuery(id+"F0.imprint","IMPRINT",FACE,{"disambiguationData":[TD([[makeQuery(id+"F0.imprint","IMPRINT",EDGE,{"derivedFrom":subQ7}),-1.0]])]});}
            var Q572;
            {var subQ0=sQuery(id+"F0.wireOp",EDGE,"E3.4.0.8");var subQ1=sQuery(id+"F0.wireOp",EDGE,"E3.4.0.6");var subQ2=makeQuery(id+"F0.imprint","INTERSECT",VERTEX,{"derivedFrom":[subQ1,subQ0]});Q572=makeQuery(id+"F0.imprint","IMPRINT",FACE,{"disambiguationData":[TD([[makeQuery(id+"F0.imprint","IMPRINT",EDGE,{"disambiguationData":[TD([[subQ2,-1.0]])],"derivedFrom":subQ1}),-1.0]])]});}
            var Q573;
            {var subQ0=sQuery(id+"F0.wireOp",EDGE,"E3.5.0.68");var subQ1=sQuery(id+"F0.wireOp",EDGE,"E3.5.0.8");var subQ2=makeQuery(id+"F0.imprint","INTERSECT",VERTEX,{"derivedFrom":[subQ1,subQ0]});Q573=makeQuery(id+"F0.imprint","IMPRINT",FACE,{"disambiguationData":[TD([[makeQuery(id+"F0.imprint","IMPRINT",EDGE,{"disambiguationData":[TD([[subQ2,1.0]])],"derivedFrom":subQ1}),-1.0]])]});}
            var Q574;
            {var subQ5=sQuery(id+"F0.wireOp",EDGE,"E3.6.0.82");Q574=makeQuery(id+"F0.imprint","IMPRINT",FACE,{"disambiguationData":[TD([[makeQuery(id+"F0.imprint","IMPRINT",EDGE,{"derivedFrom":subQ5}),-1.0]])]});}
            var Q575;
            {var subQ0=sQuery(id+"F0.wireOp",EDGE,"E3.22.0.94");var subQ1=sQuery(id+"F0.wireOp",EDGE,"E3.22.0.42");var subQ2=makeQuery(id+"F0.imprint","INTERSECT",VERTEX,{"derivedFrom":[subQ1,subQ0]});Q575=makeQuery(id+"F0.imprint","IMPRINT",FACE,{"disambiguationData":[TD([[makeQuery(id+"F0.imprint","IMPRINT",EDGE,{"disambiguationData":[TD([[subQ2,1.0]])],"derivedFrom":subQ1}),-1.0]])]});}
            var Q576;
            {var subQ0=sQuery(id+"F0.wireOp",EDGE,"E3.22.0.69");var subQ1=sQuery(id+"F0.wireOp",EDGE,"E3.22.0.12");var subQ2=makeQuery(id+"F0.imprint","INTERSECT",VERTEX,{"derivedFrom":[subQ1,subQ0]});Q576=makeQuery(id+"F0.imprint","IMPRINT",FACE,{"disambiguationData":[TD([[makeQuery(id+"F0.imprint","IMPRINT",EDGE,{"disambiguationData":[TD([[subQ2,1.0]])],"derivedFrom":subQ1}),-1.0]])]});}
            var Q577;
            {var subQ3=sQuery(id+"F0.wireOp",EDGE,"E3.24.0.85");Q577=makeQuery(id+"F0.imprint","IMPRINT",FACE,{"disambiguationData":[TD([[makeQuery(id+"F0.imprint","IMPRINT",EDGE,{"derivedFrom":subQ3}),1.0]])]});}
            var Q578;
            {var subQ0=sQuery(id+"F0.wireOp",EDGE,"E3.24.0.97");var subQ1=sQuery(id+"F0.wireOp",EDGE,"E3.24.0.44");var subQ2=makeQuery(id+"F0.imprint","INTERSECT",VERTEX,{"derivedFrom":[subQ1,subQ0]});Q578=makeQuery(id+"F0.imprint","IMPRINT",FACE,{"disambiguationData":[TD([[makeQuery(id+"F0.imprint","IMPRINT",EDGE,{"disambiguationData":[TD([[subQ2,1.0]])],"derivedFrom":subQ1}),-1.0]])]});}
            var Q579;
            {var subQ0=sQuery(id+"F0.wireOp",EDGE,"E3.17.0.97");var subQ1=sQuery(id+"F0.wireOp",EDGE,"E3.17.0.44");var subQ2=makeQuery(id+"F0.imprint","INTERSECT",VERTEX,{"derivedFrom":[subQ1,subQ0]});Q579=makeQuery(id+"F0.imprint","IMPRINT",FACE,{"disambiguationData":[TD([[makeQuery(id+"F0.imprint","IMPRINT",EDGE,{"disambiguationData":[TD([[subQ2,1.0]])],"derivedFrom":subQ1}),-1.0]])]});}
            var Q580;
            {var subQ0=sQuery(id+"F0.wireOp",EDGE,"E3.19.0.51");var subQ1=sQuery(id+"F0.wireOp",EDGE,"E3.19.0.10");var subQ2=makeQuery(id+"F0.imprint","INTERSECT",VERTEX,{"derivedFrom":[subQ1,subQ0]});Q580=makeQuery(id+"F0.imprint","IMPRINT",FACE,{"disambiguationData":[TD([[makeQuery(id+"F0.imprint","IMPRINT",EDGE,{"disambiguationData":[TD([[subQ2,-1.0]])],"derivedFrom":subQ1}),1.0]])]});}
            var Q581;
            {var subQ0=sQuery(id+"F0.wireOp",EDGE,"E3.18.0.68");var subQ1=sQuery(id+"F0.wireOp",EDGE,"E3.18.0.11");var subQ2=makeQuery(id+"F0.imprint","INTERSECT",VERTEX,{"derivedFrom":[subQ1,subQ0]});Q581=makeQuery(id+"F0.imprint","IMPRINT",FACE,{"disambiguationData":[TD([[makeQuery(id+"F0.imprint","IMPRINT",EDGE,{"disambiguationData":[TD([[subQ2,1.0]])],"derivedFrom":subQ1}),-1.0]])]});}
            var Q582;
            {var subQ0=sQuery(id+"F0.wireOp",EDGE,"E3.19.0.42");var subQ1=sQuery(id+"F0.wireOp",EDGE,"E3.19.0.16");var subQ2=makeQuery(id+"F0.imprint","INTERSECT",VERTEX,{"derivedFrom":[subQ1,subQ0]});Q582=makeQuery(id+"F0.imprint","IMPRINT",FACE,{"disambiguationData":[TD([[makeQuery(id+"F0.imprint","IMPRINT",EDGE,{"disambiguationData":[TD([[subQ2,-1.0]])],"derivedFrom":subQ1}),-1.0]])]});}
            var Q583;
            {var subQ0=sQuery(id+"F0.wireOp",EDGE,"E3.19.0.96");var subQ1=sQuery(id+"F0.wireOp",EDGE,"E3.19.0.43");var subQ2=makeQuery(id+"F0.imprint","INTERSECT",VERTEX,{"derivedFrom":[subQ1,subQ0]});Q583=makeQuery(id+"F0.imprint","IMPRINT",FACE,{"disambiguationData":[TD([[makeQuery(id+"F0.imprint","IMPRINT",EDGE,{"disambiguationData":[TD([[subQ2,1.0]])],"derivedFrom":subQ1}),-1.0]])]});}
            var Q584;
            {var subQ0=sQuery(id+"F0.wireOp",EDGE,"E3.18.0.97");var subQ1=sQuery(id+"F0.wireOp",EDGE,"E3.18.0.44");var subQ2=makeQuery(id+"F0.imprint","INTERSECT",VERTEX,{"derivedFrom":[subQ1,subQ0]});Q584=makeQuery(id+"F0.imprint","IMPRINT",FACE,{"disambiguationData":[TD([[makeQuery(id+"F0.imprint","IMPRINT",EDGE,{"disambiguationData":[TD([[subQ2,1.0]])],"derivedFrom":subQ1}),-1.0]])]});}
            var Q585;
            {var subQ0=sQuery(id+"F0.wireOp",EDGE,"E3.20.0.32");var subQ1=sQuery(id+"F0.wireOp",EDGE,"E3.20.0.0");var subQ2=makeQuery(id+"F0.imprint","INTERSECT",VERTEX,{"derivedFrom":[subQ1,subQ0]});Q585=makeQuery(id+"F0.imprint","IMPRINT",FACE,{"disambiguationData":[TD([[makeQuery(id+"F0.imprint","IMPRINT",EDGE,{"disambiguationData":[TD([[subQ2,1.0]])],"derivedFrom":subQ1}),-1.0]])]});}
            var Q586;
            {var subQ0=sQuery(id+"F0.wireOp",EDGE,"E3.20.0.96");var subQ1=sQuery(id+"F0.wireOp",EDGE,"E3.20.0.43");var subQ2=makeQuery(id+"F0.imprint","INTERSECT",VERTEX,{"derivedFrom":[subQ1,subQ0]});Q586=makeQuery(id+"F0.imprint","IMPRINT",FACE,{"disambiguationData":[TD([[makeQuery(id+"F0.imprint","IMPRINT",EDGE,{"disambiguationData":[TD([[subQ2,1.0]])],"derivedFrom":subQ1}),-1.0]])]});}
            var Q587;
            {var subQ0=sQuery(id+"F0.wireOp",EDGE,"E3.21.0.100");var subQ1=sQuery(id+"F0.wireOp",EDGE,"E3.21.0.52");var subQ2=makeQuery(id+"F0.imprint","INTERSECT",VERTEX,{"derivedFrom":[subQ1,subQ0]});Q587=makeQuery(id+"F0.imprint","IMPRINT",FACE,{"disambiguationData":[TD([[makeQuery(id+"F0.imprint","IMPRINT",EDGE,{"disambiguationData":[TD([[subQ2,1.0]])],"derivedFrom":subQ1}),-1.0]])]});}
            var Q588;
            {var subQ0=sQuery(id+"F0.wireOp",EDGE,"E3.21.0.32");var subQ1=sQuery(id+"F0.wireOp",EDGE,"E3.21.0.0");var subQ2=makeQuery(id+"F0.imprint","INTERSECT",VERTEX,{"derivedFrom":[subQ1,subQ0]});Q588=makeQuery(id+"F0.imprint","IMPRINT",FACE,{"disambiguationData":[TD([[makeQuery(id+"F0.imprint","IMPRINT",EDGE,{"disambiguationData":[TD([[subQ2,1.0]])],"derivedFrom":subQ1}),-1.0]])]});}
            var Q589;
            {var subQ0=sQuery(id+"F0.wireOp",EDGE,"E3.20.0.51");var subQ1=sQuery(id+"F0.wireOp",EDGE,"E3.20.0.10");var subQ2=makeQuery(id+"F0.imprint","INTERSECT",VERTEX,{"derivedFrom":[subQ1,subQ0]});Q589=makeQuery(id+"F0.imprint","IMPRINT",FACE,{"disambiguationData":[TD([[makeQuery(id+"F0.imprint","IMPRINT",EDGE,{"disambiguationData":[TD([[subQ2,-1.0]])],"derivedFrom":subQ1}),1.0]])]});}
            var Q590;
            {var subQ0=sQuery(id+"F0.wireOp",EDGE,"E3.21.0.64");Q590=makeQuery(id+"F0.imprint","IMPRINT",FACE,{"disambiguationData":[TD([[makeQuery(id+"F0.imprint","IMPRINT",EDGE,{"derivedFrom":subQ0}),-1.0]])]});}
            var Q591;
            {var subQ0=sQuery(id+"F0.wireOp",EDGE,"E3.20.0.42");var subQ1=sQuery(id+"F0.wireOp",EDGE,"E3.20.0.16");var subQ2=makeQuery(id+"F0.imprint","INTERSECT",VERTEX,{"derivedFrom":[subQ1,subQ0]});Q591=makeQuery(id+"F0.imprint","IMPRINT",FACE,{"disambiguationData":[TD([[makeQuery(id+"F0.imprint","IMPRINT",EDGE,{"disambiguationData":[TD([[subQ2,-1.0]])],"derivedFrom":subQ1}),-1.0]])]});}
            var Q592;
            {var subQ5=sQuery(id+"F0.wireOp",EDGE,"E3.22.0.53");Q592=makeQuery(id+"F0.imprint","IMPRINT",FACE,{"disambiguationData":[TD([[makeQuery(id+"F0.imprint","IMPRINT",EDGE,{"derivedFrom":subQ5}),-1.0]])]});}
            var Q593;
            {var subQ7=sQuery(id+"F0.wireOp",EDGE,"E3.21.0.54");Q593=makeQuery(id+"F0.imprint","IMPRINT",FACE,{"disambiguationData":[TD([[makeQuery(id+"F0.imprint","IMPRINT",EDGE,{"derivedFrom":subQ7}),-1.0]])]});}
            var Q594;
            {var subQ5=sQuery(id+"F0.wireOp",EDGE,"E3.22.0.22");Q594=makeQuery(id+"F0.imprint","IMPRINT",FACE,{"disambiguationData":[TD([[makeQuery(id+"F0.imprint","IMPRINT",EDGE,{"derivedFrom":subQ5}),-1.0]])]});}
            var Q595;
            {var subQ0=sQuery(id+"F0.wireOp",EDGE,"E3.24.0.68");var subQ1=sQuery(id+"F0.wireOp",EDGE,"E3.24.0.8");var subQ2=makeQuery(id+"F0.imprint","INTERSECT",VERTEX,{"derivedFrom":[subQ1,subQ0]});Q595=makeQuery(id+"F0.imprint","IMPRINT",FACE,{"disambiguationData":[TD([[makeQuery(id+"F0.imprint","IMPRINT",EDGE,{"disambiguationData":[TD([[subQ2,1.0]])],"derivedFrom":subQ1}),-1.0]])]});}
            var Q596;
            {var subQ0=sQuery(id+"F0.wireOp",EDGE,"E3.22.0.64");Q596=makeQuery(id+"F0.imprint","IMPRINT",FACE,{"disambiguationData":[TD([[makeQuery(id+"F0.imprint","IMPRINT",EDGE,{"derivedFrom":subQ0}),-1.0]])]});}
            var Q597;
            {var subQ5=sQuery(id+"F0.wireOp",EDGE,"E3.23.0.53");Q597=makeQuery(id+"F0.imprint","IMPRINT",FACE,{"disambiguationData":[TD([[makeQuery(id+"F0.imprint","IMPRINT",EDGE,{"derivedFrom":subQ5}),-1.0]])]});}
            var Q598;
            {var subQ3=sQuery(id+"F0.wireOp",EDGE,"E3.20.0.65");Q598=makeQuery(id+"F0.imprint","IMPRINT",FACE,{"disambiguationData":[TD([[makeQuery(id+"F0.imprint","IMPRINT",EDGE,{"derivedFrom":subQ3}),-1.0]])]});}
            var Q599;
            {var subQ0=sQuery(id+"F0.wireOp",EDGE,"E3.22.0.57");Q599=makeQuery(id+"F0.imprint","IMPRINT",FACE,{"disambiguationData":[TD([[makeQuery(id+"F0.imprint","IMPRINT",EDGE,{"derivedFrom":subQ0}),-1.0]])]});}
            var Q600;
            {var subQ0=sQuery(id+"F0.wireOp",EDGE,"E3.22.0.40");var subQ1=sQuery(id+"F0.wireOp",EDGE,"E3.22.0.18");var subQ2=makeQuery(id+"F0.imprint","INTERSECT",VERTEX,{"derivedFrom":[subQ1,subQ0]});Q600=makeQuery(id+"F0.imprint","IMPRINT",FACE,{"disambiguationData":[TD([[makeQuery(id+"F0.imprint","IMPRINT",EDGE,{"disambiguationData":[TD([[subQ2,-1.0]])],"derivedFrom":subQ1}),-1.0]])]});}
            var Q601;
            {var subQ10=sQuery(id+"F0.wireOp",EDGE,"E3.23.0.93");Q601=makeQuery(id+"F0.imprint","IMPRINT",FACE,{"disambiguationData":[TD([[makeQuery(id+"F0.imprint","IMPRINT",EDGE,{"derivedFrom":subQ10}),-1.0]])]});}
            var Q602;
            {var subQ7=sQuery(id+"F0.wireOp",EDGE,"E3.23.0.87");Q602=makeQuery(id+"F0.imprint","IMPRINT",FACE,{"disambiguationData":[TD([[makeQuery(id+"F0.imprint","IMPRINT",EDGE,{"derivedFrom":subQ7}),-1.0]])]});}
            var Q603;
            {var subQ0=sQuery(id+"F0.wireOp",EDGE,"E3.23.0.116");Q603=makeQuery(id+"F0.imprint","IMPRINT",FACE,{"disambiguationData":[TD([[makeQuery(id+"F0.imprint","IMPRINT",EDGE,{"derivedFrom":subQ0}),-1.0]])]});}
            var Q604;
            {var subQ0=sQuery(id+"F0.wireOp",EDGE,"E3.23.0.40");var subQ1=sQuery(id+"F0.wireOp",EDGE,"E3.23.0.18");var subQ2=makeQuery(id+"F0.imprint","INTERSECT",VERTEX,{"derivedFrom":[subQ1,subQ0]});Q604=makeQuery(id+"F0.imprint","IMPRINT",FACE,{"disambiguationData":[TD([[makeQuery(id+"F0.imprint","IMPRINT",EDGE,{"disambiguationData":[TD([[subQ2,-1.0]])],"derivedFrom":subQ1}),-1.0]])]});}
            var Q605;
            {var subQ0=sQuery(id+"F0.wireOp",EDGE,"E3.24.0.116");Q605=makeQuery(id+"F0.imprint","IMPRINT",FACE,{"disambiguationData":[TD([[makeQuery(id+"F0.imprint","IMPRINT",EDGE,{"derivedFrom":subQ0}),-1.0]])]});}
            var Q606;
            {var subQ0=sQuery(id+"F0.wireOp",EDGE,"E3.24.0.99");var subQ1=sQuery(id+"F0.wireOp",EDGE,"E3.24.0.49");var subQ2=makeQuery(id+"F0.imprint","INTERSECT",VERTEX,{"derivedFrom":[subQ1,subQ0]});Q606=makeQuery(id+"F0.imprint","IMPRINT",FACE,{"disambiguationData":[TD([[makeQuery(id+"F0.imprint","IMPRINT",EDGE,{"disambiguationData":[TD([[subQ2,1.0]])],"derivedFrom":subQ1}),-1.0]])]});}
            var Q607;
            {var subQ3=sQuery(id+"F0.wireOp",EDGE,"E3.24.0.83");Q607=makeQuery(id+"F0.imprint","IMPRINT",FACE,{"disambiguationData":[TD([[makeQuery(id+"F0.imprint","IMPRINT",EDGE,{"derivedFrom":subQ3}),1.0]])]});}
            var Q608;
            {var subQ3=sQuery(id+"F0.wireOp",EDGE,"E3.18.0.31");Q608=makeQuery(id+"F0.imprint","IMPRINT",FACE,{"disambiguationData":[TD([[makeQuery(id+"F0.imprint","IMPRINT",EDGE,{"derivedFrom":subQ3}),-1.0]])]});}
            var Q609;
            {var subQ5=sQuery(id+"F0.wireOp",EDGE,"E3.19.0.57");Q609=makeQuery(id+"F0.imprint","IMPRINT",FACE,{"disambiguationData":[TD([[makeQuery(id+"F0.imprint","IMPRINT",EDGE,{"derivedFrom":subQ5}),1.0]])]});}
            var Q610;
            {var subQ3=sQuery(id+"F0.wireOp",EDGE,"E3.19.0.65");Q610=makeQuery(id+"F0.imprint","IMPRINT",FACE,{"disambiguationData":[TD([[makeQuery(id+"F0.imprint","IMPRINT",EDGE,{"derivedFrom":subQ3}),-1.0]])]});}
            var Q611;
            {var subQ0=sQuery(id+"F0.wireOp",EDGE,"E3.18.0.39");var subQ1=sQuery(id+"F0.wireOp",EDGE,"E3.18.0.17");var subQ2=makeQuery(id+"F0.imprint","INTERSECT",VERTEX,{"derivedFrom":[subQ1,subQ0]});Q611=makeQuery(id+"F0.imprint","IMPRINT",FACE,{"disambiguationData":[TD([[makeQuery(id+"F0.imprint","IMPRINT",EDGE,{"disambiguationData":[TD([[subQ2,-1.0]])],"derivedFrom":subQ1}),-1.0]])]});}
            var Q612;
            {var subQ0=sQuery(id+"F0.wireOp",EDGE,"E3.18.0.91");var subQ1=sQuery(id+"F0.wireOp",EDGE,"E3.18.0.49");var subQ2=makeQuery(id+"F0.imprint","INTERSECT",VERTEX,{"derivedFrom":[subQ1,subQ0]});Q612=makeQuery(id+"F0.imprint","IMPRINT",FACE,{"disambiguationData":[TD([[makeQuery(id+"F0.imprint","IMPRINT",EDGE,{"disambiguationData":[TD([[subQ2,-1.0]])],"derivedFrom":subQ1}),-1.0]])]});}
            var Q613;
            {var subQ7=sQuery(id+"F0.wireOp",EDGE,"E3.22.0.54");Q613=makeQuery(id+"F0.imprint","IMPRINT",FACE,{"disambiguationData":[TD([[makeQuery(id+"F0.imprint","IMPRINT",EDGE,{"derivedFrom":subQ7}),-1.0]])]});}
            var Q614;
            {var subQ5=sQuery(id+"F0.wireOp",EDGE,"E3.23.0.56");Q614=makeQuery(id+"F0.imprint","IMPRINT",FACE,{"disambiguationData":[TD([[makeQuery(id+"F0.imprint","IMPRINT",EDGE,{"derivedFrom":subQ5}),1.0]])]});}
            var Q615;
            {var subQ0=sQuery(id+"F0.wireOp",EDGE,"E3.22.0.51");var subQ1=sQuery(id+"F0.wireOp",EDGE,"E3.22.0.10");var subQ2=makeQuery(id+"F0.imprint","INTERSECT",VERTEX,{"derivedFrom":[subQ1,subQ0]});Q615=makeQuery(id+"F0.imprint","IMPRINT",FACE,{"disambiguationData":[TD([[makeQuery(id+"F0.imprint","IMPRINT",EDGE,{"disambiguationData":[TD([[subQ2,-1.0]])],"derivedFrom":subQ1}),1.0]])]});}
            var Q616;
            {var subQ3=sQuery(id+"F0.wireOp",EDGE,"E3.21.0.118");Q616=makeQuery(id+"F0.imprint","IMPRINT",FACE,{"disambiguationData":[TD([[makeQuery(id+"F0.imprint","IMPRINT",EDGE,{"derivedFrom":subQ3}),1.0]])]});}
            var Q617;
            {var subQ0=sQuery(id+"F0.wireOp",EDGE,"E3.22.0.32");var subQ1=sQuery(id+"F0.wireOp",EDGE,"E3.22.0.0");var subQ2=makeQuery(id+"F0.imprint","INTERSECT",VERTEX,{"derivedFrom":[subQ1,subQ0]});Q617=makeQuery(id+"F0.imprint","IMPRINT",FACE,{"disambiguationData":[TD([[makeQuery(id+"F0.imprint","IMPRINT",EDGE,{"disambiguationData":[TD([[subQ2,1.0]])],"derivedFrom":subQ1}),-1.0]])]});}
            var Q618;
            {var subQ0=sQuery(id+"F0.wireOp",EDGE,"E3.22.0.63");Q618=makeQuery(id+"F0.imprint","IMPRINT",FACE,{"disambiguationData":[TD([[makeQuery(id+"F0.imprint","IMPRINT",EDGE,{"derivedFrom":subQ0}),-1.0]])]});}
            var Q619;
            {var subQ0=sQuery(id+"F0.wireOp",EDGE,"E3.23.0.100");var subQ1=sQuery(id+"F0.wireOp",EDGE,"E3.23.0.52");var subQ2=makeQuery(id+"F0.imprint","INTERSECT",VERTEX,{"derivedFrom":[subQ1,subQ0]});Q619=makeQuery(id+"F0.imprint","IMPRINT",FACE,{"disambiguationData":[TD([[makeQuery(id+"F0.imprint","IMPRINT",EDGE,{"disambiguationData":[TD([[subQ2,1.0]])],"derivedFrom":subQ1}),-1.0]])]});}
            var Q620;
            {var subQ5=sQuery(id+"F0.wireOp",EDGE,"E3.24.0.22");Q620=makeQuery(id+"F0.imprint","IMPRINT",FACE,{"disambiguationData":[TD([[makeQuery(id+"F0.imprint","IMPRINT",EDGE,{"derivedFrom":subQ5}),-1.0]])]});}
            var Q621;
            {var subQ0=sQuery(id+"F0.wireOp",EDGE,"E3.23.0.64");Q621=makeQuery(id+"F0.imprint","IMPRINT",FACE,{"disambiguationData":[TD([[makeQuery(id+"F0.imprint","IMPRINT",EDGE,{"derivedFrom":subQ0}),-1.0]])]});}
            var Q622;
            {var subQ0=sQuery(id+"F0.wireOp",EDGE,"E3.22.0.96");var subQ1=sQuery(id+"F0.wireOp",EDGE,"E3.22.0.43");var subQ2=makeQuery(id+"F0.imprint","INTERSECT",VERTEX,{"derivedFrom":[subQ1,subQ0]});Q622=makeQuery(id+"F0.imprint","IMPRINT",FACE,{"disambiguationData":[TD([[makeQuery(id+"F0.imprint","IMPRINT",EDGE,{"disambiguationData":[TD([[subQ2,1.0]])],"derivedFrom":subQ1}),-1.0]])]});}
            var Q623;
            {var subQ0=sQuery(id+"F0.wireOp",EDGE,"E3.24.0.100");var subQ1=sQuery(id+"F0.wireOp",EDGE,"E3.24.0.52");var subQ2=makeQuery(id+"F0.imprint","INTERSECT",VERTEX,{"derivedFrom":[subQ1,subQ0]});Q623=makeQuery(id+"F0.imprint","IMPRINT",FACE,{"disambiguationData":[TD([[makeQuery(id+"F0.imprint","IMPRINT",EDGE,{"disambiguationData":[TD([[subQ2,1.0]])],"derivedFrom":subQ1}),-1.0]])]});}
            var Q624;
            {var subQ3=sQuery(id+"F0.wireOp",EDGE,"E3.17.0.66");Q624=makeQuery(id+"F0.imprint","IMPRINT",FACE,{"disambiguationData":[TD([[makeQuery(id+"F0.imprint","IMPRINT",EDGE,{"derivedFrom":subQ3}),-1.0]])]});}
            var Q625;
            {var subQ0=sQuery(id+"F0.wireOp",EDGE,"E3.18.0.69");var subQ1=sQuery(id+"F0.wireOp",EDGE,"E3.18.0.12");var subQ2=makeQuery(id+"F0.imprint","INTERSECT",VERTEX,{"derivedFrom":[subQ1,subQ0]});Q625=makeQuery(id+"F0.imprint","IMPRINT",FACE,{"disambiguationData":[TD([[makeQuery(id+"F0.imprint","IMPRINT",EDGE,{"disambiguationData":[TD([[subQ2,1.0]])],"derivedFrom":subQ1}),-1.0]])]});}
            var Q626;
            {var subQ3=sQuery(id+"F0.wireOp",EDGE,"E3.18.0.66");Q626=makeQuery(id+"F0.imprint","IMPRINT",FACE,{"disambiguationData":[TD([[makeQuery(id+"F0.imprint","IMPRINT",EDGE,{"derivedFrom":subQ3}),-1.0]])]});}
            var Q627;
            {var subQ5=sQuery(id+"F0.wireOp",EDGE,"E3.18.0.93");Q627=makeQuery(id+"F0.imprint","IMPRINT",FACE,{"disambiguationData":[TD([[makeQuery(id+"F0.imprint","IMPRINT",EDGE,{"derivedFrom":subQ5}),1.0]])]});}
            var Q628;
            {var subQ0=sQuery(id+"F0.wireOp",EDGE,"E3.19.0.97");var subQ1=sQuery(id+"F0.wireOp",EDGE,"E3.19.0.44");var subQ2=makeQuery(id+"F0.imprint","INTERSECT",VERTEX,{"derivedFrom":[subQ1,subQ0]});Q628=makeQuery(id+"F0.imprint","IMPRINT",FACE,{"disambiguationData":[TD([[makeQuery(id+"F0.imprint","IMPRINT",EDGE,{"disambiguationData":[TD([[subQ2,1.0]])],"derivedFrom":subQ1}),-1.0]])]});}
            var Q629;
            {var subQ0=sQuery(id+"F0.wireOp",EDGE,"E3.21.0.96");var subQ1=sQuery(id+"F0.wireOp",EDGE,"E3.21.0.43");var subQ2=makeQuery(id+"F0.imprint","INTERSECT",VERTEX,{"derivedFrom":[subQ1,subQ0]});Q629=makeQuery(id+"F0.imprint","IMPRINT",FACE,{"disambiguationData":[TD([[makeQuery(id+"F0.imprint","IMPRINT",EDGE,{"disambiguationData":[TD([[subQ2,1.0]])],"derivedFrom":subQ1}),-1.0]])]});}
            var Q630;
            {var subQ0=sQuery(id+"F0.wireOp",EDGE,"E3.21.0.51");var subQ1=sQuery(id+"F0.wireOp",EDGE,"E3.21.0.10");var subQ2=makeQuery(id+"F0.imprint","INTERSECT",VERTEX,{"derivedFrom":[subQ1,subQ0]});Q630=makeQuery(id+"F0.imprint","IMPRINT",FACE,{"disambiguationData":[TD([[makeQuery(id+"F0.imprint","IMPRINT",EDGE,{"disambiguationData":[TD([[subQ2,-1.0]])],"derivedFrom":subQ1}),1.0]])]});}
            var Q631;
            {var subQ0=sQuery(id+"F0.wireOp",EDGE,"E3.22.0.116");Q631=makeQuery(id+"F0.imprint","IMPRINT",FACE,{"disambiguationData":[TD([[makeQuery(id+"F0.imprint","IMPRINT",EDGE,{"derivedFrom":subQ0}),-1.0]])]});}
            var Q632;
            {var subQ0=sQuery(id+"F0.wireOp",EDGE,"E3.21.0.40");var subQ1=sQuery(id+"F0.wireOp",EDGE,"E3.21.0.18");var subQ2=makeQuery(id+"F0.imprint","INTERSECT",VERTEX,{"derivedFrom":[subQ1,subQ0]});Q632=makeQuery(id+"F0.imprint","IMPRINT",FACE,{"disambiguationData":[TD([[makeQuery(id+"F0.imprint","IMPRINT",EDGE,{"disambiguationData":[TD([[subQ2,-1.0]])],"derivedFrom":subQ1}),-1.0]])]});}
            var Q633;
            {var subQ3=sQuery(id+"F0.wireOp",EDGE,"E3.24.0.103");Q633=makeQuery(id+"F0.imprint","IMPRINT",FACE,{"disambiguationData":[TD([[makeQuery(id+"F0.imprint","IMPRINT",EDGE,{"derivedFrom":subQ3}),1.0]])]});}
            var Q634;
            {var subQ0=sQuery(id+"F0.wireOp",EDGE,"E3.18.0.96");var subQ1=sQuery(id+"F0.wireOp",EDGE,"E3.18.0.39");var subQ2=makeQuery(id+"F0.imprint","INTERSECT",VERTEX,{"derivedFrom":[subQ1,subQ0]});Q634=makeQuery(id+"F0.imprint","IMPRINT",FACE,{"disambiguationData":[TD([[makeQuery(id+"F0.imprint","IMPRINT",EDGE,{"disambiguationData":[TD([[subQ2,1.0]])],"derivedFrom":subQ1}),-1.0]])]});}
            var Q635;
            {var subQ3=sQuery(id+"F0.wireOp",EDGE,"E3.18.0.65");Q635=makeQuery(id+"F0.imprint","IMPRINT",FACE,{"disambiguationData":[TD([[makeQuery(id+"F0.imprint","IMPRINT",EDGE,{"derivedFrom":subQ3}),-1.0]])]});}
            var Q636;
            {var subQ0=sQuery(id+"F0.wireOp",EDGE,"E3.20.0.57");Q636=makeQuery(id+"F0.imprint","IMPRINT",FACE,{"disambiguationData":[TD([[makeQuery(id+"F0.imprint","IMPRINT",EDGE,{"derivedFrom":subQ0}),-1.0]])]});}
            var Q637;
            {var subQ0=sQuery(id+"F0.wireOp",EDGE,"E3.19.0.72");var subQ1=sQuery(id+"F0.wireOp",EDGE,"E3.19.0.10");var subQ2=makeQuery(id+"F0.imprint","INTERSECT",VERTEX,{"derivedFrom":[subQ1,subQ0]});Q637=makeQuery(id+"F0.imprint","IMPRINT",FACE,{"disambiguationData":[TD([[makeQuery(id+"F0.imprint","IMPRINT",EDGE,{"disambiguationData":[TD([[subQ2,1.0]])],"derivedFrom":subQ1}),-1.0]])]});}
            var Q638;
            {var subQ0=sQuery(id+"F0.wireOp",EDGE,"E3.24.0.40");var subQ1=sQuery(id+"F0.wireOp",EDGE,"E3.24.0.18");var subQ2=makeQuery(id+"F0.imprint","INTERSECT",VERTEX,{"derivedFrom":[subQ1,subQ0]});Q638=makeQuery(id+"F0.imprint","IMPRINT",FACE,{"disambiguationData":[TD([[makeQuery(id+"F0.imprint","IMPRINT",EDGE,{"disambiguationData":[TD([[subQ2,-1.0]])],"derivedFrom":subQ1}),-1.0]])]});}
            var Q639;
            {var subQ3=sQuery(id+"F0.wireOp",EDGE,"E3.24.0.53");Q639=makeQuery(id+"F0.imprint","IMPRINT",FACE,{"disambiguationData":[TD([[makeQuery(id+"F0.imprint","IMPRINT",EDGE,{"derivedFrom":subQ3}),1.0]])]});}
            var Q640;
            {var subQ0=sQuery(id+"F0.wireOp",EDGE,"E3.18.0.8");var subQ1=sQuery(id+"F0.wireOp",EDGE,"E3.18.0.6");var subQ2=makeQuery(id+"F0.imprint","INTERSECT",VERTEX,{"derivedFrom":[subQ1,subQ0]});Q640=makeQuery(id+"F0.imprint","IMPRINT",FACE,{"disambiguationData":[TD([[makeQuery(id+"F0.imprint","IMPRINT",EDGE,{"disambiguationData":[TD([[subQ2,-1.0]])],"derivedFrom":subQ1}),-1.0]])]});}
            var Q641;
            {var subQ7=sQuery(id+"F0.wireOp",EDGE,"E3.18.0.83");Q641=makeQuery(id+"F0.imprint","IMPRINT",FACE,{"disambiguationData":[TD([[makeQuery(id+"F0.imprint","IMPRINT",EDGE,{"derivedFrom":subQ7}),-1.0]])]});}
            var Q642;
            {var subQ5=sQuery(id+"F0.wireOp",EDGE,"E3.17.0.53");Q642=makeQuery(id+"F0.imprint","IMPRINT",FACE,{"disambiguationData":[TD([[makeQuery(id+"F0.imprint","IMPRINT",EDGE,{"derivedFrom":subQ5}),-1.0]])]});}
            var Q643;
            {var subQ0=sQuery(id+"F0.wireOp",EDGE,"E3.19.0.39");var subQ1=sQuery(id+"F0.wireOp",EDGE,"E3.19.0.17");var subQ2=makeQuery(id+"F0.imprint","INTERSECT",VERTEX,{"derivedFrom":[subQ1,subQ0]});Q643=makeQuery(id+"F0.imprint","IMPRINT",FACE,{"disambiguationData":[TD([[makeQuery(id+"F0.imprint","IMPRINT",EDGE,{"disambiguationData":[TD([[subQ2,-1.0]])],"derivedFrom":subQ1}),-1.0]])]});}
            var Q644;
            {var subQ0=sQuery(id+"F0.wireOp",EDGE,"E3.18.0.35");var subQ1=sQuery(id+"F0.wireOp",EDGE,"E3.18.0.32");var subQ2=makeQuery(id+"F0.imprint","INTERSECT",VERTEX,{"derivedFrom":[subQ1,subQ0]});Q644=makeQuery(id+"F0.imprint","IMPRINT",FACE,{"disambiguationData":[TD([[makeQuery(id+"F0.imprint","IMPRINT",EDGE,{"disambiguationData":[TD([[subQ2,1.0]])],"derivedFrom":subQ1}),1.0]])]});}
            var Q645;
            {var subQ0=sQuery(id+"F0.wireOp",EDGE,"E3.19.0.35");var subQ1=sQuery(id+"F0.wireOp",EDGE,"E3.19.0.32");var subQ2=makeQuery(id+"F0.imprint","INTERSECT",VERTEX,{"derivedFrom":[subQ1,subQ0]});Q645=makeQuery(id+"F0.imprint","IMPRINT",FACE,{"disambiguationData":[TD([[makeQuery(id+"F0.imprint","IMPRINT",EDGE,{"disambiguationData":[TD([[subQ2,1.0]])],"derivedFrom":subQ1}),1.0]])]});}
            var Q646;
            {var subQ3=sQuery(id+"F0.wireOp",EDGE,"E3.20.0.31");Q646=makeQuery(id+"F0.imprint","IMPRINT",FACE,{"disambiguationData":[TD([[makeQuery(id+"F0.imprint","IMPRINT",EDGE,{"derivedFrom":subQ3}),-1.0]])]});}
            var Q647;
            {var subQ0=sQuery(id+"F0.wireOp",EDGE,"E3.19.0.8");var subQ1=sQuery(id+"F0.wireOp",EDGE,"E3.19.0.6");var subQ2=makeQuery(id+"F0.imprint","INTERSECT",VERTEX,{"derivedFrom":[subQ1,subQ0]});Q647=makeQuery(id+"F0.imprint","IMPRINT",FACE,{"disambiguationData":[TD([[makeQuery(id+"F0.imprint","IMPRINT",EDGE,{"disambiguationData":[TD([[subQ2,-1.0]])],"derivedFrom":subQ1}),-1.0]])]});}
            var Q648;
            {var subQ0=sQuery(id+"F0.wireOp",EDGE,"E3.21.0.91");var subQ1=sQuery(id+"F0.wireOp",EDGE,"E3.21.0.49");var subQ2=makeQuery(id+"F0.imprint","INTERSECT",VERTEX,{"derivedFrom":[subQ1,subQ0]});Q648=makeQuery(id+"F0.imprint","IMPRINT",FACE,{"disambiguationData":[TD([[makeQuery(id+"F0.imprint","IMPRINT",EDGE,{"disambiguationData":[TD([[subQ2,-1.0]])],"derivedFrom":subQ1}),-1.0]])]});}
            var Q649;
            {var subQ0=sQuery(id+"F0.wireOp",EDGE,"E3.22.0.37");var subQ5=sQuery(id+"F0.wireOp",EDGE,"E3.22.0.9");var subQ7=makeQuery(id+"F0.imprint","INTERSECT",VERTEX,{"derivedFrom":[subQ5,subQ0]});Q649=makeQuery(id+"F0.imprint","IMPRINT",FACE,{"disambiguationData":[TD([[makeQuery(id+"F0.imprint","IMPRINT",EDGE,{"disambiguationData":[TD([[subQ7,1.0]])],"derivedFrom":subQ5}),1.0]])]});}
            var Q650;
            {var subQ3=sQuery(id+"F0.wireOp",EDGE,"E3.21.0.31");Q650=makeQuery(id+"F0.imprint","IMPRINT",FACE,{"disambiguationData":[TD([[makeQuery(id+"F0.imprint","IMPRINT",EDGE,{"derivedFrom":subQ3}),-1.0]])]});}
            var Q651;
            {var subQ5=sQuery(id+"F0.wireOp",EDGE,"E3.21.0.82");Q651=makeQuery(id+"F0.imprint","IMPRINT",FACE,{"disambiguationData":[TD([[makeQuery(id+"F0.imprint","IMPRINT",EDGE,{"derivedFrom":subQ5}),-1.0]])]});}
            var Q652;
            {var subQ5=sQuery(id+"F0.wireOp",EDGE,"E3.22.0.93");Q652=makeQuery(id+"F0.imprint","IMPRINT",FACE,{"disambiguationData":[TD([[makeQuery(id+"F0.imprint","IMPRINT",EDGE,{"derivedFrom":subQ5}),1.0]])]});}
            var Q653;
            {var subQ3=sQuery(id+"F0.wireOp",EDGE,"E3.21.0.66");Q653=makeQuery(id+"F0.imprint","IMPRINT",FACE,{"disambiguationData":[TD([[makeQuery(id+"F0.imprint","IMPRINT",EDGE,{"derivedFrom":subQ3}),-1.0]])]});}
            var Q654;
            {var subQ3=sQuery(id+"F0.wireOp",EDGE,"E3.20.0.83");Q654=makeQuery(id+"F0.imprint","IMPRINT",FACE,{"disambiguationData":[TD([[makeQuery(id+"F0.imprint","IMPRINT",EDGE,{"derivedFrom":subQ3}),1.0]])]});}
            var Q655;
            {var subQ3=sQuery(id+"F0.wireOp",EDGE,"E3.17.0.54");Q655=makeQuery(id+"F0.imprint","IMPRINT",FACE,{"disambiguationData":[TD([[makeQuery(id+"F0.imprint","IMPRINT",EDGE,{"derivedFrom":subQ3}),1.0]])]});}
            var Q656;
            {var subQ0=sQuery(id+"F0.wireOp",EDGE,"E3.17.0.72");var subQ1=sQuery(id+"F0.wireOp",EDGE,"E3.17.0.10");var subQ2=makeQuery(id+"F0.imprint","INTERSECT",VERTEX,{"derivedFrom":[subQ1,subQ0]});Q656=makeQuery(id+"F0.imprint","IMPRINT",FACE,{"disambiguationData":[TD([[makeQuery(id+"F0.imprint","IMPRINT",EDGE,{"disambiguationData":[TD([[subQ2,1.0]])],"derivedFrom":subQ1}),-1.0]])]});}
            var Q657;
            {var subQ3=sQuery(id+"F0.wireOp",EDGE,"E3.19.0.83");Q657=makeQuery(id+"F0.imprint","IMPRINT",FACE,{"disambiguationData":[TD([[makeQuery(id+"F0.imprint","IMPRINT",EDGE,{"derivedFrom":subQ3}),1.0]])]});}
            var Q658;
            {var subQ3=sQuery(id+"F0.wireOp",EDGE,"E3.20.0.82");Q658=makeQuery(id+"F0.imprint","IMPRINT",FACE,{"disambiguationData":[TD([[makeQuery(id+"F0.imprint","IMPRINT",EDGE,{"derivedFrom":subQ3}),1.0]])]});}
            var Q659;
            {var subQ0=sQuery(id+"F0.wireOp",EDGE,"E3.18.0.99");var subQ1=sQuery(id+"F0.wireOp",EDGE,"E3.18.0.49");var subQ2=makeQuery(id+"F0.imprint","INTERSECT",VERTEX,{"derivedFrom":[subQ1,subQ0]});Q659=makeQuery(id+"F0.imprint","IMPRINT",FACE,{"disambiguationData":[TD([[makeQuery(id+"F0.imprint","IMPRINT",EDGE,{"disambiguationData":[TD([[subQ2,1.0]])],"derivedFrom":subQ1}),-1.0]])]});}
            var Q660;
            {var subQ3=sQuery(id+"F0.wireOp",EDGE,"E3.18.0.83");Q660=makeQuery(id+"F0.imprint","IMPRINT",FACE,{"disambiguationData":[TD([[makeQuery(id+"F0.imprint","IMPRINT",EDGE,{"derivedFrom":subQ3}),1.0]])]});}
            var Q661;
            {var subQ3=sQuery(id+"F0.wireOp",EDGE,"E3.18.0.56");Q661=makeQuery(id+"F0.imprint","IMPRINT",FACE,{"disambiguationData":[TD([[makeQuery(id+"F0.imprint","IMPRINT",EDGE,{"derivedFrom":subQ3}),-1.0]])]});}
            var Q662;
            {var subQ3=sQuery(id+"F0.wireOp",EDGE,"E3.22.0.82");Q662=makeQuery(id+"F0.imprint","IMPRINT",FACE,{"disambiguationData":[TD([[makeQuery(id+"F0.imprint","IMPRINT",EDGE,{"derivedFrom":subQ3}),1.0]])]});}
            var Q663;
            {var subQ3=sQuery(id+"F0.wireOp",EDGE,"E3.20.0.66");Q663=makeQuery(id+"F0.imprint","IMPRINT",FACE,{"disambiguationData":[TD([[makeQuery(id+"F0.imprint","IMPRINT",EDGE,{"derivedFrom":subQ3}),-1.0]])]});}
            var Q664;
            {var subQ3=sQuery(id+"F0.wireOp",EDGE,"E3.21.0.85");Q664=makeQuery(id+"F0.imprint","IMPRINT",FACE,{"disambiguationData":[TD([[makeQuery(id+"F0.imprint","IMPRINT",EDGE,{"derivedFrom":subQ3}),1.0]])]});}
            var Q665;
            {var subQ0=sQuery(id+"F0.wireOp",EDGE,"E3.21.0.97");var subQ1=sQuery(id+"F0.wireOp",EDGE,"E3.21.0.44");var subQ2=makeQuery(id+"F0.imprint","INTERSECT",VERTEX,{"derivedFrom":[subQ1,subQ0]});Q665=makeQuery(id+"F0.imprint","IMPRINT",FACE,{"disambiguationData":[TD([[makeQuery(id+"F0.imprint","IMPRINT",EDGE,{"disambiguationData":[TD([[subQ2,1.0]])],"derivedFrom":subQ1}),-1.0]])]});}
            var Q666;
            {var subQ0=sQuery(id+"F0.wireOp",EDGE,"E3.22.0.19");Q666=makeQuery(id+"F0.imprint","IMPRINT",FACE,{"disambiguationData":[TD([[makeQuery(id+"F0.imprint","IMPRINT",EDGE,{"derivedFrom":subQ0}),-1.0]])]});}
            var Q667;
            {var subQ3=sQuery(id+"F0.wireOp",EDGE,"E3.22.0.118");Q667=makeQuery(id+"F0.imprint","IMPRINT",FACE,{"disambiguationData":[TD([[makeQuery(id+"F0.imprint","IMPRINT",EDGE,{"derivedFrom":subQ3}),1.0]])]});}
            var Q668;
            {var subQ3=sQuery(id+"F0.wireOp",EDGE,"E3.21.0.55");Q668=makeQuery(id+"F0.imprint","IMPRINT",FACE,{"disambiguationData":[TD([[makeQuery(id+"F0.imprint","IMPRINT",EDGE,{"derivedFrom":subQ3}),1.0]])]});}
            var Q669;
            {var subQ0=sQuery(id+"F0.wireOp",EDGE,"E3.22.0.41");var subQ1=sQuery(id+"F0.wireOp",EDGE,"E3.22.0.13");var subQ2=makeQuery(id+"F0.imprint","INTERSECT",VERTEX,{"derivedFrom":[subQ1,subQ0]});Q669=makeQuery(id+"F0.imprint","IMPRINT",FACE,{"disambiguationData":[TD([[makeQuery(id+"F0.imprint","IMPRINT",EDGE,{"disambiguationData":[TD([[subQ2,-1.0]])],"derivedFrom":subQ1}),-1.0]])]});}
            var Q670;
            {var subQ3=sQuery(id+"F0.wireOp",EDGE,"E3.21.0.82");Q670=makeQuery(id+"F0.imprint","IMPRINT",FACE,{"disambiguationData":[TD([[makeQuery(id+"F0.imprint","IMPRINT",EDGE,{"derivedFrom":subQ3}),1.0]])]});}
            var Q671;
            {var subQ0=sQuery(id+"F0.wireOp",EDGE,"E3.23.0.96");var subQ1=sQuery(id+"F0.wireOp",EDGE,"E3.23.0.43");var subQ2=makeQuery(id+"F0.imprint","INTERSECT",VERTEX,{"derivedFrom":[subQ1,subQ0]});Q671=makeQuery(id+"F0.imprint","IMPRINT",FACE,{"disambiguationData":[TD([[makeQuery(id+"F0.imprint","IMPRINT",EDGE,{"disambiguationData":[TD([[subQ2,1.0]])],"derivedFrom":subQ1}),-1.0]])]});}
            var Q672;
            {var subQ3=sQuery(id+"F0.wireOp",EDGE,"E3.22.0.85");Q672=makeQuery(id+"F0.imprint","IMPRINT",FACE,{"disambiguationData":[TD([[makeQuery(id+"F0.imprint","IMPRINT",EDGE,{"derivedFrom":subQ3}),1.0]])]});}
            var Q673;
            {var subQ0=sQuery(id+"F0.wireOp",EDGE,"E3.23.0.19");Q673=makeQuery(id+"F0.imprint","IMPRINT",FACE,{"disambiguationData":[TD([[makeQuery(id+"F0.imprint","IMPRINT",EDGE,{"derivedFrom":subQ0}),-1.0]])]});}
            var Q674;
            {var subQ7=sQuery(id+"F0.wireOp",EDGE,"E3.24.0.54");Q674=makeQuery(id+"F0.imprint","IMPRINT",FACE,{"disambiguationData":[TD([[makeQuery(id+"F0.imprint","IMPRINT",EDGE,{"derivedFrom":subQ7}),-1.0]])]});}
            var Q675;
            {var subQ0=sQuery(id+"F0.wireOp",EDGE,"E3.17.0.51");var subQ1=sQuery(id+"F0.wireOp",EDGE,"E3.17.0.10");var subQ2=makeQuery(id+"F0.imprint","INTERSECT",VERTEX,{"derivedFrom":[subQ1,subQ0]});Q675=makeQuery(id+"F0.imprint","IMPRINT",FACE,{"disambiguationData":[TD([[makeQuery(id+"F0.imprint","IMPRINT",EDGE,{"disambiguationData":[TD([[subQ2,-1.0]])],"derivedFrom":subQ1}),1.0]])]});}
            var Q676;
            {var subQ7=sQuery(id+"F0.wireOp",EDGE,"E3.17.0.54");Q676=makeQuery(id+"F0.imprint","IMPRINT",FACE,{"disambiguationData":[TD([[makeQuery(id+"F0.imprint","IMPRINT",EDGE,{"derivedFrom":subQ7}),-1.0]])]});}
            var Q677;
            {var subQ0=sQuery(id+"F0.wireOp",EDGE,"E3.18.0.63");Q677=makeQuery(id+"F0.imprint","IMPRINT",FACE,{"disambiguationData":[TD([[makeQuery(id+"F0.imprint","IMPRINT",EDGE,{"derivedFrom":subQ0}),-1.0]])]});}
            var Q678;
            {var subQ0=sQuery(id+"F0.wireOp",EDGE,"E3.18.0.89");Q678=makeQuery(id+"F0.imprint","IMPRINT",FACE,{"disambiguationData":[TD([[makeQuery(id+"F0.imprint","IMPRINT",EDGE,{"derivedFrom":subQ0}),-1.0]])]});}
            var Q679;
            {var subQ3=sQuery(id+"F0.wireOp",EDGE,"E3.24.0.118");Q679=makeQuery(id+"F0.imprint","IMPRINT",FACE,{"disambiguationData":[TD([[makeQuery(id+"F0.imprint","IMPRINT",EDGE,{"derivedFrom":subQ3}),1.0]])]});}
            var Q680;
            {var subQ0=sQuery(id+"F0.wireOp",EDGE,"E3.19.0.71");var subQ1=sQuery(id+"F0.wireOp",EDGE,"E3.19.0.9");var subQ2=makeQuery(id+"F0.imprint","INTERSECT",VERTEX,{"derivedFrom":[subQ1,subQ0]});Q680=makeQuery(id+"F0.imprint","IMPRINT",FACE,{"disambiguationData":[TD([[makeQuery(id+"F0.imprint","IMPRINT",EDGE,{"disambiguationData":[TD([[subQ2,1.0]])],"derivedFrom":subQ1}),-1.0]])]});}
            var Q681;
            {var subQ5=sQuery(id+"F0.wireOp",EDGE,"E3.21.0.53");Q681=makeQuery(id+"F0.imprint","IMPRINT",FACE,{"disambiguationData":[TD([[makeQuery(id+"F0.imprint","IMPRINT",EDGE,{"derivedFrom":subQ5}),-1.0]])]});}
            var Q682;
            {var subQ0=sQuery(id+"F0.wireOp",EDGE,"E3.20.0.100");var subQ1=sQuery(id+"F0.wireOp",EDGE,"E3.20.0.52");var subQ2=makeQuery(id+"F0.imprint","INTERSECT",VERTEX,{"derivedFrom":[subQ1,subQ0]});Q682=makeQuery(id+"F0.imprint","IMPRINT",FACE,{"disambiguationData":[TD([[makeQuery(id+"F0.imprint","IMPRINT",EDGE,{"disambiguationData":[TD([[subQ2,1.0]])],"derivedFrom":subQ1}),-1.0]])]});}
            var Q683;
            {var subQ0=sQuery(id+"F0.wireOp",EDGE,"E3.22.0.8");var subQ1=sQuery(id+"F0.wireOp",EDGE,"E3.22.0.6");var subQ2=makeQuery(id+"F0.imprint","INTERSECT",VERTEX,{"derivedFrom":[subQ1,subQ0]});Q683=makeQuery(id+"F0.imprint","IMPRINT",FACE,{"disambiguationData":[TD([[makeQuery(id+"F0.imprint","IMPRINT",EDGE,{"disambiguationData":[TD([[subQ2,-1.0]])],"derivedFrom":subQ1}),-1.0]])]});}
            var Q684;
            {var subQ0=sQuery(id+"F0.wireOp",EDGE,"E3.23.0.68");var subQ1=sQuery(id+"F0.wireOp",EDGE,"E3.23.0.8");var subQ2=makeQuery(id+"F0.imprint","INTERSECT",VERTEX,{"derivedFrom":[subQ1,subQ0]});Q684=makeQuery(id+"F0.imprint","IMPRINT",FACE,{"disambiguationData":[TD([[makeQuery(id+"F0.imprint","IMPRINT",EDGE,{"disambiguationData":[TD([[subQ2,1.0]])],"derivedFrom":subQ1}),-1.0]])]});}
            var Q685;
            {var subQ0=sQuery(id+"F0.wireOp",EDGE,"E3.24.0.20");Q685=makeQuery(id+"F0.imprint","IMPRINT",FACE,{"disambiguationData":[TD([[makeQuery(id+"F0.imprint","IMPRINT",EDGE,{"derivedFrom":subQ0}),-1.0]])]});}
            var Q686;
            {var subQ7=sQuery(id+"F0.wireOp",EDGE,"E3.18.0.54");Q686=makeQuery(id+"F0.imprint","IMPRINT",FACE,{"disambiguationData":[TD([[makeQuery(id+"F0.imprint","IMPRINT",EDGE,{"derivedFrom":subQ7}),-1.0]])]});}
            var Q687;
            {var subQ5=sQuery(id+"F0.wireOp",EDGE,"E3.19.0.56");Q687=makeQuery(id+"F0.imprint","IMPRINT",FACE,{"disambiguationData":[TD([[makeQuery(id+"F0.imprint","IMPRINT",EDGE,{"derivedFrom":subQ5}),1.0]])]});}
            var Q688;
            {var subQ0=sQuery(id+"F0.wireOp",EDGE,"E3.21.0.39");var subQ1=sQuery(id+"F0.wireOp",EDGE,"E3.21.0.17");var subQ2=makeQuery(id+"F0.imprint","INTERSECT",VERTEX,{"derivedFrom":[subQ1,subQ0]});Q688=makeQuery(id+"F0.imprint","IMPRINT",FACE,{"disambiguationData":[TD([[makeQuery(id+"F0.imprint","IMPRINT",EDGE,{"disambiguationData":[TD([[subQ2,-1.0]])],"derivedFrom":subQ1}),-1.0]])]});}
            var Q689;
            {var subQ0=sQuery(id+"F0.wireOp",EDGE,"E3.20.0.75");var subQ1=sQuery(id+"F0.wireOp",EDGE,"E3.20.0.52");var subQ2=makeQuery(id+"F0.imprint","INTERSECT",VERTEX,{"derivedFrom":[subQ1,subQ0]});Q689=makeQuery(id+"F0.imprint","IMPRINT",FACE,{"disambiguationData":[TD([[makeQuery(id+"F0.imprint","IMPRINT",EDGE,{"disambiguationData":[TD([[subQ2,-1.0]])],"derivedFrom":subQ1}),-1.0]])]});}
            var Q690;
            {var subQ3=sQuery(id+"F0.wireOp",EDGE,"E3.23.0.31");Q690=makeQuery(id+"F0.imprint","IMPRINT",FACE,{"disambiguationData":[TD([[makeQuery(id+"F0.imprint","IMPRINT",EDGE,{"derivedFrom":subQ3}),-1.0]])]});}
            var Q691;
            {var subQ0=sQuery(id+"F0.wireOp",EDGE,"E3.22.0.68");var subQ1=sQuery(id+"F0.wireOp",EDGE,"E3.22.0.8");var subQ2=makeQuery(id+"F0.imprint","INTERSECT",VERTEX,{"derivedFrom":[subQ1,subQ0]});Q691=makeQuery(id+"F0.imprint","IMPRINT",FACE,{"disambiguationData":[TD([[makeQuery(id+"F0.imprint","IMPRINT",EDGE,{"disambiguationData":[TD([[subQ2,1.0]])],"derivedFrom":subQ1}),-1.0]])]});}
            var Q692;
            {var subQ0=sQuery(id+"F0.wireOp",EDGE,"E3.23.0.91");var subQ1=sQuery(id+"F0.wireOp",EDGE,"E3.23.0.49");var subQ2=makeQuery(id+"F0.imprint","INTERSECT",VERTEX,{"derivedFrom":[subQ1,subQ0]});Q692=makeQuery(id+"F0.imprint","IMPRINT",FACE,{"disambiguationData":[TD([[makeQuery(id+"F0.imprint","IMPRINT",EDGE,{"disambiguationData":[TD([[subQ2,-1.0]])],"derivedFrom":subQ1}),-1.0]])]});}
            var Q693;
            {var subQ3=sQuery(id+"F0.wireOp",EDGE,"E3.24.0.81");Q693=makeQuery(id+"F0.imprint","IMPRINT",FACE,{"disambiguationData":[TD([[makeQuery(id+"F0.imprint","IMPRINT",EDGE,{"derivedFrom":subQ3}),1.0]])]});}
            var Q694;
            {var subQ0=sQuery(id+"F0.wireOp",EDGE,"E3.23.0.20");Q694=makeQuery(id+"F0.imprint","IMPRINT",FACE,{"disambiguationData":[TD([[makeQuery(id+"F0.imprint","IMPRINT",EDGE,{"derivedFrom":subQ0}),-1.0]])]});}
            var Q695;
            {var subQ0=sQuery(id+"F0.wireOp",EDGE,"E3.18.0.51");var subQ1=sQuery(id+"F0.wireOp",EDGE,"E3.18.0.10");var subQ2=makeQuery(id+"F0.imprint","INTERSECT",VERTEX,{"derivedFrom":[subQ1,subQ0]});Q695=makeQuery(id+"F0.imprint","IMPRINT",FACE,{"disambiguationData":[TD([[makeQuery(id+"F0.imprint","IMPRINT",EDGE,{"disambiguationData":[TD([[subQ2,-1.0]])],"derivedFrom":subQ1}),1.0]])]});}
            var Q696;
            {var subQ0=sQuery(id+"F0.wireOp",EDGE,"E3.17.0.19");Q696=makeQuery(id+"F0.imprint","IMPRINT",FACE,{"disambiguationData":[TD([[makeQuery(id+"F0.imprint","IMPRINT",EDGE,{"derivedFrom":subQ0}),-1.0]])]});}
            var Q697;
            {var subQ3=sQuery(id+"F0.wireOp",EDGE,"E3.17.0.118");Q697=makeQuery(id+"F0.imprint","IMPRINT",FACE,{"disambiguationData":[TD([[makeQuery(id+"F0.imprint","IMPRINT",EDGE,{"derivedFrom":subQ3}),1.0]])]});}
            var Q698;
            {var subQ3=sQuery(id+"F0.wireOp",EDGE,"E3.3.0.54");Q698=makeQuery(id+"F0.imprint","IMPRINT",FACE,{"disambiguationData":[TD([[makeQuery(id+"F0.imprint","IMPRINT",EDGE,{"derivedFrom":subQ3}),1.0]])]});}
            var Q699;
            {var subQ0=sQuery(id+"F0.wireOp",EDGE,"E3.3.0.72");var subQ1=sQuery(id+"F0.wireOp",EDGE,"E3.3.0.10");var subQ2=makeQuery(id+"F0.imprint","INTERSECT",VERTEX,{"derivedFrom":[subQ1,subQ0]});Q699=makeQuery(id+"F0.imprint","IMPRINT",FACE,{"disambiguationData":[TD([[makeQuery(id+"F0.imprint","IMPRINT",EDGE,{"disambiguationData":[TD([[subQ2,1.0]])],"derivedFrom":subQ1}),-1.0]])]});}
            var Q700;
            {var subQ0=sQuery(id+"F0.wireOp",EDGE,"E3.4.0.41");var subQ1=sQuery(id+"F0.wireOp",EDGE,"E3.4.0.6");var subQ2=makeQuery(id+"F0.imprint","INTERSECT",VERTEX,{"derivedFrom":[subQ1,subQ0]});Q700=makeQuery(id+"F0.imprint","IMPRINT",FACE,{"disambiguationData":[TD([[makeQuery(id+"F0.imprint","IMPRINT",EDGE,{"disambiguationData":[TD([[subQ2,1.0]])],"derivedFrom":subQ1}),-1.0]])]});}
            var Q701;
            {var subQ3=sQuery(id+"F0.wireOp",EDGE,"E3.6.0.83");Q701=makeQuery(id+"F0.imprint","IMPRINT",FACE,{"disambiguationData":[TD([[makeQuery(id+"F0.imprint","IMPRINT",EDGE,{"derivedFrom":subQ3}),1.0]])]});}
            var Q702;
            {var subQ3=sQuery(id+"F0.wireOp",EDGE,"E3.8.0.55");Q702=makeQuery(id+"F0.imprint","IMPRINT",FACE,{"disambiguationData":[TD([[makeQuery(id+"F0.imprint","IMPRINT",EDGE,{"derivedFrom":subQ3}),1.0]])]});}
            var Q703;
            {var subQ3=sQuery(id+"F0.wireOp",EDGE,"E3.7.0.66");Q703=makeQuery(id+"F0.imprint","IMPRINT",FACE,{"disambiguationData":[TD([[makeQuery(id+"F0.imprint","IMPRINT",EDGE,{"derivedFrom":subQ3}),-1.0]])]});}
            var Q704;
            {var subQ0=sQuery(id+"F0.wireOp",EDGE,"E3.9.0.68");var subQ1=sQuery(id+"F0.wireOp",EDGE,"E3.9.0.11");var subQ2=makeQuery(id+"F0.imprint","INTERSECT",VERTEX,{"derivedFrom":[subQ1,subQ0]});Q704=makeQuery(id+"F0.imprint","IMPRINT",FACE,{"disambiguationData":[TD([[makeQuery(id+"F0.imprint","IMPRINT",EDGE,{"disambiguationData":[TD([[subQ2,1.0]])],"derivedFrom":subQ1}),-1.0]])]});}
            var Q705;
            {var subQ3=sQuery(id+"F0.wireOp",EDGE,"E3.9.0.85");Q705=makeQuery(id+"F0.imprint","IMPRINT",FACE,{"disambiguationData":[TD([[makeQuery(id+"F0.imprint","IMPRINT",EDGE,{"derivedFrom":subQ3}),1.0]])]});}
            var Q706;
            {var subQ3=sQuery(id+"F0.wireOp",EDGE,"E3.14.0.86");Q706=makeQuery(id+"F0.imprint","IMPRINT",FACE,{"disambiguationData":[TD([[makeQuery(id+"F0.imprint","IMPRINT",EDGE,{"derivedFrom":subQ3}),1.0]])]});}
            var Q707;
            {var subQ3=sQuery(id+"F0.wireOp",EDGE,"E3.17.0.31");Q707=makeQuery(id+"F0.imprint","IMPRINT",FACE,{"disambiguationData":[TD([[makeQuery(id+"F0.imprint","IMPRINT",EDGE,{"derivedFrom":subQ3}),-1.0]])]});}
            var Q708;
            {var subQ0=sQuery(id+"F0.wireOp",EDGE,"E3.16.0.39");var subQ1=sQuery(id+"F0.wireOp",EDGE,"E3.16.0.17");var subQ2=makeQuery(id+"F0.imprint","INTERSECT",VERTEX,{"derivedFrom":[subQ1,subQ0]});Q708=makeQuery(id+"F0.imprint","IMPRINT",FACE,{"disambiguationData":[TD([[makeQuery(id+"F0.imprint","IMPRINT",EDGE,{"disambiguationData":[TD([[subQ2,-1.0]])],"derivedFrom":subQ1}),-1.0]])]});}
            var Q709;
            {var subQ0=sQuery(id+"F0.wireOp",EDGE,"E3.15.0.75");var subQ1=sQuery(id+"F0.wireOp",EDGE,"E3.15.0.52");var subQ2=makeQuery(id+"F0.imprint","INTERSECT",VERTEX,{"derivedFrom":[subQ1,subQ0]});Q709=makeQuery(id+"F0.imprint","IMPRINT",FACE,{"disambiguationData":[TD([[makeQuery(id+"F0.imprint","IMPRINT",EDGE,{"disambiguationData":[TD([[subQ2,-1.0]])],"derivedFrom":subQ1}),-1.0]])]});}
            var Q710;
            {var subQ0=sQuery(id+"F0.wireOp",EDGE,"E2.3.0.1");var subQ1=sQuery(id+"F0.wireOp",EDGE,"E2.3.0.0");var subQ2=makeQuery(id+"F0.imprint","INTERSECT",VERTEX,{"derivedFrom":[subQ1,subQ0]});Q710=makeQuery(id+"F0.imprint","IMPRINT",FACE,{"disambiguationData":[TD([[makeQuery(id+"F0.imprint","IMPRINT",EDGE,{"disambiguationData":[TD([[subQ2,1.0]])],"derivedFrom":subQ1}),1.0]])]});}
            var Q711;
            {var subQ0=sQuery(id+"F0.wireOp",EDGE,"E3.1.0.91");var subQ1=sQuery(id+"F0.wireOp",EDGE,"E3.1.0.49");var subQ2=makeQuery(id+"F0.imprint","INTERSECT",VERTEX,{"derivedFrom":[subQ1,subQ0]});Q711=makeQuery(id+"F0.imprint","IMPRINT",FACE,{"disambiguationData":[TD([[makeQuery(id+"F0.imprint","IMPRINT",EDGE,{"disambiguationData":[TD([[subQ2,-1.0]])],"derivedFrom":subQ1}),-1.0]])]});}
            var Q712;
            {var subQ5=sQuery(id+"F0.wireOp",EDGE,"E3.1.0.82");Q712=makeQuery(id+"F0.imprint","IMPRINT",FACE,{"disambiguationData":[TD([[makeQuery(id+"F0.imprint","IMPRINT",EDGE,{"derivedFrom":subQ5}),-1.0]])]});}
            var Q713;
            {var subQ3=sQuery(id+"F0.wireOp",EDGE,"E3.1.0.31");Q713=makeQuery(id+"F0.imprint","IMPRINT",FACE,{"disambiguationData":[TD([[makeQuery(id+"F0.imprint","IMPRINT",EDGE,{"derivedFrom":subQ3}),-1.0]])]});}
            var Q714;
            {var subQ5=sQuery(id+"F0.wireOp",EDGE,"E3.2.0.57");Q714=makeQuery(id+"F0.imprint","IMPRINT",FACE,{"disambiguationData":[TD([[makeQuery(id+"F0.imprint","IMPRINT",EDGE,{"derivedFrom":subQ5}),1.0]])]});}
            var Q715;
            {var subQ3=sQuery(id+"F0.wireOp",EDGE,"E3.10.0.118");Q715=makeQuery(id+"F0.imprint","IMPRINT",FACE,{"disambiguationData":[TD([[makeQuery(id+"F0.imprint","IMPRINT",EDGE,{"derivedFrom":subQ3}),1.0]])]});}
            var Q716;
            {var subQ0=sQuery(id+"F0.wireOp",EDGE,"E3.11.0.96");var subQ1=sQuery(id+"F0.wireOp",EDGE,"E3.11.0.43");var subQ2=makeQuery(id+"F0.imprint","INTERSECT",VERTEX,{"derivedFrom":[subQ1,subQ0]});Q716=makeQuery(id+"F0.imprint","IMPRINT",FACE,{"disambiguationData":[TD([[makeQuery(id+"F0.imprint","IMPRINT",EDGE,{"disambiguationData":[TD([[subQ2,1.0]])],"derivedFrom":subQ1}),-1.0]])]});}
            var Q717;
            {var subQ0=sQuery(id+"F0.wireOp",EDGE,"E3.13.0.89");Q717=makeQuery(id+"F0.imprint","IMPRINT",FACE,{"disambiguationData":[TD([[makeQuery(id+"F0.imprint","IMPRINT",EDGE,{"derivedFrom":subQ0}),-1.0]])]});}
            var Q718;
            {var subQ5=sQuery(id+"F0.wireOp",EDGE,"E3.13.0.56");Q718=makeQuery(id+"F0.imprint","IMPRINT",FACE,{"disambiguationData":[TD([[makeQuery(id+"F0.imprint","IMPRINT",EDGE,{"derivedFrom":subQ5}),1.0]])]});}
            var Q719;
            {var subQ3=sQuery(id+"F0.wireOp",EDGE,"E3.16.0.65");Q719=makeQuery(id+"F0.imprint","IMPRINT",FACE,{"disambiguationData":[TD([[makeQuery(id+"F0.imprint","IMPRINT",EDGE,{"derivedFrom":subQ3}),-1.0]])]});}
            var Q720;
            {var subQ0=sQuery(id+"F0.wireOp",EDGE,"E3.15.0.91");var subQ1=sQuery(id+"F0.wireOp",EDGE,"E3.15.0.49");var subQ2=makeQuery(id+"F0.imprint","INTERSECT",VERTEX,{"derivedFrom":[subQ1,subQ0]});Q720=makeQuery(id+"F0.imprint","IMPRINT",FACE,{"disambiguationData":[TD([[makeQuery(id+"F0.imprint","IMPRINT",EDGE,{"disambiguationData":[TD([[subQ2,-1.0]])],"derivedFrom":subQ1}),-1.0]])]});}
            var Q721;
            {var subQ0=sQuery(id+"F0.wireOp",EDGE,"E3.1.0.72");var subQ1=sQuery(id+"F0.wireOp",EDGE,"E3.1.0.10");var subQ2=makeQuery(id+"F0.imprint","INTERSECT",VERTEX,{"derivedFrom":[subQ1,subQ0]});Q721=makeQuery(id+"F0.imprint","IMPRINT",FACE,{"disambiguationData":[TD([[makeQuery(id+"F0.imprint","IMPRINT",EDGE,{"disambiguationData":[TD([[subQ2,1.0]])],"derivedFrom":subQ1}),-1.0]])]});}
            var Q722;
            {var subQ3=sQuery(id+"F0.wireOp",EDGE,"E3.1.0.81");Q722=makeQuery(id+"F0.imprint","IMPRINT",FACE,{"disambiguationData":[TD([[makeQuery(id+"F0.imprint","IMPRINT",EDGE,{"derivedFrom":subQ3}),1.0]])]});}
            var Q723;
            {var subQ0=sQuery(id+"F0.wireOp",EDGE,"E3.2.0.57");Q723=makeQuery(id+"F0.imprint","IMPRINT",FACE,{"disambiguationData":[TD([[makeQuery(id+"F0.imprint","IMPRINT",EDGE,{"derivedFrom":subQ0}),-1.0]])]});}
            var Q724;
            {var subQ0=sQuery(id+"F0.wireOp",EDGE,"E3.4.0.99");var subQ1=sQuery(id+"F0.wireOp",EDGE,"E3.4.0.49");var subQ2=makeQuery(id+"F0.imprint","INTERSECT",VERTEX,{"derivedFrom":[subQ1,subQ0]});Q724=makeQuery(id+"F0.imprint","IMPRINT",FACE,{"disambiguationData":[TD([[makeQuery(id+"F0.imprint","IMPRINT",EDGE,{"disambiguationData":[TD([[subQ2,1.0]])],"derivedFrom":subQ1}),-1.0]])]});}
            var Q725;
            {var subQ3=sQuery(id+"F0.wireOp",EDGE,"E3.4.0.83");Q725=makeQuery(id+"F0.imprint","IMPRINT",FACE,{"disambiguationData":[TD([[makeQuery(id+"F0.imprint","IMPRINT",EDGE,{"derivedFrom":subQ3}),1.0]])]});}
            var Q726;
            {var subQ0=sQuery(id+"F0.wireOp",EDGE,"E3.14.0.39");var subQ1=sQuery(id+"F0.wireOp",EDGE,"E3.14.0.17");var subQ2=makeQuery(id+"F0.imprint","INTERSECT",VERTEX,{"derivedFrom":[subQ1,subQ0]});Q726=makeQuery(id+"F0.imprint","IMPRINT",FACE,{"disambiguationData":[TD([[makeQuery(id+"F0.imprint","IMPRINT",EDGE,{"disambiguationData":[TD([[subQ2,-1.0]])],"derivedFrom":subQ1}),-1.0]])]});}
            var Q727;
            {var subQ0=sQuery(id+"F0.wireOp",EDGE,"E3.13.0.8");var subQ1=sQuery(id+"F0.wireOp",EDGE,"E3.13.0.6");var subQ2=makeQuery(id+"F0.imprint","INTERSECT",VERTEX,{"derivedFrom":[subQ1,subQ0]});Q727=makeQuery(id+"F0.imprint","IMPRINT",FACE,{"disambiguationData":[TD([[makeQuery(id+"F0.imprint","IMPRINT",EDGE,{"disambiguationData":[TD([[subQ2,-1.0]])],"derivedFrom":subQ1}),-1.0]])]});}
            var Q728;
            {var subQ5=sQuery(id+"F0.wireOp",EDGE,"E3.12.0.53");Q728=makeQuery(id+"F0.imprint","IMPRINT",FACE,{"disambiguationData":[TD([[makeQuery(id+"F0.imprint","IMPRINT",EDGE,{"derivedFrom":subQ5}),-1.0]])]});}
            var Q729;
            {var subQ3=sQuery(id+"F0.wireOp",EDGE,"E3.12.0.86");Q729=makeQuery(id+"F0.imprint","IMPRINT",FACE,{"disambiguationData":[TD([[makeQuery(id+"F0.imprint","IMPRINT",EDGE,{"derivedFrom":subQ3}),1.0]])]});}
            var Q730;
            {var subQ0=sQuery(id+"F0.wireOp",EDGE,"E3.7.0.97");var subQ1=sQuery(id+"F0.wireOp",EDGE,"E3.7.0.44");var subQ2=makeQuery(id+"F0.imprint","INTERSECT",VERTEX,{"derivedFrom":[subQ1,subQ0]});Q730=makeQuery(id+"F0.imprint","IMPRINT",FACE,{"disambiguationData":[TD([[makeQuery(id+"F0.imprint","IMPRINT",EDGE,{"disambiguationData":[TD([[subQ2,1.0]])],"derivedFrom":subQ1}),-1.0]])]});}
            var Q731;
            {var subQ3=sQuery(id+"F0.wireOp",EDGE,"E3.7.0.85");Q731=makeQuery(id+"F0.imprint","IMPRINT",FACE,{"disambiguationData":[TD([[makeQuery(id+"F0.imprint","IMPRINT",EDGE,{"derivedFrom":subQ3}),1.0]])]});}
            var Q732;
            {var subQ0=sQuery(id+"F0.wireOp",EDGE,"E3.7.0.68");var subQ1=sQuery(id+"F0.wireOp",EDGE,"E3.7.0.11");var subQ2=makeQuery(id+"F0.imprint","INTERSECT",VERTEX,{"derivedFrom":[subQ1,subQ0]});Q732=makeQuery(id+"F0.imprint","IMPRINT",FACE,{"disambiguationData":[TD([[makeQuery(id+"F0.imprint","IMPRINT",EDGE,{"disambiguationData":[TD([[subQ2,1.0]])],"derivedFrom":subQ1}),-1.0]])]});}
            var Q733;
            {var subQ3=sQuery(id+"F0.wireOp",EDGE,"E3.6.0.103");Q733=makeQuery(id+"F0.imprint","IMPRINT",FACE,{"disambiguationData":[TD([[makeQuery(id+"F0.imprint","IMPRINT",EDGE,{"derivedFrom":subQ3}),1.0]])]});}
            var Q734;
            {var subQ3=sQuery(id+"F0.wireOp",EDGE,"E3.8.0.118");Q734=makeQuery(id+"F0.imprint","IMPRINT",FACE,{"disambiguationData":[TD([[makeQuery(id+"F0.imprint","IMPRINT",EDGE,{"derivedFrom":subQ3}),1.0]])]});}
            var Q735;
            {var subQ0=sQuery(id+"F0.wireOp",EDGE,"E3.8.0.41");var subQ1=sQuery(id+"F0.wireOp",EDGE,"E3.8.0.13");var subQ2=makeQuery(id+"F0.imprint","INTERSECT",VERTEX,{"derivedFrom":[subQ1,subQ0]});Q735=makeQuery(id+"F0.imprint","IMPRINT",FACE,{"disambiguationData":[TD([[makeQuery(id+"F0.imprint","IMPRINT",EDGE,{"disambiguationData":[TD([[subQ2,-1.0]])],"derivedFrom":subQ1}),-1.0]])]});}
            var Q736;
            {var subQ0=sQuery(id+"F0.wireOp",EDGE,"E3.10.0.32");var subQ1=sQuery(id+"F0.wireOp",EDGE,"E3.10.0.0");var subQ2=makeQuery(id+"F0.imprint","INTERSECT",VERTEX,{"derivedFrom":[subQ1,subQ0]});Q736=makeQuery(id+"F0.imprint","IMPRINT",FACE,{"disambiguationData":[TD([[makeQuery(id+"F0.imprint","IMPRINT",EDGE,{"disambiguationData":[TD([[subQ2,1.0]])],"derivedFrom":subQ1}),-1.0]])]});}
            var Q737;
            {var subQ5=sQuery(id+"F0.wireOp",EDGE,"E3.12.0.22");Q737=makeQuery(id+"F0.imprint","IMPRINT",FACE,{"disambiguationData":[TD([[makeQuery(id+"F0.imprint","IMPRINT",EDGE,{"derivedFrom":subQ5}),-1.0]])]});}
            var Q738;
            {var subQ0=sQuery(id+"F0.wireOp",EDGE,"E3.2.0.96");var subQ1=sQuery(id+"F0.wireOp",EDGE,"E3.2.0.43");var subQ2=makeQuery(id+"F0.imprint","INTERSECT",VERTEX,{"derivedFrom":[subQ1,subQ0]});Q738=makeQuery(id+"F0.imprint","IMPRINT",FACE,{"disambiguationData":[TD([[makeQuery(id+"F0.imprint","IMPRINT",EDGE,{"disambiguationData":[TD([[subQ2,1.0]])],"derivedFrom":subQ1}),-1.0]])]});}
            var Q739;
            {var subQ0=sQuery(id+"F0.wireOp",EDGE,"E3.4.0.100");var subQ1=sQuery(id+"F0.wireOp",EDGE,"E3.4.0.52");var subQ2=makeQuery(id+"F0.imprint","INTERSECT",VERTEX,{"derivedFrom":[subQ1,subQ0]});Q739=makeQuery(id+"F0.imprint","IMPRINT",FACE,{"disambiguationData":[TD([[makeQuery(id+"F0.imprint","IMPRINT",EDGE,{"disambiguationData":[TD([[subQ2,1.0]])],"derivedFrom":subQ1}),-1.0]])]});}
            var Q740;
            {var subQ0=sQuery(id+"F0.wireOp",EDGE,"E3.4.0.89");Q740=makeQuery(id+"F0.imprint","IMPRINT",FACE,{"disambiguationData":[TD([[makeQuery(id+"F0.imprint","IMPRINT",EDGE,{"derivedFrom":subQ0}),-1.0]])]});}
            var Q741;
            {var subQ5=sQuery(id+"F0.wireOp",EDGE,"E3.4.0.56");Q741=makeQuery(id+"F0.imprint","IMPRINT",FACE,{"disambiguationData":[TD([[makeQuery(id+"F0.imprint","IMPRINT",EDGE,{"derivedFrom":subQ5}),1.0]])]});}
            var Q742;
            {var subQ0=sQuery(id+"F0.wireOp",EDGE,"E3.6.0.8");var subQ1=sQuery(id+"F0.wireOp",EDGE,"E3.6.0.6");var subQ2=makeQuery(id+"F0.imprint","INTERSECT",VERTEX,{"derivedFrom":[subQ1,subQ0]});Q742=makeQuery(id+"F0.imprint","IMPRINT",FACE,{"disambiguationData":[TD([[makeQuery(id+"F0.imprint","IMPRINT",EDGE,{"disambiguationData":[TD([[subQ2,-1.0]])],"derivedFrom":subQ1}),-1.0]])]});}
            var Q743;
            {var subQ5=sQuery(id+"F0.wireOp",EDGE,"E3.5.0.53");Q743=makeQuery(id+"F0.imprint","IMPRINT",FACE,{"disambiguationData":[TD([[makeQuery(id+"F0.imprint","IMPRINT",EDGE,{"derivedFrom":subQ5}),-1.0]])]});}
            var Q744;
            {var subQ3=sQuery(id+"F0.wireOp",EDGE,"E3.5.0.86");Q744=makeQuery(id+"F0.imprint","IMPRINT",FACE,{"disambiguationData":[TD([[makeQuery(id+"F0.imprint","IMPRINT",EDGE,{"derivedFrom":subQ3}),1.0]])]});}
            var Q745;
            {var subQ0=sQuery(id+"F0.wireOp",EDGE,"E3.14.0.69");var subQ1=sQuery(id+"F0.wireOp",EDGE,"E3.14.0.12");var subQ2=makeQuery(id+"F0.imprint","INTERSECT",VERTEX,{"derivedFrom":[subQ1,subQ0]});Q745=makeQuery(id+"F0.imprint","IMPRINT",FACE,{"disambiguationData":[TD([[makeQuery(id+"F0.imprint","IMPRINT",EDGE,{"disambiguationData":[TD([[subQ2,1.0]])],"derivedFrom":subQ1}),-1.0]])]});}
            var Q746;
            {var subQ0=sQuery(id+"F0.wireOp",EDGE,"E3.13.0.99");var subQ1=sQuery(id+"F0.wireOp",EDGE,"E3.13.0.49");var subQ2=makeQuery(id+"F0.imprint","INTERSECT",VERTEX,{"derivedFrom":[subQ1,subQ0]});Q746=makeQuery(id+"F0.imprint","IMPRINT",FACE,{"disambiguationData":[TD([[makeQuery(id+"F0.imprint","IMPRINT",EDGE,{"disambiguationData":[TD([[subQ2,1.0]])],"derivedFrom":subQ1}),-1.0]])]});}
            var Q747;
            {var subQ3=sQuery(id+"F0.wireOp",EDGE,"E3.15.0.55");Q747=makeQuery(id+"F0.imprint","IMPRINT",FACE,{"disambiguationData":[TD([[makeQuery(id+"F0.imprint","IMPRINT",EDGE,{"derivedFrom":subQ3}),1.0]])]});}
            var Q748;
            {var subQ0=sQuery(id+"F0.wireOp",EDGE,"E3.14.0.94");var subQ1=sQuery(id+"F0.wireOp",EDGE,"E3.14.0.42");var subQ2=makeQuery(id+"F0.imprint","INTERSECT",VERTEX,{"derivedFrom":[subQ1,subQ0]});Q748=makeQuery(id+"F0.imprint","IMPRINT",FACE,{"disambiguationData":[TD([[makeQuery(id+"F0.imprint","IMPRINT",EDGE,{"disambiguationData":[TD([[subQ2,1.0]])],"derivedFrom":subQ1}),-1.0]])]});}
            var Q749;
            {var subQ0=sQuery(id+"F0.wireOp",EDGE,"E3.13.0.116");Q749=makeQuery(id+"F0.imprint","IMPRINT",FACE,{"disambiguationData":[TD([[makeQuery(id+"F0.imprint","IMPRINT",EDGE,{"derivedFrom":subQ0}),-1.0]])]});}
            var Q750;
            {var subQ0=sQuery(id+"F0.wireOp",EDGE,"E3.7.0.68");var subQ1=sQuery(id+"F0.wireOp",EDGE,"E3.7.0.8");var subQ2=makeQuery(id+"F0.imprint","INTERSECT",VERTEX,{"derivedFrom":[subQ1,subQ0]});Q750=makeQuery(id+"F0.imprint","IMPRINT",FACE,{"disambiguationData":[TD([[makeQuery(id+"F0.imprint","IMPRINT",EDGE,{"disambiguationData":[TD([[subQ2,1.0]])],"derivedFrom":subQ1}),-1.0]])]});}
            var Q751;
            {var subQ3=sQuery(id+"F0.wireOp",EDGE,"E3.8.0.31");Q751=makeQuery(id+"F0.imprint","IMPRINT",FACE,{"disambiguationData":[TD([[makeQuery(id+"F0.imprint","IMPRINT",EDGE,{"derivedFrom":subQ3}),-1.0]])]});}
            var Q752;
            {var subQ3=sQuery(id+"F0.wireOp",EDGE,"E3.9.0.65");Q752=makeQuery(id+"F0.imprint","IMPRINT",FACE,{"disambiguationData":[TD([[makeQuery(id+"F0.imprint","IMPRINT",EDGE,{"derivedFrom":subQ3}),-1.0]])]});}
            var Q753;
            {var subQ5=sQuery(id+"F0.wireOp",EDGE,"E3.9.0.57");Q753=makeQuery(id+"F0.imprint","IMPRINT",FACE,{"disambiguationData":[TD([[makeQuery(id+"F0.imprint","IMPRINT",EDGE,{"derivedFrom":subQ5}),1.0]])]});}
            var Q754;
            {var subQ0=sQuery(id+"F0.wireOp",EDGE,"E3.11.0.57");Q754=makeQuery(id+"F0.imprint","IMPRINT",FACE,{"disambiguationData":[TD([[makeQuery(id+"F0.imprint","IMPRINT",EDGE,{"derivedFrom":subQ0}),-1.0]])]});}
            var Q755;
            {var subQ3=sQuery(id+"F0.wireOp",EDGE,"E3.10.0.54");Q755=makeQuery(id+"F0.imprint","IMPRINT",FACE,{"disambiguationData":[TD([[makeQuery(id+"F0.imprint","IMPRINT",EDGE,{"derivedFrom":subQ3}),1.0]])]});}
            var Q756;
            {var subQ0=sQuery(id+"F0.wireOp",EDGE,"E3.10.0.72");var subQ1=sQuery(id+"F0.wireOp",EDGE,"E3.10.0.10");var subQ2=makeQuery(id+"F0.imprint","INTERSECT",VERTEX,{"derivedFrom":[subQ1,subQ0]});Q756=makeQuery(id+"F0.imprint","IMPRINT",FACE,{"disambiguationData":[TD([[makeQuery(id+"F0.imprint","IMPRINT",EDGE,{"disambiguationData":[TD([[subQ2,1.0]])],"derivedFrom":subQ1}),-1.0]])]});}
            var Q757;
            {var subQ3=sQuery(id+"F0.wireOp",EDGE,"E3.10.0.81");Q757=makeQuery(id+"F0.imprint","IMPRINT",FACE,{"disambiguationData":[TD([[makeQuery(id+"F0.imprint","IMPRINT",EDGE,{"derivedFrom":subQ3}),1.0]])]});}
            var Q758;
            {var subQ7=sQuery(id+"F0.wireOp",EDGE,"E3.12.0.87");Q758=makeQuery(id+"F0.imprint","IMPRINT",FACE,{"disambiguationData":[TD([[makeQuery(id+"F0.imprint","IMPRINT",EDGE,{"derivedFrom":subQ7}),-1.0]])]});}
            var Q759;
            {var subQ10=sQuery(id+"F0.wireOp",EDGE,"E3.12.0.93");Q759=makeQuery(id+"F0.imprint","IMPRINT",FACE,{"disambiguationData":[TD([[makeQuery(id+"F0.imprint","IMPRINT",EDGE,{"derivedFrom":subQ10}),-1.0]])]});}
            var Q760;
            {var subQ3=sQuery(id+"F0.wireOp",EDGE,"E3.11.0.84");Q760=makeQuery(id+"F0.imprint","IMPRINT",FACE,{"disambiguationData":[TD([[makeQuery(id+"F0.imprint","IMPRINT",EDGE,{"derivedFrom":subQ3}),1.0]])]});}
            var Q761;
            {var subQ3=sQuery(id+"F0.wireOp",EDGE,"E3.13.0.83");Q761=makeQuery(id+"F0.imprint","IMPRINT",FACE,{"disambiguationData":[TD([[makeQuery(id+"F0.imprint","IMPRINT",EDGE,{"derivedFrom":subQ3}),1.0]])]});}
            var Q762;
            {var subQ3=sQuery(id+"F0.wireOp",EDGE,"E3.13.0.56");Q762=makeQuery(id+"F0.imprint","IMPRINT",FACE,{"disambiguationData":[TD([[makeQuery(id+"F0.imprint","IMPRINT",EDGE,{"derivedFrom":subQ3}),-1.0]])]});}
            var Q763;
            {var subQ0=sQuery(id+"F0.wireOp",EDGE,"E3.12.0.40");var subQ1=sQuery(id+"F0.wireOp",EDGE,"E3.12.0.18");var subQ2=makeQuery(id+"F0.imprint","INTERSECT",VERTEX,{"derivedFrom":[subQ1,subQ0]});Q763=makeQuery(id+"F0.imprint","IMPRINT",FACE,{"disambiguationData":[TD([[makeQuery(id+"F0.imprint","IMPRINT",EDGE,{"disambiguationData":[TD([[subQ2,-1.0]])],"derivedFrom":subQ1}),-1.0]])]});}
            var Q764;
            {var subQ7=sQuery(id+"F0.wireOp",EDGE,"E3.14.0.87");Q764=makeQuery(id+"F0.imprint","IMPRINT",FACE,{"disambiguationData":[TD([[makeQuery(id+"F0.imprint","IMPRINT",EDGE,{"derivedFrom":subQ7}),-1.0]])]});}
            var Q765;
            {var subQ0=sQuery(id+"F0.wireOp",EDGE,"E3.13.0.41");var subQ1=sQuery(id+"F0.wireOp",EDGE,"E3.13.0.6");var subQ2=makeQuery(id+"F0.imprint","INTERSECT",VERTEX,{"derivedFrom":[subQ1,subQ0]});Q765=makeQuery(id+"F0.imprint","IMPRINT",FACE,{"disambiguationData":[TD([[makeQuery(id+"F0.imprint","IMPRINT",EDGE,{"disambiguationData":[TD([[subQ2,1.0]])],"derivedFrom":subQ1}),-1.0]])]});}
            var Q766;
            {var subQ0=sQuery(id+"F0.wireOp",EDGE,"E3.16.0.69");var subQ1=sQuery(id+"F0.wireOp",EDGE,"E3.16.0.12");var subQ2=makeQuery(id+"F0.imprint","INTERSECT",VERTEX,{"derivedFrom":[subQ1,subQ0]});Q766=makeQuery(id+"F0.imprint","IMPRINT",FACE,{"disambiguationData":[TD([[makeQuery(id+"F0.imprint","IMPRINT",EDGE,{"disambiguationData":[TD([[subQ2,1.0]])],"derivedFrom":subQ1}),-1.0]])]});}
            var Q767;
            {var subQ0=sQuery(id+"F0.wireOp",EDGE,"E3.15.0.116");Q767=makeQuery(id+"F0.imprint","IMPRINT",FACE,{"disambiguationData":[TD([[makeQuery(id+"F0.imprint","IMPRINT",EDGE,{"derivedFrom":subQ0}),-1.0]])]});}
            var Q768;
            {var subQ5=sQuery(id+"F0.wireOp",EDGE,"E2.8.0.4");Q768=makeQuery(id+"F0.imprint","IMPRINT",FACE,{"disambiguationData":[TD([[makeQuery(id+"F0.imprint","IMPRINT",EDGE,{"derivedFrom":subQ5}),1.0]])]});}
            var Q769;
            {var subQ5=sQuery(id+"F0.wireOp",EDGE,"E2.4.0.4");Q769=makeQuery(id+"F0.imprint","IMPRINT",FACE,{"disambiguationData":[TD([[makeQuery(id+"F0.imprint","IMPRINT",EDGE,{"derivedFrom":subQ5}),1.0]])]});}
            var Q770;
            {var subQ0=sQuery(id+"F0.wireOp",EDGE,"E3.8.0.35");var subQ1=sQuery(id+"F0.wireOp",EDGE,"E3.8.0.32");var subQ2=makeQuery(id+"F0.imprint","INTERSECT",VERTEX,{"derivedFrom":[subQ1,subQ0]});Q770=makeQuery(id+"F0.imprint","IMPRINT",FACE,{"disambiguationData":[TD([[makeQuery(id+"F0.imprint","IMPRINT",EDGE,{"disambiguationData":[TD([[subQ2,1.0]])],"derivedFrom":subQ1}),1.0]])]});}
            var Q771;
            {var subQ0=sQuery(id+"F0.wireOp",EDGE,"E3.8.0.8");var subQ1=sQuery(id+"F0.wireOp",EDGE,"E3.8.0.6");var subQ2=makeQuery(id+"F0.imprint","INTERSECT",VERTEX,{"derivedFrom":[subQ1,subQ0]});Q771=makeQuery(id+"F0.imprint","IMPRINT",FACE,{"disambiguationData":[TD([[makeQuery(id+"F0.imprint","IMPRINT",EDGE,{"disambiguationData":[TD([[subQ2,-1.0]])],"derivedFrom":subQ1}),-1.0]])]});}
            var Q772;
            {var subQ0=sQuery(id+"F0.wireOp",EDGE,"E3.10.0.20");Q772=makeQuery(id+"F0.imprint","IMPRINT",FACE,{"disambiguationData":[TD([[makeQuery(id+"F0.imprint","IMPRINT",EDGE,{"derivedFrom":subQ0}),-1.0]])]});}
            var Q773;
            {var subQ3=sQuery(id+"F0.wireOp",EDGE,"E3.13.0.84");Q773=makeQuery(id+"F0.imprint","IMPRINT",FACE,{"disambiguationData":[TD([[makeQuery(id+"F0.imprint","IMPRINT",EDGE,{"derivedFrom":subQ3}),1.0]])]});}
            var Q774;
            {var subQ3=sQuery(id+"F0.wireOp",EDGE,"E3.12.0.54");Q774=makeQuery(id+"F0.imprint","IMPRINT",FACE,{"disambiguationData":[TD([[makeQuery(id+"F0.imprint","IMPRINT",EDGE,{"derivedFrom":subQ3}),1.0]])]});}
            var Q775;
            {var subQ0=sQuery(id+"F0.wireOp",EDGE,"E3.2.0.97");var subQ1=sQuery(id+"F0.wireOp",EDGE,"E3.2.0.44");var subQ2=makeQuery(id+"F0.imprint","INTERSECT",VERTEX,{"derivedFrom":[subQ1,subQ0]});Q775=makeQuery(id+"F0.imprint","IMPRINT",FACE,{"disambiguationData":[TD([[makeQuery(id+"F0.imprint","IMPRINT",EDGE,{"disambiguationData":[TD([[subQ2,1.0]])],"derivedFrom":subQ1}),-1.0]])]});}
            var Q776;
            {var subQ0=sQuery(id+"F0.wireOp",EDGE,"E3.2.0.68");var subQ1=sQuery(id+"F0.wireOp",EDGE,"E3.2.0.11");var subQ2=makeQuery(id+"F0.imprint","INTERSECT",VERTEX,{"derivedFrom":[subQ1,subQ0]});Q776=makeQuery(id+"F0.imprint","IMPRINT",FACE,{"disambiguationData":[TD([[makeQuery(id+"F0.imprint","IMPRINT",EDGE,{"disambiguationData":[TD([[subQ2,1.0]])],"derivedFrom":subQ1}),-1.0]])]});}
            var Q777;
            {var subQ3=sQuery(id+"F0.wireOp",EDGE,"E3.1.0.103");Q777=makeQuery(id+"F0.imprint","IMPRINT",FACE,{"disambiguationData":[TD([[makeQuery(id+"F0.imprint","IMPRINT",EDGE,{"derivedFrom":subQ3}),1.0]])]});}
            var Q778;
            {var subQ0=sQuery(id+"F0.wireOp",EDGE,"E3.3.0.19");Q778=makeQuery(id+"F0.imprint","IMPRINT",FACE,{"disambiguationData":[TD([[makeQuery(id+"F0.imprint","IMPRINT",EDGE,{"derivedFrom":subQ0}),-1.0]])]});}
            var Q779;
            {var subQ0=sQuery(id+"F0.wireOp",EDGE,"E3.3.0.41");var subQ1=sQuery(id+"F0.wireOp",EDGE,"E3.3.0.13");var subQ2=makeQuery(id+"F0.imprint","INTERSECT",VERTEX,{"derivedFrom":[subQ1,subQ0]});Q779=makeQuery(id+"F0.imprint","IMPRINT",FACE,{"disambiguationData":[TD([[makeQuery(id+"F0.imprint","IMPRINT",EDGE,{"disambiguationData":[TD([[subQ2,-1.0]])],"derivedFrom":subQ1}),-1.0]])]});}
            var Q780;
            {var subQ0=sQuery(id+"F0.wireOp",EDGE,"E3.4.0.51");var subQ1=sQuery(id+"F0.wireOp",EDGE,"E3.4.0.10");var subQ2=makeQuery(id+"F0.imprint","INTERSECT",VERTEX,{"derivedFrom":[subQ1,subQ0]});Q780=makeQuery(id+"F0.imprint","IMPRINT",FACE,{"disambiguationData":[TD([[makeQuery(id+"F0.imprint","IMPRINT",EDGE,{"disambiguationData":[TD([[subQ2,-1.0]])],"derivedFrom":subQ1}),1.0]])]});}
            var Q781;
            {var subQ5=sQuery(id+"F0.wireOp",EDGE,"E3.6.0.56");Q781=makeQuery(id+"F0.imprint","IMPRINT",FACE,{"disambiguationData":[TD([[makeQuery(id+"F0.imprint","IMPRINT",EDGE,{"derivedFrom":subQ5}),1.0]])]});}
            var Q782;
            {var subQ7=sQuery(id+"F0.wireOp",EDGE,"E3.5.0.54");Q782=makeQuery(id+"F0.imprint","IMPRINT",FACE,{"disambiguationData":[TD([[makeQuery(id+"F0.imprint","IMPRINT",EDGE,{"derivedFrom":subQ7}),-1.0]])]});}
            var Q783;
            {var subQ0=sQuery(id+"F0.wireOp",EDGE,"E3.5.0.71");var subQ1=sQuery(id+"F0.wireOp",EDGE,"E3.5.0.9");var subQ2=makeQuery(id+"F0.imprint","INTERSECT",VERTEX,{"derivedFrom":[subQ1,subQ0]});Q783=makeQuery(id+"F0.imprint","IMPRINT",FACE,{"disambiguationData":[TD([[makeQuery(id+"F0.imprint","IMPRINT",EDGE,{"disambiguationData":[TD([[subQ2,1.0]])],"derivedFrom":subQ1}),-1.0]])]});}
            var Q784;
            {var subQ0=sQuery(id+"F0.wireOp",EDGE,"E3.6.0.89");Q784=makeQuery(id+"F0.imprint","IMPRINT",FACE,{"disambiguationData":[TD([[makeQuery(id+"F0.imprint","IMPRINT",EDGE,{"derivedFrom":subQ0}),-1.0]])]});}
            var Q785;
            {var subQ5=sQuery(id+"F0.wireOp",EDGE,"E3.7.0.22");Q785=makeQuery(id+"F0.imprint","IMPRINT",FACE,{"disambiguationData":[TD([[makeQuery(id+"F0.imprint","IMPRINT",EDGE,{"derivedFrom":subQ5}),-1.0]])]});}
            var Q786;
            {var subQ3=sQuery(id+"F0.wireOp",EDGE,"E3.16.0.86");Q786=makeQuery(id+"F0.imprint","IMPRINT",FACE,{"disambiguationData":[TD([[makeQuery(id+"F0.imprint","IMPRINT",EDGE,{"derivedFrom":subQ3}),1.0]])]});}
            var Q787;
            {var subQ0=sQuery(id+"F0.wireOp",EDGE,"E3.15.0.64");Q787=makeQuery(id+"F0.imprint","IMPRINT",FACE,{"disambiguationData":[TD([[makeQuery(id+"F0.imprint","IMPRINT",EDGE,{"derivedFrom":subQ0}),-1.0]])]});}
            var Q788;
            {var subQ5=sQuery(id+"F0.wireOp",EDGE,"E3.15.0.56");Q788=makeQuery(id+"F0.imprint","IMPRINT",FACE,{"disambiguationData":[TD([[makeQuery(id+"F0.imprint","IMPRINT",EDGE,{"derivedFrom":subQ5}),1.0]])]});}
            var Q789;
            {var subQ0=sQuery(id+"F0.wireOp",EDGE,"E3.14.0.71");var subQ1=sQuery(id+"F0.wireOp",EDGE,"E3.14.0.9");var subQ2=makeQuery(id+"F0.imprint","INTERSECT",VERTEX,{"derivedFrom":[subQ1,subQ0]});Q789=makeQuery(id+"F0.imprint","IMPRINT",FACE,{"disambiguationData":[TD([[makeQuery(id+"F0.imprint","IMPRINT",EDGE,{"disambiguationData":[TD([[subQ2,1.0]])],"derivedFrom":subQ1}),-1.0]])]});}
            var Q790;
            {var subQ0=sQuery(id+"F0.wireOp",EDGE,"E3.15.0.100");var subQ1=sQuery(id+"F0.wireOp",EDGE,"E3.15.0.52");var subQ2=makeQuery(id+"F0.imprint","INTERSECT",VERTEX,{"derivedFrom":[subQ1,subQ0]});Q790=makeQuery(id+"F0.imprint","IMPRINT",FACE,{"disambiguationData":[TD([[makeQuery(id+"F0.imprint","IMPRINT",EDGE,{"disambiguationData":[TD([[subQ2,1.0]])],"derivedFrom":subQ1}),-1.0]])]});}
            var Q791;
            {var subQ0=sQuery(id+"F0.wireOp",EDGE,"E2.4.0.0");var subQ1=sQuery(id+"F0.wireOp",EDGE,"E2.3.0.1");var subQ2=makeQuery(id+"F0.imprint","INTERSECT",VERTEX,{"derivedFrom":[subQ1,subQ0]});Q791=makeQuery(id+"F0.imprint","IMPRINT",FACE,{"disambiguationData":[TD([[makeQuery(id+"F0.imprint","IMPRINT",EDGE,{"disambiguationData":[TD([[subQ2,1.0]])],"derivedFrom":subQ1}),1.0]])]});}
            var Q792;
            {var subQ0=sQuery(id+"F0.wireOp",EDGE,"E3.1.0.8");var subQ1=sQuery(id+"F0.wireOp",EDGE,"E3.1.0.6");var subQ2=makeQuery(id+"F0.imprint","INTERSECT",VERTEX,{"derivedFrom":[subQ1,subQ0]});Q792=makeQuery(id+"F0.imprint","IMPRINT",FACE,{"disambiguationData":[TD([[makeQuery(id+"F0.imprint","IMPRINT",EDGE,{"disambiguationData":[TD([[subQ2,-1.0]])],"derivedFrom":subQ1}),-1.0]])]});}
            var Q793;
            {var subQ3=sQuery(id+"F0.wireOp",EDGE,"E3.9.0.66");Q793=makeQuery(id+"F0.imprint","IMPRINT",FACE,{"disambiguationData":[TD([[makeQuery(id+"F0.imprint","IMPRINT",EDGE,{"derivedFrom":subQ3}),-1.0]])]});}
            var Q794;
            {var subQ3=sQuery(id+"F0.wireOp",EDGE,"E3.10.0.103");Q794=makeQuery(id+"F0.imprint","IMPRINT",FACE,{"disambiguationData":[TD([[makeQuery(id+"F0.imprint","IMPRINT",EDGE,{"derivedFrom":subQ3}),1.0]])]});}
            var Q795;
            {var subQ3=sQuery(id+"F0.wireOp",EDGE,"E3.10.0.82");Q795=makeQuery(id+"F0.imprint","IMPRINT",FACE,{"disambiguationData":[TD([[makeQuery(id+"F0.imprint","IMPRINT",EDGE,{"derivedFrom":subQ3}),1.0]])]});}
            var Q796;
            {var subQ0=sQuery(id+"F0.wireOp",EDGE,"E3.12.0.41");var subQ1=sQuery(id+"F0.wireOp",EDGE,"E3.12.0.13");var subQ2=makeQuery(id+"F0.imprint","INTERSECT",VERTEX,{"derivedFrom":[subQ1,subQ0]});Q796=makeQuery(id+"F0.imprint","IMPRINT",FACE,{"disambiguationData":[TD([[makeQuery(id+"F0.imprint","IMPRINT",EDGE,{"disambiguationData":[TD([[subQ2,-1.0]])],"derivedFrom":subQ1}),-1.0]])]});}
            var Q797;
            {var subQ0=sQuery(id+"F0.wireOp",EDGE,"E3.13.0.42");var subQ1=sQuery(id+"F0.wireOp",EDGE,"E3.13.0.16");var subQ2=makeQuery(id+"F0.imprint","INTERSECT",VERTEX,{"derivedFrom":[subQ1,subQ0]});Q797=makeQuery(id+"F0.imprint","IMPRINT",FACE,{"disambiguationData":[TD([[makeQuery(id+"F0.imprint","IMPRINT",EDGE,{"disambiguationData":[TD([[subQ2,-1.0]])],"derivedFrom":subQ1}),-1.0]])]});}
            var Q798;
            {var subQ0=sQuery(id+"F0.wireOp",EDGE,"E3.13.0.51");var subQ1=sQuery(id+"F0.wireOp",EDGE,"E3.13.0.10");var subQ2=makeQuery(id+"F0.imprint","INTERSECT",VERTEX,{"derivedFrom":[subQ1,subQ0]});Q798=makeQuery(id+"F0.imprint","IMPRINT",FACE,{"disambiguationData":[TD([[makeQuery(id+"F0.imprint","IMPRINT",EDGE,{"disambiguationData":[TD([[subQ2,-1.0]])],"derivedFrom":subQ1}),1.0]])]});}
            var Q799;
            {var subQ0=sQuery(id+"F0.wireOp",EDGE,"E3.2.0.97");var subQ1=sQuery(id+"F0.wireOp",EDGE,"E3.2.0.40");var subQ2=makeQuery(id+"F0.imprint","INTERSECT",VERTEX,{"derivedFrom":[subQ1,subQ0]});Q799=makeQuery(id+"F0.imprint","IMPRINT",FACE,{"disambiguationData":[TD([[makeQuery(id+"F0.imprint","IMPRINT",EDGE,{"disambiguationData":[TD([[subQ2,1.0]])],"derivedFrom":subQ1}),-1.0]])]});}
            var Q800;
            {var subQ0=sQuery(id+"F0.wireOp",EDGE,"E3.2.0.39");var subQ1=sQuery(id+"F0.wireOp",EDGE,"E3.2.0.17");var subQ2=makeQuery(id+"F0.imprint","INTERSECT",VERTEX,{"derivedFrom":[subQ1,subQ0]});Q800=makeQuery(id+"F0.imprint","IMPRINT",FACE,{"disambiguationData":[TD([[makeQuery(id+"F0.imprint","IMPRINT",EDGE,{"disambiguationData":[TD([[subQ2,-1.0]])],"derivedFrom":subQ1}),-1.0]])]});}
            var Q801;
            {var subQ0=sQuery(id+"F0.wireOp",EDGE,"E3.2.0.68");var subQ1=sQuery(id+"F0.wireOp",EDGE,"E3.2.0.8");var subQ2=makeQuery(id+"F0.imprint","INTERSECT",VERTEX,{"derivedFrom":[subQ1,subQ0]});Q801=makeQuery(id+"F0.imprint","IMPRINT",FACE,{"disambiguationData":[TD([[makeQuery(id+"F0.imprint","IMPRINT",EDGE,{"disambiguationData":[TD([[subQ2,1.0]])],"derivedFrom":subQ1}),-1.0]])]});}
            var Q802;
            {var subQ0=sQuery(id+"F0.wireOp",EDGE,"E3.1.0.75");var subQ1=sQuery(id+"F0.wireOp",EDGE,"E3.1.0.52");var subQ2=makeQuery(id+"F0.imprint","INTERSECT",VERTEX,{"derivedFrom":[subQ1,subQ0]});Q802=makeQuery(id+"F0.imprint","IMPRINT",FACE,{"disambiguationData":[TD([[makeQuery(id+"F0.imprint","IMPRINT",EDGE,{"disambiguationData":[TD([[subQ2,-1.0]])],"derivedFrom":subQ1}),-1.0]])]});}
            var Q803;
            {var subQ0=sQuery(id+"F0.wireOp",EDGE,"E3.5.0.37");var subQ5=sQuery(id+"F0.wireOp",EDGE,"E3.5.0.9");var subQ7=makeQuery(id+"F0.imprint","INTERSECT",VERTEX,{"derivedFrom":[subQ5,subQ0]});Q803=makeQuery(id+"F0.imprint","IMPRINT",FACE,{"disambiguationData":[TD([[makeQuery(id+"F0.imprint","IMPRINT",EDGE,{"disambiguationData":[TD([[subQ7,1.0]])],"derivedFrom":subQ5}),1.0]])]});}
            var Q804;
            {var subQ0=sQuery(id+"F0.wireOp",EDGE,"E3.4.0.96");var subQ1=sQuery(id+"F0.wireOp",EDGE,"E3.4.0.39");var subQ2=makeQuery(id+"F0.imprint","INTERSECT",VERTEX,{"derivedFrom":[subQ1,subQ0]});Q804=makeQuery(id+"F0.imprint","IMPRINT",FACE,{"disambiguationData":[TD([[makeQuery(id+"F0.imprint","IMPRINT",EDGE,{"disambiguationData":[TD([[subQ2,1.0]])],"derivedFrom":subQ1}),-1.0]])]});}
            var Q805;
            {var subQ0=sQuery(id+"F0.wireOp",EDGE,"E3.5.0.72");var subQ1=sQuery(id+"F0.wireOp",EDGE,"E3.5.0.10");var subQ2=makeQuery(id+"F0.imprint","INTERSECT",VERTEX,{"derivedFrom":[subQ1,subQ0]});Q805=makeQuery(id+"F0.imprint","IMPRINT",FACE,{"disambiguationData":[TD([[makeQuery(id+"F0.imprint","IMPRINT",EDGE,{"disambiguationData":[TD([[subQ2,1.0]])],"derivedFrom":subQ1}),-1.0]])]});}
            var Q806;
            {var subQ3=sQuery(id+"F0.wireOp",EDGE,"E3.7.0.53");Q806=makeQuery(id+"F0.imprint","IMPRINT",FACE,{"disambiguationData":[TD([[makeQuery(id+"F0.imprint","IMPRINT",EDGE,{"derivedFrom":subQ3}),1.0]])]});}
            var Q807;
            {var subQ0=sQuery(id+"F0.wireOp",EDGE,"E3.8.0.99");var subQ1=sQuery(id+"F0.wireOp",EDGE,"E3.8.0.49");var subQ2=makeQuery(id+"F0.imprint","INTERSECT",VERTEX,{"derivedFrom":[subQ1,subQ0]});Q807=makeQuery(id+"F0.imprint","IMPRINT",FACE,{"disambiguationData":[TD([[makeQuery(id+"F0.imprint","IMPRINT",EDGE,{"disambiguationData":[TD([[subQ2,1.0]])],"derivedFrom":subQ1}),-1.0]])]});}
            var Q808;
            {var subQ3=sQuery(id+"F0.wireOp",EDGE,"E3.8.0.83");Q808=makeQuery(id+"F0.imprint","IMPRINT",FACE,{"disambiguationData":[TD([[makeQuery(id+"F0.imprint","IMPRINT",EDGE,{"derivedFrom":subQ3}),1.0]])]});}
            var Q809;
            {var subQ3=sQuery(id+"F0.wireOp",EDGE,"E3.16.0.53");Q809=makeQuery(id+"F0.imprint","IMPRINT",FACE,{"disambiguationData":[TD([[makeQuery(id+"F0.imprint","IMPRINT",EDGE,{"derivedFrom":subQ3}),1.0]])]});}
            var Q810;
            {var subQ0=sQuery(id+"F0.wireOp",EDGE,"E3.15.0.57");Q810=makeQuery(id+"F0.imprint","IMPRINT",FACE,{"disambiguationData":[TD([[makeQuery(id+"F0.imprint","IMPRINT",EDGE,{"derivedFrom":subQ0}),-1.0]])]});}
            var Q811;
            {var subQ0=sQuery(id+"F0.wireOp",EDGE,"E3.14.0.72");var subQ1=sQuery(id+"F0.wireOp",EDGE,"E3.14.0.10");var subQ2=makeQuery(id+"F0.imprint","INTERSECT",VERTEX,{"derivedFrom":[subQ1,subQ0]});Q811=makeQuery(id+"F0.imprint","IMPRINT",FACE,{"disambiguationData":[TD([[makeQuery(id+"F0.imprint","IMPRINT",EDGE,{"disambiguationData":[TD([[subQ2,1.0]])],"derivedFrom":subQ1}),-1.0]])]});}
            var Q812;
            {var subQ7=sQuery(id+"F0.wireOp",EDGE,"E3.16.0.87");Q812=makeQuery(id+"F0.imprint","IMPRINT",FACE,{"disambiguationData":[TD([[makeQuery(id+"F0.imprint","IMPRINT",EDGE,{"derivedFrom":subQ7}),-1.0]])]});}
            var Q813;
            {var subQ3=sQuery(id+"F0.wireOp",EDGE,"E2.4.0.7");Q813=makeQuery(id+"F0.imprint","IMPRINT",FACE,{"disambiguationData":[TD([[makeQuery(id+"F0.imprint","IMPRINT",EDGE,{"derivedFrom":subQ3}),-1.0]])]});}
            var Q814;
            {var subQ3=sQuery(id+"F0.wireOp",EDGE,"E3.1.0.83");Q814=makeQuery(id+"F0.imprint","IMPRINT",FACE,{"disambiguationData":[TD([[makeQuery(id+"F0.imprint","IMPRINT",EDGE,{"derivedFrom":subQ3}),1.0]])]});}
            var Q815;
            {var subQ3=sQuery(id+"F0.wireOp",EDGE,"E3.1.0.56");Q815=makeQuery(id+"F0.imprint","IMPRINT",FACE,{"disambiguationData":[TD([[makeQuery(id+"F0.imprint","IMPRINT",EDGE,{"derivedFrom":subQ3}),-1.0]])]});}
            var Q816;
            {var subQ0=sQuery(id+"F0.wireOp",EDGE,"E3.2.0.94");var subQ1=sQuery(id+"F0.wireOp",EDGE,"E3.2.0.42");var subQ2=makeQuery(id+"F0.imprint","INTERSECT",VERTEX,{"derivedFrom":[subQ1,subQ0]});Q816=makeQuery(id+"F0.imprint","IMPRINT",FACE,{"disambiguationData":[TD([[makeQuery(id+"F0.imprint","IMPRINT",EDGE,{"disambiguationData":[TD([[subQ2,1.0]])],"derivedFrom":subQ1}),-1.0]])]});}
            var Q817;
            {var subQ0=sQuery(id+"F0.wireOp",EDGE,"E3.2.0.69");var subQ1=sQuery(id+"F0.wireOp",EDGE,"E3.2.0.12");var subQ2=makeQuery(id+"F0.imprint","INTERSECT",VERTEX,{"derivedFrom":[subQ1,subQ0]});Q817=makeQuery(id+"F0.imprint","IMPRINT",FACE,{"disambiguationData":[TD([[makeQuery(id+"F0.imprint","IMPRINT",EDGE,{"disambiguationData":[TD([[subQ2,1.0]])],"derivedFrom":subQ1}),-1.0]])]});}
            var Q818;
            {var subQ0=sQuery(id+"F0.wireOp",EDGE,"E3.1.0.99");var subQ1=sQuery(id+"F0.wireOp",EDGE,"E3.1.0.49");var subQ2=makeQuery(id+"F0.imprint","INTERSECT",VERTEX,{"derivedFrom":[subQ1,subQ0]});Q818=makeQuery(id+"F0.imprint","IMPRINT",FACE,{"disambiguationData":[TD([[makeQuery(id+"F0.imprint","IMPRINT",EDGE,{"disambiguationData":[TD([[subQ2,1.0]])],"derivedFrom":subQ1}),-1.0]])]});}
            var Q819;
            {var subQ5=sQuery(id+"F0.wireOp",EDGE,"E3.12.0.82");Q819=makeQuery(id+"F0.imprint","IMPRINT",FACE,{"disambiguationData":[TD([[makeQuery(id+"F0.imprint","IMPRINT",EDGE,{"derivedFrom":subQ5}),-1.0]])]});}
            var Q820;
            {var subQ0=sQuery(id+"F0.wireOp",EDGE,"E3.12.0.91");var subQ1=sQuery(id+"F0.wireOp",EDGE,"E3.12.0.49");var subQ2=makeQuery(id+"F0.imprint","INTERSECT",VERTEX,{"derivedFrom":[subQ1,subQ0]});Q820=makeQuery(id+"F0.imprint","IMPRINT",FACE,{"disambiguationData":[TD([[makeQuery(id+"F0.imprint","IMPRINT",EDGE,{"disambiguationData":[TD([[subQ2,-1.0]])],"derivedFrom":subQ1}),-1.0]])]});}
            var Q821;
            {var subQ3=sQuery(id+"F0.wireOp",EDGE,"E3.3.0.103");Q821=makeQuery(id+"F0.imprint","IMPRINT",FACE,{"disambiguationData":[TD([[makeQuery(id+"F0.imprint","IMPRINT",EDGE,{"derivedFrom":subQ3}),1.0]])]});}
            var Q822;
            {var subQ3=sQuery(id+"F0.wireOp",EDGE,"E3.3.0.82");Q822=makeQuery(id+"F0.imprint","IMPRINT",FACE,{"disambiguationData":[TD([[makeQuery(id+"F0.imprint","IMPRINT",EDGE,{"derivedFrom":subQ3}),1.0]])]});}
            var Q823;
            {var subQ3=sQuery(id+"F0.wireOp",EDGE,"E3.3.0.55");Q823=makeQuery(id+"F0.imprint","IMPRINT",FACE,{"disambiguationData":[TD([[makeQuery(id+"F0.imprint","IMPRINT",EDGE,{"derivedFrom":subQ3}),1.0]])]});}
            var Q824;
            {var subQ0=sQuery(id+"F0.wireOp",EDGE,"E3.4.0.97");var subQ1=sQuery(id+"F0.wireOp",EDGE,"E3.4.0.44");var subQ2=makeQuery(id+"F0.imprint","INTERSECT",VERTEX,{"derivedFrom":[subQ1,subQ0]});Q824=makeQuery(id+"F0.imprint","IMPRINT",FACE,{"disambiguationData":[TD([[makeQuery(id+"F0.imprint","IMPRINT",EDGE,{"disambiguationData":[TD([[subQ2,1.0]])],"derivedFrom":subQ1}),-1.0]])]});}
            var Q825;
            {var subQ3=sQuery(id+"F0.wireOp",EDGE,"E3.4.0.85");Q825=makeQuery(id+"F0.imprint","IMPRINT",FACE,{"disambiguationData":[TD([[makeQuery(id+"F0.imprint","IMPRINT",EDGE,{"derivedFrom":subQ3}),1.0]])]});}
            var Q826;
            {var subQ0=sQuery(id+"F0.wireOp",EDGE,"E3.4.0.68");var subQ1=sQuery(id+"F0.wireOp",EDGE,"E3.4.0.11");var subQ2=makeQuery(id+"F0.imprint","INTERSECT",VERTEX,{"derivedFrom":[subQ1,subQ0]});Q826=makeQuery(id+"F0.imprint","IMPRINT",FACE,{"disambiguationData":[TD([[makeQuery(id+"F0.imprint","IMPRINT",EDGE,{"disambiguationData":[TD([[subQ2,1.0]])],"derivedFrom":subQ1}),-1.0]])]});}
            var Q827;
            {var subQ3=sQuery(id+"F0.wireOp",EDGE,"E3.5.0.118");Q827=makeQuery(id+"F0.imprint","IMPRINT",FACE,{"disambiguationData":[TD([[makeQuery(id+"F0.imprint","IMPRINT",EDGE,{"derivedFrom":subQ3}),1.0]])]});}
            var Q828;
            {var subQ0=sQuery(id+"F0.wireOp",EDGE,"E3.6.0.96");var subQ1=sQuery(id+"F0.wireOp",EDGE,"E3.6.0.43");var subQ2=makeQuery(id+"F0.imprint","INTERSECT",VERTEX,{"derivedFrom":[subQ1,subQ0]});Q828=makeQuery(id+"F0.imprint","IMPRINT",FACE,{"disambiguationData":[TD([[makeQuery(id+"F0.imprint","IMPRINT",EDGE,{"disambiguationData":[TD([[subQ2,1.0]])],"derivedFrom":subQ1}),-1.0]])]});}
            var Q829;
            {var subQ0=sQuery(id+"F0.wireOp",EDGE,"E3.6.0.42");var subQ1=sQuery(id+"F0.wireOp",EDGE,"E3.6.0.16");var subQ2=makeQuery(id+"F0.imprint","INTERSECT",VERTEX,{"derivedFrom":[subQ1,subQ0]});Q829=makeQuery(id+"F0.imprint","IMPRINT",FACE,{"disambiguationData":[TD([[makeQuery(id+"F0.imprint","IMPRINT",EDGE,{"disambiguationData":[TD([[subQ2,-1.0]])],"derivedFrom":subQ1}),-1.0]])]});}
            var Q830;
            {var subQ7=sQuery(id+"F0.wireOp",EDGE,"E3.7.0.54");Q830=makeQuery(id+"F0.imprint","IMPRINT",FACE,{"disambiguationData":[TD([[makeQuery(id+"F0.imprint","IMPRINT",EDGE,{"derivedFrom":subQ7}),-1.0]])]});}
            var Q831;
            {var subQ0=sQuery(id+"F0.wireOp",EDGE,"E3.7.0.71");var subQ1=sQuery(id+"F0.wireOp",EDGE,"E3.7.0.9");var subQ2=makeQuery(id+"F0.imprint","INTERSECT",VERTEX,{"derivedFrom":[subQ1,subQ0]});Q831=makeQuery(id+"F0.imprint","IMPRINT",FACE,{"disambiguationData":[TD([[makeQuery(id+"F0.imprint","IMPRINT",EDGE,{"disambiguationData":[TD([[subQ2,1.0]])],"derivedFrom":subQ1}),-1.0]])]});}
            var Q832;
            {var subQ0=sQuery(id+"F0.wireOp",EDGE,"E3.7.0.63");Q832=makeQuery(id+"F0.imprint","IMPRINT",FACE,{"disambiguationData":[TD([[makeQuery(id+"F0.imprint","IMPRINT",EDGE,{"derivedFrom":subQ0}),-1.0]])]});}
            var Q833;
            {var subQ5=sQuery(id+"F0.wireOp",EDGE,"E3.8.0.56");Q833=makeQuery(id+"F0.imprint","IMPRINT",FACE,{"disambiguationData":[TD([[makeQuery(id+"F0.imprint","IMPRINT",EDGE,{"derivedFrom":subQ5}),1.0]])]});}
            var Q834;
            {var subQ5=sQuery(id+"F0.wireOp",EDGE,"E3.9.0.53");Q834=makeQuery(id+"F0.imprint","IMPRINT",FACE,{"disambiguationData":[TD([[makeQuery(id+"F0.imprint","IMPRINT",EDGE,{"derivedFrom":subQ5}),-1.0]])]});}
            var Q835;
            {var subQ0=sQuery(id+"F0.wireOp",EDGE,"E3.15.0.42");var subQ1=sQuery(id+"F0.wireOp",EDGE,"E3.15.0.16");var subQ2=makeQuery(id+"F0.imprint","INTERSECT",VERTEX,{"derivedFrom":[subQ1,subQ0]});Q835=makeQuery(id+"F0.imprint","IMPRINT",FACE,{"disambiguationData":[TD([[makeQuery(id+"F0.imprint","IMPRINT",EDGE,{"disambiguationData":[TD([[subQ2,-1.0]])],"derivedFrom":subQ1}),-1.0]])]});}
            var Q836;
            {var subQ0=sQuery(id+"F0.wireOp",EDGE,"E3.15.0.51");var subQ1=sQuery(id+"F0.wireOp",EDGE,"E3.15.0.10");var subQ2=makeQuery(id+"F0.imprint","INTERSECT",VERTEX,{"derivedFrom":[subQ1,subQ0]});Q836=makeQuery(id+"F0.imprint","IMPRINT",FACE,{"disambiguationData":[TD([[makeQuery(id+"F0.imprint","IMPRINT",EDGE,{"disambiguationData":[TD([[subQ2,-1.0]])],"derivedFrom":subQ1}),1.0]])]});}
            var Q837;
            {var subQ3=sQuery(id+"F0.wireOp",EDGE,"E3.14.0.118");Q837=makeQuery(id+"F0.imprint","IMPRINT",FACE,{"disambiguationData":[TD([[makeQuery(id+"F0.imprint","IMPRINT",EDGE,{"derivedFrom":subQ3}),1.0]])]});}
            var Q838;
            {var subQ0=sQuery(id+"F0.wireOp",EDGE,"E3.16.0.63");Q838=makeQuery(id+"F0.imprint","IMPRINT",FACE,{"disambiguationData":[TD([[makeQuery(id+"F0.imprint","IMPRINT",EDGE,{"derivedFrom":subQ0}),-1.0]])]});}
            var Q839;
            {var subQ0=sQuery(id+"F0.wireOp",EDGE,"E2.4.0.1");var subQ1=sQuery(id+"F0.wireOp",EDGE,"E2.4.0.0");var subQ2=makeQuery(id+"F0.imprint","INTERSECT",VERTEX,{"derivedFrom":[subQ1,subQ0]});Q839=makeQuery(id+"F0.imprint","IMPRINT",FACE,{"disambiguationData":[TD([[makeQuery(id+"F0.imprint","IMPRINT",EDGE,{"disambiguationData":[TD([[subQ2,1.0]])],"derivedFrom":subQ1}),1.0]])]});}
            var Q840;
            {var subQ0=sQuery(id+"F0.wireOp",EDGE,"E3.1.0.89");Q840=makeQuery(id+"F0.imprint","IMPRINT",FACE,{"disambiguationData":[TD([[makeQuery(id+"F0.imprint","IMPRINT",EDGE,{"derivedFrom":subQ0}),-1.0]])]});}
            var Q841;
            {var subQ5=sQuery(id+"F0.wireOp",EDGE,"E3.1.0.56");Q841=makeQuery(id+"F0.imprint","IMPRINT",FACE,{"disambiguationData":[TD([[makeQuery(id+"F0.imprint","IMPRINT",EDGE,{"derivedFrom":subQ5}),1.0]])]});}
            var Q842;
            {var subQ5=sQuery(id+"F0.wireOp",EDGE,"E3.2.0.53");Q842=makeQuery(id+"F0.imprint","IMPRINT",FACE,{"disambiguationData":[TD([[makeQuery(id+"F0.imprint","IMPRINT",EDGE,{"derivedFrom":subQ5}),-1.0]])]});}
            var Q843;
            {var subQ3=sQuery(id+"F0.wireOp",EDGE,"E3.2.0.86");Q843=makeQuery(id+"F0.imprint","IMPRINT",FACE,{"disambiguationData":[TD([[makeQuery(id+"F0.imprint","IMPRINT",EDGE,{"derivedFrom":subQ3}),1.0]])]});}
            var Q844;
            {var subQ5=sQuery(id+"F0.wireOp",EDGE,"E3.2.0.22");Q844=makeQuery(id+"F0.imprint","IMPRINT",FACE,{"disambiguationData":[TD([[makeQuery(id+"F0.imprint","IMPRINT",EDGE,{"derivedFrom":subQ5}),-1.0]])]});}
            var Q845;
            {var subQ0=sQuery(id+"F0.wireOp",EDGE,"E3.16.0.71");var subQ1=sQuery(id+"F0.wireOp",EDGE,"E3.16.0.9");var subQ2=makeQuery(id+"F0.imprint","INTERSECT",VERTEX,{"derivedFrom":[subQ1,subQ0]});Q845=makeQuery(id+"F0.imprint","IMPRINT",FACE,{"disambiguationData":[TD([[makeQuery(id+"F0.imprint","IMPRINT",EDGE,{"disambiguationData":[TD([[subQ2,1.0]])],"derivedFrom":subQ1}),-1.0]])]});}
            var Q846;
            {var subQ0=sQuery(id+"F0.wireOp",EDGE,"E3.13.0.97");var subQ1=sQuery(id+"F0.wireOp",EDGE,"E3.13.0.44");var subQ2=makeQuery(id+"F0.imprint","INTERSECT",VERTEX,{"derivedFrom":[subQ1,subQ0]});Q846=makeQuery(id+"F0.imprint","IMPRINT",FACE,{"disambiguationData":[TD([[makeQuery(id+"F0.imprint","IMPRINT",EDGE,{"disambiguationData":[TD([[subQ2,1.0]])],"derivedFrom":subQ1}),-1.0]])]});}
            var Q847;
            {var subQ3=sQuery(id+"F0.wireOp",EDGE,"E3.12.0.55");Q847=makeQuery(id+"F0.imprint","IMPRINT",FACE,{"disambiguationData":[TD([[makeQuery(id+"F0.imprint","IMPRINT",EDGE,{"derivedFrom":subQ3}),1.0]])]});}
            var Q848;
            {var subQ0=sQuery(id+"F0.wireOp",EDGE,"E3.11.0.94");var subQ1=sQuery(id+"F0.wireOp",EDGE,"E3.11.0.42");var subQ2=makeQuery(id+"F0.imprint","INTERSECT",VERTEX,{"derivedFrom":[subQ1,subQ0]});Q848=makeQuery(id+"F0.imprint","IMPRINT",FACE,{"disambiguationData":[TD([[makeQuery(id+"F0.imprint","IMPRINT",EDGE,{"disambiguationData":[TD([[subQ2,1.0]])],"derivedFrom":subQ1}),-1.0]])]});}
            var Q849;
            {var subQ5=sQuery(id+"F0.wireOp",EDGE,"E3.6.0.57");Q849=makeQuery(id+"F0.imprint","IMPRINT",FACE,{"disambiguationData":[TD([[makeQuery(id+"F0.imprint","IMPRINT",EDGE,{"derivedFrom":subQ5}),1.0]])]});}
            var Q850;
            {var subQ3=sQuery(id+"F0.wireOp",EDGE,"E3.6.0.65");Q850=makeQuery(id+"F0.imprint","IMPRINT",FACE,{"disambiguationData":[TD([[makeQuery(id+"F0.imprint","IMPRINT",EDGE,{"derivedFrom":subQ3}),-1.0]])]});}
            var Q851;
            {var subQ0=sQuery(id+"F0.wireOp",EDGE,"E3.7.0.72");var subQ1=sQuery(id+"F0.wireOp",EDGE,"E3.7.0.10");var subQ2=makeQuery(id+"F0.imprint","INTERSECT",VERTEX,{"derivedFrom":[subQ1,subQ0]});Q851=makeQuery(id+"F0.imprint","IMPRINT",FACE,{"disambiguationData":[TD([[makeQuery(id+"F0.imprint","IMPRINT",EDGE,{"disambiguationData":[TD([[subQ2,1.0]])],"derivedFrom":subQ1}),-1.0]])]});}
            var Q852;
            {var subQ0=sQuery(id+"F0.wireOp",EDGE,"E3.8.0.41");var subQ1=sQuery(id+"F0.wireOp",EDGE,"E3.8.0.6");var subQ2=makeQuery(id+"F0.imprint","INTERSECT",VERTEX,{"derivedFrom":[subQ1,subQ0]});Q852=makeQuery(id+"F0.imprint","IMPRINT",FACE,{"disambiguationData":[TD([[makeQuery(id+"F0.imprint","IMPRINT",EDGE,{"disambiguationData":[TD([[subQ2,1.0]])],"derivedFrom":subQ1}),-1.0]])]});}
            var Q853;
            {var subQ3=sQuery(id+"F0.wireOp",EDGE,"E3.8.0.84");Q853=makeQuery(id+"F0.imprint","IMPRINT",FACE,{"disambiguationData":[TD([[makeQuery(id+"F0.imprint","IMPRINT",EDGE,{"derivedFrom":subQ3}),1.0]])]});}
            var Q854;
            {var subQ0=sQuery(id+"F0.wireOp",EDGE,"E3.9.0.40");var subQ1=sQuery(id+"F0.wireOp",EDGE,"E3.9.0.18");var subQ2=makeQuery(id+"F0.imprint","INTERSECT",VERTEX,{"derivedFrom":[subQ1,subQ0]});Q854=makeQuery(id+"F0.imprint","IMPRINT",FACE,{"disambiguationData":[TD([[makeQuery(id+"F0.imprint","IMPRINT",EDGE,{"disambiguationData":[TD([[subQ2,-1.0]])],"derivedFrom":subQ1}),-1.0]])]});}
            var Q855;
            {var subQ0=sQuery(id+"F0.wireOp",EDGE,"E3.11.0.69");var subQ1=sQuery(id+"F0.wireOp",EDGE,"E3.11.0.12");var subQ2=makeQuery(id+"F0.imprint","INTERSECT",VERTEX,{"derivedFrom":[subQ1,subQ0]});Q855=makeQuery(id+"F0.imprint","IMPRINT",FACE,{"disambiguationData":[TD([[makeQuery(id+"F0.imprint","IMPRINT",EDGE,{"disambiguationData":[TD([[subQ2,1.0]])],"derivedFrom":subQ1}),-1.0]])]});}
            var Q856;
            {var subQ0=sQuery(id+"F0.wireOp",EDGE,"E3.10.0.99");var subQ1=sQuery(id+"F0.wireOp",EDGE,"E3.10.0.49");var subQ2=makeQuery(id+"F0.imprint","INTERSECT",VERTEX,{"derivedFrom":[subQ1,subQ0]});Q856=makeQuery(id+"F0.imprint","IMPRINT",FACE,{"disambiguationData":[TD([[makeQuery(id+"F0.imprint","IMPRINT",EDGE,{"disambiguationData":[TD([[subQ2,1.0]])],"derivedFrom":subQ1}),-1.0]])]});}
            var Q857;
            {var subQ0=sQuery(id+"F0.wireOp",EDGE,"E3.15.0.96");var subQ1=sQuery(id+"F0.wireOp",EDGE,"E3.15.0.39");var subQ2=makeQuery(id+"F0.imprint","INTERSECT",VERTEX,{"derivedFrom":[subQ1,subQ0]});Q857=makeQuery(id+"F0.imprint","IMPRINT",FACE,{"disambiguationData":[TD([[makeQuery(id+"F0.imprint","IMPRINT",EDGE,{"disambiguationData":[TD([[subQ2,1.0]])],"derivedFrom":subQ1}),-1.0]])]});}
            var Q858;
            {var subQ5=sQuery(id+"F0.wireOp",EDGE,"E2.1.0.4");Q858=makeQuery(id+"F0.imprint","IMPRINT",FACE,{"disambiguationData":[TD([[makeQuery(id+"F0.imprint","IMPRINT",EDGE,{"derivedFrom":subQ5}),1.0]])]});}
            var Q859;
            {var subQ3=sQuery(id+"F0.wireOp",EDGE,"E3.1.0.84");Q859=makeQuery(id+"F0.imprint","IMPRINT",FACE,{"disambiguationData":[TD([[makeQuery(id+"F0.imprint","IMPRINT",EDGE,{"derivedFrom":subQ3}),1.0]])]});}
            var Q860;
            {var subQ5=sQuery(id+"F0.wireOp",EDGE,"E2.13.0.4");Q860=makeQuery(id+"F0.imprint","IMPRINT",FACE,{"disambiguationData":[TD([[makeQuery(id+"F0.imprint","IMPRINT",EDGE,{"derivedFrom":subQ5}),1.0]])]});}
            var Q861;
            {var subQ0=sQuery(id+"F0.wireOp",EDGE,"E3.3.0.99");var subQ1=sQuery(id+"F0.wireOp",EDGE,"E3.3.0.49");var subQ2=makeQuery(id+"F0.imprint","INTERSECT",VERTEX,{"derivedFrom":[subQ1,subQ0]});Q861=makeQuery(id+"F0.imprint","IMPRINT",FACE,{"disambiguationData":[TD([[makeQuery(id+"F0.imprint","IMPRINT",EDGE,{"disambiguationData":[TD([[subQ2,1.0]])],"derivedFrom":subQ1}),-1.0]])]});}
            var Q862;
            {var subQ3=sQuery(id+"F0.wireOp",EDGE,"E3.3.0.83");Q862=makeQuery(id+"F0.imprint","IMPRINT",FACE,{"disambiguationData":[TD([[makeQuery(id+"F0.imprint","IMPRINT",EDGE,{"derivedFrom":subQ3}),1.0]])]});}
            var Q863;
            {var subQ3=sQuery(id+"F0.wireOp",EDGE,"E3.16.0.54");Q863=makeQuery(id+"F0.imprint","IMPRINT",FACE,{"disambiguationData":[TD([[makeQuery(id+"F0.imprint","IMPRINT",EDGE,{"derivedFrom":subQ3}),1.0]])]});}
            var Q864;
            {var subQ3=sQuery(id+"F0.wireOp",EDGE,"E3.15.0.65");Q864=makeQuery(id+"F0.imprint","IMPRINT",FACE,{"disambiguationData":[TD([[makeQuery(id+"F0.imprint","IMPRINT",EDGE,{"derivedFrom":subQ3}),-1.0]])]});}
            var Q865;
            {var subQ0=sQuery(id+"F0.wireOp",EDGE,"E3.14.0.91");var subQ1=sQuery(id+"F0.wireOp",EDGE,"E3.14.0.49");var subQ2=makeQuery(id+"F0.imprint","INTERSECT",VERTEX,{"derivedFrom":[subQ1,subQ0]});Q865=makeQuery(id+"F0.imprint","IMPRINT",FACE,{"disambiguationData":[TD([[makeQuery(id+"F0.imprint","IMPRINT",EDGE,{"disambiguationData":[TD([[subQ2,-1.0]])],"derivedFrom":subQ1}),-1.0]])]});}
            var Q866;
            {var subQ0=sQuery(id+"F0.wireOp",EDGE,"E3.13.0.68");var subQ1=sQuery(id+"F0.wireOp",EDGE,"E3.13.0.8");var subQ2=makeQuery(id+"F0.imprint","INTERSECT",VERTEX,{"derivedFrom":[subQ1,subQ0]});Q866=makeQuery(id+"F0.imprint","IMPRINT",FACE,{"disambiguationData":[TD([[makeQuery(id+"F0.imprint","IMPRINT",EDGE,{"disambiguationData":[TD([[subQ2,1.0]])],"derivedFrom":subQ1}),-1.0]])]});}
            var Q867;
            {var subQ3=sQuery(id+"F0.wireOp",EDGE,"E3.5.0.82");Q867=makeQuery(id+"F0.imprint","IMPRINT",FACE,{"disambiguationData":[TD([[makeQuery(id+"F0.imprint","IMPRINT",EDGE,{"derivedFrom":subQ3}),1.0]])]});}
            var Q868;
            {var subQ0=sQuery(id+"F0.wireOp",EDGE,"E3.7.0.19");Q868=makeQuery(id+"F0.imprint","IMPRINT",FACE,{"disambiguationData":[TD([[makeQuery(id+"F0.imprint","IMPRINT",EDGE,{"derivedFrom":subQ0}),-1.0]])]});}
            var Q869;
            {var subQ0=sQuery(id+"F0.wireOp",EDGE,"E3.9.0.32");var subQ1=sQuery(id+"F0.wireOp",EDGE,"E3.9.0.0");var subQ2=makeQuery(id+"F0.imprint","INTERSECT",VERTEX,{"derivedFrom":[subQ1,subQ0]});Q869=makeQuery(id+"F0.imprint","IMPRINT",FACE,{"disambiguationData":[TD([[makeQuery(id+"F0.imprint","IMPRINT",EDGE,{"disambiguationData":[TD([[subQ2,1.0]])],"derivedFrom":subQ1}),-1.0]])]});}
            var Q870;
            {var subQ0=sQuery(id+"F0.wireOp",EDGE,"E3.8.0.96");var subQ1=sQuery(id+"F0.wireOp",EDGE,"E3.8.0.43");var subQ2=makeQuery(id+"F0.imprint","INTERSECT",VERTEX,{"derivedFrom":[subQ1,subQ0]});Q870=makeQuery(id+"F0.imprint","IMPRINT",FACE,{"disambiguationData":[TD([[makeQuery(id+"F0.imprint","IMPRINT",EDGE,{"disambiguationData":[TD([[subQ2,1.0]])],"derivedFrom":subQ1}),-1.0]])]});}
            var Q871;
            {var subQ5=sQuery(id+"F0.wireOp",EDGE,"E3.10.0.56");Q871=makeQuery(id+"F0.imprint","IMPRINT",FACE,{"disambiguationData":[TD([[makeQuery(id+"F0.imprint","IMPRINT",EDGE,{"derivedFrom":subQ5}),1.0]])]});}
            var Q872;
            {var subQ5=sQuery(id+"F0.wireOp",EDGE,"E3.11.0.22");Q872=makeQuery(id+"F0.imprint","IMPRINT",FACE,{"disambiguationData":[TD([[makeQuery(id+"F0.imprint","IMPRINT",EDGE,{"derivedFrom":subQ5}),-1.0]])]});}
            var Q873;
            {var subQ0=sQuery(id+"F0.wireOp",EDGE,"E3.10.0.100");var subQ1=sQuery(id+"F0.wireOp",EDGE,"E3.10.0.52");var subQ2=makeQuery(id+"F0.imprint","INTERSECT",VERTEX,{"derivedFrom":[subQ1,subQ0]});Q873=makeQuery(id+"F0.imprint","IMPRINT",FACE,{"disambiguationData":[TD([[makeQuery(id+"F0.imprint","IMPRINT",EDGE,{"disambiguationData":[TD([[subQ2,1.0]])],"derivedFrom":subQ1}),-1.0]])]});}
            var Q874;
            {var subQ0=sQuery(id+"F0.wireOp",EDGE,"E3.10.0.64");Q874=makeQuery(id+"F0.imprint","IMPRINT",FACE,{"disambiguationData":[TD([[makeQuery(id+"F0.imprint","IMPRINT",EDGE,{"derivedFrom":subQ0}),-1.0]])]});}
            var Q875;
            {var subQ7=sQuery(id+"F0.wireOp",EDGE,"E3.12.0.83");Q875=makeQuery(id+"F0.imprint","IMPRINT",FACE,{"disambiguationData":[TD([[makeQuery(id+"F0.imprint","IMPRINT",EDGE,{"derivedFrom":subQ7}),-1.0]])]});}
            var Q876;
            {var subQ5=sQuery(id+"F0.wireOp",EDGE,"E3.11.0.53");Q876=makeQuery(id+"F0.imprint","IMPRINT",FACE,{"disambiguationData":[TD([[makeQuery(id+"F0.imprint","IMPRINT",EDGE,{"derivedFrom":subQ5}),-1.0]])]});}
            var Q877;
            {var subQ0=sQuery(id+"F0.wireOp",EDGE,"E3.1.0.42");var subQ1=sQuery(id+"F0.wireOp",EDGE,"E3.1.0.16");var subQ2=makeQuery(id+"F0.imprint","INTERSECT",VERTEX,{"derivedFrom":[subQ1,subQ0]});Q877=makeQuery(id+"F0.imprint","IMPRINT",FACE,{"disambiguationData":[TD([[makeQuery(id+"F0.imprint","IMPRINT",EDGE,{"disambiguationData":[TD([[subQ2,-1.0]])],"derivedFrom":subQ1}),-1.0]])]});}
            var Q878;
            {var subQ7=sQuery(id+"F0.wireOp",EDGE,"E3.2.0.54");Q878=makeQuery(id+"F0.imprint","IMPRINT",FACE,{"disambiguationData":[TD([[makeQuery(id+"F0.imprint","IMPRINT",EDGE,{"derivedFrom":subQ7}),-1.0]])]});}
            var Q879;
            {var subQ0=sQuery(id+"F0.wireOp",EDGE,"E3.2.0.71");var subQ1=sQuery(id+"F0.wireOp",EDGE,"E3.2.0.9");var subQ2=makeQuery(id+"F0.imprint","INTERSECT",VERTEX,{"derivedFrom":[subQ1,subQ0]});Q879=makeQuery(id+"F0.imprint","IMPRINT",FACE,{"disambiguationData":[TD([[makeQuery(id+"F0.imprint","IMPRINT",EDGE,{"disambiguationData":[TD([[subQ2,1.0]])],"derivedFrom":subQ1}),-1.0]])]});}
            var Q880;
            {var subQ0=sQuery(id+"F0.wireOp",EDGE,"E3.3.0.100");var subQ1=sQuery(id+"F0.wireOp",EDGE,"E3.3.0.52");var subQ2=makeQuery(id+"F0.imprint","INTERSECT",VERTEX,{"derivedFrom":[subQ1,subQ0]});Q880=makeQuery(id+"F0.imprint","IMPRINT",FACE,{"disambiguationData":[TD([[makeQuery(id+"F0.imprint","IMPRINT",EDGE,{"disambiguationData":[TD([[subQ2,1.0]])],"derivedFrom":subQ1}),-1.0]])]});}
            var Q881;
            {var subQ5=sQuery(id+"F0.wireOp",EDGE,"E3.3.0.56");Q881=makeQuery(id+"F0.imprint","IMPRINT",FACE,{"disambiguationData":[TD([[makeQuery(id+"F0.imprint","IMPRINT",EDGE,{"derivedFrom":subQ5}),1.0]])]});}
            var Q882;
            {var subQ0=sQuery(id+"F0.wireOp",EDGE,"E3.5.0.8");var subQ1=sQuery(id+"F0.wireOp",EDGE,"E3.5.0.6");var subQ2=makeQuery(id+"F0.imprint","INTERSECT",VERTEX,{"derivedFrom":[subQ1,subQ0]});Q882=makeQuery(id+"F0.imprint","IMPRINT",FACE,{"disambiguationData":[TD([[makeQuery(id+"F0.imprint","IMPRINT",EDGE,{"disambiguationData":[TD([[subQ2,-1.0]])],"derivedFrom":subQ1}),-1.0]])]});}
            var Q883;
            {var subQ3=sQuery(id+"F0.wireOp",EDGE,"E3.4.0.86");Q883=makeQuery(id+"F0.imprint","IMPRINT",FACE,{"disambiguationData":[TD([[makeQuery(id+"F0.imprint","IMPRINT",EDGE,{"derivedFrom":subQ3}),1.0]])]});}
            var Q884;
            {var subQ3=sQuery(id+"F0.wireOp",EDGE,"E3.14.0.82");Q884=makeQuery(id+"F0.imprint","IMPRINT",FACE,{"disambiguationData":[TD([[makeQuery(id+"F0.imprint","IMPRINT",EDGE,{"derivedFrom":subQ3}),1.0]])]});}
            var Q885;
            {var subQ3=sQuery(id+"F0.wireOp",EDGE,"E3.14.0.55");Q885=makeQuery(id+"F0.imprint","IMPRINT",FACE,{"disambiguationData":[TD([[makeQuery(id+"F0.imprint","IMPRINT",EDGE,{"derivedFrom":subQ3}),1.0]])]});}
            var Q886;
            {var subQ3=sQuery(id+"F0.wireOp",EDGE,"E3.16.0.118");Q886=makeQuery(id+"F0.imprint","IMPRINT",FACE,{"disambiguationData":[TD([[makeQuery(id+"F0.imprint","IMPRINT",EDGE,{"derivedFrom":subQ3}),1.0]])]});}
            var Q887;
            {var subQ0=sQuery(id+"F0.wireOp",EDGE,"E3.16.0.41");var subQ1=sQuery(id+"F0.wireOp",EDGE,"E3.16.0.13");var subQ2=makeQuery(id+"F0.imprint","INTERSECT",VERTEX,{"derivedFrom":[subQ1,subQ0]});Q887=makeQuery(id+"F0.imprint","IMPRINT",FACE,{"disambiguationData":[TD([[makeQuery(id+"F0.imprint","IMPRINT",EDGE,{"disambiguationData":[TD([[subQ2,-1.0]])],"derivedFrom":subQ1}),-1.0]])]});}
            var Q888;
            {var subQ5=sQuery(id+"F0.wireOp",EDGE,"E3.7.0.82");Q888=makeQuery(id+"F0.imprint","IMPRINT",FACE,{"disambiguationData":[TD([[makeQuery(id+"F0.imprint","IMPRINT",EDGE,{"derivedFrom":subQ5}),-1.0]])]});}
            var Q889;
            {var subQ3=sQuery(id+"F0.wireOp",EDGE,"E3.7.0.31");Q889=makeQuery(id+"F0.imprint","IMPRINT",FACE,{"disambiguationData":[TD([[makeQuery(id+"F0.imprint","IMPRINT",EDGE,{"derivedFrom":subQ3}),-1.0]])]});}
            var Q890;
            {var subQ5=sQuery(id+"F0.wireOp",EDGE,"E3.8.0.57");Q890=makeQuery(id+"F0.imprint","IMPRINT",FACE,{"disambiguationData":[TD([[makeQuery(id+"F0.imprint","IMPRINT",EDGE,{"derivedFrom":subQ5}),1.0]])]});}
            var Q891;
            {var subQ3=sQuery(id+"F0.wireOp",EDGE,"E3.9.0.54");Q891=makeQuery(id+"F0.imprint","IMPRINT",FACE,{"disambiguationData":[TD([[makeQuery(id+"F0.imprint","IMPRINT",EDGE,{"derivedFrom":subQ3}),1.0]])]});}
            var Q892;
            {var subQ0=sQuery(id+"F0.wireOp",EDGE,"E3.9.0.72");var subQ1=sQuery(id+"F0.wireOp",EDGE,"E3.9.0.10");var subQ2=makeQuery(id+"F0.imprint","INTERSECT",VERTEX,{"derivedFrom":[subQ1,subQ0]});Q892=makeQuery(id+"F0.imprint","IMPRINT",FACE,{"disambiguationData":[TD([[makeQuery(id+"F0.imprint","IMPRINT",EDGE,{"disambiguationData":[TD([[subQ2,1.0]])],"derivedFrom":subQ1}),-1.0]])]});}
            var Q893;
            {var subQ3=sQuery(id+"F0.wireOp",EDGE,"E3.9.0.81");Q893=makeQuery(id+"F0.imprint","IMPRINT",FACE,{"disambiguationData":[TD([[makeQuery(id+"F0.imprint","IMPRINT",EDGE,{"derivedFrom":subQ3}),1.0]])]});}
            var Q894;
            {var subQ10=sQuery(id+"F0.wireOp",EDGE,"E3.11.0.93");Q894=makeQuery(id+"F0.imprint","IMPRINT",FACE,{"disambiguationData":[TD([[makeQuery(id+"F0.imprint","IMPRINT",EDGE,{"derivedFrom":subQ10}),-1.0]])]});}
            var Q895;
            {var subQ0=sQuery(id+"F0.wireOp",EDGE,"E3.10.0.41");var subQ1=sQuery(id+"F0.wireOp",EDGE,"E3.10.0.6");var subQ2=makeQuery(id+"F0.imprint","INTERSECT",VERTEX,{"derivedFrom":[subQ1,subQ0]});Q895=makeQuery(id+"F0.imprint","IMPRINT",FACE,{"disambiguationData":[TD([[makeQuery(id+"F0.imprint","IMPRINT",EDGE,{"disambiguationData":[TD([[subQ2,1.0]])],"derivedFrom":subQ1}),-1.0]])]});}
            var Q896;
            {var subQ0=sQuery(id+"F0.wireOp",EDGE,"E3.11.0.40");var subQ1=sQuery(id+"F0.wireOp",EDGE,"E3.11.0.18");var subQ2=makeQuery(id+"F0.imprint","INTERSECT",VERTEX,{"derivedFrom":[subQ1,subQ0]});Q896=makeQuery(id+"F0.imprint","IMPRINT",FACE,{"disambiguationData":[TD([[makeQuery(id+"F0.imprint","IMPRINT",EDGE,{"disambiguationData":[TD([[subQ2,-1.0]])],"derivedFrom":subQ1}),-1.0]])]});}
            var Q897;
            {var subQ5=sQuery(id+"F0.wireOp",EDGE,"E3.1.0.57");Q897=makeQuery(id+"F0.imprint","IMPRINT",FACE,{"disambiguationData":[TD([[makeQuery(id+"F0.imprint","IMPRINT",EDGE,{"derivedFrom":subQ5}),1.0]])]});}
            var Q898;
            {var subQ0=sQuery(id+"F0.wireOp",EDGE,"E3.1.0.96");var subQ1=sQuery(id+"F0.wireOp",EDGE,"E3.1.0.39");var subQ2=makeQuery(id+"F0.imprint","INTERSECT",VERTEX,{"derivedFrom":[subQ1,subQ0]});Q898=makeQuery(id+"F0.imprint","IMPRINT",FACE,{"disambiguationData":[TD([[makeQuery(id+"F0.imprint","IMPRINT",EDGE,{"disambiguationData":[TD([[subQ2,1.0]])],"derivedFrom":subQ1}),-1.0]])]});}
            var Q899;
            {var subQ7=sQuery(id+"F0.wireOp",EDGE,"E3.4.0.87");Q899=makeQuery(id+"F0.imprint","IMPRINT",FACE,{"disambiguationData":[TD([[makeQuery(id+"F0.imprint","IMPRINT",EDGE,{"derivedFrom":subQ7}),-1.0]])]});}
            var Q900;
            {var subQ0=sQuery(id+"F0.wireOp",EDGE,"E3.3.0.41");var subQ1=sQuery(id+"F0.wireOp",EDGE,"E3.3.0.6");var subQ2=makeQuery(id+"F0.imprint","INTERSECT",VERTEX,{"derivedFrom":[subQ1,subQ0]});Q900=makeQuery(id+"F0.imprint","IMPRINT",FACE,{"disambiguationData":[TD([[makeQuery(id+"F0.imprint","IMPRINT",EDGE,{"disambiguationData":[TD([[subQ2,1.0]])],"derivedFrom":subQ1}),-1.0]])]});}
            var Q901;
            {var subQ3=sQuery(id+"F0.wireOp",EDGE,"E3.5.0.83");Q901=makeQuery(id+"F0.imprint","IMPRINT",FACE,{"disambiguationData":[TD([[makeQuery(id+"F0.imprint","IMPRINT",EDGE,{"derivedFrom":subQ3}),1.0]])]});}
            var Q902;
            {var subQ3=sQuery(id+"F0.wireOp",EDGE,"E3.5.0.56");Q902=makeQuery(id+"F0.imprint","IMPRINT",FACE,{"disambiguationData":[TD([[makeQuery(id+"F0.imprint","IMPRINT",EDGE,{"derivedFrom":subQ3}),-1.0]])]});}
            var Q903;
            {var subQ3=sQuery(id+"F0.wireOp",EDGE,"E3.4.0.53");Q903=makeQuery(id+"F0.imprint","IMPRINT",FACE,{"disambiguationData":[TD([[makeQuery(id+"F0.imprint","IMPRINT",EDGE,{"derivedFrom":subQ3}),1.0]])]});}
            var Q904;
            {var subQ0=sQuery(id+"F0.wireOp",EDGE,"E3.5.0.99");var subQ1=sQuery(id+"F0.wireOp",EDGE,"E3.5.0.49");var subQ2=makeQuery(id+"F0.imprint","INTERSECT",VERTEX,{"derivedFrom":[subQ1,subQ0]});Q904=makeQuery(id+"F0.imprint","IMPRINT",FACE,{"disambiguationData":[TD([[makeQuery(id+"F0.imprint","IMPRINT",EDGE,{"disambiguationData":[TD([[subQ2,1.0]])],"derivedFrom":subQ1}),-1.0]])]});}
            var Q905;
            {var subQ3=sQuery(id+"F0.wireOp",EDGE,"E3.6.0.66");Q905=makeQuery(id+"F0.imprint","IMPRINT",FACE,{"disambiguationData":[TD([[makeQuery(id+"F0.imprint","IMPRINT",EDGE,{"derivedFrom":subQ3}),-1.0]])]});}
            var Q906;
            {var subQ0=sQuery(id+"F0.wireOp",EDGE,"E3.16.0.91");var subQ1=sQuery(id+"F0.wireOp",EDGE,"E3.16.0.49");var subQ2=makeQuery(id+"F0.imprint","INTERSECT",VERTEX,{"derivedFrom":[subQ1,subQ0]});Q906=makeQuery(id+"F0.imprint","IMPRINT",FACE,{"disambiguationData":[TD([[makeQuery(id+"F0.imprint","IMPRINT",EDGE,{"disambiguationData":[TD([[subQ2,-1.0]])],"derivedFrom":subQ1}),-1.0]])]});}
            var Q907;
            {var subQ0=sQuery(id+"F0.wireOp",EDGE,"E3.14.0.75");var subQ1=sQuery(id+"F0.wireOp",EDGE,"E3.14.0.52");var subQ2=makeQuery(id+"F0.imprint","INTERSECT",VERTEX,{"derivedFrom":[subQ1,subQ0]});Q907=makeQuery(id+"F0.imprint","IMPRINT",FACE,{"disambiguationData":[TD([[makeQuery(id+"F0.imprint","IMPRINT",EDGE,{"disambiguationData":[TD([[subQ2,-1.0]])],"derivedFrom":subQ1}),-1.0]])]});}
            var Q908;
            {var subQ0=sQuery(id+"F0.wireOp",EDGE,"E3.14.0.35");var subQ1=sQuery(id+"F0.wireOp",EDGE,"E3.14.0.32");var subQ2=makeQuery(id+"F0.imprint","INTERSECT",VERTEX,{"derivedFrom":[subQ1,subQ0]});Q908=makeQuery(id+"F0.imprint","IMPRINT",FACE,{"disambiguationData":[TD([[makeQuery(id+"F0.imprint","IMPRINT",EDGE,{"disambiguationData":[TD([[subQ2,1.0]])],"derivedFrom":subQ1}),1.0]])]});}
            var Q909;
            {var subQ7=sQuery(id+"F0.wireOp",EDGE,"E3.14.0.83");Q909=makeQuery(id+"F0.imprint","IMPRINT",FACE,{"disambiguationData":[TD([[makeQuery(id+"F0.imprint","IMPRINT",EDGE,{"derivedFrom":subQ7}),-1.0]])]});}
            var Q910;
            {var subQ0=sQuery(id+"F0.wireOp",EDGE,"E3.15.0.97");var subQ1=sQuery(id+"F0.wireOp",EDGE,"E3.15.0.40");var subQ2=makeQuery(id+"F0.imprint","INTERSECT",VERTEX,{"derivedFrom":[subQ1,subQ0]});Q910=makeQuery(id+"F0.imprint","IMPRINT",FACE,{"disambiguationData":[TD([[makeQuery(id+"F0.imprint","IMPRINT",EDGE,{"disambiguationData":[TD([[subQ2,1.0]])],"derivedFrom":subQ1}),-1.0]])]});}
            var Q911;
            {var subQ3=sQuery(id+"F0.wireOp",EDGE,"E3.8.0.85");Q911=makeQuery(id+"F0.imprint","IMPRINT",FACE,{"disambiguationData":[TD([[makeQuery(id+"F0.imprint","IMPRINT",EDGE,{"derivedFrom":subQ3}),1.0]])]});}
            var Q912;
            {var subQ0=sQuery(id+"F0.wireOp",EDGE,"E3.8.0.68");var subQ1=sQuery(id+"F0.wireOp",EDGE,"E3.8.0.11");var subQ2=makeQuery(id+"F0.imprint","INTERSECT",VERTEX,{"derivedFrom":[subQ1,subQ0]});Q912=makeQuery(id+"F0.imprint","IMPRINT",FACE,{"disambiguationData":[TD([[makeQuery(id+"F0.imprint","IMPRINT",EDGE,{"disambiguationData":[TD([[subQ2,1.0]])],"derivedFrom":subQ1}),-1.0]])]});}
            var Q913;
            {var subQ5=sQuery(id+"F0.wireOp",EDGE,"E3.7.0.93");Q913=makeQuery(id+"F0.imprint","IMPRINT",FACE,{"disambiguationData":[TD([[makeQuery(id+"F0.imprint","IMPRINT",EDGE,{"derivedFrom":subQ5}),1.0]])]});}
            var Q914;
            {var subQ0=sQuery(id+"F0.wireOp",EDGE,"E3.8.0.97");var subQ1=sQuery(id+"F0.wireOp",EDGE,"E3.8.0.44");var subQ2=makeQuery(id+"F0.imprint","INTERSECT",VERTEX,{"derivedFrom":[subQ1,subQ0]});Q914=makeQuery(id+"F0.imprint","IMPRINT",FACE,{"disambiguationData":[TD([[makeQuery(id+"F0.imprint","IMPRINT",EDGE,{"disambiguationData":[TD([[subQ2,1.0]])],"derivedFrom":subQ1}),-1.0]])]});}
            var Q915;
            {var subQ0=sQuery(id+"F0.wireOp",EDGE,"E3.10.0.42");var subQ1=sQuery(id+"F0.wireOp",EDGE,"E3.10.0.16");var subQ2=makeQuery(id+"F0.imprint","INTERSECT",VERTEX,{"derivedFrom":[subQ1,subQ0]});Q915=makeQuery(id+"F0.imprint","IMPRINT",FACE,{"disambiguationData":[TD([[makeQuery(id+"F0.imprint","IMPRINT",EDGE,{"disambiguationData":[TD([[subQ2,-1.0]])],"derivedFrom":subQ1}),-1.0]])]});}
            var Q916;
            {var subQ3=sQuery(id+"F0.wireOp",EDGE,"E3.9.0.118");Q916=makeQuery(id+"F0.imprint","IMPRINT",FACE,{"disambiguationData":[TD([[makeQuery(id+"F0.imprint","IMPRINT",EDGE,{"derivedFrom":subQ3}),1.0]])]});}
            var Q917;
            {var subQ0=sQuery(id+"F0.wireOp",EDGE,"E3.11.0.71");var subQ1=sQuery(id+"F0.wireOp",EDGE,"E3.11.0.9");var subQ2=makeQuery(id+"F0.imprint","INTERSECT",VERTEX,{"derivedFrom":[subQ1,subQ0]});Q917=makeQuery(id+"F0.imprint","IMPRINT",FACE,{"disambiguationData":[TD([[makeQuery(id+"F0.imprint","IMPRINT",EDGE,{"disambiguationData":[TD([[subQ2,1.0]])],"derivedFrom":subQ1}),-1.0]])]});}
            var Q918;
            {var subQ0=sQuery(id+"F0.wireOp",EDGE,"E3.11.0.32");var subQ1=sQuery(id+"F0.wireOp",EDGE,"E3.11.0.0");var subQ2=makeQuery(id+"F0.imprint","INTERSECT",VERTEX,{"derivedFrom":[subQ1,subQ0]});Q918=makeQuery(id+"F0.imprint","IMPRINT",FACE,{"disambiguationData":[TD([[makeQuery(id+"F0.imprint","IMPRINT",EDGE,{"disambiguationData":[TD([[subQ2,1.0]])],"derivedFrom":subQ1}),-1.0]])]});}
            var Q919;
            {var subQ0=sQuery(id+"F0.wireOp",EDGE,"E3.12.0.100");var subQ1=sQuery(id+"F0.wireOp",EDGE,"E3.12.0.52");var subQ2=makeQuery(id+"F0.imprint","INTERSECT",VERTEX,{"derivedFrom":[subQ1,subQ0]});Q919=makeQuery(id+"F0.imprint","IMPRINT",FACE,{"disambiguationData":[TD([[makeQuery(id+"F0.imprint","IMPRINT",EDGE,{"disambiguationData":[TD([[subQ2,1.0]])],"derivedFrom":subQ1}),-1.0]])]});}
            var Q920;
            {var subQ5=sQuery(id+"F0.wireOp",EDGE,"E3.12.0.56");Q920=makeQuery(id+"F0.imprint","IMPRINT",FACE,{"disambiguationData":[TD([[makeQuery(id+"F0.imprint","IMPRINT",EDGE,{"derivedFrom":subQ5}),1.0]])]});}
            var Q921;
            {var subQ3=sQuery(id+"F0.wireOp",EDGE,"E3.13.0.86");Q921=makeQuery(id+"F0.imprint","IMPRINT",FACE,{"disambiguationData":[TD([[makeQuery(id+"F0.imprint","IMPRINT",EDGE,{"derivedFrom":subQ3}),1.0]])]});}
            var Q922;
            {var subQ5=sQuery(id+"F0.wireOp",EDGE,"E3.13.0.22");Q922=makeQuery(id+"F0.imprint","IMPRINT",FACE,{"disambiguationData":[TD([[makeQuery(id+"F0.imprint","IMPRINT",EDGE,{"derivedFrom":subQ5}),-1.0]])]});}
            var Q923;
            {var subQ0=sQuery(id+"F0.wireOp",EDGE,"E3.2.0.41");var subQ1=sQuery(id+"F0.wireOp",EDGE,"E3.2.0.13");var subQ2=makeQuery(id+"F0.imprint","INTERSECT",VERTEX,{"derivedFrom":[subQ1,subQ0]});Q923=makeQuery(id+"F0.imprint","IMPRINT",FACE,{"disambiguationData":[TD([[makeQuery(id+"F0.imprint","IMPRINT",EDGE,{"disambiguationData":[TD([[subQ2,-1.0]])],"derivedFrom":subQ1}),-1.0]])]});}
            var Q924;
            {var subQ3=sQuery(id+"F0.wireOp",EDGE,"E3.1.0.85");Q924=makeQuery(id+"F0.imprint","IMPRINT",FACE,{"disambiguationData":[TD([[makeQuery(id+"F0.imprint","IMPRINT",EDGE,{"derivedFrom":subQ3}),1.0]])]});}
            var Q925;
            {var subQ0=sQuery(id+"F0.wireOp",EDGE,"E3.2.0.19");Q925=makeQuery(id+"F0.imprint","IMPRINT",FACE,{"disambiguationData":[TD([[makeQuery(id+"F0.imprint","IMPRINT",EDGE,{"derivedFrom":subQ0}),-1.0]])]});}
            var Q926;
            {var subQ0=sQuery(id+"F0.wireOp",EDGE,"E3.4.0.71");var subQ1=sQuery(id+"F0.wireOp",EDGE,"E3.4.0.9");var subQ2=makeQuery(id+"F0.imprint","INTERSECT",VERTEX,{"derivedFrom":[subQ1,subQ0]});Q926=makeQuery(id+"F0.imprint","IMPRINT",FACE,{"disambiguationData":[TD([[makeQuery(id+"F0.imprint","IMPRINT",EDGE,{"disambiguationData":[TD([[subQ2,1.0]])],"derivedFrom":subQ1}),-1.0]])]});}
            var Q927;
            {var subQ0=sQuery(id+"F0.wireOp",EDGE,"E3.4.0.63");Q927=makeQuery(id+"F0.imprint","IMPRINT",FACE,{"disambiguationData":[TD([[makeQuery(id+"F0.imprint","IMPRINT",EDGE,{"derivedFrom":subQ0}),-1.0]])]});}
            var Q928;
            {var subQ0=sQuery(id+"F0.wireOp",EDGE,"E3.5.0.89");Q928=makeQuery(id+"F0.imprint","IMPRINT",FACE,{"disambiguationData":[TD([[makeQuery(id+"F0.imprint","IMPRINT",EDGE,{"derivedFrom":subQ0}),-1.0]])]});}
            var Q929;
            {var subQ7=sQuery(id+"F0.wireOp",EDGE,"E3.4.0.54");Q929=makeQuery(id+"F0.imprint","IMPRINT",FACE,{"disambiguationData":[TD([[makeQuery(id+"F0.imprint","IMPRINT",EDGE,{"derivedFrom":subQ7}),-1.0]])]});}
            var Q930;
            {var subQ5=sQuery(id+"F0.wireOp",EDGE,"E3.6.0.22");Q930=makeQuery(id+"F0.imprint","IMPRINT",FACE,{"disambiguationData":[TD([[makeQuery(id+"F0.imprint","IMPRINT",EDGE,{"derivedFrom":subQ5}),-1.0]])]});}
            var Q931;
            {var subQ0=sQuery(id+"F0.wireOp",EDGE,"E3.5.0.100");var subQ1=sQuery(id+"F0.wireOp",EDGE,"E3.5.0.52");var subQ2=makeQuery(id+"F0.imprint","INTERSECT",VERTEX,{"derivedFrom":[subQ1,subQ0]});Q931=makeQuery(id+"F0.imprint","IMPRINT",FACE,{"disambiguationData":[TD([[makeQuery(id+"F0.imprint","IMPRINT",EDGE,{"disambiguationData":[TD([[subQ2,1.0]])],"derivedFrom":subQ1}),-1.0]])]});}
            var Q932;
            {var subQ0=sQuery(id+"F0.wireOp",EDGE,"E3.7.0.8");var subQ1=sQuery(id+"F0.wireOp",EDGE,"E3.7.0.6");var subQ2=makeQuery(id+"F0.imprint","INTERSECT",VERTEX,{"derivedFrom":[subQ1,subQ0]});Q932=makeQuery(id+"F0.imprint","IMPRINT",FACE,{"disambiguationData":[TD([[makeQuery(id+"F0.imprint","IMPRINT",EDGE,{"disambiguationData":[TD([[subQ2,-1.0]])],"derivedFrom":subQ1}),-1.0]])]});}
            var Q933;
            {var subQ5=sQuery(id+"F0.wireOp",EDGE,"E3.6.0.53");Q933=makeQuery(id+"F0.imprint","IMPRINT",FACE,{"disambiguationData":[TD([[makeQuery(id+"F0.imprint","IMPRINT",EDGE,{"derivedFrom":subQ5}),-1.0]])]});}
            var Q934;
            {var subQ0=sQuery(id+"F0.wireOp",EDGE,"E3.8.0.39");var subQ1=sQuery(id+"F0.wireOp",EDGE,"E3.8.0.17");var subQ2=makeQuery(id+"F0.imprint","INTERSECT",VERTEX,{"derivedFrom":[subQ1,subQ0]});Q934=makeQuery(id+"F0.imprint","IMPRINT",FACE,{"disambiguationData":[TD([[makeQuery(id+"F0.imprint","IMPRINT",EDGE,{"disambiguationData":[TD([[subQ2,-1.0]])],"derivedFrom":subQ1}),-1.0]])]});}
            var Q935;
            {var subQ0=sQuery(id+"F0.wireOp",EDGE,"E3.7.0.35");var subQ1=sQuery(id+"F0.wireOp",EDGE,"E3.7.0.32");var subQ2=makeQuery(id+"F0.imprint","INTERSECT",VERTEX,{"derivedFrom":[subQ1,subQ0]});Q935=makeQuery(id+"F0.imprint","IMPRINT",FACE,{"disambiguationData":[TD([[makeQuery(id+"F0.imprint","IMPRINT",EDGE,{"disambiguationData":[TD([[subQ2,1.0]])],"derivedFrom":subQ1}),1.0]])]});}
            var Q936;
            {var subQ0=sQuery(id+"F0.wireOp",EDGE,"E3.14.0.99");var subQ1=sQuery(id+"F0.wireOp",EDGE,"E3.14.0.49");var subQ2=makeQuery(id+"F0.imprint","INTERSECT",VERTEX,{"derivedFrom":[subQ1,subQ0]});Q936=makeQuery(id+"F0.imprint","IMPRINT",FACE,{"disambiguationData":[TD([[makeQuery(id+"F0.imprint","IMPRINT",EDGE,{"disambiguationData":[TD([[subQ2,1.0]])],"derivedFrom":subQ1}),-1.0]])]});}
            var Q937;
            {var subQ0=sQuery(id+"F0.wireOp",EDGE,"E3.14.0.116");Q937=makeQuery(id+"F0.imprint","IMPRINT",FACE,{"disambiguationData":[TD([[makeQuery(id+"F0.imprint","IMPRINT",EDGE,{"derivedFrom":subQ0}),-1.0]])]});}
            var Q938;
            {var subQ3=sQuery(id+"F0.wireOp",EDGE,"E3.16.0.55");Q938=makeQuery(id+"F0.imprint","IMPRINT",FACE,{"disambiguationData":[TD([[makeQuery(id+"F0.imprint","IMPRINT",EDGE,{"derivedFrom":subQ3}),1.0]])]});}
            var Q939;
            {var subQ3=sQuery(id+"F0.wireOp",EDGE,"E3.16.0.82");Q939=makeQuery(id+"F0.imprint","IMPRINT",FACE,{"disambiguationData":[TD([[makeQuery(id+"F0.imprint","IMPRINT",EDGE,{"derivedFrom":subQ3}),1.0]])]});}
            var Q940;
            {var subQ0=sQuery(id+"F0.wireOp",EDGE,"E2.1.0.1");var subQ1=sQuery(id+"F0.wireOp",EDGE,"E2.1.0.0");var subQ2=makeQuery(id+"F0.imprint","INTERSECT",VERTEX,{"derivedFrom":[subQ1,subQ0]});Q940=makeQuery(id+"F0.imprint","IMPRINT",FACE,{"disambiguationData":[TD([[makeQuery(id+"F0.imprint","IMPRINT",EDGE,{"disambiguationData":[TD([[subQ2,1.0]])],"derivedFrom":subQ1}),1.0]])]});}
            var Q941;
            {var subQ0=sQuery(id+"F0.wireOp",EDGE,"E3.1.0.68");var subQ1=sQuery(id+"F0.wireOp",EDGE,"E3.1.0.11");var subQ2=makeQuery(id+"F0.imprint","INTERSECT",VERTEX,{"derivedFrom":[subQ1,subQ0]});Q941=makeQuery(id+"F0.imprint","IMPRINT",FACE,{"disambiguationData":[TD([[makeQuery(id+"F0.imprint","IMPRINT",EDGE,{"disambiguationData":[TD([[subQ2,1.0]])],"derivedFrom":subQ1}),-1.0]])]});}
            var Q942;
            {var subQ3=sQuery(id+"F0.wireOp",EDGE,"E3.9.0.31");Q942=makeQuery(id+"F0.imprint","IMPRINT",FACE,{"disambiguationData":[TD([[makeQuery(id+"F0.imprint","IMPRINT",EDGE,{"derivedFrom":subQ3}),-1.0]])]});}
            var Q943;
            {var subQ3=sQuery(id+"F0.wireOp",EDGE,"E3.10.0.65");Q943=makeQuery(id+"F0.imprint","IMPRINT",FACE,{"disambiguationData":[TD([[makeQuery(id+"F0.imprint","IMPRINT",EDGE,{"derivedFrom":subQ3}),-1.0]])]});}
            var Q944;
            {var subQ5=sQuery(id+"F0.wireOp",EDGE,"E3.10.0.57");Q944=makeQuery(id+"F0.imprint","IMPRINT",FACE,{"disambiguationData":[TD([[makeQuery(id+"F0.imprint","IMPRINT",EDGE,{"derivedFrom":subQ5}),1.0]])]});}
            var Q945;
            {var subQ3=sQuery(id+"F0.wireOp",EDGE,"E3.11.0.54");Q945=makeQuery(id+"F0.imprint","IMPRINT",FACE,{"disambiguationData":[TD([[makeQuery(id+"F0.imprint","IMPRINT",EDGE,{"derivedFrom":subQ3}),1.0]])]});}
            var Q946;
            {var subQ10=sQuery(id+"F0.wireOp",EDGE,"E3.13.0.93");Q946=makeQuery(id+"F0.imprint","IMPRINT",FACE,{"disambiguationData":[TD([[makeQuery(id+"F0.imprint","IMPRINT",EDGE,{"derivedFrom":subQ10}),-1.0]])]});}
            var Q947;
            {var subQ3=sQuery(id+"F0.wireOp",EDGE,"E3.12.0.84");Q947=makeQuery(id+"F0.imprint","IMPRINT",FACE,{"disambiguationData":[TD([[makeQuery(id+"F0.imprint","IMPRINT",EDGE,{"derivedFrom":subQ3}),1.0]])]});}
            var Q948;
            {var subQ5=sQuery(id+"F0.wireOp",EDGE,"E3.3.0.57");Q948=makeQuery(id+"F0.imprint","IMPRINT",FACE,{"disambiguationData":[TD([[makeQuery(id+"F0.imprint","IMPRINT",EDGE,{"derivedFrom":subQ5}),1.0]])]});}
            var Q949;
            {var subQ0=sQuery(id+"F0.wireOp",EDGE,"E3.2.0.91");var subQ1=sQuery(id+"F0.wireOp",EDGE,"E3.2.0.49");var subQ2=makeQuery(id+"F0.imprint","INTERSECT",VERTEX,{"derivedFrom":[subQ1,subQ0]});Q949=makeQuery(id+"F0.imprint","IMPRINT",FACE,{"disambiguationData":[TD([[makeQuery(id+"F0.imprint","IMPRINT",EDGE,{"disambiguationData":[TD([[subQ2,-1.0]])],"derivedFrom":subQ1}),-1.0]])]});}
            var Q950;
            {var subQ0=sQuery(id+"F0.wireOp",EDGE,"E3.4.0.72");var subQ1=sQuery(id+"F0.wireOp",EDGE,"E3.4.0.10");var subQ2=makeQuery(id+"F0.imprint","INTERSECT",VERTEX,{"derivedFrom":[subQ1,subQ0]});Q950=makeQuery(id+"F0.imprint","IMPRINT",FACE,{"disambiguationData":[TD([[makeQuery(id+"F0.imprint","IMPRINT",EDGE,{"disambiguationData":[TD([[subQ2,1.0]])],"derivedFrom":subQ1}),-1.0]])]});}
            var Q951;
            {var subQ3=sQuery(id+"F0.wireOp",EDGE,"E3.8.0.66");Q951=makeQuery(id+"F0.imprint","IMPRINT",FACE,{"disambiguationData":[TD([[makeQuery(id+"F0.imprint","IMPRINT",EDGE,{"derivedFrom":subQ3}),-1.0]])]});}
            var Q952;
            {var subQ0=sQuery(id+"F0.wireOp",EDGE,"E3.7.0.99");var subQ1=sQuery(id+"F0.wireOp",EDGE,"E3.7.0.49");var subQ2=makeQuery(id+"F0.imprint","INTERSECT",VERTEX,{"derivedFrom":[subQ1,subQ0]});Q952=makeQuery(id+"F0.imprint","IMPRINT",FACE,{"disambiguationData":[TD([[makeQuery(id+"F0.imprint","IMPRINT",EDGE,{"disambiguationData":[TD([[subQ2,1.0]])],"derivedFrom":subQ1}),-1.0]])]});}
            var Q953;
            {var subQ0=sQuery(id+"F0.wireOp",EDGE,"E3.8.0.94");var subQ1=sQuery(id+"F0.wireOp",EDGE,"E3.8.0.42");var subQ2=makeQuery(id+"F0.imprint","INTERSECT",VERTEX,{"derivedFrom":[subQ1,subQ0]});Q953=makeQuery(id+"F0.imprint","IMPRINT",FACE,{"disambiguationData":[TD([[makeQuery(id+"F0.imprint","IMPRINT",EDGE,{"disambiguationData":[TD([[subQ2,1.0]])],"derivedFrom":subQ1}),-1.0]])]});}
            var Q954;
            {var subQ0=sQuery(id+"F0.wireOp",EDGE,"E3.16.0.75");var subQ1=sQuery(id+"F0.wireOp",EDGE,"E3.16.0.52");var subQ2=makeQuery(id+"F0.imprint","INTERSECT",VERTEX,{"derivedFrom":[subQ1,subQ0]});Q954=makeQuery(id+"F0.imprint","IMPRINT",FACE,{"disambiguationData":[TD([[makeQuery(id+"F0.imprint","IMPRINT",EDGE,{"disambiguationData":[TD([[subQ2,-1.0]])],"derivedFrom":subQ1}),-1.0]])]});}
            var Q955;
            {var subQ0=sQuery(id+"F0.wireOp",EDGE,"E3.14.0.64");Q955=makeQuery(id+"F0.imprint","IMPRINT",FACE,{"disambiguationData":[TD([[makeQuery(id+"F0.imprint","IMPRINT",EDGE,{"derivedFrom":subQ0}),-1.0]])]});}
            var Q956;
            {var subQ5=sQuery(id+"F0.wireOp",EDGE,"E3.14.0.56");Q956=makeQuery(id+"F0.imprint","IMPRINT",FACE,{"disambiguationData":[TD([[makeQuery(id+"F0.imprint","IMPRINT",EDGE,{"derivedFrom":subQ5}),1.0]])]});}
            var Q957;
            {var subQ0=sQuery(id+"F0.wireOp",EDGE,"E3.16.0.8");var subQ1=sQuery(id+"F0.wireOp",EDGE,"E3.16.0.6");var subQ2=makeQuery(id+"F0.imprint","INTERSECT",VERTEX,{"derivedFrom":[subQ1,subQ0]});Q957=makeQuery(id+"F0.imprint","IMPRINT",FACE,{"disambiguationData":[TD([[makeQuery(id+"F0.imprint","IMPRINT",EDGE,{"disambiguationData":[TD([[subQ2,-1.0]])],"derivedFrom":subQ1}),-1.0]])]});}
            var Q958;
            {var subQ3=sQuery(id+"F0.wireOp",EDGE,"E3.15.0.86");Q958=makeQuery(id+"F0.imprint","IMPRINT",FACE,{"disambiguationData":[TD([[makeQuery(id+"F0.imprint","IMPRINT",EDGE,{"derivedFrom":subQ3}),1.0]])]});}
            var Q959;
            {var subQ7=sQuery(id+"F0.wireOp",EDGE,"E3.16.0.83");Q959=makeQuery(id+"F0.imprint","IMPRINT",FACE,{"disambiguationData":[TD([[makeQuery(id+"F0.imprint","IMPRINT",EDGE,{"derivedFrom":subQ7}),-1.0]])]});}
            var Q960;
            {var subQ0=sQuery(id+"F0.wireOp",EDGE,"E3.1.0.97");var subQ1=sQuery(id+"F0.wireOp",EDGE,"E3.1.0.40");var subQ2=makeQuery(id+"F0.imprint","INTERSECT",VERTEX,{"derivedFrom":[subQ1,subQ0]});Q960=makeQuery(id+"F0.imprint","IMPRINT",FACE,{"disambiguationData":[TD([[makeQuery(id+"F0.imprint","IMPRINT",EDGE,{"disambiguationData":[TD([[subQ2,1.0]])],"derivedFrom":subQ1}),-1.0]])]});}
            var Q961;
            {var subQ0=sQuery(id+"F0.wireOp",EDGE,"E3.10.0.68");var subQ1=sQuery(id+"F0.wireOp",EDGE,"E3.10.0.11");var subQ2=makeQuery(id+"F0.imprint","INTERSECT",VERTEX,{"derivedFrom":[subQ1,subQ0]});Q961=makeQuery(id+"F0.imprint","IMPRINT",FACE,{"disambiguationData":[TD([[makeQuery(id+"F0.imprint","IMPRINT",EDGE,{"disambiguationData":[TD([[subQ2,1.0]])],"derivedFrom":subQ1}),-1.0]])]});}
            var Q962;
            {var subQ3=sQuery(id+"F0.wireOp",EDGE,"E3.9.0.103");Q962=makeQuery(id+"F0.imprint","IMPRINT",FACE,{"disambiguationData":[TD([[makeQuery(id+"F0.imprint","IMPRINT",EDGE,{"derivedFrom":subQ3}),1.0]])]});}
            var Q963;
            {var subQ0=sQuery(id+"F0.wireOp",EDGE,"E3.13.0.32");var subQ1=sQuery(id+"F0.wireOp",EDGE,"E3.13.0.0");var subQ2=makeQuery(id+"F0.imprint","INTERSECT",VERTEX,{"derivedFrom":[subQ1,subQ0]});Q963=makeQuery(id+"F0.imprint","IMPRINT",FACE,{"disambiguationData":[TD([[makeQuery(id+"F0.imprint","IMPRINT",EDGE,{"disambiguationData":[TD([[subQ2,1.0]])],"derivedFrom":subQ1}),-1.0]])]});}
            var Q964;
            {var subQ0=sQuery(id+"F0.wireOp",EDGE,"E3.4.0.19");Q964=makeQuery(id+"F0.imprint","IMPRINT",FACE,{"disambiguationData":[TD([[makeQuery(id+"F0.imprint","IMPRINT",EDGE,{"derivedFrom":subQ0}),-1.0]])]});}
            var Q965;
            {var subQ3=sQuery(id+"F0.wireOp",EDGE,"E3.4.0.7");Q965=makeQuery(id+"F0.imprint","IMPRINT",FACE,{"disambiguationData":[TD([[makeQuery(id+"F0.imprint","IMPRINT",EDGE,{"derivedFrom":subQ3}),1.0]])]});}
            var Q966;
            {var subQ0=sQuery(id+"F0.wireOp",EDGE,"E3.3.0.97");var subQ1=sQuery(id+"F0.wireOp",EDGE,"E3.3.0.44");var subQ2=makeQuery(id+"F0.imprint","INTERSECT",VERTEX,{"derivedFrom":[subQ1,subQ0]});Q966=makeQuery(id+"F0.imprint","IMPRINT",FACE,{"disambiguationData":[TD([[makeQuery(id+"F0.imprint","IMPRINT",EDGE,{"disambiguationData":[TD([[subQ2,1.0]])],"derivedFrom":subQ1}),-1.0]])]});}
            var Q967;
            {var subQ0=sQuery(id+"F0.wireOp",EDGE,"E3.5.0.96");var subQ1=sQuery(id+"F0.wireOp",EDGE,"E3.5.0.43");var subQ2=makeQuery(id+"F0.imprint","INTERSECT",VERTEX,{"derivedFrom":[subQ1,subQ0]});Q967=makeQuery(id+"F0.imprint","IMPRINT",FACE,{"disambiguationData":[TD([[makeQuery(id+"F0.imprint","IMPRINT",EDGE,{"disambiguationData":[TD([[subQ2,1.0]])],"derivedFrom":subQ1}),-1.0]])]});}
            var Q968;
            {var subQ0=sQuery(id+"F0.wireOp",EDGE,"E3.5.0.42");var subQ1=sQuery(id+"F0.wireOp",EDGE,"E3.5.0.16");var subQ2=makeQuery(id+"F0.imprint","INTERSECT",VERTEX,{"derivedFrom":[subQ1,subQ0]});Q968=makeQuery(id+"F0.imprint","IMPRINT",FACE,{"disambiguationData":[TD([[makeQuery(id+"F0.imprint","IMPRINT",EDGE,{"disambiguationData":[TD([[subQ2,-1.0]])],"derivedFrom":subQ1}),-1.0]])]});}
            var Q969;
            {var subQ3=sQuery(id+"F0.wireOp",EDGE,"E3.4.0.118");Q969=makeQuery(id+"F0.imprint","IMPRINT",FACE,{"disambiguationData":[TD([[makeQuery(id+"F0.imprint","IMPRINT",EDGE,{"derivedFrom":subQ3}),1.0]])]});}
            var Q970;
            {var subQ0=sQuery(id+"F0.wireOp",EDGE,"E3.6.0.63");Q970=makeQuery(id+"F0.imprint","IMPRINT",FACE,{"disambiguationData":[TD([[makeQuery(id+"F0.imprint","IMPRINT",EDGE,{"derivedFrom":subQ0}),-1.0]])]});}
            var Q971;
            {var subQ5=sQuery(id+"F0.wireOp",EDGE,"E3.7.0.56");Q971=makeQuery(id+"F0.imprint","IMPRINT",FACE,{"disambiguationData":[TD([[makeQuery(id+"F0.imprint","IMPRINT",EDGE,{"derivedFrom":subQ5}),1.0]])]});}
            var Q972;
            {var subQ7=sQuery(id+"F0.wireOp",EDGE,"E3.6.0.54");Q972=makeQuery(id+"F0.imprint","IMPRINT",FACE,{"disambiguationData":[TD([[makeQuery(id+"F0.imprint","IMPRINT",EDGE,{"derivedFrom":subQ7}),-1.0]])]});}
            var Q973;
            {var subQ5=sQuery(id+"F0.wireOp",EDGE,"E3.8.0.22");Q973=makeQuery(id+"F0.imprint","IMPRINT",FACE,{"disambiguationData":[TD([[makeQuery(id+"F0.imprint","IMPRINT",EDGE,{"derivedFrom":subQ5}),-1.0]])]});}
            var Q974;
            {var subQ0=sQuery(id+"F0.wireOp",EDGE,"E3.7.0.100");var subQ1=sQuery(id+"F0.wireOp",EDGE,"E3.7.0.52");var subQ2=makeQuery(id+"F0.imprint","INTERSECT",VERTEX,{"derivedFrom":[subQ1,subQ0]});Q974=makeQuery(id+"F0.imprint","IMPRINT",FACE,{"disambiguationData":[TD([[makeQuery(id+"F0.imprint","IMPRINT",EDGE,{"disambiguationData":[TD([[subQ2,1.0]])],"derivedFrom":subQ1}),-1.0]])]});}
            var Q975;
            {var subQ0=sQuery(id+"F0.wireOp",EDGE,"E3.7.0.89");Q975=makeQuery(id+"F0.imprint","IMPRINT",FACE,{"disambiguationData":[TD([[makeQuery(id+"F0.imprint","IMPRINT",EDGE,{"derivedFrom":subQ0}),-1.0]])]});}
            var Q976;
            {var subQ5=sQuery(id+"F0.wireOp",EDGE,"E3.8.0.53");Q976=makeQuery(id+"F0.imprint","IMPRINT",FACE,{"disambiguationData":[TD([[makeQuery(id+"F0.imprint","IMPRINT",EDGE,{"derivedFrom":subQ5}),-1.0]])]});}
            var Q977;
            {var subQ0=sQuery(id+"F0.wireOp",EDGE,"E3.14.0.57");Q977=makeQuery(id+"F0.imprint","IMPRINT",FACE,{"disambiguationData":[TD([[makeQuery(id+"F0.imprint","IMPRINT",EDGE,{"derivedFrom":subQ0}),-1.0]])]});}
            var Q978;
            {var subQ3=sQuery(id+"F0.wireOp",EDGE,"E3.15.0.53");Q978=makeQuery(id+"F0.imprint","IMPRINT",FACE,{"disambiguationData":[TD([[makeQuery(id+"F0.imprint","IMPRINT",EDGE,{"derivedFrom":subQ3}),1.0]])]});}
            var Q979;
            {var subQ7=sQuery(id+"F0.wireOp",EDGE,"E3.15.0.87");Q979=makeQuery(id+"F0.imprint","IMPRINT",FACE,{"disambiguationData":[TD([[makeQuery(id+"F0.imprint","IMPRINT",EDGE,{"derivedFrom":subQ7}),-1.0]])]});}
            var Q980;
            {var subQ0=sQuery(id+"F0.wireOp",EDGE,"E3.1.0.69");var subQ1=sQuery(id+"F0.wireOp",EDGE,"E3.1.0.12");var subQ2=makeQuery(id+"F0.imprint","INTERSECT",VERTEX,{"derivedFrom":[subQ1,subQ0]});Q980=makeQuery(id+"F0.imprint","IMPRINT",FACE,{"disambiguationData":[TD([[makeQuery(id+"F0.imprint","IMPRINT",EDGE,{"disambiguationData":[TD([[subQ2,1.0]])],"derivedFrom":subQ1}),-1.0]])]});}
            var Q981;
            {var subQ0=sQuery(id+"F0.wireOp",EDGE,"E3.1.0.94");var subQ1=sQuery(id+"F0.wireOp",EDGE,"E3.1.0.42");var subQ2=makeQuery(id+"F0.imprint","INTERSECT",VERTEX,{"derivedFrom":[subQ1,subQ0]});Q981=makeQuery(id+"F0.imprint","IMPRINT",FACE,{"disambiguationData":[TD([[makeQuery(id+"F0.imprint","IMPRINT",EDGE,{"disambiguationData":[TD([[subQ2,1.0]])],"derivedFrom":subQ1}),-1.0]])]});}
            var Q982;
            {var subQ3=sQuery(id+"F0.wireOp",EDGE,"E3.3.0.85");Q982=makeQuery(id+"F0.imprint","IMPRINT",FACE,{"disambiguationData":[TD([[makeQuery(id+"F0.imprint","IMPRINT",EDGE,{"derivedFrom":subQ3}),1.0]])]});}
            var Q983;
            {var subQ3=sQuery(id+"F0.wireOp",EDGE,"E3.2.0.103");Q983=makeQuery(id+"F0.imprint","IMPRINT",FACE,{"disambiguationData":[TD([[makeQuery(id+"F0.imprint","IMPRINT",EDGE,{"derivedFrom":subQ3}),1.0]])]});}
            var Q984;
            {var subQ0=sQuery(id+"F0.wireOp",EDGE,"E3.16.0.89");Q984=makeQuery(id+"F0.imprint","IMPRINT",FACE,{"disambiguationData":[TD([[makeQuery(id+"F0.imprint","IMPRINT",EDGE,{"derivedFrom":subQ0}),-1.0]])]});}
            var Q985;
            {var subQ0=sQuery(id+"F0.wireOp",EDGE,"E3.14.0.42");var subQ1=sQuery(id+"F0.wireOp",EDGE,"E3.14.0.16");var subQ2=makeQuery(id+"F0.imprint","INTERSECT",VERTEX,{"derivedFrom":[subQ1,subQ0]});Q985=makeQuery(id+"F0.imprint","IMPRINT",FACE,{"disambiguationData":[TD([[makeQuery(id+"F0.imprint","IMPRINT",EDGE,{"disambiguationData":[TD([[subQ2,-1.0]])],"derivedFrom":subQ1}),-1.0]])]});}
            var Q986;
            {var subQ0=sQuery(id+"F0.wireOp",EDGE,"E3.11.0.91");var subQ1=sQuery(id+"F0.wireOp",EDGE,"E3.11.0.49");var subQ2=makeQuery(id+"F0.imprint","INTERSECT",VERTEX,{"derivedFrom":[subQ1,subQ0]});Q986=makeQuery(id+"F0.imprint","IMPRINT",FACE,{"disambiguationData":[TD([[makeQuery(id+"F0.imprint","IMPRINT",EDGE,{"disambiguationData":[TD([[subQ2,-1.0]])],"derivedFrom":subQ1}),-1.0]])]});}
            var Q987;
            {var subQ3=sQuery(id+"F0.wireOp",EDGE,"E3.13.0.81");Q987=makeQuery(id+"F0.imprint","IMPRINT",FACE,{"disambiguationData":[TD([[makeQuery(id+"F0.imprint","IMPRINT",EDGE,{"derivedFrom":subQ3}),1.0]])]});}
            var Q988;
            {var subQ5=sQuery(id+"F0.wireOp",EDGE,"E3.5.0.57");Q988=makeQuery(id+"F0.imprint","IMPRINT",FACE,{"disambiguationData":[TD([[makeQuery(id+"F0.imprint","IMPRINT",EDGE,{"derivedFrom":subQ5}),1.0]])]});}
            var Q989;
            {var subQ3=sQuery(id+"F0.wireOp",EDGE,"E3.7.0.84");Q989=makeQuery(id+"F0.imprint","IMPRINT",FACE,{"disambiguationData":[TD([[makeQuery(id+"F0.imprint","IMPRINT",EDGE,{"derivedFrom":subQ3}),1.0]])]});}
            var Q990;
            {var subQ0=sQuery(id+"F0.wireOp",EDGE,"E3.6.0.72");var subQ1=sQuery(id+"F0.wireOp",EDGE,"E3.6.0.10");var subQ2=makeQuery(id+"F0.imprint","INTERSECT",VERTEX,{"derivedFrom":[subQ1,subQ0]});Q990=makeQuery(id+"F0.imprint","IMPRINT",FACE,{"disambiguationData":[TD([[makeQuery(id+"F0.imprint","IMPRINT",EDGE,{"disambiguationData":[TD([[subQ2,1.0]])],"derivedFrom":subQ1}),-1.0]])]});}
            var Q991;
            {var subQ0=sQuery(id+"F0.wireOp",EDGE,"E3.8.0.40");var subQ1=sQuery(id+"F0.wireOp",EDGE,"E3.8.0.18");var subQ2=makeQuery(id+"F0.imprint","INTERSECT",VERTEX,{"derivedFrom":[subQ1,subQ0]});Q991=makeQuery(id+"F0.imprint","IMPRINT",FACE,{"disambiguationData":[TD([[makeQuery(id+"F0.imprint","IMPRINT",EDGE,{"disambiguationData":[TD([[subQ2,-1.0]])],"derivedFrom":subQ1}),-1.0]])]});}
            var Q992;
            {var subQ0=sQuery(id+"F0.wireOp",EDGE,"E3.7.0.41");var subQ1=sQuery(id+"F0.wireOp",EDGE,"E3.7.0.6");var subQ2=makeQuery(id+"F0.imprint","INTERSECT",VERTEX,{"derivedFrom":[subQ1,subQ0]});Q992=makeQuery(id+"F0.imprint","IMPRINT",FACE,{"disambiguationData":[TD([[makeQuery(id+"F0.imprint","IMPRINT",EDGE,{"disambiguationData":[TD([[subQ2,1.0]])],"derivedFrom":subQ1}),-1.0]])]});}
            var Q993;
            {var subQ0=sQuery(id+"F0.wireOp",EDGE,"E3.9.0.116");Q993=makeQuery(id+"F0.imprint","IMPRINT",FACE,{"disambiguationData":[TD([[makeQuery(id+"F0.imprint","IMPRINT",EDGE,{"derivedFrom":subQ0}),-1.0]])]});}
            var Q994;
            {var subQ0=sQuery(id+"F0.wireOp",EDGE,"E3.10.0.94");var subQ1=sQuery(id+"F0.wireOp",EDGE,"E3.10.0.42");var subQ2=makeQuery(id+"F0.imprint","INTERSECT",VERTEX,{"derivedFrom":[subQ1,subQ0]});Q994=makeQuery(id+"F0.imprint","IMPRINT",FACE,{"disambiguationData":[TD([[makeQuery(id+"F0.imprint","IMPRINT",EDGE,{"disambiguationData":[TD([[subQ2,1.0]])],"derivedFrom":subQ1}),-1.0]])]});}
            var Q995;
            {var subQ3=sQuery(id+"F0.wireOp",EDGE,"E3.10.0.66");Q995=makeQuery(id+"F0.imprint","IMPRINT",FACE,{"disambiguationData":[TD([[makeQuery(id+"F0.imprint","IMPRINT",EDGE,{"derivedFrom":subQ3}),-1.0]])]});}
            var Q996;
            {var subQ3=sQuery(id+"F0.wireOp",EDGE,"E3.11.0.103");Q996=makeQuery(id+"F0.imprint","IMPRINT",FACE,{"disambiguationData":[TD([[makeQuery(id+"F0.imprint","IMPRINT",EDGE,{"derivedFrom":subQ3}),1.0]])]});}
            var Q997;
            {var subQ3=sQuery(id+"F0.wireOp",EDGE,"E3.11.0.82");Q997=makeQuery(id+"F0.imprint","IMPRINT",FACE,{"disambiguationData":[TD([[makeQuery(id+"F0.imprint","IMPRINT",EDGE,{"derivedFrom":subQ3}),1.0]])]});}
            var Q998;
            {var subQ3=sQuery(id+"F0.wireOp",EDGE,"E3.11.0.55");Q998=makeQuery(id+"F0.imprint","IMPRINT",FACE,{"disambiguationData":[TD([[makeQuery(id+"F0.imprint","IMPRINT",EDGE,{"derivedFrom":subQ3}),1.0]])]});}
            var Q999;
            {var subQ5=sQuery(id+"F0.wireOp",EDGE,"E3.16.0.56");Q999=makeQuery(id+"F0.imprint","IMPRINT",FACE,{"disambiguationData":[TD([[makeQuery(id+"F0.imprint","IMPRINT",EDGE,{"derivedFrom":subQ5}),1.0]])]});}
            var Q1000;
            {var subQ0=sQuery(id+"F0.wireOp",EDGE,"E3.16.0.64");Q1000=makeQuery(id+"F0.imprint","IMPRINT",FACE,{"disambiguationData":[TD([[makeQuery(id+"F0.imprint","IMPRINT",EDGE,{"derivedFrom":subQ0}),-1.0]])]});}
            var Q1001;
            {var subQ5=sQuery(id+"F0.wireOp",EDGE,"E3.1.0.22");Q1001=makeQuery(id+"F0.imprint","IMPRINT",FACE,{"disambiguationData":[TD([[makeQuery(id+"F0.imprint","IMPRINT",EDGE,{"derivedFrom":subQ5}),-1.0]])]});}
            var Q1002;
            {var subQ7=sQuery(id+"F0.wireOp",EDGE,"E3.2.0.83");Q1002=makeQuery(id+"F0.imprint","IMPRINT",FACE,{"disambiguationData":[TD([[makeQuery(id+"F0.imprint","IMPRINT",EDGE,{"derivedFrom":subQ7}),-1.0]])]});}
            var Q1003;
            {var subQ0=sQuery(id+"F0.wireOp",EDGE,"E3.3.0.68");var subQ1=sQuery(id+"F0.wireOp",EDGE,"E3.3.0.8");var subQ2=makeQuery(id+"F0.imprint","INTERSECT",VERTEX,{"derivedFrom":[subQ1,subQ0]});Q1003=makeQuery(id+"F0.imprint","IMPRINT",FACE,{"disambiguationData":[TD([[makeQuery(id+"F0.imprint","IMPRINT",EDGE,{"disambiguationData":[TD([[subQ2,1.0]])],"derivedFrom":subQ1}),-1.0]])]});}
            var Q1004;
            {var subQ5=sQuery(id+"F0.wireOp",EDGE,"E3.4.0.82");Q1004=makeQuery(id+"F0.imprint","IMPRINT",FACE,{"disambiguationData":[TD([[makeQuery(id+"F0.imprint","IMPRINT",EDGE,{"derivedFrom":subQ5}),-1.0]])]});}
            var Q1005;
            {var subQ0=sQuery(id+"F0.wireOp",EDGE,"E3.13.0.91");var subQ1=sQuery(id+"F0.wireOp",EDGE,"E3.13.0.49");var subQ2=makeQuery(id+"F0.imprint","INTERSECT",VERTEX,{"derivedFrom":[subQ1,subQ0]});Q1005=makeQuery(id+"F0.imprint","IMPRINT",FACE,{"disambiguationData":[TD([[makeQuery(id+"F0.imprint","IMPRINT",EDGE,{"disambiguationData":[TD([[subQ2,-1.0]])],"derivedFrom":subQ1}),-1.0]])]});}
            var Q1006;
            {var subQ3=sQuery(id+"F0.wireOp",EDGE,"E3.14.0.65");Q1006=makeQuery(id+"F0.imprint","IMPRINT",FACE,{"disambiguationData":[TD([[makeQuery(id+"F0.imprint","IMPRINT",EDGE,{"derivedFrom":subQ3}),-1.0]])]});}
            var Q1007;
            {var subQ0=sQuery(id+"F0.wireOp",EDGE,"E3.16.0.57");Q1007=makeQuery(id+"F0.imprint","IMPRINT",FACE,{"disambiguationData":[TD([[makeQuery(id+"F0.imprint","IMPRINT",EDGE,{"derivedFrom":subQ0}),-1.0]])]});}
            var Q1008;
            {var subQ3=sQuery(id+"F0.wireOp",EDGE,"E3.15.0.54");Q1008=makeQuery(id+"F0.imprint","IMPRINT",FACE,{"disambiguationData":[TD([[makeQuery(id+"F0.imprint","IMPRINT",EDGE,{"derivedFrom":subQ3}),1.0]])]});}
            var Q1009;
            {var subQ0=sQuery(id+"F0.wireOp",EDGE,"E3.15.0.72");var subQ1=sQuery(id+"F0.wireOp",EDGE,"E3.15.0.10");var subQ2=makeQuery(id+"F0.imprint","INTERSECT",VERTEX,{"derivedFrom":[subQ1,subQ0]});Q1009=makeQuery(id+"F0.imprint","IMPRINT",FACE,{"disambiguationData":[TD([[makeQuery(id+"F0.imprint","IMPRINT",EDGE,{"disambiguationData":[TD([[subQ2,1.0]])],"derivedFrom":subQ1}),-1.0]])]});}
            var Q1010;
            {var subQ3=sQuery(id+"F0.wireOp",EDGE,"E3.15.0.81");Q1010=makeQuery(id+"F0.imprint","IMPRINT",FACE,{"disambiguationData":[TD([[makeQuery(id+"F0.imprint","IMPRINT",EDGE,{"derivedFrom":subQ3}),1.0]])]});}
            var Q1011;
            {var subQ0=sQuery(id+"F0.wireOp",EDGE,"E3.12.0.68");var subQ1=sQuery(id+"F0.wireOp",EDGE,"E3.12.0.11");var subQ2=makeQuery(id+"F0.imprint","INTERSECT",VERTEX,{"derivedFrom":[subQ1,subQ0]});Q1011=makeQuery(id+"F0.imprint","IMPRINT",FACE,{"disambiguationData":[TD([[makeQuery(id+"F0.imprint","IMPRINT",EDGE,{"disambiguationData":[TD([[subQ2,1.0]])],"derivedFrom":subQ1}),-1.0]])]});}
            var Q1012;
            {var subQ5=sQuery(id+"F0.wireOp",EDGE,"E3.17.0.57");Q1012=makeQuery(id+"F0.imprint","IMPRINT",FACE,{"disambiguationData":[TD([[makeQuery(id+"F0.imprint","IMPRINT",EDGE,{"derivedFrom":subQ5}),1.0]])]});}
            var Q1013;
            {var subQ0=sQuery(id+"F0.wireOp",EDGE,"E3.6.0.41");var subQ1=sQuery(id+"F0.wireOp",EDGE,"E3.6.0.13");var subQ2=makeQuery(id+"F0.imprint","INTERSECT",VERTEX,{"derivedFrom":[subQ1,subQ0]});Q1013=makeQuery(id+"F0.imprint","IMPRINT",FACE,{"disambiguationData":[TD([[makeQuery(id+"F0.imprint","IMPRINT",EDGE,{"disambiguationData":[TD([[subQ2,-1.0]])],"derivedFrom":subQ1}),-1.0]])]});}
            var Q1014;
            {var subQ0=sQuery(id+"F0.wireOp",EDGE,"E3.6.0.19");Q1014=makeQuery(id+"F0.imprint","IMPRINT",FACE,{"disambiguationData":[TD([[makeQuery(id+"F0.imprint","IMPRINT",EDGE,{"derivedFrom":subQ0}),-1.0]])]});}
            var Q1015;
            {var subQ0=sQuery(id+"F0.wireOp",EDGE,"E3.8.0.63");Q1015=makeQuery(id+"F0.imprint","IMPRINT",FACE,{"disambiguationData":[TD([[makeQuery(id+"F0.imprint","IMPRINT",EDGE,{"derivedFrom":subQ0}),-1.0]])]});}
            var Q1016;
            {var subQ0=sQuery(id+"F0.wireOp",EDGE,"E3.8.0.32");var subQ1=sQuery(id+"F0.wireOp",EDGE,"E3.8.0.0");var subQ2=makeQuery(id+"F0.imprint","INTERSECT",VERTEX,{"derivedFrom":[subQ1,subQ0]});Q1016=makeQuery(id+"F0.imprint","IMPRINT",FACE,{"disambiguationData":[TD([[makeQuery(id+"F0.imprint","IMPRINT",EDGE,{"disambiguationData":[TD([[subQ2,1.0]])],"derivedFrom":subQ1}),-1.0]])]});}
            var Q1017;
            {var subQ7=sQuery(id+"F0.wireOp",EDGE,"E3.8.0.54");Q1017=makeQuery(id+"F0.imprint","IMPRINT",FACE,{"disambiguationData":[TD([[makeQuery(id+"F0.imprint","IMPRINT",EDGE,{"derivedFrom":subQ7}),-1.0]])]});}
            var Q1018;
            {var subQ5=sQuery(id+"F0.wireOp",EDGE,"E3.10.0.53");Q1018=makeQuery(id+"F0.imprint","IMPRINT",FACE,{"disambiguationData":[TD([[makeQuery(id+"F0.imprint","IMPRINT",EDGE,{"derivedFrom":subQ5}),-1.0]])]});}
            var Q1019;
            {var subQ0=sQuery(id+"F0.wireOp",EDGE,"E3.9.0.100");var subQ1=sQuery(id+"F0.wireOp",EDGE,"E3.9.0.52");var subQ2=makeQuery(id+"F0.imprint","INTERSECT",VERTEX,{"derivedFrom":[subQ1,subQ0]});Q1019=makeQuery(id+"F0.imprint","IMPRINT",FACE,{"disambiguationData":[TD([[makeQuery(id+"F0.imprint","IMPRINT",EDGE,{"disambiguationData":[TD([[subQ2,1.0]])],"derivedFrom":subQ1}),-1.0]])]});}
            var Q1020;
            {var subQ7=sQuery(id+"F0.wireOp",EDGE,"E3.11.0.83");Q1020=makeQuery(id+"F0.imprint","IMPRINT",FACE,{"disambiguationData":[TD([[makeQuery(id+"F0.imprint","IMPRINT",EDGE,{"derivedFrom":subQ7}),-1.0]])]});}
            var Q1021;
            {var subQ0=sQuery(id+"F0.wireOp",EDGE,"E3.12.0.97");var subQ1=sQuery(id+"F0.wireOp",EDGE,"E3.12.0.40");var subQ2=makeQuery(id+"F0.imprint","INTERSECT",VERTEX,{"derivedFrom":[subQ1,subQ0]});Q1021=makeQuery(id+"F0.imprint","IMPRINT",FACE,{"disambiguationData":[TD([[makeQuery(id+"F0.imprint","IMPRINT",EDGE,{"disambiguationData":[TD([[subQ2,1.0]])],"derivedFrom":subQ1}),-1.0]])]});}
            var Q1022;
            {var subQ0=sQuery(id+"F0.wireOp",EDGE,"E3.12.0.39");var subQ1=sQuery(id+"F0.wireOp",EDGE,"E3.12.0.17");var subQ2=makeQuery(id+"F0.imprint","INTERSECT",VERTEX,{"derivedFrom":[subQ1,subQ0]});Q1022=makeQuery(id+"F0.imprint","IMPRINT",FACE,{"disambiguationData":[TD([[makeQuery(id+"F0.imprint","IMPRINT",EDGE,{"disambiguationData":[TD([[subQ2,-1.0]])],"derivedFrom":subQ1}),-1.0]])]});}
            var Q1023;
            {var subQ7=sQuery(id+"F0.wireOp",EDGE,"E3.1.0.87");Q1023=makeQuery(id+"F0.imprint","IMPRINT",FACE,{"disambiguationData":[TD([[makeQuery(id+"F0.imprint","IMPRINT",EDGE,{"derivedFrom":subQ7}),-1.0]])]});}
            var Q1024;
            {var subQ3=sQuery(id+"F0.wireOp",EDGE,"E3.2.0.56");Q1024=makeQuery(id+"F0.imprint","IMPRINT",FACE,{"disambiguationData":[TD([[makeQuery(id+"F0.imprint","IMPRINT",EDGE,{"derivedFrom":subQ3}),-1.0]])]});}
            var Q1025;
            {var subQ0=sQuery(id+"F0.wireOp",EDGE,"E3.3.0.69");var subQ1=sQuery(id+"F0.wireOp",EDGE,"E3.3.0.12");var subQ2=makeQuery(id+"F0.imprint","INTERSECT",VERTEX,{"derivedFrom":[subQ1,subQ0]});Q1025=makeQuery(id+"F0.imprint","IMPRINT",FACE,{"disambiguationData":[TD([[makeQuery(id+"F0.imprint","IMPRINT",EDGE,{"disambiguationData":[TD([[subQ2,1.0]])],"derivedFrom":subQ1}),-1.0]])]});}
            var Q1026;
            {var subQ3=sQuery(id+"F0.wireOp",EDGE,"E3.4.0.55");Q1026=makeQuery(id+"F0.imprint","IMPRINT",FACE,{"disambiguationData":[TD([[makeQuery(id+"F0.imprint","IMPRINT",EDGE,{"derivedFrom":subQ3}),1.0]])]});}
            var Q1027;
            {var subQ3=sQuery(id+"F0.wireOp",EDGE,"E3.13.0.103");Q1027=makeQuery(id+"F0.imprint","IMPRINT",FACE,{"disambiguationData":[TD([[makeQuery(id+"F0.imprint","IMPRINT",EDGE,{"derivedFrom":subQ3}),1.0]])]});}
            var Q1028;
            {var subQ0=sQuery(id+"F0.wireOp",EDGE,"E3.18.0.37");var subQ5=sQuery(id+"F0.wireOp",EDGE,"E3.18.0.9");var subQ7=makeQuery(id+"F0.imprint","INTERSECT",VERTEX,{"derivedFrom":[subQ5,subQ0]});Q1028=makeQuery(id+"F0.imprint","IMPRINT",FACE,{"disambiguationData":[TD([[makeQuery(id+"F0.imprint","IMPRINT",EDGE,{"disambiguationData":[TD([[subQ7,1.0]])],"derivedFrom":subQ5}),1.0]])]});}
            var Q1029;
            {var subQ0=sQuery(id+"F0.wireOp",EDGE,"E3.14.0.97");var subQ1=sQuery(id+"F0.wireOp",EDGE,"E3.14.0.44");var subQ2=makeQuery(id+"F0.imprint","INTERSECT",VERTEX,{"derivedFrom":[subQ1,subQ0]});Q1029=makeQuery(id+"F0.imprint","IMPRINT",FACE,{"disambiguationData":[TD([[makeQuery(id+"F0.imprint","IMPRINT",EDGE,{"disambiguationData":[TD([[subQ2,1.0]])],"derivedFrom":subQ1}),-1.0]])]});}
            var Q1030;
            {var subQ0=sQuery(id+"F0.wireOp",EDGE,"E3.16.0.51");var subQ1=sQuery(id+"F0.wireOp",EDGE,"E3.16.0.10");var subQ2=makeQuery(id+"F0.imprint","INTERSECT",VERTEX,{"derivedFrom":[subQ1,subQ0]});Q1030=makeQuery(id+"F0.imprint","IMPRINT",FACE,{"disambiguationData":[TD([[makeQuery(id+"F0.imprint","IMPRINT",EDGE,{"disambiguationData":[TD([[subQ2,-1.0]])],"derivedFrom":subQ1}),1.0]])]});}
            var Q1031;
            {var subQ0=sQuery(id+"F0.wireOp",EDGE,"E3.16.0.42");var subQ1=sQuery(id+"F0.wireOp",EDGE,"E3.16.0.16");var subQ2=makeQuery(id+"F0.imprint","INTERSECT",VERTEX,{"derivedFrom":[subQ1,subQ0]});Q1031=makeQuery(id+"F0.imprint","IMPRINT",FACE,{"disambiguationData":[TD([[makeQuery(id+"F0.imprint","IMPRINT",EDGE,{"disambiguationData":[TD([[subQ2,-1.0]])],"derivedFrom":subQ1}),-1.0]])]});}
            var Q1032;
            {var subQ0=sQuery(id+"F0.wireOp",EDGE,"E3.13.0.20");Q1032=makeQuery(id+"F0.imprint","IMPRINT",FACE,{"disambiguationData":[TD([[makeQuery(id+"F0.imprint","IMPRINT",EDGE,{"derivedFrom":subQ0}),-1.0]])]});}
            var Q1033;
            {var subQ0=sQuery(id+"F0.wireOp",EDGE,"E3.7.0.96");var subQ1=sQuery(id+"F0.wireOp",EDGE,"E3.7.0.39");var subQ2=makeQuery(id+"F0.imprint","INTERSECT",VERTEX,{"derivedFrom":[subQ1,subQ0]});Q1033=makeQuery(id+"F0.imprint","IMPRINT",FACE,{"disambiguationData":[TD([[makeQuery(id+"F0.imprint","IMPRINT",EDGE,{"disambiguationData":[TD([[subQ2,1.0]])],"derivedFrom":subQ1}),-1.0]])]});}
            var Q1034;
            {var subQ0=sQuery(id+"F0.wireOp",EDGE,"E3.9.0.41");var subQ1=sQuery(id+"F0.wireOp",EDGE,"E3.9.0.6");var subQ2=makeQuery(id+"F0.imprint","INTERSECT",VERTEX,{"derivedFrom":[subQ1,subQ0]});Q1034=makeQuery(id+"F0.imprint","IMPRINT",FACE,{"disambiguationData":[TD([[makeQuery(id+"F0.imprint","IMPRINT",EDGE,{"disambiguationData":[TD([[subQ2,1.0]])],"derivedFrom":subQ1}),-1.0]])]});}
            var Q1035;
            {var subQ0=sQuery(id+"F0.wireOp",EDGE,"E3.10.0.40");var subQ1=sQuery(id+"F0.wireOp",EDGE,"E3.10.0.18");var subQ2=makeQuery(id+"F0.imprint","INTERSECT",VERTEX,{"derivedFrom":[subQ1,subQ0]});Q1035=makeQuery(id+"F0.imprint","IMPRINT",FACE,{"disambiguationData":[TD([[makeQuery(id+"F0.imprint","IMPRINT",EDGE,{"disambiguationData":[TD([[subQ2,-1.0]])],"derivedFrom":subQ1}),-1.0]])]});}
            var Q1036;
            {var subQ3=sQuery(id+"F0.wireOp",EDGE,"E3.17.0.65");Q1036=makeQuery(id+"F0.imprint","IMPRINT",FACE,{"disambiguationData":[TD([[makeQuery(id+"F0.imprint","IMPRINT",EDGE,{"derivedFrom":subQ3}),-1.0]])]});}
            var Q1037;
            {var subQ3=sQuery(id+"F0.wireOp",EDGE,"E3.12.0.66");Q1037=makeQuery(id+"F0.imprint","IMPRINT",FACE,{"disambiguationData":[TD([[makeQuery(id+"F0.imprint","IMPRINT",EDGE,{"derivedFrom":subQ3}),-1.0]])]});}
            var Q1038;
            {var subQ3=sQuery(id+"F0.wireOp",EDGE,"E3.13.0.82");Q1038=makeQuery(id+"F0.imprint","IMPRINT",FACE,{"disambiguationData":[TD([[makeQuery(id+"F0.imprint","IMPRINT",EDGE,{"derivedFrom":subQ3}),1.0]])]});}
            var Q1039;
            {var subQ0=sQuery(id+"F0.wireOp",EDGE,"E3.1.0.63");Q1039=makeQuery(id+"F0.imprint","IMPRINT",FACE,{"disambiguationData":[TD([[makeQuery(id+"F0.imprint","IMPRINT",EDGE,{"derivedFrom":subQ0}),-1.0]])]});}
            var Q1040;
            {var subQ7=sQuery(id+"F0.wireOp",EDGE,"E3.1.0.54");Q1040=makeQuery(id+"F0.imprint","IMPRINT",FACE,{"disambiguationData":[TD([[makeQuery(id+"F0.imprint","IMPRINT",EDGE,{"derivedFrom":subQ7}),-1.0]])]});}
            var Q1041;
            {var subQ3=sQuery(id+"F0.wireOp",EDGE,"E3.3.0.86");Q1041=makeQuery(id+"F0.imprint","IMPRINT",FACE,{"disambiguationData":[TD([[makeQuery(id+"F0.imprint","IMPRINT",EDGE,{"derivedFrom":subQ3}),1.0]])]});}
            var Q1042;
            {var subQ5=sQuery(id+"F0.wireOp",EDGE,"E3.3.0.22");Q1042=makeQuery(id+"F0.imprint","IMPRINT",FACE,{"disambiguationData":[TD([[makeQuery(id+"F0.imprint","IMPRINT",EDGE,{"derivedFrom":subQ5}),-1.0]])]});}
            var Q1043;
            {var subQ0=sQuery(id+"F0.wireOp",EDGE,"E3.2.0.100");var subQ1=sQuery(id+"F0.wireOp",EDGE,"E3.2.0.52");var subQ2=makeQuery(id+"F0.imprint","INTERSECT",VERTEX,{"derivedFrom":[subQ1,subQ0]});Q1043=makeQuery(id+"F0.imprint","IMPRINT",FACE,{"disambiguationData":[TD([[makeQuery(id+"F0.imprint","IMPRINT",EDGE,{"disambiguationData":[TD([[subQ2,1.0]])],"derivedFrom":subQ1}),-1.0]])]});}
            var Q1044;
            {var subQ0=sQuery(id+"F0.wireOp",EDGE,"E3.2.0.89");Q1044=makeQuery(id+"F0.imprint","IMPRINT",FACE,{"disambiguationData":[TD([[makeQuery(id+"F0.imprint","IMPRINT",EDGE,{"derivedFrom":subQ0}),-1.0]])]});}
            var Q1045;
            {var subQ0=sQuery(id+"F0.wireOp",EDGE,"E3.17.0.96");var subQ1=sQuery(id+"F0.wireOp",EDGE,"E3.17.0.39");var subQ2=makeQuery(id+"F0.imprint","INTERSECT",VERTEX,{"derivedFrom":[subQ1,subQ0]});Q1045=makeQuery(id+"F0.imprint","IMPRINT",FACE,{"disambiguationData":[TD([[makeQuery(id+"F0.imprint","IMPRINT",EDGE,{"disambiguationData":[TD([[subQ2,1.0]])],"derivedFrom":subQ1}),-1.0]])]});}
            var Q1046;
            {var subQ0=sQuery(id+"F0.wireOp",EDGE,"E3.5.0.39");var subQ1=sQuery(id+"F0.wireOp",EDGE,"E3.5.0.17");var subQ2=makeQuery(id+"F0.imprint","INTERSECT",VERTEX,{"derivedFrom":[subQ1,subQ0]});Q1046=makeQuery(id+"F0.imprint","IMPRINT",FACE,{"disambiguationData":[TD([[makeQuery(id+"F0.imprint","IMPRINT",EDGE,{"disambiguationData":[TD([[subQ2,-1.0]])],"derivedFrom":subQ1}),-1.0]])]});}
            var Q1047;
            {var subQ0=sQuery(id+"F0.wireOp",EDGE,"E3.4.0.75");var subQ1=sQuery(id+"F0.wireOp",EDGE,"E3.4.0.52");var subQ2=makeQuery(id+"F0.imprint","INTERSECT",VERTEX,{"derivedFrom":[subQ1,subQ0]});Q1047=makeQuery(id+"F0.imprint","IMPRINT",FACE,{"disambiguationData":[TD([[makeQuery(id+"F0.imprint","IMPRINT",EDGE,{"disambiguationData":[TD([[subQ2,-1.0]])],"derivedFrom":subQ1}),-1.0]])]});}
            var Q1048;
            {var subQ3=sQuery(id+"F0.wireOp",EDGE,"E3.6.0.31");Q1048=makeQuery(id+"F0.imprint","IMPRINT",FACE,{"disambiguationData":[TD([[makeQuery(id+"F0.imprint","IMPRINT",EDGE,{"derivedFrom":subQ3}),-1.0]])]});}
            var Q1049;
            {var subQ3=sQuery(id+"F0.wireOp",EDGE,"E3.19.0.84");Q1049=makeQuery(id+"F0.imprint","IMPRINT",FACE,{"disambiguationData":[TD([[makeQuery(id+"F0.imprint","IMPRINT",EDGE,{"derivedFrom":subQ3}),1.0]])]});}
            var Q1050;
            {var subQ0=sQuery(id+"F0.wireOp",EDGE,"E3.19.0.41");var subQ1=sQuery(id+"F0.wireOp",EDGE,"E3.19.0.6");var subQ2=makeQuery(id+"F0.imprint","INTERSECT",VERTEX,{"derivedFrom":[subQ1,subQ0]});Q1050=makeQuery(id+"F0.imprint","IMPRINT",FACE,{"disambiguationData":[TD([[makeQuery(id+"F0.imprint","IMPRINT",EDGE,{"disambiguationData":[TD([[subQ2,1.0]])],"derivedFrom":subQ1}),-1.0]])]});}
            var Q1051;
            {var subQ0=sQuery(id+"F0.wireOp",EDGE,"E3.18.0.72");var subQ1=sQuery(id+"F0.wireOp",EDGE,"E3.18.0.10");var subQ2=makeQuery(id+"F0.imprint","INTERSECT",VERTEX,{"derivedFrom":[subQ1,subQ0]});Q1051=makeQuery(id+"F0.imprint","IMPRINT",FACE,{"disambiguationData":[TD([[makeQuery(id+"F0.imprint","IMPRINT",EDGE,{"disambiguationData":[TD([[subQ2,1.0]])],"derivedFrom":subQ1}),-1.0]])]});}
            var Q1052;
            {var subQ3=sQuery(id+"F0.wireOp",EDGE,"E3.20.0.53");Q1052=makeQuery(id+"F0.imprint","IMPRINT",FACE,{"disambiguationData":[TD([[makeQuery(id+"F0.imprint","IMPRINT",EDGE,{"derivedFrom":subQ3}),1.0]])]});}
            var Q1053;
            {var subQ7=sQuery(id+"F0.wireOp",EDGE,"E3.20.0.87");Q1053=makeQuery(id+"F0.imprint","IMPRINT",FACE,{"disambiguationData":[TD([[makeQuery(id+"F0.imprint","IMPRINT",EDGE,{"derivedFrom":subQ7}),-1.0]])]});}
            var Q1054;
            {var subQ0=sQuery(id+"F0.wireOp",EDGE,"E3.21.0.99");var subQ1=sQuery(id+"F0.wireOp",EDGE,"E3.21.0.49");var subQ2=makeQuery(id+"F0.imprint","INTERSECT",VERTEX,{"derivedFrom":[subQ1,subQ0]});Q1054=makeQuery(id+"F0.imprint","IMPRINT",FACE,{"disambiguationData":[TD([[makeQuery(id+"F0.imprint","IMPRINT",EDGE,{"disambiguationData":[TD([[subQ2,1.0]])],"derivedFrom":subQ1}),-1.0]])]});}
            var Q1055;
            {var subQ3=sQuery(id+"F0.wireOp",EDGE,"E3.21.0.83");Q1055=makeQuery(id+"F0.imprint","IMPRINT",FACE,{"disambiguationData":[TD([[makeQuery(id+"F0.imprint","IMPRINT",EDGE,{"derivedFrom":subQ3}),1.0]])]});}
            var Q1056;
            {var subQ3=sQuery(id+"F0.wireOp",EDGE,"E3.22.0.66");Q1056=makeQuery(id+"F0.imprint","IMPRINT",FACE,{"disambiguationData":[TD([[makeQuery(id+"F0.imprint","IMPRINT",EDGE,{"derivedFrom":subQ3}),-1.0]])]});}
            var Q1057;
            {var subQ3=sQuery(id+"F0.wireOp",EDGE,"E3.23.0.82");Q1057=makeQuery(id+"F0.imprint","IMPRINT",FACE,{"disambiguationData":[TD([[makeQuery(id+"F0.imprint","IMPRINT",EDGE,{"derivedFrom":subQ3}),1.0]])]});}
            var Q1058;
            {var subQ3=sQuery(id+"F0.wireOp",EDGE,"E3.18.0.7");Q1058=makeQuery(id+"F0.imprint","IMPRINT",FACE,{"disambiguationData":[TD([[makeQuery(id+"F0.imprint","IMPRINT",EDGE,{"derivedFrom":subQ3}),1.0]])]});}
            var Q1059;
            {var subQ0=sQuery(id+"F0.wireOp",EDGE,"E3.18.0.41");var subQ1=sQuery(id+"F0.wireOp",EDGE,"E3.18.0.13");var subQ2=makeQuery(id+"F0.imprint","INTERSECT",VERTEX,{"derivedFrom":[subQ1,subQ0]});Q1059=makeQuery(id+"F0.imprint","IMPRINT",FACE,{"disambiguationData":[TD([[makeQuery(id+"F0.imprint","IMPRINT",EDGE,{"disambiguationData":[TD([[subQ2,-1.0]])],"derivedFrom":subQ1}),-1.0]])]});}
            var Q1060;
            {var subQ3=sQuery(id+"F0.wireOp",EDGE,"E3.18.0.85");Q1060=makeQuery(id+"F0.imprint","IMPRINT",FACE,{"disambiguationData":[TD([[makeQuery(id+"F0.imprint","IMPRINT",EDGE,{"derivedFrom":subQ3}),1.0]])]});}
            var Q1061;
            {var subQ5=sQuery(id+"F0.wireOp",EDGE,"E3.17.0.93");Q1061=makeQuery(id+"F0.imprint","IMPRINT",FACE,{"disambiguationData":[TD([[makeQuery(id+"F0.imprint","IMPRINT",EDGE,{"derivedFrom":subQ5}),1.0]])]});}
            var Q1062;
            {var subQ3=sQuery(id+"F0.wireOp",EDGE,"E3.18.0.118");Q1062=makeQuery(id+"F0.imprint","IMPRINT",FACE,{"disambiguationData":[TD([[makeQuery(id+"F0.imprint","IMPRINT",EDGE,{"derivedFrom":subQ3}),1.0]])]});}
            var Q1063;
            {var subQ0=sQuery(id+"F0.wireOp",EDGE,"E3.20.0.71");var subQ1=sQuery(id+"F0.wireOp",EDGE,"E3.20.0.9");var subQ2=makeQuery(id+"F0.imprint","INTERSECT",VERTEX,{"derivedFrom":[subQ1,subQ0]});Q1063=makeQuery(id+"F0.imprint","IMPRINT",FACE,{"disambiguationData":[TD([[makeQuery(id+"F0.imprint","IMPRINT",EDGE,{"disambiguationData":[TD([[subQ2,1.0]])],"derivedFrom":subQ1}),-1.0]])]});}
            var Q1064;
            {var subQ0=sQuery(id+"F0.wireOp",EDGE,"E3.20.0.63");Q1064=makeQuery(id+"F0.imprint","IMPRINT",FACE,{"disambiguationData":[TD([[makeQuery(id+"F0.imprint","IMPRINT",EDGE,{"derivedFrom":subQ0}),-1.0]])]});}
            var Q1065;
            {var subQ0=sQuery(id+"F0.wireOp",EDGE,"E3.19.0.41");var subQ1=sQuery(id+"F0.wireOp",EDGE,"E3.19.0.13");var subQ2=makeQuery(id+"F0.imprint","INTERSECT",VERTEX,{"derivedFrom":[subQ1,subQ0]});Q1065=makeQuery(id+"F0.imprint","IMPRINT",FACE,{"disambiguationData":[TD([[makeQuery(id+"F0.imprint","IMPRINT",EDGE,{"disambiguationData":[TD([[subQ2,-1.0]])],"derivedFrom":subQ1}),-1.0]])]});}
            var Q1066;
            {var subQ7=sQuery(id+"F0.wireOp",EDGE,"E3.20.0.54");Q1066=makeQuery(id+"F0.imprint","IMPRINT",FACE,{"disambiguationData":[TD([[makeQuery(id+"F0.imprint","IMPRINT",EDGE,{"derivedFrom":subQ7}),-1.0]])]});}
            var Q1067;
            {var subQ3=sQuery(id+"F0.wireOp",EDGE,"E3.19.0.118");Q1067=makeQuery(id+"F0.imprint","IMPRINT",FACE,{"disambiguationData":[TD([[makeQuery(id+"F0.imprint","IMPRINT",EDGE,{"derivedFrom":subQ3}),1.0]])]});}
            var Q1068;
            {var subQ0=sQuery(id+"F0.wireOp",EDGE,"E3.19.0.19");Q1068=makeQuery(id+"F0.imprint","IMPRINT",FACE,{"disambiguationData":[TD([[makeQuery(id+"F0.imprint","IMPRINT",EDGE,{"derivedFrom":subQ0}),-1.0]])]});}
            var Q1069;
            {var subQ3=sQuery(id+"F0.wireOp",EDGE,"E3.19.0.7");Q1069=makeQuery(id+"F0.imprint","IMPRINT",FACE,{"disambiguationData":[TD([[makeQuery(id+"F0.imprint","IMPRINT",EDGE,{"derivedFrom":subQ3}),1.0]])]});}
            var Q1070;
            {var subQ0=sQuery(id+"F0.wireOp",EDGE,"E3.21.0.89");Q1070=makeQuery(id+"F0.imprint","IMPRINT",FACE,{"disambiguationData":[TD([[makeQuery(id+"F0.imprint","IMPRINT",EDGE,{"derivedFrom":subQ0}),-1.0]])]});}
            var Q1071;
            {var subQ0=sQuery(id+"F0.wireOp",EDGE,"E3.23.0.8");var subQ1=sQuery(id+"F0.wireOp",EDGE,"E3.23.0.6");var subQ2=makeQuery(id+"F0.imprint","INTERSECT",VERTEX,{"derivedFrom":[subQ1,subQ0]});Q1071=makeQuery(id+"F0.imprint","IMPRINT",FACE,{"disambiguationData":[TD([[makeQuery(id+"F0.imprint","IMPRINT",EDGE,{"disambiguationData":[TD([[subQ2,-1.0]])],"derivedFrom":subQ1}),-1.0]])]});}
            var Q1072;
            {var subQ0=sQuery(id+"F0.wireOp",EDGE,"E3.22.0.100");var subQ1=sQuery(id+"F0.wireOp",EDGE,"E3.22.0.52");var subQ2=makeQuery(id+"F0.imprint","INTERSECT",VERTEX,{"derivedFrom":[subQ1,subQ0]});Q1072=makeQuery(id+"F0.imprint","IMPRINT",FACE,{"disambiguationData":[TD([[makeQuery(id+"F0.imprint","IMPRINT",EDGE,{"disambiguationData":[TD([[subQ2,1.0]])],"derivedFrom":subQ1}),-1.0]])]});}
            var Q1073;
            {var subQ5=sQuery(id+"F0.wireOp",EDGE,"E3.23.0.22");Q1073=makeQuery(id+"F0.imprint","IMPRINT",FACE,{"disambiguationData":[TD([[makeQuery(id+"F0.imprint","IMPRINT",EDGE,{"derivedFrom":subQ5}),-1.0]])]});}
            var Q1074;
            {var subQ7=sQuery(id+"F0.wireOp",EDGE,"E3.23.0.83");Q1074=makeQuery(id+"F0.imprint","IMPRINT",FACE,{"disambiguationData":[TD([[makeQuery(id+"F0.imprint","IMPRINT",EDGE,{"derivedFrom":subQ7}),-1.0]])]});}
            var Q1075;
            {var subQ0=sQuery(id+"F0.wireOp",EDGE,"E3.22.0.89");Q1075=makeQuery(id+"F0.imprint","IMPRINT",FACE,{"disambiguationData":[TD([[makeQuery(id+"F0.imprint","IMPRINT",EDGE,{"derivedFrom":subQ0}),-1.0]])]});}
            var Q1076;
            {var subQ0=sQuery(id+"F0.wireOp",EDGE,"E3.24.0.8");var subQ1=sQuery(id+"F0.wireOp",EDGE,"E3.24.0.6");var subQ2=makeQuery(id+"F0.imprint","INTERSECT",VERTEX,{"derivedFrom":[subQ1,subQ0]});Q1076=makeQuery(id+"F0.imprint","IMPRINT",FACE,{"disambiguationData":[TD([[makeQuery(id+"F0.imprint","IMPRINT",EDGE,{"disambiguationData":[TD([[subQ2,-1.0]])],"derivedFrom":subQ1}),-1.0]])]});}
            var Q1077;
            {var subQ0=sQuery(id+"F0.wireOp",EDGE,"E3.24.0.97");var subQ1=sQuery(id+"F0.wireOp",EDGE,"E3.24.0.40");var subQ2=makeQuery(id+"F0.imprint","INTERSECT",VERTEX,{"derivedFrom":[subQ1,subQ0]});Q1077=makeQuery(id+"F0.imprint","IMPRINT",FACE,{"disambiguationData":[TD([[makeQuery(id+"F0.imprint","IMPRINT",EDGE,{"disambiguationData":[TD([[subQ2,1.0]])],"derivedFrom":subQ1}),-1.0]])]});}
            var Q1078;
            {var subQ0=sQuery(id+"F0.wireOp",EDGE,"E3.17.0.68");var subQ1=sQuery(id+"F0.wireOp",EDGE,"E3.17.0.11");var subQ2=makeQuery(id+"F0.imprint","INTERSECT",VERTEX,{"derivedFrom":[subQ1,subQ0]});Q1078=makeQuery(id+"F0.imprint","IMPRINT",FACE,{"disambiguationData":[TD([[makeQuery(id+"F0.imprint","IMPRINT",EDGE,{"disambiguationData":[TD([[subQ2,1.0]])],"derivedFrom":subQ1}),-1.0]])]});}
            var Q1079;
            {var subQ0=sQuery(id+"F0.wireOp",EDGE,"E3.19.0.20");Q1079=makeQuery(id+"F0.imprint","IMPRINT",FACE,{"disambiguationData":[TD([[makeQuery(id+"F0.imprint","IMPRINT",EDGE,{"derivedFrom":subQ0}),-1.0]])]});}
            var Q1080;
            {var subQ0=sQuery(id+"F0.wireOp",EDGE,"E3.19.0.96");var subQ1=sQuery(id+"F0.wireOp",EDGE,"E3.19.0.39");var subQ2=makeQuery(id+"F0.imprint","INTERSECT",VERTEX,{"derivedFrom":[subQ1,subQ0]});Q1080=makeQuery(id+"F0.imprint","IMPRINT",FACE,{"disambiguationData":[TD([[makeQuery(id+"F0.imprint","IMPRINT",EDGE,{"disambiguationData":[TD([[subQ2,1.0]])],"derivedFrom":subQ1}),-1.0]])]});}
            var Q1081;
            {var subQ0=sQuery(id+"F0.wireOp",EDGE,"E3.18.0.97");var subQ1=sQuery(id+"F0.wireOp",EDGE,"E3.18.0.40");var subQ2=makeQuery(id+"F0.imprint","INTERSECT",VERTEX,{"derivedFrom":[subQ1,subQ0]});Q1081=makeQuery(id+"F0.imprint","IMPRINT",FACE,{"disambiguationData":[TD([[makeQuery(id+"F0.imprint","IMPRINT",EDGE,{"disambiguationData":[TD([[subQ2,1.0]])],"derivedFrom":subQ1}),-1.0]])]});}
            var Q1082;
            {var subQ0=sQuery(id+"F0.wireOp",EDGE,"E3.20.0.37");var subQ5=sQuery(id+"F0.wireOp",EDGE,"E3.20.0.9");var subQ7=makeQuery(id+"F0.imprint","INTERSECT",VERTEX,{"derivedFrom":[subQ5,subQ0]});Q1082=makeQuery(id+"F0.imprint","IMPRINT",FACE,{"disambiguationData":[TD([[makeQuery(id+"F0.imprint","IMPRINT",EDGE,{"disambiguationData":[TD([[subQ7,1.0]])],"derivedFrom":subQ5}),1.0]])]});}
            var Q1083;
            {var subQ3=sQuery(id+"F0.wireOp",EDGE,"E3.19.0.31");Q1083=makeQuery(id+"F0.imprint","IMPRINT",FACE,{"disambiguationData":[TD([[makeQuery(id+"F0.imprint","IMPRINT",EDGE,{"derivedFrom":subQ3}),-1.0]])]});}
            var Q1084;
            {var subQ3=sQuery(id+"F0.wireOp",EDGE,"E3.21.0.84");Q1084=makeQuery(id+"F0.imprint","IMPRINT",FACE,{"disambiguationData":[TD([[makeQuery(id+"F0.imprint","IMPRINT",EDGE,{"derivedFrom":subQ3}),1.0]])]});}
            var Q1085;
            {var subQ0=sQuery(id+"F0.wireOp",EDGE,"E3.20.0.96");var subQ1=sQuery(id+"F0.wireOp",EDGE,"E3.20.0.39");var subQ2=makeQuery(id+"F0.imprint","INTERSECT",VERTEX,{"derivedFrom":[subQ1,subQ0]});Q1085=makeQuery(id+"F0.imprint","IMPRINT",FACE,{"disambiguationData":[TD([[makeQuery(id+"F0.imprint","IMPRINT",EDGE,{"disambiguationData":[TD([[subQ2,1.0]])],"derivedFrom":subQ1}),-1.0]])]});}
            var Q1086;
            {var subQ0=sQuery(id+"F0.wireOp",EDGE,"E3.19.0.91");var subQ1=sQuery(id+"F0.wireOp",EDGE,"E3.19.0.49");var subQ2=makeQuery(id+"F0.imprint","INTERSECT",VERTEX,{"derivedFrom":[subQ1,subQ0]});Q1086=makeQuery(id+"F0.imprint","IMPRINT",FACE,{"disambiguationData":[TD([[makeQuery(id+"F0.imprint","IMPRINT",EDGE,{"disambiguationData":[TD([[subQ2,-1.0]])],"derivedFrom":subQ1}),-1.0]])]});}
            var Q1087;
            {var subQ0=sQuery(id+"F0.wireOp",EDGE,"E3.21.0.57");Q1087=makeQuery(id+"F0.imprint","IMPRINT",FACE,{"disambiguationData":[TD([[makeQuery(id+"F0.imprint","IMPRINT",EDGE,{"derivedFrom":subQ0}),-1.0]])]});}
            var Q1088;
            {var subQ5=sQuery(id+"F0.wireOp",EDGE,"E3.20.0.57");Q1088=makeQuery(id+"F0.imprint","IMPRINT",FACE,{"disambiguationData":[TD([[makeQuery(id+"F0.imprint","IMPRINT",EDGE,{"derivedFrom":subQ5}),1.0]])]});}
            var Q1089;
            {var subQ3=sQuery(id+"F0.wireOp",EDGE,"E3.21.0.54");Q1089=makeQuery(id+"F0.imprint","IMPRINT",FACE,{"disambiguationData":[TD([[makeQuery(id+"F0.imprint","IMPRINT",EDGE,{"derivedFrom":subQ3}),1.0]])]});}
            var Q1090;
            {var subQ3=sQuery(id+"F0.wireOp",EDGE,"E3.22.0.84");Q1090=makeQuery(id+"F0.imprint","IMPRINT",FACE,{"disambiguationData":[TD([[makeQuery(id+"F0.imprint","IMPRINT",EDGE,{"derivedFrom":subQ3}),1.0]])]});}
            var Q1091;
            {var subQ0=sQuery(id+"F0.wireOp",EDGE,"E3.22.0.41");var subQ1=sQuery(id+"F0.wireOp",EDGE,"E3.22.0.6");var subQ2=makeQuery(id+"F0.imprint","INTERSECT",VERTEX,{"derivedFrom":[subQ1,subQ0]});Q1091=makeQuery(id+"F0.imprint","IMPRINT",FACE,{"disambiguationData":[TD([[makeQuery(id+"F0.imprint","IMPRINT",EDGE,{"disambiguationData":[TD([[subQ2,1.0]])],"derivedFrom":subQ1}),-1.0]])]});}
            var Q1092;
            {var subQ3=sQuery(id+"F0.wireOp",EDGE,"E3.23.0.53");Q1092=makeQuery(id+"F0.imprint","IMPRINT",FACE,{"disambiguationData":[TD([[makeQuery(id+"F0.imprint","IMPRINT",EDGE,{"derivedFrom":subQ3}),1.0]])]});}
            var Q1093;
            {var subQ3=sQuery(id+"F0.wireOp",EDGE,"E3.24.0.66");Q1093=makeQuery(id+"F0.imprint","IMPRINT",FACE,{"disambiguationData":[TD([[makeQuery(id+"F0.imprint","IMPRINT",EDGE,{"derivedFrom":subQ3}),-1.0]])]});}
            var Q1094;
            {var subQ0=sQuery(id+"F0.wireOp",EDGE,"E3.17.0.8");var subQ1=sQuery(id+"F0.wireOp",EDGE,"E3.17.0.6");var subQ2=makeQuery(id+"F0.imprint","INTERSECT",VERTEX,{"derivedFrom":[subQ1,subQ0]});Q1094=makeQuery(id+"F0.imprint","IMPRINT",FACE,{"disambiguationData":[TD([[makeQuery(id+"F0.imprint","IMPRINT",EDGE,{"disambiguationData":[TD([[subQ2,-1.0]])],"derivedFrom":subQ1}),-1.0]])]});}
            var Q1095;
            {var subQ5=sQuery(id+"F0.wireOp",EDGE,"E3.18.0.82");Q1095=makeQuery(id+"F0.imprint","IMPRINT",FACE,{"disambiguationData":[TD([[makeQuery(id+"F0.imprint","IMPRINT",EDGE,{"derivedFrom":subQ5}),-1.0]])]});}
            var Q1096;
            {var subQ7=sQuery(id+"F0.wireOp",EDGE,"E3.17.0.83");Q1096=makeQuery(id+"F0.imprint","IMPRINT",FACE,{"disambiguationData":[TD([[makeQuery(id+"F0.imprint","IMPRINT",EDGE,{"derivedFrom":subQ7}),-1.0]])]});}
            var Q1097;
            {var subQ0=sQuery(id+"F0.wireOp",EDGE,"E3.17.0.39");var subQ1=sQuery(id+"F0.wireOp",EDGE,"E3.17.0.17");var subQ2=makeQuery(id+"F0.imprint","INTERSECT",VERTEX,{"derivedFrom":[subQ1,subQ0]});Q1097=makeQuery(id+"F0.imprint","IMPRINT",FACE,{"disambiguationData":[TD([[makeQuery(id+"F0.imprint","IMPRINT",EDGE,{"disambiguationData":[TD([[subQ2,-1.0]])],"derivedFrom":subQ1}),-1.0]])]});}
            var Q1098;
            {var subQ0=sQuery(id+"F0.wireOp",EDGE,"E3.17.0.97");var subQ1=sQuery(id+"F0.wireOp",EDGE,"E3.17.0.40");var subQ2=makeQuery(id+"F0.imprint","INTERSECT",VERTEX,{"derivedFrom":[subQ1,subQ0]});Q1098=makeQuery(id+"F0.imprint","IMPRINT",FACE,{"disambiguationData":[TD([[makeQuery(id+"F0.imprint","IMPRINT",EDGE,{"disambiguationData":[TD([[subQ2,1.0]])],"derivedFrom":subQ1}),-1.0]])]});}
            var Q1099;
            {var subQ0=sQuery(id+"F0.wireOp",EDGE,"E3.18.0.68");var subQ1=sQuery(id+"F0.wireOp",EDGE,"E3.18.0.8");var subQ2=makeQuery(id+"F0.imprint","INTERSECT",VERTEX,{"derivedFrom":[subQ1,subQ0]});Q1099=makeQuery(id+"F0.imprint","IMPRINT",FACE,{"disambiguationData":[TD([[makeQuery(id+"F0.imprint","IMPRINT",EDGE,{"disambiguationData":[TD([[subQ2,1.0]])],"derivedFrom":subQ1}),-1.0]])]});}
            var Q1100;
            {var subQ0=sQuery(id+"F0.wireOp",EDGE,"E3.17.0.35");var subQ1=sQuery(id+"F0.wireOp",EDGE,"E3.17.0.32");var subQ2=makeQuery(id+"F0.imprint","INTERSECT",VERTEX,{"derivedFrom":[subQ1,subQ0]});Q1100=makeQuery(id+"F0.imprint","IMPRINT",FACE,{"disambiguationData":[TD([[makeQuery(id+"F0.imprint","IMPRINT",EDGE,{"disambiguationData":[TD([[subQ2,1.0]])],"derivedFrom":subQ1}),1.0]])]});}
            var Q1101;
            {var subQ0=sQuery(id+"F0.wireOp",EDGE,"E3.17.0.75");var subQ1=sQuery(id+"F0.wireOp",EDGE,"E3.17.0.52");var subQ2=makeQuery(id+"F0.imprint","INTERSECT",VERTEX,{"derivedFrom":[subQ1,subQ0]});Q1101=makeQuery(id+"F0.imprint","IMPRINT",FACE,{"disambiguationData":[TD([[makeQuery(id+"F0.imprint","IMPRINT",EDGE,{"disambiguationData":[TD([[subQ2,-1.0]])],"derivedFrom":subQ1}),-1.0]])]});}
            var Q1102;
            {var subQ0=sQuery(id+"F0.wireOp",EDGE,"E3.22.0.71");var subQ1=sQuery(id+"F0.wireOp",EDGE,"E3.22.0.9");var subQ2=makeQuery(id+"F0.imprint","INTERSECT",VERTEX,{"derivedFrom":[subQ1,subQ0]});Q1102=makeQuery(id+"F0.imprint","IMPRINT",FACE,{"disambiguationData":[TD([[makeQuery(id+"F0.imprint","IMPRINT",EDGE,{"disambiguationData":[TD([[subQ2,1.0]])],"derivedFrom":subQ1}),-1.0]])]});}
            var Q1103;
            {var subQ0=sQuery(id+"F0.wireOp",EDGE,"E3.21.0.19");Q1103=makeQuery(id+"F0.imprint","IMPRINT",FACE,{"disambiguationData":[TD([[makeQuery(id+"F0.imprint","IMPRINT",EDGE,{"derivedFrom":subQ0}),-1.0]])]});}
            var Q1104;
            {var subQ3=sQuery(id+"F0.wireOp",EDGE,"E3.21.0.7");Q1104=makeQuery(id+"F0.imprint","IMPRINT",FACE,{"disambiguationData":[TD([[makeQuery(id+"F0.imprint","IMPRINT",EDGE,{"derivedFrom":subQ3}),1.0]])]});}
            var Q1105;
            {var subQ0=sQuery(id+"F0.wireOp",EDGE,"E3.21.0.41");var subQ1=sQuery(id+"F0.wireOp",EDGE,"E3.21.0.13");var subQ2=makeQuery(id+"F0.imprint","INTERSECT",VERTEX,{"derivedFrom":[subQ1,subQ0]});Q1105=makeQuery(id+"F0.imprint","IMPRINT",FACE,{"disambiguationData":[TD([[makeQuery(id+"F0.imprint","IMPRINT",EDGE,{"disambiguationData":[TD([[subQ2,-1.0]])],"derivedFrom":subQ1}),-1.0]])]});}
            var Q1106;
            {var subQ0=sQuery(id+"F0.wireOp",EDGE,"E3.23.0.63");Q1106=makeQuery(id+"F0.imprint","IMPRINT",FACE,{"disambiguationData":[TD([[makeQuery(id+"F0.imprint","IMPRINT",EDGE,{"derivedFrom":subQ0}),-1.0]])]});}
            var Q1107;
            {var subQ0=sQuery(id+"F0.wireOp",EDGE,"E3.22.0.42");var subQ1=sQuery(id+"F0.wireOp",EDGE,"E3.22.0.16");var subQ2=makeQuery(id+"F0.imprint","INTERSECT",VERTEX,{"derivedFrom":[subQ1,subQ0]});Q1107=makeQuery(id+"F0.imprint","IMPRINT",FACE,{"disambiguationData":[TD([[makeQuery(id+"F0.imprint","IMPRINT",EDGE,{"disambiguationData":[TD([[subQ2,-1.0]])],"derivedFrom":subQ1}),-1.0]])]});}
            var Q1108;
            {var subQ0=sQuery(id+"F0.wireOp",EDGE,"E3.23.0.71");var subQ1=sQuery(id+"F0.wireOp",EDGE,"E3.23.0.9");var subQ2=makeQuery(id+"F0.imprint","INTERSECT",VERTEX,{"derivedFrom":[subQ1,subQ0]});Q1108=makeQuery(id+"F0.imprint","IMPRINT",FACE,{"disambiguationData":[TD([[makeQuery(id+"F0.imprint","IMPRINT",EDGE,{"disambiguationData":[TD([[subQ2,1.0]])],"derivedFrom":subQ1}),-1.0]])]});}
            var Q1109;
            {var subQ7=sQuery(id+"F0.wireOp",EDGE,"E3.23.0.54");Q1109=makeQuery(id+"F0.imprint","IMPRINT",FACE,{"disambiguationData":[TD([[makeQuery(id+"F0.imprint","IMPRINT",EDGE,{"derivedFrom":subQ7}),-1.0]])]});}
            var Q1110;
            {var subQ0=sQuery(id+"F0.wireOp",EDGE,"E3.24.0.89");Q1110=makeQuery(id+"F0.imprint","IMPRINT",FACE,{"disambiguationData":[TD([[makeQuery(id+"F0.imprint","IMPRINT",EDGE,{"derivedFrom":subQ0}),-1.0]])]});}
            var Q1111;
            {var subQ3=sQuery(id+"F0.wireOp",EDGE,"E3.18.0.55");Q1111=makeQuery(id+"F0.imprint","IMPRINT",FACE,{"disambiguationData":[TD([[makeQuery(id+"F0.imprint","IMPRINT",EDGE,{"derivedFrom":subQ3}),1.0]])]});}
            var Q1112;
            {var subQ3=sQuery(id+"F0.wireOp",EDGE,"E3.17.0.56");Q1112=makeQuery(id+"F0.imprint","IMPRINT",FACE,{"disambiguationData":[TD([[makeQuery(id+"F0.imprint","IMPRINT",EDGE,{"derivedFrom":subQ3}),-1.0]])]});}
            var Q1113;
            {var subQ0=sQuery(id+"F0.wireOp",EDGE,"E3.19.0.68");var subQ1=sQuery(id+"F0.wireOp",EDGE,"E3.19.0.11");var subQ2=makeQuery(id+"F0.imprint","INTERSECT",VERTEX,{"derivedFrom":[subQ1,subQ0]});Q1113=makeQuery(id+"F0.imprint","IMPRINT",FACE,{"disambiguationData":[TD([[makeQuery(id+"F0.imprint","IMPRINT",EDGE,{"disambiguationData":[TD([[subQ2,1.0]])],"derivedFrom":subQ1}),-1.0]])]});}
            var Q1114;
            {var subQ3=sQuery(id+"F0.wireOp",EDGE,"E3.19.0.85");Q1114=makeQuery(id+"F0.imprint","IMPRINT",FACE,{"disambiguationData":[TD([[makeQuery(id+"F0.imprint","IMPRINT",EDGE,{"derivedFrom":subQ3}),1.0]])]});}
            var Q1115;
            {var subQ0=sQuery(id+"F0.wireOp",EDGE,"E3.17.0.116");Q1115=makeQuery(id+"F0.imprint","IMPRINT",FACE,{"disambiguationData":[TD([[makeQuery(id+"F0.imprint","IMPRINT",EDGE,{"derivedFrom":subQ0}),-1.0]])]});}
            var Q1116;
            {var subQ0=sQuery(id+"F0.wireOp",EDGE,"E3.17.0.99");var subQ1=sQuery(id+"F0.wireOp",EDGE,"E3.17.0.49");var subQ2=makeQuery(id+"F0.imprint","INTERSECT",VERTEX,{"derivedFrom":[subQ1,subQ0]});Q1116=makeQuery(id+"F0.imprint","IMPRINT",FACE,{"disambiguationData":[TD([[makeQuery(id+"F0.imprint","IMPRINT",EDGE,{"disambiguationData":[TD([[subQ2,1.0]])],"derivedFrom":subQ1}),-1.0]])]});}
            var Q1117;
            {var subQ0=sQuery(id+"F0.wireOp",EDGE,"E3.20.0.41");var subQ1=sQuery(id+"F0.wireOp",EDGE,"E3.20.0.13");var subQ2=makeQuery(id+"F0.imprint","INTERSECT",VERTEX,{"derivedFrom":[subQ1,subQ0]});Q1117=makeQuery(id+"F0.imprint","IMPRINT",FACE,{"disambiguationData":[TD([[makeQuery(id+"F0.imprint","IMPRINT",EDGE,{"disambiguationData":[TD([[subQ2,-1.0]])],"derivedFrom":subQ1}),-1.0]])]});}
            var Q1118;
            {var subQ0=sQuery(id+"F0.wireOp",EDGE,"E3.21.0.42");var subQ1=sQuery(id+"F0.wireOp",EDGE,"E3.21.0.16");var subQ2=makeQuery(id+"F0.imprint","INTERSECT",VERTEX,{"derivedFrom":[subQ1,subQ0]});Q1118=makeQuery(id+"F0.imprint","IMPRINT",FACE,{"disambiguationData":[TD([[makeQuery(id+"F0.imprint","IMPRINT",EDGE,{"disambiguationData":[TD([[subQ2,-1.0]])],"derivedFrom":subQ1}),-1.0]])]});}
            var Q1119;
            {var subQ3=sQuery(id+"F0.wireOp",EDGE,"E3.20.0.85");Q1119=makeQuery(id+"F0.imprint","IMPRINT",FACE,{"disambiguationData":[TD([[makeQuery(id+"F0.imprint","IMPRINT",EDGE,{"derivedFrom":subQ3}),1.0]])]});}
            var Q1120;
            {var subQ0=sQuery(id+"F0.wireOp",EDGE,"E3.20.0.97");var subQ1=sQuery(id+"F0.wireOp",EDGE,"E3.20.0.44");var subQ2=makeQuery(id+"F0.imprint","INTERSECT",VERTEX,{"derivedFrom":[subQ1,subQ0]});Q1120=makeQuery(id+"F0.imprint","IMPRINT",FACE,{"disambiguationData":[TD([[makeQuery(id+"F0.imprint","IMPRINT",EDGE,{"disambiguationData":[TD([[subQ2,1.0]])],"derivedFrom":subQ1}),-1.0]])]});}
            var Q1121;
            {var subQ0=sQuery(id+"F0.wireOp",EDGE,"E3.20.0.68");var subQ1=sQuery(id+"F0.wireOp",EDGE,"E3.20.0.11");var subQ2=makeQuery(id+"F0.imprint","INTERSECT",VERTEX,{"derivedFrom":[subQ1,subQ0]});Q1121=makeQuery(id+"F0.imprint","IMPRINT",FACE,{"disambiguationData":[TD([[makeQuery(id+"F0.imprint","IMPRINT",EDGE,{"disambiguationData":[TD([[subQ2,1.0]])],"derivedFrom":subQ1}),-1.0]])]});}
            var Q1122;
            {var subQ3=sQuery(id+"F0.wireOp",EDGE,"E3.22.0.56");Q1122=makeQuery(id+"F0.imprint","IMPRINT",FACE,{"disambiguationData":[TD([[makeQuery(id+"F0.imprint","IMPRINT",EDGE,{"derivedFrom":subQ3}),-1.0]])]});}
            var Q1123;
            {var subQ3=sQuery(id+"F0.wireOp",EDGE,"E3.22.0.83");Q1123=makeQuery(id+"F0.imprint","IMPRINT",FACE,{"disambiguationData":[TD([[makeQuery(id+"F0.imprint","IMPRINT",EDGE,{"derivedFrom":subQ3}),1.0]])]});}
            var Q1124;
            {var subQ0=sQuery(id+"F0.wireOp",EDGE,"E3.23.0.94");var subQ1=sQuery(id+"F0.wireOp",EDGE,"E3.23.0.42");var subQ2=makeQuery(id+"F0.imprint","INTERSECT",VERTEX,{"derivedFrom":[subQ1,subQ0]});Q1124=makeQuery(id+"F0.imprint","IMPRINT",FACE,{"disambiguationData":[TD([[makeQuery(id+"F0.imprint","IMPRINT",EDGE,{"disambiguationData":[TD([[subQ2,1.0]])],"derivedFrom":subQ1}),-1.0]])]});}
            var Q1125;
            {var subQ3=sQuery(id+"F0.wireOp",EDGE,"E3.24.0.82");Q1125=makeQuery(id+"F0.imprint","IMPRINT",FACE,{"disambiguationData":[TD([[makeQuery(id+"F0.imprint","IMPRINT",EDGE,{"derivedFrom":subQ3}),1.0]])]});}
            var Q1126;
            {var subQ5=sQuery(id+"F0.wireOp",EDGE,"E3.24.0.93");Q1126=makeQuery(id+"F0.imprint","IMPRINT",FACE,{"disambiguationData":[TD([[makeQuery(id+"F0.imprint","IMPRINT",EDGE,{"derivedFrom":subQ5}),1.0]])]});}
            var Q1127;
            {var subQ0=sQuery(id+"F0.wireOp",EDGE,"E3.17.0.91");var subQ1=sQuery(id+"F0.wireOp",EDGE,"E3.17.0.49");var subQ2=makeQuery(id+"F0.imprint","INTERSECT",VERTEX,{"derivedFrom":[subQ1,subQ0]});Q1127=makeQuery(id+"F0.imprint","IMPRINT",FACE,{"disambiguationData":[TD([[makeQuery(id+"F0.imprint","IMPRINT",EDGE,{"disambiguationData":[TD([[subQ2,-1.0]])],"derivedFrom":subQ1}),-1.0]])]});}
            var Q1128;
            {var subQ5=sQuery(id+"F0.wireOp",EDGE,"E3.17.0.82");Q1128=makeQuery(id+"F0.imprint","IMPRINT",FACE,{"disambiguationData":[TD([[makeQuery(id+"F0.imprint","IMPRINT",EDGE,{"derivedFrom":subQ5}),-1.0]])]});}
            var Q1129;
            {var subQ0=sQuery(id+"F0.wireOp",EDGE,"E3.19.0.37");var subQ5=sQuery(id+"F0.wireOp",EDGE,"E3.19.0.9");var subQ7=makeQuery(id+"F0.imprint","INTERSECT",VERTEX,{"derivedFrom":[subQ5,subQ0]});Q1129=makeQuery(id+"F0.imprint","IMPRINT",FACE,{"disambiguationData":[TD([[makeQuery(id+"F0.imprint","IMPRINT",EDGE,{"disambiguationData":[TD([[subQ7,1.0]])],"derivedFrom":subQ5}),1.0]])]});}
            var Q1130;
            {var subQ5=sQuery(id+"F0.wireOp",EDGE,"E3.18.0.57");Q1130=makeQuery(id+"F0.imprint","IMPRINT",FACE,{"disambiguationData":[TD([[makeQuery(id+"F0.imprint","IMPRINT",EDGE,{"derivedFrom":subQ5}),1.0]])]});}
            var Q1131;
            {var subQ3=sQuery(id+"F0.wireOp",EDGE,"E3.19.0.81");Q1131=makeQuery(id+"F0.imprint","IMPRINT",FACE,{"disambiguationData":[TD([[makeQuery(id+"F0.imprint","IMPRINT",EDGE,{"derivedFrom":subQ3}),1.0]])]});}
            var Q1132;
            {var subQ3=sQuery(id+"F0.wireOp",EDGE,"E3.20.0.84");Q1132=makeQuery(id+"F0.imprint","IMPRINT",FACE,{"disambiguationData":[TD([[makeQuery(id+"F0.imprint","IMPRINT",EDGE,{"derivedFrom":subQ3}),1.0]])]});}
            var Q1133;
            {var subQ0=sQuery(id+"F0.wireOp",EDGE,"E3.20.0.41");var subQ1=sQuery(id+"F0.wireOp",EDGE,"E3.20.0.6");var subQ2=makeQuery(id+"F0.imprint","INTERSECT",VERTEX,{"derivedFrom":[subQ1,subQ0]});Q1133=makeQuery(id+"F0.imprint","IMPRINT",FACE,{"disambiguationData":[TD([[makeQuery(id+"F0.imprint","IMPRINT",EDGE,{"disambiguationData":[TD([[subQ2,1.0]])],"derivedFrom":subQ1}),-1.0]])]});}
            var Q1134;
            {var subQ0=sQuery(id+"F0.wireOp",EDGE,"E3.23.0.72");var subQ1=sQuery(id+"F0.wireOp",EDGE,"E3.23.0.10");var subQ2=makeQuery(id+"F0.imprint","INTERSECT",VERTEX,{"derivedFrom":[subQ1,subQ0]});Q1134=makeQuery(id+"F0.imprint","IMPRINT",FACE,{"disambiguationData":[TD([[makeQuery(id+"F0.imprint","IMPRINT",EDGE,{"disambiguationData":[TD([[subQ2,1.0]])],"derivedFrom":subQ1}),-1.0]])]});}
            var Q1135;
            {var subQ3=sQuery(id+"F0.wireOp",EDGE,"E3.24.0.84");Q1135=makeQuery(id+"F0.imprint","IMPRINT",FACE,{"disambiguationData":[TD([[makeQuery(id+"F0.imprint","IMPRINT",EDGE,{"derivedFrom":subQ3}),1.0]])]});}
            var Q1136;
            {var subQ0=sQuery(id+"F0.wireOp",EDGE,"E3.17.0.64");Q1136=makeQuery(id+"F0.imprint","IMPRINT",FACE,{"disambiguationData":[TD([[makeQuery(id+"F0.imprint","IMPRINT",EDGE,{"derivedFrom":subQ0}),-1.0]])]});}
            var Q1137;
            {var subQ3=sQuery(id+"F0.wireOp",EDGE,"E3.17.0.86");Q1137=makeQuery(id+"F0.imprint","IMPRINT",FACE,{"disambiguationData":[TD([[makeQuery(id+"F0.imprint","IMPRINT",EDGE,{"derivedFrom":subQ3}),1.0]])]});}
            var Q1138;
            {var subQ0=sQuery(id+"F0.wireOp",EDGE,"E3.19.0.68");var subQ1=sQuery(id+"F0.wireOp",EDGE,"E3.19.0.8");var subQ2=makeQuery(id+"F0.imprint","INTERSECT",VERTEX,{"derivedFrom":[subQ1,subQ0]});Q1138=makeQuery(id+"F0.imprint","IMPRINT",FACE,{"disambiguationData":[TD([[makeQuery(id+"F0.imprint","IMPRINT",EDGE,{"disambiguationData":[TD([[subQ2,1.0]])],"derivedFrom":subQ1}),-1.0]])]});}
            var Q1139;
            {var subQ5=sQuery(id+"F0.wireOp",EDGE,"E3.18.0.22");Q1139=makeQuery(id+"F0.imprint","IMPRINT",FACE,{"disambiguationData":[TD([[makeQuery(id+"F0.imprint","IMPRINT",EDGE,{"derivedFrom":subQ5}),-1.0]])]});}
            var Q1140;
            {var subQ3=sQuery(id+"F0.wireOp",EDGE,"E3.18.0.86");Q1140=makeQuery(id+"F0.imprint","IMPRINT",FACE,{"disambiguationData":[TD([[makeQuery(id+"F0.imprint","IMPRINT",EDGE,{"derivedFrom":subQ3}),1.0]])]});}
            var Q1141;
            {var subQ0=sQuery(id+"F0.wireOp",EDGE,"E3.18.0.75");var subQ1=sQuery(id+"F0.wireOp",EDGE,"E3.18.0.52");var subQ2=makeQuery(id+"F0.imprint","INTERSECT",VERTEX,{"derivedFrom":[subQ1,subQ0]});Q1141=makeQuery(id+"F0.imprint","IMPRINT",FACE,{"disambiguationData":[TD([[makeQuery(id+"F0.imprint","IMPRINT",EDGE,{"disambiguationData":[TD([[subQ2,-1.0]])],"derivedFrom":subQ1}),-1.0]])]});}
            var Q1142;
            {var subQ5=sQuery(id+"F0.wireOp",EDGE,"E3.20.0.82");Q1142=makeQuery(id+"F0.imprint","IMPRINT",FACE,{"disambiguationData":[TD([[makeQuery(id+"F0.imprint","IMPRINT",EDGE,{"derivedFrom":subQ5}),-1.0]])]});}
            var Q1143;
            {var subQ7=sQuery(id+"F0.wireOp",EDGE,"E3.19.0.83");Q1143=makeQuery(id+"F0.imprint","IMPRINT",FACE,{"disambiguationData":[TD([[makeQuery(id+"F0.imprint","IMPRINT",EDGE,{"derivedFrom":subQ7}),-1.0]])]});}
            var Q1144;
            {var subQ0=sQuery(id+"F0.wireOp",EDGE,"E3.19.0.97");var subQ1=sQuery(id+"F0.wireOp",EDGE,"E3.19.0.40");var subQ2=makeQuery(id+"F0.imprint","INTERSECT",VERTEX,{"derivedFrom":[subQ1,subQ0]});Q1144=makeQuery(id+"F0.imprint","IMPRINT",FACE,{"disambiguationData":[TD([[makeQuery(id+"F0.imprint","IMPRINT",EDGE,{"disambiguationData":[TD([[subQ2,1.0]])],"derivedFrom":subQ1}),-1.0]])]});}
            var Q1145;
            {var subQ0=sQuery(id+"F0.wireOp",EDGE,"E3.21.0.96");var subQ1=sQuery(id+"F0.wireOp",EDGE,"E3.21.0.39");var subQ2=makeQuery(id+"F0.imprint","INTERSECT",VERTEX,{"derivedFrom":[subQ1,subQ0]});Q1145=makeQuery(id+"F0.imprint","IMPRINT",FACE,{"disambiguationData":[TD([[makeQuery(id+"F0.imprint","IMPRINT",EDGE,{"disambiguationData":[TD([[subQ2,1.0]])],"derivedFrom":subQ1}),-1.0]])]});}
            var Q1146;
            {var subQ0=sQuery(id+"F0.wireOp",EDGE,"E3.20.0.91");var subQ1=sQuery(id+"F0.wireOp",EDGE,"E3.20.0.49");var subQ2=makeQuery(id+"F0.imprint","INTERSECT",VERTEX,{"derivedFrom":[subQ1,subQ0]});Q1146=makeQuery(id+"F0.imprint","IMPRINT",FACE,{"disambiguationData":[TD([[makeQuery(id+"F0.imprint","IMPRINT",EDGE,{"disambiguationData":[TD([[subQ2,-1.0]])],"derivedFrom":subQ1}),-1.0]])]});}
            var Q1147;
            {var subQ0=sQuery(id+"F0.wireOp",EDGE,"E3.20.0.68");var subQ1=sQuery(id+"F0.wireOp",EDGE,"E3.20.0.8");var subQ2=makeQuery(id+"F0.imprint","INTERSECT",VERTEX,{"derivedFrom":[subQ1,subQ0]});Q1147=makeQuery(id+"F0.imprint","IMPRINT",FACE,{"disambiguationData":[TD([[makeQuery(id+"F0.imprint","IMPRINT",EDGE,{"disambiguationData":[TD([[subQ2,1.0]])],"derivedFrom":subQ1}),-1.0]])]});}
            var Q1148;
            {var subQ0=sQuery(id+"F0.wireOp",EDGE,"E3.22.0.72");var subQ1=sQuery(id+"F0.wireOp",EDGE,"E3.22.0.10");var subQ2=makeQuery(id+"F0.imprint","INTERSECT",VERTEX,{"derivedFrom":[subQ1,subQ0]});Q1148=makeQuery(id+"F0.imprint","IMPRINT",FACE,{"disambiguationData":[TD([[makeQuery(id+"F0.imprint","IMPRINT",EDGE,{"disambiguationData":[TD([[subQ2,1.0]])],"derivedFrom":subQ1}),-1.0]])]});}
            var Q1149;
            {var subQ3=sQuery(id+"F0.wireOp",EDGE,"E3.22.0.54");Q1149=makeQuery(id+"F0.imprint","IMPRINT",FACE,{"disambiguationData":[TD([[makeQuery(id+"F0.imprint","IMPRINT",EDGE,{"derivedFrom":subQ3}),1.0]])]});}
            var Q1150;
            {var subQ3=sQuery(id+"F0.wireOp",EDGE,"E3.22.0.81");Q1150=makeQuery(id+"F0.imprint","IMPRINT",FACE,{"disambiguationData":[TD([[makeQuery(id+"F0.imprint","IMPRINT",EDGE,{"derivedFrom":subQ3}),1.0]])]});}
            var Q1151;
            {var subQ0=sQuery(id+"F0.wireOp",EDGE,"E3.22.0.96");var subQ1=sQuery(id+"F0.wireOp",EDGE,"E3.22.0.39");var subQ2=makeQuery(id+"F0.imprint","INTERSECT",VERTEX,{"derivedFrom":[subQ1,subQ0]});Q1151=makeQuery(id+"F0.imprint","IMPRINT",FACE,{"disambiguationData":[TD([[makeQuery(id+"F0.imprint","IMPRINT",EDGE,{"disambiguationData":[TD([[subQ2,1.0]])],"derivedFrom":subQ1}),-1.0]])]});}
            var Q1152;
            {var subQ5=sQuery(id+"F0.wireOp",EDGE,"E3.22.0.57");Q1152=makeQuery(id+"F0.imprint","IMPRINT",FACE,{"disambiguationData":[TD([[makeQuery(id+"F0.imprint","IMPRINT",EDGE,{"derivedFrom":subQ5}),1.0]])]});}
            var Q1153;
            {var subQ3=sQuery(id+"F0.wireOp",EDGE,"E3.23.0.84");Q1153=makeQuery(id+"F0.imprint","IMPRINT",FACE,{"disambiguationData":[TD([[makeQuery(id+"F0.imprint","IMPRINT",EDGE,{"derivedFrom":subQ3}),1.0]])]});}
            var Q1154;
            {var subQ0=sQuery(id+"F0.wireOp",EDGE,"E3.20.0.99");var subQ1=sQuery(id+"F0.wireOp",EDGE,"E3.20.0.49");var subQ2=makeQuery(id+"F0.imprint","INTERSECT",VERTEX,{"derivedFrom":[subQ1,subQ0]});Q1154=makeQuery(id+"F0.imprint","IMPRINT",FACE,{"disambiguationData":[TD([[makeQuery(id+"F0.imprint","IMPRINT",EDGE,{"disambiguationData":[TD([[subQ2,1.0]])],"derivedFrom":subQ1}),-1.0]])]});}
            var Q1155;
            {var subQ3=sQuery(id+"F0.wireOp",EDGE,"E3.19.0.53");Q1155=makeQuery(id+"F0.imprint","IMPRINT",FACE,{"disambiguationData":[TD([[makeQuery(id+"F0.imprint","IMPRINT",EDGE,{"derivedFrom":subQ3}),1.0]])]});}
            var Q1156;
            {var subQ7=sQuery(id+"F0.wireOp",EDGE,"E3.19.0.87");Q1156=makeQuery(id+"F0.imprint","IMPRINT",FACE,{"disambiguationData":[TD([[makeQuery(id+"F0.imprint","IMPRINT",EDGE,{"derivedFrom":subQ7}),-1.0]])]});}
            var Q1157;
            {var subQ3=sQuery(id+"F0.wireOp",EDGE,"E3.23.0.85");Q1157=makeQuery(id+"F0.imprint","IMPRINT",FACE,{"disambiguationData":[TD([[makeQuery(id+"F0.imprint","IMPRINT",EDGE,{"derivedFrom":subQ3}),1.0]])]});}
            var Q1158;
            {var subQ3=sQuery(id+"F0.wireOp",EDGE,"E3.18.0.84");Q1158=makeQuery(id+"F0.imprint","IMPRINT",FACE,{"disambiguationData":[TD([[makeQuery(id+"F0.imprint","IMPRINT",EDGE,{"derivedFrom":subQ3}),1.0]])]});}
            var Q1159;
            {var subQ0=sQuery(id+"F0.wireOp",EDGE,"E3.23.0.97");var subQ1=sQuery(id+"F0.wireOp",EDGE,"E3.23.0.44");var subQ2=makeQuery(id+"F0.imprint","INTERSECT",VERTEX,{"derivedFrom":[subQ1,subQ0]});Q1159=makeQuery(id+"F0.imprint","IMPRINT",FACE,{"disambiguationData":[TD([[makeQuery(id+"F0.imprint","IMPRINT",EDGE,{"disambiguationData":[TD([[subQ2,1.0]])],"derivedFrom":subQ1}),-1.0]])]});}
            var Q1160;
            {var subQ3=sQuery(id+"F0.wireOp",EDGE,"E3.20.0.55");Q1160=makeQuery(id+"F0.imprint","IMPRINT",FACE,{"disambiguationData":[TD([[makeQuery(id+"F0.imprint","IMPRINT",EDGE,{"derivedFrom":subQ3}),1.0]])]});}
            var Q1161;
            {var subQ0=sQuery(id+"F0.wireOp",EDGE,"E3.17.0.41");var subQ1=sQuery(id+"F0.wireOp",EDGE,"E3.17.0.6");var subQ2=makeQuery(id+"F0.imprint","INTERSECT",VERTEX,{"derivedFrom":[subQ1,subQ0]});Q1161=makeQuery(id+"F0.imprint","IMPRINT",FACE,{"disambiguationData":[TD([[makeQuery(id+"F0.imprint","IMPRINT",EDGE,{"disambiguationData":[TD([[subQ2,1.0]])],"derivedFrom":subQ1}),-1.0]])]});}
            var Q1162;
            {var subQ3=sQuery(id+"F0.wireOp",EDGE,"E3.17.0.84");Q1162=makeQuery(id+"F0.imprint","IMPRINT",FACE,{"disambiguationData":[TD([[makeQuery(id+"F0.imprint","IMPRINT",EDGE,{"derivedFrom":subQ3}),1.0]])]});}
            var Q1163;
            {var subQ3=sQuery(id+"F0.wireOp",EDGE,"E3.22.0.55");Q1163=makeQuery(id+"F0.imprint","IMPRINT",FACE,{"disambiguationData":[TD([[makeQuery(id+"F0.imprint","IMPRINT",EDGE,{"derivedFrom":subQ3}),1.0]])]});}
            var Q1164;
            {var subQ0=sQuery(id+"F0.wireOp",EDGE,"E3.19.0.99");var subQ1=sQuery(id+"F0.wireOp",EDGE,"E3.19.0.49");var subQ2=makeQuery(id+"F0.imprint","INTERSECT",VERTEX,{"derivedFrom":[subQ1,subQ0]});Q1164=makeQuery(id+"F0.imprint","IMPRINT",FACE,{"disambiguationData":[TD([[makeQuery(id+"F0.imprint","IMPRINT",EDGE,{"disambiguationData":[TD([[subQ2,1.0]])],"derivedFrom":subQ1}),-1.0]])]});}
            var Q1165;
            {var subQ3=sQuery(id+"F0.wireOp",EDGE,"E3.20.0.103");Q1165=makeQuery(id+"F0.imprint","IMPRINT",FACE,{"disambiguationData":[TD([[makeQuery(id+"F0.imprint","IMPRINT",EDGE,{"derivedFrom":subQ3}),1.0]])]});}
            var Q1166;
            {var subQ0=sQuery(id+"F0.wireOp",EDGE,"E3.22.0.97");var subQ1=sQuery(id+"F0.wireOp",EDGE,"E3.22.0.44");var subQ2=makeQuery(id+"F0.imprint","INTERSECT",VERTEX,{"derivedFrom":[subQ1,subQ0]});Q1166=makeQuery(id+"F0.imprint","IMPRINT",FACE,{"disambiguationData":[TD([[makeQuery(id+"F0.imprint","IMPRINT",EDGE,{"disambiguationData":[TD([[subQ2,1.0]])],"derivedFrom":subQ1}),-1.0]])]});}
            var Q1167;
            {var subQ3=sQuery(id+"F0.wireOp",EDGE,"E3.23.0.118");Q1167=makeQuery(id+"F0.imprint","IMPRINT",FACE,{"disambiguationData":[TD([[makeQuery(id+"F0.imprint","IMPRINT",EDGE,{"derivedFrom":subQ3}),1.0]])]});}
            var Q1168;
            {var subQ0=sQuery(id+"F0.wireOp",EDGE,"E3.17.0.63");Q1168=makeQuery(id+"F0.imprint","IMPRINT",FACE,{"disambiguationData":[TD([[makeQuery(id+"F0.imprint","IMPRINT",EDGE,{"derivedFrom":subQ0}),-1.0]])]});}
            var Q1169;
            {var subQ5=sQuery(id+"F0.wireOp",EDGE,"E3.18.0.56");Q1169=makeQuery(id+"F0.imprint","IMPRINT",FACE,{"disambiguationData":[TD([[makeQuery(id+"F0.imprint","IMPRINT",EDGE,{"derivedFrom":subQ5}),1.0]])]});}
            var Q1170;
            {var subQ0=sQuery(id+"F0.wireOp",EDGE,"E3.17.0.42");var subQ1=sQuery(id+"F0.wireOp",EDGE,"E3.17.0.16");var subQ2=makeQuery(id+"F0.imprint","INTERSECT",VERTEX,{"derivedFrom":[subQ1,subQ0]});Q1170=makeQuery(id+"F0.imprint","IMPRINT",FACE,{"disambiguationData":[TD([[makeQuery(id+"F0.imprint","IMPRINT",EDGE,{"disambiguationData":[TD([[subQ2,-1.0]])],"derivedFrom":subQ1}),-1.0]])]});}
            var Q1171;
            {var subQ5=sQuery(id+"F0.wireOp",EDGE,"E3.19.0.22");Q1171=makeQuery(id+"F0.imprint","IMPRINT",FACE,{"disambiguationData":[TD([[makeQuery(id+"F0.imprint","IMPRINT",EDGE,{"derivedFrom":subQ5}),-1.0]])]});}
            var Q1172;
            {var subQ0=sQuery(id+"F0.wireOp",EDGE,"E3.18.0.71");var subQ1=sQuery(id+"F0.wireOp",EDGE,"E3.18.0.9");var subQ2=makeQuery(id+"F0.imprint","INTERSECT",VERTEX,{"derivedFrom":[subQ1,subQ0]});Q1172=makeQuery(id+"F0.imprint","IMPRINT",FACE,{"disambiguationData":[TD([[makeQuery(id+"F0.imprint","IMPRINT",EDGE,{"disambiguationData":[TD([[subQ2,1.0]])],"derivedFrom":subQ1}),-1.0]])]});}
            var Q1173;
            {var subQ0=sQuery(id+"F0.wireOp",EDGE,"E3.18.0.100");var subQ1=sQuery(id+"F0.wireOp",EDGE,"E3.18.0.52");var subQ2=makeQuery(id+"F0.imprint","INTERSECT",VERTEX,{"derivedFrom":[subQ1,subQ0]});Q1173=makeQuery(id+"F0.imprint","IMPRINT",FACE,{"disambiguationData":[TD([[makeQuery(id+"F0.imprint","IMPRINT",EDGE,{"disambiguationData":[TD([[subQ2,1.0]])],"derivedFrom":subQ1}),-1.0]])]});}
            var Q1174;
            {var subQ5=sQuery(id+"F0.wireOp",EDGE,"E3.20.0.56");Q1174=makeQuery(id+"F0.imprint","IMPRINT",FACE,{"disambiguationData":[TD([[makeQuery(id+"F0.imprint","IMPRINT",EDGE,{"derivedFrom":subQ5}),1.0]])]});}
            var Q1175;
            {var subQ3=sQuery(id+"F0.wireOp",EDGE,"E3.21.0.86");Q1175=makeQuery(id+"F0.imprint","IMPRINT",FACE,{"disambiguationData":[TD([[makeQuery(id+"F0.imprint","IMPRINT",EDGE,{"derivedFrom":subQ3}),1.0]])]});}
            var Q1176;
            {var subQ0=sQuery(id+"F0.wireOp",EDGE,"E3.23.0.97");var subQ1=sQuery(id+"F0.wireOp",EDGE,"E3.23.0.40");var subQ2=makeQuery(id+"F0.imprint","INTERSECT",VERTEX,{"derivedFrom":[subQ1,subQ0]});Q1176=makeQuery(id+"F0.imprint","IMPRINT",FACE,{"disambiguationData":[TD([[makeQuery(id+"F0.imprint","IMPRINT",EDGE,{"disambiguationData":[TD([[subQ2,1.0]])],"derivedFrom":subQ1}),-1.0]])]});}
            var Q1177;
            {var subQ0=sQuery(id+"F0.wireOp",EDGE,"E3.19.0.89");Q1177=makeQuery(id+"F0.imprint","IMPRINT",FACE,{"disambiguationData":[TD([[makeQuery(id+"F0.imprint","IMPRINT",EDGE,{"derivedFrom":subQ0}),-1.0]])]});}
            var Q1178;
            {var subQ3=sQuery(id+"F0.wireOp",EDGE,"E3.20.0.86");Q1178=makeQuery(id+"F0.imprint","IMPRINT",FACE,{"disambiguationData":[TD([[makeQuery(id+"F0.imprint","IMPRINT",EDGE,{"derivedFrom":subQ3}),1.0]])]});}
            var Q1179;
            {var subQ0=sQuery(id+"F0.wireOp",EDGE,"E3.21.0.97");var subQ1=sQuery(id+"F0.wireOp",EDGE,"E3.21.0.40");var subQ2=makeQuery(id+"F0.imprint","INTERSECT",VERTEX,{"derivedFrom":[subQ1,subQ0]});Q1179=makeQuery(id+"F0.imprint","IMPRINT",FACE,{"disambiguationData":[TD([[makeQuery(id+"F0.imprint","IMPRINT",EDGE,{"disambiguationData":[TD([[subQ2,1.0]])],"derivedFrom":subQ1}),-1.0]])]});}
            var Q1180;
            {var subQ0=sQuery(id+"F0.wireOp",EDGE,"E3.19.0.100");var subQ1=sQuery(id+"F0.wireOp",EDGE,"E3.19.0.52");var subQ2=makeQuery(id+"F0.imprint","INTERSECT",VERTEX,{"derivedFrom":[subQ1,subQ0]});Q1180=makeQuery(id+"F0.imprint","IMPRINT",FACE,{"disambiguationData":[TD([[makeQuery(id+"F0.imprint","IMPRINT",EDGE,{"disambiguationData":[TD([[subQ2,1.0]])],"derivedFrom":subQ1}),-1.0]])]});}
            var Q1181;
            {var subQ0=sQuery(id+"F0.wireOp",EDGE,"E3.22.0.20");Q1181=makeQuery(id+"F0.imprint","IMPRINT",FACE,{"disambiguationData":[TD([[makeQuery(id+"F0.imprint","IMPRINT",EDGE,{"derivedFrom":subQ0}),-1.0]])]});}
            var Q1182;
            {var subQ0=sQuery(id+"F0.wireOp",EDGE,"E3.21.0.8");var subQ1=sQuery(id+"F0.wireOp",EDGE,"E3.21.0.6");var subQ2=makeQuery(id+"F0.imprint","INTERSECT",VERTEX,{"derivedFrom":[subQ1,subQ0]});Q1182=makeQuery(id+"F0.imprint","IMPRINT",FACE,{"disambiguationData":[TD([[makeQuery(id+"F0.imprint","IMPRINT",EDGE,{"disambiguationData":[TD([[subQ2,-1.0]])],"derivedFrom":subQ1}),-1.0]])]});}
            var Q1183;
            {var subQ0=sQuery(id+"F0.wireOp",EDGE,"E3.23.0.96");var subQ1=sQuery(id+"F0.wireOp",EDGE,"E3.23.0.39");var subQ2=makeQuery(id+"F0.imprint","INTERSECT",VERTEX,{"derivedFrom":[subQ1,subQ0]});Q1183=makeQuery(id+"F0.imprint","IMPRINT",FACE,{"disambiguationData":[TD([[makeQuery(id+"F0.imprint","IMPRINT",EDGE,{"disambiguationData":[TD([[subQ2,1.0]])],"derivedFrom":subQ1}),-1.0]])]});}
            var Q1184;
            {var subQ3=sQuery(id+"F0.wireOp",EDGE,"E3.24.0.54");Q1184=makeQuery(id+"F0.imprint","IMPRINT",FACE,{"disambiguationData":[TD([[makeQuery(id+"F0.imprint","IMPRINT",EDGE,{"derivedFrom":subQ3}),1.0]])]});}
            var Q1185;
            {var subQ0=sQuery(id+"F0.wireOp",EDGE,"E3.17.0.41");var subQ1=sQuery(id+"F0.wireOp",EDGE,"E3.17.0.13");var subQ2=makeQuery(id+"F0.imprint","INTERSECT",VERTEX,{"derivedFrom":[subQ1,subQ0]});Q1185=makeQuery(id+"F0.imprint","IMPRINT",FACE,{"disambiguationData":[TD([[makeQuery(id+"F0.imprint","IMPRINT",EDGE,{"disambiguationData":[TD([[subQ2,-1.0]])],"derivedFrom":subQ1}),-1.0]])]});}
            var Q1186;
            {var subQ0=sQuery(id+"F0.wireOp",EDGE,"E3.18.0.42");var subQ1=sQuery(id+"F0.wireOp",EDGE,"E3.18.0.16");var subQ2=makeQuery(id+"F0.imprint","INTERSECT",VERTEX,{"derivedFrom":[subQ1,subQ0]});Q1186=makeQuery(id+"F0.imprint","IMPRINT",FACE,{"disambiguationData":[TD([[makeQuery(id+"F0.imprint","IMPRINT",EDGE,{"disambiguationData":[TD([[subQ2,-1.0]])],"derivedFrom":subQ1}),-1.0]])]});}
            var Q1187;
            {var subQ0=sQuery(id+"F0.wireOp",EDGE,"E3.16.0.97");var subQ1=sQuery(id+"F0.wireOp",EDGE,"E3.16.0.40");var subQ2=makeQuery(id+"F0.imprint","INTERSECT",VERTEX,{"derivedFrom":[subQ1,subQ0]});Q1187=makeQuery(id+"F0.imprint","IMPRINT",FACE,{"disambiguationData":[TD([[makeQuery(id+"F0.imprint","IMPRINT",EDGE,{"disambiguationData":[TD([[subQ2,1.0]])],"derivedFrom":subQ1}),-1.0]])]});}
            var Q1188;
            {var subQ3=sQuery(id+"F0.wireOp",EDGE,"E3.3.0.81");Q1188=makeQuery(id+"F0.imprint","IMPRINT",FACE,{"disambiguationData":[TD([[makeQuery(id+"F0.imprint","IMPRINT",EDGE,{"derivedFrom":subQ3}),1.0]])]});}
            var Q1189;
            {var subQ3=sQuery(id+"F0.wireOp",EDGE,"E3.5.0.53");Q1189=makeQuery(id+"F0.imprint","IMPRINT",FACE,{"disambiguationData":[TD([[makeQuery(id+"F0.imprint","IMPRINT",EDGE,{"derivedFrom":subQ3}),1.0]])]});}
            var Q1190;
            {var subQ0=sQuery(id+"F0.wireOp",EDGE,"E3.6.0.99");var subQ1=sQuery(id+"F0.wireOp",EDGE,"E3.6.0.49");var subQ2=makeQuery(id+"F0.imprint","INTERSECT",VERTEX,{"derivedFrom":[subQ1,subQ0]});Q1190=makeQuery(id+"F0.imprint","IMPRINT",FACE,{"disambiguationData":[TD([[makeQuery(id+"F0.imprint","IMPRINT",EDGE,{"disambiguationData":[TD([[subQ2,1.0]])],"derivedFrom":subQ1}),-1.0]])]});}
            var Q1191;
            {var subQ5=sQuery(id+"F0.wireOp",EDGE,"E3.8.0.93");Q1191=makeQuery(id+"F0.imprint","IMPRINT",FACE,{"disambiguationData":[TD([[makeQuery(id+"F0.imprint","IMPRINT",EDGE,{"derivedFrom":subQ5}),1.0]])]});}
            var Q1192;
            {var subQ3=sQuery(id+"F0.wireOp",EDGE,"E3.8.0.82");Q1192=makeQuery(id+"F0.imprint","IMPRINT",FACE,{"disambiguationData":[TD([[makeQuery(id+"F0.imprint","IMPRINT",EDGE,{"derivedFrom":subQ3}),1.0]])]});}
            var Q1193;
            {var subQ5=sQuery(id+"F0.wireOp",EDGE,"E3.14.0.22");Q1193=makeQuery(id+"F0.imprint","IMPRINT",FACE,{"disambiguationData":[TD([[makeQuery(id+"F0.imprint","IMPRINT",EDGE,{"derivedFrom":subQ5}),-1.0]])]});}
            var Q1194;
            {var subQ7=sQuery(id+"F0.wireOp",EDGE,"E3.15.0.83");Q1194=makeQuery(id+"F0.imprint","IMPRINT",FACE,{"disambiguationData":[TD([[makeQuery(id+"F0.imprint","IMPRINT",EDGE,{"derivedFrom":subQ7}),-1.0]])]});}
            var Q1195;
            {var subQ0=sQuery(id+"F0.wireOp",EDGE,"E3.1.0.20");Q1195=makeQuery(id+"F0.imprint","IMPRINT",FACE,{"disambiguationData":[TD([[makeQuery(id+"F0.imprint","IMPRINT",EDGE,{"derivedFrom":subQ0}),-1.0]])]});}
            var Q1196;
            {var subQ0=sQuery(id+"F0.wireOp",EDGE,"E3.2.0.96");var subQ1=sQuery(id+"F0.wireOp",EDGE,"E3.2.0.39");var subQ2=makeQuery(id+"F0.imprint","INTERSECT",VERTEX,{"derivedFrom":[subQ1,subQ0]});Q1196=makeQuery(id+"F0.imprint","IMPRINT",FACE,{"disambiguationData":[TD([[makeQuery(id+"F0.imprint","IMPRINT",EDGE,{"disambiguationData":[TD([[subQ2,1.0]])],"derivedFrom":subQ1}),-1.0]])]});}
            var Q1197;
            {var subQ0=sQuery(id+"F0.wireOp",EDGE,"E3.10.0.19");Q1197=makeQuery(id+"F0.imprint","IMPRINT",FACE,{"disambiguationData":[TD([[makeQuery(id+"F0.imprint","IMPRINT",EDGE,{"derivedFrom":subQ0}),-1.0]])]});}
            var Q1198;
            {var subQ0=sQuery(id+"F0.wireOp",EDGE,"E3.12.0.32");var subQ1=sQuery(id+"F0.wireOp",EDGE,"E3.12.0.0");var subQ2=makeQuery(id+"F0.imprint","INTERSECT",VERTEX,{"derivedFrom":[subQ1,subQ0]});Q1198=makeQuery(id+"F0.imprint","IMPRINT",FACE,{"disambiguationData":[TD([[makeQuery(id+"F0.imprint","IMPRINT",EDGE,{"disambiguationData":[TD([[subQ2,1.0]])],"derivedFrom":subQ1}),-1.0]])]});}
            var Q1199;
            {var subQ5=sQuery(id+"F0.wireOp",EDGE,"E3.16.0.57");Q1199=makeQuery(id+"F0.imprint","IMPRINT",FACE,{"disambiguationData":[TD([[makeQuery(id+"F0.imprint","IMPRINT",EDGE,{"derivedFrom":subQ5}),1.0]])]});}
            var Q1200;
            {var subQ3=sQuery(id+"F0.wireOp",EDGE,"E3.1.0.54");Q1200=makeQuery(id+"F0.imprint","IMPRINT",FACE,{"disambiguationData":[TD([[makeQuery(id+"F0.imprint","IMPRINT",EDGE,{"derivedFrom":subQ3}),1.0]])]});}
            var Q1201;
            {var subQ3=sQuery(id+"F0.wireOp",EDGE,"E3.3.0.53");Q1201=makeQuery(id+"F0.imprint","IMPRINT",FACE,{"disambiguationData":[TD([[makeQuery(id+"F0.imprint","IMPRINT",EDGE,{"derivedFrom":subQ3}),1.0]])]});}
            var Q1202;
            {var subQ0=sQuery(id+"F0.wireOp",EDGE,"E3.16.0.96");var subQ1=sQuery(id+"F0.wireOp",EDGE,"E3.16.0.39");var subQ2=makeQuery(id+"F0.imprint","INTERSECT",VERTEX,{"derivedFrom":[subQ1,subQ0]});Q1202=makeQuery(id+"F0.imprint","IMPRINT",FACE,{"disambiguationData":[TD([[makeQuery(id+"F0.imprint","IMPRINT",EDGE,{"disambiguationData":[TD([[subQ2,1.0]])],"derivedFrom":subQ1}),-1.0]])]});}
            var Q1203;
            {var subQ0=sQuery(id+"F0.wireOp",EDGE,"E3.14.0.97");var subQ1=sQuery(id+"F0.wireOp",EDGE,"E3.14.0.40");var subQ2=makeQuery(id+"F0.imprint","INTERSECT",VERTEX,{"derivedFrom":[subQ1,subQ0]});Q1203=makeQuery(id+"F0.imprint","IMPRINT",FACE,{"disambiguationData":[TD([[makeQuery(id+"F0.imprint","IMPRINT",EDGE,{"disambiguationData":[TD([[subQ2,1.0]])],"derivedFrom":subQ1}),-1.0]])]});}
            var Q1204;
            {var subQ0=sQuery(id+"F0.wireOp",EDGE,"E3.13.0.35");var subQ1=sQuery(id+"F0.wireOp",EDGE,"E3.13.0.32");var subQ2=makeQuery(id+"F0.imprint","INTERSECT",VERTEX,{"derivedFrom":[subQ1,subQ0]});Q1204=makeQuery(id+"F0.imprint","IMPRINT",FACE,{"disambiguationData":[TD([[makeQuery(id+"F0.imprint","IMPRINT",EDGE,{"disambiguationData":[TD([[subQ2,1.0]])],"derivedFrom":subQ1}),1.0]])]});}
            var Q1205;
            {var subQ3=sQuery(id+"F0.wireOp",EDGE,"E3.6.0.55");Q1205=makeQuery(id+"F0.imprint","IMPRINT",FACE,{"disambiguationData":[TD([[makeQuery(id+"F0.imprint","IMPRINT",EDGE,{"derivedFrom":subQ3}),1.0]])]});}
            var Q1206;
            {var subQ0=sQuery(id+"F0.wireOp",EDGE,"E3.8.0.19");Q1206=makeQuery(id+"F0.imprint","IMPRINT",FACE,{"disambiguationData":[TD([[makeQuery(id+"F0.imprint","IMPRINT",EDGE,{"derivedFrom":subQ0}),-1.0]])]});}
            var Q1207;
            {var subQ0=sQuery(id+"F0.wireOp",EDGE,"E3.11.0.89");Q1207=makeQuery(id+"F0.imprint","IMPRINT",FACE,{"disambiguationData":[TD([[makeQuery(id+"F0.imprint","IMPRINT",EDGE,{"derivedFrom":subQ0}),-1.0]])]});}
            var Q1208;
            {var subQ3=sQuery(id+"F0.wireOp",EDGE,"E3.1.0.118");Q1208=makeQuery(id+"F0.imprint","IMPRINT",FACE,{"disambiguationData":[TD([[makeQuery(id+"F0.imprint","IMPRINT",EDGE,{"derivedFrom":subQ3}),1.0]])]});}
            var Q1209;
            {var subQ3=sQuery(id+"F0.wireOp",EDGE,"E3.16.0.85");Q1209=makeQuery(id+"F0.imprint","IMPRINT",FACE,{"disambiguationData":[TD([[makeQuery(id+"F0.imprint","IMPRINT",EDGE,{"derivedFrom":subQ3}),1.0]])]});}
            var Q1210;
            {var subQ3=sQuery(id+"F0.wireOp",EDGE,"E3.15.0.103");Q1210=makeQuery(id+"F0.imprint","IMPRINT",FACE,{"disambiguationData":[TD([[makeQuery(id+"F0.imprint","IMPRINT",EDGE,{"derivedFrom":subQ3}),1.0]])]});}
            var Q1211;
            {var subQ0=sQuery(id+"F0.wireOp",EDGE,"E3.7.0.97");var subQ1=sQuery(id+"F0.wireOp",EDGE,"E3.7.0.40");var subQ2=makeQuery(id+"F0.imprint","INTERSECT",VERTEX,{"derivedFrom":[subQ1,subQ0]});Q1211=makeQuery(id+"F0.imprint","IMPRINT",FACE,{"disambiguationData":[TD([[makeQuery(id+"F0.imprint","IMPRINT",EDGE,{"disambiguationData":[TD([[subQ2,1.0]])],"derivedFrom":subQ1}),-1.0]])]});}
            var Q1212;
            {var subQ0=sQuery(id+"F0.wireOp",EDGE,"E3.8.0.20");Q1212=makeQuery(id+"F0.imprint","IMPRINT",FACE,{"disambiguationData":[TD([[makeQuery(id+"F0.imprint","IMPRINT",EDGE,{"derivedFrom":subQ0}),-1.0]])]});}
            var Q1213;
            {var subQ0=sQuery(id+"F0.wireOp",EDGE,"E3.9.0.96");var subQ1=sQuery(id+"F0.wireOp",EDGE,"E3.9.0.39");var subQ2=makeQuery(id+"F0.imprint","INTERSECT",VERTEX,{"derivedFrom":[subQ1,subQ0]});Q1213=makeQuery(id+"F0.imprint","IMPRINT",FACE,{"disambiguationData":[TD([[makeQuery(id+"F0.imprint","IMPRINT",EDGE,{"disambiguationData":[TD([[subQ2,1.0]])],"derivedFrom":subQ1}),-1.0]])]});}
            var Q1214;
            {var subQ3=sQuery(id+"F0.wireOp",EDGE,"E3.12.0.53");Q1214=makeQuery(id+"F0.imprint","IMPRINT",FACE,{"disambiguationData":[TD([[makeQuery(id+"F0.imprint","IMPRINT",EDGE,{"derivedFrom":subQ3}),1.0]])]});}
            var Q1215;
            {var subQ0=sQuery(id+"F0.wireOp",EDGE,"E3.16.0.94");var subQ1=sQuery(id+"F0.wireOp",EDGE,"E3.16.0.42");var subQ2=makeQuery(id+"F0.imprint","INTERSECT",VERTEX,{"derivedFrom":[subQ1,subQ0]});Q1215=makeQuery(id+"F0.imprint","IMPRINT",FACE,{"disambiguationData":[TD([[makeQuery(id+"F0.imprint","IMPRINT",EDGE,{"disambiguationData":[TD([[subQ2,1.0]])],"derivedFrom":subQ1}),-1.0]])]});}
            var Q1216;
            {var subQ3=sQuery(id+"F0.wireOp",EDGE,"E3.14.0.53");Q1216=makeQuery(id+"F0.imprint","IMPRINT",FACE,{"disambiguationData":[TD([[makeQuery(id+"F0.imprint","IMPRINT",EDGE,{"derivedFrom":subQ3}),1.0]])]});}
            var Q1217;
            {var subQ0=sQuery(id+"F0.wireOp",EDGE,"E3.9.0.97");var subQ1=sQuery(id+"F0.wireOp",EDGE,"E3.9.0.40");var subQ2=makeQuery(id+"F0.imprint","INTERSECT",VERTEX,{"derivedFrom":[subQ1,subQ0]});Q1217=makeQuery(id+"F0.imprint","IMPRINT",FACE,{"disambiguationData":[TD([[makeQuery(id+"F0.imprint","IMPRINT",EDGE,{"disambiguationData":[TD([[subQ2,1.0]])],"derivedFrom":subQ1}),-1.0]])]});}
            var Q1218;
            {var subQ5=sQuery(id+"F0.wireOp",EDGE,"E3.11.0.57");Q1218=makeQuery(id+"F0.imprint","IMPRINT",FACE,{"disambiguationData":[TD([[makeQuery(id+"F0.imprint","IMPRINT",EDGE,{"derivedFrom":subQ5}),1.0]])]});}
            var Q1219;
            {var subQ0=sQuery(id+"F0.wireOp",EDGE,"E3.11.0.96");var subQ1=sQuery(id+"F0.wireOp",EDGE,"E3.11.0.39");var subQ2=makeQuery(id+"F0.imprint","INTERSECT",VERTEX,{"derivedFrom":[subQ1,subQ0]});Q1219=makeQuery(id+"F0.imprint","IMPRINT",FACE,{"disambiguationData":[TD([[makeQuery(id+"F0.imprint","IMPRINT",EDGE,{"disambiguationData":[TD([[subQ2,1.0]])],"derivedFrom":subQ1}),-1.0]])]});}
            var Q1220;
            {var subQ3=sQuery(id+"F0.wireOp",EDGE,"E3.11.0.65");Q1220=makeQuery(id+"F0.imprint","IMPRINT",FACE,{"disambiguationData":[TD([[makeQuery(id+"F0.imprint","IMPRINT",EDGE,{"derivedFrom":subQ3}),-1.0]])]});}
            var Q1221;
            {var subQ0=sQuery(id+"F0.wireOp",EDGE,"E3.13.0.57");Q1221=makeQuery(id+"F0.imprint","IMPRINT",FACE,{"disambiguationData":[TD([[makeQuery(id+"F0.imprint","IMPRINT",EDGE,{"derivedFrom":subQ0}),-1.0]])]});}
            var Q1222;
            {var subQ0=sQuery(id+"F0.wireOp",EDGE,"E3.12.0.72");var subQ1=sQuery(id+"F0.wireOp",EDGE,"E3.12.0.10");var subQ2=makeQuery(id+"F0.imprint","INTERSECT",VERTEX,{"derivedFrom":[subQ1,subQ0]});Q1222=makeQuery(id+"F0.imprint","IMPRINT",FACE,{"disambiguationData":[TD([[makeQuery(id+"F0.imprint","IMPRINT",EDGE,{"disambiguationData":[TD([[subQ2,1.0]])],"derivedFrom":subQ1}),-1.0]])]});}
            var Q1223;
            {var subQ3=sQuery(id+"F0.wireOp",EDGE,"E3.1.0.82");Q1223=makeQuery(id+"F0.imprint","IMPRINT",FACE,{"disambiguationData":[TD([[makeQuery(id+"F0.imprint","IMPRINT",EDGE,{"derivedFrom":subQ3}),1.0]])]});}
            var Q1224;
            {var subQ3=sQuery(id+"F0.wireOp",EDGE,"E3.1.0.55");Q1224=makeQuery(id+"F0.imprint","IMPRINT",FACE,{"disambiguationData":[TD([[makeQuery(id+"F0.imprint","IMPRINT",EDGE,{"derivedFrom":subQ3}),1.0]])]});}
            var Q1225;
            {var subQ3=sQuery(id+"F0.wireOp",EDGE,"E3.2.0.85");Q1225=makeQuery(id+"F0.imprint","IMPRINT",FACE,{"disambiguationData":[TD([[makeQuery(id+"F0.imprint","IMPRINT",EDGE,{"derivedFrom":subQ3}),1.0]])]});}
            var Q1226;
            {var subQ3=sQuery(id+"F0.wireOp",EDGE,"E3.3.0.118");Q1226=makeQuery(id+"F0.imprint","IMPRINT",FACE,{"disambiguationData":[TD([[makeQuery(id+"F0.imprint","IMPRINT",EDGE,{"derivedFrom":subQ3}),1.0]])]});}
            var Q1227;
            {var subQ0=sQuery(id+"F0.wireOp",EDGE,"E3.5.0.63");Q1227=makeQuery(id+"F0.imprint","IMPRINT",FACE,{"disambiguationData":[TD([[makeQuery(id+"F0.imprint","IMPRINT",EDGE,{"derivedFrom":subQ0}),-1.0]])]});}
            var Q1228;
            {var subQ3=sQuery(id+"F0.wireOp",EDGE,"E3.7.0.86");Q1228=makeQuery(id+"F0.imprint","IMPRINT",FACE,{"disambiguationData":[TD([[makeQuery(id+"F0.imprint","IMPRINT",EDGE,{"derivedFrom":subQ3}),1.0]])]});}
            var Q1229;
            {var subQ0=sQuery(id+"F0.wireOp",EDGE,"E3.6.0.100");var subQ1=sQuery(id+"F0.wireOp",EDGE,"E3.6.0.52");var subQ2=makeQuery(id+"F0.imprint","INTERSECT",VERTEX,{"derivedFrom":[subQ1,subQ0]});Q1229=makeQuery(id+"F0.imprint","IMPRINT",FACE,{"disambiguationData":[TD([[makeQuery(id+"F0.imprint","IMPRINT",EDGE,{"disambiguationData":[TD([[subQ2,1.0]])],"derivedFrom":subQ1}),-1.0]])]});}
            var Q1230;
            {var subQ0=sQuery(id+"F0.wireOp",EDGE,"E3.13.0.96");var subQ1=sQuery(id+"F0.wireOp",EDGE,"E3.13.0.43");var subQ2=makeQuery(id+"F0.imprint","INTERSECT",VERTEX,{"derivedFrom":[subQ1,subQ0]});Q1230=makeQuery(id+"F0.imprint","IMPRINT",FACE,{"disambiguationData":[TD([[makeQuery(id+"F0.imprint","IMPRINT",EDGE,{"disambiguationData":[TD([[subQ2,1.0]])],"derivedFrom":subQ1}),-1.0]])]});}
            var Q1231;
            {var subQ5=sQuery(id+"F0.wireOp",EDGE,"E3.16.0.22");Q1231=makeQuery(id+"F0.imprint","IMPRINT",FACE,{"disambiguationData":[TD([[makeQuery(id+"F0.imprint","IMPRINT",EDGE,{"derivedFrom":subQ5}),-1.0]])]});}
            var Q1232;
            {var subQ0=sQuery(id+"F0.wireOp",EDGE,"E3.15.0.89");Q1232=makeQuery(id+"F0.imprint","IMPRINT",FACE,{"disambiguationData":[TD([[makeQuery(id+"F0.imprint","IMPRINT",EDGE,{"derivedFrom":subQ0}),-1.0]])]});}
            var Q1233;
            {var subQ3=sQuery(id+"F0.wireOp",EDGE,"E3.10.0.55");Q1233=makeQuery(id+"F0.imprint","IMPRINT",FACE,{"disambiguationData":[TD([[makeQuery(id+"F0.imprint","IMPRINT",EDGE,{"derivedFrom":subQ3}),1.0]])]});}
            var Q1234;
            {var subQ0=sQuery(id+"F0.wireOp",EDGE,"E3.9.0.94");var subQ1=sQuery(id+"F0.wireOp",EDGE,"E3.9.0.42");var subQ2=makeQuery(id+"F0.imprint","INTERSECT",VERTEX,{"derivedFrom":[subQ1,subQ0]});Q1234=makeQuery(id+"F0.imprint","IMPRINT",FACE,{"disambiguationData":[TD([[makeQuery(id+"F0.imprint","IMPRINT",EDGE,{"disambiguationData":[TD([[subQ2,1.0]])],"derivedFrom":subQ1}),-1.0]])]});}
            var Q1235;
            {var subQ3=sQuery(id+"F0.wireOp",EDGE,"E3.12.0.118");Q1235=makeQuery(id+"F0.imprint","IMPRINT",FACE,{"disambiguationData":[TD([[makeQuery(id+"F0.imprint","IMPRINT",EDGE,{"derivedFrom":subQ3}),1.0]])]});}
            var Q1236;
            {var subQ0=sQuery(id+"F0.wireOp",EDGE,"E3.12.0.19");Q1236=makeQuery(id+"F0.imprint","IMPRINT",FACE,{"disambiguationData":[TD([[makeQuery(id+"F0.imprint","IMPRINT",EDGE,{"derivedFrom":subQ0}),-1.0]])]});}
            var Q1237;
            {var subQ0=sQuery(id+"F0.wireOp",EDGE,"E3.3.0.20");Q1237=makeQuery(id+"F0.imprint","IMPRINT",FACE,{"disambiguationData":[TD([[makeQuery(id+"F0.imprint","IMPRINT",EDGE,{"derivedFrom":subQ0}),-1.0]])]});}
            var Q1238;
            {var subQ3=sQuery(id+"F0.wireOp",EDGE,"E3.5.0.54");Q1238=makeQuery(id+"F0.imprint","IMPRINT",FACE,{"disambiguationData":[TD([[makeQuery(id+"F0.imprint","IMPRINT",EDGE,{"derivedFrom":subQ3}),1.0]])]});}
            var Q1239;
            {var subQ0=sQuery(id+"F0.wireOp",EDGE,"E3.6.0.41");var subQ1=sQuery(id+"F0.wireOp",EDGE,"E3.6.0.6");var subQ2=makeQuery(id+"F0.imprint","INTERSECT",VERTEX,{"derivedFrom":[subQ1,subQ0]});Q1239=makeQuery(id+"F0.imprint","IMPRINT",FACE,{"disambiguationData":[TD([[makeQuery(id+"F0.imprint","IMPRINT",EDGE,{"disambiguationData":[TD([[subQ2,1.0]])],"derivedFrom":subQ1}),-1.0]])]});}
            var Q1240;
            {var subQ0=sQuery(id+"F0.wireOp",EDGE,"E3.13.0.96");var subQ1=sQuery(id+"F0.wireOp",EDGE,"E3.13.0.39");var subQ2=makeQuery(id+"F0.imprint","INTERSECT",VERTEX,{"derivedFrom":[subQ1,subQ0]});Q1240=makeQuery(id+"F0.imprint","IMPRINT",FACE,{"disambiguationData":[TD([[makeQuery(id+"F0.imprint","IMPRINT",EDGE,{"disambiguationData":[TD([[subQ2,1.0]])],"derivedFrom":subQ1}),-1.0]])]});}
            var Q1241;
            {var subQ3=sQuery(id+"F0.wireOp",EDGE,"E3.15.0.84");Q1241=makeQuery(id+"F0.imprint","IMPRINT",FACE,{"disambiguationData":[TD([[makeQuery(id+"F0.imprint","IMPRINT",EDGE,{"derivedFrom":subQ3}),1.0]])]});}
            var Q1242;
            {var subQ0=sQuery(id+"F0.wireOp",EDGE,"E3.11.0.68");var subQ1=sQuery(id+"F0.wireOp",EDGE,"E3.11.0.8");var subQ2=makeQuery(id+"F0.imprint","INTERSECT",VERTEX,{"derivedFrom":[subQ1,subQ0]});Q1242=makeQuery(id+"F0.imprint","IMPRINT",FACE,{"disambiguationData":[TD([[makeQuery(id+"F0.imprint","IMPRINT",EDGE,{"disambiguationData":[TD([[subQ2,1.0]])],"derivedFrom":subQ1}),-1.0]])]});}
            var Q1243;
            {var subQ0=sQuery(id+"F0.wireOp",EDGE,"E3.10.0.35");var subQ1=sQuery(id+"F0.wireOp",EDGE,"E3.10.0.32");var subQ2=makeQuery(id+"F0.imprint","INTERSECT",VERTEX,{"derivedFrom":[subQ1,subQ0]});Q1243=makeQuery(id+"F0.imprint","IMPRINT",FACE,{"disambiguationData":[TD([[makeQuery(id+"F0.imprint","IMPRINT",EDGE,{"disambiguationData":[TD([[subQ2,1.0]])],"derivedFrom":subQ1}),1.0]])]});}
            var Q1244;
            {var subQ0=sQuery(id+"F0.wireOp",EDGE,"E3.11.0.39");var subQ1=sQuery(id+"F0.wireOp",EDGE,"E3.11.0.17");var subQ2=makeQuery(id+"F0.imprint","INTERSECT",VERTEX,{"derivedFrom":[subQ1,subQ0]});Q1244=makeQuery(id+"F0.imprint","IMPRINT",FACE,{"disambiguationData":[TD([[makeQuery(id+"F0.imprint","IMPRINT",EDGE,{"disambiguationData":[TD([[subQ2,-1.0]])],"derivedFrom":subQ1}),-1.0]])]});}
            var Q1245;
            {var subQ3=sQuery(id+"F0.wireOp",EDGE,"E3.13.0.65");Q1245=makeQuery(id+"F0.imprint","IMPRINT",FACE,{"disambiguationData":[TD([[makeQuery(id+"F0.imprint","IMPRINT",EDGE,{"derivedFrom":subQ3}),-1.0]])]});}
            var Q1246;
            {var subQ0=sQuery(id+"F0.wireOp",EDGE,"E3.12.0.20");Q1246=makeQuery(id+"F0.imprint","IMPRINT",FACE,{"disambiguationData":[TD([[makeQuery(id+"F0.imprint","IMPRINT",EDGE,{"derivedFrom":subQ0}),-1.0]])]});}
            var Q1247;
            {var subQ0=sQuery(id+"F0.wireOp",EDGE,"E3.5.0.41");var subQ1=sQuery(id+"F0.wireOp",EDGE,"E3.5.0.13");var subQ2=makeQuery(id+"F0.imprint","INTERSECT",VERTEX,{"derivedFrom":[subQ1,subQ0]});Q1247=makeQuery(id+"F0.imprint","IMPRINT",FACE,{"disambiguationData":[TD([[makeQuery(id+"F0.imprint","IMPRINT",EDGE,{"disambiguationData":[TD([[subQ2,-1.0]])],"derivedFrom":subQ1}),-1.0]])]});}
            var Q1248;
            {var subQ0=sQuery(id+"F0.wireOp",EDGE,"E3.8.0.89");Q1248=makeQuery(id+"F0.imprint","IMPRINT",FACE,{"disambiguationData":[TD([[makeQuery(id+"F0.imprint","IMPRINT",EDGE,{"derivedFrom":subQ0}),-1.0]])]});}
            var Q1249;
            {var subQ3=sQuery(id+"F0.wireOp",EDGE,"E3.9.0.86");Q1249=makeQuery(id+"F0.imprint","IMPRINT",FACE,{"disambiguationData":[TD([[makeQuery(id+"F0.imprint","IMPRINT",EDGE,{"derivedFrom":subQ3}),1.0]])]});}
            var Q1250;
            {var subQ0=sQuery(id+"F0.wireOp",EDGE,"E3.1.0.100");var subQ1=sQuery(id+"F0.wireOp",EDGE,"E3.1.0.52");var subQ2=makeQuery(id+"F0.imprint","INTERSECT",VERTEX,{"derivedFrom":[subQ1,subQ0]});Q1250=makeQuery(id+"F0.imprint","IMPRINT",FACE,{"disambiguationData":[TD([[makeQuery(id+"F0.imprint","IMPRINT",EDGE,{"disambiguationData":[TD([[subQ2,1.0]])],"derivedFrom":subQ1}),-1.0]])]});}
            var Q1251;
            {var subQ3=sQuery(id+"F0.wireOp",EDGE,"E3.12.0.103");Q1251=makeQuery(id+"F0.imprint","IMPRINT",FACE,{"disambiguationData":[TD([[makeQuery(id+"F0.imprint","IMPRINT",EDGE,{"derivedFrom":subQ3}),1.0]])]});}
            var Q1252;
            {var subQ5=sQuery(id+"F0.wireOp",EDGE,"E3.12.0.93");Q1252=makeQuery(id+"F0.imprint","IMPRINT",FACE,{"disambiguationData":[TD([[makeQuery(id+"F0.imprint","IMPRINT",EDGE,{"derivedFrom":subQ5}),1.0]])]});}
            var Q1253;
            {var subQ0=sQuery(id+"F0.wireOp",EDGE,"E3.4.0.97");var subQ1=sQuery(id+"F0.wireOp",EDGE,"E3.4.0.40");var subQ2=makeQuery(id+"F0.imprint","INTERSECT",VERTEX,{"derivedFrom":[subQ1,subQ0]});Q1253=makeQuery(id+"F0.imprint","IMPRINT",FACE,{"disambiguationData":[TD([[makeQuery(id+"F0.imprint","IMPRINT",EDGE,{"disambiguationData":[TD([[subQ2,1.0]])],"derivedFrom":subQ1}),-1.0]])]});}
            var Q1254;
            {var subQ0=sQuery(id+"F0.wireOp",EDGE,"E3.6.0.96");var subQ1=sQuery(id+"F0.wireOp",EDGE,"E3.6.0.39");var subQ2=makeQuery(id+"F0.imprint","INTERSECT",VERTEX,{"derivedFrom":[subQ1,subQ0]});Q1254=makeQuery(id+"F0.imprint","IMPRINT",FACE,{"disambiguationData":[TD([[makeQuery(id+"F0.imprint","IMPRINT",EDGE,{"disambiguationData":[TD([[subQ2,1.0]])],"derivedFrom":subQ1}),-1.0]])]});}
            var Q1255;
            {var subQ3=sQuery(id+"F0.wireOp",EDGE,"E3.7.0.54");Q1255=makeQuery(id+"F0.imprint","IMPRINT",FACE,{"disambiguationData":[TD([[makeQuery(id+"F0.imprint","IMPRINT",EDGE,{"derivedFrom":subQ3}),1.0]])]});}
            var Q1256;
            {var subQ3=sQuery(id+"F0.wireOp",EDGE,"E3.7.0.81");Q1256=makeQuery(id+"F0.imprint","IMPRINT",FACE,{"disambiguationData":[TD([[makeQuery(id+"F0.imprint","IMPRINT",EDGE,{"derivedFrom":subQ3}),1.0]])]});}
            var Q1257;
            {var subQ10=sQuery(id+"F0.wireOp",EDGE,"E3.9.0.93");Q1257=makeQuery(id+"F0.imprint","IMPRINT",FACE,{"disambiguationData":[TD([[makeQuery(id+"F0.imprint","IMPRINT",EDGE,{"derivedFrom":subQ10}),-1.0]])]});}
            var Q1258;
            {var subQ3=sQuery(id+"F0.wireOp",EDGE,"E3.9.0.53");Q1258=makeQuery(id+"F0.imprint","IMPRINT",FACE,{"disambiguationData":[TD([[makeQuery(id+"F0.imprint","IMPRINT",EDGE,{"derivedFrom":subQ3}),1.0]])]});}
            var Q1259;
            {var subQ3=sQuery(id+"F0.wireOp",EDGE,"E3.16.0.81");Q1259=makeQuery(id+"F0.imprint","IMPRINT",FACE,{"disambiguationData":[TD([[makeQuery(id+"F0.imprint","IMPRINT",EDGE,{"derivedFrom":subQ3}),1.0]])]});}
            var Q1260;
            {var subQ5=sQuery(id+"F0.wireOp",EDGE,"E2.5.0.4");Q1260=makeQuery(id+"F0.imprint","IMPRINT",FACE,{"disambiguationData":[TD([[makeQuery(id+"F0.imprint","IMPRINT",EDGE,{"derivedFrom":subQ5}),1.0]])]});}
            var Q1261;
            {var subQ0=sQuery(id+"F0.wireOp",EDGE,"E3.1.0.41");var subQ1=sQuery(id+"F0.wireOp",EDGE,"E3.1.0.6");var subQ2=makeQuery(id+"F0.imprint","INTERSECT",VERTEX,{"derivedFrom":[subQ1,subQ0]});Q1261=makeQuery(id+"F0.imprint","IMPRINT",FACE,{"disambiguationData":[TD([[makeQuery(id+"F0.imprint","IMPRINT",EDGE,{"disambiguationData":[TD([[subQ2,1.0]])],"derivedFrom":subQ1}),-1.0]])]});}
            var Q1262;
            {var subQ3=sQuery(id+"F0.wireOp",EDGE,"E3.2.0.53");Q1262=makeQuery(id+"F0.imprint","IMPRINT",FACE,{"disambiguationData":[TD([[makeQuery(id+"F0.imprint","IMPRINT",EDGE,{"derivedFrom":subQ3}),1.0]])]});}
            var Q1263;
            {var subQ3=sQuery(id+"F0.wireOp",EDGE,"E3.5.0.55");Q1263=makeQuery(id+"F0.imprint","IMPRINT",FACE,{"disambiguationData":[TD([[makeQuery(id+"F0.imprint","IMPRINT",EDGE,{"derivedFrom":subQ3}),1.0]])]});}
            var Q1264;
            {var subQ0=sQuery(id+"F0.wireOp",EDGE,"E3.4.0.94");var subQ1=sQuery(id+"F0.wireOp",EDGE,"E3.4.0.42");var subQ2=makeQuery(id+"F0.imprint","INTERSECT",VERTEX,{"derivedFrom":[subQ1,subQ0]});Q1264=makeQuery(id+"F0.imprint","IMPRINT",FACE,{"disambiguationData":[TD([[makeQuery(id+"F0.imprint","IMPRINT",EDGE,{"disambiguationData":[TD([[subQ2,1.0]])],"derivedFrom":subQ1}),-1.0]])]});}
            var Q1265;
            {var subQ0=sQuery(id+"F0.wireOp",EDGE,"E3.16.0.72");var subQ1=sQuery(id+"F0.wireOp",EDGE,"E3.16.0.10");var subQ2=makeQuery(id+"F0.imprint","INTERSECT",VERTEX,{"derivedFrom":[subQ1,subQ0]});Q1265=makeQuery(id+"F0.imprint","IMPRINT",FACE,{"disambiguationData":[TD([[makeQuery(id+"F0.imprint","IMPRINT",EDGE,{"disambiguationData":[TD([[subQ2,1.0]])],"derivedFrom":subQ1}),-1.0]])]});}
            var Q1266;
            {var subQ0=sQuery(id+"F0.wireOp",EDGE,"E3.13.0.97");var subQ1=sQuery(id+"F0.wireOp",EDGE,"E3.13.0.40");var subQ2=makeQuery(id+"F0.imprint","INTERSECT",VERTEX,{"derivedFrom":[subQ1,subQ0]});Q1266=makeQuery(id+"F0.imprint","IMPRINT",FACE,{"disambiguationData":[TD([[makeQuery(id+"F0.imprint","IMPRINT",EDGE,{"disambiguationData":[TD([[subQ2,1.0]])],"derivedFrom":subQ1}),-1.0]])]});}
            var Q1267;
            {var subQ5=sQuery(id+"F0.wireOp",EDGE,"E3.15.0.57");Q1267=makeQuery(id+"F0.imprint","IMPRINT",FACE,{"disambiguationData":[TD([[makeQuery(id+"F0.imprint","IMPRINT",EDGE,{"derivedFrom":subQ5}),1.0]])]});}
            var Q1268;
            {var subQ0=sQuery(id+"F0.wireOp",EDGE,"E3.13.0.39");var subQ1=sQuery(id+"F0.wireOp",EDGE,"E3.13.0.17");var subQ2=makeQuery(id+"F0.imprint","INTERSECT",VERTEX,{"derivedFrom":[subQ1,subQ0]});Q1268=makeQuery(id+"F0.imprint","IMPRINT",FACE,{"disambiguationData":[TD([[makeQuery(id+"F0.imprint","IMPRINT",EDGE,{"disambiguationData":[TD([[subQ2,-1.0]])],"derivedFrom":subQ1}),-1.0]])]});}
            var Q1269;
            {var subQ0=sQuery(id+"F0.wireOp",EDGE,"E3.12.0.35");var subQ1=sQuery(id+"F0.wireOp",EDGE,"E3.12.0.32");var subQ2=makeQuery(id+"F0.imprint","INTERSECT",VERTEX,{"derivedFrom":[subQ1,subQ0]});Q1269=makeQuery(id+"F0.imprint","IMPRINT",FACE,{"disambiguationData":[TD([[makeQuery(id+"F0.imprint","IMPRINT",EDGE,{"disambiguationData":[TD([[subQ2,1.0]])],"derivedFrom":subQ1}),1.0]])]});}
            var Q1270;
            {var subQ0=sQuery(id+"F0.wireOp",EDGE,"E3.6.0.97");var subQ1=sQuery(id+"F0.wireOp",EDGE,"E3.6.0.44");var subQ2=makeQuery(id+"F0.imprint","INTERSECT",VERTEX,{"derivedFrom":[subQ1,subQ0]});Q1270=makeQuery(id+"F0.imprint","IMPRINT",FACE,{"disambiguationData":[TD([[makeQuery(id+"F0.imprint","IMPRINT",EDGE,{"disambiguationData":[TD([[subQ2,1.0]])],"derivedFrom":subQ1}),-1.0]])]});}
            var Q1271;
            {var subQ3=sQuery(id+"F0.wireOp",EDGE,"E3.6.0.85");Q1271=makeQuery(id+"F0.imprint","IMPRINT",FACE,{"disambiguationData":[TD([[makeQuery(id+"F0.imprint","IMPRINT",EDGE,{"derivedFrom":subQ3}),1.0]])]});}
            var Q1272;
            {var subQ3=sQuery(id+"F0.wireOp",EDGE,"E3.7.0.118");Q1272=makeQuery(id+"F0.imprint","IMPRINT",FACE,{"disambiguationData":[TD([[makeQuery(id+"F0.imprint","IMPRINT",EDGE,{"derivedFrom":subQ3}),1.0]])]});}
            var Q1273;
            {var subQ0=sQuery(id+"F0.wireOp",EDGE,"E3.7.0.41");var subQ1=sQuery(id+"F0.wireOp",EDGE,"E3.7.0.13");var subQ2=makeQuery(id+"F0.imprint","INTERSECT",VERTEX,{"derivedFrom":[subQ1,subQ0]});Q1273=makeQuery(id+"F0.imprint","IMPRINT",FACE,{"disambiguationData":[TD([[makeQuery(id+"F0.imprint","IMPRINT",EDGE,{"disambiguationData":[TD([[subQ2,-1.0]])],"derivedFrom":subQ1}),-1.0]])]});}
            var Q1274;
            {var subQ0=sQuery(id+"F0.wireOp",EDGE,"E3.9.0.71");var subQ1=sQuery(id+"F0.wireOp",EDGE,"E3.9.0.9");var subQ2=makeQuery(id+"F0.imprint","INTERSECT",VERTEX,{"derivedFrom":[subQ1,subQ0]});Q1274=makeQuery(id+"F0.imprint","IMPRINT",FACE,{"disambiguationData":[TD([[makeQuery(id+"F0.imprint","IMPRINT",EDGE,{"disambiguationData":[TD([[subQ2,1.0]])],"derivedFrom":subQ1}),-1.0]])]});}
            var Q1275;
            {var subQ3=sQuery(id+"F0.wireOp",EDGE,"E3.11.0.86");Q1275=makeQuery(id+"F0.imprint","IMPRINT",FACE,{"disambiguationData":[TD([[makeQuery(id+"F0.imprint","IMPRINT",EDGE,{"derivedFrom":subQ3}),1.0]])]});}
            var Q1276;
            {var subQ0=sQuery(id+"F0.wireOp",EDGE,"E3.2.0.63");Q1276=makeQuery(id+"F0.imprint","IMPRINT",FACE,{"disambiguationData":[TD([[makeQuery(id+"F0.imprint","IMPRINT",EDGE,{"derivedFrom":subQ0}),-1.0]])]});}
            var Q1277;
            {var subQ5=sQuery(id+"F0.wireOp",EDGE,"E3.4.0.22");Q1277=makeQuery(id+"F0.imprint","IMPRINT",FACE,{"disambiguationData":[TD([[makeQuery(id+"F0.imprint","IMPRINT",EDGE,{"derivedFrom":subQ5}),-1.0]])]});}
            var Q1278;
            {var subQ0=sQuery(id+"F0.wireOp",EDGE,"E3.6.0.68");var subQ1=sQuery(id+"F0.wireOp",EDGE,"E3.6.0.8");var subQ2=makeQuery(id+"F0.imprint","INTERSECT",VERTEX,{"derivedFrom":[subQ1,subQ0]});Q1278=makeQuery(id+"F0.imprint","IMPRINT",FACE,{"disambiguationData":[TD([[makeQuery(id+"F0.imprint","IMPRINT",EDGE,{"disambiguationData":[TD([[subQ2,1.0]])],"derivedFrom":subQ1}),-1.0]])]});}
            var Q1279;
            {var subQ0=sQuery(id+"F0.wireOp",EDGE,"E3.13.0.94");var subQ1=sQuery(id+"F0.wireOp",EDGE,"E3.13.0.42");var subQ2=makeQuery(id+"F0.imprint","INTERSECT",VERTEX,{"derivedFrom":[subQ1,subQ0]});Q1279=makeQuery(id+"F0.imprint","IMPRINT",FACE,{"disambiguationData":[TD([[makeQuery(id+"F0.imprint","IMPRINT",EDGE,{"disambiguationData":[TD([[subQ2,1.0]])],"derivedFrom":subQ1}),-1.0]])]});}
            var Q1280;
            {var subQ3=sQuery(id+"F0.wireOp",EDGE,"E3.15.0.85");Q1280=makeQuery(id+"F0.imprint","IMPRINT",FACE,{"disambiguationData":[TD([[makeQuery(id+"F0.imprint","IMPRINT",EDGE,{"derivedFrom":subQ3}),1.0]])]});}
            var Q1281;
            {var subQ3=sQuery(id+"F0.wireOp",EDGE,"E3.14.0.103");Q1281=makeQuery(id+"F0.imprint","IMPRINT",FACE,{"disambiguationData":[TD([[makeQuery(id+"F0.imprint","IMPRINT",EDGE,{"derivedFrom":subQ3}),1.0]])]});}
            var Q1282;
            {var subQ5=sQuery(id+"F0.wireOp",EDGE,"E3.14.0.93");Q1282=makeQuery(id+"F0.imprint","IMPRINT",FACE,{"disambiguationData":[TD([[makeQuery(id+"F0.imprint","IMPRINT",EDGE,{"derivedFrom":subQ5}),1.0]])]});}
            var Q1283;
            {var subQ0=sQuery(id+"F0.wireOp",EDGE,"E3.7.0.20");Q1283=makeQuery(id+"F0.imprint","IMPRINT",FACE,{"disambiguationData":[TD([[makeQuery(id+"F0.imprint","IMPRINT",EDGE,{"derivedFrom":subQ0}),-1.0]])]});}
            var Q1284;
            {var subQ0=sQuery(id+"F0.wireOp",EDGE,"E3.8.0.96");var subQ1=sQuery(id+"F0.wireOp",EDGE,"E3.8.0.39");var subQ2=makeQuery(id+"F0.imprint","INTERSECT",VERTEX,{"derivedFrom":[subQ1,subQ0]});Q1284=makeQuery(id+"F0.imprint","IMPRINT",FACE,{"disambiguationData":[TD([[makeQuery(id+"F0.imprint","IMPRINT",EDGE,{"disambiguationData":[TD([[subQ2,1.0]])],"derivedFrom":subQ1}),-1.0]])]});}
            var Q1285;
            {var subQ3=sQuery(id+"F0.wireOp",EDGE,"E3.10.0.84");Q1285=makeQuery(id+"F0.imprint","IMPRINT",FACE,{"disambiguationData":[TD([[makeQuery(id+"F0.imprint","IMPRINT",EDGE,{"derivedFrom":subQ3}),1.0]])]});}
            var Q1286;
            {var subQ3=sQuery(id+"F0.wireOp",EDGE,"E3.12.0.83");Q1286=makeQuery(id+"F0.imprint","IMPRINT",FACE,{"disambiguationData":[TD([[makeQuery(id+"F0.imprint","IMPRINT",EDGE,{"derivedFrom":subQ3}),1.0]])]});}
            var Q1287;
            {var subQ3=sQuery(id+"F0.wireOp",EDGE,"E3.11.0.53");Q1287=makeQuery(id+"F0.imprint","IMPRINT",FACE,{"disambiguationData":[TD([[makeQuery(id+"F0.imprint","IMPRINT",EDGE,{"derivedFrom":subQ3}),1.0]])]});}
            var Q1288;
            {var subQ0=sQuery(id+"F0.wireOp",EDGE,"E3.12.0.99");var subQ1=sQuery(id+"F0.wireOp",EDGE,"E3.12.0.49");var subQ2=makeQuery(id+"F0.imprint","INTERSECT",VERTEX,{"derivedFrom":[subQ1,subQ0]});Q1288=makeQuery(id+"F0.imprint","IMPRINT",FACE,{"disambiguationData":[TD([[makeQuery(id+"F0.imprint","IMPRINT",EDGE,{"disambiguationData":[TD([[subQ2,1.0]])],"derivedFrom":subQ1}),-1.0]])]});}
            var Q1289;
            {var subQ0=sQuery(id+"F0.wireOp",EDGE,"E3.12.0.116");Q1289=makeQuery(id+"F0.imprint","IMPRINT",FACE,{"disambiguationData":[TD([[makeQuery(id+"F0.imprint","IMPRINT",EDGE,{"derivedFrom":subQ0}),-1.0]])]});}
            var Q1290;
            {var subQ3=sQuery(id+"F0.wireOp",EDGE,"E3.2.0.54");Q1290=makeQuery(id+"F0.imprint","IMPRINT",FACE,{"disambiguationData":[TD([[makeQuery(id+"F0.imprint","IMPRINT",EDGE,{"derivedFrom":subQ3}),1.0]])]});}
            var Q1291;
            {var subQ0=sQuery(id+"F0.wireOp",EDGE,"E3.2.0.72");var subQ1=sQuery(id+"F0.wireOp",EDGE,"E3.2.0.10");var subQ2=makeQuery(id+"F0.imprint","INTERSECT",VERTEX,{"derivedFrom":[subQ1,subQ0]});Q1291=makeQuery(id+"F0.imprint","IMPRINT",FACE,{"disambiguationData":[TD([[makeQuery(id+"F0.imprint","IMPRINT",EDGE,{"disambiguationData":[TD([[subQ2,1.0]])],"derivedFrom":subQ1}),-1.0]])]});}
            var Q1292;
            {var subQ3=sQuery(id+"F0.wireOp",EDGE,"E3.7.0.82");Q1292=makeQuery(id+"F0.imprint","IMPRINT",FACE,{"disambiguationData":[TD([[makeQuery(id+"F0.imprint","IMPRINT",EDGE,{"derivedFrom":subQ3}),1.0]])]});}
            var Q1293;
            {var subQ3=sQuery(id+"F0.wireOp",EDGE,"E3.7.0.55");Q1293=makeQuery(id+"F0.imprint","IMPRINT",FACE,{"disambiguationData":[TD([[makeQuery(id+"F0.imprint","IMPRINT",EDGE,{"derivedFrom":subQ3}),1.0]])]});}
            var Q1294;
            {var subQ0=sQuery(id+"F0.wireOp",EDGE,"E3.16.0.20");Q1294=makeQuery(id+"F0.imprint","IMPRINT",FACE,{"disambiguationData":[TD([[makeQuery(id+"F0.imprint","IMPRINT",EDGE,{"derivedFrom":subQ0}),-1.0]])]});}
            var Q1295;
            {var subQ0=sQuery(id+"F0.wireOp",EDGE,"E3.9.0.19");Q1295=makeQuery(id+"F0.imprint","IMPRINT",FACE,{"disambiguationData":[TD([[makeQuery(id+"F0.imprint","IMPRINT",EDGE,{"derivedFrom":subQ0}),-1.0]])]});}
            var Q1296;
            {var subQ0=sQuery(id+"F0.wireOp",EDGE,"E3.10.0.96");var subQ1=sQuery(id+"F0.wireOp",EDGE,"E3.10.0.43");var subQ2=makeQuery(id+"F0.imprint","INTERSECT",VERTEX,{"derivedFrom":[subQ1,subQ0]});Q1296=makeQuery(id+"F0.imprint","IMPRINT",FACE,{"disambiguationData":[TD([[makeQuery(id+"F0.imprint","IMPRINT",EDGE,{"disambiguationData":[TD([[subQ2,1.0]])],"derivedFrom":subQ1}),-1.0]])]});}
            var Q1297;
            {var subQ3=sQuery(id+"F0.wireOp",EDGE,"E3.6.0.86");Q1297=makeQuery(id+"F0.imprint","IMPRINT",FACE,{"disambiguationData":[TD([[makeQuery(id+"F0.imprint","IMPRINT",EDGE,{"derivedFrom":subQ3}),1.0]])]});}
            var Q1298;
            {var subQ3=sQuery(id+"F0.wireOp",EDGE,"E3.13.0.53");Q1298=makeQuery(id+"F0.imprint","IMPRINT",FACE,{"disambiguationData":[TD([[makeQuery(id+"F0.imprint","IMPRINT",EDGE,{"derivedFrom":subQ3}),1.0]])]});}
            var Q1299;
            {var subQ3=sQuery(id+"F0.wireOp",EDGE,"E3.16.0.103");Q1299=makeQuery(id+"F0.imprint","IMPRINT",FACE,{"disambiguationData":[TD([[makeQuery(id+"F0.imprint","IMPRINT",EDGE,{"derivedFrom":subQ3}),1.0]])]});}
            var Q1300;
            {var subQ3=sQuery(id+"F0.wireOp",EDGE,"E3.14.0.83");Q1300=makeQuery(id+"F0.imprint","IMPRINT",FACE,{"disambiguationData":[TD([[makeQuery(id+"F0.imprint","IMPRINT",EDGE,{"derivedFrom":subQ3}),1.0]])]});}
            var Q1301;
            {var subQ0=sQuery(id+"F0.wireOp",EDGE,"E3.15.0.94");var subQ1=sQuery(id+"F0.wireOp",EDGE,"E3.15.0.42");var subQ2=makeQuery(id+"F0.imprint","INTERSECT",VERTEX,{"derivedFrom":[subQ1,subQ0]});Q1301=makeQuery(id+"F0.imprint","IMPRINT",FACE,{"disambiguationData":[TD([[makeQuery(id+"F0.imprint","IMPRINT",EDGE,{"disambiguationData":[TD([[subQ2,1.0]])],"derivedFrom":subQ1}),-1.0]])]});}
            var Q1302;
            {var subQ0=sQuery(id+"F0.wireOp",EDGE,"E3.15.0.69");var subQ1=sQuery(id+"F0.wireOp",EDGE,"E3.15.0.12");var subQ2=makeQuery(id+"F0.imprint","INTERSECT",VERTEX,{"derivedFrom":[subQ1,subQ0]});Q1302=makeQuery(id+"F0.imprint","IMPRINT",FACE,{"disambiguationData":[TD([[makeQuery(id+"F0.imprint","IMPRINT",EDGE,{"disambiguationData":[TD([[subQ2,1.0]])],"derivedFrom":subQ1}),-1.0]])]});}
            var Q1303;
            {var subQ0=sQuery(id+"F0.wireOp",EDGE,"E3.8.0.97");var subQ1=sQuery(id+"F0.wireOp",EDGE,"E3.8.0.40");var subQ2=makeQuery(id+"F0.imprint","INTERSECT",VERTEX,{"derivedFrom":[subQ1,subQ0]});Q1303=makeQuery(id+"F0.imprint","IMPRINT",FACE,{"disambiguationData":[TD([[makeQuery(id+"F0.imprint","IMPRINT",EDGE,{"disambiguationData":[TD([[subQ2,1.0]])],"derivedFrom":subQ1}),-1.0]])]});}
            var Q1304;
            {var subQ0=sQuery(id+"F0.wireOp",EDGE,"E3.11.0.72");var subQ1=sQuery(id+"F0.wireOp",EDGE,"E3.11.0.10");var subQ2=makeQuery(id+"F0.imprint","INTERSECT",VERTEX,{"derivedFrom":[subQ1,subQ0]});Q1304=makeQuery(id+"F0.imprint","IMPRINT",FACE,{"disambiguationData":[TD([[makeQuery(id+"F0.imprint","IMPRINT",EDGE,{"disambiguationData":[TD([[subQ2,1.0]])],"derivedFrom":subQ1}),-1.0]])]});}
            var Q1305;
            {var subQ0=sQuery(id+"F0.wireOp",EDGE,"E3.12.0.57");Q1305=makeQuery(id+"F0.imprint","IMPRINT",FACE,{"disambiguationData":[TD([[makeQuery(id+"F0.imprint","IMPRINT",EDGE,{"derivedFrom":subQ0}),-1.0]])]});}
            var Q1306;
            {var subQ0=sQuery(id+"F0.wireOp",EDGE,"E3.2.0.20");Q1306=makeQuery(id+"F0.imprint","IMPRINT",FACE,{"disambiguationData":[TD([[makeQuery(id+"F0.imprint","IMPRINT",EDGE,{"derivedFrom":subQ0}),-1.0]])]});}
            var Q1307;
            {var subQ3=sQuery(id+"F0.wireOp",EDGE,"E3.4.0.81");Q1307=makeQuery(id+"F0.imprint","IMPRINT",FACE,{"disambiguationData":[TD([[makeQuery(id+"F0.imprint","IMPRINT",EDGE,{"derivedFrom":subQ3}),1.0]])]});}
            var Q1308;
            {var subQ0=sQuery(id+"F0.wireOp",EDGE,"E3.3.0.96");var subQ1=sQuery(id+"F0.wireOp",EDGE,"E3.3.0.39");var subQ2=makeQuery(id+"F0.imprint","INTERSECT",VERTEX,{"derivedFrom":[subQ1,subQ0]});Q1308=makeQuery(id+"F0.imprint","IMPRINT",FACE,{"disambiguationData":[TD([[makeQuery(id+"F0.imprint","IMPRINT",EDGE,{"disambiguationData":[TD([[subQ2,1.0]])],"derivedFrom":subQ1}),-1.0]])]});}
            var Q1309;
            {var subQ3=sQuery(id+"F0.wireOp",EDGE,"E3.4.0.54");Q1309=makeQuery(id+"F0.imprint","IMPRINT",FACE,{"disambiguationData":[TD([[makeQuery(id+"F0.imprint","IMPRINT",EDGE,{"derivedFrom":subQ3}),1.0]])]});}
            var Q1310;
            {var subQ3=sQuery(id+"F0.wireOp",EDGE,"E3.7.0.83");Q1310=makeQuery(id+"F0.imprint","IMPRINT",FACE,{"disambiguationData":[TD([[makeQuery(id+"F0.imprint","IMPRINT",EDGE,{"derivedFrom":subQ3}),1.0]])]});}
            var Q1311;
            {var subQ3=sQuery(id+"F0.wireOp",EDGE,"E3.6.0.53");Q1311=makeQuery(id+"F0.imprint","IMPRINT",FACE,{"disambiguationData":[TD([[makeQuery(id+"F0.imprint","IMPRINT",EDGE,{"derivedFrom":subQ3}),1.0]])]});}
            var Q1312;
            {var subQ3=sQuery(id+"F0.wireOp",EDGE,"E3.9.0.82");Q1312=makeQuery(id+"F0.imprint","IMPRINT",FACE,{"disambiguationData":[TD([[makeQuery(id+"F0.imprint","IMPRINT",EDGE,{"derivedFrom":subQ3}),1.0]])]});}
            var Q1313;
            {var subQ3=sQuery(id+"F0.wireOp",EDGE,"E3.9.0.55");Q1313=makeQuery(id+"F0.imprint","IMPRINT",FACE,{"disambiguationData":[TD([[makeQuery(id+"F0.imprint","IMPRINT",EDGE,{"derivedFrom":subQ3}),1.0]])]});}
            var Q1314;
            {var subQ0=sQuery(id+"F0.wireOp",EDGE,"E3.14.0.100");var subQ1=sQuery(id+"F0.wireOp",EDGE,"E3.14.0.52");var subQ2=makeQuery(id+"F0.imprint","INTERSECT",VERTEX,{"derivedFrom":[subQ1,subQ0]});Q1314=makeQuery(id+"F0.imprint","IMPRINT",FACE,{"disambiguationData":[TD([[makeQuery(id+"F0.imprint","IMPRINT",EDGE,{"disambiguationData":[TD([[subQ2,1.0]])],"derivedFrom":subQ1}),-1.0]])]});}
            var Q1315;
            {var subQ0=sQuery(id+"F0.wireOp",EDGE,"E3.14.0.89");Q1315=makeQuery(id+"F0.imprint","IMPRINT",FACE,{"disambiguationData":[TD([[makeQuery(id+"F0.imprint","IMPRINT",EDGE,{"derivedFrom":subQ0}),-1.0]])]});}
            var Q1316;
            {var subQ5=sQuery(id+"F0.wireOp",EDGE,"E3.15.0.22");Q1316=makeQuery(id+"F0.imprint","IMPRINT",FACE,{"disambiguationData":[TD([[makeQuery(id+"F0.imprint","IMPRINT",EDGE,{"derivedFrom":subQ5}),-1.0]])]});}
            var Q1317;
            {var subQ0=sQuery(id+"F0.wireOp",EDGE,"E3.1.0.68");var subQ1=sQuery(id+"F0.wireOp",EDGE,"E3.1.0.8");var subQ2=makeQuery(id+"F0.imprint","INTERSECT",VERTEX,{"derivedFrom":[subQ1,subQ0]});Q1317=makeQuery(id+"F0.imprint","IMPRINT",FACE,{"disambiguationData":[TD([[makeQuery(id+"F0.imprint","IMPRINT",EDGE,{"disambiguationData":[TD([[subQ2,1.0]])],"derivedFrom":subQ1}),-1.0]])]});}
            var Q1318;
            {var subQ3=sQuery(id+"F0.wireOp",EDGE,"E3.13.0.54");Q1318=makeQuery(id+"F0.imprint","IMPRINT",FACE,{"disambiguationData":[TD([[makeQuery(id+"F0.imprint","IMPRINT",EDGE,{"derivedFrom":subQ3}),1.0]])]});}
            var Q1319;
            {var subQ0=sQuery(id+"F0.wireOp",EDGE,"E3.16.0.99");var subQ1=sQuery(id+"F0.wireOp",EDGE,"E3.16.0.49");var subQ2=makeQuery(id+"F0.imprint","INTERSECT",VERTEX,{"derivedFrom":[subQ1,subQ0]});Q1319=makeQuery(id+"F0.imprint","IMPRINT",FACE,{"disambiguationData":[TD([[makeQuery(id+"F0.imprint","IMPRINT",EDGE,{"disambiguationData":[TD([[subQ2,1.0]])],"derivedFrom":subQ1}),-1.0]])]});}
            var Q1320;
            {var subQ0=sQuery(id+"F0.wireOp",EDGE,"E3.10.0.97");var subQ1=sQuery(id+"F0.wireOp",EDGE,"E3.10.0.44");var subQ2=makeQuery(id+"F0.imprint","INTERSECT",VERTEX,{"derivedFrom":[subQ1,subQ0]});Q1320=makeQuery(id+"F0.imprint","IMPRINT",FACE,{"disambiguationData":[TD([[makeQuery(id+"F0.imprint","IMPRINT",EDGE,{"disambiguationData":[TD([[subQ2,1.0]])],"derivedFrom":subQ1}),-1.0]])]});}
            var Q1321;
            {var subQ3=sQuery(id+"F0.wireOp",EDGE,"E3.10.0.85");Q1321=makeQuery(id+"F0.imprint","IMPRINT",FACE,{"disambiguationData":[TD([[makeQuery(id+"F0.imprint","IMPRINT",EDGE,{"derivedFrom":subQ3}),1.0]])]});}
            var Q1322;
            {var subQ3=sQuery(id+"F0.wireOp",EDGE,"E3.11.0.118");Q1322=makeQuery(id+"F0.imprint","IMPRINT",FACE,{"disambiguationData":[TD([[makeQuery(id+"F0.imprint","IMPRINT",EDGE,{"derivedFrom":subQ3}),1.0]])]});}
            var Q1323;
            {var subQ0=sQuery(id+"F0.wireOp",EDGE,"E3.11.0.19");Q1323=makeQuery(id+"F0.imprint","IMPRINT",FACE,{"disambiguationData":[TD([[makeQuery(id+"F0.imprint","IMPRINT",EDGE,{"derivedFrom":subQ0}),-1.0]])]});}
            var Q1324;
            {var subQ0=sQuery(id+"F0.wireOp",EDGE,"E3.12.0.96");var subQ1=sQuery(id+"F0.wireOp",EDGE,"E3.12.0.43");var subQ2=makeQuery(id+"F0.imprint","INTERSECT",VERTEX,{"derivedFrom":[subQ1,subQ0]});Q1324=makeQuery(id+"F0.imprint","IMPRINT",FACE,{"disambiguationData":[TD([[makeQuery(id+"F0.imprint","IMPRINT",EDGE,{"disambiguationData":[TD([[subQ2,1.0]])],"derivedFrom":subQ1}),-1.0]])]});}
            var Q1325;
            {var subQ0=sQuery(id+"F0.wireOp",EDGE,"E3.12.0.51");var subQ1=sQuery(id+"F0.wireOp",EDGE,"E3.12.0.10");var subQ2=makeQuery(id+"F0.imprint","INTERSECT",VERTEX,{"derivedFrom":[subQ1,subQ0]});Q1325=makeQuery(id+"F0.imprint","IMPRINT",FACE,{"disambiguationData":[TD([[makeQuery(id+"F0.imprint","IMPRINT",EDGE,{"disambiguationData":[TD([[subQ2,-1.0]])],"derivedFrom":subQ1}),1.0]])]});}
            var Q1326;
            {var subQ0=sQuery(id+"F0.wireOp",EDGE,"E3.13.0.71");var subQ1=sQuery(id+"F0.wireOp",EDGE,"E3.13.0.9");var subQ2=makeQuery(id+"F0.imprint","INTERSECT",VERTEX,{"derivedFrom":[subQ1,subQ0]});Q1326=makeQuery(id+"F0.imprint","IMPRINT",FACE,{"disambiguationData":[TD([[makeQuery(id+"F0.imprint","IMPRINT",EDGE,{"disambiguationData":[TD([[subQ2,1.0]])],"derivedFrom":subQ1}),-1.0]])]});}
            var Q1327;
            {var subQ0=sQuery(id+"F0.wireOp",EDGE,"E3.4.0.41");var subQ1=sQuery(id+"F0.wireOp",EDGE,"E3.4.0.13");var subQ2=makeQuery(id+"F0.imprint","INTERSECT",VERTEX,{"derivedFrom":[subQ1,subQ0]});Q1327=makeQuery(id+"F0.imprint","IMPRINT",FACE,{"disambiguationData":[TD([[makeQuery(id+"F0.imprint","IMPRINT",EDGE,{"disambiguationData":[TD([[subQ2,-1.0]])],"derivedFrom":subQ1}),-1.0]])]});}
            var Q1328;
            {var subQ0=sQuery(id+"F0.wireOp",EDGE,"E3.6.0.71");var subQ1=sQuery(id+"F0.wireOp",EDGE,"E3.6.0.9");var subQ2=makeQuery(id+"F0.imprint","INTERSECT",VERTEX,{"derivedFrom":[subQ1,subQ0]});Q1328=makeQuery(id+"F0.imprint","IMPRINT",FACE,{"disambiguationData":[TD([[makeQuery(id+"F0.imprint","IMPRINT",EDGE,{"disambiguationData":[TD([[subQ2,1.0]])],"derivedFrom":subQ1}),-1.0]])]});}
            var Q1329;
            {var subQ0=sQuery(id+"F0.wireOp",EDGE,"E3.10.0.97");var subQ1=sQuery(id+"F0.wireOp",EDGE,"E3.10.0.40");var subQ2=makeQuery(id+"F0.imprint","INTERSECT",VERTEX,{"derivedFrom":[subQ1,subQ0]});Q1329=makeQuery(id+"F0.imprint","IMPRINT",FACE,{"disambiguationData":[TD([[makeQuery(id+"F0.imprint","IMPRINT",EDGE,{"disambiguationData":[TD([[subQ2,1.0]])],"derivedFrom":subQ1}),-1.0]])]});}
            var Q1330;
            {var subQ0=sQuery(id+"F0.wireOp",EDGE,"E3.10.0.39");var subQ1=sQuery(id+"F0.wireOp",EDGE,"E3.10.0.17");var subQ2=makeQuery(id+"F0.imprint","INTERSECT",VERTEX,{"derivedFrom":[subQ1,subQ0]});Q1330=makeQuery(id+"F0.imprint","IMPRINT",FACE,{"disambiguationData":[TD([[makeQuery(id+"F0.imprint","IMPRINT",EDGE,{"disambiguationData":[TD([[subQ2,-1.0]])],"derivedFrom":subQ1}),-1.0]])]});}
            var Q1331;
            {var subQ0=sQuery(id+"F0.wireOp",EDGE,"E3.10.0.68");var subQ1=sQuery(id+"F0.wireOp",EDGE,"E3.10.0.8");var subQ2=makeQuery(id+"F0.imprint","INTERSECT",VERTEX,{"derivedFrom":[subQ1,subQ0]});Q1331=makeQuery(id+"F0.imprint","IMPRINT",FACE,{"disambiguationData":[TD([[makeQuery(id+"F0.imprint","IMPRINT",EDGE,{"disambiguationData":[TD([[subQ2,1.0]])],"derivedFrom":subQ1}),-1.0]])]});}
            var Q1332;
            {var subQ3=sQuery(id+"F0.wireOp",EDGE,"E3.14.0.84");Q1332=makeQuery(id+"F0.imprint","IMPRINT",FACE,{"disambiguationData":[TD([[makeQuery(id+"F0.imprint","IMPRINT",EDGE,{"derivedFrom":subQ3}),1.0]])]});}
            var Q1333;
            {var subQ3=sQuery(id+"F0.wireOp",EDGE,"E3.16.0.83");Q1333=makeQuery(id+"F0.imprint","IMPRINT",FACE,{"disambiguationData":[TD([[makeQuery(id+"F0.imprint","IMPRINT",EDGE,{"derivedFrom":subQ3}),1.0]])]});}
            var Q1334;
            {var subQ3=sQuery(id+"F0.wireOp",EDGE,"E3.2.0.82");Q1334=makeQuery(id+"F0.imprint","IMPRINT",FACE,{"disambiguationData":[TD([[makeQuery(id+"F0.imprint","IMPRINT",EDGE,{"derivedFrom":subQ3}),1.0]])]});}
            var Q1335;
            {var subQ3=sQuery(id+"F0.wireOp",EDGE,"E3.2.0.55");Q1335=makeQuery(id+"F0.imprint","IMPRINT",FACE,{"disambiguationData":[TD([[makeQuery(id+"F0.imprint","IMPRINT",EDGE,{"derivedFrom":subQ3}),1.0]])]});}
            var Q1336;
            {var subQ3=sQuery(id+"F0.wireOp",EDGE,"E3.13.0.118");Q1336=makeQuery(id+"F0.imprint","IMPRINT",FACE,{"disambiguationData":[TD([[makeQuery(id+"F0.imprint","IMPRINT",EDGE,{"derivedFrom":subQ3}),1.0]])]});}
            var Q1337;
            {var subQ0=sQuery(id+"F0.wireOp",EDGE,"E3.16.0.100");var subQ1=sQuery(id+"F0.wireOp",EDGE,"E3.16.0.52");var subQ2=makeQuery(id+"F0.imprint","INTERSECT",VERTEX,{"derivedFrom":[subQ1,subQ0]});Q1337=makeQuery(id+"F0.imprint","IMPRINT",FACE,{"disambiguationData":[TD([[makeQuery(id+"F0.imprint","IMPRINT",EDGE,{"disambiguationData":[TD([[subQ2,1.0]])],"derivedFrom":subQ1}),-1.0]])]});}
            var Q1338;
            {var subQ0=sQuery(id+"F0.wireOp",EDGE,"E3.14.0.96");var subQ1=sQuery(id+"F0.wireOp",EDGE,"E3.14.0.43");var subQ2=makeQuery(id+"F0.imprint","INTERSECT",VERTEX,{"derivedFrom":[subQ1,subQ0]});Q1338=makeQuery(id+"F0.imprint","IMPRINT",FACE,{"disambiguationData":[TD([[makeQuery(id+"F0.imprint","IMPRINT",EDGE,{"disambiguationData":[TD([[subQ2,1.0]])],"derivedFrom":subQ1}),-1.0]])]});}
            var Q1339;
            {var subQ3=sQuery(id+"F0.wireOp",EDGE,"E3.12.0.65");Q1339=makeQuery(id+"F0.imprint","IMPRINT",FACE,{"disambiguationData":[TD([[makeQuery(id+"F0.imprint","IMPRINT",EDGE,{"derivedFrom":subQ3}),-1.0]])]});}
            var Q1340;
            {var subQ3=sQuery(id+"F0.wireOp",EDGE,"E3.6.0.81");Q1340=makeQuery(id+"F0.imprint","IMPRINT",FACE,{"disambiguationData":[TD([[makeQuery(id+"F0.imprint","IMPRINT",EDGE,{"derivedFrom":subQ3}),1.0]])]});}
            var Q1341;
            {var subQ3=sQuery(id+"F0.wireOp",EDGE,"E3.6.0.54");Q1341=makeQuery(id+"F0.imprint","IMPRINT",FACE,{"disambiguationData":[TD([[makeQuery(id+"F0.imprint","IMPRINT",EDGE,{"derivedFrom":subQ3}),1.0]])]});}
            var Q1342;
            {var subQ10=sQuery(id+"F0.wireOp",EDGE,"E3.8.0.93");Q1342=makeQuery(id+"F0.imprint","IMPRINT",FACE,{"disambiguationData":[TD([[makeQuery(id+"F0.imprint","IMPRINT",EDGE,{"derivedFrom":subQ10}),-1.0]])]});}
            var Q1343;
            {var subQ3=sQuery(id+"F0.wireOp",EDGE,"E3.8.0.53");Q1343=makeQuery(id+"F0.imprint","IMPRINT",FACE,{"disambiguationData":[TD([[makeQuery(id+"F0.imprint","IMPRINT",EDGE,{"derivedFrom":subQ3}),1.0]])]});}
            var Q1344;
            {var subQ5=sQuery(id+"F0.wireOp",EDGE,"E3.11.0.93");Q1344=makeQuery(id+"F0.imprint","IMPRINT",FACE,{"disambiguationData":[TD([[makeQuery(id+"F0.imprint","IMPRINT",EDGE,{"derivedFrom":subQ5}),1.0]])]});}
            var Q1345;
            {var subQ0=sQuery(id+"F0.wireOp",EDGE,"E3.15.0.71");var subQ1=sQuery(id+"F0.wireOp",EDGE,"E3.15.0.9");var subQ2=makeQuery(id+"F0.imprint","INTERSECT",VERTEX,{"derivedFrom":[subQ1,subQ0]});Q1345=makeQuery(id+"F0.imprint","IMPRINT",FACE,{"disambiguationData":[TD([[makeQuery(id+"F0.imprint","IMPRINT",EDGE,{"disambiguationData":[TD([[subQ2,1.0]])],"derivedFrom":subQ1}),-1.0]])]});}
            var Q1346;
            {var subQ0=sQuery(id+"F0.wireOp",EDGE,"E3.2.0.8");var subQ1=sQuery(id+"F0.wireOp",EDGE,"E3.2.0.6");var subQ2=makeQuery(id+"F0.imprint","INTERSECT",VERTEX,{"derivedFrom":[subQ1,subQ0]});Q1346=makeQuery(id+"F0.imprint","IMPRINT",FACE,{"disambiguationData":[TD([[makeQuery(id+"F0.imprint","IMPRINT",EDGE,{"disambiguationData":[TD([[subQ2,-1.0]])],"derivedFrom":subQ1}),-1.0]])]});}
            var Q1347;
            {var subQ0=sQuery(id+"F0.wireOp",EDGE,"E3.3.0.97");var subQ1=sQuery(id+"F0.wireOp",EDGE,"E3.3.0.40");var subQ2=makeQuery(id+"F0.imprint","INTERSECT",VERTEX,{"derivedFrom":[subQ1,subQ0]});Q1347=makeQuery(id+"F0.imprint","IMPRINT",FACE,{"disambiguationData":[TD([[makeQuery(id+"F0.imprint","IMPRINT",EDGE,{"disambiguationData":[TD([[subQ2,1.0]])],"derivedFrom":subQ1}),-1.0]])]});}
            var Q1348;
            {var subQ0=sQuery(id+"F0.wireOp",EDGE,"E3.14.0.96");var subQ1=sQuery(id+"F0.wireOp",EDGE,"E3.14.0.39");var subQ2=makeQuery(id+"F0.imprint","INTERSECT",VERTEX,{"derivedFrom":[subQ1,subQ0]});Q1348=makeQuery(id+"F0.imprint","IMPRINT",FACE,{"disambiguationData":[TD([[makeQuery(id+"F0.imprint","IMPRINT",EDGE,{"disambiguationData":[TD([[subQ2,1.0]])],"derivedFrom":subQ1}),-1.0]])]});}
            var Q1349;
            {var subQ5=sQuery(id+"F0.wireOp",EDGE,"E3.14.0.57");Q1349=makeQuery(id+"F0.imprint","IMPRINT",FACE,{"disambiguationData":[TD([[makeQuery(id+"F0.imprint","IMPRINT",EDGE,{"derivedFrom":subQ5}),1.0]])]});}
            var Q1350;
            {var subQ3=sQuery(id+"F0.wireOp",EDGE,"E3.10.0.86");Q1350=makeQuery(id+"F0.imprint","IMPRINT",FACE,{"disambiguationData":[TD([[makeQuery(id+"F0.imprint","IMPRINT",EDGE,{"derivedFrom":subQ3}),1.0]])]});}
            var Q1351;
            {var subQ0=sQuery(id+"F0.wireOp",EDGE,"E3.11.0.35");var subQ1=sQuery(id+"F0.wireOp",EDGE,"E3.11.0.32");var subQ2=makeQuery(id+"F0.imprint","INTERSECT",VERTEX,{"derivedFrom":[subQ1,subQ0]});Q1351=makeQuery(id+"F0.imprint","IMPRINT",FACE,{"disambiguationData":[TD([[makeQuery(id+"F0.imprint","IMPRINT",EDGE,{"disambiguationData":[TD([[subQ2,1.0]])],"derivedFrom":subQ1}),1.0]])]});}
            var Q1352;
            {var subQ0=sQuery(id+"F0.wireOp",EDGE,"E3.12.0.68");var subQ1=sQuery(id+"F0.wireOp",EDGE,"E3.12.0.8");var subQ2=makeQuery(id+"F0.imprint","INTERSECT",VERTEX,{"derivedFrom":[subQ1,subQ0]});Q1352=makeQuery(id+"F0.imprint","IMPRINT",FACE,{"disambiguationData":[TD([[makeQuery(id+"F0.imprint","IMPRINT",EDGE,{"disambiguationData":[TD([[subQ2,1.0]])],"derivedFrom":subQ1}),-1.0]])]});}
            var Q1353;
            {var subQ3=sQuery(id+"F0.wireOp",EDGE,"E3.16.0.84");Q1353=makeQuery(id+"F0.imprint","IMPRINT",FACE,{"disambiguationData":[TD([[makeQuery(id+"F0.imprint","IMPRINT",EDGE,{"derivedFrom":subQ3}),1.0]])]});}
            var Q1354;
            {var subQ3=sQuery(id+"F0.wireOp",EDGE,"E3.2.0.83");Q1354=makeQuery(id+"F0.imprint","IMPRINT",FACE,{"disambiguationData":[TD([[makeQuery(id+"F0.imprint","IMPRINT",EDGE,{"derivedFrom":subQ3}),1.0]])]});}
            var Q1355;
            {var subQ0=sQuery(id+"F0.wireOp",EDGE,"E3.2.0.99");var subQ1=sQuery(id+"F0.wireOp",EDGE,"E3.2.0.49");var subQ2=makeQuery(id+"F0.imprint","INTERSECT",VERTEX,{"derivedFrom":[subQ1,subQ0]});Q1355=makeQuery(id+"F0.imprint","IMPRINT",FACE,{"disambiguationData":[TD([[makeQuery(id+"F0.imprint","IMPRINT",EDGE,{"disambiguationData":[TD([[subQ2,1.0]])],"derivedFrom":subQ1}),-1.0]])]});}
            var Q1356;
            {var subQ3=sQuery(id+"F0.wireOp",EDGE,"E3.4.0.82");Q1356=makeQuery(id+"F0.imprint","IMPRINT",FACE,{"disambiguationData":[TD([[makeQuery(id+"F0.imprint","IMPRINT",EDGE,{"derivedFrom":subQ3}),1.0]])]});}
            var Q1357;
            {var subQ0=sQuery(id+"F0.wireOp",EDGE,"E3.5.0.97");var subQ1=sQuery(id+"F0.wireOp",EDGE,"E3.5.0.44");var subQ2=makeQuery(id+"F0.imprint","INTERSECT",VERTEX,{"derivedFrom":[subQ1,subQ0]});Q1357=makeQuery(id+"F0.imprint","IMPRINT",FACE,{"disambiguationData":[TD([[makeQuery(id+"F0.imprint","IMPRINT",EDGE,{"disambiguationData":[TD([[subQ2,1.0]])],"derivedFrom":subQ1}),-1.0]])]});}
            var Q1358;
            {var subQ3=sQuery(id+"F0.wireOp",EDGE,"E3.5.0.85");Q1358=makeQuery(id+"F0.imprint","IMPRINT",FACE,{"disambiguationData":[TD([[makeQuery(id+"F0.imprint","IMPRINT",EDGE,{"derivedFrom":subQ3}),1.0]])]});}
            var Q1359;
            {var subQ3=sQuery(id+"F0.wireOp",EDGE,"E3.4.0.103");Q1359=makeQuery(id+"F0.imprint","IMPRINT",FACE,{"disambiguationData":[TD([[makeQuery(id+"F0.imprint","IMPRINT",EDGE,{"derivedFrom":subQ3}),1.0]])]});}
            var Q1360;
            {var subQ3=sQuery(id+"F0.wireOp",EDGE,"E3.14.0.85");Q1360=makeQuery(id+"F0.imprint","IMPRINT",FACE,{"disambiguationData":[TD([[makeQuery(id+"F0.imprint","IMPRINT",EDGE,{"derivedFrom":subQ3}),1.0]])]});}
            var Q1361;
            {var subQ3=sQuery(id+"F0.wireOp",EDGE,"E3.15.0.118");Q1361=makeQuery(id+"F0.imprint","IMPRINT",FACE,{"disambiguationData":[TD([[makeQuery(id+"F0.imprint","IMPRINT",EDGE,{"derivedFrom":subQ3}),1.0]])]});}
            var Q1362;
            {var subQ3=sQuery(id+"F0.wireOp",EDGE,"E3.18.0.81");Q1362=makeQuery(id+"F0.imprint","IMPRINT",FACE,{"disambiguationData":[TD([[makeQuery(id+"F0.imprint","IMPRINT",EDGE,{"derivedFrom":subQ3}),1.0]])]});}
            var Q1363;
            {var subQ0=sQuery(id+"F0.wireOp",EDGE,"E3.6.0.20");Q1363=makeQuery(id+"F0.imprint","IMPRINT",FACE,{"disambiguationData":[TD([[makeQuery(id+"F0.imprint","IMPRINT",EDGE,{"derivedFrom":subQ0}),-1.0]])]});}
            var Q1364;
            {var subQ0=sQuery(id+"F0.wireOp",EDGE,"E3.8.0.72");var subQ1=sQuery(id+"F0.wireOp",EDGE,"E3.8.0.10");var subQ2=makeQuery(id+"F0.imprint","INTERSECT",VERTEX,{"derivedFrom":[subQ1,subQ0]});Q1364=makeQuery(id+"F0.imprint","IMPRINT",FACE,{"disambiguationData":[TD([[makeQuery(id+"F0.imprint","IMPRINT",EDGE,{"disambiguationData":[TD([[subQ2,1.0]])],"derivedFrom":subQ1}),-1.0]])]});}
            var Q1365;
            {var subQ3=sQuery(id+"F0.wireOp",EDGE,"E3.8.0.81");Q1365=makeQuery(id+"F0.imprint","IMPRINT",FACE,{"disambiguationData":[TD([[makeQuery(id+"F0.imprint","IMPRINT",EDGE,{"derivedFrom":subQ3}),1.0]])]});}
            var Q1366;
            {var subQ3=sQuery(id+"F0.wireOp",EDGE,"E3.9.0.84");Q1366=makeQuery(id+"F0.imprint","IMPRINT",FACE,{"disambiguationData":[TD([[makeQuery(id+"F0.imprint","IMPRINT",EDGE,{"derivedFrom":subQ3}),1.0]])]});}
            var Q1367;
            {var subQ3=sQuery(id+"F0.wireOp",EDGE,"E3.8.0.54");Q1367=makeQuery(id+"F0.imprint","IMPRINT",FACE,{"disambiguationData":[TD([[makeQuery(id+"F0.imprint","IMPRINT",EDGE,{"derivedFrom":subQ3}),1.0]])]});}
            var Q1368;
            {var subQ10=sQuery(id+"F0.wireOp",EDGE,"E3.10.0.93");Q1368=makeQuery(id+"F0.imprint","IMPRINT",FACE,{"disambiguationData":[TD([[makeQuery(id+"F0.imprint","IMPRINT",EDGE,{"derivedFrom":subQ10}),-1.0]])]});}
            var Q1369;
            {var subQ0=sQuery(id+"F0.wireOp",EDGE,"E3.11.0.99");var subQ1=sQuery(id+"F0.wireOp",EDGE,"E3.11.0.49");var subQ2=makeQuery(id+"F0.imprint","INTERSECT",VERTEX,{"derivedFrom":[subQ1,subQ0]});Q1369=makeQuery(id+"F0.imprint","IMPRINT",FACE,{"disambiguationData":[TD([[makeQuery(id+"F0.imprint","IMPRINT",EDGE,{"disambiguationData":[TD([[subQ2,1.0]])],"derivedFrom":subQ1}),-1.0]])]});}
            var Q1370;
            {var subQ0=sQuery(id+"F0.wireOp",EDGE,"E3.11.0.116");Q1370=makeQuery(id+"F0.imprint","IMPRINT",FACE,{"disambiguationData":[TD([[makeQuery(id+"F0.imprint","IMPRINT",EDGE,{"derivedFrom":subQ0}),-1.0]])]});}
            var Q1371;
            {var subQ3=sQuery(id+"F0.wireOp",EDGE,"E3.11.0.83");Q1371=makeQuery(id+"F0.imprint","IMPRINT",FACE,{"disambiguationData":[TD([[makeQuery(id+"F0.imprint","IMPRINT",EDGE,{"derivedFrom":subQ3}),1.0]])]});}
            var Q1372;
            {var subQ3=sQuery(id+"F0.wireOp",EDGE,"E3.13.0.55");Q1372=makeQuery(id+"F0.imprint","IMPRINT",FACE,{"disambiguationData":[TD([[makeQuery(id+"F0.imprint","IMPRINT",EDGE,{"derivedFrom":subQ3}),1.0]])]});}
            var Q1373;
            {var subQ5=sQuery(id+"F0.wireOp",EDGE,"E3.13.0.93");Q1373=makeQuery(id+"F0.imprint","IMPRINT",FACE,{"disambiguationData":[TD([[makeQuery(id+"F0.imprint","IMPRINT",EDGE,{"derivedFrom":subQ5}),1.0]])]});}
            var Q1374;
            {var subQ5=sQuery(id+"F0.wireOp",EDGE,"E3.2.0.56");Q1374=makeQuery(id+"F0.imprint","IMPRINT",FACE,{"disambiguationData":[TD([[makeQuery(id+"F0.imprint","IMPRINT",EDGE,{"derivedFrom":subQ5}),1.0]])]});}
            var Q1375;
            {var subQ0=sQuery(id+"F0.wireOp",EDGE,"E3.1.0.71");var subQ1=sQuery(id+"F0.wireOp",EDGE,"E3.1.0.9");var subQ2=makeQuery(id+"F0.imprint","INTERSECT",VERTEX,{"derivedFrom":[subQ1,subQ0]});Q1375=makeQuery(id+"F0.imprint","IMPRINT",FACE,{"disambiguationData":[TD([[makeQuery(id+"F0.imprint","IMPRINT",EDGE,{"disambiguationData":[TD([[subQ2,1.0]])],"derivedFrom":subQ1}),-1.0]])]});}
            var Q1376;
            {var subQ3=sQuery(id+"F0.wireOp",EDGE,"E3.18.0.54");Q1376=makeQuery(id+"F0.imprint","IMPRINT",FACE,{"disambiguationData":[TD([[makeQuery(id+"F0.imprint","IMPRINT",EDGE,{"derivedFrom":subQ3}),1.0]])]});}
            var Q1377;
            {var subQ3=sQuery(id+"F0.wireOp",EDGE,"E3.21.0.56");Q1377=makeQuery(id+"F0.imprint","IMPRINT",FACE,{"disambiguationData":[TD([[makeQuery(id+"F0.imprint","IMPRINT",EDGE,{"derivedFrom":subQ3}),-1.0]])]});}
            var Q1378;
            {var subQ3=sQuery(id+"F0.wireOp",EDGE,"E3.23.0.55");Q1378=makeQuery(id+"F0.imprint","IMPRINT",FACE,{"disambiguationData":[TD([[makeQuery(id+"F0.imprint","IMPRINT",EDGE,{"derivedFrom":subQ3}),1.0]])]});}
            var Q1379;
            {var subQ5=sQuery(id+"F0.wireOp",EDGE,"E3.23.0.93");Q1379=makeQuery(id+"F0.imprint","IMPRINT",FACE,{"disambiguationData":[TD([[makeQuery(id+"F0.imprint","IMPRINT",EDGE,{"derivedFrom":subQ5}),1.0]])]});}
            var Q1380;
            {var subQ3=sQuery(id+"F0.wireOp",EDGE,"E3.17.0.55");Q1380=makeQuery(id+"F0.imprint","IMPRINT",FACE,{"disambiguationData":[TD([[makeQuery(id+"F0.imprint","IMPRINT",EDGE,{"derivedFrom":subQ3}),1.0]])]});}
            var Q1381;
            {var subQ3=sQuery(id+"F0.wireOp",EDGE,"E3.17.0.82");Q1381=makeQuery(id+"F0.imprint","IMPRINT",FACE,{"disambiguationData":[TD([[makeQuery(id+"F0.imprint","IMPRINT",EDGE,{"derivedFrom":subQ3}),1.0]])]});}
            var Q1382;
            {var subQ3=sQuery(id+"F0.wireOp",EDGE,"E3.17.0.85");Q1382=makeQuery(id+"F0.imprint","IMPRINT",FACE,{"disambiguationData":[TD([[makeQuery(id+"F0.imprint","IMPRINT",EDGE,{"derivedFrom":subQ3}),1.0]])]});}
            var Q1383;
            {var subQ3=sQuery(id+"F0.wireOp",EDGE,"E3.17.0.103");Q1383=makeQuery(id+"F0.imprint","IMPRINT",FACE,{"disambiguationData":[TD([[makeQuery(id+"F0.imprint","IMPRINT",EDGE,{"derivedFrom":subQ3}),1.0]])]});}
            var Q1384;
            {var subQ5=sQuery(id+"F0.wireOp",EDGE,"E3.22.0.56");Q1384=makeQuery(id+"F0.imprint","IMPRINT",FACE,{"disambiguationData":[TD([[makeQuery(id+"F0.imprint","IMPRINT",EDGE,{"derivedFrom":subQ5}),1.0]])]});}
            var Q1385;
            {var subQ0=sQuery(id+"F0.wireOp",EDGE,"E3.21.0.63");Q1385=makeQuery(id+"F0.imprint","IMPRINT",FACE,{"disambiguationData":[TD([[makeQuery(id+"F0.imprint","IMPRINT",EDGE,{"derivedFrom":subQ0}),-1.0]])]});}
            var Q1386;
            {var subQ3=sQuery(id+"F0.wireOp",EDGE,"E3.22.0.86");Q1386=makeQuery(id+"F0.imprint","IMPRINT",FACE,{"disambiguationData":[TD([[makeQuery(id+"F0.imprint","IMPRINT",EDGE,{"derivedFrom":subQ3}),1.0]])]});}
            var Q1387;
            {var subQ0=sQuery(id+"F0.wireOp",EDGE,"E3.21.0.71");var subQ1=sQuery(id+"F0.wireOp",EDGE,"E3.21.0.9");var subQ2=makeQuery(id+"F0.imprint","INTERSECT",VERTEX,{"derivedFrom":[subQ1,subQ0]});Q1387=makeQuery(id+"F0.imprint","IMPRINT",FACE,{"disambiguationData":[TD([[makeQuery(id+"F0.imprint","IMPRINT",EDGE,{"disambiguationData":[TD([[subQ2,1.0]])],"derivedFrom":subQ1}),-1.0]])]});}
            var Q1388;
            {var subQ3=sQuery(id+"F0.wireOp",EDGE,"E3.20.0.81");Q1388=makeQuery(id+"F0.imprint","IMPRINT",FACE,{"disambiguationData":[TD([[makeQuery(id+"F0.imprint","IMPRINT",EDGE,{"derivedFrom":subQ3}),1.0]])]});}
            var Q1389;
            {var subQ5=sQuery(id+"F0.wireOp",EDGE,"E3.19.0.82");Q1389=makeQuery(id+"F0.imprint","IMPRINT",FACE,{"disambiguationData":[TD([[makeQuery(id+"F0.imprint","IMPRINT",EDGE,{"derivedFrom":subQ5}),-1.0]])]});}
            var Q1390;
            {var subQ3=sQuery(id+"F0.wireOp",EDGE,"E3.20.0.54");Q1390=makeQuery(id+"F0.imprint","IMPRINT",FACE,{"disambiguationData":[TD([[makeQuery(id+"F0.imprint","IMPRINT",EDGE,{"derivedFrom":subQ3}),1.0]])]});}
            var Q1391;
            {var subQ3=sQuery(id+"F0.wireOp",EDGE,"E3.22.0.53");Q1391=makeQuery(id+"F0.imprint","IMPRINT",FACE,{"disambiguationData":[TD([[makeQuery(id+"F0.imprint","IMPRINT",EDGE,{"derivedFrom":subQ3}),1.0]])]});}
            var Q1392;
            {var subQ0=sQuery(id+"F0.wireOp",EDGE,"E3.21.0.72");var subQ1=sQuery(id+"F0.wireOp",EDGE,"E3.21.0.10");var subQ2=makeQuery(id+"F0.imprint","INTERSECT",VERTEX,{"derivedFrom":[subQ1,subQ0]});Q1392=makeQuery(id+"F0.imprint","IMPRINT",FACE,{"disambiguationData":[TD([[makeQuery(id+"F0.imprint","IMPRINT",EDGE,{"disambiguationData":[TD([[subQ2,1.0]])],"derivedFrom":subQ1}),-1.0]])]});}
            var Q1393;
            {var subQ3=sQuery(id+"F0.wireOp",EDGE,"E3.23.0.83");Q1393=makeQuery(id+"F0.imprint","IMPRINT",FACE,{"disambiguationData":[TD([[makeQuery(id+"F0.imprint","IMPRINT",EDGE,{"derivedFrom":subQ3}),1.0]])]});}
            var Q1394;
            {var subQ0=sQuery(id+"F0.wireOp",EDGE,"E3.17.0.68");var subQ1=sQuery(id+"F0.wireOp",EDGE,"E3.17.0.8");var subQ2=makeQuery(id+"F0.imprint","INTERSECT",VERTEX,{"derivedFrom":[subQ1,subQ0]});Q1394=makeQuery(id+"F0.imprint","IMPRINT",FACE,{"disambiguationData":[TD([[makeQuery(id+"F0.imprint","IMPRINT",EDGE,{"disambiguationData":[TD([[subQ2,1.0]])],"derivedFrom":subQ1}),-1.0]])]});}
            var Q1395;
            {var subQ0=sQuery(id+"F0.wireOp",EDGE,"E3.23.0.89");Q1395=makeQuery(id+"F0.imprint","IMPRINT",FACE,{"disambiguationData":[TD([[makeQuery(id+"F0.imprint","IMPRINT",EDGE,{"derivedFrom":subQ0}),-1.0]])]});}
            var Q1396;
            {var subQ3=sQuery(id+"F0.wireOp",EDGE,"E3.24.0.86");Q1396=makeQuery(id+"F0.imprint","IMPRINT",FACE,{"disambiguationData":[TD([[makeQuery(id+"F0.imprint","IMPRINT",EDGE,{"derivedFrom":subQ3}),1.0]])]});}
            var Q1397;
            {var subQ0=sQuery(id+"F0.wireOp",EDGE,"E3.17.0.69");var subQ1=sQuery(id+"F0.wireOp",EDGE,"E3.17.0.12");var subQ2=makeQuery(id+"F0.imprint","INTERSECT",VERTEX,{"derivedFrom":[subQ1,subQ0]});Q1397=makeQuery(id+"F0.imprint","IMPRINT",FACE,{"disambiguationData":[TD([[makeQuery(id+"F0.imprint","IMPRINT",EDGE,{"disambiguationData":[TD([[subQ2,1.0]])],"derivedFrom":subQ1}),-1.0]])]});}
            var Q1398;
            {var subQ3=sQuery(id+"F0.wireOp",EDGE,"E3.18.0.82");Q1398=makeQuery(id+"F0.imprint","IMPRINT",FACE,{"disambiguationData":[TD([[makeQuery(id+"F0.imprint","IMPRINT",EDGE,{"derivedFrom":subQ3}),1.0]])]});}
            var Q1399;
            {var subQ0=sQuery(id+"F0.wireOp",EDGE,"E3.17.0.94");var subQ1=sQuery(id+"F0.wireOp",EDGE,"E3.17.0.42");var subQ2=makeQuery(id+"F0.imprint","INTERSECT",VERTEX,{"derivedFrom":[subQ1,subQ0]});Q1399=makeQuery(id+"F0.imprint","IMPRINT",FACE,{"disambiguationData":[TD([[makeQuery(id+"F0.imprint","IMPRINT",EDGE,{"disambiguationData":[TD([[subQ2,1.0]])],"derivedFrom":subQ1}),-1.0]])]});}
            var Q1400;
            {var subQ3=sQuery(id+"F0.wireOp",EDGE,"E3.18.0.103");Q1400=makeQuery(id+"F0.imprint","IMPRINT",FACE,{"disambiguationData":[TD([[makeQuery(id+"F0.imprint","IMPRINT",EDGE,{"derivedFrom":subQ3}),1.0]])]});}
            var Q1401;
            {var subQ0=sQuery(id+"F0.wireOp",EDGE,"E3.20.0.19");Q1401=makeQuery(id+"F0.imprint","IMPRINT",FACE,{"disambiguationData":[TD([[makeQuery(id+"F0.imprint","IMPRINT",EDGE,{"derivedFrom":subQ0}),-1.0]])]});}
            var Q1402;
            {var subQ0=sQuery(id+"F0.wireOp",EDGE,"E3.18.0.94");var subQ1=sQuery(id+"F0.wireOp",EDGE,"E3.18.0.42");var subQ2=makeQuery(id+"F0.imprint","INTERSECT",VERTEX,{"derivedFrom":[subQ1,subQ0]});Q1402=makeQuery(id+"F0.imprint","IMPRINT",FACE,{"disambiguationData":[TD([[makeQuery(id+"F0.imprint","IMPRINT",EDGE,{"disambiguationData":[TD([[subQ2,1.0]])],"derivedFrom":subQ1}),-1.0]])]});}
            var Q1403;
            {var subQ3=sQuery(id+"F0.wireOp",EDGE,"E3.20.0.7");Q1403=makeQuery(id+"F0.imprint","IMPRINT",FACE,{"disambiguationData":[TD([[makeQuery(id+"F0.imprint","IMPRINT",EDGE,{"derivedFrom":subQ3}),1.0]])]});}
            var Q1404;
            {var subQ3=sQuery(id+"F0.wireOp",EDGE,"E3.19.0.55");Q1404=makeQuery(id+"F0.imprint","IMPRINT",FACE,{"disambiguationData":[TD([[makeQuery(id+"F0.imprint","IMPRINT",EDGE,{"derivedFrom":subQ3}),1.0]])]});}
            var Q1405;
            {var subQ3=sQuery(id+"F0.wireOp",EDGE,"E3.20.0.118");Q1405=makeQuery(id+"F0.imprint","IMPRINT",FACE,{"disambiguationData":[TD([[makeQuery(id+"F0.imprint","IMPRINT",EDGE,{"derivedFrom":subQ3}),1.0]])]});}
            var Q1406;
            {var subQ3=sQuery(id+"F0.wireOp",EDGE,"E3.21.0.53");Q1406=makeQuery(id+"F0.imprint","IMPRINT",FACE,{"disambiguationData":[TD([[makeQuery(id+"F0.imprint","IMPRINT",EDGE,{"derivedFrom":subQ3}),1.0]])]});}
            var Q1407;
            {var subQ3=sQuery(id+"F0.wireOp",EDGE,"E3.23.0.66");Q1407=makeQuery(id+"F0.imprint","IMPRINT",FACE,{"disambiguationData":[TD([[makeQuery(id+"F0.imprint","IMPRINT",EDGE,{"derivedFrom":subQ3}),-1.0]])]});}
            var Q1408;
            {var subQ0=sQuery(id+"F0.wireOp",EDGE,"E3.22.0.99");var subQ1=sQuery(id+"F0.wireOp",EDGE,"E3.22.0.49");var subQ2=makeQuery(id+"F0.imprint","INTERSECT",VERTEX,{"derivedFrom":[subQ1,subQ0]});Q1408=makeQuery(id+"F0.imprint","IMPRINT",FACE,{"disambiguationData":[TD([[makeQuery(id+"F0.imprint","IMPRINT",EDGE,{"disambiguationData":[TD([[subQ2,1.0]])],"derivedFrom":subQ1}),-1.0]])]});}
            var Q1409;
            {var subQ3=sQuery(id+"F0.wireOp",EDGE,"E3.24.0.55");Q1409=makeQuery(id+"F0.imprint","IMPRINT",FACE,{"disambiguationData":[TD([[makeQuery(id+"F0.imprint","IMPRINT",EDGE,{"derivedFrom":subQ3}),1.0]])]});}
            var Q1410;
            {var subQ3=sQuery(id+"F0.wireOp",EDGE,"E3.19.0.54");Q1410=makeQuery(id+"F0.imprint","IMPRINT",FACE,{"disambiguationData":[TD([[makeQuery(id+"F0.imprint","IMPRINT",EDGE,{"derivedFrom":subQ3}),1.0]])]});}
            var Q1411;
            {var subQ3=sQuery(id+"F0.wireOp",EDGE,"E3.23.0.54");Q1411=makeQuery(id+"F0.imprint","IMPRINT",FACE,{"disambiguationData":[TD([[makeQuery(id+"F0.imprint","IMPRINT",EDGE,{"derivedFrom":subQ3}),1.0]])]});}
            var Q1412;
            {var subQ5=sQuery(id+"F0.wireOp",EDGE,"E3.17.0.22");Q1412=makeQuery(id+"F0.imprint","IMPRINT",FACE,{"disambiguationData":[TD([[makeQuery(id+"F0.imprint","IMPRINT",EDGE,{"derivedFrom":subQ5}),-1.0]])]});}
            var Q1413;
            {var subQ5=sQuery(id+"F0.wireOp",EDGE,"E3.17.0.56");Q1413=makeQuery(id+"F0.imprint","IMPRINT",FACE,{"disambiguationData":[TD([[makeQuery(id+"F0.imprint","IMPRINT",EDGE,{"derivedFrom":subQ5}),1.0]])]});}
            var Q1414;
            {var subQ0=sQuery(id+"F0.wireOp",EDGE,"E3.17.0.89");Q1414=makeQuery(id+"F0.imprint","IMPRINT",FACE,{"disambiguationData":[TD([[makeQuery(id+"F0.imprint","IMPRINT",EDGE,{"derivedFrom":subQ0}),-1.0]])]});}
            var Q1415;
            {var subQ0=sQuery(id+"F0.wireOp",EDGE,"E3.17.0.100");var subQ1=sQuery(id+"F0.wireOp",EDGE,"E3.17.0.52");var subQ2=makeQuery(id+"F0.imprint","INTERSECT",VERTEX,{"derivedFrom":[subQ1,subQ0]});Q1415=makeQuery(id+"F0.imprint","IMPRINT",FACE,{"disambiguationData":[TD([[makeQuery(id+"F0.imprint","IMPRINT",EDGE,{"disambiguationData":[TD([[subQ2,1.0]])],"derivedFrom":subQ1}),-1.0]])]});}
            var Q1416;
            {var subQ0=sQuery(id+"F0.wireOp",EDGE,"E3.20.0.20");Q1416=makeQuery(id+"F0.imprint","IMPRINT",FACE,{"disambiguationData":[TD([[makeQuery(id+"F0.imprint","IMPRINT",EDGE,{"derivedFrom":subQ0}),-1.0]])]});}
            var Q1417;
            {var subQ0=sQuery(id+"F0.wireOp",EDGE,"E3.20.0.97");var subQ1=sQuery(id+"F0.wireOp",EDGE,"E3.20.0.40");var subQ2=makeQuery(id+"F0.imprint","INTERSECT",VERTEX,{"derivedFrom":[subQ1,subQ0]});Q1417=makeQuery(id+"F0.imprint","IMPRINT",FACE,{"disambiguationData":[TD([[makeQuery(id+"F0.imprint","IMPRINT",EDGE,{"disambiguationData":[TD([[subQ2,1.0]])],"derivedFrom":subQ1}),-1.0]])]});}
            var Q1418;
            {var subQ0=sQuery(id+"F0.wireOp",EDGE,"E3.19.0.75");var subQ1=sQuery(id+"F0.wireOp",EDGE,"E3.19.0.52");var subQ2=makeQuery(id+"F0.imprint","INTERSECT",VERTEX,{"derivedFrom":[subQ1,subQ0]});Q1418=makeQuery(id+"F0.imprint","IMPRINT",FACE,{"disambiguationData":[TD([[makeQuery(id+"F0.imprint","IMPRINT",EDGE,{"disambiguationData":[TD([[subQ2,-1.0]])],"derivedFrom":subQ1}),-1.0]])]});}
            var Q1419;
            {var subQ5=sQuery(id+"F0.wireOp",EDGE,"E3.21.0.57");Q1419=makeQuery(id+"F0.imprint","IMPRINT",FACE,{"disambiguationData":[TD([[makeQuery(id+"F0.imprint","IMPRINT",EDGE,{"derivedFrom":subQ5}),1.0]])]});}
            var Q1420;
            {var subQ0=sQuery(id+"F0.wireOp",EDGE,"E3.21.0.20");Q1420=makeQuery(id+"F0.imprint","IMPRINT",FACE,{"disambiguationData":[TD([[makeQuery(id+"F0.imprint","IMPRINT",EDGE,{"derivedFrom":subQ0}),-1.0]])]});}
            var Q1421;
            {var subQ0=sQuery(id+"F0.wireOp",EDGE,"E3.23.0.41");var subQ1=sQuery(id+"F0.wireOp",EDGE,"E3.23.0.6");var subQ2=makeQuery(id+"F0.imprint","INTERSECT",VERTEX,{"derivedFrom":[subQ1,subQ0]});Q1421=makeQuery(id+"F0.imprint","IMPRINT",FACE,{"disambiguationData":[TD([[makeQuery(id+"F0.imprint","IMPRINT",EDGE,{"disambiguationData":[TD([[subQ2,1.0]])],"derivedFrom":subQ1}),-1.0]])]});}
            var Q1422;
            {var subQ3=sQuery(id+"F0.wireOp",EDGE,"E3.23.0.81");Q1422=makeQuery(id+"F0.imprint","IMPRINT",FACE,{"disambiguationData":[TD([[makeQuery(id+"F0.imprint","IMPRINT",EDGE,{"derivedFrom":subQ3}),1.0]])]});}
            var Q1423;
            {var subQ7=sQuery(id+"F0.wireOp",EDGE,"E3.17.0.87");Q1423=makeQuery(id+"F0.imprint","IMPRINT",FACE,{"disambiguationData":[TD([[makeQuery(id+"F0.imprint","IMPRINT",EDGE,{"derivedFrom":subQ7}),-1.0]])]});}
            var Q1424;
            {var subQ3=sQuery(id+"F0.wireOp",EDGE,"E3.17.0.81");Q1424=makeQuery(id+"F0.imprint","IMPRINT",FACE,{"disambiguationData":[TD([[makeQuery(id+"F0.imprint","IMPRINT",EDGE,{"derivedFrom":subQ3}),1.0]])]});}
            var Q1425;
            {var subQ0=sQuery(id+"F0.wireOp",EDGE,"E3.17.0.71");var subQ1=sQuery(id+"F0.wireOp",EDGE,"E3.17.0.9");var subQ2=makeQuery(id+"F0.imprint","INTERSECT",VERTEX,{"derivedFrom":[subQ1,subQ0]});Q1425=makeQuery(id+"F0.imprint","IMPRINT",FACE,{"disambiguationData":[TD([[makeQuery(id+"F0.imprint","IMPRINT",EDGE,{"disambiguationData":[TD([[subQ2,1.0]])],"derivedFrom":subQ1}),-1.0]])]});}
            var Q1426;
            {var subQ0=sQuery(id+"F0.wireOp",EDGE,"E3.22.0.97");var subQ1=sQuery(id+"F0.wireOp",EDGE,"E3.22.0.40");var subQ2=makeQuery(id+"F0.imprint","INTERSECT",VERTEX,{"derivedFrom":[subQ1,subQ0]});Q1426=makeQuery(id+"F0.imprint","IMPRINT",FACE,{"disambiguationData":[TD([[makeQuery(id+"F0.imprint","IMPRINT",EDGE,{"disambiguationData":[TD([[subQ2,1.0]])],"derivedFrom":subQ1}),-1.0]])]});}
            var Q1427;
            {var subQ0=sQuery(id+"F0.wireOp",EDGE,"E3.2.0.41");var subQ1=sQuery(id+"F0.wireOp",EDGE,"E3.2.0.6");var subQ2=makeQuery(id+"F0.imprint","INTERSECT",VERTEX,{"derivedFrom":[subQ1,subQ0]});Q1427=makeQuery(id+"F0.imprint","IMPRINT",FACE,{"disambiguationData":[TD([[makeQuery(id+"F0.imprint","IMPRINT",EDGE,{"disambiguationData":[TD([[subQ2,1.0]])],"derivedFrom":subQ1}),-1.0]])]});}
            var Q1428;
            {var subQ0=sQuery(id+"F0.wireOp",EDGE,"E3.10.0.71");var subQ1=sQuery(id+"F0.wireOp",EDGE,"E3.10.0.9");var subQ2=makeQuery(id+"F0.imprint","INTERSECT",VERTEX,{"derivedFrom":[subQ1,subQ0]});Q1428=makeQuery(id+"F0.imprint","IMPRINT",FACE,{"disambiguationData":[TD([[makeQuery(id+"F0.imprint","IMPRINT",EDGE,{"disambiguationData":[TD([[subQ2,1.0]])],"derivedFrom":subQ1}),-1.0]])]});}
            var Q1429;
            {var subQ0=sQuery(id+"F0.wireOp",EDGE,"E3.11.0.100");var subQ1=sQuery(id+"F0.wireOp",EDGE,"E3.11.0.52");var subQ2=makeQuery(id+"F0.imprint","INTERSECT",VERTEX,{"derivedFrom":[subQ1,subQ0]});Q1429=makeQuery(id+"F0.imprint","IMPRINT",FACE,{"disambiguationData":[TD([[makeQuery(id+"F0.imprint","IMPRINT",EDGE,{"disambiguationData":[TD([[subQ2,1.0]])],"derivedFrom":subQ1}),-1.0]])]});}
            var Q1430;
            {var subQ3=sQuery(id+"F0.wireOp",EDGE,"E3.15.0.83");Q1430=makeQuery(id+"F0.imprint","IMPRINT",FACE,{"disambiguationData":[TD([[makeQuery(id+"F0.imprint","IMPRINT",EDGE,{"derivedFrom":subQ3}),1.0]])]});}
            var Q1431;
            {var subQ0=sQuery(id+"F0.wireOp",EDGE,"E3.15.0.99");var subQ1=sQuery(id+"F0.wireOp",EDGE,"E3.15.0.49");var subQ2=makeQuery(id+"F0.imprint","INTERSECT",VERTEX,{"derivedFrom":[subQ1,subQ0]});Q1431=makeQuery(id+"F0.imprint","IMPRINT",FACE,{"disambiguationData":[TD([[makeQuery(id+"F0.imprint","IMPRINT",EDGE,{"disambiguationData":[TD([[subQ2,1.0]])],"derivedFrom":subQ1}),-1.0]])]});}
            var Q1432;
            {var subQ0=sQuery(id+"F0.wireOp",EDGE,"E3.9.0.68");var subQ1=sQuery(id+"F0.wireOp",EDGE,"E3.9.0.8");var subQ2=makeQuery(id+"F0.imprint","INTERSECT",VERTEX,{"derivedFrom":[subQ1,subQ0]});Q1432=makeQuery(id+"F0.imprint","IMPRINT",FACE,{"disambiguationData":[TD([[makeQuery(id+"F0.imprint","IMPRINT",EDGE,{"disambiguationData":[TD([[subQ2,1.0]])],"derivedFrom":subQ1}),-1.0]])]});}
            var Q1433;
            {var subQ5=sQuery(id+"F0.wireOp",EDGE,"E3.10.0.93");Q1433=makeQuery(id+"F0.imprint","IMPRINT",FACE,{"disambiguationData":[TD([[makeQuery(id+"F0.imprint","IMPRINT",EDGE,{"derivedFrom":subQ5}),1.0]])]});}
            var Q1434;
            {var subQ3=sQuery(id+"F0.wireOp",EDGE,"E3.11.0.85");Q1434=makeQuery(id+"F0.imprint","IMPRINT",FACE,{"disambiguationData":[TD([[makeQuery(id+"F0.imprint","IMPRINT",EDGE,{"derivedFrom":subQ3}),1.0]])]});}
            var Q1435;
            {var subQ5=sQuery(id+"F0.wireOp",EDGE,"E3.4.0.57");Q1435=makeQuery(id+"F0.imprint","IMPRINT",FACE,{"disambiguationData":[TD([[makeQuery(id+"F0.imprint","IMPRINT",EDGE,{"derivedFrom":subQ5}),1.0]])]});}
            var Q1436;
            {var subQ3=sQuery(id+"F0.wireOp",EDGE,"E3.5.0.81");Q1436=makeQuery(id+"F0.imprint","IMPRINT",FACE,{"disambiguationData":[TD([[makeQuery(id+"F0.imprint","IMPRINT",EDGE,{"derivedFrom":subQ3}),1.0]])]});}
            var Q1437;
            {var subQ3=sQuery(id+"F0.wireOp",EDGE,"E3.14.0.54");Q1437=makeQuery(id+"F0.imprint","IMPRINT",FACE,{"disambiguationData":[TD([[makeQuery(id+"F0.imprint","IMPRINT",EDGE,{"derivedFrom":subQ3}),1.0]])]});}
            var Q1438;
            {var subQ5=sQuery(id+"F0.wireOp",EDGE,"E3.13.0.57");Q1438=makeQuery(id+"F0.imprint","IMPRINT",FACE,{"disambiguationData":[TD([[makeQuery(id+"F0.imprint","IMPRINT",EDGE,{"derivedFrom":subQ5}),1.0]])]});}
            var Q1439;
            {var subQ3=sQuery(id+"F0.wireOp",EDGE,"E3.12.0.82");Q1439=makeQuery(id+"F0.imprint","IMPRINT",FACE,{"disambiguationData":[TD([[makeQuery(id+"F0.imprint","IMPRINT",EDGE,{"derivedFrom":subQ3}),1.0]])]});}
            var Q1440;
            {var subQ3=sQuery(id+"F0.wireOp",EDGE,"E3.13.0.85");Q1440=makeQuery(id+"F0.imprint","IMPRINT",FACE,{"disambiguationData":[TD([[makeQuery(id+"F0.imprint","IMPRINT",EDGE,{"derivedFrom":subQ3}),1.0]])]});}
            var Q1441;
            {var subQ0=sQuery(id+"F0.wireOp",EDGE,"E3.5.0.20");Q1441=makeQuery(id+"F0.imprint","IMPRINT",FACE,{"disambiguationData":[TD([[makeQuery(id+"F0.imprint","IMPRINT",EDGE,{"derivedFrom":subQ0}),-1.0]])]});}
            var Q1442;
            {var subQ0=sQuery(id+"F0.wireOp",EDGE,"E3.10.0.89");Q1442=makeQuery(id+"F0.imprint","IMPRINT",FACE,{"disambiguationData":[TD([[makeQuery(id+"F0.imprint","IMPRINT",EDGE,{"derivedFrom":subQ0}),-1.0]])]});}
            var Q1443;
            {var subQ0=sQuery(id+"F0.wireOp",EDGE,"E3.6.0.97");var subQ1=sQuery(id+"F0.wireOp",EDGE,"E3.6.0.40");var subQ2=makeQuery(id+"F0.imprint","INTERSECT",VERTEX,{"derivedFrom":[subQ1,subQ0]});Q1443=makeQuery(id+"F0.imprint","IMPRINT",FACE,{"disambiguationData":[TD([[makeQuery(id+"F0.imprint","IMPRINT",EDGE,{"disambiguationData":[TD([[subQ2,1.0]])],"derivedFrom":subQ1}),-1.0]])]});}
            var Q1444;
            {var subQ3=sQuery(id+"F0.wireOp",EDGE,"E3.2.0.81");Q1444=makeQuery(id+"F0.imprint","IMPRINT",FACE,{"disambiguationData":[TD([[makeQuery(id+"F0.imprint","IMPRINT",EDGE,{"derivedFrom":subQ3}),1.0]])]});}
            var Q1445;
            {var subQ0=sQuery(id+"F0.wireOp",EDGE,"E3.12.0.89");Q1445=makeQuery(id+"F0.imprint","IMPRINT",FACE,{"disambiguationData":[TD([[makeQuery(id+"F0.imprint","IMPRINT",EDGE,{"derivedFrom":subQ0}),-1.0]])]});}
            var Q1446;
            {var subQ5=sQuery(id+"F0.wireOp",EDGE,"E3.5.0.56");Q1446=makeQuery(id+"F0.imprint","IMPRINT",FACE,{"disambiguationData":[TD([[makeQuery(id+"F0.imprint","IMPRINT",EDGE,{"derivedFrom":subQ5}),1.0]])]});}
            var Q1447;
            {var subQ0=sQuery(id+"F0.wireOp",EDGE,"E3.8.0.68");var subQ1=sQuery(id+"F0.wireOp",EDGE,"E3.8.0.8");var subQ2=makeQuery(id+"F0.imprint","INTERSECT",VERTEX,{"derivedFrom":[subQ1,subQ0]});Q1447=makeQuery(id+"F0.imprint","IMPRINT",FACE,{"disambiguationData":[TD([[makeQuery(id+"F0.imprint","IMPRINT",EDGE,{"disambiguationData":[TD([[subQ2,1.0]])],"derivedFrom":subQ1}),-1.0]])]});}
            var Q1448;
            {var subQ0=sQuery(id+"F0.wireOp",EDGE,"E3.10.0.96");var subQ1=sQuery(id+"F0.wireOp",EDGE,"E3.10.0.39");var subQ2=makeQuery(id+"F0.imprint","INTERSECT",VERTEX,{"derivedFrom":[subQ1,subQ0]});Q1448=makeQuery(id+"F0.imprint","IMPRINT",FACE,{"disambiguationData":[TD([[makeQuery(id+"F0.imprint","IMPRINT",EDGE,{"disambiguationData":[TD([[subQ2,1.0]])],"derivedFrom":subQ1}),-1.0]])]});}
            var Q1449;
            {var subQ0=sQuery(id+"F0.wireOp",EDGE,"E3.5.0.41");var subQ1=sQuery(id+"F0.wireOp",EDGE,"E3.5.0.6");var subQ2=makeQuery(id+"F0.imprint","INTERSECT",VERTEX,{"derivedFrom":[subQ1,subQ0]});Q1449=makeQuery(id+"F0.imprint","IMPRINT",FACE,{"disambiguationData":[TD([[makeQuery(id+"F0.imprint","IMPRINT",EDGE,{"disambiguationData":[TD([[subQ2,1.0]])],"derivedFrom":subQ1}),-1.0]])]});}
            var Q1450;
            {var subQ5=sQuery(id+"F0.wireOp",EDGE,"E3.9.0.93");Q1450=makeQuery(id+"F0.imprint","IMPRINT",FACE,{"disambiguationData":[TD([[makeQuery(id+"F0.imprint","IMPRINT",EDGE,{"derivedFrom":subQ5}),1.0]])]});}
            var Q1451;
            {var subQ3=sQuery(id+"F0.wireOp",EDGE,"E3.8.0.86");Q1451=makeQuery(id+"F0.imprint","IMPRINT",FACE,{"disambiguationData":[TD([[makeQuery(id+"F0.imprint","IMPRINT",EDGE,{"derivedFrom":subQ3}),1.0]])]});}
            var Q1452;
            {var subQ0=sQuery(id+"F0.wireOp",EDGE,"E3.9.0.35");var subQ1=sQuery(id+"F0.wireOp",EDGE,"E3.9.0.32");var subQ2=makeQuery(id+"F0.imprint","INTERSECT",VERTEX,{"derivedFrom":[subQ1,subQ0]});Q1452=makeQuery(id+"F0.imprint","IMPRINT",FACE,{"disambiguationData":[TD([[makeQuery(id+"F0.imprint","IMPRINT",EDGE,{"disambiguationData":[TD([[subQ2,1.0]])],"derivedFrom":subQ1}),1.0]])]});}
            var Q1453;
            {var subQ0=sQuery(id+"F0.wireOp",EDGE,"E3.12.0.96");var subQ1=sQuery(id+"F0.wireOp",EDGE,"E3.12.0.39");var subQ2=makeQuery(id+"F0.imprint","INTERSECT",VERTEX,{"derivedFrom":[subQ1,subQ0]});Q1453=makeQuery(id+"F0.imprint","IMPRINT",FACE,{"disambiguationData":[TD([[makeQuery(id+"F0.imprint","IMPRINT",EDGE,{"disambiguationData":[TD([[subQ2,1.0]])],"derivedFrom":subQ1}),-1.0]])]});}
            var Q1454;
            {var subQ5=sQuery(id+"F0.wireOp",EDGE,"E3.12.0.57");Q1454=makeQuery(id+"F0.imprint","IMPRINT",FACE,{"disambiguationData":[TD([[makeQuery(id+"F0.imprint","IMPRINT",EDGE,{"derivedFrom":subQ5}),1.0]])]});}
            var Q1455;
            {var subQ0=sQuery(id+"F0.wireOp",EDGE,"E3.13.0.72");var subQ1=sQuery(id+"F0.wireOp",EDGE,"E3.13.0.10");var subQ2=makeQuery(id+"F0.imprint","INTERSECT",VERTEX,{"derivedFrom":[subQ1,subQ0]});Q1455=makeQuery(id+"F0.imprint","IMPRINT",FACE,{"disambiguationData":[TD([[makeQuery(id+"F0.imprint","IMPRINT",EDGE,{"disambiguationData":[TD([[subQ2,1.0]])],"derivedFrom":subQ1}),-1.0]])]});}
            var Q1456;
            {var subQ0=sQuery(id+"F0.wireOp",EDGE,"E3.5.0.96");var subQ1=sQuery(id+"F0.wireOp",EDGE,"E3.5.0.39");var subQ2=makeQuery(id+"F0.imprint","INTERSECT",VERTEX,{"derivedFrom":[subQ1,subQ0]});Q1456=makeQuery(id+"F0.imprint","IMPRINT",FACE,{"disambiguationData":[TD([[makeQuery(id+"F0.imprint","IMPRINT",EDGE,{"disambiguationData":[TD([[subQ2,1.0]])],"derivedFrom":subQ1}),-1.0]])]});}
            var Q1457;
            {var subQ0=sQuery(id+"F0.wireOp",EDGE,"E3.4.0.20");Q1457=makeQuery(id+"F0.imprint","IMPRINT",FACE,{"disambiguationData":[TD([[makeQuery(id+"F0.imprint","IMPRINT",EDGE,{"derivedFrom":subQ0}),-1.0]])]});}
            var Q1458;
            {var subQ0=sQuery(id+"F0.wireOp",EDGE,"E3.16.0.41");var subQ1=sQuery(id+"F0.wireOp",EDGE,"E3.16.0.6");var subQ2=makeQuery(id+"F0.imprint","INTERSECT",VERTEX,{"derivedFrom":[subQ1,subQ0]});Q1458=makeQuery(id+"F0.imprint","IMPRINT",FACE,{"disambiguationData":[TD([[makeQuery(id+"F0.imprint","IMPRINT",EDGE,{"disambiguationData":[TD([[subQ2,1.0]])],"derivedFrom":subQ1}),-1.0]])]});}
            var Q1459;
            {var subQ3=sQuery(id+"F0.wireOp",EDGE,"E3.12.0.85");Q1459=makeQuery(id+"F0.imprint","IMPRINT",FACE,{"disambiguationData":[TD([[makeQuery(id+"F0.imprint","IMPRINT",EDGE,{"derivedFrom":subQ3}),1.0]])]});}
            var Q1460;
            {var subQ0=sQuery(id+"F0.wireOp",EDGE,"E3.9.0.89");Q1460=makeQuery(id+"F0.imprint","IMPRINT",FACE,{"disambiguationData":[TD([[makeQuery(id+"F0.imprint","IMPRINT",EDGE,{"derivedFrom":subQ0}),-1.0]])]});}
            var Q1461;
            {var subQ3=sQuery(id+"F0.wireOp",EDGE,"E3.10.0.53");Q1461=makeQuery(id+"F0.imprint","IMPRINT",FACE,{"disambiguationData":[TD([[makeQuery(id+"F0.imprint","IMPRINT",EDGE,{"derivedFrom":subQ3}),1.0]])]});}
            var Q1462;
            {var subQ0=sQuery(id+"F0.wireOp",EDGE,"E3.12.0.94");var subQ1=sQuery(id+"F0.wireOp",EDGE,"E3.12.0.42");var subQ2=makeQuery(id+"F0.imprint","INTERSECT",VERTEX,{"derivedFrom":[subQ1,subQ0]});Q1462=makeQuery(id+"F0.imprint","IMPRINT",FACE,{"disambiguationData":[TD([[makeQuery(id+"F0.imprint","IMPRINT",EDGE,{"disambiguationData":[TD([[subQ2,1.0]])],"derivedFrom":subQ1}),-1.0]])]});}
            var Q1463;
            {var subQ0=sQuery(id+"F0.wireOp",EDGE,"E3.5.0.97");var subQ1=sQuery(id+"F0.wireOp",EDGE,"E3.5.0.40");var subQ2=makeQuery(id+"F0.imprint","INTERSECT",VERTEX,{"derivedFrom":[subQ1,subQ0]});Q1463=makeQuery(id+"F0.imprint","IMPRINT",FACE,{"disambiguationData":[TD([[makeQuery(id+"F0.imprint","IMPRINT",EDGE,{"disambiguationData":[TD([[subQ2,1.0]])],"derivedFrom":subQ1}),-1.0]])]});}
            var Q1464;
            {var subQ3=sQuery(id+"F0.wireOp",EDGE,"E3.23.0.86");Q1464=makeQuery(id+"F0.imprint","IMPRINT",FACE,{"disambiguationData":[TD([[makeQuery(id+"F0.imprint","IMPRINT",EDGE,{"derivedFrom":subQ3}),1.0]])]});}
            var Q1465;
            {var subQ0=sQuery(id+"F0.wireOp",EDGE,"E3.21.0.41");var subQ1=sQuery(id+"F0.wireOp",EDGE,"E3.21.0.6");var subQ2=makeQuery(id+"F0.imprint","INTERSECT",VERTEX,{"derivedFrom":[subQ1,subQ0]});Q1465=makeQuery(id+"F0.imprint","IMPRINT",FACE,{"disambiguationData":[TD([[makeQuery(id+"F0.imprint","IMPRINT",EDGE,{"disambiguationData":[TD([[subQ2,1.0]])],"derivedFrom":subQ1}),-1.0]])]});}
            var Q1466;
            {var subQ0=sQuery(id+"F0.wireOp",EDGE,"E3.21.0.37");var subQ5=sQuery(id+"F0.wireOp",EDGE,"E3.21.0.9");var subQ7=makeQuery(id+"F0.imprint","INTERSECT",VERTEX,{"derivedFrom":[subQ5,subQ0]});Q1466=makeQuery(id+"F0.imprint","IMPRINT",FACE,{"disambiguationData":[TD([[makeQuery(id+"F0.imprint","IMPRINT",EDGE,{"disambiguationData":[TD([[subQ7,1.0]])],"derivedFrom":subQ5}),1.0]])]});}
            var Q1467;
            {var subQ3=sQuery(id+"F0.wireOp",EDGE,"E3.21.0.81");Q1467=makeQuery(id+"F0.imprint","IMPRINT",FACE,{"disambiguationData":[TD([[makeQuery(id+"F0.imprint","IMPRINT",EDGE,{"derivedFrom":subQ3}),1.0]])]});}
            var Q1468;
            {var subQ0=sQuery(id+"F0.wireOp",EDGE,"E3.23.0.99");var subQ1=sQuery(id+"F0.wireOp",EDGE,"E3.23.0.49");var subQ2=makeQuery(id+"F0.imprint","INTERSECT",VERTEX,{"derivedFrom":[subQ1,subQ0]});Q1468=makeQuery(id+"F0.imprint","IMPRINT",FACE,{"disambiguationData":[TD([[makeQuery(id+"F0.imprint","IMPRINT",EDGE,{"disambiguationData":[TD([[subQ2,1.0]])],"derivedFrom":subQ1}),-1.0]])]});}
            var Q1469;
            {var subQ0=sQuery(id+"F0.wireOp",EDGE,"E3.18.0.20");Q1469=makeQuery(id+"F0.imprint","IMPRINT",FACE,{"disambiguationData":[TD([[makeQuery(id+"F0.imprint","IMPRINT",EDGE,{"derivedFrom":subQ0}),-1.0]])]});}
            var Q1470;
            {var subQ3=sQuery(id+"F0.wireOp",EDGE,"E3.17.0.83");Q1470=makeQuery(id+"F0.imprint","IMPRINT",FACE,{"disambiguationData":[TD([[makeQuery(id+"F0.imprint","IMPRINT",EDGE,{"derivedFrom":subQ3}),1.0]])]});}
            var Q1471;
            {var subQ3=sQuery(id+"F0.wireOp",EDGE,"E3.19.0.82");Q1471=makeQuery(id+"F0.imprint","IMPRINT",FACE,{"disambiguationData":[TD([[makeQuery(id+"F0.imprint","IMPRINT",EDGE,{"derivedFrom":subQ3}),1.0]])]});}
            var Q1472;
            {var subQ3=sQuery(id+"F0.wireOp",EDGE,"E3.19.0.103");Q1472=makeQuery(id+"F0.imprint","IMPRINT",FACE,{"disambiguationData":[TD([[makeQuery(id+"F0.imprint","IMPRINT",EDGE,{"derivedFrom":subQ3}),1.0]])]});}
            var Q1473;
            {var subQ0=sQuery(id+"F0.wireOp",EDGE,"E3.17.0.20");Q1473=makeQuery(id+"F0.imprint","IMPRINT",FACE,{"disambiguationData":[TD([[makeQuery(id+"F0.imprint","IMPRINT",EDGE,{"derivedFrom":subQ0}),-1.0]])]});}
            var Q1474;
            {var subQ5=sQuery(id+"F0.wireOp",EDGE,"E3.21.0.56");Q1474=makeQuery(id+"F0.imprint","IMPRINT",FACE,{"disambiguationData":[TD([[makeQuery(id+"F0.imprint","IMPRINT",EDGE,{"derivedFrom":subQ5}),1.0]])]});}
            extrude(context, id + "F1", {"entities" : qUnion([Q0, Q1, Q2, Q3, Q4, Q5, Q6, Q7, Q8, Q9, Q10, Q11, Q12, Q13, Q14, Q15, Q16, Q17, Q18, Q19, Q20, Q21, Q22, Q23, Q24, Q25, Q26, Q27, Q28, Q29, Q30, Q31, Q32, Q33, Q34, Q35, Q36, Q37, Q38, Q39, Q40, Q41, Q42, Q43, Q44, Q45, Q46, Q47, Q48, Q49, Q50, Q51, Q52, Q53, Q54, Q55, Q56, Q57, Q58, Q59, Q60, Q61, Q62, Q63, Q64, Q65, Q66, Q67, Q68, Q69, Q70, Q71, Q72, Q73, Q74, Q75, Q76, Q77, Q78, Q79, Q80, Q81, Q82, Q83, Q84, Q85, Q86, Q87, Q88, Q89, Q90, Q91, Q92, Q93, Q94, Q95, Q96, Q97, Q98, Q99, Q100, Q101, Q102, Q103, Q104, Q105, Q106, Q107, Q108, Q109, Q110, Q111, Q112, Q113, Q114, Q115, Q116, Q117, Q118, Q119, Q120, Q121, Q122, Q123, Q124, Q125, Q126, Q127, Q128, Q129, Q130, Q131, Q132, Q133, Q134, Q135, Q136, Q137, Q138, Q139, Q140, Q141, Q142, Q143, Q144, Q145, Q146, Q147, Q148, Q149, Q150, Q151, Q152, Q153, Q154, Q155, Q156, Q157, Q158, Q159, Q160, Q161, Q162, Q163, Q164, Q165, Q166, Q167, Q168, Q169, Q170, Q171, Q172, Q173, Q174, Q175, Q176, Q177, Q178, Q179, Q180, Q181, Q182, Q183, Q184, Q185, Q186, Q187, Q188, Q189, Q190, Q191, Q192, Q193, Q194, Q195, Q196, Q197, Q198, Q199, Q200, Q201, Q202, Q203, Q204, Q205, Q206, Q207, Q208, Q209, Q210, Q211, Q212, Q213, Q214, Q215, Q216, Q217, Q218, Q219, Q220, Q221, Q222, Q223, Q224, Q225, Q226, Q227, Q228, Q229, Q230, Q231, Q232, Q233, Q234, Q235, Q236, Q237, Q238, Q239, Q240, Q241, Q242, Q243, Q244, Q245, Q246, Q247, Q248, Q249, Q250, Q251, Q252, Q253, Q254, Q255, Q256, Q257, Q258, Q259, Q260, Q261, Q262, Q263, Q264, Q265, Q266, Q267, Q268, Q269, Q270, Q271, Q272, Q273, Q274, Q275, Q276, Q277, Q278, Q279, Q280, Q281, Q282, Q283, Q284, Q285, Q286, Q287, Q288, Q289, Q290, Q291, Q292, Q293, Q294, Q295, Q296, Q297, Q298, Q299, Q300, Q301, Q302, Q303, Q304, Q305, Q306, Q307, Q308, Q309, Q310, Q311, Q312, Q313, Q314, Q315, Q316, Q317, Q318, Q319, Q320, Q321, Q322, Q323, Q324, Q325, Q326, Q327, Q328, Q329, Q330, Q331, Q332, Q333, Q334, Q335, Q336, Q337, Q338, Q339, Q340, Q341, Q342, Q343, Q344, Q345, Q346, Q347, Q348, Q349, Q350, Q351, Q352, Q353, Q354, Q355, Q356, Q357, Q358, Q359, Q360, Q361, Q362, Q363, Q364, Q365, Q366, Q367, Q368, Q369, Q370, Q371, Q372, Q373, Q374, Q375, Q376, Q377, Q378, Q379, Q380, Q381, Q382, Q383, Q384, Q385, Q386, Q387, Q388, Q389, Q390, Q391, Q392, Q393, Q394, Q395, Q396, Q397, Q398, Q399, Q400, Q401, Q402, Q403, Q404, Q405, Q406, Q407, Q408, Q409, Q410, Q411, Q412, Q413, Q414, Q415, Q416, Q417, Q418, Q419, Q420, Q421, Q422, Q423, Q424, Q425, Q426, Q427, Q428, Q429, Q430, Q431, Q432, Q433, Q434, Q435, Q436, Q437, Q438, Q439, Q440, Q441, Q442, Q443, Q444, Q445, Q446, Q447, Q448, Q449, Q450, Q451, Q452, Q453, Q454, Q455, Q456, Q457, Q458, Q459, Q460, Q461, Q462, Q463, Q464, Q465, Q466, Q467, Q468, Q469, Q470, Q471, Q472, Q473, Q474, Q475, Q476, Q477, Q478, Q479, Q480, Q481, Q482, Q483, Q484, Q485, Q486, Q487, Q488, Q489, Q490, Q491, Q492, Q493, Q494, Q495, Q496, Q497, Q498, Q499, Q500, Q501, Q502, Q503, Q504, Q505, Q506, Q507, Q508, Q509, Q510, Q511, Q512, Q513, Q514, Q515, Q516, Q517, Q518, Q519, Q520, Q521, Q522, Q523, Q524, Q525, Q526, Q527, Q528, Q529, Q530, Q531, Q532, Q533, Q534, Q535, Q536, Q537, Q538, Q539, Q540, Q541, Q542, Q543, Q544, Q545, Q546, Q547, Q548, Q549, Q550, Q551, Q552, Q553, Q554, Q555, Q556, Q557, Q558, Q559, Q560, Q561, Q562, Q563, Q564, Q565, Q566, Q567, Q568, Q569, Q570, Q571, Q572, Q573, Q574, Q575, Q576, Q577, Q578, Q579, Q580, Q581, Q582, Q583, Q584, Q585, Q586, Q587, Q588, Q589, Q590, Q591, Q592, Q593, Q594, Q595, Q596, Q597, Q598, Q599, Q600, Q601, Q602, Q603, Q604, Q605, Q606, Q607, Q608, Q609, Q610, Q611, Q612, Q613, Q614, Q615, Q616, Q617, Q618, Q619, Q620, Q621, Q622, Q623, Q624, Q625, Q626, Q627, Q628, Q629, Q630, Q631, Q632, Q633, Q634, Q635, Q636, Q637, Q638, Q639, Q640, Q641, Q642, Q643, Q644, Q645, Q646, Q647, Q648, Q649, Q650, Q651, Q652, Q653, Q654, Q655, Q656, Q657, Q658, Q659, Q660, Q661, Q662, Q663, Q664, Q665, Q666, Q667, Q668, Q669, Q670, Q671, Q672, Q673, Q674, Q675, Q676, Q677, Q678, Q679, Q680, Q681, Q682, Q683, Q684, Q685, Q686, Q687, Q688, Q689, Q690, Q691, Q692, Q693, Q694, Q695, Q696, Q697, Q698, Q699, Q700, Q701, Q702, Q703, Q704, Q705, Q706, Q707, Q708, Q709, Q710, Q711, Q712, Q713, Q714, Q715, Q716, Q717, Q718, Q719, Q720, Q721, Q722, Q723, Q724, Q725, Q726, Q727, Q728, Q729, Q730, Q731, Q732, Q733, Q734, Q735, Q736, Q737, Q738, Q739, Q740, Q741, Q742, Q743, Q744, Q745, Q746, Q747, Q748, Q749, Q750, Q751, Q752, Q753, Q754, Q755, Q756, Q757, Q758, Q759, Q760, Q761, Q762, Q763, Q764, Q765, Q766, Q767, Q768, Q769, Q770, Q771, Q772, Q773, Q774, Q775, Q776, Q777, Q778, Q779, Q780, Q781, Q782, Q783, Q784, Q785, Q786, Q787, Q788, Q789, Q790, Q791, Q792, Q793, Q794, Q795, Q796, Q797, Q798, Q799, Q800, Q801, Q802, Q803, Q804, Q805, Q806, Q807, Q808, Q809, Q810, Q811, Q812, Q813, Q814, Q815, Q816, Q817, Q818, Q819, Q820, Q821, Q822, Q823, Q824, Q825, Q826, Q827, Q828, Q829, Q830, Q831, Q832, Q833, Q834, Q835, Q836, Q837, Q838, Q839, Q840, Q841, Q842, Q843, Q844, Q845, Q846, Q847, Q848, Q849, Q850, Q851, Q852, Q853, Q854, Q855, Q856, Q857, Q858, Q859, Q860, Q861, Q862, Q863, Q864, Q865, Q866, Q867, Q868, Q869, Q870, Q871, Q872, Q873, Q874, Q875, Q876, Q877, Q878, Q879, Q880, Q881, Q882, Q883, Q884, Q885, Q886, Q887, Q888, Q889, Q890, Q891, Q892, Q893, Q894, Q895, Q896, Q897, Q898, Q899, Q900, Q901, Q902, Q903, Q904, Q905, Q906, Q907, Q908, Q909, Q910, Q911, Q912, Q913, Q914, Q915, Q916, Q917, Q918, Q919, Q920, Q921, Q922, Q923, Q924, Q925, Q926, Q927, Q928, Q929, Q930, Q931, Q932, Q933, Q934, Q935, Q936, Q937, Q938, Q939, Q940, Q941, Q942, Q943, Q944, Q945, Q946, Q947, Q948, Q949, Q950, Q951, Q952, Q953, Q954, Q955, Q956, Q957, Q958, Q959, Q960, Q961, Q962, Q963, Q964, Q965, Q966, Q967, Q968, Q969, Q970, Q971, Q972, Q973, Q974, Q975, Q976, Q977, Q978, Q979, Q980, Q981, Q982, Q983, Q984, Q985, Q986, Q987, Q988, Q989, Q990, Q991, Q992, Q993, Q994, Q995, Q996, Q997, Q998, Q999, Q1000, Q1001, Q1002, Q1003, Q1004, Q1005, Q1006, Q1007, Q1008, Q1009, Q1010, Q1011, Q1012, Q1013, Q1014, Q1015, Q1016, Q1017, Q1018, Q1019, Q1020, Q1021, Q1022, Q1023, Q1024, Q1025, Q1026, Q1027, Q1028, Q1029, Q1030, Q1031, Q1032, Q1033, Q1034, Q1035, Q1036, Q1037, Q1038, Q1039, Q1040, Q1041, Q1042, Q1043, Q1044, Q1045, Q1046, Q1047, Q1048, Q1049, Q1050, Q1051, Q1052, Q1053, Q1054, Q1055, Q1056, Q1057, Q1058, Q1059, Q1060, Q1061, Q1062, Q1063, Q1064, Q1065, Q1066, Q1067, Q1068, Q1069, Q1070, Q1071, Q1072, Q1073, Q1074, Q1075, Q1076, Q1077, Q1078, Q1079, Q1080, Q1081, Q1082, Q1083, Q1084, Q1085, Q1086, Q1087, Q1088, Q1089, Q1090, Q1091, Q1092, Q1093, Q1094, Q1095, Q1096, Q1097, Q1098, Q1099, Q1100, Q1101, Q1102, Q1103, Q1104, Q1105, Q1106, Q1107, Q1108, Q1109, Q1110, Q1111, Q1112, Q1113, Q1114, Q1115, Q1116, Q1117, Q1118, Q1119, Q1120, Q1121, Q1122, Q1123, Q1124, Q1125, Q1126, Q1127, Q1128, Q1129, Q1130, Q1131, Q1132, Q1133, Q1134, Q1135, Q1136, Q1137, Q1138, Q1139, Q1140, Q1141, Q1142, Q1143, Q1144, Q1145, Q1146, Q1147, Q1148, Q1149, Q1150, Q1151, Q1152, Q1153, Q1154, Q1155, Q1156, Q1157, Q1158, Q1159, Q1160, Q1161, Q1162, Q1163, Q1164, Q1165, Q1166, Q1167, Q1168, Q1169, Q1170, Q1171, Q1172, Q1173, Q1174, Q1175, Q1176, Q1177, Q1178, Q1179, Q1180, Q1181, Q1182, Q1183, Q1184, Q1185, Q1186, Q1187, Q1188, Q1189, Q1190, Q1191, Q1192, Q1193, Q1194, Q1195, Q1196, Q1197, Q1198, Q1199, Q1200, Q1201, Q1202, Q1203, Q1204, Q1205, Q1206, Q1207, Q1208, Q1209, Q1210, Q1211, Q1212, Q1213, Q1214, Q1215, Q1216, Q1217, Q1218, Q1219, Q1220, Q1221, Q1222, Q1223, Q1224, Q1225, Q1226, Q1227, Q1228, Q1229, Q1230, Q1231, Q1232, Q1233, Q1234, Q1235, Q1236, Q1237, Q1238, Q1239, Q1240, Q1241, Q1242, Q1243, Q1244, Q1245, Q1246, Q1247, Q1248, Q1249, Q1250, Q1251, Q1252, Q1253, Q1254, Q1255, Q1256, Q1257, Q1258, Q1259, Q1260, Q1261, Q1262, Q1263, Q1264, Q1265, Q1266, Q1267, Q1268, Q1269, Q1270, Q1271, Q1272, Q1273, Q1274, Q1275, Q1276, Q1277, Q1278, Q1279, Q1280, Q1281, Q1282, Q1283, Q1284, Q1285, Q1286, Q1287, Q1288, Q1289, Q1290, Q1291, Q1292, Q1293, Q1294, Q1295, Q1296, Q1297, Q1298, Q1299, Q1300, Q1301, Q1302, Q1303, Q1304, Q1305, Q1306, Q1307, Q1308, Q1309, Q1310, Q1311, Q1312, Q1313, Q1314, Q1315, Q1316, Q1317, Q1318, Q1319, Q1320, Q1321, Q1322, Q1323, Q1324, Q1325, Q1326, Q1327, Q1328, Q1329, Q1330, Q1331, Q1332, Q1333, Q1334, Q1335, Q1336, Q1337, Q1338, Q1339, Q1340, Q1341, Q1342, Q1343, Q1344, Q1345, Q1346, Q1347, Q1348, Q1349, Q1350, Q1351, Q1352, Q1353, Q1354, Q1355, Q1356, Q1357, Q1358, Q1359, Q1360, Q1361, Q1362, Q1363, Q1364, Q1365, Q1366, Q1367, Q1368, Q1369, Q1370, Q1371, Q1372, Q1373, Q1374, Q1375, Q1376, Q1377, Q1378, Q1379, Q1380, Q1381, Q1382, Q1383, Q1384, Q1385, Q1386, Q1387, Q1388, Q1389, Q1390, Q1391, Q1392, Q1393, Q1394, Q1395, Q1396, Q1397, Q1398, Q1399, Q1400, Q1401, Q1402, Q1403, Q1404, Q1405, Q1406, Q1407, Q1408, Q1409, Q1410, Q1411, Q1412, Q1413, Q1414, Q1415, Q1416, Q1417, Q1418, Q1419, Q1420, Q1421, Q1422, Q1423, Q1424, Q1425, Q1426, Q1427, Q1428, Q1429, Q1430, Q1431, Q1432, Q1433, Q1434, Q1435, Q1436, Q1437, Q1438, Q1439, Q1440, Q1441, Q1442, Q1443, Q1444, Q1445, Q1446, Q1447, Q1448, Q1449, Q1450, Q1451, Q1452, Q1453, Q1454, Q1455, Q1456, Q1457, Q1458, Q1459, Q1460, Q1461, Q1462, Q1463, Q1464, Q1465, Q1466, Q1467, Q1468, Q1469, Q1470, Q1471, Q1472, Q1473, Q1474]), "depth" : 0.5 * mm, "offsetDistance" : 25 * mm});
        }
    });
